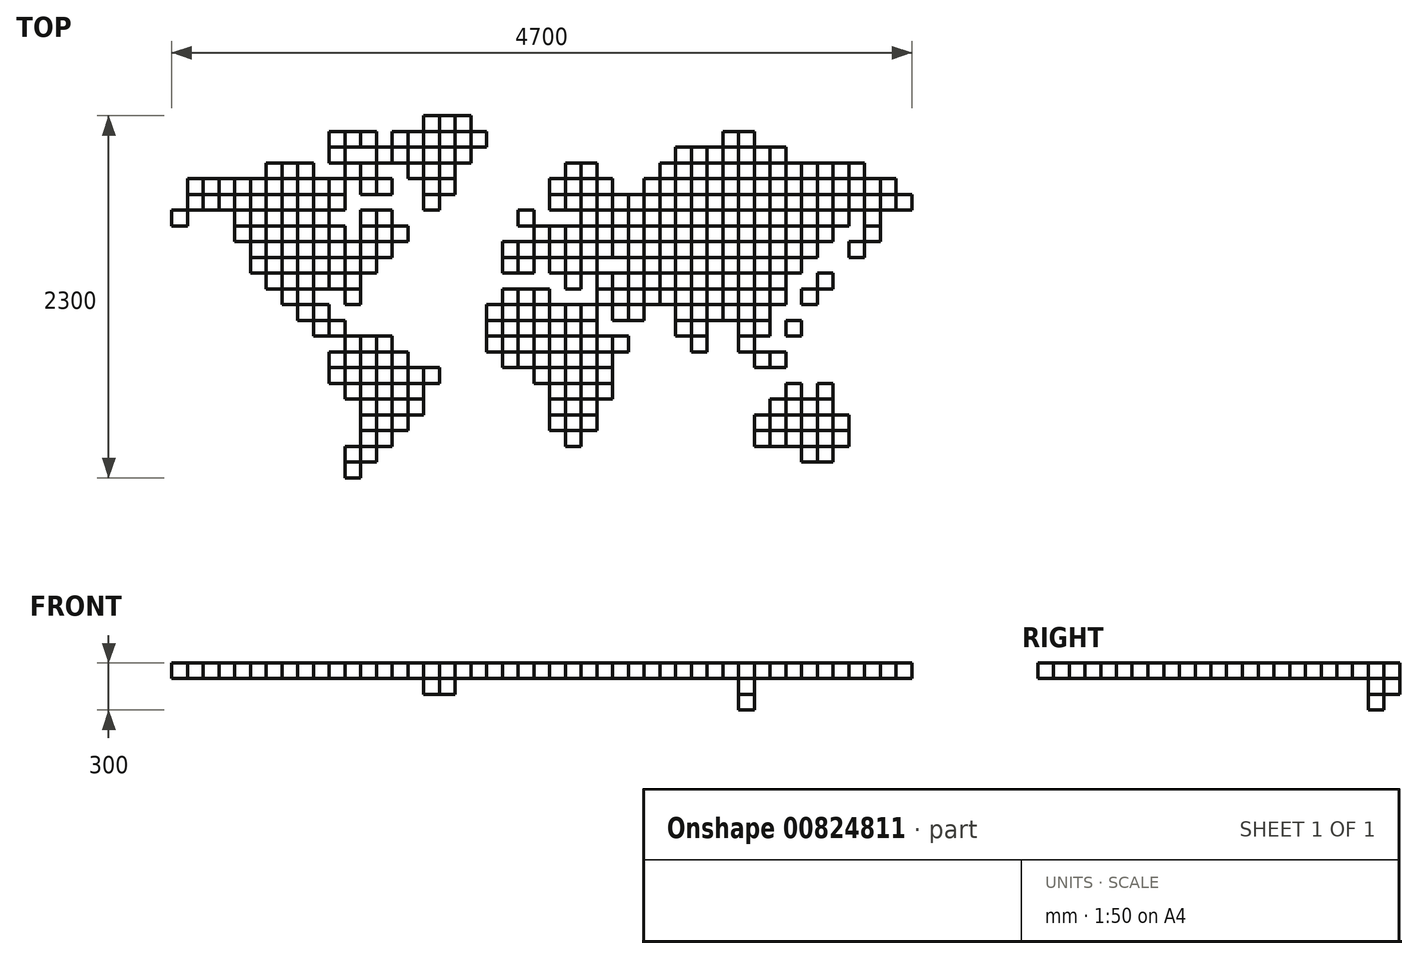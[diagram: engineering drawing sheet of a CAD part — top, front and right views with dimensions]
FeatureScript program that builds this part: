
annotation { "Feature Type Name" : "Feature", "Feature Type Description" : "" }
export const myFeature = defineFeature(function(context is Context, id is Id, definition is map)
    precondition{}
    {
        {
            var Q0;
            Q0=qCreatedBy(makeId("Top.planeOp"),FACE);
            var sketch = newSketch(context, id + "F0", { "sketchPlane" : qUnion([Q0])});
            skLineSegment(sketch, "E0.bottom", {"start": v(-5, 5) * mm, "end": v(5, 5) * mm});
            skLineSegment(sketch, "E0.top", {"start": v(-5, -5) * mm, "end": v(5, -5) * mm});
            skLineSegment(sketch, "E0.left", {"start": v(-5, 5) * mm, "end": v(-5, -5) * mm});
            skLineSegment(sketch, "E0.right", {"start": v(5, 5) * mm, "end": v(5, -5) * mm});
            skLineSegment(sketch, "E1", {"start": v(0, 0) * mm, "end": v(0, 5) * mm, "construction": true});
            skLineSegment(sketch, "E2", {"start": v(0, 0) * mm, "end": v(5, 0) * mm, "construction": true});
            skSolve(sketch);
        }
        {
            var Q0;
            Q0 = qSketchRegion(id + "F0", true);
            extrude(context, id + "F1", {"entities" : qUnion([Q0]), "depth" : 10 * mm, "offsetDistance" : 25 * mm});
        }
        {
            var Q0;
            Q0=makeQuery(id+"F1.opExtrude","SWEPT_BODY",BODY,{"disambiguationData":[OSD([sQuery(id+"F0.wireOp",EDGE,"E0.bottom"),sQuery(id+"F0.wireOp",EDGE,"E0.top"),sQuery(id+"F0.wireOp",EDGE,"E0.left"),sQuery(id+"F0.wireOp",EDGE,"E0.right")])]});
            var Q1;
            Q1=makeQuery(id+"F1.opExtrude","CAP_EDGE",EDGE,{"disambiguationData":[OSD([sQuery(id+"F0.wireOp",EDGE,"E0.bottom")])],"isStart":false});
            transform(context, id + "F2", {"entities" : qUnion([Q0]), "transformType" : TransformType.TRANSLATION_DISTANCE, "transformDirection" : qUnion([Q1]), "distance" : 10 * mm, "makeCopy" : true});
        }
        {
            var Q0;
            Q0=makeQuery(id+"F1.opExtrude","SWEPT_BODY",BODY,{"disambiguationData":[OSD([sQuery(id+"F0.wireOp",EDGE,"E0.bottom"),sQuery(id+"F0.wireOp",EDGE,"E0.top"),sQuery(id+"F0.wireOp",EDGE,"E0.left"),sQuery(id+"F0.wireOp",EDGE,"E0.right")])]});
            var Q1;
            Q1=makeQuery(id+"F2.opPattern","COPY",BODY,{"derivedFrom":makeQuery(id+"F1.opExtrude","SWEPT_BODY",BODY,{"disambiguationData":[OSD([sQuery(id+"F0.wireOp",EDGE,"E0.bottom"),sQuery(id+"F0.wireOp",EDGE,"E0.top"),sQuery(id+"F0.wireOp",EDGE,"E0.left"),sQuery(id+"F0.wireOp",EDGE,"E0.right")])]}),"instanceName":"1"});
            var Q2;
            Q2=makeQuery(id+"F2.opPattern","COPY",EDGE,{"derivedFrom":makeQuery(id+"F1.opExtrude","CAP_EDGE",EDGE,{"disambiguationData":[OSD([sQuery(id+"F0.wireOp",EDGE,"E0.right")])],"isStart":false}),"instanceName":"1"});
            transform(context, id + "F3", {"entities" : qUnion([Q0, Q1]), "transformType" : TransformType.TRANSLATION_DISTANCE, "transformDirection" : qUnion([Q2]), "distance" : 10 * mm, "makeCopy" : true});
        }
        {
            var Q0;
            Q0=makeQuery(id+"F1.opExtrude","SWEPT_BODY",BODY,{"disambiguationData":[OSD([sQuery(id+"F0.wireOp",EDGE,"E0.bottom"),sQuery(id+"F0.wireOp",EDGE,"E0.top"),sQuery(id+"F0.wireOp",EDGE,"E0.left"),sQuery(id+"F0.wireOp",EDGE,"E0.right")])]});
            var Q1;
            Q1=makeQuery(id+"F2.opPattern","COPY",BODY,{"derivedFrom":makeQuery(id+"F1.opExtrude","SWEPT_BODY",BODY,{"disambiguationData":[OSD([sQuery(id+"F0.wireOp",EDGE,"E0.bottom"),sQuery(id+"F0.wireOp",EDGE,"E0.top"),sQuery(id+"F0.wireOp",EDGE,"E0.left"),sQuery(id+"F0.wireOp",EDGE,"E0.right")])]}),"instanceName":"1"});
            var Q2;
            Q2=makeQuery(id+"F3.opPattern","COPY",EDGE,{"derivedFrom":makeQuery(id+"F2.opPattern","COPY",EDGE,{"derivedFrom":makeQuery(id+"F1.opExtrude","CAP_EDGE",EDGE,{"disambiguationData":[OSD([sQuery(id+"F0.wireOp",EDGE,"E0.bottom")])],"isStart":false}),"instanceName":"1"}),"instanceName":"1"});
            transform(context, id + "F4", {"entities" : qUnion([Q0, Q1]), "transformType" : TransformType.TRANSLATION_DISTANCE, "transformDirection" : qUnion([Q2]), "distance" : 20 * mm, "makeCopy" : true});
        }
        {
            var Q0;
            Q0=makeQuery(id+"F4.opPattern","COPY",BODY,{"derivedFrom":makeQuery(id+"F1.opExtrude","SWEPT_BODY",BODY,{"disambiguationData":[OSD([sQuery(id+"F0.wireOp",EDGE,"E0.bottom"),sQuery(id+"F0.wireOp",EDGE,"E0.top"),sQuery(id+"F0.wireOp",EDGE,"E0.left"),sQuery(id+"F0.wireOp",EDGE,"E0.right")])]}),"instanceName":"1"});
            var Q1;
            Q1=makeQuery(id+"F1.opExtrude","SWEPT_BODY",BODY,{"disambiguationData":[OSD([sQuery(id+"F0.wireOp",EDGE,"E0.bottom"),sQuery(id+"F0.wireOp",EDGE,"E0.top"),sQuery(id+"F0.wireOp",EDGE,"E0.left"),sQuery(id+"F0.wireOp",EDGE,"E0.right")])]});
            var Q2;
            Q2=makeQuery(id+"F2.opPattern","COPY",BODY,{"derivedFrom":makeQuery(id+"F1.opExtrude","SWEPT_BODY",BODY,{"disambiguationData":[OSD([sQuery(id+"F0.wireOp",EDGE,"E0.bottom"),sQuery(id+"F0.wireOp",EDGE,"E0.top"),sQuery(id+"F0.wireOp",EDGE,"E0.left"),sQuery(id+"F0.wireOp",EDGE,"E0.right")])]}),"instanceName":"1"});
            var Q3;
            Q3=makeQuery(id+"F4.opPattern","COPY",BODY,{"derivedFrom":makeQuery(id+"F2.opPattern","COPY",BODY,{"derivedFrom":makeQuery(id+"F1.opExtrude","SWEPT_BODY",BODY,{"disambiguationData":[OSD([sQuery(id+"F0.wireOp",EDGE,"E0.bottom"),sQuery(id+"F0.wireOp",EDGE,"E0.top"),sQuery(id+"F0.wireOp",EDGE,"E0.left"),sQuery(id+"F0.wireOp",EDGE,"E0.right")])]}),"instanceName":"1"}),"instanceName":"1"});
            var Q4;
            Q4=makeQuery(id+"F4.opPattern","COPY",EDGE,{"derivedFrom":makeQuery(id+"F2.opPattern","COPY",EDGE,{"derivedFrom":makeQuery(id+"F1.opExtrude","CAP_EDGE",EDGE,{"disambiguationData":[OSD([sQuery(id+"F0.wireOp",EDGE,"E0.top")])],"isStart":false}),"instanceName":"1"}),"instanceName":"1"});
            transform(context, id + "F5", {"entities" : qUnion([Q0, Q1, Q2, Q3]), "transformType" : TransformType.TRANSLATION_DISTANCE, "transformDirection" : qUnion([Q4]), "distance" : 40 * mm, "makeCopy" : true});
        }
        {
            var Q0;
            Q0=makeQuery(id+"F4.opPattern","COPY",BODY,{"derivedFrom":makeQuery(id+"F1.opExtrude","SWEPT_BODY",BODY,{"disambiguationData":[OSD([sQuery(id+"F0.wireOp",EDGE,"E0.bottom"),sQuery(id+"F0.wireOp",EDGE,"E0.top"),sQuery(id+"F0.wireOp",EDGE,"E0.left"),sQuery(id+"F0.wireOp",EDGE,"E0.right")])]}),"instanceName":"1"});
            var Q1;
            Q1=makeQuery(id+"F5.opPattern","COPY",BODY,{"derivedFrom":makeQuery(id+"F1.opExtrude","SWEPT_BODY",BODY,{"disambiguationData":[OSD([sQuery(id+"F0.wireOp",EDGE,"E0.bottom"),sQuery(id+"F0.wireOp",EDGE,"E0.top"),sQuery(id+"F0.wireOp",EDGE,"E0.left"),sQuery(id+"F0.wireOp",EDGE,"E0.right")])]}),"instanceName":"1"});
            var Q2;
            Q2=makeQuery(id+"F4.opPattern","COPY",BODY,{"derivedFrom":makeQuery(id+"F2.opPattern","COPY",BODY,{"derivedFrom":makeQuery(id+"F1.opExtrude","SWEPT_BODY",BODY,{"disambiguationData":[OSD([sQuery(id+"F0.wireOp",EDGE,"E0.bottom"),sQuery(id+"F0.wireOp",EDGE,"E0.top"),sQuery(id+"F0.wireOp",EDGE,"E0.left"),sQuery(id+"F0.wireOp",EDGE,"E0.right")])]}),"instanceName":"1"}),"instanceName":"1"});
            var Q3;
            Q3=makeQuery(id+"F5.opPattern","COPY",BODY,{"derivedFrom":makeQuery(id+"F2.opPattern","COPY",BODY,{"derivedFrom":makeQuery(id+"F1.opExtrude","SWEPT_BODY",BODY,{"disambiguationData":[OSD([sQuery(id+"F0.wireOp",EDGE,"E0.bottom"),sQuery(id+"F0.wireOp",EDGE,"E0.top"),sQuery(id+"F0.wireOp",EDGE,"E0.left"),sQuery(id+"F0.wireOp",EDGE,"E0.right")])]}),"instanceName":"1"}),"instanceName":"1"});
            var Q4;
            Q4=makeQuery(id+"F5.opPattern","COPY",BODY,{"derivedFrom":makeQuery(id+"F4.opPattern","COPY",BODY,{"derivedFrom":makeQuery(id+"F1.opExtrude","SWEPT_BODY",BODY,{"disambiguationData":[OSD([sQuery(id+"F0.wireOp",EDGE,"E0.bottom"),sQuery(id+"F0.wireOp",EDGE,"E0.top"),sQuery(id+"F0.wireOp",EDGE,"E0.left"),sQuery(id+"F0.wireOp",EDGE,"E0.right")])]}),"instanceName":"1"}),"instanceName":"1"});
            var Q5;
            Q5=makeQuery(id+"F5.opPattern","COPY",BODY,{"derivedFrom":makeQuery(id+"F4.opPattern","COPY",BODY,{"derivedFrom":makeQuery(id+"F2.opPattern","COPY",BODY,{"derivedFrom":makeQuery(id+"F1.opExtrude","SWEPT_BODY",BODY,{"disambiguationData":[OSD([sQuery(id+"F0.wireOp",EDGE,"E0.bottom"),sQuery(id+"F0.wireOp",EDGE,"E0.top"),sQuery(id+"F0.wireOp",EDGE,"E0.left"),sQuery(id+"F0.wireOp",EDGE,"E0.right")])]}),"instanceName":"1"}),"instanceName":"1"}),"instanceName":"1"});
            var Q6;
            Q6=makeQuery(id+"F5.opPattern","COPY",EDGE,{"derivedFrom":makeQuery(id+"F4.opPattern","COPY",EDGE,{"derivedFrom":makeQuery(id+"F2.opPattern","COPY",EDGE,{"derivedFrom":makeQuery(id+"F1.opExtrude","CAP_EDGE",EDGE,{"disambiguationData":[OSD([sQuery(id+"F0.wireOp",EDGE,"E0.right")])],"isStart":false}),"instanceName":"1"}),"instanceName":"1"}),"instanceName":"1"});
            transform(context, id + "F6", {"entities" : qUnion([Q0, Q1, Q2, Q3, Q4, Q5]), "transformType" : TransformType.TRANSLATION_DISTANCE, "transformDirection" : qUnion([Q6]), "distance" : 10 * mm, "oppositeDirection" : true, "makeCopy" : true});
        }
        {
            var Q0;
            Q0=makeQuery(id+"F4.opPattern","COPY",BODY,{"derivedFrom":makeQuery(id+"F2.opPattern","COPY",BODY,{"derivedFrom":makeQuery(id+"F1.opExtrude","SWEPT_BODY",BODY,{"disambiguationData":[OSD([sQuery(id+"F0.wireOp",EDGE,"E0.bottom"),sQuery(id+"F0.wireOp",EDGE,"E0.top"),sQuery(id+"F0.wireOp",EDGE,"E0.left"),sQuery(id+"F0.wireOp",EDGE,"E0.right")])]}),"instanceName":"1"}),"instanceName":"1"});
            var Q1;
            Q1=makeQuery(id+"F5.opPattern","COPY",BODY,{"derivedFrom":makeQuery(id+"F2.opPattern","COPY",BODY,{"derivedFrom":makeQuery(id+"F1.opExtrude","SWEPT_BODY",BODY,{"disambiguationData":[OSD([sQuery(id+"F0.wireOp",EDGE,"E0.bottom"),sQuery(id+"F0.wireOp",EDGE,"E0.top"),sQuery(id+"F0.wireOp",EDGE,"E0.left"),sQuery(id+"F0.wireOp",EDGE,"E0.right")])]}),"instanceName":"1"}),"instanceName":"1"});
            var Q2;
            Q2=makeQuery(id+"F5.opPattern","COPY",EDGE,{"derivedFrom":makeQuery(id+"F4.opPattern","COPY",EDGE,{"derivedFrom":makeQuery(id+"F2.opPattern","COPY",EDGE,{"derivedFrom":makeQuery(id+"F1.opExtrude","CAP_EDGE",EDGE,{"disambiguationData":[OSD([sQuery(id+"F0.wireOp",EDGE,"E0.right")])],"isStart":false}),"instanceName":"1"}),"instanceName":"1"}),"instanceName":"1"});
            transform(context, id + "F7", {"entities" : qUnion([Q0, Q1]), "transformType" : TransformType.TRANSLATION_DISTANCE, "transformDirection" : qUnion([Q2]), "distance" : 10 * mm, "makeCopy" : true});
        }
        {
            var Q0;
            Q0=makeQuery(id+"F5.opPattern","COPY",BODY,{"derivedFrom":makeQuery(id+"F1.opExtrude","SWEPT_BODY",BODY,{"disambiguationData":[OSD([sQuery(id+"F0.wireOp",EDGE,"E0.bottom"),sQuery(id+"F0.wireOp",EDGE,"E0.top"),sQuery(id+"F0.wireOp",EDGE,"E0.left"),sQuery(id+"F0.wireOp",EDGE,"E0.right")])]}),"instanceName":"1"});
            var Q1;
            Q1=makeQuery(id+"F5.opPattern","COPY",BODY,{"derivedFrom":makeQuery(id+"F4.opPattern","COPY",BODY,{"derivedFrom":makeQuery(id+"F1.opExtrude","SWEPT_BODY",BODY,{"disambiguationData":[OSD([sQuery(id+"F0.wireOp",EDGE,"E0.bottom"),sQuery(id+"F0.wireOp",EDGE,"E0.top"),sQuery(id+"F0.wireOp",EDGE,"E0.left"),sQuery(id+"F0.wireOp",EDGE,"E0.right")])]}),"instanceName":"1"}),"instanceName":"1"});
            var Q2;
            Q2=makeQuery(id+"F5.opPattern","COPY",BODY,{"derivedFrom":makeQuery(id+"F4.opPattern","COPY",BODY,{"derivedFrom":makeQuery(id+"F2.opPattern","COPY",BODY,{"derivedFrom":makeQuery(id+"F1.opExtrude","SWEPT_BODY",BODY,{"disambiguationData":[OSD([sQuery(id+"F0.wireOp",EDGE,"E0.bottom"),sQuery(id+"F0.wireOp",EDGE,"E0.top"),sQuery(id+"F0.wireOp",EDGE,"E0.left"),sQuery(id+"F0.wireOp",EDGE,"E0.right")])]}),"instanceName":"1"}),"instanceName":"1"}),"instanceName":"1"});
            var Q3;
            Q3=makeQuery(id+"F5.opPattern","COPY",EDGE,{"derivedFrom":makeQuery(id+"F4.opPattern","COPY",EDGE,{"derivedFrom":makeQuery(id+"F2.opPattern","COPY",EDGE,{"derivedFrom":makeQuery(id+"F1.opExtrude","CAP_EDGE",EDGE,{"disambiguationData":[OSD([sQuery(id+"F0.wireOp",EDGE,"E0.right")])],"isStart":false}),"instanceName":"1"}),"instanceName":"1"}),"instanceName":"1"});
            transform(context, id + "F8", {"entities" : qUnion([Q0, Q1, Q2]), "transformType" : TransformType.TRANSLATION_DISTANCE, "transformDirection" : qUnion([Q3]), "distance" : 20 * mm, "makeCopy" : true});
        }
        {
            var Q0;
            Q0=makeQuery(id+"F6.opPattern","COPY",BODY,{"derivedFrom":makeQuery(id+"F4.opPattern","COPY",BODY,{"derivedFrom":makeQuery(id+"F1.opExtrude","SWEPT_BODY",BODY,{"disambiguationData":[OSD([sQuery(id+"F0.wireOp",EDGE,"E0.bottom"),sQuery(id+"F0.wireOp",EDGE,"E0.top"),sQuery(id+"F0.wireOp",EDGE,"E0.left"),sQuery(id+"F0.wireOp",EDGE,"E0.right")])]}),"instanceName":"1"}),"instanceName":"1"});
            var Q1;
            Q1=makeQuery(id+"F6.opPattern","COPY",EDGE,{"derivedFrom":makeQuery(id+"F4.opPattern","COPY",EDGE,{"derivedFrom":makeQuery(id+"F1.opExtrude","CAP_EDGE",EDGE,{"disambiguationData":[OSD([sQuery(id+"F0.wireOp",EDGE,"E0.left")])],"isStart":false}),"instanceName":"1"}),"instanceName":"1"});
            transform(context, id + "F9", {"entities" : qUnion([Q0]), "transformType" : TransformType.TRANSLATION_DISTANCE, "transformDirection" : qUnion([Q1]), "distance" : 10 * mm, "oppositeDirection" : true, "makeCopy" : true});
        }
        {
            var Q0;
            Q0=makeQuery(id+"F9.opPattern","COPY",BODY,{"derivedFrom":makeQuery(id+"F6.opPattern","COPY",BODY,{"derivedFrom":makeQuery(id+"F4.opPattern","COPY",BODY,{"derivedFrom":makeQuery(id+"F1.opExtrude","SWEPT_BODY",BODY,{"disambiguationData":[OSD([sQuery(id+"F0.wireOp",EDGE,"E0.bottom"),sQuery(id+"F0.wireOp",EDGE,"E0.top"),sQuery(id+"F0.wireOp",EDGE,"E0.left"),sQuery(id+"F0.wireOp",EDGE,"E0.right")])]}),"instanceName":"1"}),"instanceName":"1"}),"instanceName":"1"});
            var Q1;
            Q1=makeQuery(id+"F9.opPattern","COPY",EDGE,{"derivedFrom":makeQuery(id+"F6.opPattern","COPY",EDGE,{"derivedFrom":makeQuery(id+"F4.opPattern","COPY",EDGE,{"derivedFrom":makeQuery(id+"F1.opExtrude","CAP_EDGE",EDGE,{"disambiguationData":[OSD([sQuery(id+"F0.wireOp",EDGE,"E0.bottom")])],"isStart":false}),"instanceName":"1"}),"instanceName":"1"}),"instanceName":"1"});
            transform(context, id + "F10", {"entities" : qUnion([Q0]), "transformType" : TransformType.TRANSLATION_DISTANCE, "transformDirection" : qUnion([Q1]), "distance" : 10 * mm, "oppositeDirection" : true, "makeCopy" : false});
        }
        {
            var Q0;
            Q0=makeQuery(id+"F4.opPattern","COPY",BODY,{"derivedFrom":makeQuery(id+"F2.opPattern","COPY",BODY,{"derivedFrom":makeQuery(id+"F1.opExtrude","SWEPT_BODY",BODY,{"disambiguationData":[OSD([sQuery(id+"F0.wireOp",EDGE,"E0.bottom"),sQuery(id+"F0.wireOp",EDGE,"E0.top"),sQuery(id+"F0.wireOp",EDGE,"E0.left"),sQuery(id+"F0.wireOp",EDGE,"E0.right")])]}),"instanceName":"1"}),"instanceName":"1"});
            var Q1;
            Q1=makeQuery(id+"F5.opPattern","COPY",BODY,{"derivedFrom":makeQuery(id+"F1.opExtrude","SWEPT_BODY",BODY,{"disambiguationData":[OSD([sQuery(id+"F0.wireOp",EDGE,"E0.bottom"),sQuery(id+"F0.wireOp",EDGE,"E0.top"),sQuery(id+"F0.wireOp",EDGE,"E0.left"),sQuery(id+"F0.wireOp",EDGE,"E0.right")])]}),"instanceName":"1"});
            var Q2;
            Q2=makeQuery(id+"F6.opPattern","COPY",BODY,{"derivedFrom":makeQuery(id+"F4.opPattern","COPY",BODY,{"derivedFrom":makeQuery(id+"F2.opPattern","COPY",BODY,{"derivedFrom":makeQuery(id+"F1.opExtrude","SWEPT_BODY",BODY,{"disambiguationData":[OSD([sQuery(id+"F0.wireOp",EDGE,"E0.bottom"),sQuery(id+"F0.wireOp",EDGE,"E0.top"),sQuery(id+"F0.wireOp",EDGE,"E0.left"),sQuery(id+"F0.wireOp",EDGE,"E0.right")])]}),"instanceName":"1"}),"instanceName":"1"}),"instanceName":"1"});
            var Q3;
            Q3=makeQuery(id+"F6.opPattern","COPY",BODY,{"derivedFrom":makeQuery(id+"F5.opPattern","COPY",BODY,{"derivedFrom":makeQuery(id+"F1.opExtrude","SWEPT_BODY",BODY,{"disambiguationData":[OSD([sQuery(id+"F0.wireOp",EDGE,"E0.bottom"),sQuery(id+"F0.wireOp",EDGE,"E0.top"),sQuery(id+"F0.wireOp",EDGE,"E0.left"),sQuery(id+"F0.wireOp",EDGE,"E0.right")])]}),"instanceName":"1"}),"instanceName":"1"});
            var Q4;
            Q4=makeQuery(id+"F6.opPattern","COPY",EDGE,{"derivedFrom":makeQuery(id+"F4.opPattern","COPY",EDGE,{"derivedFrom":makeQuery(id+"F2.opPattern","COPY",EDGE,{"derivedFrom":makeQuery(id+"F1.opExtrude","CAP_EDGE",EDGE,{"disambiguationData":[OSD([sQuery(id+"F0.wireOp",EDGE,"E0.left")])],"isStart":false}),"instanceName":"1"}),"instanceName":"1"}),"instanceName":"1"});
            transform(context, id + "F11", {"entities" : qUnion([Q0, Q1, Q2, Q3]), "transformType" : TransformType.TRANSLATION_DISTANCE, "transformDirection" : qUnion([Q4]), "distance" : 30 * mm, "oppositeDirection" : true, "makeCopy" : true});
        }
        {
            var Q0;
            Q0=makeQuery(id+"F6.opPattern","COPY",BODY,{"derivedFrom":makeQuery(id+"F5.opPattern","COPY",BODY,{"derivedFrom":makeQuery(id+"F2.opPattern","COPY",BODY,{"derivedFrom":makeQuery(id+"F1.opExtrude","SWEPT_BODY",BODY,{"disambiguationData":[OSD([sQuery(id+"F0.wireOp",EDGE,"E0.bottom"),sQuery(id+"F0.wireOp",EDGE,"E0.top"),sQuery(id+"F0.wireOp",EDGE,"E0.left"),sQuery(id+"F0.wireOp",EDGE,"E0.right")])]}),"instanceName":"1"}),"instanceName":"1"}),"instanceName":"1"});
            var Q1;
            Q1=makeQuery(id+"F6.opPattern","COPY",BODY,{"derivedFrom":makeQuery(id+"F5.opPattern","COPY",BODY,{"derivedFrom":makeQuery(id+"F4.opPattern","COPY",BODY,{"derivedFrom":makeQuery(id+"F2.opPattern","COPY",BODY,{"derivedFrom":makeQuery(id+"F1.opExtrude","SWEPT_BODY",BODY,{"disambiguationData":[OSD([sQuery(id+"F0.wireOp",EDGE,"E0.bottom"),sQuery(id+"F0.wireOp",EDGE,"E0.top"),sQuery(id+"F0.wireOp",EDGE,"E0.left"),sQuery(id+"F0.wireOp",EDGE,"E0.right")])]}),"instanceName":"1"}),"instanceName":"1"}),"instanceName":"1"}),"instanceName":"1"});
            var Q2;
            Q2=makeQuery(id+"F6.opPattern","COPY",BODY,{"derivedFrom":makeQuery(id+"F5.opPattern","COPY",BODY,{"derivedFrom":makeQuery(id+"F4.opPattern","COPY",BODY,{"derivedFrom":makeQuery(id+"F1.opExtrude","SWEPT_BODY",BODY,{"disambiguationData":[OSD([sQuery(id+"F0.wireOp",EDGE,"E0.bottom"),sQuery(id+"F0.wireOp",EDGE,"E0.top"),sQuery(id+"F0.wireOp",EDGE,"E0.left"),sQuery(id+"F0.wireOp",EDGE,"E0.right")])]}),"instanceName":"1"}),"instanceName":"1"}),"instanceName":"1"});
            var Q3;
            Q3=makeQuery(id+"F6.opPattern","COPY",EDGE,{"derivedFrom":makeQuery(id+"F5.opPattern","COPY",EDGE,{"derivedFrom":makeQuery(id+"F4.opPattern","COPY",EDGE,{"derivedFrom":makeQuery(id+"F2.opPattern","COPY",EDGE,{"derivedFrom":makeQuery(id+"F1.opExtrude","CAP_EDGE",EDGE,{"disambiguationData":[OSD([sQuery(id+"F0.wireOp",EDGE,"E0.right")])],"isStart":false}),"instanceName":"1"}),"instanceName":"1"}),"instanceName":"1"}),"instanceName":"1"});
            transform(context, id + "F12", {"entities" : qUnion([Q0, Q1, Q2]), "transformType" : TransformType.TRANSLATION_DISTANCE, "transformDirection" : qUnion([Q3]), "distance" : 10 * mm, "oppositeDirection" : true, "makeCopy" : true});
        }
        {
            var Q0;
            Q0=makeQuery(id+"F6.opPattern","COPY",BODY,{"derivedFrom":makeQuery(id+"F5.opPattern","COPY",BODY,{"derivedFrom":makeQuery(id+"F2.opPattern","COPY",BODY,{"derivedFrom":makeQuery(id+"F1.opExtrude","SWEPT_BODY",BODY,{"disambiguationData":[OSD([sQuery(id+"F0.wireOp",EDGE,"E0.bottom"),sQuery(id+"F0.wireOp",EDGE,"E0.top"),sQuery(id+"F0.wireOp",EDGE,"E0.left"),sQuery(id+"F0.wireOp",EDGE,"E0.right")])]}),"instanceName":"1"}),"instanceName":"1"}),"instanceName":"1"});
            var Q1;
            Q1=makeQuery(id+"F5.opPattern","COPY",BODY,{"derivedFrom":makeQuery(id+"F4.opPattern","COPY",BODY,{"derivedFrom":makeQuery(id+"F1.opExtrude","SWEPT_BODY",BODY,{"disambiguationData":[OSD([sQuery(id+"F0.wireOp",EDGE,"E0.bottom"),sQuery(id+"F0.wireOp",EDGE,"E0.top"),sQuery(id+"F0.wireOp",EDGE,"E0.left"),sQuery(id+"F0.wireOp",EDGE,"E0.right")])]}),"instanceName":"1"}),"instanceName":"1"});
            var Q2;
            Q2=makeQuery(id+"F12.opPattern","COPY",BODY,{"derivedFrom":makeQuery(id+"F6.opPattern","COPY",BODY,{"derivedFrom":makeQuery(id+"F5.opPattern","COPY",BODY,{"derivedFrom":makeQuery(id+"F2.opPattern","COPY",BODY,{"derivedFrom":makeQuery(id+"F1.opExtrude","SWEPT_BODY",BODY,{"disambiguationData":[OSD([sQuery(id+"F0.wireOp",EDGE,"E0.bottom"),sQuery(id+"F0.wireOp",EDGE,"E0.top"),sQuery(id+"F0.wireOp",EDGE,"E0.left"),sQuery(id+"F0.wireOp",EDGE,"E0.right")])]}),"instanceName":"1"}),"instanceName":"1"}),"instanceName":"1"}),"instanceName":"1"});
            var Q3;
            Q3=makeQuery(id+"F6.opPattern","COPY",BODY,{"derivedFrom":makeQuery(id+"F5.opPattern","COPY",BODY,{"derivedFrom":makeQuery(id+"F4.opPattern","COPY",BODY,{"derivedFrom":makeQuery(id+"F1.opExtrude","SWEPT_BODY",BODY,{"disambiguationData":[OSD([sQuery(id+"F0.wireOp",EDGE,"E0.bottom"),sQuery(id+"F0.wireOp",EDGE,"E0.top"),sQuery(id+"F0.wireOp",EDGE,"E0.left"),sQuery(id+"F0.wireOp",EDGE,"E0.right")])]}),"instanceName":"1"}),"instanceName":"1"}),"instanceName":"1"});
            var Q4;
            Q4=makeQuery(id+"F12.opPattern","COPY",EDGE,{"derivedFrom":makeQuery(id+"F6.opPattern","COPY",EDGE,{"derivedFrom":makeQuery(id+"F5.opPattern","COPY",EDGE,{"derivedFrom":makeQuery(id+"F4.opPattern","COPY",EDGE,{"derivedFrom":makeQuery(id+"F2.opPattern","COPY",EDGE,{"derivedFrom":makeQuery(id+"F1.opExtrude","CAP_EDGE",EDGE,{"disambiguationData":[OSD([sQuery(id+"F0.wireOp",EDGE,"E0.right")])],"isStart":false}),"instanceName":"1"}),"instanceName":"1"}),"instanceName":"1"}),"instanceName":"1"}),"instanceName":"1"});
            transform(context, id + "F13", {"entities" : qUnion([Q0, Q1, Q2, Q3]), "transformType" : TransformType.TRANSLATION_DISTANCE, "transformDirection" : qUnion([Q4]), "distance" : 30 * mm, "oppositeDirection" : true, "makeCopy" : true});
        }
        {
            var Q0;
            Q0=makeQuery(id+"F13.opPattern","COPY",BODY,{"derivedFrom":makeQuery(id+"F12.opPattern","COPY",BODY,{"derivedFrom":makeQuery(id+"F6.opPattern","COPY",BODY,{"derivedFrom":makeQuery(id+"F5.opPattern","COPY",BODY,{"derivedFrom":makeQuery(id+"F2.opPattern","COPY",BODY,{"derivedFrom":makeQuery(id+"F1.opExtrude","SWEPT_BODY",BODY,{"disambiguationData":[OSD([sQuery(id+"F0.wireOp",EDGE,"E0.bottom"),sQuery(id+"F0.wireOp",EDGE,"E0.top"),sQuery(id+"F0.wireOp",EDGE,"E0.left"),sQuery(id+"F0.wireOp",EDGE,"E0.right")])]}),"instanceName":"1"}),"instanceName":"1"}),"instanceName":"1"}),"instanceName":"1"}),"instanceName":"1"});
            var Q1;
            Q1=makeQuery(id+"F13.opPattern","COPY",EDGE,{"derivedFrom":makeQuery(id+"F12.opPattern","COPY",EDGE,{"derivedFrom":makeQuery(id+"F6.opPattern","COPY",EDGE,{"derivedFrom":makeQuery(id+"F5.opPattern","COPY",EDGE,{"derivedFrom":makeQuery(id+"F2.opPattern","COPY",EDGE,{"derivedFrom":makeQuery(id+"F1.opExtrude","CAP_EDGE",EDGE,{"disambiguationData":[OSD([sQuery(id+"F0.wireOp",EDGE,"E0.bottom")])],"isStart":true}),"instanceName":"1"}),"instanceName":"1"}),"instanceName":"1"}),"instanceName":"1"}),"instanceName":"1"});
            transform(context, id + "F14", {"entities" : qUnion([Q0]), "transformType" : TransformType.TRANSLATION_DISTANCE, "transformDirection" : qUnion([Q1]), "distance" : 10 * mm, "oppositeDirection" : true, "makeCopy" : true});
        }
        {
            var Q0;
            Q0=makeQuery(id+"F12.opPattern","COPY",BODY,{"derivedFrom":makeQuery(id+"F6.opPattern","COPY",BODY,{"derivedFrom":makeQuery(id+"F5.opPattern","COPY",BODY,{"derivedFrom":makeQuery(id+"F4.opPattern","COPY",BODY,{"derivedFrom":makeQuery(id+"F2.opPattern","COPY",BODY,{"derivedFrom":makeQuery(id+"F1.opExtrude","SWEPT_BODY",BODY,{"disambiguationData":[OSD([sQuery(id+"F0.wireOp",EDGE,"E0.bottom"),sQuery(id+"F0.wireOp",EDGE,"E0.top"),sQuery(id+"F0.wireOp",EDGE,"E0.left"),sQuery(id+"F0.wireOp",EDGE,"E0.right")])]}),"instanceName":"1"}),"instanceName":"1"}),"instanceName":"1"}),"instanceName":"1"}),"instanceName":"1"});
            var Q1;
            Q1=makeQuery(id+"F12.opPattern","COPY",EDGE,{"derivedFrom":makeQuery(id+"F6.opPattern","COPY",EDGE,{"derivedFrom":makeQuery(id+"F5.opPattern","COPY",EDGE,{"derivedFrom":makeQuery(id+"F4.opPattern","COPY",EDGE,{"derivedFrom":makeQuery(id+"F2.opPattern","COPY",EDGE,{"derivedFrom":makeQuery(id+"F1.opExtrude","CAP_EDGE",EDGE,{"disambiguationData":[OSD([sQuery(id+"F0.wireOp",EDGE,"E0.right")])],"isStart":false}),"instanceName":"1"}),"instanceName":"1"}),"instanceName":"1"}),"instanceName":"1"}),"instanceName":"1"});
            transform(context, id + "F15", {"entities" : qUnion([Q0]), "transformType" : TransformType.TRANSLATION_DISTANCE, "transformDirection" : qUnion([Q1]), "distance" : 10 * mm, "oppositeDirection" : true, "makeCopy" : true});
        }
        {
            var Q0;
            Q0=makeQuery(id+"F8.opPattern","COPY",BODY,{"derivedFrom":makeQuery(id+"F5.opPattern","COPY",BODY,{"derivedFrom":makeQuery(id+"F4.opPattern","COPY",BODY,{"derivedFrom":makeQuery(id+"F2.opPattern","COPY",BODY,{"derivedFrom":makeQuery(id+"F1.opExtrude","SWEPT_BODY",BODY,{"disambiguationData":[OSD([sQuery(id+"F0.wireOp",EDGE,"E0.bottom"),sQuery(id+"F0.wireOp",EDGE,"E0.top"),sQuery(id+"F0.wireOp",EDGE,"E0.left"),sQuery(id+"F0.wireOp",EDGE,"E0.right")])]}),"instanceName":"1"}),"instanceName":"1"}),"instanceName":"1"}),"instanceName":"1"});
            var Q1;
            Q1=makeQuery(id+"F8.opPattern","COPY",BODY,{"derivedFrom":makeQuery(id+"F5.opPattern","COPY",BODY,{"derivedFrom":makeQuery(id+"F4.opPattern","COPY",BODY,{"derivedFrom":makeQuery(id+"F1.opExtrude","SWEPT_BODY",BODY,{"disambiguationData":[OSD([sQuery(id+"F0.wireOp",EDGE,"E0.bottom"),sQuery(id+"F0.wireOp",EDGE,"E0.top"),sQuery(id+"F0.wireOp",EDGE,"E0.left"),sQuery(id+"F0.wireOp",EDGE,"E0.right")])]}),"instanceName":"1"}),"instanceName":"1"}),"instanceName":"1"});
            var Q2;
            Q2=makeQuery(id+"F8.opPattern","COPY",EDGE,{"derivedFrom":makeQuery(id+"F5.opPattern","COPY",EDGE,{"derivedFrom":makeQuery(id+"F4.opPattern","COPY",EDGE,{"derivedFrom":makeQuery(id+"F2.opPattern","COPY",EDGE,{"derivedFrom":makeQuery(id+"F1.opExtrude","CAP_EDGE",EDGE,{"disambiguationData":[OSD([sQuery(id+"F0.wireOp",EDGE,"E0.right")])],"isStart":false}),"instanceName":"1"}),"instanceName":"1"}),"instanceName":"1"}),"instanceName":"1"});
            transform(context, id + "F16", {"entities" : qUnion([Q0, Q1]), "transformType" : TransformType.TRANSLATION_DISTANCE, "transformDirection" : qUnion([Q2]), "distance" : 10 * mm, "makeCopy" : true});
        }
        {
            var Q0;
            Q0=makeQuery(id+"F5.opPattern","COPY",BODY,{"derivedFrom":makeQuery(id+"F4.opPattern","COPY",BODY,{"derivedFrom":makeQuery(id+"F1.opExtrude","SWEPT_BODY",BODY,{"disambiguationData":[OSD([sQuery(id+"F0.wireOp",EDGE,"E0.bottom"),sQuery(id+"F0.wireOp",EDGE,"E0.top"),sQuery(id+"F0.wireOp",EDGE,"E0.left"),sQuery(id+"F0.wireOp",EDGE,"E0.right")])]}),"instanceName":"1"}),"instanceName":"1"});
            var Q1;
            Q1=makeQuery(id+"F13.opPattern","COPY",BODY,{"derivedFrom":makeQuery(id+"F5.opPattern","COPY",BODY,{"derivedFrom":makeQuery(id+"F4.opPattern","COPY",BODY,{"derivedFrom":makeQuery(id+"F1.opExtrude","SWEPT_BODY",BODY,{"disambiguationData":[OSD([sQuery(id+"F0.wireOp",EDGE,"E0.bottom"),sQuery(id+"F0.wireOp",EDGE,"E0.top"),sQuery(id+"F0.wireOp",EDGE,"E0.left"),sQuery(id+"F0.wireOp",EDGE,"E0.right")])]}),"instanceName":"1"}),"instanceName":"1"}),"instanceName":"1"});
            var Q2;
            Q2=makeQuery(id+"F6.opPattern","COPY",BODY,{"derivedFrom":makeQuery(id+"F5.opPattern","COPY",BODY,{"derivedFrom":makeQuery(id+"F4.opPattern","COPY",BODY,{"derivedFrom":makeQuery(id+"F2.opPattern","COPY",BODY,{"derivedFrom":makeQuery(id+"F1.opExtrude","SWEPT_BODY",BODY,{"disambiguationData":[OSD([sQuery(id+"F0.wireOp",EDGE,"E0.bottom"),sQuery(id+"F0.wireOp",EDGE,"E0.top"),sQuery(id+"F0.wireOp",EDGE,"E0.left"),sQuery(id+"F0.wireOp",EDGE,"E0.right")])]}),"instanceName":"1"}),"instanceName":"1"}),"instanceName":"1"}),"instanceName":"1"});
            var Q3;
            Q3=makeQuery(id+"F8.opPattern","COPY",BODY,{"derivedFrom":makeQuery(id+"F5.opPattern","COPY",BODY,{"derivedFrom":makeQuery(id+"F4.opPattern","COPY",BODY,{"derivedFrom":makeQuery(id+"F2.opPattern","COPY",BODY,{"derivedFrom":makeQuery(id+"F1.opExtrude","SWEPT_BODY",BODY,{"disambiguationData":[OSD([sQuery(id+"F0.wireOp",EDGE,"E0.bottom"),sQuery(id+"F0.wireOp",EDGE,"E0.top"),sQuery(id+"F0.wireOp",EDGE,"E0.left"),sQuery(id+"F0.wireOp",EDGE,"E0.right")])]}),"instanceName":"1"}),"instanceName":"1"}),"instanceName":"1"}),"instanceName":"1"});
            var Q4;
            Q4=makeQuery(id+"F12.opPattern","COPY",BODY,{"derivedFrom":makeQuery(id+"F6.opPattern","COPY",BODY,{"derivedFrom":makeQuery(id+"F5.opPattern","COPY",BODY,{"derivedFrom":makeQuery(id+"F4.opPattern","COPY",BODY,{"derivedFrom":makeQuery(id+"F2.opPattern","COPY",BODY,{"derivedFrom":makeQuery(id+"F1.opExtrude","SWEPT_BODY",BODY,{"disambiguationData":[OSD([sQuery(id+"F0.wireOp",EDGE,"E0.bottom"),sQuery(id+"F0.wireOp",EDGE,"E0.top"),sQuery(id+"F0.wireOp",EDGE,"E0.left"),sQuery(id+"F0.wireOp",EDGE,"E0.right")])]}),"instanceName":"1"}),"instanceName":"1"}),"instanceName":"1"}),"instanceName":"1"}),"instanceName":"1"});
            var Q5;
            Q5=makeQuery(id+"F6.opPattern","COPY",BODY,{"derivedFrom":makeQuery(id+"F5.opPattern","COPY",BODY,{"derivedFrom":makeQuery(id+"F4.opPattern","COPY",BODY,{"derivedFrom":makeQuery(id+"F1.opExtrude","SWEPT_BODY",BODY,{"disambiguationData":[OSD([sQuery(id+"F0.wireOp",EDGE,"E0.bottom"),sQuery(id+"F0.wireOp",EDGE,"E0.top"),sQuery(id+"F0.wireOp",EDGE,"E0.left"),sQuery(id+"F0.wireOp",EDGE,"E0.right")])]}),"instanceName":"1"}),"instanceName":"1"}),"instanceName":"1"});
            var Q6;
            Q6=makeQuery(id+"F12.opPattern","COPY",BODY,{"derivedFrom":makeQuery(id+"F6.opPattern","COPY",BODY,{"derivedFrom":makeQuery(id+"F5.opPattern","COPY",BODY,{"derivedFrom":makeQuery(id+"F4.opPattern","COPY",BODY,{"derivedFrom":makeQuery(id+"F1.opExtrude","SWEPT_BODY",BODY,{"disambiguationData":[OSD([sQuery(id+"F0.wireOp",EDGE,"E0.bottom"),sQuery(id+"F0.wireOp",EDGE,"E0.top"),sQuery(id+"F0.wireOp",EDGE,"E0.left"),sQuery(id+"F0.wireOp",EDGE,"E0.right")])]}),"instanceName":"1"}),"instanceName":"1"}),"instanceName":"1"}),"instanceName":"1"});
            var Q7;
            Q7=makeQuery(id+"F15.opPattern","COPY",BODY,{"derivedFrom":makeQuery(id+"F12.opPattern","COPY",BODY,{"derivedFrom":makeQuery(id+"F6.opPattern","COPY",BODY,{"derivedFrom":makeQuery(id+"F5.opPattern","COPY",BODY,{"derivedFrom":makeQuery(id+"F4.opPattern","COPY",BODY,{"derivedFrom":makeQuery(id+"F2.opPattern","COPY",BODY,{"derivedFrom":makeQuery(id+"F1.opExtrude","SWEPT_BODY",BODY,{"disambiguationData":[OSD([sQuery(id+"F0.wireOp",EDGE,"E0.bottom"),sQuery(id+"F0.wireOp",EDGE,"E0.top"),sQuery(id+"F0.wireOp",EDGE,"E0.left"),sQuery(id+"F0.wireOp",EDGE,"E0.right")])]}),"instanceName":"1"}),"instanceName":"1"}),"instanceName":"1"}),"instanceName":"1"}),"instanceName":"1"}),"instanceName":"1"});
            var Q8;
            Q8=makeQuery(id+"F5.opPattern","COPY",BODY,{"derivedFrom":makeQuery(id+"F4.opPattern","COPY",BODY,{"derivedFrom":makeQuery(id+"F2.opPattern","COPY",BODY,{"derivedFrom":makeQuery(id+"F1.opExtrude","SWEPT_BODY",BODY,{"disambiguationData":[OSD([sQuery(id+"F0.wireOp",EDGE,"E0.bottom"),sQuery(id+"F0.wireOp",EDGE,"E0.top"),sQuery(id+"F0.wireOp",EDGE,"E0.left"),sQuery(id+"F0.wireOp",EDGE,"E0.right")])]}),"instanceName":"1"}),"instanceName":"1"}),"instanceName":"1"});
            var Q9;
            Q9=makeQuery(id+"F8.opPattern","COPY",BODY,{"derivedFrom":makeQuery(id+"F5.opPattern","COPY",BODY,{"derivedFrom":makeQuery(id+"F4.opPattern","COPY",BODY,{"derivedFrom":makeQuery(id+"F1.opExtrude","SWEPT_BODY",BODY,{"disambiguationData":[OSD([sQuery(id+"F0.wireOp",EDGE,"E0.bottom"),sQuery(id+"F0.wireOp",EDGE,"E0.top"),sQuery(id+"F0.wireOp",EDGE,"E0.left"),sQuery(id+"F0.wireOp",EDGE,"E0.right")])]}),"instanceName":"1"}),"instanceName":"1"}),"instanceName":"1"});
            var Q10;
            Q10=makeQuery(id+"F16.opPattern","COPY",BODY,{"derivedFrom":makeQuery(id+"F8.opPattern","COPY",BODY,{"derivedFrom":makeQuery(id+"F5.opPattern","COPY",BODY,{"derivedFrom":makeQuery(id+"F4.opPattern","COPY",BODY,{"derivedFrom":makeQuery(id+"F2.opPattern","COPY",BODY,{"derivedFrom":makeQuery(id+"F1.opExtrude","SWEPT_BODY",BODY,{"disambiguationData":[OSD([sQuery(id+"F0.wireOp",EDGE,"E0.bottom"),sQuery(id+"F0.wireOp",EDGE,"E0.top"),sQuery(id+"F0.wireOp",EDGE,"E0.left"),sQuery(id+"F0.wireOp",EDGE,"E0.right")])]}),"instanceName":"1"}),"instanceName":"1"}),"instanceName":"1"}),"instanceName":"1"}),"instanceName":"1"});
            var Q11;
            Q11=makeQuery(id+"F15.opPattern","COPY",EDGE,{"derivedFrom":makeQuery(id+"F12.opPattern","COPY",EDGE,{"derivedFrom":makeQuery(id+"F6.opPattern","COPY",EDGE,{"derivedFrom":makeQuery(id+"F5.opPattern","COPY",EDGE,{"derivedFrom":makeQuery(id+"F4.opPattern","COPY",EDGE,{"derivedFrom":makeQuery(id+"F2.opPattern","COPY",EDGE,{"derivedFrom":makeQuery(id+"F1.opExtrude","CAP_EDGE",EDGE,{"disambiguationData":[OSD([sQuery(id+"F0.wireOp",EDGE,"E0.bottom")])],"isStart":false}),"instanceName":"1"}),"instanceName":"1"}),"instanceName":"1"}),"instanceName":"1"}),"instanceName":"1"}),"instanceName":"1"});
            transform(context, id + "F17", {"entities" : qUnion([Q0, Q1, Q2, Q3, Q4, Q5, Q6, Q7, Q8, Q9, Q10]), "transformType" : TransformType.TRANSLATION_DISTANCE, "transformDirection" : qUnion([Q11]), "distance" : 20 * mm, "makeCopy" : true});
        }
        {
            var Q0;
            Q0=makeQuery(id+"F17.opPattern","COPY",BODY,{"derivedFrom":makeQuery(id+"F15.opPattern","COPY",BODY,{"derivedFrom":makeQuery(id+"F12.opPattern","COPY",BODY,{"derivedFrom":makeQuery(id+"F6.opPattern","COPY",BODY,{"derivedFrom":makeQuery(id+"F5.opPattern","COPY",BODY,{"derivedFrom":makeQuery(id+"F4.opPattern","COPY",BODY,{"derivedFrom":makeQuery(id+"F2.opPattern","COPY",BODY,{"derivedFrom":makeQuery(id+"F1.opExtrude","SWEPT_BODY",BODY,{"disambiguationData":[OSD([sQuery(id+"F0.wireOp",EDGE,"E0.bottom"),sQuery(id+"F0.wireOp",EDGE,"E0.top"),sQuery(id+"F0.wireOp",EDGE,"E0.left"),sQuery(id+"F0.wireOp",EDGE,"E0.right")])]}),"instanceName":"1"}),"instanceName":"1"}),"instanceName":"1"}),"instanceName":"1"}),"instanceName":"1"}),"instanceName":"1"}),"instanceName":"1"});
            var Q1;
            Q1=makeQuery(id+"F17.opPattern","COPY",BODY,{"derivedFrom":makeQuery(id+"F8.opPattern","COPY",BODY,{"derivedFrom":makeQuery(id+"F5.opPattern","COPY",BODY,{"derivedFrom":makeQuery(id+"F4.opPattern","COPY",BODY,{"derivedFrom":makeQuery(id+"F1.opExtrude","SWEPT_BODY",BODY,{"disambiguationData":[OSD([sQuery(id+"F0.wireOp",EDGE,"E0.bottom"),sQuery(id+"F0.wireOp",EDGE,"E0.top"),sQuery(id+"F0.wireOp",EDGE,"E0.left"),sQuery(id+"F0.wireOp",EDGE,"E0.right")])]}),"instanceName":"1"}),"instanceName":"1"}),"instanceName":"1"}),"instanceName":"1"});
            var Q2;
            Q2=makeQuery(id+"F17.opPattern","COPY",BODY,{"derivedFrom":makeQuery(id+"F8.opPattern","COPY",BODY,{"derivedFrom":makeQuery(id+"F5.opPattern","COPY",BODY,{"derivedFrom":makeQuery(id+"F4.opPattern","COPY",BODY,{"derivedFrom":makeQuery(id+"F2.opPattern","COPY",BODY,{"derivedFrom":makeQuery(id+"F1.opExtrude","SWEPT_BODY",BODY,{"disambiguationData":[OSD([sQuery(id+"F0.wireOp",EDGE,"E0.bottom"),sQuery(id+"F0.wireOp",EDGE,"E0.top"),sQuery(id+"F0.wireOp",EDGE,"E0.left"),sQuery(id+"F0.wireOp",EDGE,"E0.right")])]}),"instanceName":"1"}),"instanceName":"1"}),"instanceName":"1"}),"instanceName":"1"}),"instanceName":"1"});
            var Q3;
            Q3=makeQuery(id+"F17.opPattern","COPY",EDGE,{"derivedFrom":makeQuery(id+"F15.opPattern","COPY",EDGE,{"derivedFrom":makeQuery(id+"F12.opPattern","COPY",EDGE,{"derivedFrom":makeQuery(id+"F6.opPattern","COPY",EDGE,{"derivedFrom":makeQuery(id+"F5.opPattern","COPY",EDGE,{"derivedFrom":makeQuery(id+"F4.opPattern","COPY",EDGE,{"derivedFrom":makeQuery(id+"F2.opPattern","COPY",EDGE,{"derivedFrom":makeQuery(id+"F1.opExtrude","CAP_EDGE",EDGE,{"disambiguationData":[OSD([sQuery(id+"F0.wireOp",EDGE,"E0.right")])],"isStart":false}),"instanceName":"1"}),"instanceName":"1"}),"instanceName":"1"}),"instanceName":"1"}),"instanceName":"1"}),"instanceName":"1"}),"instanceName":"1"});
            transform(context, id + "F18", {"entities" : qUnion([Q0, Q1, Q2]), "transformType" : TransformType.TRANSLATION_DISTANCE, "transformDirection" : qUnion([Q3]), "distance" : 10 * mm, "oppositeDirection" : true, "makeCopy" : true});
        }
        {
            var Q0;
            Q0=makeQuery(id+"F13.opPattern","COPY",BODY,{"derivedFrom":makeQuery(id+"F5.opPattern","COPY",BODY,{"derivedFrom":makeQuery(id+"F4.opPattern","COPY",BODY,{"derivedFrom":makeQuery(id+"F1.opExtrude","SWEPT_BODY",BODY,{"disambiguationData":[OSD([sQuery(id+"F0.wireOp",EDGE,"E0.bottom"),sQuery(id+"F0.wireOp",EDGE,"E0.top"),sQuery(id+"F0.wireOp",EDGE,"E0.left"),sQuery(id+"F0.wireOp",EDGE,"E0.right")])]}),"instanceName":"1"}),"instanceName":"1"}),"instanceName":"1"});
            var Q1;
            Q1=makeQuery(id+"F15.opPattern","COPY",BODY,{"derivedFrom":makeQuery(id+"F12.opPattern","COPY",BODY,{"derivedFrom":makeQuery(id+"F6.opPattern","COPY",BODY,{"derivedFrom":makeQuery(id+"F5.opPattern","COPY",BODY,{"derivedFrom":makeQuery(id+"F4.opPattern","COPY",BODY,{"derivedFrom":makeQuery(id+"F2.opPattern","COPY",BODY,{"derivedFrom":makeQuery(id+"F1.opExtrude","SWEPT_BODY",BODY,{"disambiguationData":[OSD([sQuery(id+"F0.wireOp",EDGE,"E0.bottom"),sQuery(id+"F0.wireOp",EDGE,"E0.top"),sQuery(id+"F0.wireOp",EDGE,"E0.left"),sQuery(id+"F0.wireOp",EDGE,"E0.right")])]}),"instanceName":"1"}),"instanceName":"1"}),"instanceName":"1"}),"instanceName":"1"}),"instanceName":"1"}),"instanceName":"1"});
            var Q2;
            Q2=makeQuery(id+"F17.opPattern","COPY",BODY,{"derivedFrom":makeQuery(id+"F13.opPattern","COPY",BODY,{"derivedFrom":makeQuery(id+"F5.opPattern","COPY",BODY,{"derivedFrom":makeQuery(id+"F4.opPattern","COPY",BODY,{"derivedFrom":makeQuery(id+"F1.opExtrude","SWEPT_BODY",BODY,{"disambiguationData":[OSD([sQuery(id+"F0.wireOp",EDGE,"E0.bottom"),sQuery(id+"F0.wireOp",EDGE,"E0.top"),sQuery(id+"F0.wireOp",EDGE,"E0.left"),sQuery(id+"F0.wireOp",EDGE,"E0.right")])]}),"instanceName":"1"}),"instanceName":"1"}),"instanceName":"1"}),"instanceName":"1"});
            var Q3;
            Q3=makeQuery(id+"F17.opPattern","COPY",BODY,{"derivedFrom":makeQuery(id+"F15.opPattern","COPY",BODY,{"derivedFrom":makeQuery(id+"F12.opPattern","COPY",BODY,{"derivedFrom":makeQuery(id+"F6.opPattern","COPY",BODY,{"derivedFrom":makeQuery(id+"F5.opPattern","COPY",BODY,{"derivedFrom":makeQuery(id+"F4.opPattern","COPY",BODY,{"derivedFrom":makeQuery(id+"F2.opPattern","COPY",BODY,{"derivedFrom":makeQuery(id+"F1.opExtrude","SWEPT_BODY",BODY,{"disambiguationData":[OSD([sQuery(id+"F0.wireOp",EDGE,"E0.bottom"),sQuery(id+"F0.wireOp",EDGE,"E0.top"),sQuery(id+"F0.wireOp",EDGE,"E0.left"),sQuery(id+"F0.wireOp",EDGE,"E0.right")])]}),"instanceName":"1"}),"instanceName":"1"}),"instanceName":"1"}),"instanceName":"1"}),"instanceName":"1"}),"instanceName":"1"}),"instanceName":"1"});
            var Q4;
            Q4=makeQuery(id+"F17.opPattern","COPY",BODY,{"derivedFrom":makeQuery(id+"F12.opPattern","COPY",BODY,{"derivedFrom":makeQuery(id+"F6.opPattern","COPY",BODY,{"derivedFrom":makeQuery(id+"F5.opPattern","COPY",BODY,{"derivedFrom":makeQuery(id+"F4.opPattern","COPY",BODY,{"derivedFrom":makeQuery(id+"F2.opPattern","COPY",BODY,{"derivedFrom":makeQuery(id+"F1.opExtrude","SWEPT_BODY",BODY,{"disambiguationData":[OSD([sQuery(id+"F0.wireOp",EDGE,"E0.bottom"),sQuery(id+"F0.wireOp",EDGE,"E0.top"),sQuery(id+"F0.wireOp",EDGE,"E0.left"),sQuery(id+"F0.wireOp",EDGE,"E0.right")])]}),"instanceName":"1"}),"instanceName":"1"}),"instanceName":"1"}),"instanceName":"1"}),"instanceName":"1"}),"instanceName":"1"});
            var Q5;
            Q5=makeQuery(id+"F6.opPattern","COPY",BODY,{"derivedFrom":makeQuery(id+"F5.opPattern","COPY",BODY,{"derivedFrom":makeQuery(id+"F4.opPattern","COPY",BODY,{"derivedFrom":makeQuery(id+"F2.opPattern","COPY",BODY,{"derivedFrom":makeQuery(id+"F1.opExtrude","SWEPT_BODY",BODY,{"disambiguationData":[OSD([sQuery(id+"F0.wireOp",EDGE,"E0.bottom"),sQuery(id+"F0.wireOp",EDGE,"E0.top"),sQuery(id+"F0.wireOp",EDGE,"E0.left"),sQuery(id+"F0.wireOp",EDGE,"E0.right")])]}),"instanceName":"1"}),"instanceName":"1"}),"instanceName":"1"}),"instanceName":"1"});
            var Q6;
            Q6=makeQuery(id+"F17.opPattern","COPY",BODY,{"derivedFrom":makeQuery(id+"F12.opPattern","COPY",BODY,{"derivedFrom":makeQuery(id+"F6.opPattern","COPY",BODY,{"derivedFrom":makeQuery(id+"F5.opPattern","COPY",BODY,{"derivedFrom":makeQuery(id+"F4.opPattern","COPY",BODY,{"derivedFrom":makeQuery(id+"F1.opExtrude","SWEPT_BODY",BODY,{"disambiguationData":[OSD([sQuery(id+"F0.wireOp",EDGE,"E0.bottom"),sQuery(id+"F0.wireOp",EDGE,"E0.top"),sQuery(id+"F0.wireOp",EDGE,"E0.left"),sQuery(id+"F0.wireOp",EDGE,"E0.right")])]}),"instanceName":"1"}),"instanceName":"1"}),"instanceName":"1"}),"instanceName":"1"}),"instanceName":"1"});
            var Q7;
            Q7=makeQuery(id+"F12.opPattern","COPY",BODY,{"derivedFrom":makeQuery(id+"F6.opPattern","COPY",BODY,{"derivedFrom":makeQuery(id+"F5.opPattern","COPY",BODY,{"derivedFrom":makeQuery(id+"F4.opPattern","COPY",BODY,{"derivedFrom":makeQuery(id+"F1.opExtrude","SWEPT_BODY",BODY,{"disambiguationData":[OSD([sQuery(id+"F0.wireOp",EDGE,"E0.bottom"),sQuery(id+"F0.wireOp",EDGE,"E0.top"),sQuery(id+"F0.wireOp",EDGE,"E0.left"),sQuery(id+"F0.wireOp",EDGE,"E0.right")])]}),"instanceName":"1"}),"instanceName":"1"}),"instanceName":"1"}),"instanceName":"1"});
            var Q8;
            Q8=makeQuery(id+"F12.opPattern","COPY",BODY,{"derivedFrom":makeQuery(id+"F6.opPattern","COPY",BODY,{"derivedFrom":makeQuery(id+"F5.opPattern","COPY",BODY,{"derivedFrom":makeQuery(id+"F4.opPattern","COPY",BODY,{"derivedFrom":makeQuery(id+"F2.opPattern","COPY",BODY,{"derivedFrom":makeQuery(id+"F1.opExtrude","SWEPT_BODY",BODY,{"disambiguationData":[OSD([sQuery(id+"F0.wireOp",EDGE,"E0.bottom"),sQuery(id+"F0.wireOp",EDGE,"E0.top"),sQuery(id+"F0.wireOp",EDGE,"E0.left"),sQuery(id+"F0.wireOp",EDGE,"E0.right")])]}),"instanceName":"1"}),"instanceName":"1"}),"instanceName":"1"}),"instanceName":"1"}),"instanceName":"1"});
            var Q9;
            Q9=makeQuery(id+"F6.opPattern","COPY",BODY,{"derivedFrom":makeQuery(id+"F5.opPattern","COPY",BODY,{"derivedFrom":makeQuery(id+"F4.opPattern","COPY",BODY,{"derivedFrom":makeQuery(id+"F1.opExtrude","SWEPT_BODY",BODY,{"disambiguationData":[OSD([sQuery(id+"F0.wireOp",EDGE,"E0.bottom"),sQuery(id+"F0.wireOp",EDGE,"E0.top"),sQuery(id+"F0.wireOp",EDGE,"E0.left"),sQuery(id+"F0.wireOp",EDGE,"E0.right")])]}),"instanceName":"1"}),"instanceName":"1"}),"instanceName":"1"});
            var Q10;
            Q10=makeQuery(id+"F17.opPattern","COPY",BODY,{"derivedFrom":makeQuery(id+"F6.opPattern","COPY",BODY,{"derivedFrom":makeQuery(id+"F5.opPattern","COPY",BODY,{"derivedFrom":makeQuery(id+"F4.opPattern","COPY",BODY,{"derivedFrom":makeQuery(id+"F2.opPattern","COPY",BODY,{"derivedFrom":makeQuery(id+"F1.opExtrude","SWEPT_BODY",BODY,{"disambiguationData":[OSD([sQuery(id+"F0.wireOp",EDGE,"E0.bottom"),sQuery(id+"F0.wireOp",EDGE,"E0.top"),sQuery(id+"F0.wireOp",EDGE,"E0.left"),sQuery(id+"F0.wireOp",EDGE,"E0.right")])]}),"instanceName":"1"}),"instanceName":"1"}),"instanceName":"1"}),"instanceName":"1"}),"instanceName":"1"});
            var Q11;
            Q11=makeQuery(id+"F17.opPattern","COPY",BODY,{"derivedFrom":makeQuery(id+"F6.opPattern","COPY",BODY,{"derivedFrom":makeQuery(id+"F5.opPattern","COPY",BODY,{"derivedFrom":makeQuery(id+"F4.opPattern","COPY",BODY,{"derivedFrom":makeQuery(id+"F1.opExtrude","SWEPT_BODY",BODY,{"disambiguationData":[OSD([sQuery(id+"F0.wireOp",EDGE,"E0.bottom"),sQuery(id+"F0.wireOp",EDGE,"E0.top"),sQuery(id+"F0.wireOp",EDGE,"E0.left"),sQuery(id+"F0.wireOp",EDGE,"E0.right")])]}),"instanceName":"1"}),"instanceName":"1"}),"instanceName":"1"}),"instanceName":"1"});
            var Q12;
            Q12=makeQuery(id+"F17.opPattern","COPY",BODY,{"derivedFrom":makeQuery(id+"F5.opPattern","COPY",BODY,{"derivedFrom":makeQuery(id+"F4.opPattern","COPY",BODY,{"derivedFrom":makeQuery(id+"F2.opPattern","COPY",BODY,{"derivedFrom":makeQuery(id+"F1.opExtrude","SWEPT_BODY",BODY,{"disambiguationData":[OSD([sQuery(id+"F0.wireOp",EDGE,"E0.bottom"),sQuery(id+"F0.wireOp",EDGE,"E0.top"),sQuery(id+"F0.wireOp",EDGE,"E0.left"),sQuery(id+"F0.wireOp",EDGE,"E0.right")])]}),"instanceName":"1"}),"instanceName":"1"}),"instanceName":"1"}),"instanceName":"1"});
            var Q13;
            Q13=makeQuery(id+"F5.opPattern","COPY",BODY,{"derivedFrom":makeQuery(id+"F4.opPattern","COPY",BODY,{"derivedFrom":makeQuery(id+"F1.opExtrude","SWEPT_BODY",BODY,{"disambiguationData":[OSD([sQuery(id+"F0.wireOp",EDGE,"E0.bottom"),sQuery(id+"F0.wireOp",EDGE,"E0.top"),sQuery(id+"F0.wireOp",EDGE,"E0.left"),sQuery(id+"F0.wireOp",EDGE,"E0.right")])]}),"instanceName":"1"}),"instanceName":"1"});
            var Q14;
            Q14=makeQuery(id+"F5.opPattern","COPY",BODY,{"derivedFrom":makeQuery(id+"F4.opPattern","COPY",BODY,{"derivedFrom":makeQuery(id+"F2.opPattern","COPY",BODY,{"derivedFrom":makeQuery(id+"F1.opExtrude","SWEPT_BODY",BODY,{"disambiguationData":[OSD([sQuery(id+"F0.wireOp",EDGE,"E0.bottom"),sQuery(id+"F0.wireOp",EDGE,"E0.top"),sQuery(id+"F0.wireOp",EDGE,"E0.left"),sQuery(id+"F0.wireOp",EDGE,"E0.right")])]}),"instanceName":"1"}),"instanceName":"1"}),"instanceName":"1"});
            var Q15;
            Q15=makeQuery(id+"F17.opPattern","COPY",BODY,{"derivedFrom":makeQuery(id+"F5.opPattern","COPY",BODY,{"derivedFrom":makeQuery(id+"F4.opPattern","COPY",BODY,{"derivedFrom":makeQuery(id+"F1.opExtrude","SWEPT_BODY",BODY,{"disambiguationData":[OSD([sQuery(id+"F0.wireOp",EDGE,"E0.bottom"),sQuery(id+"F0.wireOp",EDGE,"E0.top"),sQuery(id+"F0.wireOp",EDGE,"E0.left"),sQuery(id+"F0.wireOp",EDGE,"E0.right")])]}),"instanceName":"1"}),"instanceName":"1"}),"instanceName":"1"});
            var Q16;
            Q16=makeQuery(id+"F18.opPattern","COPY",EDGE,{"derivedFrom":makeQuery(id+"F17.opPattern","COPY",EDGE,{"derivedFrom":makeQuery(id+"F15.opPattern","COPY",EDGE,{"derivedFrom":makeQuery(id+"F12.opPattern","COPY",EDGE,{"derivedFrom":makeQuery(id+"F6.opPattern","COPY",EDGE,{"derivedFrom":makeQuery(id+"F5.opPattern","COPY",EDGE,{"derivedFrom":makeQuery(id+"F4.opPattern","COPY",EDGE,{"derivedFrom":makeQuery(id+"F2.opPattern","COPY",EDGE,{"derivedFrom":makeQuery(id+"F1.opExtrude","CAP_EDGE",EDGE,{"disambiguationData":[OSD([sQuery(id+"F0.wireOp",EDGE,"E0.bottom")])],"isStart":false}),"instanceName":"1"}),"instanceName":"1"}),"instanceName":"1"}),"instanceName":"1"}),"instanceName":"1"}),"instanceName":"1"}),"instanceName":"1"}),"instanceName":"1"});
            transform(context, id + "F19", {"entities" : qUnion([Q0, Q1, Q2, Q3, Q4, Q5, Q6, Q7, Q8, Q9, Q10, Q11, Q12, Q13, Q14, Q15]), "transformType" : TransformType.TRANSLATION_DISTANCE, "transformDirection" : qUnion([Q16]), "distance" : 40 * mm, "makeCopy" : true});
        }
        {
            var Q0;
            Q0=makeQuery(id+"F8.opPattern","COPY",BODY,{"derivedFrom":makeQuery(id+"F5.opPattern","COPY",BODY,{"derivedFrom":makeQuery(id+"F4.opPattern","COPY",BODY,{"derivedFrom":makeQuery(id+"F2.opPattern","COPY",BODY,{"derivedFrom":makeQuery(id+"F1.opExtrude","SWEPT_BODY",BODY,{"disambiguationData":[OSD([sQuery(id+"F0.wireOp",EDGE,"E0.bottom"),sQuery(id+"F0.wireOp",EDGE,"E0.top"),sQuery(id+"F0.wireOp",EDGE,"E0.left"),sQuery(id+"F0.wireOp",EDGE,"E0.right")])]}),"instanceName":"1"}),"instanceName":"1"}),"instanceName":"1"}),"instanceName":"1"});
            var Q1;
            Q1=makeQuery(id+"F17.opPattern","COPY",BODY,{"derivedFrom":makeQuery(id+"F8.opPattern","COPY",BODY,{"derivedFrom":makeQuery(id+"F5.opPattern","COPY",BODY,{"derivedFrom":makeQuery(id+"F4.opPattern","COPY",BODY,{"derivedFrom":makeQuery(id+"F1.opExtrude","SWEPT_BODY",BODY,{"disambiguationData":[OSD([sQuery(id+"F0.wireOp",EDGE,"E0.bottom"),sQuery(id+"F0.wireOp",EDGE,"E0.top"),sQuery(id+"F0.wireOp",EDGE,"E0.left"),sQuery(id+"F0.wireOp",EDGE,"E0.right")])]}),"instanceName":"1"}),"instanceName":"1"}),"instanceName":"1"}),"instanceName":"1"});
            var Q2;
            Q2=makeQuery(id+"F17.opPattern","COPY",EDGE,{"derivedFrom":makeQuery(id+"F16.opPattern","COPY",EDGE,{"derivedFrom":makeQuery(id+"F8.opPattern","COPY",EDGE,{"derivedFrom":makeQuery(id+"F5.opPattern","COPY",EDGE,{"derivedFrom":makeQuery(id+"F4.opPattern","COPY",EDGE,{"derivedFrom":makeQuery(id+"F2.opPattern","COPY",EDGE,{"derivedFrom":makeQuery(id+"F1.opExtrude","CAP_EDGE",EDGE,{"disambiguationData":[OSD([sQuery(id+"F0.wireOp",EDGE,"E0.right")])],"isStart":false}),"instanceName":"1"}),"instanceName":"1"}),"instanceName":"1"}),"instanceName":"1"}),"instanceName":"1"}),"instanceName":"1"});
            transform(context, id + "F20", {"entities" : qUnion([Q0, Q1]), "transformType" : TransformType.TRANSLATION_DISTANCE, "transformDirection" : qUnion([Q2]), "distance" : 20 * mm, "makeCopy" : true});
        }
        {
            var Q0;
            Q0=makeQuery(id+"F19.opPattern","COPY",BODY,{"derivedFrom":makeQuery(id+"F12.opPattern","COPY",BODY,{"derivedFrom":makeQuery(id+"F6.opPattern","COPY",BODY,{"derivedFrom":makeQuery(id+"F5.opPattern","COPY",BODY,{"derivedFrom":makeQuery(id+"F4.opPattern","COPY",BODY,{"derivedFrom":makeQuery(id+"F2.opPattern","COPY",BODY,{"derivedFrom":makeQuery(id+"F1.opExtrude","SWEPT_BODY",BODY,{"disambiguationData":[OSD([sQuery(id+"F0.wireOp",EDGE,"E0.bottom"),sQuery(id+"F0.wireOp",EDGE,"E0.top"),sQuery(id+"F0.wireOp",EDGE,"E0.left"),sQuery(id+"F0.wireOp",EDGE,"E0.right")])]}),"instanceName":"1"}),"instanceName":"1"}),"instanceName":"1"}),"instanceName":"1"}),"instanceName":"1"}),"instanceName":"1"});
            var Q1;
            Q1=makeQuery(id+"F19.opPattern","COPY",BODY,{"derivedFrom":makeQuery(id+"F12.opPattern","COPY",BODY,{"derivedFrom":makeQuery(id+"F6.opPattern","COPY",BODY,{"derivedFrom":makeQuery(id+"F5.opPattern","COPY",BODY,{"derivedFrom":makeQuery(id+"F4.opPattern","COPY",BODY,{"derivedFrom":makeQuery(id+"F1.opExtrude","SWEPT_BODY",BODY,{"disambiguationData":[OSD([sQuery(id+"F0.wireOp",EDGE,"E0.bottom"),sQuery(id+"F0.wireOp",EDGE,"E0.top"),sQuery(id+"F0.wireOp",EDGE,"E0.left"),sQuery(id+"F0.wireOp",EDGE,"E0.right")])]}),"instanceName":"1"}),"instanceName":"1"}),"instanceName":"1"}),"instanceName":"1"}),"instanceName":"1"});
            var Q2;
            Q2=makeQuery(id+"F19.opPattern","COPY",BODY,{"derivedFrom":makeQuery(id+"F17.opPattern","COPY",BODY,{"derivedFrom":makeQuery(id+"F5.opPattern","COPY",BODY,{"derivedFrom":makeQuery(id+"F4.opPattern","COPY",BODY,{"derivedFrom":makeQuery(id+"F2.opPattern","COPY",BODY,{"derivedFrom":makeQuery(id+"F1.opExtrude","SWEPT_BODY",BODY,{"disambiguationData":[OSD([sQuery(id+"F0.wireOp",EDGE,"E0.bottom"),sQuery(id+"F0.wireOp",EDGE,"E0.top"),sQuery(id+"F0.wireOp",EDGE,"E0.left"),sQuery(id+"F0.wireOp",EDGE,"E0.right")])]}),"instanceName":"1"}),"instanceName":"1"}),"instanceName":"1"}),"instanceName":"1"}),"instanceName":"1"});
            var Q3;
            Q3=makeQuery(id+"F19.opPattern","COPY",BODY,{"derivedFrom":makeQuery(id+"F17.opPattern","COPY",BODY,{"derivedFrom":makeQuery(id+"F12.opPattern","COPY",BODY,{"derivedFrom":makeQuery(id+"F6.opPattern","COPY",BODY,{"derivedFrom":makeQuery(id+"F5.opPattern","COPY",BODY,{"derivedFrom":makeQuery(id+"F4.opPattern","COPY",BODY,{"derivedFrom":makeQuery(id+"F1.opExtrude","SWEPT_BODY",BODY,{"disambiguationData":[OSD([sQuery(id+"F0.wireOp",EDGE,"E0.bottom"),sQuery(id+"F0.wireOp",EDGE,"E0.top"),sQuery(id+"F0.wireOp",EDGE,"E0.left"),sQuery(id+"F0.wireOp",EDGE,"E0.right")])]}),"instanceName":"1"}),"instanceName":"1"}),"instanceName":"1"}),"instanceName":"1"}),"instanceName":"1"}),"instanceName":"1"});
            var Q4;
            Q4=makeQuery(id+"F19.opPattern","COPY",BODY,{"derivedFrom":makeQuery(id+"F5.opPattern","COPY",BODY,{"derivedFrom":makeQuery(id+"F4.opPattern","COPY",BODY,{"derivedFrom":makeQuery(id+"F1.opExtrude","SWEPT_BODY",BODY,{"disambiguationData":[OSD([sQuery(id+"F0.wireOp",EDGE,"E0.bottom"),sQuery(id+"F0.wireOp",EDGE,"E0.top"),sQuery(id+"F0.wireOp",EDGE,"E0.left"),sQuery(id+"F0.wireOp",EDGE,"E0.right")])]}),"instanceName":"1"}),"instanceName":"1"}),"instanceName":"1"});
            var Q5;
            Q5=makeQuery(id+"F19.opPattern","COPY",BODY,{"derivedFrom":makeQuery(id+"F17.opPattern","COPY",BODY,{"derivedFrom":makeQuery(id+"F6.opPattern","COPY",BODY,{"derivedFrom":makeQuery(id+"F5.opPattern","COPY",BODY,{"derivedFrom":makeQuery(id+"F4.opPattern","COPY",BODY,{"derivedFrom":makeQuery(id+"F2.opPattern","COPY",BODY,{"derivedFrom":makeQuery(id+"F1.opExtrude","SWEPT_BODY",BODY,{"disambiguationData":[OSD([sQuery(id+"F0.wireOp",EDGE,"E0.bottom"),sQuery(id+"F0.wireOp",EDGE,"E0.top"),sQuery(id+"F0.wireOp",EDGE,"E0.left"),sQuery(id+"F0.wireOp",EDGE,"E0.right")])]}),"instanceName":"1"}),"instanceName":"1"}),"instanceName":"1"}),"instanceName":"1"}),"instanceName":"1"}),"instanceName":"1"});
            var Q6;
            Q6=makeQuery(id+"F19.opPattern","COPY",BODY,{"derivedFrom":makeQuery(id+"F17.opPattern","COPY",BODY,{"derivedFrom":makeQuery(id+"F12.opPattern","COPY",BODY,{"derivedFrom":makeQuery(id+"F6.opPattern","COPY",BODY,{"derivedFrom":makeQuery(id+"F5.opPattern","COPY",BODY,{"derivedFrom":makeQuery(id+"F4.opPattern","COPY",BODY,{"derivedFrom":makeQuery(id+"F2.opPattern","COPY",BODY,{"derivedFrom":makeQuery(id+"F1.opExtrude","SWEPT_BODY",BODY,{"disambiguationData":[OSD([sQuery(id+"F0.wireOp",EDGE,"E0.bottom"),sQuery(id+"F0.wireOp",EDGE,"E0.top"),sQuery(id+"F0.wireOp",EDGE,"E0.left"),sQuery(id+"F0.wireOp",EDGE,"E0.right")])]}),"instanceName":"1"}),"instanceName":"1"}),"instanceName":"1"}),"instanceName":"1"}),"instanceName":"1"}),"instanceName":"1"}),"instanceName":"1"});
            var Q7;
            Q7=makeQuery(id+"F19.opPattern","COPY",BODY,{"derivedFrom":makeQuery(id+"F6.opPattern","COPY",BODY,{"derivedFrom":makeQuery(id+"F5.opPattern","COPY",BODY,{"derivedFrom":makeQuery(id+"F4.opPattern","COPY",BODY,{"derivedFrom":makeQuery(id+"F2.opPattern","COPY",BODY,{"derivedFrom":makeQuery(id+"F1.opExtrude","SWEPT_BODY",BODY,{"disambiguationData":[OSD([sQuery(id+"F0.wireOp",EDGE,"E0.bottom"),sQuery(id+"F0.wireOp",EDGE,"E0.top"),sQuery(id+"F0.wireOp",EDGE,"E0.left"),sQuery(id+"F0.wireOp",EDGE,"E0.right")])]}),"instanceName":"1"}),"instanceName":"1"}),"instanceName":"1"}),"instanceName":"1"}),"instanceName":"1"});
            var Q8;
            Q8=makeQuery(id+"F19.opPattern","COPY",BODY,{"derivedFrom":makeQuery(id+"F17.opPattern","COPY",BODY,{"derivedFrom":makeQuery(id+"F5.opPattern","COPY",BODY,{"derivedFrom":makeQuery(id+"F4.opPattern","COPY",BODY,{"derivedFrom":makeQuery(id+"F1.opExtrude","SWEPT_BODY",BODY,{"disambiguationData":[OSD([sQuery(id+"F0.wireOp",EDGE,"E0.bottom"),sQuery(id+"F0.wireOp",EDGE,"E0.top"),sQuery(id+"F0.wireOp",EDGE,"E0.left"),sQuery(id+"F0.wireOp",EDGE,"E0.right")])]}),"instanceName":"1"}),"instanceName":"1"}),"instanceName":"1"}),"instanceName":"1"});
            var Q9;
            Q9=makeQuery(id+"F19.opPattern","COPY",BODY,{"derivedFrom":makeQuery(id+"F5.opPattern","COPY",BODY,{"derivedFrom":makeQuery(id+"F4.opPattern","COPY",BODY,{"derivedFrom":makeQuery(id+"F2.opPattern","COPY",BODY,{"derivedFrom":makeQuery(id+"F1.opExtrude","SWEPT_BODY",BODY,{"disambiguationData":[OSD([sQuery(id+"F0.wireOp",EDGE,"E0.bottom"),sQuery(id+"F0.wireOp",EDGE,"E0.top"),sQuery(id+"F0.wireOp",EDGE,"E0.left"),sQuery(id+"F0.wireOp",EDGE,"E0.right")])]}),"instanceName":"1"}),"instanceName":"1"}),"instanceName":"1"}),"instanceName":"1"});
            var Q10;
            Q10=makeQuery(id+"F19.opPattern","COPY",BODY,{"derivedFrom":makeQuery(id+"F17.opPattern","COPY",BODY,{"derivedFrom":makeQuery(id+"F6.opPattern","COPY",BODY,{"derivedFrom":makeQuery(id+"F5.opPattern","COPY",BODY,{"derivedFrom":makeQuery(id+"F4.opPattern","COPY",BODY,{"derivedFrom":makeQuery(id+"F1.opExtrude","SWEPT_BODY",BODY,{"disambiguationData":[OSD([sQuery(id+"F0.wireOp",EDGE,"E0.bottom"),sQuery(id+"F0.wireOp",EDGE,"E0.top"),sQuery(id+"F0.wireOp",EDGE,"E0.left"),sQuery(id+"F0.wireOp",EDGE,"E0.right")])]}),"instanceName":"1"}),"instanceName":"1"}),"instanceName":"1"}),"instanceName":"1"}),"instanceName":"1"});
            var Q11;
            Q11=makeQuery(id+"F19.opPattern","COPY",BODY,{"derivedFrom":makeQuery(id+"F6.opPattern","COPY",BODY,{"derivedFrom":makeQuery(id+"F5.opPattern","COPY",BODY,{"derivedFrom":makeQuery(id+"F4.opPattern","COPY",BODY,{"derivedFrom":makeQuery(id+"F1.opExtrude","SWEPT_BODY",BODY,{"disambiguationData":[OSD([sQuery(id+"F0.wireOp",EDGE,"E0.bottom"),sQuery(id+"F0.wireOp",EDGE,"E0.top"),sQuery(id+"F0.wireOp",EDGE,"E0.left"),sQuery(id+"F0.wireOp",EDGE,"E0.right")])]}),"instanceName":"1"}),"instanceName":"1"}),"instanceName":"1"}),"instanceName":"1"});
            var Q12;
            Q12=makeQuery(id+"F19.opPattern","COPY",EDGE,{"derivedFrom":makeQuery(id+"F17.opPattern","COPY",EDGE,{"derivedFrom":makeQuery(id+"F5.opPattern","COPY",EDGE,{"derivedFrom":makeQuery(id+"F4.opPattern","COPY",EDGE,{"derivedFrom":makeQuery(id+"F2.opPattern","COPY",EDGE,{"derivedFrom":makeQuery(id+"F1.opExtrude","CAP_EDGE",EDGE,{"disambiguationData":[OSD([sQuery(id+"F0.wireOp",EDGE,"E0.right")])],"isStart":false}),"instanceName":"1"}),"instanceName":"1"}),"instanceName":"1"}),"instanceName":"1"}),"instanceName":"1"});
            transform(context, id + "F21", {"entities" : qUnion([Q0, Q1, Q2, Q3, Q4, Q5, Q6, Q7, Q8, Q9, Q10, Q11]), "transformType" : TransformType.TRANSLATION_DISTANCE, "transformDirection" : qUnion([Q12]), "distance" : 30 * mm, "makeCopy" : true});
        }
        {
            var Q0;
            Q0=makeQuery(id+"F21.opPattern","COPY",BODY,{"derivedFrom":makeQuery(id+"F19.opPattern","COPY",BODY,{"derivedFrom":makeQuery(id+"F12.opPattern","COPY",BODY,{"derivedFrom":makeQuery(id+"F6.opPattern","COPY",BODY,{"derivedFrom":makeQuery(id+"F5.opPattern","COPY",BODY,{"derivedFrom":makeQuery(id+"F4.opPattern","COPY",BODY,{"derivedFrom":makeQuery(id+"F2.opPattern","COPY",BODY,{"derivedFrom":makeQuery(id+"F1.opExtrude","SWEPT_BODY",BODY,{"disambiguationData":[OSD([sQuery(id+"F0.wireOp",EDGE,"E0.bottom"),sQuery(id+"F0.wireOp",EDGE,"E0.top"),sQuery(id+"F0.wireOp",EDGE,"E0.left"),sQuery(id+"F0.wireOp",EDGE,"E0.right")])]}),"instanceName":"1"}),"instanceName":"1"}),"instanceName":"1"}),"instanceName":"1"}),"instanceName":"1"}),"instanceName":"1"}),"instanceName":"1"});
            var Q1;
            Q1=makeQuery(id+"F21.opPattern","COPY",BODY,{"derivedFrom":makeQuery(id+"F19.opPattern","COPY",BODY,{"derivedFrom":makeQuery(id+"F6.opPattern","COPY",BODY,{"derivedFrom":makeQuery(id+"F5.opPattern","COPY",BODY,{"derivedFrom":makeQuery(id+"F4.opPattern","COPY",BODY,{"derivedFrom":makeQuery(id+"F2.opPattern","COPY",BODY,{"derivedFrom":makeQuery(id+"F1.opExtrude","SWEPT_BODY",BODY,{"disambiguationData":[OSD([sQuery(id+"F0.wireOp",EDGE,"E0.bottom"),sQuery(id+"F0.wireOp",EDGE,"E0.top"),sQuery(id+"F0.wireOp",EDGE,"E0.left"),sQuery(id+"F0.wireOp",EDGE,"E0.right")])]}),"instanceName":"1"}),"instanceName":"1"}),"instanceName":"1"}),"instanceName":"1"}),"instanceName":"1"}),"instanceName":"1"});
            var Q2;
            Q2=makeQuery(id+"F21.opPattern","COPY",BODY,{"derivedFrom":makeQuery(id+"F19.opPattern","COPY",BODY,{"derivedFrom":makeQuery(id+"F17.opPattern","COPY",BODY,{"derivedFrom":makeQuery(id+"F12.opPattern","COPY",BODY,{"derivedFrom":makeQuery(id+"F6.opPattern","COPY",BODY,{"derivedFrom":makeQuery(id+"F5.opPattern","COPY",BODY,{"derivedFrom":makeQuery(id+"F4.opPattern","COPY",BODY,{"derivedFrom":makeQuery(id+"F1.opExtrude","SWEPT_BODY",BODY,{"disambiguationData":[OSD([sQuery(id+"F0.wireOp",EDGE,"E0.bottom"),sQuery(id+"F0.wireOp",EDGE,"E0.top"),sQuery(id+"F0.wireOp",EDGE,"E0.left"),sQuery(id+"F0.wireOp",EDGE,"E0.right")])]}),"instanceName":"1"}),"instanceName":"1"}),"instanceName":"1"}),"instanceName":"1"}),"instanceName":"1"}),"instanceName":"1"}),"instanceName":"1"});
            var Q3;
            Q3=makeQuery(id+"F21.opPattern","COPY",BODY,{"derivedFrom":makeQuery(id+"F19.opPattern","COPY",BODY,{"derivedFrom":makeQuery(id+"F17.opPattern","COPY",BODY,{"derivedFrom":makeQuery(id+"F6.opPattern","COPY",BODY,{"derivedFrom":makeQuery(id+"F5.opPattern","COPY",BODY,{"derivedFrom":makeQuery(id+"F4.opPattern","COPY",BODY,{"derivedFrom":makeQuery(id+"F1.opExtrude","SWEPT_BODY",BODY,{"disambiguationData":[OSD([sQuery(id+"F0.wireOp",EDGE,"E0.bottom"),sQuery(id+"F0.wireOp",EDGE,"E0.top"),sQuery(id+"F0.wireOp",EDGE,"E0.left"),sQuery(id+"F0.wireOp",EDGE,"E0.right")])]}),"instanceName":"1"}),"instanceName":"1"}),"instanceName":"1"}),"instanceName":"1"}),"instanceName":"1"}),"instanceName":"1"});
            var Q4;
            Q4=makeQuery(id+"F21.opPattern","COPY",BODY,{"derivedFrom":makeQuery(id+"F19.opPattern","COPY",BODY,{"derivedFrom":makeQuery(id+"F17.opPattern","COPY",BODY,{"derivedFrom":makeQuery(id+"F5.opPattern","COPY",BODY,{"derivedFrom":makeQuery(id+"F4.opPattern","COPY",BODY,{"derivedFrom":makeQuery(id+"F1.opExtrude","SWEPT_BODY",BODY,{"disambiguationData":[OSD([sQuery(id+"F0.wireOp",EDGE,"E0.bottom"),sQuery(id+"F0.wireOp",EDGE,"E0.top"),sQuery(id+"F0.wireOp",EDGE,"E0.left"),sQuery(id+"F0.wireOp",EDGE,"E0.right")])]}),"instanceName":"1"}),"instanceName":"1"}),"instanceName":"1"}),"instanceName":"1"}),"instanceName":"1"});
            var Q5;
            Q5=makeQuery(id+"F21.opPattern","COPY",EDGE,{"derivedFrom":makeQuery(id+"F19.opPattern","COPY",EDGE,{"derivedFrom":makeQuery(id+"F17.opPattern","COPY",EDGE,{"derivedFrom":makeQuery(id+"F5.opPattern","COPY",EDGE,{"derivedFrom":makeQuery(id+"F4.opPattern","COPY",EDGE,{"derivedFrom":makeQuery(id+"F2.opPattern","COPY",EDGE,{"derivedFrom":makeQuery(id+"F1.opExtrude","CAP_EDGE",EDGE,{"disambiguationData":[OSD([sQuery(id+"F0.wireOp",EDGE,"E0.right")])],"isStart":false}),"instanceName":"1"}),"instanceName":"1"}),"instanceName":"1"}),"instanceName":"1"}),"instanceName":"1"}),"instanceName":"1"});
            transform(context, id + "F22", {"entities" : qUnion([Q0, Q1, Q2, Q3, Q4]), "transformType" : TransformType.TRANSLATION_DISTANCE, "transformDirection" : qUnion([Q5]), "distance" : 30 * mm, "makeCopy" : true});
        }
        {
            var Q0;
            Q0=makeQuery(id+"F19.opPattern","COPY",BODY,{"derivedFrom":makeQuery(id+"F17.opPattern","COPY",BODY,{"derivedFrom":makeQuery(id+"F15.opPattern","COPY",BODY,{"derivedFrom":makeQuery(id+"F12.opPattern","COPY",BODY,{"derivedFrom":makeQuery(id+"F6.opPattern","COPY",BODY,{"derivedFrom":makeQuery(id+"F5.opPattern","COPY",BODY,{"derivedFrom":makeQuery(id+"F4.opPattern","COPY",BODY,{"derivedFrom":makeQuery(id+"F2.opPattern","COPY",BODY,{"derivedFrom":makeQuery(id+"F1.opExtrude","SWEPT_BODY",BODY,{"disambiguationData":[OSD([sQuery(id+"F0.wireOp",EDGE,"E0.bottom"),sQuery(id+"F0.wireOp",EDGE,"E0.top"),sQuery(id+"F0.wireOp",EDGE,"E0.left"),sQuery(id+"F0.wireOp",EDGE,"E0.right")])]}),"instanceName":"1"}),"instanceName":"1"}),"instanceName":"1"}),"instanceName":"1"}),"instanceName":"1"}),"instanceName":"1"}),"instanceName":"1"}),"instanceName":"1"});
            var Q1;
            Q1=makeQuery(id+"F19.opPattern","COPY",BODY,{"derivedFrom":makeQuery(id+"F17.opPattern","COPY",BODY,{"derivedFrom":makeQuery(id+"F13.opPattern","COPY",BODY,{"derivedFrom":makeQuery(id+"F5.opPattern","COPY",BODY,{"derivedFrom":makeQuery(id+"F4.opPattern","COPY",BODY,{"derivedFrom":makeQuery(id+"F1.opExtrude","SWEPT_BODY",BODY,{"disambiguationData":[OSD([sQuery(id+"F0.wireOp",EDGE,"E0.bottom"),sQuery(id+"F0.wireOp",EDGE,"E0.top"),sQuery(id+"F0.wireOp",EDGE,"E0.left"),sQuery(id+"F0.wireOp",EDGE,"E0.right")])]}),"instanceName":"1"}),"instanceName":"1"}),"instanceName":"1"}),"instanceName":"1"}),"instanceName":"1"});
            var Q2;
            Q2=makeQuery(id+"F19.opPattern","COPY",BODY,{"derivedFrom":makeQuery(id+"F15.opPattern","COPY",BODY,{"derivedFrom":makeQuery(id+"F12.opPattern","COPY",BODY,{"derivedFrom":makeQuery(id+"F6.opPattern","COPY",BODY,{"derivedFrom":makeQuery(id+"F5.opPattern","COPY",BODY,{"derivedFrom":makeQuery(id+"F4.opPattern","COPY",BODY,{"derivedFrom":makeQuery(id+"F2.opPattern","COPY",BODY,{"derivedFrom":makeQuery(id+"F1.opExtrude","SWEPT_BODY",BODY,{"disambiguationData":[OSD([sQuery(id+"F0.wireOp",EDGE,"E0.bottom"),sQuery(id+"F0.wireOp",EDGE,"E0.top"),sQuery(id+"F0.wireOp",EDGE,"E0.left"),sQuery(id+"F0.wireOp",EDGE,"E0.right")])]}),"instanceName":"1"}),"instanceName":"1"}),"instanceName":"1"}),"instanceName":"1"}),"instanceName":"1"}),"instanceName":"1"}),"instanceName":"1"});
            var Q3;
            Q3=makeQuery(id+"F19.opPattern","COPY",BODY,{"derivedFrom":makeQuery(id+"F12.opPattern","COPY",BODY,{"derivedFrom":makeQuery(id+"F6.opPattern","COPY",BODY,{"derivedFrom":makeQuery(id+"F5.opPattern","COPY",BODY,{"derivedFrom":makeQuery(id+"F4.opPattern","COPY",BODY,{"derivedFrom":makeQuery(id+"F2.opPattern","COPY",BODY,{"derivedFrom":makeQuery(id+"F1.opExtrude","SWEPT_BODY",BODY,{"disambiguationData":[OSD([sQuery(id+"F0.wireOp",EDGE,"E0.bottom"),sQuery(id+"F0.wireOp",EDGE,"E0.top"),sQuery(id+"F0.wireOp",EDGE,"E0.left"),sQuery(id+"F0.wireOp",EDGE,"E0.right")])]}),"instanceName":"1"}),"instanceName":"1"}),"instanceName":"1"}),"instanceName":"1"}),"instanceName":"1"}),"instanceName":"1"});
            var Q4;
            Q4=makeQuery(id+"F19.opPattern","COPY",BODY,{"derivedFrom":makeQuery(id+"F17.opPattern","COPY",BODY,{"derivedFrom":makeQuery(id+"F12.opPattern","COPY",BODY,{"derivedFrom":makeQuery(id+"F6.opPattern","COPY",BODY,{"derivedFrom":makeQuery(id+"F5.opPattern","COPY",BODY,{"derivedFrom":makeQuery(id+"F4.opPattern","COPY",BODY,{"derivedFrom":makeQuery(id+"F1.opExtrude","SWEPT_BODY",BODY,{"disambiguationData":[OSD([sQuery(id+"F0.wireOp",EDGE,"E0.bottom"),sQuery(id+"F0.wireOp",EDGE,"E0.top"),sQuery(id+"F0.wireOp",EDGE,"E0.left"),sQuery(id+"F0.wireOp",EDGE,"E0.right")])]}),"instanceName":"1"}),"instanceName":"1"}),"instanceName":"1"}),"instanceName":"1"}),"instanceName":"1"}),"instanceName":"1"});
            var Q5;
            Q5=makeQuery(id+"F19.opPattern","COPY",BODY,{"derivedFrom":makeQuery(id+"F17.opPattern","COPY",BODY,{"derivedFrom":makeQuery(id+"F12.opPattern","COPY",BODY,{"derivedFrom":makeQuery(id+"F6.opPattern","COPY",BODY,{"derivedFrom":makeQuery(id+"F5.opPattern","COPY",BODY,{"derivedFrom":makeQuery(id+"F4.opPattern","COPY",BODY,{"derivedFrom":makeQuery(id+"F2.opPattern","COPY",BODY,{"derivedFrom":makeQuery(id+"F1.opExtrude","SWEPT_BODY",BODY,{"disambiguationData":[OSD([sQuery(id+"F0.wireOp",EDGE,"E0.bottom"),sQuery(id+"F0.wireOp",EDGE,"E0.top"),sQuery(id+"F0.wireOp",EDGE,"E0.left"),sQuery(id+"F0.wireOp",EDGE,"E0.right")])]}),"instanceName":"1"}),"instanceName":"1"}),"instanceName":"1"}),"instanceName":"1"}),"instanceName":"1"}),"instanceName":"1"}),"instanceName":"1"});
            var Q6;
            Q6=makeQuery(id+"F19.opPattern","COPY",BODY,{"derivedFrom":makeQuery(id+"F17.opPattern","COPY",BODY,{"derivedFrom":makeQuery(id+"F6.opPattern","COPY",BODY,{"derivedFrom":makeQuery(id+"F5.opPattern","COPY",BODY,{"derivedFrom":makeQuery(id+"F4.opPattern","COPY",BODY,{"derivedFrom":makeQuery(id+"F2.opPattern","COPY",BODY,{"derivedFrom":makeQuery(id+"F1.opExtrude","SWEPT_BODY",BODY,{"disambiguationData":[OSD([sQuery(id+"F0.wireOp",EDGE,"E0.bottom"),sQuery(id+"F0.wireOp",EDGE,"E0.top"),sQuery(id+"F0.wireOp",EDGE,"E0.left"),sQuery(id+"F0.wireOp",EDGE,"E0.right")])]}),"instanceName":"1"}),"instanceName":"1"}),"instanceName":"1"}),"instanceName":"1"}),"instanceName":"1"}),"instanceName":"1"});
            var Q7;
            Q7=makeQuery(id+"F19.opPattern","COPY",BODY,{"derivedFrom":makeQuery(id+"F17.opPattern","COPY",BODY,{"derivedFrom":makeQuery(id+"F6.opPattern","COPY",BODY,{"derivedFrom":makeQuery(id+"F5.opPattern","COPY",BODY,{"derivedFrom":makeQuery(id+"F4.opPattern","COPY",BODY,{"derivedFrom":makeQuery(id+"F1.opExtrude","SWEPT_BODY",BODY,{"disambiguationData":[OSD([sQuery(id+"F0.wireOp",EDGE,"E0.bottom"),sQuery(id+"F0.wireOp",EDGE,"E0.top"),sQuery(id+"F0.wireOp",EDGE,"E0.left"),sQuery(id+"F0.wireOp",EDGE,"E0.right")])]}),"instanceName":"1"}),"instanceName":"1"}),"instanceName":"1"}),"instanceName":"1"}),"instanceName":"1"});
            var Q8;
            Q8=makeQuery(id+"F19.opPattern","COPY",BODY,{"derivedFrom":makeQuery(id+"F6.opPattern","COPY",BODY,{"derivedFrom":makeQuery(id+"F5.opPattern","COPY",BODY,{"derivedFrom":makeQuery(id+"F4.opPattern","COPY",BODY,{"derivedFrom":makeQuery(id+"F2.opPattern","COPY",BODY,{"derivedFrom":makeQuery(id+"F1.opExtrude","SWEPT_BODY",BODY,{"disambiguationData":[OSD([sQuery(id+"F0.wireOp",EDGE,"E0.bottom"),sQuery(id+"F0.wireOp",EDGE,"E0.top"),sQuery(id+"F0.wireOp",EDGE,"E0.left"),sQuery(id+"F0.wireOp",EDGE,"E0.right")])]}),"instanceName":"1"}),"instanceName":"1"}),"instanceName":"1"}),"instanceName":"1"}),"instanceName":"1"});
            var Q9;
            Q9=makeQuery(id+"F19.opPattern","COPY",BODY,{"derivedFrom":makeQuery(id+"F5.opPattern","COPY",BODY,{"derivedFrom":makeQuery(id+"F4.opPattern","COPY",BODY,{"derivedFrom":makeQuery(id+"F2.opPattern","COPY",BODY,{"derivedFrom":makeQuery(id+"F1.opExtrude","SWEPT_BODY",BODY,{"disambiguationData":[OSD([sQuery(id+"F0.wireOp",EDGE,"E0.bottom"),sQuery(id+"F0.wireOp",EDGE,"E0.top"),sQuery(id+"F0.wireOp",EDGE,"E0.left"),sQuery(id+"F0.wireOp",EDGE,"E0.right")])]}),"instanceName":"1"}),"instanceName":"1"}),"instanceName":"1"}),"instanceName":"1"});
            var Q10;
            Q10=makeQuery(id+"F19.opPattern","COPY",BODY,{"derivedFrom":makeQuery(id+"F17.opPattern","COPY",BODY,{"derivedFrom":makeQuery(id+"F5.opPattern","COPY",BODY,{"derivedFrom":makeQuery(id+"F4.opPattern","COPY",BODY,{"derivedFrom":makeQuery(id+"F1.opExtrude","SWEPT_BODY",BODY,{"disambiguationData":[OSD([sQuery(id+"F0.wireOp",EDGE,"E0.bottom"),sQuery(id+"F0.wireOp",EDGE,"E0.top"),sQuery(id+"F0.wireOp",EDGE,"E0.left"),sQuery(id+"F0.wireOp",EDGE,"E0.right")])]}),"instanceName":"1"}),"instanceName":"1"}),"instanceName":"1"}),"instanceName":"1"});
            var Q11;
            Q11=makeQuery(id+"F19.opPattern","COPY",BODY,{"derivedFrom":makeQuery(id+"F17.opPattern","COPY",BODY,{"derivedFrom":makeQuery(id+"F5.opPattern","COPY",BODY,{"derivedFrom":makeQuery(id+"F4.opPattern","COPY",BODY,{"derivedFrom":makeQuery(id+"F2.opPattern","COPY",BODY,{"derivedFrom":makeQuery(id+"F1.opExtrude","SWEPT_BODY",BODY,{"disambiguationData":[OSD([sQuery(id+"F0.wireOp",EDGE,"E0.bottom"),sQuery(id+"F0.wireOp",EDGE,"E0.top"),sQuery(id+"F0.wireOp",EDGE,"E0.left"),sQuery(id+"F0.wireOp",EDGE,"E0.right")])]}),"instanceName":"1"}),"instanceName":"1"}),"instanceName":"1"}),"instanceName":"1"}),"instanceName":"1"});
            var Q12;
            Q12=makeQuery(id+"F21.opPattern","COPY",BODY,{"derivedFrom":makeQuery(id+"F19.opPattern","COPY",BODY,{"derivedFrom":makeQuery(id+"F17.opPattern","COPY",BODY,{"derivedFrom":makeQuery(id+"F12.opPattern","COPY",BODY,{"derivedFrom":makeQuery(id+"F6.opPattern","COPY",BODY,{"derivedFrom":makeQuery(id+"F5.opPattern","COPY",BODY,{"derivedFrom":makeQuery(id+"F4.opPattern","COPY",BODY,{"derivedFrom":makeQuery(id+"F2.opPattern","COPY",BODY,{"derivedFrom":makeQuery(id+"F1.opExtrude","SWEPT_BODY",BODY,{"disambiguationData":[OSD([sQuery(id+"F0.wireOp",EDGE,"E0.bottom"),sQuery(id+"F0.wireOp",EDGE,"E0.top"),sQuery(id+"F0.wireOp",EDGE,"E0.left"),sQuery(id+"F0.wireOp",EDGE,"E0.right")])]}),"instanceName":"1"}),"instanceName":"1"}),"instanceName":"1"}),"instanceName":"1"}),"instanceName":"1"}),"instanceName":"1"}),"instanceName":"1"}),"instanceName":"1"});
            var Q13;
            Q13=makeQuery(id+"F21.opPattern","COPY",BODY,{"derivedFrom":makeQuery(id+"F19.opPattern","COPY",BODY,{"derivedFrom":makeQuery(id+"F17.opPattern","COPY",BODY,{"derivedFrom":makeQuery(id+"F6.opPattern","COPY",BODY,{"derivedFrom":makeQuery(id+"F5.opPattern","COPY",BODY,{"derivedFrom":makeQuery(id+"F4.opPattern","COPY",BODY,{"derivedFrom":makeQuery(id+"F2.opPattern","COPY",BODY,{"derivedFrom":makeQuery(id+"F1.opExtrude","SWEPT_BODY",BODY,{"disambiguationData":[OSD([sQuery(id+"F0.wireOp",EDGE,"E0.bottom"),sQuery(id+"F0.wireOp",EDGE,"E0.top"),sQuery(id+"F0.wireOp",EDGE,"E0.left"),sQuery(id+"F0.wireOp",EDGE,"E0.right")])]}),"instanceName":"1"}),"instanceName":"1"}),"instanceName":"1"}),"instanceName":"1"}),"instanceName":"1"}),"instanceName":"1"}),"instanceName":"1"});
            var Q14;
            Q14=makeQuery(id+"F21.opPattern","COPY",BODY,{"derivedFrom":makeQuery(id+"F19.opPattern","COPY",BODY,{"derivedFrom":makeQuery(id+"F17.opPattern","COPY",BODY,{"derivedFrom":makeQuery(id+"F5.opPattern","COPY",BODY,{"derivedFrom":makeQuery(id+"F4.opPattern","COPY",BODY,{"derivedFrom":makeQuery(id+"F2.opPattern","COPY",BODY,{"derivedFrom":makeQuery(id+"F1.opExtrude","SWEPT_BODY",BODY,{"disambiguationData":[OSD([sQuery(id+"F0.wireOp",EDGE,"E0.bottom"),sQuery(id+"F0.wireOp",EDGE,"E0.top"),sQuery(id+"F0.wireOp",EDGE,"E0.left"),sQuery(id+"F0.wireOp",EDGE,"E0.right")])]}),"instanceName":"1"}),"instanceName":"1"}),"instanceName":"1"}),"instanceName":"1"}),"instanceName":"1"}),"instanceName":"1"});
            var Q15;
            Q15=makeQuery(id+"F21.opPattern","COPY",BODY,{"derivedFrom":makeQuery(id+"F19.opPattern","COPY",BODY,{"derivedFrom":makeQuery(id+"F17.opPattern","COPY",BODY,{"derivedFrom":makeQuery(id+"F5.opPattern","COPY",BODY,{"derivedFrom":makeQuery(id+"F4.opPattern","COPY",BODY,{"derivedFrom":makeQuery(id+"F1.opExtrude","SWEPT_BODY",BODY,{"disambiguationData":[OSD([sQuery(id+"F0.wireOp",EDGE,"E0.bottom"),sQuery(id+"F0.wireOp",EDGE,"E0.top"),sQuery(id+"F0.wireOp",EDGE,"E0.left"),sQuery(id+"F0.wireOp",EDGE,"E0.right")])]}),"instanceName":"1"}),"instanceName":"1"}),"instanceName":"1"}),"instanceName":"1"}),"instanceName":"1"});
            var Q16;
            Q16=makeQuery(id+"F21.opPattern","COPY",BODY,{"derivedFrom":makeQuery(id+"F19.opPattern","COPY",BODY,{"derivedFrom":makeQuery(id+"F17.opPattern","COPY",BODY,{"derivedFrom":makeQuery(id+"F6.opPattern","COPY",BODY,{"derivedFrom":makeQuery(id+"F5.opPattern","COPY",BODY,{"derivedFrom":makeQuery(id+"F4.opPattern","COPY",BODY,{"derivedFrom":makeQuery(id+"F1.opExtrude","SWEPT_BODY",BODY,{"disambiguationData":[OSD([sQuery(id+"F0.wireOp",EDGE,"E0.bottom"),sQuery(id+"F0.wireOp",EDGE,"E0.top"),sQuery(id+"F0.wireOp",EDGE,"E0.left"),sQuery(id+"F0.wireOp",EDGE,"E0.right")])]}),"instanceName":"1"}),"instanceName":"1"}),"instanceName":"1"}),"instanceName":"1"}),"instanceName":"1"}),"instanceName":"1"});
            var Q17;
            Q17=makeQuery(id+"F21.opPattern","COPY",BODY,{"derivedFrom":makeQuery(id+"F19.opPattern","COPY",BODY,{"derivedFrom":makeQuery(id+"F17.opPattern","COPY",BODY,{"derivedFrom":makeQuery(id+"F12.opPattern","COPY",BODY,{"derivedFrom":makeQuery(id+"F6.opPattern","COPY",BODY,{"derivedFrom":makeQuery(id+"F5.opPattern","COPY",BODY,{"derivedFrom":makeQuery(id+"F4.opPattern","COPY",BODY,{"derivedFrom":makeQuery(id+"F1.opExtrude","SWEPT_BODY",BODY,{"disambiguationData":[OSD([sQuery(id+"F0.wireOp",EDGE,"E0.bottom"),sQuery(id+"F0.wireOp",EDGE,"E0.top"),sQuery(id+"F0.wireOp",EDGE,"E0.left"),sQuery(id+"F0.wireOp",EDGE,"E0.right")])]}),"instanceName":"1"}),"instanceName":"1"}),"instanceName":"1"}),"instanceName":"1"}),"instanceName":"1"}),"instanceName":"1"}),"instanceName":"1"});
            var Q18;
            Q18=makeQuery(id+"F21.opPattern","COPY",BODY,{"derivedFrom":makeQuery(id+"F19.opPattern","COPY",BODY,{"derivedFrom":makeQuery(id+"F12.opPattern","COPY",BODY,{"derivedFrom":makeQuery(id+"F6.opPattern","COPY",BODY,{"derivedFrom":makeQuery(id+"F5.opPattern","COPY",BODY,{"derivedFrom":makeQuery(id+"F4.opPattern","COPY",BODY,{"derivedFrom":makeQuery(id+"F2.opPattern","COPY",BODY,{"derivedFrom":makeQuery(id+"F1.opExtrude","SWEPT_BODY",BODY,{"disambiguationData":[OSD([sQuery(id+"F0.wireOp",EDGE,"E0.bottom"),sQuery(id+"F0.wireOp",EDGE,"E0.top"),sQuery(id+"F0.wireOp",EDGE,"E0.left"),sQuery(id+"F0.wireOp",EDGE,"E0.right")])]}),"instanceName":"1"}),"instanceName":"1"}),"instanceName":"1"}),"instanceName":"1"}),"instanceName":"1"}),"instanceName":"1"}),"instanceName":"1"});
            var Q19;
            Q19=makeQuery(id+"F21.opPattern","COPY",BODY,{"derivedFrom":makeQuery(id+"F19.opPattern","COPY",BODY,{"derivedFrom":makeQuery(id+"F6.opPattern","COPY",BODY,{"derivedFrom":makeQuery(id+"F5.opPattern","COPY",BODY,{"derivedFrom":makeQuery(id+"F4.opPattern","COPY",BODY,{"derivedFrom":makeQuery(id+"F2.opPattern","COPY",BODY,{"derivedFrom":makeQuery(id+"F1.opExtrude","SWEPT_BODY",BODY,{"disambiguationData":[OSD([sQuery(id+"F0.wireOp",EDGE,"E0.bottom"),sQuery(id+"F0.wireOp",EDGE,"E0.top"),sQuery(id+"F0.wireOp",EDGE,"E0.left"),sQuery(id+"F0.wireOp",EDGE,"E0.right")])]}),"instanceName":"1"}),"instanceName":"1"}),"instanceName":"1"}),"instanceName":"1"}),"instanceName":"1"}),"instanceName":"1"});
            var Q20;
            Q20=makeQuery(id+"F21.opPattern","COPY",BODY,{"derivedFrom":makeQuery(id+"F19.opPattern","COPY",BODY,{"derivedFrom":makeQuery(id+"F5.opPattern","COPY",BODY,{"derivedFrom":makeQuery(id+"F4.opPattern","COPY",BODY,{"derivedFrom":makeQuery(id+"F2.opPattern","COPY",BODY,{"derivedFrom":makeQuery(id+"F1.opExtrude","SWEPT_BODY",BODY,{"disambiguationData":[OSD([sQuery(id+"F0.wireOp",EDGE,"E0.bottom"),sQuery(id+"F0.wireOp",EDGE,"E0.top"),sQuery(id+"F0.wireOp",EDGE,"E0.left"),sQuery(id+"F0.wireOp",EDGE,"E0.right")])]}),"instanceName":"1"}),"instanceName":"1"}),"instanceName":"1"}),"instanceName":"1"}),"instanceName":"1"});
            var Q21;
            Q21=makeQuery(id+"F21.opPattern","COPY",EDGE,{"derivedFrom":makeQuery(id+"F19.opPattern","COPY",EDGE,{"derivedFrom":makeQuery(id+"F17.opPattern","COPY",EDGE,{"derivedFrom":makeQuery(id+"F5.opPattern","COPY",EDGE,{"derivedFrom":makeQuery(id+"F4.opPattern","COPY",EDGE,{"derivedFrom":makeQuery(id+"F2.opPattern","COPY",EDGE,{"derivedFrom":makeQuery(id+"F1.opExtrude","CAP_EDGE",EDGE,{"disambiguationData":[OSD([sQuery(id+"F0.wireOp",EDGE,"E0.top")])],"isStart":false}),"instanceName":"1"}),"instanceName":"1"}),"instanceName":"1"}),"instanceName":"1"}),"instanceName":"1"}),"instanceName":"1"});
            transform(context, id + "F23", {"entities" : qUnion([Q0, Q1, Q2, Q3, Q4, Q5, Q6, Q7, Q8, Q9, Q10, Q11, Q12, Q13, Q14, Q15, Q16, Q17, Q18, Q19, Q20]), "transformType" : TransformType.TRANSLATION_DISTANCE, "transformDirection" : qUnion([Q21]), "distance" : 30 * mm, "makeCopy" : true});
        }
        {
            var Q0;
            Q0=makeQuery(id+"F23.opPattern","COPY",BODY,{"derivedFrom":makeQuery(id+"F21.opPattern","COPY",BODY,{"derivedFrom":makeQuery(id+"F19.opPattern","COPY",BODY,{"derivedFrom":makeQuery(id+"F17.opPattern","COPY",BODY,{"derivedFrom":makeQuery(id+"F12.opPattern","COPY",BODY,{"derivedFrom":makeQuery(id+"F6.opPattern","COPY",BODY,{"derivedFrom":makeQuery(id+"F5.opPattern","COPY",BODY,{"derivedFrom":makeQuery(id+"F4.opPattern","COPY",BODY,{"derivedFrom":makeQuery(id+"F1.opExtrude","SWEPT_BODY",BODY,{"disambiguationData":[OSD([sQuery(id+"F0.wireOp",EDGE,"E0.bottom"),sQuery(id+"F0.wireOp",EDGE,"E0.top"),sQuery(id+"F0.wireOp",EDGE,"E0.left"),sQuery(id+"F0.wireOp",EDGE,"E0.right")])]}),"instanceName":"1"}),"instanceName":"1"}),"instanceName":"1"}),"instanceName":"1"}),"instanceName":"1"}),"instanceName":"1"}),"instanceName":"1"}),"instanceName":"1"});
            var Q1;
            Q1=makeQuery(id+"F19.opPattern","COPY",BODY,{"derivedFrom":makeQuery(id+"F17.opPattern","COPY",BODY,{"derivedFrom":makeQuery(id+"F5.opPattern","COPY",BODY,{"derivedFrom":makeQuery(id+"F4.opPattern","COPY",BODY,{"derivedFrom":makeQuery(id+"F2.opPattern","COPY",BODY,{"derivedFrom":makeQuery(id+"F1.opExtrude","SWEPT_BODY",BODY,{"disambiguationData":[OSD([sQuery(id+"F0.wireOp",EDGE,"E0.bottom"),sQuery(id+"F0.wireOp",EDGE,"E0.top"),sQuery(id+"F0.wireOp",EDGE,"E0.left"),sQuery(id+"F0.wireOp",EDGE,"E0.right")])]}),"instanceName":"1"}),"instanceName":"1"}),"instanceName":"1"}),"instanceName":"1"}),"instanceName":"1"});
            var Q2;
            Q2=makeQuery(id+"F23.opPattern","COPY",BODY,{"derivedFrom":makeQuery(id+"F19.opPattern","COPY",BODY,{"derivedFrom":makeQuery(id+"F5.opPattern","COPY",BODY,{"derivedFrom":makeQuery(id+"F4.opPattern","COPY",BODY,{"derivedFrom":makeQuery(id+"F2.opPattern","COPY",BODY,{"derivedFrom":makeQuery(id+"F1.opExtrude","SWEPT_BODY",BODY,{"disambiguationData":[OSD([sQuery(id+"F0.wireOp",EDGE,"E0.bottom"),sQuery(id+"F0.wireOp",EDGE,"E0.top"),sQuery(id+"F0.wireOp",EDGE,"E0.left"),sQuery(id+"F0.wireOp",EDGE,"E0.right")])]}),"instanceName":"1"}),"instanceName":"1"}),"instanceName":"1"}),"instanceName":"1"}),"instanceName":"1"});
            var Q3;
            Q3=makeQuery(id+"F23.opPattern","COPY",BODY,{"derivedFrom":makeQuery(id+"F19.opPattern","COPY",BODY,{"derivedFrom":makeQuery(id+"F17.opPattern","COPY",BODY,{"derivedFrom":makeQuery(id+"F5.opPattern","COPY",BODY,{"derivedFrom":makeQuery(id+"F4.opPattern","COPY",BODY,{"derivedFrom":makeQuery(id+"F1.opExtrude","SWEPT_BODY",BODY,{"disambiguationData":[OSD([sQuery(id+"F0.wireOp",EDGE,"E0.bottom"),sQuery(id+"F0.wireOp",EDGE,"E0.top"),sQuery(id+"F0.wireOp",EDGE,"E0.left"),sQuery(id+"F0.wireOp",EDGE,"E0.right")])]}),"instanceName":"1"}),"instanceName":"1"}),"instanceName":"1"}),"instanceName":"1"}),"instanceName":"1"});
            var Q4;
            Q4=makeQuery(id+"F23.opPattern","COPY",BODY,{"derivedFrom":makeQuery(id+"F19.opPattern","COPY",BODY,{"derivedFrom":makeQuery(id+"F17.opPattern","COPY",BODY,{"derivedFrom":makeQuery(id+"F5.opPattern","COPY",BODY,{"derivedFrom":makeQuery(id+"F4.opPattern","COPY",BODY,{"derivedFrom":makeQuery(id+"F2.opPattern","COPY",BODY,{"derivedFrom":makeQuery(id+"F1.opExtrude","SWEPT_BODY",BODY,{"disambiguationData":[OSD([sQuery(id+"F0.wireOp",EDGE,"E0.bottom"),sQuery(id+"F0.wireOp",EDGE,"E0.top"),sQuery(id+"F0.wireOp",EDGE,"E0.left"),sQuery(id+"F0.wireOp",EDGE,"E0.right")])]}),"instanceName":"1"}),"instanceName":"1"}),"instanceName":"1"}),"instanceName":"1"}),"instanceName":"1"}),"instanceName":"1"});
            var Q5;
            Q5=makeQuery(id+"F23.opPattern","COPY",BODY,{"derivedFrom":makeQuery(id+"F21.opPattern","COPY",BODY,{"derivedFrom":makeQuery(id+"F19.opPattern","COPY",BODY,{"derivedFrom":makeQuery(id+"F17.opPattern","COPY",BODY,{"derivedFrom":makeQuery(id+"F6.opPattern","COPY",BODY,{"derivedFrom":makeQuery(id+"F5.opPattern","COPY",BODY,{"derivedFrom":makeQuery(id+"F4.opPattern","COPY",BODY,{"derivedFrom":makeQuery(id+"F1.opExtrude","SWEPT_BODY",BODY,{"disambiguationData":[OSD([sQuery(id+"F0.wireOp",EDGE,"E0.bottom"),sQuery(id+"F0.wireOp",EDGE,"E0.top"),sQuery(id+"F0.wireOp",EDGE,"E0.left"),sQuery(id+"F0.wireOp",EDGE,"E0.right")])]}),"instanceName":"1"}),"instanceName":"1"}),"instanceName":"1"}),"instanceName":"1"}),"instanceName":"1"}),"instanceName":"1"}),"instanceName":"1"});
            var Q6;
            Q6=makeQuery(id+"F23.opPattern","COPY",BODY,{"derivedFrom":makeQuery(id+"F21.opPattern","COPY",BODY,{"derivedFrom":makeQuery(id+"F19.opPattern","COPY",BODY,{"derivedFrom":makeQuery(id+"F17.opPattern","COPY",BODY,{"derivedFrom":makeQuery(id+"F12.opPattern","COPY",BODY,{"derivedFrom":makeQuery(id+"F6.opPattern","COPY",BODY,{"derivedFrom":makeQuery(id+"F5.opPattern","COPY",BODY,{"derivedFrom":makeQuery(id+"F4.opPattern","COPY",BODY,{"derivedFrom":makeQuery(id+"F2.opPattern","COPY",BODY,{"derivedFrom":makeQuery(id+"F1.opExtrude","SWEPT_BODY",BODY,{"disambiguationData":[OSD([sQuery(id+"F0.wireOp",EDGE,"E0.bottom"),sQuery(id+"F0.wireOp",EDGE,"E0.top"),sQuery(id+"F0.wireOp",EDGE,"E0.left"),sQuery(id+"F0.wireOp",EDGE,"E0.right")])]}),"instanceName":"1"}),"instanceName":"1"}),"instanceName":"1"}),"instanceName":"1"}),"instanceName":"1"}),"instanceName":"1"}),"instanceName":"1"}),"instanceName":"1"}),"instanceName":"1"});
            var Q7;
            Q7=makeQuery(id+"F23.opPattern","COPY",BODY,{"derivedFrom":makeQuery(id+"F21.opPattern","COPY",BODY,{"derivedFrom":makeQuery(id+"F19.opPattern","COPY",BODY,{"derivedFrom":makeQuery(id+"F17.opPattern","COPY",BODY,{"derivedFrom":makeQuery(id+"F5.opPattern","COPY",BODY,{"derivedFrom":makeQuery(id+"F4.opPattern","COPY",BODY,{"derivedFrom":makeQuery(id+"F2.opPattern","COPY",BODY,{"derivedFrom":makeQuery(id+"F1.opExtrude","SWEPT_BODY",BODY,{"disambiguationData":[OSD([sQuery(id+"F0.wireOp",EDGE,"E0.bottom"),sQuery(id+"F0.wireOp",EDGE,"E0.top"),sQuery(id+"F0.wireOp",EDGE,"E0.left"),sQuery(id+"F0.wireOp",EDGE,"E0.right")])]}),"instanceName":"1"}),"instanceName":"1"}),"instanceName":"1"}),"instanceName":"1"}),"instanceName":"1"}),"instanceName":"1"}),"instanceName":"1"});
            var Q8;
            Q8=makeQuery(id+"F23.opPattern","COPY",EDGE,{"derivedFrom":makeQuery(id+"F21.opPattern","COPY",EDGE,{"derivedFrom":makeQuery(id+"F19.opPattern","COPY",EDGE,{"derivedFrom":makeQuery(id+"F17.opPattern","COPY",EDGE,{"derivedFrom":makeQuery(id+"F5.opPattern","COPY",EDGE,{"derivedFrom":makeQuery(id+"F4.opPattern","COPY",EDGE,{"derivedFrom":makeQuery(id+"F2.opPattern","COPY",EDGE,{"derivedFrom":makeQuery(id+"F1.opExtrude","CAP_EDGE",EDGE,{"disambiguationData":[OSD([sQuery(id+"F0.wireOp",EDGE,"E0.right")])],"isStart":false}),"instanceName":"1"}),"instanceName":"1"}),"instanceName":"1"}),"instanceName":"1"}),"instanceName":"1"}),"instanceName":"1"}),"instanceName":"1"});
            transform(context, id + "F24", {"entities" : qUnion([Q0, Q1, Q2, Q3, Q4, Q5, Q6, Q7]), "transformType" : TransformType.TRANSLATION_DISTANCE, "transformDirection" : qUnion([Q8]), "distance" : 40 * mm, "makeCopy" : true});
        }
        {
            var Q0;
            Q0=makeQuery(id+"F24.opPattern","COPY",BODY,{"derivedFrom":makeQuery(id+"F23.opPattern","COPY",BODY,{"derivedFrom":makeQuery(id+"F21.opPattern","COPY",BODY,{"derivedFrom":makeQuery(id+"F19.opPattern","COPY",BODY,{"derivedFrom":makeQuery(id+"F17.opPattern","COPY",BODY,{"derivedFrom":makeQuery(id+"F5.opPattern","COPY",BODY,{"derivedFrom":makeQuery(id+"F4.opPattern","COPY",BODY,{"derivedFrom":makeQuery(id+"F2.opPattern","COPY",BODY,{"derivedFrom":makeQuery(id+"F1.opExtrude","SWEPT_BODY",BODY,{"disambiguationData":[OSD([sQuery(id+"F0.wireOp",EDGE,"E0.bottom"),sQuery(id+"F0.wireOp",EDGE,"E0.top"),sQuery(id+"F0.wireOp",EDGE,"E0.left"),sQuery(id+"F0.wireOp",EDGE,"E0.right")])]}),"instanceName":"1"}),"instanceName":"1"}),"instanceName":"1"}),"instanceName":"1"}),"instanceName":"1"}),"instanceName":"1"}),"instanceName":"1"}),"instanceName":"1"});
            var Q1;
            Q1=makeQuery(id+"F24.opPattern","COPY",EDGE,{"derivedFrom":makeQuery(id+"F23.opPattern","COPY",EDGE,{"derivedFrom":makeQuery(id+"F21.opPattern","COPY",EDGE,{"derivedFrom":makeQuery(id+"F19.opPattern","COPY",EDGE,{"derivedFrom":makeQuery(id+"F17.opPattern","COPY",EDGE,{"derivedFrom":makeQuery(id+"F5.opPattern","COPY",EDGE,{"derivedFrom":makeQuery(id+"F4.opPattern","COPY",EDGE,{"derivedFrom":makeQuery(id+"F2.opPattern","COPY",EDGE,{"derivedFrom":makeQuery(id+"F1.opExtrude","CAP_EDGE",EDGE,{"disambiguationData":[OSD([sQuery(id+"F0.wireOp",EDGE,"E0.top")])],"isStart":false}),"instanceName":"1"}),"instanceName":"1"}),"instanceName":"1"}),"instanceName":"1"}),"instanceName":"1"}),"instanceName":"1"}),"instanceName":"1"}),"instanceName":"1"});
            transform(context, id + "F25", {"entities" : qUnion([Q0]), "transformType" : TransformType.TRANSLATION_DISTANCE, "transformDirection" : qUnion([Q1]), "distance" : 10 * mm, "makeCopy" : true});
        }
        {
            var Q0;
            Q0=makeQuery(id+"F19.opPattern","COPY",BODY,{"derivedFrom":makeQuery(id+"F6.opPattern","COPY",BODY,{"derivedFrom":makeQuery(id+"F5.opPattern","COPY",BODY,{"derivedFrom":makeQuery(id+"F4.opPattern","COPY",BODY,{"derivedFrom":makeQuery(id+"F1.opExtrude","SWEPT_BODY",BODY,{"disambiguationData":[OSD([sQuery(id+"F0.wireOp",EDGE,"E0.bottom"),sQuery(id+"F0.wireOp",EDGE,"E0.top"),sQuery(id+"F0.wireOp",EDGE,"E0.left"),sQuery(id+"F0.wireOp",EDGE,"E0.right")])]}),"instanceName":"1"}),"instanceName":"1"}),"instanceName":"1"}),"instanceName":"1"});
            var Q1;
            Q1=makeQuery(id+"F19.opPattern","COPY",BODY,{"derivedFrom":makeQuery(id+"F15.opPattern","COPY",BODY,{"derivedFrom":makeQuery(id+"F12.opPattern","COPY",BODY,{"derivedFrom":makeQuery(id+"F6.opPattern","COPY",BODY,{"derivedFrom":makeQuery(id+"F5.opPattern","COPY",BODY,{"derivedFrom":makeQuery(id+"F4.opPattern","COPY",BODY,{"derivedFrom":makeQuery(id+"F2.opPattern","COPY",BODY,{"derivedFrom":makeQuery(id+"F1.opExtrude","SWEPT_BODY",BODY,{"disambiguationData":[OSD([sQuery(id+"F0.wireOp",EDGE,"E0.bottom"),sQuery(id+"F0.wireOp",EDGE,"E0.top"),sQuery(id+"F0.wireOp",EDGE,"E0.left"),sQuery(id+"F0.wireOp",EDGE,"E0.right")])]}),"instanceName":"1"}),"instanceName":"1"}),"instanceName":"1"}),"instanceName":"1"}),"instanceName":"1"}),"instanceName":"1"}),"instanceName":"1"});
            var Q2;
            Q2=makeQuery(id+"F19.opPattern","COPY",BODY,{"derivedFrom":makeQuery(id+"F5.opPattern","COPY",BODY,{"derivedFrom":makeQuery(id+"F4.opPattern","COPY",BODY,{"derivedFrom":makeQuery(id+"F1.opExtrude","SWEPT_BODY",BODY,{"disambiguationData":[OSD([sQuery(id+"F0.wireOp",EDGE,"E0.bottom"),sQuery(id+"F0.wireOp",EDGE,"E0.top"),sQuery(id+"F0.wireOp",EDGE,"E0.left"),sQuery(id+"F0.wireOp",EDGE,"E0.right")])]}),"instanceName":"1"}),"instanceName":"1"}),"instanceName":"1"});
            var Q3;
            Q3=makeQuery(id+"F23.opPattern","COPY",BODY,{"derivedFrom":makeQuery(id+"F19.opPattern","COPY",BODY,{"derivedFrom":makeQuery(id+"F6.opPattern","COPY",BODY,{"derivedFrom":makeQuery(id+"F5.opPattern","COPY",BODY,{"derivedFrom":makeQuery(id+"F4.opPattern","COPY",BODY,{"derivedFrom":makeQuery(id+"F2.opPattern","COPY",BODY,{"derivedFrom":makeQuery(id+"F1.opExtrude","SWEPT_BODY",BODY,{"disambiguationData":[OSD([sQuery(id+"F0.wireOp",EDGE,"E0.bottom"),sQuery(id+"F0.wireOp",EDGE,"E0.top"),sQuery(id+"F0.wireOp",EDGE,"E0.left"),sQuery(id+"F0.wireOp",EDGE,"E0.right")])]}),"instanceName":"1"}),"instanceName":"1"}),"instanceName":"1"}),"instanceName":"1"}),"instanceName":"1"}),"instanceName":"1"});
            var Q4;
            Q4=makeQuery(id+"F23.opPattern","COPY",BODY,{"derivedFrom":makeQuery(id+"F19.opPattern","COPY",BODY,{"derivedFrom":makeQuery(id+"F17.opPattern","COPY",BODY,{"derivedFrom":makeQuery(id+"F15.opPattern","COPY",BODY,{"derivedFrom":makeQuery(id+"F12.opPattern","COPY",BODY,{"derivedFrom":makeQuery(id+"F6.opPattern","COPY",BODY,{"derivedFrom":makeQuery(id+"F5.opPattern","COPY",BODY,{"derivedFrom":makeQuery(id+"F4.opPattern","COPY",BODY,{"derivedFrom":makeQuery(id+"F2.opPattern","COPY",BODY,{"derivedFrom":makeQuery(id+"F1.opExtrude","SWEPT_BODY",BODY,{"disambiguationData":[OSD([sQuery(id+"F0.wireOp",EDGE,"E0.bottom"),sQuery(id+"F0.wireOp",EDGE,"E0.top"),sQuery(id+"F0.wireOp",EDGE,"E0.left"),sQuery(id+"F0.wireOp",EDGE,"E0.right")])]}),"instanceName":"1"}),"instanceName":"1"}),"instanceName":"1"}),"instanceName":"1"}),"instanceName":"1"}),"instanceName":"1"}),"instanceName":"1"}),"instanceName":"1"}),"instanceName":"1"});
            var Q5;
            Q5=makeQuery(id+"F17.opPattern","COPY",BODY,{"derivedFrom":makeQuery(id+"F12.opPattern","COPY",BODY,{"derivedFrom":makeQuery(id+"F6.opPattern","COPY",BODY,{"derivedFrom":makeQuery(id+"F5.opPattern","COPY",BODY,{"derivedFrom":makeQuery(id+"F4.opPattern","COPY",BODY,{"derivedFrom":makeQuery(id+"F2.opPattern","COPY",BODY,{"derivedFrom":makeQuery(id+"F1.opExtrude","SWEPT_BODY",BODY,{"disambiguationData":[OSD([sQuery(id+"F0.wireOp",EDGE,"E0.bottom"),sQuery(id+"F0.wireOp",EDGE,"E0.top"),sQuery(id+"F0.wireOp",EDGE,"E0.left"),sQuery(id+"F0.wireOp",EDGE,"E0.right")])]}),"instanceName":"1"}),"instanceName":"1"}),"instanceName":"1"}),"instanceName":"1"}),"instanceName":"1"}),"instanceName":"1"});
            var Q6;
            Q6=makeQuery(id+"F19.opPattern","COPY",BODY,{"derivedFrom":makeQuery(id+"F17.opPattern","COPY",BODY,{"derivedFrom":makeQuery(id+"F12.opPattern","COPY",BODY,{"derivedFrom":makeQuery(id+"F6.opPattern","COPY",BODY,{"derivedFrom":makeQuery(id+"F5.opPattern","COPY",BODY,{"derivedFrom":makeQuery(id+"F4.opPattern","COPY",BODY,{"derivedFrom":makeQuery(id+"F1.opExtrude","SWEPT_BODY",BODY,{"disambiguationData":[OSD([sQuery(id+"F0.wireOp",EDGE,"E0.bottom"),sQuery(id+"F0.wireOp",EDGE,"E0.top"),sQuery(id+"F0.wireOp",EDGE,"E0.left"),sQuery(id+"F0.wireOp",EDGE,"E0.right")])]}),"instanceName":"1"}),"instanceName":"1"}),"instanceName":"1"}),"instanceName":"1"}),"instanceName":"1"}),"instanceName":"1"});
            var Q7;
            Q7=makeQuery(id+"F17.opPattern","COPY",BODY,{"derivedFrom":makeQuery(id+"F5.opPattern","COPY",BODY,{"derivedFrom":makeQuery(id+"F4.opPattern","COPY",BODY,{"derivedFrom":makeQuery(id+"F2.opPattern","COPY",BODY,{"derivedFrom":makeQuery(id+"F1.opExtrude","SWEPT_BODY",BODY,{"disambiguationData":[OSD([sQuery(id+"F0.wireOp",EDGE,"E0.bottom"),sQuery(id+"F0.wireOp",EDGE,"E0.top"),sQuery(id+"F0.wireOp",EDGE,"E0.left"),sQuery(id+"F0.wireOp",EDGE,"E0.right")])]}),"instanceName":"1"}),"instanceName":"1"}),"instanceName":"1"}),"instanceName":"1"});
            var Q8;
            Q8=makeQuery(id+"F17.opPattern","COPY",BODY,{"derivedFrom":makeQuery(id+"F15.opPattern","COPY",BODY,{"derivedFrom":makeQuery(id+"F12.opPattern","COPY",BODY,{"derivedFrom":makeQuery(id+"F6.opPattern","COPY",BODY,{"derivedFrom":makeQuery(id+"F5.opPattern","COPY",BODY,{"derivedFrom":makeQuery(id+"F4.opPattern","COPY",BODY,{"derivedFrom":makeQuery(id+"F2.opPattern","COPY",BODY,{"derivedFrom":makeQuery(id+"F1.opExtrude","SWEPT_BODY",BODY,{"disambiguationData":[OSD([sQuery(id+"F0.wireOp",EDGE,"E0.bottom"),sQuery(id+"F0.wireOp",EDGE,"E0.top"),sQuery(id+"F0.wireOp",EDGE,"E0.left"),sQuery(id+"F0.wireOp",EDGE,"E0.right")])]}),"instanceName":"1"}),"instanceName":"1"}),"instanceName":"1"}),"instanceName":"1"}),"instanceName":"1"}),"instanceName":"1"}),"instanceName":"1"});
            var Q9;
            Q9=makeQuery(id+"F23.opPattern","COPY",BODY,{"derivedFrom":makeQuery(id+"F19.opPattern","COPY",BODY,{"derivedFrom":makeQuery(id+"F12.opPattern","COPY",BODY,{"derivedFrom":makeQuery(id+"F6.opPattern","COPY",BODY,{"derivedFrom":makeQuery(id+"F5.opPattern","COPY",BODY,{"derivedFrom":makeQuery(id+"F4.opPattern","COPY",BODY,{"derivedFrom":makeQuery(id+"F2.opPattern","COPY",BODY,{"derivedFrom":makeQuery(id+"F1.opExtrude","SWEPT_BODY",BODY,{"disambiguationData":[OSD([sQuery(id+"F0.wireOp",EDGE,"E0.bottom"),sQuery(id+"F0.wireOp",EDGE,"E0.top"),sQuery(id+"F0.wireOp",EDGE,"E0.left"),sQuery(id+"F0.wireOp",EDGE,"E0.right")])]}),"instanceName":"1"}),"instanceName":"1"}),"instanceName":"1"}),"instanceName":"1"}),"instanceName":"1"}),"instanceName":"1"}),"instanceName":"1"});
            var Q10;
            Q10=makeQuery(id+"F19.opPattern","COPY",BODY,{"derivedFrom":makeQuery(id+"F17.opPattern","COPY",BODY,{"derivedFrom":makeQuery(id+"F5.opPattern","COPY",BODY,{"derivedFrom":makeQuery(id+"F4.opPattern","COPY",BODY,{"derivedFrom":makeQuery(id+"F2.opPattern","COPY",BODY,{"derivedFrom":makeQuery(id+"F1.opExtrude","SWEPT_BODY",BODY,{"disambiguationData":[OSD([sQuery(id+"F0.wireOp",EDGE,"E0.bottom"),sQuery(id+"F0.wireOp",EDGE,"E0.top"),sQuery(id+"F0.wireOp",EDGE,"E0.left"),sQuery(id+"F0.wireOp",EDGE,"E0.right")])]}),"instanceName":"1"}),"instanceName":"1"}),"instanceName":"1"}),"instanceName":"1"}),"instanceName":"1"});
            var Q11;
            Q11=makeQuery(id+"F17.opPattern","COPY",BODY,{"derivedFrom":makeQuery(id+"F8.opPattern","COPY",BODY,{"derivedFrom":makeQuery(id+"F5.opPattern","COPY",BODY,{"derivedFrom":makeQuery(id+"F4.opPattern","COPY",BODY,{"derivedFrom":makeQuery(id+"F1.opExtrude","SWEPT_BODY",BODY,{"disambiguationData":[OSD([sQuery(id+"F0.wireOp",EDGE,"E0.bottom"),sQuery(id+"F0.wireOp",EDGE,"E0.top"),sQuery(id+"F0.wireOp",EDGE,"E0.left"),sQuery(id+"F0.wireOp",EDGE,"E0.right")])]}),"instanceName":"1"}),"instanceName":"1"}),"instanceName":"1"}),"instanceName":"1"});
            var Q12;
            Q12=makeQuery(id+"F17.opPattern","COPY",BODY,{"derivedFrom":makeQuery(id+"F6.opPattern","COPY",BODY,{"derivedFrom":makeQuery(id+"F5.opPattern","COPY",BODY,{"derivedFrom":makeQuery(id+"F4.opPattern","COPY",BODY,{"derivedFrom":makeQuery(id+"F1.opExtrude","SWEPT_BODY",BODY,{"disambiguationData":[OSD([sQuery(id+"F0.wireOp",EDGE,"E0.bottom"),sQuery(id+"F0.wireOp",EDGE,"E0.top"),sQuery(id+"F0.wireOp",EDGE,"E0.left"),sQuery(id+"F0.wireOp",EDGE,"E0.right")])]}),"instanceName":"1"}),"instanceName":"1"}),"instanceName":"1"}),"instanceName":"1"});
            var Q13;
            Q13=makeQuery(id+"F17.opPattern","COPY",BODY,{"derivedFrom":makeQuery(id+"F5.opPattern","COPY",BODY,{"derivedFrom":makeQuery(id+"F4.opPattern","COPY",BODY,{"derivedFrom":makeQuery(id+"F1.opExtrude","SWEPT_BODY",BODY,{"disambiguationData":[OSD([sQuery(id+"F0.wireOp",EDGE,"E0.bottom"),sQuery(id+"F0.wireOp",EDGE,"E0.top"),sQuery(id+"F0.wireOp",EDGE,"E0.left"),sQuery(id+"F0.wireOp",EDGE,"E0.right")])]}),"instanceName":"1"}),"instanceName":"1"}),"instanceName":"1"});
            var Q14;
            Q14=makeQuery(id+"F19.opPattern","COPY",BODY,{"derivedFrom":makeQuery(id+"F6.opPattern","COPY",BODY,{"derivedFrom":makeQuery(id+"F5.opPattern","COPY",BODY,{"derivedFrom":makeQuery(id+"F4.opPattern","COPY",BODY,{"derivedFrom":makeQuery(id+"F2.opPattern","COPY",BODY,{"derivedFrom":makeQuery(id+"F1.opExtrude","SWEPT_BODY",BODY,{"disambiguationData":[OSD([sQuery(id+"F0.wireOp",EDGE,"E0.bottom"),sQuery(id+"F0.wireOp",EDGE,"E0.top"),sQuery(id+"F0.wireOp",EDGE,"E0.left"),sQuery(id+"F0.wireOp",EDGE,"E0.right")])]}),"instanceName":"1"}),"instanceName":"1"}),"instanceName":"1"}),"instanceName":"1"}),"instanceName":"1"});
            var Q15;
            Q15=makeQuery(id+"F17.opPattern","COPY",BODY,{"derivedFrom":makeQuery(id+"F12.opPattern","COPY",BODY,{"derivedFrom":makeQuery(id+"F6.opPattern","COPY",BODY,{"derivedFrom":makeQuery(id+"F5.opPattern","COPY",BODY,{"derivedFrom":makeQuery(id+"F4.opPattern","COPY",BODY,{"derivedFrom":makeQuery(id+"F1.opExtrude","SWEPT_BODY",BODY,{"disambiguationData":[OSD([sQuery(id+"F0.wireOp",EDGE,"E0.bottom"),sQuery(id+"F0.wireOp",EDGE,"E0.top"),sQuery(id+"F0.wireOp",EDGE,"E0.left"),sQuery(id+"F0.wireOp",EDGE,"E0.right")])]}),"instanceName":"1"}),"instanceName":"1"}),"instanceName":"1"}),"instanceName":"1"}),"instanceName":"1"});
            var Q16;
            Q16=makeQuery(id+"F19.opPattern","COPY",BODY,{"derivedFrom":makeQuery(id+"F12.opPattern","COPY",BODY,{"derivedFrom":makeQuery(id+"F6.opPattern","COPY",BODY,{"derivedFrom":makeQuery(id+"F5.opPattern","COPY",BODY,{"derivedFrom":makeQuery(id+"F4.opPattern","COPY",BODY,{"derivedFrom":makeQuery(id+"F2.opPattern","COPY",BODY,{"derivedFrom":makeQuery(id+"F1.opExtrude","SWEPT_BODY",BODY,{"disambiguationData":[OSD([sQuery(id+"F0.wireOp",EDGE,"E0.bottom"),sQuery(id+"F0.wireOp",EDGE,"E0.top"),sQuery(id+"F0.wireOp",EDGE,"E0.left"),sQuery(id+"F0.wireOp",EDGE,"E0.right")])]}),"instanceName":"1"}),"instanceName":"1"}),"instanceName":"1"}),"instanceName":"1"}),"instanceName":"1"}),"instanceName":"1"});
            var Q17;
            Q17=makeQuery(id+"F19.opPattern","COPY",BODY,{"derivedFrom":makeQuery(id+"F12.opPattern","COPY",BODY,{"derivedFrom":makeQuery(id+"F6.opPattern","COPY",BODY,{"derivedFrom":makeQuery(id+"F5.opPattern","COPY",BODY,{"derivedFrom":makeQuery(id+"F4.opPattern","COPY",BODY,{"derivedFrom":makeQuery(id+"F1.opExtrude","SWEPT_BODY",BODY,{"disambiguationData":[OSD([sQuery(id+"F0.wireOp",EDGE,"E0.bottom"),sQuery(id+"F0.wireOp",EDGE,"E0.top"),sQuery(id+"F0.wireOp",EDGE,"E0.left"),sQuery(id+"F0.wireOp",EDGE,"E0.right")])]}),"instanceName":"1"}),"instanceName":"1"}),"instanceName":"1"}),"instanceName":"1"}),"instanceName":"1"});
            var Q18;
            Q18=makeQuery(id+"F18.opPattern","COPY",BODY,{"derivedFrom":makeQuery(id+"F17.opPattern","COPY",BODY,{"derivedFrom":makeQuery(id+"F8.opPattern","COPY",BODY,{"derivedFrom":makeQuery(id+"F5.opPattern","COPY",BODY,{"derivedFrom":makeQuery(id+"F4.opPattern","COPY",BODY,{"derivedFrom":makeQuery(id+"F1.opExtrude","SWEPT_BODY",BODY,{"disambiguationData":[OSD([sQuery(id+"F0.wireOp",EDGE,"E0.bottom"),sQuery(id+"F0.wireOp",EDGE,"E0.top"),sQuery(id+"F0.wireOp",EDGE,"E0.left"),sQuery(id+"F0.wireOp",EDGE,"E0.right")])]}),"instanceName":"1"}),"instanceName":"1"}),"instanceName":"1"}),"instanceName":"1"}),"instanceName":"1"});
            var Q19;
            Q19=makeQuery(id+"F23.opPattern","COPY",BODY,{"derivedFrom":makeQuery(id+"F19.opPattern","COPY",BODY,{"derivedFrom":makeQuery(id+"F15.opPattern","COPY",BODY,{"derivedFrom":makeQuery(id+"F12.opPattern","COPY",BODY,{"derivedFrom":makeQuery(id+"F6.opPattern","COPY",BODY,{"derivedFrom":makeQuery(id+"F5.opPattern","COPY",BODY,{"derivedFrom":makeQuery(id+"F4.opPattern","COPY",BODY,{"derivedFrom":makeQuery(id+"F2.opPattern","COPY",BODY,{"derivedFrom":makeQuery(id+"F1.opExtrude","SWEPT_BODY",BODY,{"disambiguationData":[OSD([sQuery(id+"F0.wireOp",EDGE,"E0.bottom"),sQuery(id+"F0.wireOp",EDGE,"E0.top"),sQuery(id+"F0.wireOp",EDGE,"E0.left"),sQuery(id+"F0.wireOp",EDGE,"E0.right")])]}),"instanceName":"1"}),"instanceName":"1"}),"instanceName":"1"}),"instanceName":"1"}),"instanceName":"1"}),"instanceName":"1"}),"instanceName":"1"}),"instanceName":"1"});
            var Q20;
            Q20=makeQuery(id+"F19.opPattern","COPY",BODY,{"derivedFrom":makeQuery(id+"F17.opPattern","COPY",BODY,{"derivedFrom":makeQuery(id+"F13.opPattern","COPY",BODY,{"derivedFrom":makeQuery(id+"F5.opPattern","COPY",BODY,{"derivedFrom":makeQuery(id+"F4.opPattern","COPY",BODY,{"derivedFrom":makeQuery(id+"F1.opExtrude","SWEPT_BODY",BODY,{"disambiguationData":[OSD([sQuery(id+"F0.wireOp",EDGE,"E0.bottom"),sQuery(id+"F0.wireOp",EDGE,"E0.top"),sQuery(id+"F0.wireOp",EDGE,"E0.left"),sQuery(id+"F0.wireOp",EDGE,"E0.right")])]}),"instanceName":"1"}),"instanceName":"1"}),"instanceName":"1"}),"instanceName":"1"}),"instanceName":"1"});
            var Q21;
            Q21=makeQuery(id+"F21.opPattern","COPY",BODY,{"derivedFrom":makeQuery(id+"F19.opPattern","COPY",BODY,{"derivedFrom":makeQuery(id+"F6.opPattern","COPY",BODY,{"derivedFrom":makeQuery(id+"F5.opPattern","COPY",BODY,{"derivedFrom":makeQuery(id+"F4.opPattern","COPY",BODY,{"derivedFrom":makeQuery(id+"F2.opPattern","COPY",BODY,{"derivedFrom":makeQuery(id+"F1.opExtrude","SWEPT_BODY",BODY,{"disambiguationData":[OSD([sQuery(id+"F0.wireOp",EDGE,"E0.bottom"),sQuery(id+"F0.wireOp",EDGE,"E0.top"),sQuery(id+"F0.wireOp",EDGE,"E0.left"),sQuery(id+"F0.wireOp",EDGE,"E0.right")])]}),"instanceName":"1"}),"instanceName":"1"}),"instanceName":"1"}),"instanceName":"1"}),"instanceName":"1"}),"instanceName":"1"});
            var Q22;
            Q22=makeQuery(id+"F23.opPattern","COPY",BODY,{"derivedFrom":makeQuery(id+"F19.opPattern","COPY",BODY,{"derivedFrom":makeQuery(id+"F17.opPattern","COPY",BODY,{"derivedFrom":makeQuery(id+"F13.opPattern","COPY",BODY,{"derivedFrom":makeQuery(id+"F5.opPattern","COPY",BODY,{"derivedFrom":makeQuery(id+"F4.opPattern","COPY",BODY,{"derivedFrom":makeQuery(id+"F1.opExtrude","SWEPT_BODY",BODY,{"disambiguationData":[OSD([sQuery(id+"F0.wireOp",EDGE,"E0.bottom"),sQuery(id+"F0.wireOp",EDGE,"E0.top"),sQuery(id+"F0.wireOp",EDGE,"E0.left"),sQuery(id+"F0.wireOp",EDGE,"E0.right")])]}),"instanceName":"1"}),"instanceName":"1"}),"instanceName":"1"}),"instanceName":"1"}),"instanceName":"1"}),"instanceName":"1"});
            var Q23;
            Q23=makeQuery(id+"F21.opPattern","COPY",BODY,{"derivedFrom":makeQuery(id+"F19.opPattern","COPY",BODY,{"derivedFrom":makeQuery(id+"F5.opPattern","COPY",BODY,{"derivedFrom":makeQuery(id+"F4.opPattern","COPY",BODY,{"derivedFrom":makeQuery(id+"F1.opExtrude","SWEPT_BODY",BODY,{"disambiguationData":[OSD([sQuery(id+"F0.wireOp",EDGE,"E0.bottom"),sQuery(id+"F0.wireOp",EDGE,"E0.top"),sQuery(id+"F0.wireOp",EDGE,"E0.left"),sQuery(id+"F0.wireOp",EDGE,"E0.right")])]}),"instanceName":"1"}),"instanceName":"1"}),"instanceName":"1"}),"instanceName":"1"});
            var Q24;
            Q24=makeQuery(id+"F18.opPattern","COPY",BODY,{"derivedFrom":makeQuery(id+"F17.opPattern","COPY",BODY,{"derivedFrom":makeQuery(id+"F8.opPattern","COPY",BODY,{"derivedFrom":makeQuery(id+"F5.opPattern","COPY",BODY,{"derivedFrom":makeQuery(id+"F4.opPattern","COPY",BODY,{"derivedFrom":makeQuery(id+"F2.opPattern","COPY",BODY,{"derivedFrom":makeQuery(id+"F1.opExtrude","SWEPT_BODY",BODY,{"disambiguationData":[OSD([sQuery(id+"F0.wireOp",EDGE,"E0.bottom"),sQuery(id+"F0.wireOp",EDGE,"E0.top"),sQuery(id+"F0.wireOp",EDGE,"E0.left"),sQuery(id+"F0.wireOp",EDGE,"E0.right")])]}),"instanceName":"1"}),"instanceName":"1"}),"instanceName":"1"}),"instanceName":"1"}),"instanceName":"1"}),"instanceName":"1"});
            var Q25;
            Q25=makeQuery(id+"F19.opPattern","COPY",BODY,{"derivedFrom":makeQuery(id+"F17.opPattern","COPY",BODY,{"derivedFrom":makeQuery(id+"F15.opPattern","COPY",BODY,{"derivedFrom":makeQuery(id+"F12.opPattern","COPY",BODY,{"derivedFrom":makeQuery(id+"F6.opPattern","COPY",BODY,{"derivedFrom":makeQuery(id+"F5.opPattern","COPY",BODY,{"derivedFrom":makeQuery(id+"F4.opPattern","COPY",BODY,{"derivedFrom":makeQuery(id+"F2.opPattern","COPY",BODY,{"derivedFrom":makeQuery(id+"F1.opExtrude","SWEPT_BODY",BODY,{"disambiguationData":[OSD([sQuery(id+"F0.wireOp",EDGE,"E0.bottom"),sQuery(id+"F0.wireOp",EDGE,"E0.top"),sQuery(id+"F0.wireOp",EDGE,"E0.left"),sQuery(id+"F0.wireOp",EDGE,"E0.right")])]}),"instanceName":"1"}),"instanceName":"1"}),"instanceName":"1"}),"instanceName":"1"}),"instanceName":"1"}),"instanceName":"1"}),"instanceName":"1"}),"instanceName":"1"});
            var Q26;
            Q26=makeQuery(id+"F19.opPattern","COPY",BODY,{"derivedFrom":makeQuery(id+"F13.opPattern","COPY",BODY,{"derivedFrom":makeQuery(id+"F5.opPattern","COPY",BODY,{"derivedFrom":makeQuery(id+"F4.opPattern","COPY",BODY,{"derivedFrom":makeQuery(id+"F1.opExtrude","SWEPT_BODY",BODY,{"disambiguationData":[OSD([sQuery(id+"F0.wireOp",EDGE,"E0.bottom"),sQuery(id+"F0.wireOp",EDGE,"E0.top"),sQuery(id+"F0.wireOp",EDGE,"E0.left"),sQuery(id+"F0.wireOp",EDGE,"E0.right")])]}),"instanceName":"1"}),"instanceName":"1"}),"instanceName":"1"}),"instanceName":"1"});
            var Q27;
            Q27=makeQuery(id+"F17.opPattern","COPY",BODY,{"derivedFrom":makeQuery(id+"F13.opPattern","COPY",BODY,{"derivedFrom":makeQuery(id+"F5.opPattern","COPY",BODY,{"derivedFrom":makeQuery(id+"F4.opPattern","COPY",BODY,{"derivedFrom":makeQuery(id+"F1.opExtrude","SWEPT_BODY",BODY,{"disambiguationData":[OSD([sQuery(id+"F0.wireOp",EDGE,"E0.bottom"),sQuery(id+"F0.wireOp",EDGE,"E0.top"),sQuery(id+"F0.wireOp",EDGE,"E0.left"),sQuery(id+"F0.wireOp",EDGE,"E0.right")])]}),"instanceName":"1"}),"instanceName":"1"}),"instanceName":"1"}),"instanceName":"1"});
            var Q28;
            Q28=makeQuery(id+"F17.opPattern","COPY",BODY,{"derivedFrom":makeQuery(id+"F6.opPattern","COPY",BODY,{"derivedFrom":makeQuery(id+"F5.opPattern","COPY",BODY,{"derivedFrom":makeQuery(id+"F4.opPattern","COPY",BODY,{"derivedFrom":makeQuery(id+"F2.opPattern","COPY",BODY,{"derivedFrom":makeQuery(id+"F1.opExtrude","SWEPT_BODY",BODY,{"disambiguationData":[OSD([sQuery(id+"F0.wireOp",EDGE,"E0.bottom"),sQuery(id+"F0.wireOp",EDGE,"E0.top"),sQuery(id+"F0.wireOp",EDGE,"E0.left"),sQuery(id+"F0.wireOp",EDGE,"E0.right")])]}),"instanceName":"1"}),"instanceName":"1"}),"instanceName":"1"}),"instanceName":"1"}),"instanceName":"1"});
            var Q29;
            Q29=makeQuery(id+"F23.opPattern","COPY",EDGE,{"derivedFrom":makeQuery(id+"F19.opPattern","COPY",EDGE,{"derivedFrom":makeQuery(id+"F17.opPattern","COPY",EDGE,{"derivedFrom":makeQuery(id+"F15.opPattern","COPY",EDGE,{"derivedFrom":makeQuery(id+"F12.opPattern","COPY",EDGE,{"derivedFrom":makeQuery(id+"F6.opPattern","COPY",EDGE,{"derivedFrom":makeQuery(id+"F5.opPattern","COPY",EDGE,{"derivedFrom":makeQuery(id+"F4.opPattern","COPY",EDGE,{"derivedFrom":makeQuery(id+"F2.opPattern","COPY",EDGE,{"derivedFrom":makeQuery(id+"F1.opExtrude","CAP_EDGE",EDGE,{"disambiguationData":[OSD([sQuery(id+"F0.wireOp",EDGE,"E0.bottom")])],"isStart":false}),"instanceName":"1"}),"instanceName":"1"}),"instanceName":"1"}),"instanceName":"1"}),"instanceName":"1"}),"instanceName":"1"}),"instanceName":"1"}),"instanceName":"1"}),"instanceName":"1"});
            transform(context, id + "F26", {"entities" : qUnion([Q0, Q1, Q2, Q3, Q4, Q5, Q6, Q7, Q8, Q9, Q10, Q11, Q12, Q13, Q14, Q15, Q16, Q17, Q18, Q19, Q20, Q21, Q22, Q23, Q24, Q25, Q26, Q27, Q28]), "transformType" : TransformType.TRANSLATION_DISTANCE, "transformDirection" : qUnion([Q29]), "distance" : 90 * mm, "makeCopy" : true});
        }
        {
            var Q0;
            Q0=makeQuery(id+"F24.opPattern","COPY",BODY,{"derivedFrom":makeQuery(id+"F23.opPattern","COPY",BODY,{"derivedFrom":makeQuery(id+"F21.opPattern","COPY",BODY,{"derivedFrom":makeQuery(id+"F19.opPattern","COPY",BODY,{"derivedFrom":makeQuery(id+"F17.opPattern","COPY",BODY,{"derivedFrom":makeQuery(id+"F12.opPattern","COPY",BODY,{"derivedFrom":makeQuery(id+"F6.opPattern","COPY",BODY,{"derivedFrom":makeQuery(id+"F5.opPattern","COPY",BODY,{"derivedFrom":makeQuery(id+"F4.opPattern","COPY",BODY,{"derivedFrom":makeQuery(id+"F2.opPattern","COPY",BODY,{"derivedFrom":makeQuery(id+"F1.opExtrude","SWEPT_BODY",BODY,{"disambiguationData":[OSD([sQuery(id+"F0.wireOp",EDGE,"E0.bottom"),sQuery(id+"F0.wireOp",EDGE,"E0.top"),sQuery(id+"F0.wireOp",EDGE,"E0.left"),sQuery(id+"F0.wireOp",EDGE,"E0.right")])]}),"instanceName":"1"}),"instanceName":"1"}),"instanceName":"1"}),"instanceName":"1"}),"instanceName":"1"}),"instanceName":"1"}),"instanceName":"1"}),"instanceName":"1"}),"instanceName":"1"}),"instanceName":"1"});
            var Q1;
            Q1=makeQuery(id+"F23.opPattern","COPY",BODY,{"derivedFrom":makeQuery(id+"F21.opPattern","COPY",BODY,{"derivedFrom":makeQuery(id+"F19.opPattern","COPY",BODY,{"derivedFrom":makeQuery(id+"F17.opPattern","COPY",BODY,{"derivedFrom":makeQuery(id+"F5.opPattern","COPY",BODY,{"derivedFrom":makeQuery(id+"F4.opPattern","COPY",BODY,{"derivedFrom":makeQuery(id+"F1.opExtrude","SWEPT_BODY",BODY,{"disambiguationData":[OSD([sQuery(id+"F0.wireOp",EDGE,"E0.bottom"),sQuery(id+"F0.wireOp",EDGE,"E0.top"),sQuery(id+"F0.wireOp",EDGE,"E0.left"),sQuery(id+"F0.wireOp",EDGE,"E0.right")])]}),"instanceName":"1"}),"instanceName":"1"}),"instanceName":"1"}),"instanceName":"1"}),"instanceName":"1"}),"instanceName":"1"});
            var Q2;
            Q2=makeQuery(id+"F24.opPattern","COPY",EDGE,{"derivedFrom":makeQuery(id+"F23.opPattern","COPY",EDGE,{"derivedFrom":makeQuery(id+"F21.opPattern","COPY",EDGE,{"derivedFrom":makeQuery(id+"F19.opPattern","COPY",EDGE,{"derivedFrom":makeQuery(id+"F17.opPattern","COPY",EDGE,{"derivedFrom":makeQuery(id+"F12.opPattern","COPY",EDGE,{"derivedFrom":makeQuery(id+"F6.opPattern","COPY",EDGE,{"derivedFrom":makeQuery(id+"F5.opPattern","COPY",EDGE,{"derivedFrom":makeQuery(id+"F4.opPattern","COPY",EDGE,{"derivedFrom":makeQuery(id+"F2.opPattern","COPY",EDGE,{"derivedFrom":makeQuery(id+"F1.opExtrude","CAP_EDGE",EDGE,{"disambiguationData":[OSD([sQuery(id+"F0.wireOp",EDGE,"E0.top")])],"isStart":false}),"instanceName":"1"}),"instanceName":"1"}),"instanceName":"1"}),"instanceName":"1"}),"instanceName":"1"}),"instanceName":"1"}),"instanceName":"1"}),"instanceName":"1"}),"instanceName":"1"}),"instanceName":"1"});
            transform(context, id + "F27", {"entities" : qUnion([Q0, Q1]), "transformType" : TransformType.TRANSLATION_DISTANCE, "transformDirection" : qUnion([Q2]), "distance" : 20 * mm, "makeCopy" : true});
        }
        {
            var Q0;
            Q0=makeQuery(id+"F23.opPattern","COPY",BODY,{"derivedFrom":makeQuery(id+"F19.opPattern","COPY",BODY,{"derivedFrom":makeQuery(id+"F15.opPattern","COPY",BODY,{"derivedFrom":makeQuery(id+"F12.opPattern","COPY",BODY,{"derivedFrom":makeQuery(id+"F6.opPattern","COPY",BODY,{"derivedFrom":makeQuery(id+"F5.opPattern","COPY",BODY,{"derivedFrom":makeQuery(id+"F4.opPattern","COPY",BODY,{"derivedFrom":makeQuery(id+"F2.opPattern","COPY",BODY,{"derivedFrom":makeQuery(id+"F1.opExtrude","SWEPT_BODY",BODY,{"disambiguationData":[OSD([sQuery(id+"F0.wireOp",EDGE,"E0.bottom"),sQuery(id+"F0.wireOp",EDGE,"E0.top"),sQuery(id+"F0.wireOp",EDGE,"E0.left"),sQuery(id+"F0.wireOp",EDGE,"E0.right")])]}),"instanceName":"1"}),"instanceName":"1"}),"instanceName":"1"}),"instanceName":"1"}),"instanceName":"1"}),"instanceName":"1"}),"instanceName":"1"}),"instanceName":"1"});
            var Q1;
            Q1=makeQuery(id+"F19.opPattern","COPY",BODY,{"derivedFrom":makeQuery(id+"F17.opPattern","COPY",BODY,{"derivedFrom":makeQuery(id+"F15.opPattern","COPY",BODY,{"derivedFrom":makeQuery(id+"F12.opPattern","COPY",BODY,{"derivedFrom":makeQuery(id+"F6.opPattern","COPY",BODY,{"derivedFrom":makeQuery(id+"F5.opPattern","COPY",BODY,{"derivedFrom":makeQuery(id+"F4.opPattern","COPY",BODY,{"derivedFrom":makeQuery(id+"F2.opPattern","COPY",BODY,{"derivedFrom":makeQuery(id+"F1.opExtrude","SWEPT_BODY",BODY,{"disambiguationData":[OSD([sQuery(id+"F0.wireOp",EDGE,"E0.bottom"),sQuery(id+"F0.wireOp",EDGE,"E0.top"),sQuery(id+"F0.wireOp",EDGE,"E0.left"),sQuery(id+"F0.wireOp",EDGE,"E0.right")])]}),"instanceName":"1"}),"instanceName":"1"}),"instanceName":"1"}),"instanceName":"1"}),"instanceName":"1"}),"instanceName":"1"}),"instanceName":"1"}),"instanceName":"1"});
            var Q2;
            Q2=makeQuery(id+"F23.opPattern","COPY",BODY,{"derivedFrom":makeQuery(id+"F19.opPattern","COPY",BODY,{"derivedFrom":makeQuery(id+"F17.opPattern","COPY",BODY,{"derivedFrom":makeQuery(id+"F13.opPattern","COPY",BODY,{"derivedFrom":makeQuery(id+"F5.opPattern","COPY",BODY,{"derivedFrom":makeQuery(id+"F4.opPattern","COPY",BODY,{"derivedFrom":makeQuery(id+"F1.opExtrude","SWEPT_BODY",BODY,{"disambiguationData":[OSD([sQuery(id+"F0.wireOp",EDGE,"E0.bottom"),sQuery(id+"F0.wireOp",EDGE,"E0.top"),sQuery(id+"F0.wireOp",EDGE,"E0.left"),sQuery(id+"F0.wireOp",EDGE,"E0.right")])]}),"instanceName":"1"}),"instanceName":"1"}),"instanceName":"1"}),"instanceName":"1"}),"instanceName":"1"}),"instanceName":"1"});
            var Q3;
            Q3=makeQuery(id+"F26.opPattern","COPY",BODY,{"derivedFrom":makeQuery(id+"F19.opPattern","COPY",BODY,{"derivedFrom":makeQuery(id+"F15.opPattern","COPY",BODY,{"derivedFrom":makeQuery(id+"F12.opPattern","COPY",BODY,{"derivedFrom":makeQuery(id+"F6.opPattern","COPY",BODY,{"derivedFrom":makeQuery(id+"F5.opPattern","COPY",BODY,{"derivedFrom":makeQuery(id+"F4.opPattern","COPY",BODY,{"derivedFrom":makeQuery(id+"F2.opPattern","COPY",BODY,{"derivedFrom":makeQuery(id+"F1.opExtrude","SWEPT_BODY",BODY,{"disambiguationData":[OSD([sQuery(id+"F0.wireOp",EDGE,"E0.bottom"),sQuery(id+"F0.wireOp",EDGE,"E0.top"),sQuery(id+"F0.wireOp",EDGE,"E0.left"),sQuery(id+"F0.wireOp",EDGE,"E0.right")])]}),"instanceName":"1"}),"instanceName":"1"}),"instanceName":"1"}),"instanceName":"1"}),"instanceName":"1"}),"instanceName":"1"}),"instanceName":"1"}),"instanceName":"1"});
            var Q4;
            Q4=makeQuery(id+"F19.opPattern","COPY",BODY,{"derivedFrom":makeQuery(id+"F17.opPattern","COPY",BODY,{"derivedFrom":makeQuery(id+"F13.opPattern","COPY",BODY,{"derivedFrom":makeQuery(id+"F5.opPattern","COPY",BODY,{"derivedFrom":makeQuery(id+"F4.opPattern","COPY",BODY,{"derivedFrom":makeQuery(id+"F1.opExtrude","SWEPT_BODY",BODY,{"disambiguationData":[OSD([sQuery(id+"F0.wireOp",EDGE,"E0.bottom"),sQuery(id+"F0.wireOp",EDGE,"E0.top"),sQuery(id+"F0.wireOp",EDGE,"E0.left"),sQuery(id+"F0.wireOp",EDGE,"E0.right")])]}),"instanceName":"1"}),"instanceName":"1"}),"instanceName":"1"}),"instanceName":"1"}),"instanceName":"1"});
            var Q5;
            Q5=makeQuery(id+"F26.opPattern","COPY",BODY,{"derivedFrom":makeQuery(id+"F19.opPattern","COPY",BODY,{"derivedFrom":makeQuery(id+"F17.opPattern","COPY",BODY,{"derivedFrom":makeQuery(id+"F15.opPattern","COPY",BODY,{"derivedFrom":makeQuery(id+"F12.opPattern","COPY",BODY,{"derivedFrom":makeQuery(id+"F6.opPattern","COPY",BODY,{"derivedFrom":makeQuery(id+"F5.opPattern","COPY",BODY,{"derivedFrom":makeQuery(id+"F4.opPattern","COPY",BODY,{"derivedFrom":makeQuery(id+"F2.opPattern","COPY",BODY,{"derivedFrom":makeQuery(id+"F1.opExtrude","SWEPT_BODY",BODY,{"disambiguationData":[OSD([sQuery(id+"F0.wireOp",EDGE,"E0.bottom"),sQuery(id+"F0.wireOp",EDGE,"E0.top"),sQuery(id+"F0.wireOp",EDGE,"E0.left"),sQuery(id+"F0.wireOp",EDGE,"E0.right")])]}),"instanceName":"1"}),"instanceName":"1"}),"instanceName":"1"}),"instanceName":"1"}),"instanceName":"1"}),"instanceName":"1"}),"instanceName":"1"}),"instanceName":"1"}),"instanceName":"1"});
            var Q6;
            Q6=makeQuery(id+"F26.opPattern","COPY",BODY,{"derivedFrom":makeQuery(id+"F17.opPattern","COPY",BODY,{"derivedFrom":makeQuery(id+"F13.opPattern","COPY",BODY,{"derivedFrom":makeQuery(id+"F5.opPattern","COPY",BODY,{"derivedFrom":makeQuery(id+"F4.opPattern","COPY",BODY,{"derivedFrom":makeQuery(id+"F1.opExtrude","SWEPT_BODY",BODY,{"disambiguationData":[OSD([sQuery(id+"F0.wireOp",EDGE,"E0.bottom"),sQuery(id+"F0.wireOp",EDGE,"E0.top"),sQuery(id+"F0.wireOp",EDGE,"E0.left"),sQuery(id+"F0.wireOp",EDGE,"E0.right")])]}),"instanceName":"1"}),"instanceName":"1"}),"instanceName":"1"}),"instanceName":"1"}),"instanceName":"1"});
            var Q7;
            Q7=makeQuery(id+"F26.opPattern","COPY",BODY,{"derivedFrom":makeQuery(id+"F23.opPattern","COPY",BODY,{"derivedFrom":makeQuery(id+"F19.opPattern","COPY",BODY,{"derivedFrom":makeQuery(id+"F15.opPattern","COPY",BODY,{"derivedFrom":makeQuery(id+"F12.opPattern","COPY",BODY,{"derivedFrom":makeQuery(id+"F6.opPattern","COPY",BODY,{"derivedFrom":makeQuery(id+"F5.opPattern","COPY",BODY,{"derivedFrom":makeQuery(id+"F4.opPattern","COPY",BODY,{"derivedFrom":makeQuery(id+"F2.opPattern","COPY",BODY,{"derivedFrom":makeQuery(id+"F1.opExtrude","SWEPT_BODY",BODY,{"disambiguationData":[OSD([sQuery(id+"F0.wireOp",EDGE,"E0.bottom"),sQuery(id+"F0.wireOp",EDGE,"E0.top"),sQuery(id+"F0.wireOp",EDGE,"E0.left"),sQuery(id+"F0.wireOp",EDGE,"E0.right")])]}),"instanceName":"1"}),"instanceName":"1"}),"instanceName":"1"}),"instanceName":"1"}),"instanceName":"1"}),"instanceName":"1"}),"instanceName":"1"}),"instanceName":"1"}),"instanceName":"1"});
            var Q8;
            Q8=makeQuery(id+"F19.opPattern","COPY",BODY,{"derivedFrom":makeQuery(id+"F13.opPattern","COPY",BODY,{"derivedFrom":makeQuery(id+"F5.opPattern","COPY",BODY,{"derivedFrom":makeQuery(id+"F4.opPattern","COPY",BODY,{"derivedFrom":makeQuery(id+"F1.opExtrude","SWEPT_BODY",BODY,{"disambiguationData":[OSD([sQuery(id+"F0.wireOp",EDGE,"E0.bottom"),sQuery(id+"F0.wireOp",EDGE,"E0.top"),sQuery(id+"F0.wireOp",EDGE,"E0.left"),sQuery(id+"F0.wireOp",EDGE,"E0.right")])]}),"instanceName":"1"}),"instanceName":"1"}),"instanceName":"1"}),"instanceName":"1"});
            var Q9;
            Q9=makeQuery(id+"F19.opPattern","COPY",BODY,{"derivedFrom":makeQuery(id+"F15.opPattern","COPY",BODY,{"derivedFrom":makeQuery(id+"F12.opPattern","COPY",BODY,{"derivedFrom":makeQuery(id+"F6.opPattern","COPY",BODY,{"derivedFrom":makeQuery(id+"F5.opPattern","COPY",BODY,{"derivedFrom":makeQuery(id+"F4.opPattern","COPY",BODY,{"derivedFrom":makeQuery(id+"F2.opPattern","COPY",BODY,{"derivedFrom":makeQuery(id+"F1.opExtrude","SWEPT_BODY",BODY,{"disambiguationData":[OSD([sQuery(id+"F0.wireOp",EDGE,"E0.bottom"),sQuery(id+"F0.wireOp",EDGE,"E0.top"),sQuery(id+"F0.wireOp",EDGE,"E0.left"),sQuery(id+"F0.wireOp",EDGE,"E0.right")])]}),"instanceName":"1"}),"instanceName":"1"}),"instanceName":"1"}),"instanceName":"1"}),"instanceName":"1"}),"instanceName":"1"}),"instanceName":"1"});
            var Q10;
            Q10=makeQuery(id+"F26.opPattern","COPY",BODY,{"derivedFrom":makeQuery(id+"F17.opPattern","COPY",BODY,{"derivedFrom":makeQuery(id+"F15.opPattern","COPY",BODY,{"derivedFrom":makeQuery(id+"F12.opPattern","COPY",BODY,{"derivedFrom":makeQuery(id+"F6.opPattern","COPY",BODY,{"derivedFrom":makeQuery(id+"F5.opPattern","COPY",BODY,{"derivedFrom":makeQuery(id+"F4.opPattern","COPY",BODY,{"derivedFrom":makeQuery(id+"F2.opPattern","COPY",BODY,{"derivedFrom":makeQuery(id+"F1.opExtrude","SWEPT_BODY",BODY,{"disambiguationData":[OSD([sQuery(id+"F0.wireOp",EDGE,"E0.bottom"),sQuery(id+"F0.wireOp",EDGE,"E0.top"),sQuery(id+"F0.wireOp",EDGE,"E0.left"),sQuery(id+"F0.wireOp",EDGE,"E0.right")])]}),"instanceName":"1"}),"instanceName":"1"}),"instanceName":"1"}),"instanceName":"1"}),"instanceName":"1"}),"instanceName":"1"}),"instanceName":"1"}),"instanceName":"1"});
            var Q11;
            Q11=makeQuery(id+"F26.opPattern","COPY",BODY,{"derivedFrom":makeQuery(id+"F19.opPattern","COPY",BODY,{"derivedFrom":makeQuery(id+"F13.opPattern","COPY",BODY,{"derivedFrom":makeQuery(id+"F5.opPattern","COPY",BODY,{"derivedFrom":makeQuery(id+"F4.opPattern","COPY",BODY,{"derivedFrom":makeQuery(id+"F1.opExtrude","SWEPT_BODY",BODY,{"disambiguationData":[OSD([sQuery(id+"F0.wireOp",EDGE,"E0.bottom"),sQuery(id+"F0.wireOp",EDGE,"E0.top"),sQuery(id+"F0.wireOp",EDGE,"E0.left"),sQuery(id+"F0.wireOp",EDGE,"E0.right")])]}),"instanceName":"1"}),"instanceName":"1"}),"instanceName":"1"}),"instanceName":"1"}),"instanceName":"1"});
            var Q12;
            Q12=makeQuery(id+"F26.opPattern","COPY",BODY,{"derivedFrom":makeQuery(id+"F19.opPattern","COPY",BODY,{"derivedFrom":makeQuery(id+"F17.opPattern","COPY",BODY,{"derivedFrom":makeQuery(id+"F13.opPattern","COPY",BODY,{"derivedFrom":makeQuery(id+"F5.opPattern","COPY",BODY,{"derivedFrom":makeQuery(id+"F4.opPattern","COPY",BODY,{"derivedFrom":makeQuery(id+"F1.opExtrude","SWEPT_BODY",BODY,{"disambiguationData":[OSD([sQuery(id+"F0.wireOp",EDGE,"E0.bottom"),sQuery(id+"F0.wireOp",EDGE,"E0.top"),sQuery(id+"F0.wireOp",EDGE,"E0.left"),sQuery(id+"F0.wireOp",EDGE,"E0.right")])]}),"instanceName":"1"}),"instanceName":"1"}),"instanceName":"1"}),"instanceName":"1"}),"instanceName":"1"}),"instanceName":"1"});
            var Q13;
            Q13=makeQuery(id+"F23.opPattern","COPY",BODY,{"derivedFrom":makeQuery(id+"F19.opPattern","COPY",BODY,{"derivedFrom":makeQuery(id+"F17.opPattern","COPY",BODY,{"derivedFrom":makeQuery(id+"F15.opPattern","COPY",BODY,{"derivedFrom":makeQuery(id+"F12.opPattern","COPY",BODY,{"derivedFrom":makeQuery(id+"F6.opPattern","COPY",BODY,{"derivedFrom":makeQuery(id+"F5.opPattern","COPY",BODY,{"derivedFrom":makeQuery(id+"F4.opPattern","COPY",BODY,{"derivedFrom":makeQuery(id+"F2.opPattern","COPY",BODY,{"derivedFrom":makeQuery(id+"F1.opExtrude","SWEPT_BODY",BODY,{"disambiguationData":[OSD([sQuery(id+"F0.wireOp",EDGE,"E0.bottom"),sQuery(id+"F0.wireOp",EDGE,"E0.top"),sQuery(id+"F0.wireOp",EDGE,"E0.left"),sQuery(id+"F0.wireOp",EDGE,"E0.right")])]}),"instanceName":"1"}),"instanceName":"1"}),"instanceName":"1"}),"instanceName":"1"}),"instanceName":"1"}),"instanceName":"1"}),"instanceName":"1"}),"instanceName":"1"}),"instanceName":"1"});
            var Q14;
            Q14=makeQuery(id+"F26.opPattern","COPY",BODY,{"derivedFrom":makeQuery(id+"F23.opPattern","COPY",BODY,{"derivedFrom":makeQuery(id+"F19.opPattern","COPY",BODY,{"derivedFrom":makeQuery(id+"F17.opPattern","COPY",BODY,{"derivedFrom":makeQuery(id+"F13.opPattern","COPY",BODY,{"derivedFrom":makeQuery(id+"F5.opPattern","COPY",BODY,{"derivedFrom":makeQuery(id+"F4.opPattern","COPY",BODY,{"derivedFrom":makeQuery(id+"F1.opExtrude","SWEPT_BODY",BODY,{"disambiguationData":[OSD([sQuery(id+"F0.wireOp",EDGE,"E0.bottom"),sQuery(id+"F0.wireOp",EDGE,"E0.top"),sQuery(id+"F0.wireOp",EDGE,"E0.left"),sQuery(id+"F0.wireOp",EDGE,"E0.right")])]}),"instanceName":"1"}),"instanceName":"1"}),"instanceName":"1"}),"instanceName":"1"}),"instanceName":"1"}),"instanceName":"1"}),"instanceName":"1"});
            var Q15;
            Q15=makeQuery(id+"F26.opPattern","COPY",EDGE,{"derivedFrom":makeQuery(id+"F23.opPattern","COPY",EDGE,{"derivedFrom":makeQuery(id+"F19.opPattern","COPY",EDGE,{"derivedFrom":makeQuery(id+"F17.opPattern","COPY",EDGE,{"derivedFrom":makeQuery(id+"F15.opPattern","COPY",EDGE,{"derivedFrom":makeQuery(id+"F12.opPattern","COPY",EDGE,{"derivedFrom":makeQuery(id+"F6.opPattern","COPY",EDGE,{"derivedFrom":makeQuery(id+"F5.opPattern","COPY",EDGE,{"derivedFrom":makeQuery(id+"F4.opPattern","COPY",EDGE,{"derivedFrom":makeQuery(id+"F2.opPattern","COPY",EDGE,{"derivedFrom":makeQuery(id+"F1.opExtrude","CAP_EDGE",EDGE,{"disambiguationData":[OSD([sQuery(id+"F0.wireOp",EDGE,"E0.right")])],"isStart":false}),"instanceName":"1"}),"instanceName":"1"}),"instanceName":"1"}),"instanceName":"1"}),"instanceName":"1"}),"instanceName":"1"}),"instanceName":"1"}),"instanceName":"1"}),"instanceName":"1"}),"instanceName":"1"});
            transform(context, id + "F28", {"entities" : qUnion([Q0, Q1, Q2, Q3, Q4, Q5, Q6, Q7, Q8, Q9, Q10, Q11, Q12, Q13, Q14]), "transformType" : TransformType.TRANSLATION_DISTANCE, "transformDirection" : qUnion([Q15]), "distance" : 10 * mm, "oppositeDirection" : true, "makeCopy" : true});
        }
        {
            var Q0;
            Q0=makeQuery(id+"F19.opPattern","COPY",BODY,{"derivedFrom":makeQuery(id+"F15.opPattern","COPY",BODY,{"derivedFrom":makeQuery(id+"F12.opPattern","COPY",BODY,{"derivedFrom":makeQuery(id+"F6.opPattern","COPY",BODY,{"derivedFrom":makeQuery(id+"F5.opPattern","COPY",BODY,{"derivedFrom":makeQuery(id+"F4.opPattern","COPY",BODY,{"derivedFrom":makeQuery(id+"F2.opPattern","COPY",BODY,{"derivedFrom":makeQuery(id+"F1.opExtrude","SWEPT_BODY",BODY,{"disambiguationData":[OSD([sQuery(id+"F0.wireOp",EDGE,"E0.bottom"),sQuery(id+"F0.wireOp",EDGE,"E0.top"),sQuery(id+"F0.wireOp",EDGE,"E0.left"),sQuery(id+"F0.wireOp",EDGE,"E0.right")])]}),"instanceName":"1"}),"instanceName":"1"}),"instanceName":"1"}),"instanceName":"1"}),"instanceName":"1"}),"instanceName":"1"}),"instanceName":"1"});
            var Q1;
            Q1=makeQuery(id+"F26.opPattern","COPY",BODY,{"derivedFrom":makeQuery(id+"F17.opPattern","COPY",BODY,{"derivedFrom":makeQuery(id+"F13.opPattern","COPY",BODY,{"derivedFrom":makeQuery(id+"F5.opPattern","COPY",BODY,{"derivedFrom":makeQuery(id+"F4.opPattern","COPY",BODY,{"derivedFrom":makeQuery(id+"F1.opExtrude","SWEPT_BODY",BODY,{"disambiguationData":[OSD([sQuery(id+"F0.wireOp",EDGE,"E0.bottom"),sQuery(id+"F0.wireOp",EDGE,"E0.top"),sQuery(id+"F0.wireOp",EDGE,"E0.left"),sQuery(id+"F0.wireOp",EDGE,"E0.right")])]}),"instanceName":"1"}),"instanceName":"1"}),"instanceName":"1"}),"instanceName":"1"}),"instanceName":"1"});
            var Q2;
            Q2=makeQuery(id+"F19.opPattern","COPY",BODY,{"derivedFrom":makeQuery(id+"F13.opPattern","COPY",BODY,{"derivedFrom":makeQuery(id+"F5.opPattern","COPY",BODY,{"derivedFrom":makeQuery(id+"F4.opPattern","COPY",BODY,{"derivedFrom":makeQuery(id+"F1.opExtrude","SWEPT_BODY",BODY,{"disambiguationData":[OSD([sQuery(id+"F0.wireOp",EDGE,"E0.bottom"),sQuery(id+"F0.wireOp",EDGE,"E0.top"),sQuery(id+"F0.wireOp",EDGE,"E0.left"),sQuery(id+"F0.wireOp",EDGE,"E0.right")])]}),"instanceName":"1"}),"instanceName":"1"}),"instanceName":"1"}),"instanceName":"1"});
            var Q3;
            Q3=makeQuery(id+"F28.opPattern","COPY",BODY,{"derivedFrom":makeQuery(id+"F23.opPattern","COPY",BODY,{"derivedFrom":makeQuery(id+"F19.opPattern","COPY",BODY,{"derivedFrom":makeQuery(id+"F17.opPattern","COPY",BODY,{"derivedFrom":makeQuery(id+"F15.opPattern","COPY",BODY,{"derivedFrom":makeQuery(id+"F12.opPattern","COPY",BODY,{"derivedFrom":makeQuery(id+"F6.opPattern","COPY",BODY,{"derivedFrom":makeQuery(id+"F5.opPattern","COPY",BODY,{"derivedFrom":makeQuery(id+"F4.opPattern","COPY",BODY,{"derivedFrom":makeQuery(id+"F2.opPattern","COPY",BODY,{"derivedFrom":makeQuery(id+"F1.opExtrude","SWEPT_BODY",BODY,{"disambiguationData":[OSD([sQuery(id+"F0.wireOp",EDGE,"E0.bottom"),sQuery(id+"F0.wireOp",EDGE,"E0.top"),sQuery(id+"F0.wireOp",EDGE,"E0.left"),sQuery(id+"F0.wireOp",EDGE,"E0.right")])]}),"instanceName":"1"}),"instanceName":"1"}),"instanceName":"1"}),"instanceName":"1"}),"instanceName":"1"}),"instanceName":"1"}),"instanceName":"1"}),"instanceName":"1"}),"instanceName":"1"}),"instanceName":"1"});
            var Q4;
            Q4=makeQuery(id+"F19.opPattern","COPY",BODY,{"derivedFrom":makeQuery(id+"F17.opPattern","COPY",BODY,{"derivedFrom":makeQuery(id+"F15.opPattern","COPY",BODY,{"derivedFrom":makeQuery(id+"F12.opPattern","COPY",BODY,{"derivedFrom":makeQuery(id+"F6.opPattern","COPY",BODY,{"derivedFrom":makeQuery(id+"F5.opPattern","COPY",BODY,{"derivedFrom":makeQuery(id+"F4.opPattern","COPY",BODY,{"derivedFrom":makeQuery(id+"F2.opPattern","COPY",BODY,{"derivedFrom":makeQuery(id+"F1.opExtrude","SWEPT_BODY",BODY,{"disambiguationData":[OSD([sQuery(id+"F0.wireOp",EDGE,"E0.bottom"),sQuery(id+"F0.wireOp",EDGE,"E0.top"),sQuery(id+"F0.wireOp",EDGE,"E0.left"),sQuery(id+"F0.wireOp",EDGE,"E0.right")])]}),"instanceName":"1"}),"instanceName":"1"}),"instanceName":"1"}),"instanceName":"1"}),"instanceName":"1"}),"instanceName":"1"}),"instanceName":"1"}),"instanceName":"1"});
            var Q5;
            Q5=makeQuery(id+"F28.opPattern","COPY",BODY,{"derivedFrom":makeQuery(id+"F23.opPattern","COPY",BODY,{"derivedFrom":makeQuery(id+"F19.opPattern","COPY",BODY,{"derivedFrom":makeQuery(id+"F17.opPattern","COPY",BODY,{"derivedFrom":makeQuery(id+"F13.opPattern","COPY",BODY,{"derivedFrom":makeQuery(id+"F5.opPattern","COPY",BODY,{"derivedFrom":makeQuery(id+"F4.opPattern","COPY",BODY,{"derivedFrom":makeQuery(id+"F1.opExtrude","SWEPT_BODY",BODY,{"disambiguationData":[OSD([sQuery(id+"F0.wireOp",EDGE,"E0.bottom"),sQuery(id+"F0.wireOp",EDGE,"E0.top"),sQuery(id+"F0.wireOp",EDGE,"E0.left"),sQuery(id+"F0.wireOp",EDGE,"E0.right")])]}),"instanceName":"1"}),"instanceName":"1"}),"instanceName":"1"}),"instanceName":"1"}),"instanceName":"1"}),"instanceName":"1"}),"instanceName":"1"});
            var Q6;
            Q6=makeQuery(id+"F28.opPattern","COPY",BODY,{"derivedFrom":makeQuery(id+"F23.opPattern","COPY",BODY,{"derivedFrom":makeQuery(id+"F19.opPattern","COPY",BODY,{"derivedFrom":makeQuery(id+"F15.opPattern","COPY",BODY,{"derivedFrom":makeQuery(id+"F12.opPattern","COPY",BODY,{"derivedFrom":makeQuery(id+"F6.opPattern","COPY",BODY,{"derivedFrom":makeQuery(id+"F5.opPattern","COPY",BODY,{"derivedFrom":makeQuery(id+"F4.opPattern","COPY",BODY,{"derivedFrom":makeQuery(id+"F2.opPattern","COPY",BODY,{"derivedFrom":makeQuery(id+"F1.opExtrude","SWEPT_BODY",BODY,{"disambiguationData":[OSD([sQuery(id+"F0.wireOp",EDGE,"E0.bottom"),sQuery(id+"F0.wireOp",EDGE,"E0.top"),sQuery(id+"F0.wireOp",EDGE,"E0.left"),sQuery(id+"F0.wireOp",EDGE,"E0.right")])]}),"instanceName":"1"}),"instanceName":"1"}),"instanceName":"1"}),"instanceName":"1"}),"instanceName":"1"}),"instanceName":"1"}),"instanceName":"1"}),"instanceName":"1"}),"instanceName":"1"});
            var Q7;
            Q7=makeQuery(id+"F19.opPattern","COPY",BODY,{"derivedFrom":makeQuery(id+"F17.opPattern","COPY",BODY,{"derivedFrom":makeQuery(id+"F13.opPattern","COPY",BODY,{"derivedFrom":makeQuery(id+"F5.opPattern","COPY",BODY,{"derivedFrom":makeQuery(id+"F4.opPattern","COPY",BODY,{"derivedFrom":makeQuery(id+"F1.opExtrude","SWEPT_BODY",BODY,{"disambiguationData":[OSD([sQuery(id+"F0.wireOp",EDGE,"E0.bottom"),sQuery(id+"F0.wireOp",EDGE,"E0.top"),sQuery(id+"F0.wireOp",EDGE,"E0.left"),sQuery(id+"F0.wireOp",EDGE,"E0.right")])]}),"instanceName":"1"}),"instanceName":"1"}),"instanceName":"1"}),"instanceName":"1"}),"instanceName":"1"});
            var Q8;
            Q8=makeQuery(id+"F28.opPattern","COPY",BODY,{"derivedFrom":makeQuery(id+"F19.opPattern","COPY",BODY,{"derivedFrom":makeQuery(id+"F17.opPattern","COPY",BODY,{"derivedFrom":makeQuery(id+"F15.opPattern","COPY",BODY,{"derivedFrom":makeQuery(id+"F12.opPattern","COPY",BODY,{"derivedFrom":makeQuery(id+"F6.opPattern","COPY",BODY,{"derivedFrom":makeQuery(id+"F5.opPattern","COPY",BODY,{"derivedFrom":makeQuery(id+"F4.opPattern","COPY",BODY,{"derivedFrom":makeQuery(id+"F2.opPattern","COPY",BODY,{"derivedFrom":makeQuery(id+"F1.opExtrude","SWEPT_BODY",BODY,{"disambiguationData":[OSD([sQuery(id+"F0.wireOp",EDGE,"E0.bottom"),sQuery(id+"F0.wireOp",EDGE,"E0.top"),sQuery(id+"F0.wireOp",EDGE,"E0.left"),sQuery(id+"F0.wireOp",EDGE,"E0.right")])]}),"instanceName":"1"}),"instanceName":"1"}),"instanceName":"1"}),"instanceName":"1"}),"instanceName":"1"}),"instanceName":"1"}),"instanceName":"1"}),"instanceName":"1"}),"instanceName":"1"});
            var Q9;
            Q9=makeQuery(id+"F23.opPattern","COPY",BODY,{"derivedFrom":makeQuery(id+"F19.opPattern","COPY",BODY,{"derivedFrom":makeQuery(id+"F17.opPattern","COPY",BODY,{"derivedFrom":makeQuery(id+"F13.opPattern","COPY",BODY,{"derivedFrom":makeQuery(id+"F5.opPattern","COPY",BODY,{"derivedFrom":makeQuery(id+"F4.opPattern","COPY",BODY,{"derivedFrom":makeQuery(id+"F1.opExtrude","SWEPT_BODY",BODY,{"disambiguationData":[OSD([sQuery(id+"F0.wireOp",EDGE,"E0.bottom"),sQuery(id+"F0.wireOp",EDGE,"E0.top"),sQuery(id+"F0.wireOp",EDGE,"E0.left"),sQuery(id+"F0.wireOp",EDGE,"E0.right")])]}),"instanceName":"1"}),"instanceName":"1"}),"instanceName":"1"}),"instanceName":"1"}),"instanceName":"1"}),"instanceName":"1"});
            var Q10;
            Q10=makeQuery(id+"F26.opPattern","COPY",BODY,{"derivedFrom":makeQuery(id+"F19.opPattern","COPY",BODY,{"derivedFrom":makeQuery(id+"F15.opPattern","COPY",BODY,{"derivedFrom":makeQuery(id+"F12.opPattern","COPY",BODY,{"derivedFrom":makeQuery(id+"F6.opPattern","COPY",BODY,{"derivedFrom":makeQuery(id+"F5.opPattern","COPY",BODY,{"derivedFrom":makeQuery(id+"F4.opPattern","COPY",BODY,{"derivedFrom":makeQuery(id+"F2.opPattern","COPY",BODY,{"derivedFrom":makeQuery(id+"F1.opExtrude","SWEPT_BODY",BODY,{"disambiguationData":[OSD([sQuery(id+"F0.wireOp",EDGE,"E0.bottom"),sQuery(id+"F0.wireOp",EDGE,"E0.top"),sQuery(id+"F0.wireOp",EDGE,"E0.left"),sQuery(id+"F0.wireOp",EDGE,"E0.right")])]}),"instanceName":"1"}),"instanceName":"1"}),"instanceName":"1"}),"instanceName":"1"}),"instanceName":"1"}),"instanceName":"1"}),"instanceName":"1"}),"instanceName":"1"});
            var Q11;
            Q11=makeQuery(id+"F26.opPattern","COPY",BODY,{"derivedFrom":makeQuery(id+"F19.opPattern","COPY",BODY,{"derivedFrom":makeQuery(id+"F17.opPattern","COPY",BODY,{"derivedFrom":makeQuery(id+"F13.opPattern","COPY",BODY,{"derivedFrom":makeQuery(id+"F5.opPattern","COPY",BODY,{"derivedFrom":makeQuery(id+"F4.opPattern","COPY",BODY,{"derivedFrom":makeQuery(id+"F1.opExtrude","SWEPT_BODY",BODY,{"disambiguationData":[OSD([sQuery(id+"F0.wireOp",EDGE,"E0.bottom"),sQuery(id+"F0.wireOp",EDGE,"E0.top"),sQuery(id+"F0.wireOp",EDGE,"E0.left"),sQuery(id+"F0.wireOp",EDGE,"E0.right")])]}),"instanceName":"1"}),"instanceName":"1"}),"instanceName":"1"}),"instanceName":"1"}),"instanceName":"1"}),"instanceName":"1"});
            var Q12;
            Q12=makeQuery(id+"F26.opPattern","COPY",BODY,{"derivedFrom":makeQuery(id+"F19.opPattern","COPY",BODY,{"derivedFrom":makeQuery(id+"F17.opPattern","COPY",BODY,{"derivedFrom":makeQuery(id+"F15.opPattern","COPY",BODY,{"derivedFrom":makeQuery(id+"F12.opPattern","COPY",BODY,{"derivedFrom":makeQuery(id+"F6.opPattern","COPY",BODY,{"derivedFrom":makeQuery(id+"F5.opPattern","COPY",BODY,{"derivedFrom":makeQuery(id+"F4.opPattern","COPY",BODY,{"derivedFrom":makeQuery(id+"F2.opPattern","COPY",BODY,{"derivedFrom":makeQuery(id+"F1.opExtrude","SWEPT_BODY",BODY,{"disambiguationData":[OSD([sQuery(id+"F0.wireOp",EDGE,"E0.bottom"),sQuery(id+"F0.wireOp",EDGE,"E0.top"),sQuery(id+"F0.wireOp",EDGE,"E0.left"),sQuery(id+"F0.wireOp",EDGE,"E0.right")])]}),"instanceName":"1"}),"instanceName":"1"}),"instanceName":"1"}),"instanceName":"1"}),"instanceName":"1"}),"instanceName":"1"}),"instanceName":"1"}),"instanceName":"1"}),"instanceName":"1"});
            var Q13;
            Q13=makeQuery(id+"F23.opPattern","COPY",BODY,{"derivedFrom":makeQuery(id+"F19.opPattern","COPY",BODY,{"derivedFrom":makeQuery(id+"F15.opPattern","COPY",BODY,{"derivedFrom":makeQuery(id+"F12.opPattern","COPY",BODY,{"derivedFrom":makeQuery(id+"F6.opPattern","COPY",BODY,{"derivedFrom":makeQuery(id+"F5.opPattern","COPY",BODY,{"derivedFrom":makeQuery(id+"F4.opPattern","COPY",BODY,{"derivedFrom":makeQuery(id+"F2.opPattern","COPY",BODY,{"derivedFrom":makeQuery(id+"F1.opExtrude","SWEPT_BODY",BODY,{"disambiguationData":[OSD([sQuery(id+"F0.wireOp",EDGE,"E0.bottom"),sQuery(id+"F0.wireOp",EDGE,"E0.top"),sQuery(id+"F0.wireOp",EDGE,"E0.left"),sQuery(id+"F0.wireOp",EDGE,"E0.right")])]}),"instanceName":"1"}),"instanceName":"1"}),"instanceName":"1"}),"instanceName":"1"}),"instanceName":"1"}),"instanceName":"1"}),"instanceName":"1"}),"instanceName":"1"});
            var Q14;
            Q14=makeQuery(id+"F28.opPattern","COPY",BODY,{"derivedFrom":makeQuery(id+"F26.opPattern","COPY",BODY,{"derivedFrom":makeQuery(id+"F17.opPattern","COPY",BODY,{"derivedFrom":makeQuery(id+"F13.opPattern","COPY",BODY,{"derivedFrom":makeQuery(id+"F5.opPattern","COPY",BODY,{"derivedFrom":makeQuery(id+"F4.opPattern","COPY",BODY,{"derivedFrom":makeQuery(id+"F1.opExtrude","SWEPT_BODY",BODY,{"disambiguationData":[OSD([sQuery(id+"F0.wireOp",EDGE,"E0.bottom"),sQuery(id+"F0.wireOp",EDGE,"E0.top"),sQuery(id+"F0.wireOp",EDGE,"E0.left"),sQuery(id+"F0.wireOp",EDGE,"E0.right")])]}),"instanceName":"1"}),"instanceName":"1"}),"instanceName":"1"}),"instanceName":"1"}),"instanceName":"1"}),"instanceName":"1"});
            var Q15;
            Q15=makeQuery(id+"F23.opPattern","COPY",BODY,{"derivedFrom":makeQuery(id+"F19.opPattern","COPY",BODY,{"derivedFrom":makeQuery(id+"F17.opPattern","COPY",BODY,{"derivedFrom":makeQuery(id+"F15.opPattern","COPY",BODY,{"derivedFrom":makeQuery(id+"F12.opPattern","COPY",BODY,{"derivedFrom":makeQuery(id+"F6.opPattern","COPY",BODY,{"derivedFrom":makeQuery(id+"F5.opPattern","COPY",BODY,{"derivedFrom":makeQuery(id+"F4.opPattern","COPY",BODY,{"derivedFrom":makeQuery(id+"F2.opPattern","COPY",BODY,{"derivedFrom":makeQuery(id+"F1.opExtrude","SWEPT_BODY",BODY,{"disambiguationData":[OSD([sQuery(id+"F0.wireOp",EDGE,"E0.bottom"),sQuery(id+"F0.wireOp",EDGE,"E0.top"),sQuery(id+"F0.wireOp",EDGE,"E0.left"),sQuery(id+"F0.wireOp",EDGE,"E0.right")])]}),"instanceName":"1"}),"instanceName":"1"}),"instanceName":"1"}),"instanceName":"1"}),"instanceName":"1"}),"instanceName":"1"}),"instanceName":"1"}),"instanceName":"1"}),"instanceName":"1"});
            var Q16;
            Q16=makeQuery(id+"F26.opPattern","COPY",BODY,{"derivedFrom":makeQuery(id+"F17.opPattern","COPY",BODY,{"derivedFrom":makeQuery(id+"F15.opPattern","COPY",BODY,{"derivedFrom":makeQuery(id+"F12.opPattern","COPY",BODY,{"derivedFrom":makeQuery(id+"F6.opPattern","COPY",BODY,{"derivedFrom":makeQuery(id+"F5.opPattern","COPY",BODY,{"derivedFrom":makeQuery(id+"F4.opPattern","COPY",BODY,{"derivedFrom":makeQuery(id+"F2.opPattern","COPY",BODY,{"derivedFrom":makeQuery(id+"F1.opExtrude","SWEPT_BODY",BODY,{"disambiguationData":[OSD([sQuery(id+"F0.wireOp",EDGE,"E0.bottom"),sQuery(id+"F0.wireOp",EDGE,"E0.top"),sQuery(id+"F0.wireOp",EDGE,"E0.left"),sQuery(id+"F0.wireOp",EDGE,"E0.right")])]}),"instanceName":"1"}),"instanceName":"1"}),"instanceName":"1"}),"instanceName":"1"}),"instanceName":"1"}),"instanceName":"1"}),"instanceName":"1"}),"instanceName":"1"});
            var Q17;
            Q17=makeQuery(id+"F26.opPattern","COPY",BODY,{"derivedFrom":makeQuery(id+"F19.opPattern","COPY",BODY,{"derivedFrom":makeQuery(id+"F13.opPattern","COPY",BODY,{"derivedFrom":makeQuery(id+"F5.opPattern","COPY",BODY,{"derivedFrom":makeQuery(id+"F4.opPattern","COPY",BODY,{"derivedFrom":makeQuery(id+"F1.opExtrude","SWEPT_BODY",BODY,{"disambiguationData":[OSD([sQuery(id+"F0.wireOp",EDGE,"E0.bottom"),sQuery(id+"F0.wireOp",EDGE,"E0.top"),sQuery(id+"F0.wireOp",EDGE,"E0.left"),sQuery(id+"F0.wireOp",EDGE,"E0.right")])]}),"instanceName":"1"}),"instanceName":"1"}),"instanceName":"1"}),"instanceName":"1"}),"instanceName":"1"});
            var Q18;
            Q18=makeQuery(id+"F28.opPattern","COPY",BODY,{"derivedFrom":makeQuery(id+"F19.opPattern","COPY",BODY,{"derivedFrom":makeQuery(id+"F17.opPattern","COPY",BODY,{"derivedFrom":makeQuery(id+"F13.opPattern","COPY",BODY,{"derivedFrom":makeQuery(id+"F5.opPattern","COPY",BODY,{"derivedFrom":makeQuery(id+"F4.opPattern","COPY",BODY,{"derivedFrom":makeQuery(id+"F1.opExtrude","SWEPT_BODY",BODY,{"disambiguationData":[OSD([sQuery(id+"F0.wireOp",EDGE,"E0.bottom"),sQuery(id+"F0.wireOp",EDGE,"E0.top"),sQuery(id+"F0.wireOp",EDGE,"E0.left"),sQuery(id+"F0.wireOp",EDGE,"E0.right")])]}),"instanceName":"1"}),"instanceName":"1"}),"instanceName":"1"}),"instanceName":"1"}),"instanceName":"1"}),"instanceName":"1"});
            var Q19;
            Q19=makeQuery(id+"F28.opPattern","COPY",BODY,{"derivedFrom":makeQuery(id+"F19.opPattern","COPY",BODY,{"derivedFrom":makeQuery(id+"F15.opPattern","COPY",BODY,{"derivedFrom":makeQuery(id+"F12.opPattern","COPY",BODY,{"derivedFrom":makeQuery(id+"F6.opPattern","COPY",BODY,{"derivedFrom":makeQuery(id+"F5.opPattern","COPY",BODY,{"derivedFrom":makeQuery(id+"F4.opPattern","COPY",BODY,{"derivedFrom":makeQuery(id+"F2.opPattern","COPY",BODY,{"derivedFrom":makeQuery(id+"F1.opExtrude","SWEPT_BODY",BODY,{"disambiguationData":[OSD([sQuery(id+"F0.wireOp",EDGE,"E0.bottom"),sQuery(id+"F0.wireOp",EDGE,"E0.top"),sQuery(id+"F0.wireOp",EDGE,"E0.left"),sQuery(id+"F0.wireOp",EDGE,"E0.right")])]}),"instanceName":"1"}),"instanceName":"1"}),"instanceName":"1"}),"instanceName":"1"}),"instanceName":"1"}),"instanceName":"1"}),"instanceName":"1"}),"instanceName":"1"});
            var Q20;
            Q20=makeQuery(id+"F26.opPattern","COPY",EDGE,{"derivedFrom":makeQuery(id+"F23.opPattern","COPY",EDGE,{"derivedFrom":makeQuery(id+"F19.opPattern","COPY",EDGE,{"derivedFrom":makeQuery(id+"F17.opPattern","COPY",EDGE,{"derivedFrom":makeQuery(id+"F15.opPattern","COPY",EDGE,{"derivedFrom":makeQuery(id+"F12.opPattern","COPY",EDGE,{"derivedFrom":makeQuery(id+"F6.opPattern","COPY",EDGE,{"derivedFrom":makeQuery(id+"F5.opPattern","COPY",EDGE,{"derivedFrom":makeQuery(id+"F4.opPattern","COPY",EDGE,{"derivedFrom":makeQuery(id+"F2.opPattern","COPY",EDGE,{"derivedFrom":makeQuery(id+"F1.opExtrude","CAP_EDGE",EDGE,{"disambiguationData":[OSD([sQuery(id+"F0.wireOp",EDGE,"E0.right")])],"isStart":false}),"instanceName":"1"}),"instanceName":"1"}),"instanceName":"1"}),"instanceName":"1"}),"instanceName":"1"}),"instanceName":"1"}),"instanceName":"1"}),"instanceName":"1"}),"instanceName":"1"}),"instanceName":"1"});
            transform(context, id + "F29", {"entities" : qUnion([Q0, Q1, Q2, Q3, Q4, Q5, Q6, Q7, Q8, Q9, Q10, Q11, Q12, Q13, Q14, Q15, Q16, Q17, Q18, Q19]), "transformType" : TransformType.TRANSLATION_DISTANCE, "transformDirection" : qUnion([Q20]), "distance" : 20 * mm, "oppositeDirection" : true, "makeCopy" : true});
        }
        {
            var Q0;
            Q0=makeQuery(id+"F29.opPattern","COPY",BODY,{"derivedFrom":makeQuery(id+"F23.opPattern","COPY",BODY,{"derivedFrom":makeQuery(id+"F19.opPattern","COPY",BODY,{"derivedFrom":makeQuery(id+"F15.opPattern","COPY",BODY,{"derivedFrom":makeQuery(id+"F12.opPattern","COPY",BODY,{"derivedFrom":makeQuery(id+"F6.opPattern","COPY",BODY,{"derivedFrom":makeQuery(id+"F5.opPattern","COPY",BODY,{"derivedFrom":makeQuery(id+"F4.opPattern","COPY",BODY,{"derivedFrom":makeQuery(id+"F2.opPattern","COPY",BODY,{"derivedFrom":makeQuery(id+"F1.opExtrude","SWEPT_BODY",BODY,{"disambiguationData":[OSD([sQuery(id+"F0.wireOp",EDGE,"E0.bottom"),sQuery(id+"F0.wireOp",EDGE,"E0.top"),sQuery(id+"F0.wireOp",EDGE,"E0.left"),sQuery(id+"F0.wireOp",EDGE,"E0.right")])]}),"instanceName":"1"}),"instanceName":"1"}),"instanceName":"1"}),"instanceName":"1"}),"instanceName":"1"}),"instanceName":"1"}),"instanceName":"1"}),"instanceName":"1"}),"instanceName":"1"});
            var Q1;
            Q1=makeQuery(id+"F29.opPattern","COPY",BODY,{"derivedFrom":makeQuery(id+"F23.opPattern","COPY",BODY,{"derivedFrom":makeQuery(id+"F19.opPattern","COPY",BODY,{"derivedFrom":makeQuery(id+"F17.opPattern","COPY",BODY,{"derivedFrom":makeQuery(id+"F13.opPattern","COPY",BODY,{"derivedFrom":makeQuery(id+"F5.opPattern","COPY",BODY,{"derivedFrom":makeQuery(id+"F4.opPattern","COPY",BODY,{"derivedFrom":makeQuery(id+"F1.opExtrude","SWEPT_BODY",BODY,{"disambiguationData":[OSD([sQuery(id+"F0.wireOp",EDGE,"E0.bottom"),sQuery(id+"F0.wireOp",EDGE,"E0.top"),sQuery(id+"F0.wireOp",EDGE,"E0.left"),sQuery(id+"F0.wireOp",EDGE,"E0.right")])]}),"instanceName":"1"}),"instanceName":"1"}),"instanceName":"1"}),"instanceName":"1"}),"instanceName":"1"}),"instanceName":"1"}),"instanceName":"1"});
            var Q2;
            Q2=makeQuery(id+"F29.opPattern","COPY",EDGE,{"derivedFrom":makeQuery(id+"F28.opPattern","COPY",EDGE,{"derivedFrom":makeQuery(id+"F26.opPattern","COPY",EDGE,{"derivedFrom":makeQuery(id+"F17.opPattern","COPY",EDGE,{"derivedFrom":makeQuery(id+"F13.opPattern","COPY",EDGE,{"derivedFrom":makeQuery(id+"F5.opPattern","COPY",EDGE,{"derivedFrom":makeQuery(id+"F4.opPattern","COPY",EDGE,{"derivedFrom":makeQuery(id+"F1.opExtrude","CAP_EDGE",EDGE,{"disambiguationData":[OSD([sQuery(id+"F0.wireOp",EDGE,"E0.right")])],"isStart":false}),"instanceName":"1"}),"instanceName":"1"}),"instanceName":"1"}),"instanceName":"1"}),"instanceName":"1"}),"instanceName":"1"}),"instanceName":"1"});
            transform(context, id + "F30", {"entities" : qUnion([Q0, Q1]), "transformType" : TransformType.TRANSLATION_DISTANCE, "transformDirection" : qUnion([Q2]), "distance" : 20 * mm, "oppositeDirection" : true, "makeCopy" : true});
        }
        {
            var Q0;
            Q0=makeQuery(id+"F4.opPattern","COPY",BODY,{"derivedFrom":makeQuery(id+"F2.opPattern","COPY",BODY,{"derivedFrom":makeQuery(id+"F1.opExtrude","SWEPT_BODY",BODY,{"disambiguationData":[OSD([sQuery(id+"F0.wireOp",EDGE,"E0.bottom"),sQuery(id+"F0.wireOp",EDGE,"E0.top"),sQuery(id+"F0.wireOp",EDGE,"E0.left"),sQuery(id+"F0.wireOp",EDGE,"E0.right")])]}),"instanceName":"1"}),"instanceName":"1"});
            var Q1;
            Q1=makeQuery(id+"F1.opExtrude","SWEPT_BODY",BODY,{"disambiguationData":[OSD([sQuery(id+"F0.wireOp",EDGE,"E0.bottom"),sQuery(id+"F0.wireOp",EDGE,"E0.top"),sQuery(id+"F0.wireOp",EDGE,"E0.left"),sQuery(id+"F0.wireOp",EDGE,"E0.right")])]});
            var Q2;
            Q2=makeQuery(id+"F4.opPattern","COPY",BODY,{"derivedFrom":makeQuery(id+"F1.opExtrude","SWEPT_BODY",BODY,{"disambiguationData":[OSD([sQuery(id+"F0.wireOp",EDGE,"E0.bottom"),sQuery(id+"F0.wireOp",EDGE,"E0.top"),sQuery(id+"F0.wireOp",EDGE,"E0.left"),sQuery(id+"F0.wireOp",EDGE,"E0.right")])]}),"instanceName":"1"});
            var Q3;
            Q3=makeQuery(id+"F5.opPattern","COPY",BODY,{"derivedFrom":makeQuery(id+"F1.opExtrude","SWEPT_BODY",BODY,{"disambiguationData":[OSD([sQuery(id+"F0.wireOp",EDGE,"E0.bottom"),sQuery(id+"F0.wireOp",EDGE,"E0.top"),sQuery(id+"F0.wireOp",EDGE,"E0.left"),sQuery(id+"F0.wireOp",EDGE,"E0.right")])]}),"instanceName":"1"});
            var Q4;
            Q4=makeQuery(id+"F5.opPattern","COPY",BODY,{"derivedFrom":makeQuery(id+"F2.opPattern","COPY",BODY,{"derivedFrom":makeQuery(id+"F1.opExtrude","SWEPT_BODY",BODY,{"disambiguationData":[OSD([sQuery(id+"F0.wireOp",EDGE,"E0.bottom"),sQuery(id+"F0.wireOp",EDGE,"E0.top"),sQuery(id+"F0.wireOp",EDGE,"E0.left"),sQuery(id+"F0.wireOp",EDGE,"E0.right")])]}),"instanceName":"1"}),"instanceName":"1"});
            var Q5;
            Q5=makeQuery(id+"F2.opPattern","COPY",BODY,{"derivedFrom":makeQuery(id+"F1.opExtrude","SWEPT_BODY",BODY,{"disambiguationData":[OSD([sQuery(id+"F0.wireOp",EDGE,"E0.bottom"),sQuery(id+"F0.wireOp",EDGE,"E0.top"),sQuery(id+"F0.wireOp",EDGE,"E0.left"),sQuery(id+"F0.wireOp",EDGE,"E0.right")])]}),"instanceName":"1"});
            var Q6;
            Q6=makeQuery(id+"F3.opPattern","COPY",EDGE,{"derivedFrom":makeQuery(id+"F2.opPattern","COPY",EDGE,{"derivedFrom":makeQuery(id+"F1.opExtrude","CAP_EDGE",EDGE,{"disambiguationData":[OSD([sQuery(id+"F0.wireOp",EDGE,"E0.right")])],"isStart":false}),"instanceName":"1"}),"instanceName":"1"});
            transform(context, id + "F31", {"entities" : qUnion([Q0, Q1, Q2, Q3, Q4, Q5]), "transformType" : TransformType.TRANSLATION_DISTANCE, "transformDirection" : qUnion([Q6]), "distance" : 40 * mm, "makeCopy" : true});
        }
        {
            var Q0;
            Q0=makeQuery(id+"F31.opPattern","COPY",BODY,{"derivedFrom":makeQuery(id+"F1.opExtrude","SWEPT_BODY",BODY,{"disambiguationData":[OSD([sQuery(id+"F0.wireOp",EDGE,"E0.bottom"),sQuery(id+"F0.wireOp",EDGE,"E0.top"),sQuery(id+"F0.wireOp",EDGE,"E0.left"),sQuery(id+"F0.wireOp",EDGE,"E0.right")])]}),"instanceName":"1"});
            var Q1;
            Q1=makeQuery(id+"F31.opPattern","COPY",EDGE,{"derivedFrom":makeQuery(id+"F1.opExtrude","CAP_EDGE",EDGE,{"disambiguationData":[OSD([sQuery(id+"F0.wireOp",EDGE,"E0.top")])],"isStart":false}),"instanceName":"1"});
            transform(context, id + "F32", {"entities" : qUnion([Q0]), "transformType" : TransformType.TRANSLATION_DISTANCE, "transformDirection" : qUnion([Q1]), "distance" : 10 * mm, "oppositeDirection" : true, "makeCopy" : true});
        }
        {
            var Q0;
            Q0=makeQuery(id+"F31.opPattern","COPY",BODY,{"derivedFrom":makeQuery(id+"F2.opPattern","COPY",BODY,{"derivedFrom":makeQuery(id+"F1.opExtrude","SWEPT_BODY",BODY,{"disambiguationData":[OSD([sQuery(id+"F0.wireOp",EDGE,"E0.bottom"),sQuery(id+"F0.wireOp",EDGE,"E0.top"),sQuery(id+"F0.wireOp",EDGE,"E0.left"),sQuery(id+"F0.wireOp",EDGE,"E0.right")])]}),"instanceName":"1"}),"instanceName":"1"});
            var Q1;
            Q1=makeQuery(id+"F31.opPattern","COPY",BODY,{"derivedFrom":makeQuery(id+"F1.opExtrude","SWEPT_BODY",BODY,{"disambiguationData":[OSD([sQuery(id+"F0.wireOp",EDGE,"E0.bottom"),sQuery(id+"F0.wireOp",EDGE,"E0.top"),sQuery(id+"F0.wireOp",EDGE,"E0.left"),sQuery(id+"F0.wireOp",EDGE,"E0.right")])]}),"instanceName":"1"});
            var Q2;
            Q2=makeQuery(id+"F31.opPattern","COPY",BODY,{"derivedFrom":makeQuery(id+"F4.opPattern","COPY",BODY,{"derivedFrom":makeQuery(id+"F1.opExtrude","SWEPT_BODY",BODY,{"disambiguationData":[OSD([sQuery(id+"F0.wireOp",EDGE,"E0.bottom"),sQuery(id+"F0.wireOp",EDGE,"E0.top"),sQuery(id+"F0.wireOp",EDGE,"E0.left"),sQuery(id+"F0.wireOp",EDGE,"E0.right")])]}),"instanceName":"1"}),"instanceName":"1"});
            var Q3;
            Q3=makeQuery(id+"F31.opPattern","COPY",EDGE,{"derivedFrom":makeQuery(id+"F5.opPattern","COPY",EDGE,{"derivedFrom":makeQuery(id+"F2.opPattern","COPY",EDGE,{"derivedFrom":makeQuery(id+"F1.opExtrude","CAP_EDGE",EDGE,{"disambiguationData":[OSD([sQuery(id+"F0.wireOp",EDGE,"E0.right")])],"isStart":false}),"instanceName":"1"}),"instanceName":"1"}),"instanceName":"1"});
            transform(context, id + "F33", {"entities" : qUnion([Q0, Q1, Q2]), "transformType" : TransformType.TRANSLATION_DISTANCE, "transformDirection" : qUnion([Q3]), "distance" : 10 * mm, "oppositeDirection" : true, "makeCopy" : true});
        }
        {
            var Q0;
            Q0=makeQuery(id+"F31.opPattern","COPY",BODY,{"derivedFrom":makeQuery(id+"F4.opPattern","COPY",BODY,{"derivedFrom":makeQuery(id+"F2.opPattern","COPY",BODY,{"derivedFrom":makeQuery(id+"F1.opExtrude","SWEPT_BODY",BODY,{"disambiguationData":[OSD([sQuery(id+"F0.wireOp",EDGE,"E0.bottom"),sQuery(id+"F0.wireOp",EDGE,"E0.top"),sQuery(id+"F0.wireOp",EDGE,"E0.left"),sQuery(id+"F0.wireOp",EDGE,"E0.right")])]}),"instanceName":"1"}),"instanceName":"1"}),"instanceName":"1"});
            var Q1;
            Q1=makeQuery(id+"F31.opPattern","COPY",BODY,{"derivedFrom":makeQuery(id+"F1.opExtrude","SWEPT_BODY",BODY,{"disambiguationData":[OSD([sQuery(id+"F0.wireOp",EDGE,"E0.bottom"),sQuery(id+"F0.wireOp",EDGE,"E0.top"),sQuery(id+"F0.wireOp",EDGE,"E0.left"),sQuery(id+"F0.wireOp",EDGE,"E0.right")])]}),"instanceName":"1"});
            var Q2;
            Q2=makeQuery(id+"F31.opPattern","COPY",BODY,{"derivedFrom":makeQuery(id+"F2.opPattern","COPY",BODY,{"derivedFrom":makeQuery(id+"F1.opExtrude","SWEPT_BODY",BODY,{"disambiguationData":[OSD([sQuery(id+"F0.wireOp",EDGE,"E0.bottom"),sQuery(id+"F0.wireOp",EDGE,"E0.top"),sQuery(id+"F0.wireOp",EDGE,"E0.left"),sQuery(id+"F0.wireOp",EDGE,"E0.right")])]}),"instanceName":"1"}),"instanceName":"1"});
            var Q3;
            Q3=makeQuery(id+"F31.opPattern","COPY",BODY,{"derivedFrom":makeQuery(id+"F5.opPattern","COPY",BODY,{"derivedFrom":makeQuery(id+"F1.opExtrude","SWEPT_BODY",BODY,{"disambiguationData":[OSD([sQuery(id+"F0.wireOp",EDGE,"E0.bottom"),sQuery(id+"F0.wireOp",EDGE,"E0.top"),sQuery(id+"F0.wireOp",EDGE,"E0.left"),sQuery(id+"F0.wireOp",EDGE,"E0.right")])]}),"instanceName":"1"}),"instanceName":"1"});
            var Q4;
            Q4=makeQuery(id+"F31.opPattern","COPY",BODY,{"derivedFrom":makeQuery(id+"F5.opPattern","COPY",BODY,{"derivedFrom":makeQuery(id+"F2.opPattern","COPY",BODY,{"derivedFrom":makeQuery(id+"F1.opExtrude","SWEPT_BODY",BODY,{"disambiguationData":[OSD([sQuery(id+"F0.wireOp",EDGE,"E0.bottom"),sQuery(id+"F0.wireOp",EDGE,"E0.top"),sQuery(id+"F0.wireOp",EDGE,"E0.left"),sQuery(id+"F0.wireOp",EDGE,"E0.right")])]}),"instanceName":"1"}),"instanceName":"1"}),"instanceName":"1"});
            var Q5;
            Q5=makeQuery(id+"F32.opPattern","COPY",BODY,{"derivedFrom":makeQuery(id+"F31.opPattern","COPY",BODY,{"derivedFrom":makeQuery(id+"F1.opExtrude","SWEPT_BODY",BODY,{"disambiguationData":[OSD([sQuery(id+"F0.wireOp",EDGE,"E0.bottom"),sQuery(id+"F0.wireOp",EDGE,"E0.top"),sQuery(id+"F0.wireOp",EDGE,"E0.left"),sQuery(id+"F0.wireOp",EDGE,"E0.right")])]}),"instanceName":"1"}),"instanceName":"1"});
            var Q6;
            Q6=makeQuery(id+"F31.opPattern","COPY",BODY,{"derivedFrom":makeQuery(id+"F4.opPattern","COPY",BODY,{"derivedFrom":makeQuery(id+"F1.opExtrude","SWEPT_BODY",BODY,{"disambiguationData":[OSD([sQuery(id+"F0.wireOp",EDGE,"E0.bottom"),sQuery(id+"F0.wireOp",EDGE,"E0.top"),sQuery(id+"F0.wireOp",EDGE,"E0.left"),sQuery(id+"F0.wireOp",EDGE,"E0.right")])]}),"instanceName":"1"}),"instanceName":"1"});
            var Q7;
            Q7=makeQuery(id+"F31.opPattern","COPY",EDGE,{"derivedFrom":makeQuery(id+"F5.opPattern","COPY",EDGE,{"derivedFrom":makeQuery(id+"F2.opPattern","COPY",EDGE,{"derivedFrom":makeQuery(id+"F1.opExtrude","CAP_EDGE",EDGE,{"disambiguationData":[OSD([sQuery(id+"F0.wireOp",EDGE,"E0.right")])],"isStart":false}),"instanceName":"1"}),"instanceName":"1"}),"instanceName":"1"});
            transform(context, id + "F34", {"entities" : qUnion([Q0, Q1, Q2, Q3, Q4, Q5, Q6]), "transformType" : TransformType.TRANSLATION_DISTANCE, "transformDirection" : qUnion([Q7]), "distance" : 10 * mm, "makeCopy" : true});
        }
        {
            var Q0;
            Q0=makeQuery(id+"F31.opPattern","COPY",BODY,{"derivedFrom":makeQuery(id+"F4.opPattern","COPY",BODY,{"derivedFrom":makeQuery(id+"F1.opExtrude","SWEPT_BODY",BODY,{"disambiguationData":[OSD([sQuery(id+"F0.wireOp",EDGE,"E0.bottom"),sQuery(id+"F0.wireOp",EDGE,"E0.top"),sQuery(id+"F0.wireOp",EDGE,"E0.left"),sQuery(id+"F0.wireOp",EDGE,"E0.right")])]}),"instanceName":"1"}),"instanceName":"1"});
            var Q1;
            Q1=makeQuery(id+"F34.opPattern","COPY",BODY,{"derivedFrom":makeQuery(id+"F31.opPattern","COPY",BODY,{"derivedFrom":makeQuery(id+"F5.opPattern","COPY",BODY,{"derivedFrom":makeQuery(id+"F1.opExtrude","SWEPT_BODY",BODY,{"disambiguationData":[OSD([sQuery(id+"F0.wireOp",EDGE,"E0.bottom"),sQuery(id+"F0.wireOp",EDGE,"E0.top"),sQuery(id+"F0.wireOp",EDGE,"E0.left"),sQuery(id+"F0.wireOp",EDGE,"E0.right")])]}),"instanceName":"1"}),"instanceName":"1"}),"instanceName":"1"});
            var Q2;
            Q2=makeQuery(id+"F31.opPattern","COPY",BODY,{"derivedFrom":makeQuery(id+"F1.opExtrude","SWEPT_BODY",BODY,{"disambiguationData":[OSD([sQuery(id+"F0.wireOp",EDGE,"E0.bottom"),sQuery(id+"F0.wireOp",EDGE,"E0.top"),sQuery(id+"F0.wireOp",EDGE,"E0.left"),sQuery(id+"F0.wireOp",EDGE,"E0.right")])]}),"instanceName":"1"});
            var Q3;
            Q3=makeQuery(id+"F32.opPattern","COPY",BODY,{"derivedFrom":makeQuery(id+"F31.opPattern","COPY",BODY,{"derivedFrom":makeQuery(id+"F1.opExtrude","SWEPT_BODY",BODY,{"disambiguationData":[OSD([sQuery(id+"F0.wireOp",EDGE,"E0.bottom"),sQuery(id+"F0.wireOp",EDGE,"E0.top"),sQuery(id+"F0.wireOp",EDGE,"E0.left"),sQuery(id+"F0.wireOp",EDGE,"E0.right")])]}),"instanceName":"1"}),"instanceName":"1"});
            var Q4;
            Q4=makeQuery(id+"F34.opPattern","COPY",BODY,{"derivedFrom":makeQuery(id+"F31.opPattern","COPY",BODY,{"derivedFrom":makeQuery(id+"F5.opPattern","COPY",BODY,{"derivedFrom":makeQuery(id+"F2.opPattern","COPY",BODY,{"derivedFrom":makeQuery(id+"F1.opExtrude","SWEPT_BODY",BODY,{"disambiguationData":[OSD([sQuery(id+"F0.wireOp",EDGE,"E0.bottom"),sQuery(id+"F0.wireOp",EDGE,"E0.top"),sQuery(id+"F0.wireOp",EDGE,"E0.left"),sQuery(id+"F0.wireOp",EDGE,"E0.right")])]}),"instanceName":"1"}),"instanceName":"1"}),"instanceName":"1"}),"instanceName":"1"});
            var Q5;
            Q5=makeQuery(id+"F31.opPattern","COPY",BODY,{"derivedFrom":makeQuery(id+"F5.opPattern","COPY",BODY,{"derivedFrom":makeQuery(id+"F1.opExtrude","SWEPT_BODY",BODY,{"disambiguationData":[OSD([sQuery(id+"F0.wireOp",EDGE,"E0.bottom"),sQuery(id+"F0.wireOp",EDGE,"E0.top"),sQuery(id+"F0.wireOp",EDGE,"E0.left"),sQuery(id+"F0.wireOp",EDGE,"E0.right")])]}),"instanceName":"1"}),"instanceName":"1"});
            var Q6;
            Q6=makeQuery(id+"F34.opPattern","COPY",BODY,{"derivedFrom":makeQuery(id+"F31.opPattern","COPY",BODY,{"derivedFrom":makeQuery(id+"F4.opPattern","COPY",BODY,{"derivedFrom":makeQuery(id+"F1.opExtrude","SWEPT_BODY",BODY,{"disambiguationData":[OSD([sQuery(id+"F0.wireOp",EDGE,"E0.bottom"),sQuery(id+"F0.wireOp",EDGE,"E0.top"),sQuery(id+"F0.wireOp",EDGE,"E0.left"),sQuery(id+"F0.wireOp",EDGE,"E0.right")])]}),"instanceName":"1"}),"instanceName":"1"}),"instanceName":"1"});
            var Q7;
            Q7=makeQuery(id+"F31.opPattern","COPY",BODY,{"derivedFrom":makeQuery(id+"F2.opPattern","COPY",BODY,{"derivedFrom":makeQuery(id+"F1.opExtrude","SWEPT_BODY",BODY,{"disambiguationData":[OSD([sQuery(id+"F0.wireOp",EDGE,"E0.bottom"),sQuery(id+"F0.wireOp",EDGE,"E0.top"),sQuery(id+"F0.wireOp",EDGE,"E0.left"),sQuery(id+"F0.wireOp",EDGE,"E0.right")])]}),"instanceName":"1"}),"instanceName":"1"});
            var Q8;
            Q8=makeQuery(id+"F34.opPattern","COPY",BODY,{"derivedFrom":makeQuery(id+"F31.opPattern","COPY",BODY,{"derivedFrom":makeQuery(id+"F2.opPattern","COPY",BODY,{"derivedFrom":makeQuery(id+"F1.opExtrude","SWEPT_BODY",BODY,{"disambiguationData":[OSD([sQuery(id+"F0.wireOp",EDGE,"E0.bottom"),sQuery(id+"F0.wireOp",EDGE,"E0.top"),sQuery(id+"F0.wireOp",EDGE,"E0.left"),sQuery(id+"F0.wireOp",EDGE,"E0.right")])]}),"instanceName":"1"}),"instanceName":"1"}),"instanceName":"1"});
            var Q9;
            Q9=makeQuery(id+"F34.opPattern","COPY",BODY,{"derivedFrom":makeQuery(id+"F31.opPattern","COPY",BODY,{"derivedFrom":makeQuery(id+"F4.opPattern","COPY",BODY,{"derivedFrom":makeQuery(id+"F2.opPattern","COPY",BODY,{"derivedFrom":makeQuery(id+"F1.opExtrude","SWEPT_BODY",BODY,{"disambiguationData":[OSD([sQuery(id+"F0.wireOp",EDGE,"E0.bottom"),sQuery(id+"F0.wireOp",EDGE,"E0.top"),sQuery(id+"F0.wireOp",EDGE,"E0.left"),sQuery(id+"F0.wireOp",EDGE,"E0.right")])]}),"instanceName":"1"}),"instanceName":"1"}),"instanceName":"1"}),"instanceName":"1"});
            var Q10;
            Q10=makeQuery(id+"F31.opPattern","COPY",BODY,{"derivedFrom":makeQuery(id+"F5.opPattern","COPY",BODY,{"derivedFrom":makeQuery(id+"F2.opPattern","COPY",BODY,{"derivedFrom":makeQuery(id+"F1.opExtrude","SWEPT_BODY",BODY,{"disambiguationData":[OSD([sQuery(id+"F0.wireOp",EDGE,"E0.bottom"),sQuery(id+"F0.wireOp",EDGE,"E0.top"),sQuery(id+"F0.wireOp",EDGE,"E0.left"),sQuery(id+"F0.wireOp",EDGE,"E0.right")])]}),"instanceName":"1"}),"instanceName":"1"}),"instanceName":"1"});
            var Q11;
            Q11=makeQuery(id+"F34.opPattern","COPY",BODY,{"derivedFrom":makeQuery(id+"F31.opPattern","COPY",BODY,{"derivedFrom":makeQuery(id+"F1.opExtrude","SWEPT_BODY",BODY,{"disambiguationData":[OSD([sQuery(id+"F0.wireOp",EDGE,"E0.bottom"),sQuery(id+"F0.wireOp",EDGE,"E0.top"),sQuery(id+"F0.wireOp",EDGE,"E0.left"),sQuery(id+"F0.wireOp",EDGE,"E0.right")])]}),"instanceName":"1"}),"instanceName":"1"});
            var Q12;
            Q12=makeQuery(id+"F31.opPattern","COPY",BODY,{"derivedFrom":makeQuery(id+"F4.opPattern","COPY",BODY,{"derivedFrom":makeQuery(id+"F2.opPattern","COPY",BODY,{"derivedFrom":makeQuery(id+"F1.opExtrude","SWEPT_BODY",BODY,{"disambiguationData":[OSD([sQuery(id+"F0.wireOp",EDGE,"E0.bottom"),sQuery(id+"F0.wireOp",EDGE,"E0.top"),sQuery(id+"F0.wireOp",EDGE,"E0.left"),sQuery(id+"F0.wireOp",EDGE,"E0.right")])]}),"instanceName":"1"}),"instanceName":"1"}),"instanceName":"1"});
            var Q13;
            Q13=makeQuery(id+"F34.opPattern","COPY",EDGE,{"derivedFrom":makeQuery(id+"F31.opPattern","COPY",EDGE,{"derivedFrom":makeQuery(id+"F5.opPattern","COPY",EDGE,{"derivedFrom":makeQuery(id+"F2.opPattern","COPY",EDGE,{"derivedFrom":makeQuery(id+"F1.opExtrude","CAP_EDGE",EDGE,{"disambiguationData":[OSD([sQuery(id+"F0.wireOp",EDGE,"E0.right")])],"isStart":false}),"instanceName":"1"}),"instanceName":"1"}),"instanceName":"1"}),"instanceName":"1"});
            transform(context, id + "F35", {"entities" : qUnion([Q0, Q1, Q2, Q3, Q4, Q5, Q6, Q7, Q8, Q9, Q10, Q11, Q12]), "transformType" : TransformType.TRANSLATION_DISTANCE, "transformDirection" : qUnion([Q13]), "distance" : 20 * mm, "makeCopy" : true});
        }
        {
            var Q0;
            Q0=makeQuery(id+"F35.opPattern","COPY",BODY,{"derivedFrom":makeQuery(id+"F34.opPattern","COPY",BODY,{"derivedFrom":makeQuery(id+"F31.opPattern","COPY",BODY,{"derivedFrom":makeQuery(id+"F5.opPattern","COPY",BODY,{"derivedFrom":makeQuery(id+"F1.opExtrude","SWEPT_BODY",BODY,{"disambiguationData":[OSD([sQuery(id+"F0.wireOp",EDGE,"E0.bottom"),sQuery(id+"F0.wireOp",EDGE,"E0.top"),sQuery(id+"F0.wireOp",EDGE,"E0.left"),sQuery(id+"F0.wireOp",EDGE,"E0.right")])]}),"instanceName":"1"}),"instanceName":"1"}),"instanceName":"1"}),"instanceName":"1"});
            var Q1;
            Q1=makeQuery(id+"F35.opPattern","COPY",BODY,{"derivedFrom":makeQuery(id+"F31.opPattern","COPY",BODY,{"derivedFrom":makeQuery(id+"F5.opPattern","COPY",BODY,{"derivedFrom":makeQuery(id+"F1.opExtrude","SWEPT_BODY",BODY,{"disambiguationData":[OSD([sQuery(id+"F0.wireOp",EDGE,"E0.bottom"),sQuery(id+"F0.wireOp",EDGE,"E0.top"),sQuery(id+"F0.wireOp",EDGE,"E0.left"),sQuery(id+"F0.wireOp",EDGE,"E0.right")])]}),"instanceName":"1"}),"instanceName":"1"}),"instanceName":"1"});
            var Q2;
            Q2=makeQuery(id+"F35.opPattern","COPY",BODY,{"derivedFrom":makeQuery(id+"F31.opPattern","COPY",BODY,{"derivedFrom":makeQuery(id+"F5.opPattern","COPY",BODY,{"derivedFrom":makeQuery(id+"F2.opPattern","COPY",BODY,{"derivedFrom":makeQuery(id+"F1.opExtrude","SWEPT_BODY",BODY,{"disambiguationData":[OSD([sQuery(id+"F0.wireOp",EDGE,"E0.bottom"),sQuery(id+"F0.wireOp",EDGE,"E0.top"),sQuery(id+"F0.wireOp",EDGE,"E0.left"),sQuery(id+"F0.wireOp",EDGE,"E0.right")])]}),"instanceName":"1"}),"instanceName":"1"}),"instanceName":"1"}),"instanceName":"1"});
            var Q3;
            Q3=makeQuery(id+"F35.opPattern","COPY",EDGE,{"derivedFrom":makeQuery(id+"F34.opPattern","COPY",EDGE,{"derivedFrom":makeQuery(id+"F31.opPattern","COPY",EDGE,{"derivedFrom":makeQuery(id+"F5.opPattern","COPY",EDGE,{"derivedFrom":makeQuery(id+"F2.opPattern","COPY",EDGE,{"derivedFrom":makeQuery(id+"F1.opExtrude","CAP_EDGE",EDGE,{"disambiguationData":[OSD([sQuery(id+"F0.wireOp",EDGE,"E0.top")])],"isStart":false}),"instanceName":"1"}),"instanceName":"1"}),"instanceName":"1"}),"instanceName":"1"}),"instanceName":"1"});
            transform(context, id + "F36", {"entities" : qUnion([Q0, Q1, Q2]), "transformType" : TransformType.TRANSLATION_DISTANCE, "transformDirection" : qUnion([Q3]), "distance" : 20 * mm, "makeCopy" : true});
        }
        {
            var Q0;
            Q0=makeQuery(id+"F35.opPattern","COPY",BODY,{"derivedFrom":makeQuery(id+"F34.opPattern","COPY",BODY,{"derivedFrom":makeQuery(id+"F31.opPattern","COPY",BODY,{"derivedFrom":makeQuery(id+"F5.opPattern","COPY",BODY,{"derivedFrom":makeQuery(id+"F1.opExtrude","SWEPT_BODY",BODY,{"disambiguationData":[OSD([sQuery(id+"F0.wireOp",EDGE,"E0.bottom"),sQuery(id+"F0.wireOp",EDGE,"E0.top"),sQuery(id+"F0.wireOp",EDGE,"E0.left"),sQuery(id+"F0.wireOp",EDGE,"E0.right")])]}),"instanceName":"1"}),"instanceName":"1"}),"instanceName":"1"}),"instanceName":"1"});
            var Q1;
            Q1=makeQuery(id+"F35.opPattern","COPY",BODY,{"derivedFrom":makeQuery(id+"F34.opPattern","COPY",BODY,{"derivedFrom":makeQuery(id+"F31.opPattern","COPY",BODY,{"derivedFrom":makeQuery(id+"F4.opPattern","COPY",BODY,{"derivedFrom":makeQuery(id+"F2.opPattern","COPY",BODY,{"derivedFrom":makeQuery(id+"F1.opExtrude","SWEPT_BODY",BODY,{"disambiguationData":[OSD([sQuery(id+"F0.wireOp",EDGE,"E0.bottom"),sQuery(id+"F0.wireOp",EDGE,"E0.top"),sQuery(id+"F0.wireOp",EDGE,"E0.left"),sQuery(id+"F0.wireOp",EDGE,"E0.right")])]}),"instanceName":"1"}),"instanceName":"1"}),"instanceName":"1"}),"instanceName":"1"}),"instanceName":"1"});
            var Q2;
            Q2=makeQuery(id+"F35.opPattern","COPY",BODY,{"derivedFrom":makeQuery(id+"F31.opPattern","COPY",BODY,{"derivedFrom":makeQuery(id+"F5.opPattern","COPY",BODY,{"derivedFrom":makeQuery(id+"F2.opPattern","COPY",BODY,{"derivedFrom":makeQuery(id+"F1.opExtrude","SWEPT_BODY",BODY,{"disambiguationData":[OSD([sQuery(id+"F0.wireOp",EDGE,"E0.bottom"),sQuery(id+"F0.wireOp",EDGE,"E0.top"),sQuery(id+"F0.wireOp",EDGE,"E0.left"),sQuery(id+"F0.wireOp",EDGE,"E0.right")])]}),"instanceName":"1"}),"instanceName":"1"}),"instanceName":"1"}),"instanceName":"1"});
            var Q3;
            Q3=makeQuery(id+"F36.opPattern","COPY",BODY,{"derivedFrom":makeQuery(id+"F35.opPattern","COPY",BODY,{"derivedFrom":makeQuery(id+"F31.opPattern","COPY",BODY,{"derivedFrom":makeQuery(id+"F5.opPattern","COPY",BODY,{"derivedFrom":makeQuery(id+"F1.opExtrude","SWEPT_BODY",BODY,{"disambiguationData":[OSD([sQuery(id+"F0.wireOp",EDGE,"E0.bottom"),sQuery(id+"F0.wireOp",EDGE,"E0.top"),sQuery(id+"F0.wireOp",EDGE,"E0.left"),sQuery(id+"F0.wireOp",EDGE,"E0.right")])]}),"instanceName":"1"}),"instanceName":"1"}),"instanceName":"1"}),"instanceName":"1"});
            var Q4;
            Q4=makeQuery(id+"F36.opPattern","COPY",BODY,{"derivedFrom":makeQuery(id+"F35.opPattern","COPY",BODY,{"derivedFrom":makeQuery(id+"F34.opPattern","COPY",BODY,{"derivedFrom":makeQuery(id+"F31.opPattern","COPY",BODY,{"derivedFrom":makeQuery(id+"F5.opPattern","COPY",BODY,{"derivedFrom":makeQuery(id+"F1.opExtrude","SWEPT_BODY",BODY,{"disambiguationData":[OSD([sQuery(id+"F0.wireOp",EDGE,"E0.bottom"),sQuery(id+"F0.wireOp",EDGE,"E0.top"),sQuery(id+"F0.wireOp",EDGE,"E0.left"),sQuery(id+"F0.wireOp",EDGE,"E0.right")])]}),"instanceName":"1"}),"instanceName":"1"}),"instanceName":"1"}),"instanceName":"1"}),"instanceName":"1"});
            var Q5;
            Q5=makeQuery(id+"F35.opPattern","COPY",BODY,{"derivedFrom":makeQuery(id+"F31.opPattern","COPY",BODY,{"derivedFrom":makeQuery(id+"F4.opPattern","COPY",BODY,{"derivedFrom":makeQuery(id+"F1.opExtrude","SWEPT_BODY",BODY,{"disambiguationData":[OSD([sQuery(id+"F0.wireOp",EDGE,"E0.bottom"),sQuery(id+"F0.wireOp",EDGE,"E0.top"),sQuery(id+"F0.wireOp",EDGE,"E0.left"),sQuery(id+"F0.wireOp",EDGE,"E0.right")])]}),"instanceName":"1"}),"instanceName":"1"}),"instanceName":"1"});
            var Q6;
            Q6=makeQuery(id+"F35.opPattern","COPY",BODY,{"derivedFrom":makeQuery(id+"F31.opPattern","COPY",BODY,{"derivedFrom":makeQuery(id+"F5.opPattern","COPY",BODY,{"derivedFrom":makeQuery(id+"F1.opExtrude","SWEPT_BODY",BODY,{"disambiguationData":[OSD([sQuery(id+"F0.wireOp",EDGE,"E0.bottom"),sQuery(id+"F0.wireOp",EDGE,"E0.top"),sQuery(id+"F0.wireOp",EDGE,"E0.left"),sQuery(id+"F0.wireOp",EDGE,"E0.right")])]}),"instanceName":"1"}),"instanceName":"1"}),"instanceName":"1"});
            var Q7;
            Q7=makeQuery(id+"F35.opPattern","COPY",BODY,{"derivedFrom":makeQuery(id+"F31.opPattern","COPY",BODY,{"derivedFrom":makeQuery(id+"F4.opPattern","COPY",BODY,{"derivedFrom":makeQuery(id+"F2.opPattern","COPY",BODY,{"derivedFrom":makeQuery(id+"F1.opExtrude","SWEPT_BODY",BODY,{"disambiguationData":[OSD([sQuery(id+"F0.wireOp",EDGE,"E0.bottom"),sQuery(id+"F0.wireOp",EDGE,"E0.top"),sQuery(id+"F0.wireOp",EDGE,"E0.left"),sQuery(id+"F0.wireOp",EDGE,"E0.right")])]}),"instanceName":"1"}),"instanceName":"1"}),"instanceName":"1"}),"instanceName":"1"});
            var Q8;
            Q8=makeQuery(id+"F35.opPattern","COPY",BODY,{"derivedFrom":makeQuery(id+"F34.opPattern","COPY",BODY,{"derivedFrom":makeQuery(id+"F31.opPattern","COPY",BODY,{"derivedFrom":makeQuery(id+"F5.opPattern","COPY",BODY,{"derivedFrom":makeQuery(id+"F2.opPattern","COPY",BODY,{"derivedFrom":makeQuery(id+"F1.opExtrude","SWEPT_BODY",BODY,{"disambiguationData":[OSD([sQuery(id+"F0.wireOp",EDGE,"E0.bottom"),sQuery(id+"F0.wireOp",EDGE,"E0.top"),sQuery(id+"F0.wireOp",EDGE,"E0.left"),sQuery(id+"F0.wireOp",EDGE,"E0.right")])]}),"instanceName":"1"}),"instanceName":"1"}),"instanceName":"1"}),"instanceName":"1"}),"instanceName":"1"});
            var Q9;
            Q9=makeQuery(id+"F36.opPattern","COPY",EDGE,{"derivedFrom":makeQuery(id+"F35.opPattern","COPY",EDGE,{"derivedFrom":makeQuery(id+"F34.opPattern","COPY",EDGE,{"derivedFrom":makeQuery(id+"F31.opPattern","COPY",EDGE,{"derivedFrom":makeQuery(id+"F5.opPattern","COPY",EDGE,{"derivedFrom":makeQuery(id+"F1.opExtrude","CAP_EDGE",EDGE,{"disambiguationData":[OSD([sQuery(id+"F0.wireOp",EDGE,"E0.right")])],"isStart":false}),"instanceName":"1"}),"instanceName":"1"}),"instanceName":"1"}),"instanceName":"1"}),"instanceName":"1"});
            transform(context, id + "F37", {"entities" : qUnion([Q0, Q1, Q2, Q3, Q4, Q5, Q6, Q7, Q8]), "transformType" : TransformType.TRANSLATION_DISTANCE, "transformDirection" : qUnion([Q9]), "distance" : 20 * mm, "makeCopy" : true});
        }
        {
            var Q0;
            Q0=makeQuery(id+"F35.opPattern","COPY",BODY,{"derivedFrom":makeQuery(id+"F34.opPattern","COPY",BODY,{"derivedFrom":makeQuery(id+"F31.opPattern","COPY",BODY,{"derivedFrom":makeQuery(id+"F4.opPattern","COPY",BODY,{"derivedFrom":makeQuery(id+"F2.opPattern","COPY",BODY,{"derivedFrom":makeQuery(id+"F1.opExtrude","SWEPT_BODY",BODY,{"disambiguationData":[OSD([sQuery(id+"F0.wireOp",EDGE,"E0.bottom"),sQuery(id+"F0.wireOp",EDGE,"E0.top"),sQuery(id+"F0.wireOp",EDGE,"E0.left"),sQuery(id+"F0.wireOp",EDGE,"E0.right")])]}),"instanceName":"1"}),"instanceName":"1"}),"instanceName":"1"}),"instanceName":"1"}),"instanceName":"1"});
            var Q1;
            Q1=makeQuery(id+"F37.opPattern","COPY",BODY,{"derivedFrom":makeQuery(id+"F35.opPattern","COPY",BODY,{"derivedFrom":makeQuery(id+"F31.opPattern","COPY",BODY,{"derivedFrom":makeQuery(id+"F5.opPattern","COPY",BODY,{"derivedFrom":makeQuery(id+"F1.opExtrude","SWEPT_BODY",BODY,{"disambiguationData":[OSD([sQuery(id+"F0.wireOp",EDGE,"E0.bottom"),sQuery(id+"F0.wireOp",EDGE,"E0.top"),sQuery(id+"F0.wireOp",EDGE,"E0.left"),sQuery(id+"F0.wireOp",EDGE,"E0.right")])]}),"instanceName":"1"}),"instanceName":"1"}),"instanceName":"1"}),"instanceName":"1"});
            var Q2;
            Q2=makeQuery(id+"F35.opPattern","COPY",BODY,{"derivedFrom":makeQuery(id+"F34.opPattern","COPY",BODY,{"derivedFrom":makeQuery(id+"F31.opPattern","COPY",BODY,{"derivedFrom":makeQuery(id+"F5.opPattern","COPY",BODY,{"derivedFrom":makeQuery(id+"F2.opPattern","COPY",BODY,{"derivedFrom":makeQuery(id+"F1.opExtrude","SWEPT_BODY",BODY,{"disambiguationData":[OSD([sQuery(id+"F0.wireOp",EDGE,"E0.bottom"),sQuery(id+"F0.wireOp",EDGE,"E0.top"),sQuery(id+"F0.wireOp",EDGE,"E0.left"),sQuery(id+"F0.wireOp",EDGE,"E0.right")])]}),"instanceName":"1"}),"instanceName":"1"}),"instanceName":"1"}),"instanceName":"1"}),"instanceName":"1"});
            var Q3;
            Q3=makeQuery(id+"F35.opPattern","COPY",BODY,{"derivedFrom":makeQuery(id+"F34.opPattern","COPY",BODY,{"derivedFrom":makeQuery(id+"F31.opPattern","COPY",BODY,{"derivedFrom":makeQuery(id+"F5.opPattern","COPY",BODY,{"derivedFrom":makeQuery(id+"F1.opExtrude","SWEPT_BODY",BODY,{"disambiguationData":[OSD([sQuery(id+"F0.wireOp",EDGE,"E0.bottom"),sQuery(id+"F0.wireOp",EDGE,"E0.top"),sQuery(id+"F0.wireOp",EDGE,"E0.left"),sQuery(id+"F0.wireOp",EDGE,"E0.right")])]}),"instanceName":"1"}),"instanceName":"1"}),"instanceName":"1"}),"instanceName":"1"});
            var Q4;
            Q4=makeQuery(id+"F37.opPattern","COPY",BODY,{"derivedFrom":makeQuery(id+"F35.opPattern","COPY",BODY,{"derivedFrom":makeQuery(id+"F31.opPattern","COPY",BODY,{"derivedFrom":makeQuery(id+"F5.opPattern","COPY",BODY,{"derivedFrom":makeQuery(id+"F2.opPattern","COPY",BODY,{"derivedFrom":makeQuery(id+"F1.opExtrude","SWEPT_BODY",BODY,{"disambiguationData":[OSD([sQuery(id+"F0.wireOp",EDGE,"E0.bottom"),sQuery(id+"F0.wireOp",EDGE,"E0.top"),sQuery(id+"F0.wireOp",EDGE,"E0.left"),sQuery(id+"F0.wireOp",EDGE,"E0.right")])]}),"instanceName":"1"}),"instanceName":"1"}),"instanceName":"1"}),"instanceName":"1"}),"instanceName":"1"});
            var Q5;
            Q5=makeQuery(id+"F37.opPattern","COPY",BODY,{"derivedFrom":makeQuery(id+"F35.opPattern","COPY",BODY,{"derivedFrom":makeQuery(id+"F34.opPattern","COPY",BODY,{"derivedFrom":makeQuery(id+"F31.opPattern","COPY",BODY,{"derivedFrom":makeQuery(id+"F5.opPattern","COPY",BODY,{"derivedFrom":makeQuery(id+"F1.opExtrude","SWEPT_BODY",BODY,{"disambiguationData":[OSD([sQuery(id+"F0.wireOp",EDGE,"E0.bottom"),sQuery(id+"F0.wireOp",EDGE,"E0.top"),sQuery(id+"F0.wireOp",EDGE,"E0.left"),sQuery(id+"F0.wireOp",EDGE,"E0.right")])]}),"instanceName":"1"}),"instanceName":"1"}),"instanceName":"1"}),"instanceName":"1"}),"instanceName":"1"});
            var Q6;
            Q6=makeQuery(id+"F37.opPattern","COPY",BODY,{"derivedFrom":makeQuery(id+"F35.opPattern","COPY",BODY,{"derivedFrom":makeQuery(id+"F31.opPattern","COPY",BODY,{"derivedFrom":makeQuery(id+"F4.opPattern","COPY",BODY,{"derivedFrom":makeQuery(id+"F2.opPattern","COPY",BODY,{"derivedFrom":makeQuery(id+"F1.opExtrude","SWEPT_BODY",BODY,{"disambiguationData":[OSD([sQuery(id+"F0.wireOp",EDGE,"E0.bottom"),sQuery(id+"F0.wireOp",EDGE,"E0.top"),sQuery(id+"F0.wireOp",EDGE,"E0.left"),sQuery(id+"F0.wireOp",EDGE,"E0.right")])]}),"instanceName":"1"}),"instanceName":"1"}),"instanceName":"1"}),"instanceName":"1"}),"instanceName":"1"});
            var Q7;
            Q7=makeQuery(id+"F37.opPattern","COPY",EDGE,{"derivedFrom":makeQuery(id+"F36.opPattern","COPY",EDGE,{"derivedFrom":makeQuery(id+"F35.opPattern","COPY",EDGE,{"derivedFrom":makeQuery(id+"F34.opPattern","COPY",EDGE,{"derivedFrom":makeQuery(id+"F31.opPattern","COPY",EDGE,{"derivedFrom":makeQuery(id+"F5.opPattern","COPY",EDGE,{"derivedFrom":makeQuery(id+"F1.opExtrude","CAP_EDGE",EDGE,{"disambiguationData":[OSD([sQuery(id+"F0.wireOp",EDGE,"E0.right")])],"isStart":false}),"instanceName":"1"}),"instanceName":"1"}),"instanceName":"1"}),"instanceName":"1"}),"instanceName":"1"}),"instanceName":"1"});
            transform(context, id + "F38", {"entities" : qUnion([Q0, Q1, Q2, Q3, Q4, Q5, Q6]), "transformType" : TransformType.TRANSLATION_DISTANCE, "transformDirection" : qUnion([Q7]), "distance" : 30 * mm, "makeCopy" : true});
        }
        {
            var Q0;
            Q0=makeQuery(id+"F28.opPattern","COPY",BODY,{"derivedFrom":makeQuery(id+"F26.opPattern","COPY",BODY,{"derivedFrom":makeQuery(id+"F17.opPattern","COPY",BODY,{"derivedFrom":makeQuery(id+"F13.opPattern","COPY",BODY,{"derivedFrom":makeQuery(id+"F5.opPattern","COPY",BODY,{"derivedFrom":makeQuery(id+"F4.opPattern","COPY",BODY,{"derivedFrom":makeQuery(id+"F1.opExtrude","SWEPT_BODY",BODY,{"disambiguationData":[OSD([sQuery(id+"F0.wireOp",EDGE,"E0.bottom"),sQuery(id+"F0.wireOp",EDGE,"E0.top"),sQuery(id+"F0.wireOp",EDGE,"E0.left"),sQuery(id+"F0.wireOp",EDGE,"E0.right")])]}),"instanceName":"1"}),"instanceName":"1"}),"instanceName":"1"}),"instanceName":"1"}),"instanceName":"1"}),"instanceName":"1"});
            var Q1;
            Q1=makeQuery(id+"F28.opPattern","COPY",BODY,{"derivedFrom":makeQuery(id+"F26.opPattern","COPY",BODY,{"derivedFrom":makeQuery(id+"F19.opPattern","COPY",BODY,{"derivedFrom":makeQuery(id+"F13.opPattern","COPY",BODY,{"derivedFrom":makeQuery(id+"F5.opPattern","COPY",BODY,{"derivedFrom":makeQuery(id+"F4.opPattern","COPY",BODY,{"derivedFrom":makeQuery(id+"F1.opExtrude","SWEPT_BODY",BODY,{"disambiguationData":[OSD([sQuery(id+"F0.wireOp",EDGE,"E0.bottom"),sQuery(id+"F0.wireOp",EDGE,"E0.top"),sQuery(id+"F0.wireOp",EDGE,"E0.left"),sQuery(id+"F0.wireOp",EDGE,"E0.right")])]}),"instanceName":"1"}),"instanceName":"1"}),"instanceName":"1"}),"instanceName":"1"}),"instanceName":"1"}),"instanceName":"1"});
            var Q2;
            Q2=makeQuery(id+"F26.opPattern","COPY",BODY,{"derivedFrom":makeQuery(id+"F19.opPattern","COPY",BODY,{"derivedFrom":makeQuery(id+"F17.opPattern","COPY",BODY,{"derivedFrom":makeQuery(id+"F12.opPattern","COPY",BODY,{"derivedFrom":makeQuery(id+"F6.opPattern","COPY",BODY,{"derivedFrom":makeQuery(id+"F5.opPattern","COPY",BODY,{"derivedFrom":makeQuery(id+"F4.opPattern","COPY",BODY,{"derivedFrom":makeQuery(id+"F1.opExtrude","SWEPT_BODY",BODY,{"disambiguationData":[OSD([sQuery(id+"F0.wireOp",EDGE,"E0.bottom"),sQuery(id+"F0.wireOp",EDGE,"E0.top"),sQuery(id+"F0.wireOp",EDGE,"E0.left"),sQuery(id+"F0.wireOp",EDGE,"E0.right")])]}),"instanceName":"1"}),"instanceName":"1"}),"instanceName":"1"}),"instanceName":"1"}),"instanceName":"1"}),"instanceName":"1"}),"instanceName":"1"});
            var Q3;
            Q3=makeQuery(id+"F26.opPattern","COPY",BODY,{"derivedFrom":makeQuery(id+"F19.opPattern","COPY",BODY,{"derivedFrom":makeQuery(id+"F12.opPattern","COPY",BODY,{"derivedFrom":makeQuery(id+"F6.opPattern","COPY",BODY,{"derivedFrom":makeQuery(id+"F5.opPattern","COPY",BODY,{"derivedFrom":makeQuery(id+"F4.opPattern","COPY",BODY,{"derivedFrom":makeQuery(id+"F2.opPattern","COPY",BODY,{"derivedFrom":makeQuery(id+"F1.opExtrude","SWEPT_BODY",BODY,{"disambiguationData":[OSD([sQuery(id+"F0.wireOp",EDGE,"E0.bottom"),sQuery(id+"F0.wireOp",EDGE,"E0.top"),sQuery(id+"F0.wireOp",EDGE,"E0.left"),sQuery(id+"F0.wireOp",EDGE,"E0.right")])]}),"instanceName":"1"}),"instanceName":"1"}),"instanceName":"1"}),"instanceName":"1"}),"instanceName":"1"}),"instanceName":"1"}),"instanceName":"1"});
            var Q4;
            Q4=makeQuery(id+"F26.opPattern","COPY",BODY,{"derivedFrom":makeQuery(id+"F19.opPattern","COPY",BODY,{"derivedFrom":makeQuery(id+"F17.opPattern","COPY",BODY,{"derivedFrom":makeQuery(id+"F13.opPattern","COPY",BODY,{"derivedFrom":makeQuery(id+"F5.opPattern","COPY",BODY,{"derivedFrom":makeQuery(id+"F4.opPattern","COPY",BODY,{"derivedFrom":makeQuery(id+"F1.opExtrude","SWEPT_BODY",BODY,{"disambiguationData":[OSD([sQuery(id+"F0.wireOp",EDGE,"E0.bottom"),sQuery(id+"F0.wireOp",EDGE,"E0.top"),sQuery(id+"F0.wireOp",EDGE,"E0.left"),sQuery(id+"F0.wireOp",EDGE,"E0.right")])]}),"instanceName":"1"}),"instanceName":"1"}),"instanceName":"1"}),"instanceName":"1"}),"instanceName":"1"}),"instanceName":"1"});
            var Q5;
            Q5=makeQuery(id+"F26.opPattern","COPY",BODY,{"derivedFrom":makeQuery(id+"F17.opPattern","COPY",BODY,{"derivedFrom":makeQuery(id+"F12.opPattern","COPY",BODY,{"derivedFrom":makeQuery(id+"F6.opPattern","COPY",BODY,{"derivedFrom":makeQuery(id+"F5.opPattern","COPY",BODY,{"derivedFrom":makeQuery(id+"F4.opPattern","COPY",BODY,{"derivedFrom":makeQuery(id+"F2.opPattern","COPY",BODY,{"derivedFrom":makeQuery(id+"F1.opExtrude","SWEPT_BODY",BODY,{"disambiguationData":[OSD([sQuery(id+"F0.wireOp",EDGE,"E0.bottom"),sQuery(id+"F0.wireOp",EDGE,"E0.top"),sQuery(id+"F0.wireOp",EDGE,"E0.left"),sQuery(id+"F0.wireOp",EDGE,"E0.right")])]}),"instanceName":"1"}),"instanceName":"1"}),"instanceName":"1"}),"instanceName":"1"}),"instanceName":"1"}),"instanceName":"1"}),"instanceName":"1"});
            var Q6;
            Q6=makeQuery(id+"F26.opPattern","COPY",BODY,{"derivedFrom":makeQuery(id+"F19.opPattern","COPY",BODY,{"derivedFrom":makeQuery(id+"F13.opPattern","COPY",BODY,{"derivedFrom":makeQuery(id+"F5.opPattern","COPY",BODY,{"derivedFrom":makeQuery(id+"F4.opPattern","COPY",BODY,{"derivedFrom":makeQuery(id+"F1.opExtrude","SWEPT_BODY",BODY,{"disambiguationData":[OSD([sQuery(id+"F0.wireOp",EDGE,"E0.bottom"),sQuery(id+"F0.wireOp",EDGE,"E0.top"),sQuery(id+"F0.wireOp",EDGE,"E0.left"),sQuery(id+"F0.wireOp",EDGE,"E0.right")])]}),"instanceName":"1"}),"instanceName":"1"}),"instanceName":"1"}),"instanceName":"1"}),"instanceName":"1"});
            var Q7;
            Q7=makeQuery(id+"F26.opPattern","COPY",BODY,{"derivedFrom":makeQuery(id+"F19.opPattern","COPY",BODY,{"derivedFrom":makeQuery(id+"F12.opPattern","COPY",BODY,{"derivedFrom":makeQuery(id+"F6.opPattern","COPY",BODY,{"derivedFrom":makeQuery(id+"F5.opPattern","COPY",BODY,{"derivedFrom":makeQuery(id+"F4.opPattern","COPY",BODY,{"derivedFrom":makeQuery(id+"F1.opExtrude","SWEPT_BODY",BODY,{"disambiguationData":[OSD([sQuery(id+"F0.wireOp",EDGE,"E0.bottom"),sQuery(id+"F0.wireOp",EDGE,"E0.top"),sQuery(id+"F0.wireOp",EDGE,"E0.left"),sQuery(id+"F0.wireOp",EDGE,"E0.right")])]}),"instanceName":"1"}),"instanceName":"1"}),"instanceName":"1"}),"instanceName":"1"}),"instanceName":"1"}),"instanceName":"1"});
            var Q8;
            Q8=makeQuery(id+"F26.opPattern","COPY",BODY,{"derivedFrom":makeQuery(id+"F17.opPattern","COPY",BODY,{"derivedFrom":makeQuery(id+"F15.opPattern","COPY",BODY,{"derivedFrom":makeQuery(id+"F12.opPattern","COPY",BODY,{"derivedFrom":makeQuery(id+"F6.opPattern","COPY",BODY,{"derivedFrom":makeQuery(id+"F5.opPattern","COPY",BODY,{"derivedFrom":makeQuery(id+"F4.opPattern","COPY",BODY,{"derivedFrom":makeQuery(id+"F2.opPattern","COPY",BODY,{"derivedFrom":makeQuery(id+"F1.opExtrude","SWEPT_BODY",BODY,{"disambiguationData":[OSD([sQuery(id+"F0.wireOp",EDGE,"E0.bottom"),sQuery(id+"F0.wireOp",EDGE,"E0.top"),sQuery(id+"F0.wireOp",EDGE,"E0.left"),sQuery(id+"F0.wireOp",EDGE,"E0.right")])]}),"instanceName":"1"}),"instanceName":"1"}),"instanceName":"1"}),"instanceName":"1"}),"instanceName":"1"}),"instanceName":"1"}),"instanceName":"1"}),"instanceName":"1"});
            var Q9;
            Q9=makeQuery(id+"F23.opPattern","COPY",BODY,{"derivedFrom":makeQuery(id+"F19.opPattern","COPY",BODY,{"derivedFrom":makeQuery(id+"F17.opPattern","COPY",BODY,{"derivedFrom":makeQuery(id+"F12.opPattern","COPY",BODY,{"derivedFrom":makeQuery(id+"F6.opPattern","COPY",BODY,{"derivedFrom":makeQuery(id+"F5.opPattern","COPY",BODY,{"derivedFrom":makeQuery(id+"F4.opPattern","COPY",BODY,{"derivedFrom":makeQuery(id+"F2.opPattern","COPY",BODY,{"derivedFrom":makeQuery(id+"F1.opExtrude","SWEPT_BODY",BODY,{"disambiguationData":[OSD([sQuery(id+"F0.wireOp",EDGE,"E0.bottom"),sQuery(id+"F0.wireOp",EDGE,"E0.top"),sQuery(id+"F0.wireOp",EDGE,"E0.left"),sQuery(id+"F0.wireOp",EDGE,"E0.right")])]}),"instanceName":"1"}),"instanceName":"1"}),"instanceName":"1"}),"instanceName":"1"}),"instanceName":"1"}),"instanceName":"1"}),"instanceName":"1"}),"instanceName":"1"});
            var Q10;
            Q10=makeQuery(id+"F28.opPattern","COPY",BODY,{"derivedFrom":makeQuery(id+"F26.opPattern","COPY",BODY,{"derivedFrom":makeQuery(id+"F19.opPattern","COPY",BODY,{"derivedFrom":makeQuery(id+"F15.opPattern","COPY",BODY,{"derivedFrom":makeQuery(id+"F12.opPattern","COPY",BODY,{"derivedFrom":makeQuery(id+"F6.opPattern","COPY",BODY,{"derivedFrom":makeQuery(id+"F5.opPattern","COPY",BODY,{"derivedFrom":makeQuery(id+"F4.opPattern","COPY",BODY,{"derivedFrom":makeQuery(id+"F2.opPattern","COPY",BODY,{"derivedFrom":makeQuery(id+"F1.opExtrude","SWEPT_BODY",BODY,{"disambiguationData":[OSD([sQuery(id+"F0.wireOp",EDGE,"E0.bottom"),sQuery(id+"F0.wireOp",EDGE,"E0.top"),sQuery(id+"F0.wireOp",EDGE,"E0.left"),sQuery(id+"F0.wireOp",EDGE,"E0.right")])]}),"instanceName":"1"}),"instanceName":"1"}),"instanceName":"1"}),"instanceName":"1"}),"instanceName":"1"}),"instanceName":"1"}),"instanceName":"1"}),"instanceName":"1"}),"instanceName":"1"});
            var Q11;
            Q11=makeQuery(id+"F23.opPattern","COPY",BODY,{"derivedFrom":makeQuery(id+"F19.opPattern","COPY",BODY,{"derivedFrom":makeQuery(id+"F17.opPattern","COPY",BODY,{"derivedFrom":makeQuery(id+"F15.opPattern","COPY",BODY,{"derivedFrom":makeQuery(id+"F12.opPattern","COPY",BODY,{"derivedFrom":makeQuery(id+"F6.opPattern","COPY",BODY,{"derivedFrom":makeQuery(id+"F5.opPattern","COPY",BODY,{"derivedFrom":makeQuery(id+"F4.opPattern","COPY",BODY,{"derivedFrom":makeQuery(id+"F2.opPattern","COPY",BODY,{"derivedFrom":makeQuery(id+"F1.opExtrude","SWEPT_BODY",BODY,{"disambiguationData":[OSD([sQuery(id+"F0.wireOp",EDGE,"E0.bottom"),sQuery(id+"F0.wireOp",EDGE,"E0.top"),sQuery(id+"F0.wireOp",EDGE,"E0.left"),sQuery(id+"F0.wireOp",EDGE,"E0.right")])]}),"instanceName":"1"}),"instanceName":"1"}),"instanceName":"1"}),"instanceName":"1"}),"instanceName":"1"}),"instanceName":"1"}),"instanceName":"1"}),"instanceName":"1"}),"instanceName":"1"});
            var Q12;
            Q12=makeQuery(id+"F26.opPattern","COPY",BODY,{"derivedFrom":makeQuery(id+"F19.opPattern","COPY",BODY,{"derivedFrom":makeQuery(id+"F6.opPattern","COPY",BODY,{"derivedFrom":makeQuery(id+"F5.opPattern","COPY",BODY,{"derivedFrom":makeQuery(id+"F4.opPattern","COPY",BODY,{"derivedFrom":makeQuery(id+"F1.opExtrude","SWEPT_BODY",BODY,{"disambiguationData":[OSD([sQuery(id+"F0.wireOp",EDGE,"E0.bottom"),sQuery(id+"F0.wireOp",EDGE,"E0.top"),sQuery(id+"F0.wireOp",EDGE,"E0.left"),sQuery(id+"F0.wireOp",EDGE,"E0.right")])]}),"instanceName":"1"}),"instanceName":"1"}),"instanceName":"1"}),"instanceName":"1"}),"instanceName":"1"});
            var Q13;
            Q13=makeQuery(id+"F26.opPattern","COPY",BODY,{"derivedFrom":makeQuery(id+"F17.opPattern","COPY",BODY,{"derivedFrom":makeQuery(id+"F12.opPattern","COPY",BODY,{"derivedFrom":makeQuery(id+"F6.opPattern","COPY",BODY,{"derivedFrom":makeQuery(id+"F5.opPattern","COPY",BODY,{"derivedFrom":makeQuery(id+"F4.opPattern","COPY",BODY,{"derivedFrom":makeQuery(id+"F1.opExtrude","SWEPT_BODY",BODY,{"disambiguationData":[OSD([sQuery(id+"F0.wireOp",EDGE,"E0.bottom"),sQuery(id+"F0.wireOp",EDGE,"E0.top"),sQuery(id+"F0.wireOp",EDGE,"E0.left"),sQuery(id+"F0.wireOp",EDGE,"E0.right")])]}),"instanceName":"1"}),"instanceName":"1"}),"instanceName":"1"}),"instanceName":"1"}),"instanceName":"1"}),"instanceName":"1"});
            var Q14;
            Q14=makeQuery(id+"F26.opPattern","COPY",BODY,{"derivedFrom":makeQuery(id+"F19.opPattern","COPY",BODY,{"derivedFrom":makeQuery(id+"F15.opPattern","COPY",BODY,{"derivedFrom":makeQuery(id+"F12.opPattern","COPY",BODY,{"derivedFrom":makeQuery(id+"F6.opPattern","COPY",BODY,{"derivedFrom":makeQuery(id+"F5.opPattern","COPY",BODY,{"derivedFrom":makeQuery(id+"F4.opPattern","COPY",BODY,{"derivedFrom":makeQuery(id+"F2.opPattern","COPY",BODY,{"derivedFrom":makeQuery(id+"F1.opExtrude","SWEPT_BODY",BODY,{"disambiguationData":[OSD([sQuery(id+"F0.wireOp",EDGE,"E0.bottom"),sQuery(id+"F0.wireOp",EDGE,"E0.top"),sQuery(id+"F0.wireOp",EDGE,"E0.left"),sQuery(id+"F0.wireOp",EDGE,"E0.right")])]}),"instanceName":"1"}),"instanceName":"1"}),"instanceName":"1"}),"instanceName":"1"}),"instanceName":"1"}),"instanceName":"1"}),"instanceName":"1"}),"instanceName":"1"});
            var Q15;
            Q15=makeQuery(id+"F26.opPattern","COPY",BODY,{"derivedFrom":makeQuery(id+"F19.opPattern","COPY",BODY,{"derivedFrom":makeQuery(id+"F6.opPattern","COPY",BODY,{"derivedFrom":makeQuery(id+"F5.opPattern","COPY",BODY,{"derivedFrom":makeQuery(id+"F4.opPattern","COPY",BODY,{"derivedFrom":makeQuery(id+"F2.opPattern","COPY",BODY,{"derivedFrom":makeQuery(id+"F1.opExtrude","SWEPT_BODY",BODY,{"disambiguationData":[OSD([sQuery(id+"F0.wireOp",EDGE,"E0.bottom"),sQuery(id+"F0.wireOp",EDGE,"E0.top"),sQuery(id+"F0.wireOp",EDGE,"E0.left"),sQuery(id+"F0.wireOp",EDGE,"E0.right")])]}),"instanceName":"1"}),"instanceName":"1"}),"instanceName":"1"}),"instanceName":"1"}),"instanceName":"1"}),"instanceName":"1"});
            var Q16;
            Q16=makeQuery(id+"F28.opPattern","COPY",BODY,{"derivedFrom":makeQuery(id+"F26.opPattern","COPY",BODY,{"derivedFrom":makeQuery(id+"F17.opPattern","COPY",BODY,{"derivedFrom":makeQuery(id+"F15.opPattern","COPY",BODY,{"derivedFrom":makeQuery(id+"F12.opPattern","COPY",BODY,{"derivedFrom":makeQuery(id+"F6.opPattern","COPY",BODY,{"derivedFrom":makeQuery(id+"F5.opPattern","COPY",BODY,{"derivedFrom":makeQuery(id+"F4.opPattern","COPY",BODY,{"derivedFrom":makeQuery(id+"F2.opPattern","COPY",BODY,{"derivedFrom":makeQuery(id+"F1.opExtrude","SWEPT_BODY",BODY,{"disambiguationData":[OSD([sQuery(id+"F0.wireOp",EDGE,"E0.bottom"),sQuery(id+"F0.wireOp",EDGE,"E0.top"),sQuery(id+"F0.wireOp",EDGE,"E0.left"),sQuery(id+"F0.wireOp",EDGE,"E0.right")])]}),"instanceName":"1"}),"instanceName":"1"}),"instanceName":"1"}),"instanceName":"1"}),"instanceName":"1"}),"instanceName":"1"}),"instanceName":"1"}),"instanceName":"1"}),"instanceName":"1"});
            var Q17;
            Q17=makeQuery(id+"F29.opPattern","COPY",BODY,{"derivedFrom":makeQuery(id+"F26.opPattern","COPY",BODY,{"derivedFrom":makeQuery(id+"F19.opPattern","COPY",BODY,{"derivedFrom":makeQuery(id+"F15.opPattern","COPY",BODY,{"derivedFrom":makeQuery(id+"F12.opPattern","COPY",BODY,{"derivedFrom":makeQuery(id+"F6.opPattern","COPY",BODY,{"derivedFrom":makeQuery(id+"F5.opPattern","COPY",BODY,{"derivedFrom":makeQuery(id+"F4.opPattern","COPY",BODY,{"derivedFrom":makeQuery(id+"F2.opPattern","COPY",BODY,{"derivedFrom":makeQuery(id+"F1.opExtrude","SWEPT_BODY",BODY,{"disambiguationData":[OSD([sQuery(id+"F0.wireOp",EDGE,"E0.bottom"),sQuery(id+"F0.wireOp",EDGE,"E0.top"),sQuery(id+"F0.wireOp",EDGE,"E0.left"),sQuery(id+"F0.wireOp",EDGE,"E0.right")])]}),"instanceName":"1"}),"instanceName":"1"}),"instanceName":"1"}),"instanceName":"1"}),"instanceName":"1"}),"instanceName":"1"}),"instanceName":"1"}),"instanceName":"1"}),"instanceName":"1"});
            var Q18;
            Q18=makeQuery(id+"F26.opPattern","COPY",BODY,{"derivedFrom":makeQuery(id+"F17.opPattern","COPY",BODY,{"derivedFrom":makeQuery(id+"F13.opPattern","COPY",BODY,{"derivedFrom":makeQuery(id+"F5.opPattern","COPY",BODY,{"derivedFrom":makeQuery(id+"F4.opPattern","COPY",BODY,{"derivedFrom":makeQuery(id+"F1.opExtrude","SWEPT_BODY",BODY,{"disambiguationData":[OSD([sQuery(id+"F0.wireOp",EDGE,"E0.bottom"),sQuery(id+"F0.wireOp",EDGE,"E0.top"),sQuery(id+"F0.wireOp",EDGE,"E0.left"),sQuery(id+"F0.wireOp",EDGE,"E0.right")])]}),"instanceName":"1"}),"instanceName":"1"}),"instanceName":"1"}),"instanceName":"1"}),"instanceName":"1"});
            var Q19;
            Q19=makeQuery(id+"F29.opPattern","COPY",BODY,{"derivedFrom":makeQuery(id+"F26.opPattern","COPY",BODY,{"derivedFrom":makeQuery(id+"F17.opPattern","COPY",BODY,{"derivedFrom":makeQuery(id+"F15.opPattern","COPY",BODY,{"derivedFrom":makeQuery(id+"F12.opPattern","COPY",BODY,{"derivedFrom":makeQuery(id+"F6.opPattern","COPY",BODY,{"derivedFrom":makeQuery(id+"F5.opPattern","COPY",BODY,{"derivedFrom":makeQuery(id+"F4.opPattern","COPY",BODY,{"derivedFrom":makeQuery(id+"F2.opPattern","COPY",BODY,{"derivedFrom":makeQuery(id+"F1.opExtrude","SWEPT_BODY",BODY,{"disambiguationData":[OSD([sQuery(id+"F0.wireOp",EDGE,"E0.bottom"),sQuery(id+"F0.wireOp",EDGE,"E0.top"),sQuery(id+"F0.wireOp",EDGE,"E0.left"),sQuery(id+"F0.wireOp",EDGE,"E0.right")])]}),"instanceName":"1"}),"instanceName":"1"}),"instanceName":"1"}),"instanceName":"1"}),"instanceName":"1"}),"instanceName":"1"}),"instanceName":"1"}),"instanceName":"1"}),"instanceName":"1"});
            var Q20;
            Q20=makeQuery(id+"F26.opPattern","COPY",EDGE,{"derivedFrom":makeQuery(id+"F23.opPattern","COPY",EDGE,{"derivedFrom":makeQuery(id+"F19.opPattern","COPY",EDGE,{"derivedFrom":makeQuery(id+"F15.opPattern","COPY",EDGE,{"derivedFrom":makeQuery(id+"F12.opPattern","COPY",EDGE,{"derivedFrom":makeQuery(id+"F6.opPattern","COPY",EDGE,{"derivedFrom":makeQuery(id+"F5.opPattern","COPY",EDGE,{"derivedFrom":makeQuery(id+"F4.opPattern","COPY",EDGE,{"derivedFrom":makeQuery(id+"F2.opPattern","COPY",EDGE,{"derivedFrom":makeQuery(id+"F1.opExtrude","CAP_EDGE",EDGE,{"disambiguationData":[OSD([sQuery(id+"F0.wireOp",EDGE,"E0.left")])],"isStart":false}),"instanceName":"1"}),"instanceName":"1"}),"instanceName":"1"}),"instanceName":"1"}),"instanceName":"1"}),"instanceName":"1"}),"instanceName":"1"}),"instanceName":"1"}),"instanceName":"1"});
            transform(context, id + "F39", {"entities" : qUnion([Q0, Q1, Q2, Q3, Q4, Q5, Q6, Q7, Q8, Q9, Q10, Q11, Q12, Q13, Q14, Q15, Q16, Q17, Q18, Q19]), "transformType" : TransformType.TRANSLATION_DISTANCE, "transformDirection" : qUnion([Q20]), "distance" : 140 * mm, "makeCopy" : true});
        }
        {
            var Q0;
            Q0=makeQuery(id+"F19.opPattern","COPY",BODY,{"derivedFrom":makeQuery(id+"F17.opPattern","COPY",BODY,{"derivedFrom":makeQuery(id+"F12.opPattern","COPY",BODY,{"derivedFrom":makeQuery(id+"F6.opPattern","COPY",BODY,{"derivedFrom":makeQuery(id+"F5.opPattern","COPY",BODY,{"derivedFrom":makeQuery(id+"F4.opPattern","COPY",BODY,{"derivedFrom":makeQuery(id+"F2.opPattern","COPY",BODY,{"derivedFrom":makeQuery(id+"F1.opExtrude","SWEPT_BODY",BODY,{"disambiguationData":[OSD([sQuery(id+"F0.wireOp",EDGE,"E0.bottom"),sQuery(id+"F0.wireOp",EDGE,"E0.top"),sQuery(id+"F0.wireOp",EDGE,"E0.left"),sQuery(id+"F0.wireOp",EDGE,"E0.right")])]}),"instanceName":"1"}),"instanceName":"1"}),"instanceName":"1"}),"instanceName":"1"}),"instanceName":"1"}),"instanceName":"1"}),"instanceName":"1"});
            var Q1;
            Q1=makeQuery(id+"F23.opPattern","COPY",BODY,{"derivedFrom":makeQuery(id+"F19.opPattern","COPY",BODY,{"derivedFrom":makeQuery(id+"F17.opPattern","COPY",BODY,{"derivedFrom":makeQuery(id+"F12.opPattern","COPY",BODY,{"derivedFrom":makeQuery(id+"F6.opPattern","COPY",BODY,{"derivedFrom":makeQuery(id+"F5.opPattern","COPY",BODY,{"derivedFrom":makeQuery(id+"F4.opPattern","COPY",BODY,{"derivedFrom":makeQuery(id+"F1.opExtrude","SWEPT_BODY",BODY,{"disambiguationData":[OSD([sQuery(id+"F0.wireOp",EDGE,"E0.bottom"),sQuery(id+"F0.wireOp",EDGE,"E0.top"),sQuery(id+"F0.wireOp",EDGE,"E0.left"),sQuery(id+"F0.wireOp",EDGE,"E0.right")])]}),"instanceName":"1"}),"instanceName":"1"}),"instanceName":"1"}),"instanceName":"1"}),"instanceName":"1"}),"instanceName":"1"}),"instanceName":"1"});
            var Q2;
            Q2=makeQuery(id+"F24.opPattern","COPY",BODY,{"derivedFrom":makeQuery(id+"F23.opPattern","COPY",BODY,{"derivedFrom":makeQuery(id+"F21.opPattern","COPY",BODY,{"derivedFrom":makeQuery(id+"F19.opPattern","COPY",BODY,{"derivedFrom":makeQuery(id+"F17.opPattern","COPY",BODY,{"derivedFrom":makeQuery(id+"F12.opPattern","COPY",BODY,{"derivedFrom":makeQuery(id+"F6.opPattern","COPY",BODY,{"derivedFrom":makeQuery(id+"F5.opPattern","COPY",BODY,{"derivedFrom":makeQuery(id+"F4.opPattern","COPY",BODY,{"derivedFrom":makeQuery(id+"F2.opPattern","COPY",BODY,{"derivedFrom":makeQuery(id+"F1.opExtrude","SWEPT_BODY",BODY,{"disambiguationData":[OSD([sQuery(id+"F0.wireOp",EDGE,"E0.bottom"),sQuery(id+"F0.wireOp",EDGE,"E0.top"),sQuery(id+"F0.wireOp",EDGE,"E0.left"),sQuery(id+"F0.wireOp",EDGE,"E0.right")])]}),"instanceName":"1"}),"instanceName":"1"}),"instanceName":"1"}),"instanceName":"1"}),"instanceName":"1"}),"instanceName":"1"}),"instanceName":"1"}),"instanceName":"1"}),"instanceName":"1"}),"instanceName":"1"});
            var Q3;
            Q3=makeQuery(id+"F29.opPattern","COPY",BODY,{"derivedFrom":makeQuery(id+"F19.opPattern","COPY",BODY,{"derivedFrom":makeQuery(id+"F17.opPattern","COPY",BODY,{"derivedFrom":makeQuery(id+"F15.opPattern","COPY",BODY,{"derivedFrom":makeQuery(id+"F12.opPattern","COPY",BODY,{"derivedFrom":makeQuery(id+"F6.opPattern","COPY",BODY,{"derivedFrom":makeQuery(id+"F5.opPattern","COPY",BODY,{"derivedFrom":makeQuery(id+"F4.opPattern","COPY",BODY,{"derivedFrom":makeQuery(id+"F2.opPattern","COPY",BODY,{"derivedFrom":makeQuery(id+"F1.opExtrude","SWEPT_BODY",BODY,{"disambiguationData":[OSD([sQuery(id+"F0.wireOp",EDGE,"E0.bottom"),sQuery(id+"F0.wireOp",EDGE,"E0.top"),sQuery(id+"F0.wireOp",EDGE,"E0.left"),sQuery(id+"F0.wireOp",EDGE,"E0.right")])]}),"instanceName":"1"}),"instanceName":"1"}),"instanceName":"1"}),"instanceName":"1"}),"instanceName":"1"}),"instanceName":"1"}),"instanceName":"1"}),"instanceName":"1"}),"instanceName":"1"});
            var Q4;
            Q4=makeQuery(id+"F29.opPattern","COPY",BODY,{"derivedFrom":makeQuery(id+"F26.opPattern","COPY",BODY,{"derivedFrom":makeQuery(id+"F17.opPattern","COPY",BODY,{"derivedFrom":makeQuery(id+"F13.opPattern","COPY",BODY,{"derivedFrom":makeQuery(id+"F5.opPattern","COPY",BODY,{"derivedFrom":makeQuery(id+"F4.opPattern","COPY",BODY,{"derivedFrom":makeQuery(id+"F1.opExtrude","SWEPT_BODY",BODY,{"disambiguationData":[OSD([sQuery(id+"F0.wireOp",EDGE,"E0.bottom"),sQuery(id+"F0.wireOp",EDGE,"E0.top"),sQuery(id+"F0.wireOp",EDGE,"E0.left"),sQuery(id+"F0.wireOp",EDGE,"E0.right")])]}),"instanceName":"1"}),"instanceName":"1"}),"instanceName":"1"}),"instanceName":"1"}),"instanceName":"1"}),"instanceName":"1"});
            var Q5;
            Q5=makeQuery(id+"F26.opPattern","COPY",BODY,{"derivedFrom":makeQuery(id+"F17.opPattern","COPY",BODY,{"derivedFrom":makeQuery(id+"F5.opPattern","COPY",BODY,{"derivedFrom":makeQuery(id+"F4.opPattern","COPY",BODY,{"derivedFrom":makeQuery(id+"F2.opPattern","COPY",BODY,{"derivedFrom":makeQuery(id+"F1.opExtrude","SWEPT_BODY",BODY,{"disambiguationData":[OSD([sQuery(id+"F0.wireOp",EDGE,"E0.bottom"),sQuery(id+"F0.wireOp",EDGE,"E0.top"),sQuery(id+"F0.wireOp",EDGE,"E0.left"),sQuery(id+"F0.wireOp",EDGE,"E0.right")])]}),"instanceName":"1"}),"instanceName":"1"}),"instanceName":"1"}),"instanceName":"1"}),"instanceName":"1"});
            var Q6;
            Q6=makeQuery(id+"F18.opPattern","COPY",BODY,{"derivedFrom":makeQuery(id+"F17.opPattern","COPY",BODY,{"derivedFrom":makeQuery(id+"F15.opPattern","COPY",BODY,{"derivedFrom":makeQuery(id+"F12.opPattern","COPY",BODY,{"derivedFrom":makeQuery(id+"F6.opPattern","COPY",BODY,{"derivedFrom":makeQuery(id+"F5.opPattern","COPY",BODY,{"derivedFrom":makeQuery(id+"F4.opPattern","COPY",BODY,{"derivedFrom":makeQuery(id+"F2.opPattern","COPY",BODY,{"derivedFrom":makeQuery(id+"F1.opExtrude","SWEPT_BODY",BODY,{"disambiguationData":[OSD([sQuery(id+"F0.wireOp",EDGE,"E0.bottom"),sQuery(id+"F0.wireOp",EDGE,"E0.top"),sQuery(id+"F0.wireOp",EDGE,"E0.left"),sQuery(id+"F0.wireOp",EDGE,"E0.right")])]}),"instanceName":"1"}),"instanceName":"1"}),"instanceName":"1"}),"instanceName":"1"}),"instanceName":"1"}),"instanceName":"1"}),"instanceName":"1"}),"instanceName":"1"});
            var Q7;
            Q7=makeQuery(id+"F26.opPattern","COPY",BODY,{"derivedFrom":makeQuery(id+"F19.opPattern","COPY",BODY,{"derivedFrom":makeQuery(id+"F12.opPattern","COPY",BODY,{"derivedFrom":makeQuery(id+"F6.opPattern","COPY",BODY,{"derivedFrom":makeQuery(id+"F5.opPattern","COPY",BODY,{"derivedFrom":makeQuery(id+"F4.opPattern","COPY",BODY,{"derivedFrom":makeQuery(id+"F1.opExtrude","SWEPT_BODY",BODY,{"disambiguationData":[OSD([sQuery(id+"F0.wireOp",EDGE,"E0.bottom"),sQuery(id+"F0.wireOp",EDGE,"E0.top"),sQuery(id+"F0.wireOp",EDGE,"E0.left"),sQuery(id+"F0.wireOp",EDGE,"E0.right")])]}),"instanceName":"1"}),"instanceName":"1"}),"instanceName":"1"}),"instanceName":"1"}),"instanceName":"1"}),"instanceName":"1"});
            var Q8;
            Q8=makeQuery(id+"F26.opPattern","COPY",BODY,{"derivedFrom":makeQuery(id+"F18.opPattern","COPY",BODY,{"derivedFrom":makeQuery(id+"F17.opPattern","COPY",BODY,{"derivedFrom":makeQuery(id+"F8.opPattern","COPY",BODY,{"derivedFrom":makeQuery(id+"F5.opPattern","COPY",BODY,{"derivedFrom":makeQuery(id+"F4.opPattern","COPY",BODY,{"derivedFrom":makeQuery(id+"F2.opPattern","COPY",BODY,{"derivedFrom":makeQuery(id+"F1.opExtrude","SWEPT_BODY",BODY,{"disambiguationData":[OSD([sQuery(id+"F0.wireOp",EDGE,"E0.bottom"),sQuery(id+"F0.wireOp",EDGE,"E0.top"),sQuery(id+"F0.wireOp",EDGE,"E0.left"),sQuery(id+"F0.wireOp",EDGE,"E0.right")])]}),"instanceName":"1"}),"instanceName":"1"}),"instanceName":"1"}),"instanceName":"1"}),"instanceName":"1"}),"instanceName":"1"}),"instanceName":"1"});
            var Q9;
            Q9=makeQuery(id+"F19.opPattern","COPY",BODY,{"derivedFrom":makeQuery(id+"F6.opPattern","COPY",BODY,{"derivedFrom":makeQuery(id+"F5.opPattern","COPY",BODY,{"derivedFrom":makeQuery(id+"F4.opPattern","COPY",BODY,{"derivedFrom":makeQuery(id+"F1.opExtrude","SWEPT_BODY",BODY,{"disambiguationData":[OSD([sQuery(id+"F0.wireOp",EDGE,"E0.bottom"),sQuery(id+"F0.wireOp",EDGE,"E0.top"),sQuery(id+"F0.wireOp",EDGE,"E0.left"),sQuery(id+"F0.wireOp",EDGE,"E0.right")])]}),"instanceName":"1"}),"instanceName":"1"}),"instanceName":"1"}),"instanceName":"1"});
            var Q10;
            Q10=makeQuery(id+"F23.opPattern","COPY",BODY,{"derivedFrom":makeQuery(id+"F21.opPattern","COPY",BODY,{"derivedFrom":makeQuery(id+"F19.opPattern","COPY",BODY,{"derivedFrom":makeQuery(id+"F12.opPattern","COPY",BODY,{"derivedFrom":makeQuery(id+"F6.opPattern","COPY",BODY,{"derivedFrom":makeQuery(id+"F5.opPattern","COPY",BODY,{"derivedFrom":makeQuery(id+"F4.opPattern","COPY",BODY,{"derivedFrom":makeQuery(id+"F2.opPattern","COPY",BODY,{"derivedFrom":makeQuery(id+"F1.opExtrude","SWEPT_BODY",BODY,{"disambiguationData":[OSD([sQuery(id+"F0.wireOp",EDGE,"E0.bottom"),sQuery(id+"F0.wireOp",EDGE,"E0.top"),sQuery(id+"F0.wireOp",EDGE,"E0.left"),sQuery(id+"F0.wireOp",EDGE,"E0.right")])]}),"instanceName":"1"}),"instanceName":"1"}),"instanceName":"1"}),"instanceName":"1"}),"instanceName":"1"}),"instanceName":"1"}),"instanceName":"1"}),"instanceName":"1"});
            var Q11;
            Q11=makeQuery(id+"F26.opPattern","COPY",BODY,{"derivedFrom":makeQuery(id+"F19.opPattern","COPY",BODY,{"derivedFrom":makeQuery(id+"F5.opPattern","COPY",BODY,{"derivedFrom":makeQuery(id+"F4.opPattern","COPY",BODY,{"derivedFrom":makeQuery(id+"F1.opExtrude","SWEPT_BODY",BODY,{"disambiguationData":[OSD([sQuery(id+"F0.wireOp",EDGE,"E0.bottom"),sQuery(id+"F0.wireOp",EDGE,"E0.top"),sQuery(id+"F0.wireOp",EDGE,"E0.left"),sQuery(id+"F0.wireOp",EDGE,"E0.right")])]}),"instanceName":"1"}),"instanceName":"1"}),"instanceName":"1"}),"instanceName":"1"});
            var Q12;
            Q12=makeQuery(id+"F23.opPattern","COPY",BODY,{"derivedFrom":makeQuery(id+"F19.opPattern","COPY",BODY,{"derivedFrom":makeQuery(id+"F12.opPattern","COPY",BODY,{"derivedFrom":makeQuery(id+"F6.opPattern","COPY",BODY,{"derivedFrom":makeQuery(id+"F5.opPattern","COPY",BODY,{"derivedFrom":makeQuery(id+"F4.opPattern","COPY",BODY,{"derivedFrom":makeQuery(id+"F2.opPattern","COPY",BODY,{"derivedFrom":makeQuery(id+"F1.opExtrude","SWEPT_BODY",BODY,{"disambiguationData":[OSD([sQuery(id+"F0.wireOp",EDGE,"E0.bottom"),sQuery(id+"F0.wireOp",EDGE,"E0.top"),sQuery(id+"F0.wireOp",EDGE,"E0.left"),sQuery(id+"F0.wireOp",EDGE,"E0.right")])]}),"instanceName":"1"}),"instanceName":"1"}),"instanceName":"1"}),"instanceName":"1"}),"instanceName":"1"}),"instanceName":"1"}),"instanceName":"1"});
            var Q13;
            Q13=makeQuery(id+"F12.opPattern","COPY",BODY,{"derivedFrom":makeQuery(id+"F6.opPattern","COPY",BODY,{"derivedFrom":makeQuery(id+"F5.opPattern","COPY",BODY,{"derivedFrom":makeQuery(id+"F4.opPattern","COPY",BODY,{"derivedFrom":makeQuery(id+"F1.opExtrude","SWEPT_BODY",BODY,{"disambiguationData":[OSD([sQuery(id+"F0.wireOp",EDGE,"E0.bottom"),sQuery(id+"F0.wireOp",EDGE,"E0.top"),sQuery(id+"F0.wireOp",EDGE,"E0.left"),sQuery(id+"F0.wireOp",EDGE,"E0.right")])]}),"instanceName":"1"}),"instanceName":"1"}),"instanceName":"1"}),"instanceName":"1"});
            var Q14;
            Q14=makeQuery(id+"F21.opPattern","COPY",BODY,{"derivedFrom":makeQuery(id+"F19.opPattern","COPY",BODY,{"derivedFrom":makeQuery(id+"F17.opPattern","COPY",BODY,{"derivedFrom":makeQuery(id+"F12.opPattern","COPY",BODY,{"derivedFrom":makeQuery(id+"F6.opPattern","COPY",BODY,{"derivedFrom":makeQuery(id+"F5.opPattern","COPY",BODY,{"derivedFrom":makeQuery(id+"F4.opPattern","COPY",BODY,{"derivedFrom":makeQuery(id+"F1.opExtrude","SWEPT_BODY",BODY,{"disambiguationData":[OSD([sQuery(id+"F0.wireOp",EDGE,"E0.bottom"),sQuery(id+"F0.wireOp",EDGE,"E0.top"),sQuery(id+"F0.wireOp",EDGE,"E0.left"),sQuery(id+"F0.wireOp",EDGE,"E0.right")])]}),"instanceName":"1"}),"instanceName":"1"}),"instanceName":"1"}),"instanceName":"1"}),"instanceName":"1"}),"instanceName":"1"}),"instanceName":"1"});
            var Q15;
            Q15=makeQuery(id+"F29.opPattern","COPY",BODY,{"derivedFrom":makeQuery(id+"F23.opPattern","COPY",BODY,{"derivedFrom":makeQuery(id+"F19.opPattern","COPY",BODY,{"derivedFrom":makeQuery(id+"F15.opPattern","COPY",BODY,{"derivedFrom":makeQuery(id+"F12.opPattern","COPY",BODY,{"derivedFrom":makeQuery(id+"F6.opPattern","COPY",BODY,{"derivedFrom":makeQuery(id+"F5.opPattern","COPY",BODY,{"derivedFrom":makeQuery(id+"F4.opPattern","COPY",BODY,{"derivedFrom":makeQuery(id+"F2.opPattern","COPY",BODY,{"derivedFrom":makeQuery(id+"F1.opExtrude","SWEPT_BODY",BODY,{"disambiguationData":[OSD([sQuery(id+"F0.wireOp",EDGE,"E0.bottom"),sQuery(id+"F0.wireOp",EDGE,"E0.top"),sQuery(id+"F0.wireOp",EDGE,"E0.left"),sQuery(id+"F0.wireOp",EDGE,"E0.right")])]}),"instanceName":"1"}),"instanceName":"1"}),"instanceName":"1"}),"instanceName":"1"}),"instanceName":"1"}),"instanceName":"1"}),"instanceName":"1"}),"instanceName":"1"}),"instanceName":"1"});
            var Q16;
            Q16=makeQuery(id+"F26.opPattern","COPY",BODY,{"derivedFrom":makeQuery(id+"F17.opPattern","COPY",BODY,{"derivedFrom":makeQuery(id+"F5.opPattern","COPY",BODY,{"derivedFrom":makeQuery(id+"F4.opPattern","COPY",BODY,{"derivedFrom":makeQuery(id+"F1.opExtrude","SWEPT_BODY",BODY,{"disambiguationData":[OSD([sQuery(id+"F0.wireOp",EDGE,"E0.bottom"),sQuery(id+"F0.wireOp",EDGE,"E0.top"),sQuery(id+"F0.wireOp",EDGE,"E0.left"),sQuery(id+"F0.wireOp",EDGE,"E0.right")])]}),"instanceName":"1"}),"instanceName":"1"}),"instanceName":"1"}),"instanceName":"1"});
            var Q17;
            Q17=makeQuery(id+"F28.opPattern","COPY",BODY,{"derivedFrom":makeQuery(id+"F26.opPattern","COPY",BODY,{"derivedFrom":makeQuery(id+"F17.opPattern","COPY",BODY,{"derivedFrom":makeQuery(id+"F15.opPattern","COPY",BODY,{"derivedFrom":makeQuery(id+"F12.opPattern","COPY",BODY,{"derivedFrom":makeQuery(id+"F6.opPattern","COPY",BODY,{"derivedFrom":makeQuery(id+"F5.opPattern","COPY",BODY,{"derivedFrom":makeQuery(id+"F4.opPattern","COPY",BODY,{"derivedFrom":makeQuery(id+"F2.opPattern","COPY",BODY,{"derivedFrom":makeQuery(id+"F1.opExtrude","SWEPT_BODY",BODY,{"disambiguationData":[OSD([sQuery(id+"F0.wireOp",EDGE,"E0.bottom"),sQuery(id+"F0.wireOp",EDGE,"E0.top"),sQuery(id+"F0.wireOp",EDGE,"E0.left"),sQuery(id+"F0.wireOp",EDGE,"E0.right")])]}),"instanceName":"1"}),"instanceName":"1"}),"instanceName":"1"}),"instanceName":"1"}),"instanceName":"1"}),"instanceName":"1"}),"instanceName":"1"}),"instanceName":"1"}),"instanceName":"1"});
            var Q18;
            Q18=makeQuery(id+"F23.opPattern","COPY",BODY,{"derivedFrom":makeQuery(id+"F21.opPattern","COPY",BODY,{"derivedFrom":makeQuery(id+"F19.opPattern","COPY",BODY,{"derivedFrom":makeQuery(id+"F5.opPattern","COPY",BODY,{"derivedFrom":makeQuery(id+"F4.opPattern","COPY",BODY,{"derivedFrom":makeQuery(id+"F2.opPattern","COPY",BODY,{"derivedFrom":makeQuery(id+"F1.opExtrude","SWEPT_BODY",BODY,{"disambiguationData":[OSD([sQuery(id+"F0.wireOp",EDGE,"E0.bottom"),sQuery(id+"F0.wireOp",EDGE,"E0.top"),sQuery(id+"F0.wireOp",EDGE,"E0.left"),sQuery(id+"F0.wireOp",EDGE,"E0.right")])]}),"instanceName":"1"}),"instanceName":"1"}),"instanceName":"1"}),"instanceName":"1"}),"instanceName":"1"}),"instanceName":"1"});
            var Q19;
            Q19=makeQuery(id+"F23.opPattern","COPY",BODY,{"derivedFrom":makeQuery(id+"F19.opPattern","COPY",BODY,{"derivedFrom":makeQuery(id+"F5.opPattern","COPY",BODY,{"derivedFrom":makeQuery(id+"F4.opPattern","COPY",BODY,{"derivedFrom":makeQuery(id+"F2.opPattern","COPY",BODY,{"derivedFrom":makeQuery(id+"F1.opExtrude","SWEPT_BODY",BODY,{"disambiguationData":[OSD([sQuery(id+"F0.wireOp",EDGE,"E0.bottom"),sQuery(id+"F0.wireOp",EDGE,"E0.top"),sQuery(id+"F0.wireOp",EDGE,"E0.left"),sQuery(id+"F0.wireOp",EDGE,"E0.right")])]}),"instanceName":"1"}),"instanceName":"1"}),"instanceName":"1"}),"instanceName":"1"}),"instanceName":"1"});
            var Q20;
            Q20=makeQuery(id+"F19.opPattern","COPY",BODY,{"derivedFrom":makeQuery(id+"F17.opPattern","COPY",BODY,{"derivedFrom":makeQuery(id+"F5.opPattern","COPY",BODY,{"derivedFrom":makeQuery(id+"F4.opPattern","COPY",BODY,{"derivedFrom":makeQuery(id+"F2.opPattern","COPY",BODY,{"derivedFrom":makeQuery(id+"F1.opExtrude","SWEPT_BODY",BODY,{"disambiguationData":[OSD([sQuery(id+"F0.wireOp",EDGE,"E0.bottom"),sQuery(id+"F0.wireOp",EDGE,"E0.top"),sQuery(id+"F0.wireOp",EDGE,"E0.left"),sQuery(id+"F0.wireOp",EDGE,"E0.right")])]}),"instanceName":"1"}),"instanceName":"1"}),"instanceName":"1"}),"instanceName":"1"}),"instanceName":"1"});
            var Q21;
            Q21=makeQuery(id+"F21.opPattern","COPY",BODY,{"derivedFrom":makeQuery(id+"F19.opPattern","COPY",BODY,{"derivedFrom":makeQuery(id+"F17.opPattern","COPY",BODY,{"derivedFrom":makeQuery(id+"F6.opPattern","COPY",BODY,{"derivedFrom":makeQuery(id+"F5.opPattern","COPY",BODY,{"derivedFrom":makeQuery(id+"F4.opPattern","COPY",BODY,{"derivedFrom":makeQuery(id+"F1.opExtrude","SWEPT_BODY",BODY,{"disambiguationData":[OSD([sQuery(id+"F0.wireOp",EDGE,"E0.bottom"),sQuery(id+"F0.wireOp",EDGE,"E0.top"),sQuery(id+"F0.wireOp",EDGE,"E0.left"),sQuery(id+"F0.wireOp",EDGE,"E0.right")])]}),"instanceName":"1"}),"instanceName":"1"}),"instanceName":"1"}),"instanceName":"1"}),"instanceName":"1"}),"instanceName":"1"});
            var Q22;
            Q22=makeQuery(id+"F26.opPattern","COPY",BODY,{"derivedFrom":makeQuery(id+"F17.opPattern","COPY",BODY,{"derivedFrom":makeQuery(id+"F6.opPattern","COPY",BODY,{"derivedFrom":makeQuery(id+"F5.opPattern","COPY",BODY,{"derivedFrom":makeQuery(id+"F4.opPattern","COPY",BODY,{"derivedFrom":makeQuery(id+"F2.opPattern","COPY",BODY,{"derivedFrom":makeQuery(id+"F1.opExtrude","SWEPT_BODY",BODY,{"disambiguationData":[OSD([sQuery(id+"F0.wireOp",EDGE,"E0.bottom"),sQuery(id+"F0.wireOp",EDGE,"E0.top"),sQuery(id+"F0.wireOp",EDGE,"E0.left"),sQuery(id+"F0.wireOp",EDGE,"E0.right")])]}),"instanceName":"1"}),"instanceName":"1"}),"instanceName":"1"}),"instanceName":"1"}),"instanceName":"1"}),"instanceName":"1"});
            var Q23;
            Q23=makeQuery(id+"F23.opPattern","COPY",BODY,{"derivedFrom":makeQuery(id+"F19.opPattern","COPY",BODY,{"derivedFrom":makeQuery(id+"F17.opPattern","COPY",BODY,{"derivedFrom":makeQuery(id+"F6.opPattern","COPY",BODY,{"derivedFrom":makeQuery(id+"F5.opPattern","COPY",BODY,{"derivedFrom":makeQuery(id+"F4.opPattern","COPY",BODY,{"derivedFrom":makeQuery(id+"F1.opExtrude","SWEPT_BODY",BODY,{"disambiguationData":[OSD([sQuery(id+"F0.wireOp",EDGE,"E0.bottom"),sQuery(id+"F0.wireOp",EDGE,"E0.top"),sQuery(id+"F0.wireOp",EDGE,"E0.left"),sQuery(id+"F0.wireOp",EDGE,"E0.right")])]}),"instanceName":"1"}),"instanceName":"1"}),"instanceName":"1"}),"instanceName":"1"}),"instanceName":"1"}),"instanceName":"1"});
            var Q24;
            Q24=makeQuery(id+"F19.opPattern","COPY",BODY,{"derivedFrom":makeQuery(id+"F5.opPattern","COPY",BODY,{"derivedFrom":makeQuery(id+"F4.opPattern","COPY",BODY,{"derivedFrom":makeQuery(id+"F2.opPattern","COPY",BODY,{"derivedFrom":makeQuery(id+"F1.opExtrude","SWEPT_BODY",BODY,{"disambiguationData":[OSD([sQuery(id+"F0.wireOp",EDGE,"E0.bottom"),sQuery(id+"F0.wireOp",EDGE,"E0.top"),sQuery(id+"F0.wireOp",EDGE,"E0.left"),sQuery(id+"F0.wireOp",EDGE,"E0.right")])]}),"instanceName":"1"}),"instanceName":"1"}),"instanceName":"1"}),"instanceName":"1"});
            var Q25;
            Q25=makeQuery(id+"F24.opPattern","COPY",BODY,{"derivedFrom":makeQuery(id+"F23.opPattern","COPY",BODY,{"derivedFrom":makeQuery(id+"F19.opPattern","COPY",BODY,{"derivedFrom":makeQuery(id+"F17.opPattern","COPY",BODY,{"derivedFrom":makeQuery(id+"F5.opPattern","COPY",BODY,{"derivedFrom":makeQuery(id+"F4.opPattern","COPY",BODY,{"derivedFrom":makeQuery(id+"F1.opExtrude","SWEPT_BODY",BODY,{"disambiguationData":[OSD([sQuery(id+"F0.wireOp",EDGE,"E0.bottom"),sQuery(id+"F0.wireOp",EDGE,"E0.top"),sQuery(id+"F0.wireOp",EDGE,"E0.left"),sQuery(id+"F0.wireOp",EDGE,"E0.right")])]}),"instanceName":"1"}),"instanceName":"1"}),"instanceName":"1"}),"instanceName":"1"}),"instanceName":"1"}),"instanceName":"1"});
            var Q26;
            Q26=makeQuery(id+"F28.opPattern","COPY",BODY,{"derivedFrom":makeQuery(id+"F19.opPattern","COPY",BODY,{"derivedFrom":makeQuery(id+"F15.opPattern","COPY",BODY,{"derivedFrom":makeQuery(id+"F12.opPattern","COPY",BODY,{"derivedFrom":makeQuery(id+"F6.opPattern","COPY",BODY,{"derivedFrom":makeQuery(id+"F5.opPattern","COPY",BODY,{"derivedFrom":makeQuery(id+"F4.opPattern","COPY",BODY,{"derivedFrom":makeQuery(id+"F2.opPattern","COPY",BODY,{"derivedFrom":makeQuery(id+"F1.opExtrude","SWEPT_BODY",BODY,{"disambiguationData":[OSD([sQuery(id+"F0.wireOp",EDGE,"E0.bottom"),sQuery(id+"F0.wireOp",EDGE,"E0.top"),sQuery(id+"F0.wireOp",EDGE,"E0.left"),sQuery(id+"F0.wireOp",EDGE,"E0.right")])]}),"instanceName":"1"}),"instanceName":"1"}),"instanceName":"1"}),"instanceName":"1"}),"instanceName":"1"}),"instanceName":"1"}),"instanceName":"1"}),"instanceName":"1"});
            var Q27;
            Q27=makeQuery(id+"F28.opPattern","COPY",BODY,{"derivedFrom":makeQuery(id+"F19.opPattern","COPY",BODY,{"derivedFrom":makeQuery(id+"F17.opPattern","COPY",BODY,{"derivedFrom":makeQuery(id+"F13.opPattern","COPY",BODY,{"derivedFrom":makeQuery(id+"F5.opPattern","COPY",BODY,{"derivedFrom":makeQuery(id+"F4.opPattern","COPY",BODY,{"derivedFrom":makeQuery(id+"F1.opExtrude","SWEPT_BODY",BODY,{"disambiguationData":[OSD([sQuery(id+"F0.wireOp",EDGE,"E0.bottom"),sQuery(id+"F0.wireOp",EDGE,"E0.top"),sQuery(id+"F0.wireOp",EDGE,"E0.left"),sQuery(id+"F0.wireOp",EDGE,"E0.right")])]}),"instanceName":"1"}),"instanceName":"1"}),"instanceName":"1"}),"instanceName":"1"}),"instanceName":"1"}),"instanceName":"1"});
            var Q28;
            Q28=makeQuery(id+"F23.opPattern","COPY",BODY,{"derivedFrom":makeQuery(id+"F21.opPattern","COPY",BODY,{"derivedFrom":makeQuery(id+"F19.opPattern","COPY",BODY,{"derivedFrom":makeQuery(id+"F17.opPattern","COPY",BODY,{"derivedFrom":makeQuery(id+"F6.opPattern","COPY",BODY,{"derivedFrom":makeQuery(id+"F5.opPattern","COPY",BODY,{"derivedFrom":makeQuery(id+"F4.opPattern","COPY",BODY,{"derivedFrom":makeQuery(id+"F2.opPattern","COPY",BODY,{"derivedFrom":makeQuery(id+"F1.opExtrude","SWEPT_BODY",BODY,{"disambiguationData":[OSD([sQuery(id+"F0.wireOp",EDGE,"E0.bottom"),sQuery(id+"F0.wireOp",EDGE,"E0.top"),sQuery(id+"F0.wireOp",EDGE,"E0.left"),sQuery(id+"F0.wireOp",EDGE,"E0.right")])]}),"instanceName":"1"}),"instanceName":"1"}),"instanceName":"1"}),"instanceName":"1"}),"instanceName":"1"}),"instanceName":"1"}),"instanceName":"1"}),"instanceName":"1"});
            var Q29;
            Q29=makeQuery(id+"F19.opPattern","COPY",BODY,{"derivedFrom":makeQuery(id+"F17.opPattern","COPY",BODY,{"derivedFrom":makeQuery(id+"F12.opPattern","COPY",BODY,{"derivedFrom":makeQuery(id+"F6.opPattern","COPY",BODY,{"derivedFrom":makeQuery(id+"F5.opPattern","COPY",BODY,{"derivedFrom":makeQuery(id+"F4.opPattern","COPY",BODY,{"derivedFrom":makeQuery(id+"F1.opExtrude","SWEPT_BODY",BODY,{"disambiguationData":[OSD([sQuery(id+"F0.wireOp",EDGE,"E0.bottom"),sQuery(id+"F0.wireOp",EDGE,"E0.top"),sQuery(id+"F0.wireOp",EDGE,"E0.left"),sQuery(id+"F0.wireOp",EDGE,"E0.right")])]}),"instanceName":"1"}),"instanceName":"1"}),"instanceName":"1"}),"instanceName":"1"}),"instanceName":"1"}),"instanceName":"1"});
            var Q30;
            Q30=makeQuery(id+"F26.opPattern","COPY",BODY,{"derivedFrom":makeQuery(id+"F17.opPattern","COPY",BODY,{"derivedFrom":makeQuery(id+"F12.opPattern","COPY",BODY,{"derivedFrom":makeQuery(id+"F6.opPattern","COPY",BODY,{"derivedFrom":makeQuery(id+"F5.opPattern","COPY",BODY,{"derivedFrom":makeQuery(id+"F4.opPattern","COPY",BODY,{"derivedFrom":makeQuery(id+"F2.opPattern","COPY",BODY,{"derivedFrom":makeQuery(id+"F1.opExtrude","SWEPT_BODY",BODY,{"disambiguationData":[OSD([sQuery(id+"F0.wireOp",EDGE,"E0.bottom"),sQuery(id+"F0.wireOp",EDGE,"E0.top"),sQuery(id+"F0.wireOp",EDGE,"E0.left"),sQuery(id+"F0.wireOp",EDGE,"E0.right")])]}),"instanceName":"1"}),"instanceName":"1"}),"instanceName":"1"}),"instanceName":"1"}),"instanceName":"1"}),"instanceName":"1"}),"instanceName":"1"});
            var Q31;
            Q31=makeQuery(id+"F28.opPattern","COPY",BODY,{"derivedFrom":makeQuery(id+"F19.opPattern","COPY",BODY,{"derivedFrom":makeQuery(id+"F17.opPattern","COPY",BODY,{"derivedFrom":makeQuery(id+"F15.opPattern","COPY",BODY,{"derivedFrom":makeQuery(id+"F12.opPattern","COPY",BODY,{"derivedFrom":makeQuery(id+"F6.opPattern","COPY",BODY,{"derivedFrom":makeQuery(id+"F5.opPattern","COPY",BODY,{"derivedFrom":makeQuery(id+"F4.opPattern","COPY",BODY,{"derivedFrom":makeQuery(id+"F2.opPattern","COPY",BODY,{"derivedFrom":makeQuery(id+"F1.opExtrude","SWEPT_BODY",BODY,{"disambiguationData":[OSD([sQuery(id+"F0.wireOp",EDGE,"E0.bottom"),sQuery(id+"F0.wireOp",EDGE,"E0.top"),sQuery(id+"F0.wireOp",EDGE,"E0.left"),sQuery(id+"F0.wireOp",EDGE,"E0.right")])]}),"instanceName":"1"}),"instanceName":"1"}),"instanceName":"1"}),"instanceName":"1"}),"instanceName":"1"}),"instanceName":"1"}),"instanceName":"1"}),"instanceName":"1"}),"instanceName":"1"});
            var Q32;
            Q32=makeQuery(id+"F23.opPattern","COPY",BODY,{"derivedFrom":makeQuery(id+"F21.opPattern","COPY",BODY,{"derivedFrom":makeQuery(id+"F19.opPattern","COPY",BODY,{"derivedFrom":makeQuery(id+"F6.opPattern","COPY",BODY,{"derivedFrom":makeQuery(id+"F5.opPattern","COPY",BODY,{"derivedFrom":makeQuery(id+"F4.opPattern","COPY",BODY,{"derivedFrom":makeQuery(id+"F2.opPattern","COPY",BODY,{"derivedFrom":makeQuery(id+"F1.opExtrude","SWEPT_BODY",BODY,{"disambiguationData":[OSD([sQuery(id+"F0.wireOp",EDGE,"E0.bottom"),sQuery(id+"F0.wireOp",EDGE,"E0.top"),sQuery(id+"F0.wireOp",EDGE,"E0.left"),sQuery(id+"F0.wireOp",EDGE,"E0.right")])]}),"instanceName":"1"}),"instanceName":"1"}),"instanceName":"1"}),"instanceName":"1"}),"instanceName":"1"}),"instanceName":"1"}),"instanceName":"1"});
            var Q33;
            Q33=makeQuery(id+"F19.opPattern","COPY",BODY,{"derivedFrom":makeQuery(id+"F6.opPattern","COPY",BODY,{"derivedFrom":makeQuery(id+"F5.opPattern","COPY",BODY,{"derivedFrom":makeQuery(id+"F4.opPattern","COPY",BODY,{"derivedFrom":makeQuery(id+"F2.opPattern","COPY",BODY,{"derivedFrom":makeQuery(id+"F1.opExtrude","SWEPT_BODY",BODY,{"disambiguationData":[OSD([sQuery(id+"F0.wireOp",EDGE,"E0.bottom"),sQuery(id+"F0.wireOp",EDGE,"E0.top"),sQuery(id+"F0.wireOp",EDGE,"E0.left"),sQuery(id+"F0.wireOp",EDGE,"E0.right")])]}),"instanceName":"1"}),"instanceName":"1"}),"instanceName":"1"}),"instanceName":"1"}),"instanceName":"1"});
            var Q34;
            Q34=makeQuery(id+"F23.opPattern","COPY",BODY,{"derivedFrom":makeQuery(id+"F19.opPattern","COPY",BODY,{"derivedFrom":makeQuery(id+"F15.opPattern","COPY",BODY,{"derivedFrom":makeQuery(id+"F12.opPattern","COPY",BODY,{"derivedFrom":makeQuery(id+"F6.opPattern","COPY",BODY,{"derivedFrom":makeQuery(id+"F5.opPattern","COPY",BODY,{"derivedFrom":makeQuery(id+"F4.opPattern","COPY",BODY,{"derivedFrom":makeQuery(id+"F2.opPattern","COPY",BODY,{"derivedFrom":makeQuery(id+"F1.opExtrude","SWEPT_BODY",BODY,{"disambiguationData":[OSD([sQuery(id+"F0.wireOp",EDGE,"E0.bottom"),sQuery(id+"F0.wireOp",EDGE,"E0.top"),sQuery(id+"F0.wireOp",EDGE,"E0.left"),sQuery(id+"F0.wireOp",EDGE,"E0.right")])]}),"instanceName":"1"}),"instanceName":"1"}),"instanceName":"1"}),"instanceName":"1"}),"instanceName":"1"}),"instanceName":"1"}),"instanceName":"1"}),"instanceName":"1"});
            var Q35;
            Q35=makeQuery(id+"F28.opPattern","COPY",BODY,{"derivedFrom":makeQuery(id+"F26.opPattern","COPY",BODY,{"derivedFrom":makeQuery(id+"F19.opPattern","COPY",BODY,{"derivedFrom":makeQuery(id+"F13.opPattern","COPY",BODY,{"derivedFrom":makeQuery(id+"F5.opPattern","COPY",BODY,{"derivedFrom":makeQuery(id+"F4.opPattern","COPY",BODY,{"derivedFrom":makeQuery(id+"F1.opExtrude","SWEPT_BODY",BODY,{"disambiguationData":[OSD([sQuery(id+"F0.wireOp",EDGE,"E0.bottom"),sQuery(id+"F0.wireOp",EDGE,"E0.top"),sQuery(id+"F0.wireOp",EDGE,"E0.left"),sQuery(id+"F0.wireOp",EDGE,"E0.right")])]}),"instanceName":"1"}),"instanceName":"1"}),"instanceName":"1"}),"instanceName":"1"}),"instanceName":"1"}),"instanceName":"1"});
            var Q36;
            Q36=makeQuery(id+"F21.opPattern","COPY",BODY,{"derivedFrom":makeQuery(id+"F19.opPattern","COPY",BODY,{"derivedFrom":makeQuery(id+"F17.opPattern","COPY",BODY,{"derivedFrom":makeQuery(id+"F5.opPattern","COPY",BODY,{"derivedFrom":makeQuery(id+"F4.opPattern","COPY",BODY,{"derivedFrom":makeQuery(id+"F2.opPattern","COPY",BODY,{"derivedFrom":makeQuery(id+"F1.opExtrude","SWEPT_BODY",BODY,{"disambiguationData":[OSD([sQuery(id+"F0.wireOp",EDGE,"E0.bottom"),sQuery(id+"F0.wireOp",EDGE,"E0.top"),sQuery(id+"F0.wireOp",EDGE,"E0.left"),sQuery(id+"F0.wireOp",EDGE,"E0.right")])]}),"instanceName":"1"}),"instanceName":"1"}),"instanceName":"1"}),"instanceName":"1"}),"instanceName":"1"}),"instanceName":"1"});
            var Q37;
            Q37=makeQuery(id+"F23.opPattern","COPY",BODY,{"derivedFrom":makeQuery(id+"F19.opPattern","COPY",BODY,{"derivedFrom":makeQuery(id+"F17.opPattern","COPY",BODY,{"derivedFrom":makeQuery(id+"F15.opPattern","COPY",BODY,{"derivedFrom":makeQuery(id+"F12.opPattern","COPY",BODY,{"derivedFrom":makeQuery(id+"F6.opPattern","COPY",BODY,{"derivedFrom":makeQuery(id+"F5.opPattern","COPY",BODY,{"derivedFrom":makeQuery(id+"F4.opPattern","COPY",BODY,{"derivedFrom":makeQuery(id+"F2.opPattern","COPY",BODY,{"derivedFrom":makeQuery(id+"F1.opExtrude","SWEPT_BODY",BODY,{"disambiguationData":[OSD([sQuery(id+"F0.wireOp",EDGE,"E0.bottom"),sQuery(id+"F0.wireOp",EDGE,"E0.top"),sQuery(id+"F0.wireOp",EDGE,"E0.left"),sQuery(id+"F0.wireOp",EDGE,"E0.right")])]}),"instanceName":"1"}),"instanceName":"1"}),"instanceName":"1"}),"instanceName":"1"}),"instanceName":"1"}),"instanceName":"1"}),"instanceName":"1"}),"instanceName":"1"}),"instanceName":"1"});
            var Q38;
            Q38=makeQuery(id+"F19.opPattern","COPY",BODY,{"derivedFrom":makeQuery(id+"F17.opPattern","COPY",BODY,{"derivedFrom":makeQuery(id+"F15.opPattern","COPY",BODY,{"derivedFrom":makeQuery(id+"F12.opPattern","COPY",BODY,{"derivedFrom":makeQuery(id+"F6.opPattern","COPY",BODY,{"derivedFrom":makeQuery(id+"F5.opPattern","COPY",BODY,{"derivedFrom":makeQuery(id+"F4.opPattern","COPY",BODY,{"derivedFrom":makeQuery(id+"F2.opPattern","COPY",BODY,{"derivedFrom":makeQuery(id+"F1.opExtrude","SWEPT_BODY",BODY,{"disambiguationData":[OSD([sQuery(id+"F0.wireOp",EDGE,"E0.bottom"),sQuery(id+"F0.wireOp",EDGE,"E0.top"),sQuery(id+"F0.wireOp",EDGE,"E0.left"),sQuery(id+"F0.wireOp",EDGE,"E0.right")])]}),"instanceName":"1"}),"instanceName":"1"}),"instanceName":"1"}),"instanceName":"1"}),"instanceName":"1"}),"instanceName":"1"}),"instanceName":"1"}),"instanceName":"1"});
            var Q39;
            Q39=makeQuery(id+"F21.opPattern","COPY",BODY,{"derivedFrom":makeQuery(id+"F19.opPattern","COPY",BODY,{"derivedFrom":makeQuery(id+"F17.opPattern","COPY",BODY,{"derivedFrom":makeQuery(id+"F12.opPattern","COPY",BODY,{"derivedFrom":makeQuery(id+"F6.opPattern","COPY",BODY,{"derivedFrom":makeQuery(id+"F5.opPattern","COPY",BODY,{"derivedFrom":makeQuery(id+"F4.opPattern","COPY",BODY,{"derivedFrom":makeQuery(id+"F2.opPattern","COPY",BODY,{"derivedFrom":makeQuery(id+"F1.opExtrude","SWEPT_BODY",BODY,{"disambiguationData":[OSD([sQuery(id+"F0.wireOp",EDGE,"E0.bottom"),sQuery(id+"F0.wireOp",EDGE,"E0.top"),sQuery(id+"F0.wireOp",EDGE,"E0.left"),sQuery(id+"F0.wireOp",EDGE,"E0.right")])]}),"instanceName":"1"}),"instanceName":"1"}),"instanceName":"1"}),"instanceName":"1"}),"instanceName":"1"}),"instanceName":"1"}),"instanceName":"1"}),"instanceName":"1"});
            var Q40;
            Q40=makeQuery(id+"F21.opPattern","COPY",BODY,{"derivedFrom":makeQuery(id+"F19.opPattern","COPY",BODY,{"derivedFrom":makeQuery(id+"F12.opPattern","COPY",BODY,{"derivedFrom":makeQuery(id+"F6.opPattern","COPY",BODY,{"derivedFrom":makeQuery(id+"F5.opPattern","COPY",BODY,{"derivedFrom":makeQuery(id+"F4.opPattern","COPY",BODY,{"derivedFrom":makeQuery(id+"F2.opPattern","COPY",BODY,{"derivedFrom":makeQuery(id+"F1.opExtrude","SWEPT_BODY",BODY,{"disambiguationData":[OSD([sQuery(id+"F0.wireOp",EDGE,"E0.bottom"),sQuery(id+"F0.wireOp",EDGE,"E0.top"),sQuery(id+"F0.wireOp",EDGE,"E0.left"),sQuery(id+"F0.wireOp",EDGE,"E0.right")])]}),"instanceName":"1"}),"instanceName":"1"}),"instanceName":"1"}),"instanceName":"1"}),"instanceName":"1"}),"instanceName":"1"}),"instanceName":"1"});
            var Q41;
            Q41=makeQuery(id+"F28.opPattern","COPY",BODY,{"derivedFrom":makeQuery(id+"F23.opPattern","COPY",BODY,{"derivedFrom":makeQuery(id+"F19.opPattern","COPY",BODY,{"derivedFrom":makeQuery(id+"F15.opPattern","COPY",BODY,{"derivedFrom":makeQuery(id+"F12.opPattern","COPY",BODY,{"derivedFrom":makeQuery(id+"F6.opPattern","COPY",BODY,{"derivedFrom":makeQuery(id+"F5.opPattern","COPY",BODY,{"derivedFrom":makeQuery(id+"F4.opPattern","COPY",BODY,{"derivedFrom":makeQuery(id+"F2.opPattern","COPY",BODY,{"derivedFrom":makeQuery(id+"F1.opExtrude","SWEPT_BODY",BODY,{"disambiguationData":[OSD([sQuery(id+"F0.wireOp",EDGE,"E0.bottom"),sQuery(id+"F0.wireOp",EDGE,"E0.top"),sQuery(id+"F0.wireOp",EDGE,"E0.left"),sQuery(id+"F0.wireOp",EDGE,"E0.right")])]}),"instanceName":"1"}),"instanceName":"1"}),"instanceName":"1"}),"instanceName":"1"}),"instanceName":"1"}),"instanceName":"1"}),"instanceName":"1"}),"instanceName":"1"}),"instanceName":"1"});
            var Q42;
            Q42=makeQuery(id+"F28.opPattern","COPY",BODY,{"derivedFrom":makeQuery(id+"F23.opPattern","COPY",BODY,{"derivedFrom":makeQuery(id+"F19.opPattern","COPY",BODY,{"derivedFrom":makeQuery(id+"F17.opPattern","COPY",BODY,{"derivedFrom":makeQuery(id+"F13.opPattern","COPY",BODY,{"derivedFrom":makeQuery(id+"F5.opPattern","COPY",BODY,{"derivedFrom":makeQuery(id+"F4.opPattern","COPY",BODY,{"derivedFrom":makeQuery(id+"F1.opExtrude","SWEPT_BODY",BODY,{"disambiguationData":[OSD([sQuery(id+"F0.wireOp",EDGE,"E0.bottom"),sQuery(id+"F0.wireOp",EDGE,"E0.top"),sQuery(id+"F0.wireOp",EDGE,"E0.left"),sQuery(id+"F0.wireOp",EDGE,"E0.right")])]}),"instanceName":"1"}),"instanceName":"1"}),"instanceName":"1"}),"instanceName":"1"}),"instanceName":"1"}),"instanceName":"1"}),"instanceName":"1"});
            var Q43;
            Q43=makeQuery(id+"F23.opPattern","COPY",BODY,{"derivedFrom":makeQuery(id+"F19.opPattern","COPY",BODY,{"derivedFrom":makeQuery(id+"F17.opPattern","COPY",BODY,{"derivedFrom":makeQuery(id+"F5.opPattern","COPY",BODY,{"derivedFrom":makeQuery(id+"F4.opPattern","COPY",BODY,{"derivedFrom":makeQuery(id+"F1.opExtrude","SWEPT_BODY",BODY,{"disambiguationData":[OSD([sQuery(id+"F0.wireOp",EDGE,"E0.bottom"),sQuery(id+"F0.wireOp",EDGE,"E0.top"),sQuery(id+"F0.wireOp",EDGE,"E0.left"),sQuery(id+"F0.wireOp",EDGE,"E0.right")])]}),"instanceName":"1"}),"instanceName":"1"}),"instanceName":"1"}),"instanceName":"1"}),"instanceName":"1"});
            var Q44;
            Q44=makeQuery(id+"F23.opPattern","COPY",BODY,{"derivedFrom":makeQuery(id+"F19.opPattern","COPY",BODY,{"derivedFrom":makeQuery(id+"F17.opPattern","COPY",BODY,{"derivedFrom":makeQuery(id+"F5.opPattern","COPY",BODY,{"derivedFrom":makeQuery(id+"F4.opPattern","COPY",BODY,{"derivedFrom":makeQuery(id+"F2.opPattern","COPY",BODY,{"derivedFrom":makeQuery(id+"F1.opExtrude","SWEPT_BODY",BODY,{"disambiguationData":[OSD([sQuery(id+"F0.wireOp",EDGE,"E0.bottom"),sQuery(id+"F0.wireOp",EDGE,"E0.top"),sQuery(id+"F0.wireOp",EDGE,"E0.left"),sQuery(id+"F0.wireOp",EDGE,"E0.right")])]}),"instanceName":"1"}),"instanceName":"1"}),"instanceName":"1"}),"instanceName":"1"}),"instanceName":"1"}),"instanceName":"1"});
            var Q45;
            Q45=makeQuery(id+"F26.opPattern","COPY",BODY,{"derivedFrom":makeQuery(id+"F18.opPattern","COPY",BODY,{"derivedFrom":makeQuery(id+"F17.opPattern","COPY",BODY,{"derivedFrom":makeQuery(id+"F8.opPattern","COPY",BODY,{"derivedFrom":makeQuery(id+"F5.opPattern","COPY",BODY,{"derivedFrom":makeQuery(id+"F4.opPattern","COPY",BODY,{"derivedFrom":makeQuery(id+"F1.opExtrude","SWEPT_BODY",BODY,{"disambiguationData":[OSD([sQuery(id+"F0.wireOp",EDGE,"E0.bottom"),sQuery(id+"F0.wireOp",EDGE,"E0.top"),sQuery(id+"F0.wireOp",EDGE,"E0.left"),sQuery(id+"F0.wireOp",EDGE,"E0.right")])]}),"instanceName":"1"}),"instanceName":"1"}),"instanceName":"1"}),"instanceName":"1"}),"instanceName":"1"}),"instanceName":"1"});
            var Q46;
            Q46=makeQuery(id+"F26.opPattern","COPY",BODY,{"derivedFrom":makeQuery(id+"F17.opPattern","COPY",BODY,{"derivedFrom":makeQuery(id+"F8.opPattern","COPY",BODY,{"derivedFrom":makeQuery(id+"F5.opPattern","COPY",BODY,{"derivedFrom":makeQuery(id+"F4.opPattern","COPY",BODY,{"derivedFrom":makeQuery(id+"F1.opExtrude","SWEPT_BODY",BODY,{"disambiguationData":[OSD([sQuery(id+"F0.wireOp",EDGE,"E0.bottom"),sQuery(id+"F0.wireOp",EDGE,"E0.top"),sQuery(id+"F0.wireOp",EDGE,"E0.left"),sQuery(id+"F0.wireOp",EDGE,"E0.right")])]}),"instanceName":"1"}),"instanceName":"1"}),"instanceName":"1"}),"instanceName":"1"}),"instanceName":"1"});
            var Q47;
            Q47=makeQuery(id+"F29.opPattern","COPY",BODY,{"derivedFrom":makeQuery(id+"F26.opPattern","COPY",BODY,{"derivedFrom":makeQuery(id+"F17.opPattern","COPY",BODY,{"derivedFrom":makeQuery(id+"F15.opPattern","COPY",BODY,{"derivedFrom":makeQuery(id+"F12.opPattern","COPY",BODY,{"derivedFrom":makeQuery(id+"F6.opPattern","COPY",BODY,{"derivedFrom":makeQuery(id+"F5.opPattern","COPY",BODY,{"derivedFrom":makeQuery(id+"F4.opPattern","COPY",BODY,{"derivedFrom":makeQuery(id+"F2.opPattern","COPY",BODY,{"derivedFrom":makeQuery(id+"F1.opExtrude","SWEPT_BODY",BODY,{"disambiguationData":[OSD([sQuery(id+"F0.wireOp",EDGE,"E0.bottom"),sQuery(id+"F0.wireOp",EDGE,"E0.top"),sQuery(id+"F0.wireOp",EDGE,"E0.left"),sQuery(id+"F0.wireOp",EDGE,"E0.right")])]}),"instanceName":"1"}),"instanceName":"1"}),"instanceName":"1"}),"instanceName":"1"}),"instanceName":"1"}),"instanceName":"1"}),"instanceName":"1"}),"instanceName":"1"}),"instanceName":"1"});
            var Q48;
            Q48=makeQuery(id+"F19.opPattern","COPY",BODY,{"derivedFrom":makeQuery(id+"F12.opPattern","COPY",BODY,{"derivedFrom":makeQuery(id+"F6.opPattern","COPY",BODY,{"derivedFrom":makeQuery(id+"F5.opPattern","COPY",BODY,{"derivedFrom":makeQuery(id+"F4.opPattern","COPY",BODY,{"derivedFrom":makeQuery(id+"F1.opExtrude","SWEPT_BODY",BODY,{"disambiguationData":[OSD([sQuery(id+"F0.wireOp",EDGE,"E0.bottom"),sQuery(id+"F0.wireOp",EDGE,"E0.top"),sQuery(id+"F0.wireOp",EDGE,"E0.left"),sQuery(id+"F0.wireOp",EDGE,"E0.right")])]}),"instanceName":"1"}),"instanceName":"1"}),"instanceName":"1"}),"instanceName":"1"}),"instanceName":"1"});
            var Q49;
            Q49=makeQuery(id+"F17.opPattern","COPY",BODY,{"derivedFrom":makeQuery(id+"F13.opPattern","COPY",BODY,{"derivedFrom":makeQuery(id+"F5.opPattern","COPY",BODY,{"derivedFrom":makeQuery(id+"F4.opPattern","COPY",BODY,{"derivedFrom":makeQuery(id+"F1.opExtrude","SWEPT_BODY",BODY,{"disambiguationData":[OSD([sQuery(id+"F0.wireOp",EDGE,"E0.bottom"),sQuery(id+"F0.wireOp",EDGE,"E0.top"),sQuery(id+"F0.wireOp",EDGE,"E0.left"),sQuery(id+"F0.wireOp",EDGE,"E0.right")])]}),"instanceName":"1"}),"instanceName":"1"}),"instanceName":"1"}),"instanceName":"1"});
            var Q50;
            Q50=makeQuery(id+"F28.opPattern","COPY",BODY,{"derivedFrom":makeQuery(id+"F23.opPattern","COPY",BODY,{"derivedFrom":makeQuery(id+"F19.opPattern","COPY",BODY,{"derivedFrom":makeQuery(id+"F17.opPattern","COPY",BODY,{"derivedFrom":makeQuery(id+"F15.opPattern","COPY",BODY,{"derivedFrom":makeQuery(id+"F12.opPattern","COPY",BODY,{"derivedFrom":makeQuery(id+"F6.opPattern","COPY",BODY,{"derivedFrom":makeQuery(id+"F5.opPattern","COPY",BODY,{"derivedFrom":makeQuery(id+"F4.opPattern","COPY",BODY,{"derivedFrom":makeQuery(id+"F2.opPattern","COPY",BODY,{"derivedFrom":makeQuery(id+"F1.opExtrude","SWEPT_BODY",BODY,{"disambiguationData":[OSD([sQuery(id+"F0.wireOp",EDGE,"E0.bottom"),sQuery(id+"F0.wireOp",EDGE,"E0.top"),sQuery(id+"F0.wireOp",EDGE,"E0.left"),sQuery(id+"F0.wireOp",EDGE,"E0.right")])]}),"instanceName":"1"}),"instanceName":"1"}),"instanceName":"1"}),"instanceName":"1"}),"instanceName":"1"}),"instanceName":"1"}),"instanceName":"1"}),"instanceName":"1"}),"instanceName":"1"}),"instanceName":"1"});
            var Q51;
            Q51=makeQuery(id+"F28.opPattern","COPY",BODY,{"derivedFrom":makeQuery(id+"F19.opPattern","COPY",BODY,{"derivedFrom":makeQuery(id+"F13.opPattern","COPY",BODY,{"derivedFrom":makeQuery(id+"F5.opPattern","COPY",BODY,{"derivedFrom":makeQuery(id+"F4.opPattern","COPY",BODY,{"derivedFrom":makeQuery(id+"F1.opExtrude","SWEPT_BODY",BODY,{"disambiguationData":[OSD([sQuery(id+"F0.wireOp",EDGE,"E0.bottom"),sQuery(id+"F0.wireOp",EDGE,"E0.top"),sQuery(id+"F0.wireOp",EDGE,"E0.left"),sQuery(id+"F0.wireOp",EDGE,"E0.right")])]}),"instanceName":"1"}),"instanceName":"1"}),"instanceName":"1"}),"instanceName":"1"}),"instanceName":"1"});
            var Q52;
            Q52=makeQuery(id+"F29.opPattern","COPY",BODY,{"derivedFrom":makeQuery(id+"F19.opPattern","COPY",BODY,{"derivedFrom":makeQuery(id+"F17.opPattern","COPY",BODY,{"derivedFrom":makeQuery(id+"F13.opPattern","COPY",BODY,{"derivedFrom":makeQuery(id+"F5.opPattern","COPY",BODY,{"derivedFrom":makeQuery(id+"F4.opPattern","COPY",BODY,{"derivedFrom":makeQuery(id+"F1.opExtrude","SWEPT_BODY",BODY,{"disambiguationData":[OSD([sQuery(id+"F0.wireOp",EDGE,"E0.bottom"),sQuery(id+"F0.wireOp",EDGE,"E0.top"),sQuery(id+"F0.wireOp",EDGE,"E0.left"),sQuery(id+"F0.wireOp",EDGE,"E0.right")])]}),"instanceName":"1"}),"instanceName":"1"}),"instanceName":"1"}),"instanceName":"1"}),"instanceName":"1"}),"instanceName":"1"});
            var Q53;
            Q53=makeQuery(id+"F27.opPattern","COPY",BODY,{"derivedFrom":makeQuery(id+"F23.opPattern","COPY",BODY,{"derivedFrom":makeQuery(id+"F21.opPattern","COPY",BODY,{"derivedFrom":makeQuery(id+"F19.opPattern","COPY",BODY,{"derivedFrom":makeQuery(id+"F17.opPattern","COPY",BODY,{"derivedFrom":makeQuery(id+"F5.opPattern","COPY",BODY,{"derivedFrom":makeQuery(id+"F4.opPattern","COPY",BODY,{"derivedFrom":makeQuery(id+"F1.opExtrude","SWEPT_BODY",BODY,{"disambiguationData":[OSD([sQuery(id+"F0.wireOp",EDGE,"E0.bottom"),sQuery(id+"F0.wireOp",EDGE,"E0.top"),sQuery(id+"F0.wireOp",EDGE,"E0.left"),sQuery(id+"F0.wireOp",EDGE,"E0.right")])]}),"instanceName":"1"}),"instanceName":"1"}),"instanceName":"1"}),"instanceName":"1"}),"instanceName":"1"}),"instanceName":"1"}),"instanceName":"1"});
            var Q54;
            Q54=makeQuery(id+"F23.opPattern","COPY",BODY,{"derivedFrom":makeQuery(id+"F21.opPattern","COPY",BODY,{"derivedFrom":makeQuery(id+"F19.opPattern","COPY",BODY,{"derivedFrom":makeQuery(id+"F17.opPattern","COPY",BODY,{"derivedFrom":makeQuery(id+"F12.opPattern","COPY",BODY,{"derivedFrom":makeQuery(id+"F6.opPattern","COPY",BODY,{"derivedFrom":makeQuery(id+"F5.opPattern","COPY",BODY,{"derivedFrom":makeQuery(id+"F4.opPattern","COPY",BODY,{"derivedFrom":makeQuery(id+"F2.opPattern","COPY",BODY,{"derivedFrom":makeQuery(id+"F1.opExtrude","SWEPT_BODY",BODY,{"disambiguationData":[OSD([sQuery(id+"F0.wireOp",EDGE,"E0.bottom"),sQuery(id+"F0.wireOp",EDGE,"E0.top"),sQuery(id+"F0.wireOp",EDGE,"E0.left"),sQuery(id+"F0.wireOp",EDGE,"E0.right")])]}),"instanceName":"1"}),"instanceName":"1"}),"instanceName":"1"}),"instanceName":"1"}),"instanceName":"1"}),"instanceName":"1"}),"instanceName":"1"}),"instanceName":"1"}),"instanceName":"1"});
            var Q55;
            Q55=makeQuery(id+"F26.opPattern","COPY",BODY,{"derivedFrom":makeQuery(id+"F19.opPattern","COPY",BODY,{"derivedFrom":makeQuery(id+"F6.opPattern","COPY",BODY,{"derivedFrom":makeQuery(id+"F5.opPattern","COPY",BODY,{"derivedFrom":makeQuery(id+"F4.opPattern","COPY",BODY,{"derivedFrom":makeQuery(id+"F2.opPattern","COPY",BODY,{"derivedFrom":makeQuery(id+"F1.opExtrude","SWEPT_BODY",BODY,{"disambiguationData":[OSD([sQuery(id+"F0.wireOp",EDGE,"E0.bottom"),sQuery(id+"F0.wireOp",EDGE,"E0.top"),sQuery(id+"F0.wireOp",EDGE,"E0.left"),sQuery(id+"F0.wireOp",EDGE,"E0.right")])]}),"instanceName":"1"}),"instanceName":"1"}),"instanceName":"1"}),"instanceName":"1"}),"instanceName":"1"}),"instanceName":"1"});
            var Q56;
            Q56=makeQuery(id+"F24.opPattern","COPY",BODY,{"derivedFrom":makeQuery(id+"F23.opPattern","COPY",BODY,{"derivedFrom":makeQuery(id+"F21.opPattern","COPY",BODY,{"derivedFrom":makeQuery(id+"F19.opPattern","COPY",BODY,{"derivedFrom":makeQuery(id+"F17.opPattern","COPY",BODY,{"derivedFrom":makeQuery(id+"F12.opPattern","COPY",BODY,{"derivedFrom":makeQuery(id+"F6.opPattern","COPY",BODY,{"derivedFrom":makeQuery(id+"F5.opPattern","COPY",BODY,{"derivedFrom":makeQuery(id+"F4.opPattern","COPY",BODY,{"derivedFrom":makeQuery(id+"F1.opExtrude","SWEPT_BODY",BODY,{"disambiguationData":[OSD([sQuery(id+"F0.wireOp",EDGE,"E0.bottom"),sQuery(id+"F0.wireOp",EDGE,"E0.top"),sQuery(id+"F0.wireOp",EDGE,"E0.left"),sQuery(id+"F0.wireOp",EDGE,"E0.right")])]}),"instanceName":"1"}),"instanceName":"1"}),"instanceName":"1"}),"instanceName":"1"}),"instanceName":"1"}),"instanceName":"1"}),"instanceName":"1"}),"instanceName":"1"}),"instanceName":"1"});
            var Q57;
            Q57=makeQuery(id+"F23.opPattern","COPY",BODY,{"derivedFrom":makeQuery(id+"F21.opPattern","COPY",BODY,{"derivedFrom":makeQuery(id+"F19.opPattern","COPY",BODY,{"derivedFrom":makeQuery(id+"F17.opPattern","COPY",BODY,{"derivedFrom":makeQuery(id+"F6.opPattern","COPY",BODY,{"derivedFrom":makeQuery(id+"F5.opPattern","COPY",BODY,{"derivedFrom":makeQuery(id+"F4.opPattern","COPY",BODY,{"derivedFrom":makeQuery(id+"F1.opExtrude","SWEPT_BODY",BODY,{"disambiguationData":[OSD([sQuery(id+"F0.wireOp",EDGE,"E0.bottom"),sQuery(id+"F0.wireOp",EDGE,"E0.top"),sQuery(id+"F0.wireOp",EDGE,"E0.left"),sQuery(id+"F0.wireOp",EDGE,"E0.right")])]}),"instanceName":"1"}),"instanceName":"1"}),"instanceName":"1"}),"instanceName":"1"}),"instanceName":"1"}),"instanceName":"1"}),"instanceName":"1"});
            var Q58;
            Q58=makeQuery(id+"F19.opPattern","COPY",BODY,{"derivedFrom":makeQuery(id+"F17.opPattern","COPY",BODY,{"derivedFrom":makeQuery(id+"F5.opPattern","COPY",BODY,{"derivedFrom":makeQuery(id+"F4.opPattern","COPY",BODY,{"derivedFrom":makeQuery(id+"F1.opExtrude","SWEPT_BODY",BODY,{"disambiguationData":[OSD([sQuery(id+"F0.wireOp",EDGE,"E0.bottom"),sQuery(id+"F0.wireOp",EDGE,"E0.top"),sQuery(id+"F0.wireOp",EDGE,"E0.left"),sQuery(id+"F0.wireOp",EDGE,"E0.right")])]}),"instanceName":"1"}),"instanceName":"1"}),"instanceName":"1"}),"instanceName":"1"});
            var Q59;
            Q59=makeQuery(id+"F15.opPattern","COPY",BODY,{"derivedFrom":makeQuery(id+"F12.opPattern","COPY",BODY,{"derivedFrom":makeQuery(id+"F6.opPattern","COPY",BODY,{"derivedFrom":makeQuery(id+"F5.opPattern","COPY",BODY,{"derivedFrom":makeQuery(id+"F4.opPattern","COPY",BODY,{"derivedFrom":makeQuery(id+"F2.opPattern","COPY",BODY,{"derivedFrom":makeQuery(id+"F1.opExtrude","SWEPT_BODY",BODY,{"disambiguationData":[OSD([sQuery(id+"F0.wireOp",EDGE,"E0.bottom"),sQuery(id+"F0.wireOp",EDGE,"E0.top"),sQuery(id+"F0.wireOp",EDGE,"E0.left"),sQuery(id+"F0.wireOp",EDGE,"E0.right")])]}),"instanceName":"1"}),"instanceName":"1"}),"instanceName":"1"}),"instanceName":"1"}),"instanceName":"1"}),"instanceName":"1"});
            var Q60;
            Q60=makeQuery(id+"F19.opPattern","COPY",BODY,{"derivedFrom":makeQuery(id+"F15.opPattern","COPY",BODY,{"derivedFrom":makeQuery(id+"F12.opPattern","COPY",BODY,{"derivedFrom":makeQuery(id+"F6.opPattern","COPY",BODY,{"derivedFrom":makeQuery(id+"F5.opPattern","COPY",BODY,{"derivedFrom":makeQuery(id+"F4.opPattern","COPY",BODY,{"derivedFrom":makeQuery(id+"F2.opPattern","COPY",BODY,{"derivedFrom":makeQuery(id+"F1.opExtrude","SWEPT_BODY",BODY,{"disambiguationData":[OSD([sQuery(id+"F0.wireOp",EDGE,"E0.bottom"),sQuery(id+"F0.wireOp",EDGE,"E0.top"),sQuery(id+"F0.wireOp",EDGE,"E0.left"),sQuery(id+"F0.wireOp",EDGE,"E0.right")])]}),"instanceName":"1"}),"instanceName":"1"}),"instanceName":"1"}),"instanceName":"1"}),"instanceName":"1"}),"instanceName":"1"}),"instanceName":"1"});
            var Q61;
            Q61=makeQuery(id+"F26.opPattern","COPY",BODY,{"derivedFrom":makeQuery(id+"F19.opPattern","COPY",BODY,{"derivedFrom":makeQuery(id+"F6.opPattern","COPY",BODY,{"derivedFrom":makeQuery(id+"F5.opPattern","COPY",BODY,{"derivedFrom":makeQuery(id+"F4.opPattern","COPY",BODY,{"derivedFrom":makeQuery(id+"F1.opExtrude","SWEPT_BODY",BODY,{"disambiguationData":[OSD([sQuery(id+"F0.wireOp",EDGE,"E0.bottom"),sQuery(id+"F0.wireOp",EDGE,"E0.top"),sQuery(id+"F0.wireOp",EDGE,"E0.left"),sQuery(id+"F0.wireOp",EDGE,"E0.right")])]}),"instanceName":"1"}),"instanceName":"1"}),"instanceName":"1"}),"instanceName":"1"}),"instanceName":"1"});
            var Q62;
            Q62=makeQuery(id+"F23.opPattern","COPY",BODY,{"derivedFrom":makeQuery(id+"F21.opPattern","COPY",BODY,{"derivedFrom":makeQuery(id+"F19.opPattern","COPY",BODY,{"derivedFrom":makeQuery(id+"F17.opPattern","COPY",BODY,{"derivedFrom":makeQuery(id+"F12.opPattern","COPY",BODY,{"derivedFrom":makeQuery(id+"F6.opPattern","COPY",BODY,{"derivedFrom":makeQuery(id+"F5.opPattern","COPY",BODY,{"derivedFrom":makeQuery(id+"F4.opPattern","COPY",BODY,{"derivedFrom":makeQuery(id+"F1.opExtrude","SWEPT_BODY",BODY,{"disambiguationData":[OSD([sQuery(id+"F0.wireOp",EDGE,"E0.bottom"),sQuery(id+"F0.wireOp",EDGE,"E0.top"),sQuery(id+"F0.wireOp",EDGE,"E0.left"),sQuery(id+"F0.wireOp",EDGE,"E0.right")])]}),"instanceName":"1"}),"instanceName":"1"}),"instanceName":"1"}),"instanceName":"1"}),"instanceName":"1"}),"instanceName":"1"}),"instanceName":"1"}),"instanceName":"1"});
            var Q63;
            Q63=makeQuery(id+"F23.opPattern","COPY",BODY,{"derivedFrom":makeQuery(id+"F19.opPattern","COPY",BODY,{"derivedFrom":makeQuery(id+"F6.opPattern","COPY",BODY,{"derivedFrom":makeQuery(id+"F5.opPattern","COPY",BODY,{"derivedFrom":makeQuery(id+"F4.opPattern","COPY",BODY,{"derivedFrom":makeQuery(id+"F2.opPattern","COPY",BODY,{"derivedFrom":makeQuery(id+"F1.opExtrude","SWEPT_BODY",BODY,{"disambiguationData":[OSD([sQuery(id+"F0.wireOp",EDGE,"E0.bottom"),sQuery(id+"F0.wireOp",EDGE,"E0.top"),sQuery(id+"F0.wireOp",EDGE,"E0.left"),sQuery(id+"F0.wireOp",EDGE,"E0.right")])]}),"instanceName":"1"}),"instanceName":"1"}),"instanceName":"1"}),"instanceName":"1"}),"instanceName":"1"}),"instanceName":"1"});
            var Q64;
            Q64=makeQuery(id+"F24.opPattern","COPY",BODY,{"derivedFrom":makeQuery(id+"F23.opPattern","COPY",BODY,{"derivedFrom":makeQuery(id+"F19.opPattern","COPY",BODY,{"derivedFrom":makeQuery(id+"F5.opPattern","COPY",BODY,{"derivedFrom":makeQuery(id+"F4.opPattern","COPY",BODY,{"derivedFrom":makeQuery(id+"F2.opPattern","COPY",BODY,{"derivedFrom":makeQuery(id+"F1.opExtrude","SWEPT_BODY",BODY,{"disambiguationData":[OSD([sQuery(id+"F0.wireOp",EDGE,"E0.bottom"),sQuery(id+"F0.wireOp",EDGE,"E0.top"),sQuery(id+"F0.wireOp",EDGE,"E0.left"),sQuery(id+"F0.wireOp",EDGE,"E0.right")])]}),"instanceName":"1"}),"instanceName":"1"}),"instanceName":"1"}),"instanceName":"1"}),"instanceName":"1"}),"instanceName":"1"});
            var Q65;
            Q65=makeQuery(id+"F17.opPattern","COPY",BODY,{"derivedFrom":makeQuery(id+"F15.opPattern","COPY",BODY,{"derivedFrom":makeQuery(id+"F12.opPattern","COPY",BODY,{"derivedFrom":makeQuery(id+"F6.opPattern","COPY",BODY,{"derivedFrom":makeQuery(id+"F5.opPattern","COPY",BODY,{"derivedFrom":makeQuery(id+"F4.opPattern","COPY",BODY,{"derivedFrom":makeQuery(id+"F2.opPattern","COPY",BODY,{"derivedFrom":makeQuery(id+"F1.opExtrude","SWEPT_BODY",BODY,{"disambiguationData":[OSD([sQuery(id+"F0.wireOp",EDGE,"E0.bottom"),sQuery(id+"F0.wireOp",EDGE,"E0.top"),sQuery(id+"F0.wireOp",EDGE,"E0.left"),sQuery(id+"F0.wireOp",EDGE,"E0.right")])]}),"instanceName":"1"}),"instanceName":"1"}),"instanceName":"1"}),"instanceName":"1"}),"instanceName":"1"}),"instanceName":"1"}),"instanceName":"1"});
            var Q66;
            Q66=makeQuery(id+"F19.opPattern","COPY",BODY,{"derivedFrom":makeQuery(id+"F17.opPattern","COPY",BODY,{"derivedFrom":makeQuery(id+"F6.opPattern","COPY",BODY,{"derivedFrom":makeQuery(id+"F5.opPattern","COPY",BODY,{"derivedFrom":makeQuery(id+"F4.opPattern","COPY",BODY,{"derivedFrom":makeQuery(id+"F2.opPattern","COPY",BODY,{"derivedFrom":makeQuery(id+"F1.opExtrude","SWEPT_BODY",BODY,{"disambiguationData":[OSD([sQuery(id+"F0.wireOp",EDGE,"E0.bottom"),sQuery(id+"F0.wireOp",EDGE,"E0.top"),sQuery(id+"F0.wireOp",EDGE,"E0.left"),sQuery(id+"F0.wireOp",EDGE,"E0.right")])]}),"instanceName":"1"}),"instanceName":"1"}),"instanceName":"1"}),"instanceName":"1"}),"instanceName":"1"}),"instanceName":"1"});
            var Q67;
            Q67=makeQuery(id+"F21.opPattern","COPY",BODY,{"derivedFrom":makeQuery(id+"F19.opPattern","COPY",BODY,{"derivedFrom":makeQuery(id+"F17.opPattern","COPY",BODY,{"derivedFrom":makeQuery(id+"F6.opPattern","COPY",BODY,{"derivedFrom":makeQuery(id+"F5.opPattern","COPY",BODY,{"derivedFrom":makeQuery(id+"F4.opPattern","COPY",BODY,{"derivedFrom":makeQuery(id+"F2.opPattern","COPY",BODY,{"derivedFrom":makeQuery(id+"F1.opExtrude","SWEPT_BODY",BODY,{"disambiguationData":[OSD([sQuery(id+"F0.wireOp",EDGE,"E0.bottom"),sQuery(id+"F0.wireOp",EDGE,"E0.top"),sQuery(id+"F0.wireOp",EDGE,"E0.left"),sQuery(id+"F0.wireOp",EDGE,"E0.right")])]}),"instanceName":"1"}),"instanceName":"1"}),"instanceName":"1"}),"instanceName":"1"}),"instanceName":"1"}),"instanceName":"1"}),"instanceName":"1"});
            var Q68;
            Q68=makeQuery(id+"F23.opPattern","COPY",BODY,{"derivedFrom":makeQuery(id+"F19.opPattern","COPY",BODY,{"derivedFrom":makeQuery(id+"F17.opPattern","COPY",BODY,{"derivedFrom":makeQuery(id+"F6.opPattern","COPY",BODY,{"derivedFrom":makeQuery(id+"F5.opPattern","COPY",BODY,{"derivedFrom":makeQuery(id+"F4.opPattern","COPY",BODY,{"derivedFrom":makeQuery(id+"F2.opPattern","COPY",BODY,{"derivedFrom":makeQuery(id+"F1.opExtrude","SWEPT_BODY",BODY,{"disambiguationData":[OSD([sQuery(id+"F0.wireOp",EDGE,"E0.bottom"),sQuery(id+"F0.wireOp",EDGE,"E0.top"),sQuery(id+"F0.wireOp",EDGE,"E0.left"),sQuery(id+"F0.wireOp",EDGE,"E0.right")])]}),"instanceName":"1"}),"instanceName":"1"}),"instanceName":"1"}),"instanceName":"1"}),"instanceName":"1"}),"instanceName":"1"}),"instanceName":"1"});
            var Q69;
            Q69=makeQuery(id+"F19.opPattern","COPY",BODY,{"derivedFrom":makeQuery(id+"F12.opPattern","COPY",BODY,{"derivedFrom":makeQuery(id+"F6.opPattern","COPY",BODY,{"derivedFrom":makeQuery(id+"F5.opPattern","COPY",BODY,{"derivedFrom":makeQuery(id+"F4.opPattern","COPY",BODY,{"derivedFrom":makeQuery(id+"F2.opPattern","COPY",BODY,{"derivedFrom":makeQuery(id+"F1.opExtrude","SWEPT_BODY",BODY,{"disambiguationData":[OSD([sQuery(id+"F0.wireOp",EDGE,"E0.bottom"),sQuery(id+"F0.wireOp",EDGE,"E0.top"),sQuery(id+"F0.wireOp",EDGE,"E0.left"),sQuery(id+"F0.wireOp",EDGE,"E0.right")])]}),"instanceName":"1"}),"instanceName":"1"}),"instanceName":"1"}),"instanceName":"1"}),"instanceName":"1"}),"instanceName":"1"});
            var Q70;
            Q70=makeQuery(id+"F23.opPattern","COPY",BODY,{"derivedFrom":makeQuery(id+"F19.opPattern","COPY",BODY,{"derivedFrom":makeQuery(id+"F17.opPattern","COPY",BODY,{"derivedFrom":makeQuery(id+"F13.opPattern","COPY",BODY,{"derivedFrom":makeQuery(id+"F5.opPattern","COPY",BODY,{"derivedFrom":makeQuery(id+"F4.opPattern","COPY",BODY,{"derivedFrom":makeQuery(id+"F1.opExtrude","SWEPT_BODY",BODY,{"disambiguationData":[OSD([sQuery(id+"F0.wireOp",EDGE,"E0.bottom"),sQuery(id+"F0.wireOp",EDGE,"E0.top"),sQuery(id+"F0.wireOp",EDGE,"E0.left"),sQuery(id+"F0.wireOp",EDGE,"E0.right")])]}),"instanceName":"1"}),"instanceName":"1"}),"instanceName":"1"}),"instanceName":"1"}),"instanceName":"1"}),"instanceName":"1"});
            var Q71;
            Q71=makeQuery(id+"F19.opPattern","COPY",BODY,{"derivedFrom":makeQuery(id+"F13.opPattern","COPY",BODY,{"derivedFrom":makeQuery(id+"F5.opPattern","COPY",BODY,{"derivedFrom":makeQuery(id+"F4.opPattern","COPY",BODY,{"derivedFrom":makeQuery(id+"F1.opExtrude","SWEPT_BODY",BODY,{"disambiguationData":[OSD([sQuery(id+"F0.wireOp",EDGE,"E0.bottom"),sQuery(id+"F0.wireOp",EDGE,"E0.top"),sQuery(id+"F0.wireOp",EDGE,"E0.left"),sQuery(id+"F0.wireOp",EDGE,"E0.right")])]}),"instanceName":"1"}),"instanceName":"1"}),"instanceName":"1"}),"instanceName":"1"});
            var Q72;
            Q72=makeQuery(id+"F19.opPattern","COPY",BODY,{"derivedFrom":makeQuery(id+"F17.opPattern","COPY",BODY,{"derivedFrom":makeQuery(id+"F6.opPattern","COPY",BODY,{"derivedFrom":makeQuery(id+"F5.opPattern","COPY",BODY,{"derivedFrom":makeQuery(id+"F4.opPattern","COPY",BODY,{"derivedFrom":makeQuery(id+"F1.opExtrude","SWEPT_BODY",BODY,{"disambiguationData":[OSD([sQuery(id+"F0.wireOp",EDGE,"E0.bottom"),sQuery(id+"F0.wireOp",EDGE,"E0.top"),sQuery(id+"F0.wireOp",EDGE,"E0.left"),sQuery(id+"F0.wireOp",EDGE,"E0.right")])]}),"instanceName":"1"}),"instanceName":"1"}),"instanceName":"1"}),"instanceName":"1"}),"instanceName":"1"});
            var Q73;
            Q73=makeQuery(id+"F19.opPattern","COPY",BODY,{"derivedFrom":makeQuery(id+"F17.opPattern","COPY",BODY,{"derivedFrom":makeQuery(id+"F13.opPattern","COPY",BODY,{"derivedFrom":makeQuery(id+"F5.opPattern","COPY",BODY,{"derivedFrom":makeQuery(id+"F4.opPattern","COPY",BODY,{"derivedFrom":makeQuery(id+"F1.opExtrude","SWEPT_BODY",BODY,{"disambiguationData":[OSD([sQuery(id+"F0.wireOp",EDGE,"E0.bottom"),sQuery(id+"F0.wireOp",EDGE,"E0.top"),sQuery(id+"F0.wireOp",EDGE,"E0.left"),sQuery(id+"F0.wireOp",EDGE,"E0.right")])]}),"instanceName":"1"}),"instanceName":"1"}),"instanceName":"1"}),"instanceName":"1"}),"instanceName":"1"});
            var Q74;
            Q74=makeQuery(id+"F3.opPattern","COPY",EDGE,{"derivedFrom":makeQuery(id+"F1.opExtrude","CAP_EDGE",EDGE,{"disambiguationData":[OSD([sQuery(id+"F0.wireOp",EDGE,"E0.top")])],"isStart":false}),"instanceName":"1"});
            transform(context, id + "F40", {"entities" : qUnion([Q0, Q1, Q2, Q3, Q4, Q5, Q6, Q7, Q8, Q9, Q10, Q11, Q12, Q13, Q14, Q15, Q16, Q17, Q18, Q19, Q20, Q21, Q22, Q23, Q24, Q25, Q26, Q27, Q28, Q29, Q30, Q31, Q32, Q33, Q34, Q35, Q36, Q37, Q38, Q39, Q40, Q41, Q42, Q43, Q44, Q45, Q46, Q47, Q48, Q49, Q50, Q51, Q52, Q53, Q54, Q55, Q56, Q57, Q58, Q59, Q60, Q61, Q62, Q63, Q64, Q65, Q66, Q67, Q68, Q69, Q70, Q71, Q72, Q73]), "transformType" : TransformType.TRANSLATION_DISTANCE, "transformDirection" : qUnion([Q74]), "distance" : 270 * mm, "oppositeDirection" : true, "makeCopy" : true});
        }
        {
            var Q0;
            Q0=makeQuery(id+"F40.opPattern","COPY",BODY,{"derivedFrom":makeQuery(id+"F18.opPattern","COPY",BODY,{"derivedFrom":makeQuery(id+"F17.opPattern","COPY",BODY,{"derivedFrom":makeQuery(id+"F15.opPattern","COPY",BODY,{"derivedFrom":makeQuery(id+"F12.opPattern","COPY",BODY,{"derivedFrom":makeQuery(id+"F6.opPattern","COPY",BODY,{"derivedFrom":makeQuery(id+"F5.opPattern","COPY",BODY,{"derivedFrom":makeQuery(id+"F4.opPattern","COPY",BODY,{"derivedFrom":makeQuery(id+"F2.opPattern","COPY",BODY,{"derivedFrom":makeQuery(id+"F1.opExtrude","SWEPT_BODY",BODY,{"disambiguationData":[OSD([sQuery(id+"F0.wireOp",EDGE,"E0.bottom"),sQuery(id+"F0.wireOp",EDGE,"E0.top"),sQuery(id+"F0.wireOp",EDGE,"E0.left"),sQuery(id+"F0.wireOp",EDGE,"E0.right")])]}),"instanceName":"1"}),"instanceName":"1"}),"instanceName":"1"}),"instanceName":"1"}),"instanceName":"1"}),"instanceName":"1"}),"instanceName":"1"}),"instanceName":"1"}),"instanceName":"1"});
            var Q1;
            Q1=makeQuery(id+"F40.opPattern","COPY",BODY,{"derivedFrom":makeQuery(id+"F28.opPattern","COPY",BODY,{"derivedFrom":makeQuery(id+"F19.opPattern","COPY",BODY,{"derivedFrom":makeQuery(id+"F13.opPattern","COPY",BODY,{"derivedFrom":makeQuery(id+"F5.opPattern","COPY",BODY,{"derivedFrom":makeQuery(id+"F4.opPattern","COPY",BODY,{"derivedFrom":makeQuery(id+"F1.opExtrude","SWEPT_BODY",BODY,{"disambiguationData":[OSD([sQuery(id+"F0.wireOp",EDGE,"E0.bottom"),sQuery(id+"F0.wireOp",EDGE,"E0.top"),sQuery(id+"F0.wireOp",EDGE,"E0.left"),sQuery(id+"F0.wireOp",EDGE,"E0.right")])]}),"instanceName":"1"}),"instanceName":"1"}),"instanceName":"1"}),"instanceName":"1"}),"instanceName":"1"}),"instanceName":"1"});
            var Q2;
            Q2=makeQuery(id+"F40.opPattern","COPY",EDGE,{"derivedFrom":makeQuery(id+"F18.opPattern","COPY",EDGE,{"derivedFrom":makeQuery(id+"F17.opPattern","COPY",EDGE,{"derivedFrom":makeQuery(id+"F15.opPattern","COPY",EDGE,{"derivedFrom":makeQuery(id+"F12.opPattern","COPY",EDGE,{"derivedFrom":makeQuery(id+"F6.opPattern","COPY",EDGE,{"derivedFrom":makeQuery(id+"F5.opPattern","COPY",EDGE,{"derivedFrom":makeQuery(id+"F4.opPattern","COPY",EDGE,{"derivedFrom":makeQuery(id+"F2.opPattern","COPY",EDGE,{"derivedFrom":makeQuery(id+"F1.opExtrude","CAP_EDGE",EDGE,{"disambiguationData":[OSD([sQuery(id+"F0.wireOp",EDGE,"E0.bottom")])],"isStart":false}),"instanceName":"1"}),"instanceName":"1"}),"instanceName":"1"}),"instanceName":"1"}),"instanceName":"1"}),"instanceName":"1"}),"instanceName":"1"}),"instanceName":"1"}),"instanceName":"1"});
            transform(context, id + "F41", {"entities" : qUnion([Q0, Q1]), "transformType" : TransformType.TRANSLATION_DISTANCE, "transformDirection" : qUnion([Q2]), "distance" : 20 * mm, "oppositeDirection" : true, "makeCopy" : true});
        }
        {
            var Q0;
            Q0=makeQuery(id+"F29.opPattern","COPY",BODY,{"derivedFrom":makeQuery(id+"F28.opPattern","COPY",BODY,{"derivedFrom":makeQuery(id+"F19.opPattern","COPY",BODY,{"derivedFrom":makeQuery(id+"F17.opPattern","COPY",BODY,{"derivedFrom":makeQuery(id+"F15.opPattern","COPY",BODY,{"derivedFrom":makeQuery(id+"F12.opPattern","COPY",BODY,{"derivedFrom":makeQuery(id+"F6.opPattern","COPY",BODY,{"derivedFrom":makeQuery(id+"F5.opPattern","COPY",BODY,{"derivedFrom":makeQuery(id+"F4.opPattern","COPY",BODY,{"derivedFrom":makeQuery(id+"F2.opPattern","COPY",BODY,{"derivedFrom":makeQuery(id+"F1.opExtrude","SWEPT_BODY",BODY,{"disambiguationData":[OSD([sQuery(id+"F0.wireOp",EDGE,"E0.bottom"),sQuery(id+"F0.wireOp",EDGE,"E0.top"),sQuery(id+"F0.wireOp",EDGE,"E0.left"),sQuery(id+"F0.wireOp",EDGE,"E0.right")])]}),"instanceName":"1"}),"instanceName":"1"}),"instanceName":"1"}),"instanceName":"1"}),"instanceName":"1"}),"instanceName":"1"}),"instanceName":"1"}),"instanceName":"1"}),"instanceName":"1"}),"instanceName":"1"});
            var Q1;
            Q1=makeQuery(id+"F29.opPattern","COPY",BODY,{"derivedFrom":makeQuery(id+"F23.opPattern","COPY",BODY,{"derivedFrom":makeQuery(id+"F19.opPattern","COPY",BODY,{"derivedFrom":makeQuery(id+"F17.opPattern","COPY",BODY,{"derivedFrom":makeQuery(id+"F15.opPattern","COPY",BODY,{"derivedFrom":makeQuery(id+"F12.opPattern","COPY",BODY,{"derivedFrom":makeQuery(id+"F6.opPattern","COPY",BODY,{"derivedFrom":makeQuery(id+"F5.opPattern","COPY",BODY,{"derivedFrom":makeQuery(id+"F4.opPattern","COPY",BODY,{"derivedFrom":makeQuery(id+"F2.opPattern","COPY",BODY,{"derivedFrom":makeQuery(id+"F1.opExtrude","SWEPT_BODY",BODY,{"disambiguationData":[OSD([sQuery(id+"F0.wireOp",EDGE,"E0.bottom"),sQuery(id+"F0.wireOp",EDGE,"E0.top"),sQuery(id+"F0.wireOp",EDGE,"E0.left"),sQuery(id+"F0.wireOp",EDGE,"E0.right")])]}),"instanceName":"1"}),"instanceName":"1"}),"instanceName":"1"}),"instanceName":"1"}),"instanceName":"1"}),"instanceName":"1"}),"instanceName":"1"}),"instanceName":"1"}),"instanceName":"1"}),"instanceName":"1"});
            var Q2;
            Q2=makeQuery(id+"F29.opPattern","COPY",BODY,{"derivedFrom":makeQuery(id+"F28.opPattern","COPY",BODY,{"derivedFrom":makeQuery(id+"F23.opPattern","COPY",BODY,{"derivedFrom":makeQuery(id+"F19.opPattern","COPY",BODY,{"derivedFrom":makeQuery(id+"F17.opPattern","COPY",BODY,{"derivedFrom":makeQuery(id+"F13.opPattern","COPY",BODY,{"derivedFrom":makeQuery(id+"F5.opPattern","COPY",BODY,{"derivedFrom":makeQuery(id+"F4.opPattern","COPY",BODY,{"derivedFrom":makeQuery(id+"F1.opExtrude","SWEPT_BODY",BODY,{"disambiguationData":[OSD([sQuery(id+"F0.wireOp",EDGE,"E0.bottom"),sQuery(id+"F0.wireOp",EDGE,"E0.top"),sQuery(id+"F0.wireOp",EDGE,"E0.left"),sQuery(id+"F0.wireOp",EDGE,"E0.right")])]}),"instanceName":"1"}),"instanceName":"1"}),"instanceName":"1"}),"instanceName":"1"}),"instanceName":"1"}),"instanceName":"1"}),"instanceName":"1"}),"instanceName":"1"});
            var Q3;
            Q3=makeQuery(id+"F29.opPattern","COPY",BODY,{"derivedFrom":makeQuery(id+"F23.opPattern","COPY",BODY,{"derivedFrom":makeQuery(id+"F19.opPattern","COPY",BODY,{"derivedFrom":makeQuery(id+"F15.opPattern","COPY",BODY,{"derivedFrom":makeQuery(id+"F12.opPattern","COPY",BODY,{"derivedFrom":makeQuery(id+"F6.opPattern","COPY",BODY,{"derivedFrom":makeQuery(id+"F5.opPattern","COPY",BODY,{"derivedFrom":makeQuery(id+"F4.opPattern","COPY",BODY,{"derivedFrom":makeQuery(id+"F2.opPattern","COPY",BODY,{"derivedFrom":makeQuery(id+"F1.opExtrude","SWEPT_BODY",BODY,{"disambiguationData":[OSD([sQuery(id+"F0.wireOp",EDGE,"E0.bottom"),sQuery(id+"F0.wireOp",EDGE,"E0.top"),sQuery(id+"F0.wireOp",EDGE,"E0.left"),sQuery(id+"F0.wireOp",EDGE,"E0.right")])]}),"instanceName":"1"}),"instanceName":"1"}),"instanceName":"1"}),"instanceName":"1"}),"instanceName":"1"}),"instanceName":"1"}),"instanceName":"1"}),"instanceName":"1"}),"instanceName":"1"});
            var Q4;
            Q4=makeQuery(id+"F29.opPattern","COPY",BODY,{"derivedFrom":makeQuery(id+"F19.opPattern","COPY",BODY,{"derivedFrom":makeQuery(id+"F17.opPattern","COPY",BODY,{"derivedFrom":makeQuery(id+"F13.opPattern","COPY",BODY,{"derivedFrom":makeQuery(id+"F5.opPattern","COPY",BODY,{"derivedFrom":makeQuery(id+"F4.opPattern","COPY",BODY,{"derivedFrom":makeQuery(id+"F1.opExtrude","SWEPT_BODY",BODY,{"disambiguationData":[OSD([sQuery(id+"F0.wireOp",EDGE,"E0.bottom"),sQuery(id+"F0.wireOp",EDGE,"E0.top"),sQuery(id+"F0.wireOp",EDGE,"E0.left"),sQuery(id+"F0.wireOp",EDGE,"E0.right")])]}),"instanceName":"1"}),"instanceName":"1"}),"instanceName":"1"}),"instanceName":"1"}),"instanceName":"1"}),"instanceName":"1"});
            var Q5;
            Q5=makeQuery(id+"F29.opPattern","COPY",BODY,{"derivedFrom":makeQuery(id+"F28.opPattern","COPY",BODY,{"derivedFrom":makeQuery(id+"F26.opPattern","COPY",BODY,{"derivedFrom":makeQuery(id+"F17.opPattern","COPY",BODY,{"derivedFrom":makeQuery(id+"F13.opPattern","COPY",BODY,{"derivedFrom":makeQuery(id+"F5.opPattern","COPY",BODY,{"derivedFrom":makeQuery(id+"F4.opPattern","COPY",BODY,{"derivedFrom":makeQuery(id+"F1.opExtrude","SWEPT_BODY",BODY,{"disambiguationData":[OSD([sQuery(id+"F0.wireOp",EDGE,"E0.bottom"),sQuery(id+"F0.wireOp",EDGE,"E0.top"),sQuery(id+"F0.wireOp",EDGE,"E0.left"),sQuery(id+"F0.wireOp",EDGE,"E0.right")])]}),"instanceName":"1"}),"instanceName":"1"}),"instanceName":"1"}),"instanceName":"1"}),"instanceName":"1"}),"instanceName":"1"}),"instanceName":"1"});
            var Q6;
            Q6=makeQuery(id+"F29.opPattern","COPY",BODY,{"derivedFrom":makeQuery(id+"F28.opPattern","COPY",BODY,{"derivedFrom":makeQuery(id+"F23.opPattern","COPY",BODY,{"derivedFrom":makeQuery(id+"F19.opPattern","COPY",BODY,{"derivedFrom":makeQuery(id+"F17.opPattern","COPY",BODY,{"derivedFrom":makeQuery(id+"F15.opPattern","COPY",BODY,{"derivedFrom":makeQuery(id+"F12.opPattern","COPY",BODY,{"derivedFrom":makeQuery(id+"F6.opPattern","COPY",BODY,{"derivedFrom":makeQuery(id+"F5.opPattern","COPY",BODY,{"derivedFrom":makeQuery(id+"F4.opPattern","COPY",BODY,{"derivedFrom":makeQuery(id+"F2.opPattern","COPY",BODY,{"derivedFrom":makeQuery(id+"F1.opExtrude","SWEPT_BODY",BODY,{"disambiguationData":[OSD([sQuery(id+"F0.wireOp",EDGE,"E0.bottom"),sQuery(id+"F0.wireOp",EDGE,"E0.top"),sQuery(id+"F0.wireOp",EDGE,"E0.left"),sQuery(id+"F0.wireOp",EDGE,"E0.right")])]}),"instanceName":"1"}),"instanceName":"1"}),"instanceName":"1"}),"instanceName":"1"}),"instanceName":"1"}),"instanceName":"1"}),"instanceName":"1"}),"instanceName":"1"}),"instanceName":"1"}),"instanceName":"1"}),"instanceName":"1"});
            var Q7;
            Q7=makeQuery(id+"F23.opPattern","COPY",BODY,{"derivedFrom":makeQuery(id+"F19.opPattern","COPY",BODY,{"derivedFrom":makeQuery(id+"F12.opPattern","COPY",BODY,{"derivedFrom":makeQuery(id+"F6.opPattern","COPY",BODY,{"derivedFrom":makeQuery(id+"F5.opPattern","COPY",BODY,{"derivedFrom":makeQuery(id+"F4.opPattern","COPY",BODY,{"derivedFrom":makeQuery(id+"F2.opPattern","COPY",BODY,{"derivedFrom":makeQuery(id+"F1.opExtrude","SWEPT_BODY",BODY,{"disambiguationData":[OSD([sQuery(id+"F0.wireOp",EDGE,"E0.bottom"),sQuery(id+"F0.wireOp",EDGE,"E0.top"),sQuery(id+"F0.wireOp",EDGE,"E0.left"),sQuery(id+"F0.wireOp",EDGE,"E0.right")])]}),"instanceName":"1"}),"instanceName":"1"}),"instanceName":"1"}),"instanceName":"1"}),"instanceName":"1"}),"instanceName":"1"}),"instanceName":"1"});
            var Q8;
            Q8=makeQuery(id+"F23.opPattern","COPY",BODY,{"derivedFrom":makeQuery(id+"F19.opPattern","COPY",BODY,{"derivedFrom":makeQuery(id+"F17.opPattern","COPY",BODY,{"derivedFrom":makeQuery(id+"F13.opPattern","COPY",BODY,{"derivedFrom":makeQuery(id+"F5.opPattern","COPY",BODY,{"derivedFrom":makeQuery(id+"F4.opPattern","COPY",BODY,{"derivedFrom":makeQuery(id+"F1.opExtrude","SWEPT_BODY",BODY,{"disambiguationData":[OSD([sQuery(id+"F0.wireOp",EDGE,"E0.bottom"),sQuery(id+"F0.wireOp",EDGE,"E0.top"),sQuery(id+"F0.wireOp",EDGE,"E0.left"),sQuery(id+"F0.wireOp",EDGE,"E0.right")])]}),"instanceName":"1"}),"instanceName":"1"}),"instanceName":"1"}),"instanceName":"1"}),"instanceName":"1"}),"instanceName":"1"});
            var Q9;
            Q9=makeQuery(id+"F28.opPattern","COPY",BODY,{"derivedFrom":makeQuery(id+"F19.opPattern","COPY",BODY,{"derivedFrom":makeQuery(id+"F17.opPattern","COPY",BODY,{"derivedFrom":makeQuery(id+"F15.opPattern","COPY",BODY,{"derivedFrom":makeQuery(id+"F12.opPattern","COPY",BODY,{"derivedFrom":makeQuery(id+"F6.opPattern","COPY",BODY,{"derivedFrom":makeQuery(id+"F5.opPattern","COPY",BODY,{"derivedFrom":makeQuery(id+"F4.opPattern","COPY",BODY,{"derivedFrom":makeQuery(id+"F2.opPattern","COPY",BODY,{"derivedFrom":makeQuery(id+"F1.opExtrude","SWEPT_BODY",BODY,{"disambiguationData":[OSD([sQuery(id+"F0.wireOp",EDGE,"E0.bottom"),sQuery(id+"F0.wireOp",EDGE,"E0.top"),sQuery(id+"F0.wireOp",EDGE,"E0.left"),sQuery(id+"F0.wireOp",EDGE,"E0.right")])]}),"instanceName":"1"}),"instanceName":"1"}),"instanceName":"1"}),"instanceName":"1"}),"instanceName":"1"}),"instanceName":"1"}),"instanceName":"1"}),"instanceName":"1"}),"instanceName":"1"});
            var Q10;
            Q10=makeQuery(id+"F23.opPattern","COPY",BODY,{"derivedFrom":makeQuery(id+"F19.opPattern","COPY",BODY,{"derivedFrom":makeQuery(id+"F15.opPattern","COPY",BODY,{"derivedFrom":makeQuery(id+"F12.opPattern","COPY",BODY,{"derivedFrom":makeQuery(id+"F6.opPattern","COPY",BODY,{"derivedFrom":makeQuery(id+"F5.opPattern","COPY",BODY,{"derivedFrom":makeQuery(id+"F4.opPattern","COPY",BODY,{"derivedFrom":makeQuery(id+"F2.opPattern","COPY",BODY,{"derivedFrom":makeQuery(id+"F1.opExtrude","SWEPT_BODY",BODY,{"disambiguationData":[OSD([sQuery(id+"F0.wireOp",EDGE,"E0.bottom"),sQuery(id+"F0.wireOp",EDGE,"E0.top"),sQuery(id+"F0.wireOp",EDGE,"E0.left"),sQuery(id+"F0.wireOp",EDGE,"E0.right")])]}),"instanceName":"1"}),"instanceName":"1"}),"instanceName":"1"}),"instanceName":"1"}),"instanceName":"1"}),"instanceName":"1"}),"instanceName":"1"}),"instanceName":"1"});
            var Q11;
            Q11=makeQuery(id+"F29.opPattern","COPY",BODY,{"derivedFrom":makeQuery(id+"F19.opPattern","COPY",BODY,{"derivedFrom":makeQuery(id+"F15.opPattern","COPY",BODY,{"derivedFrom":makeQuery(id+"F12.opPattern","COPY",BODY,{"derivedFrom":makeQuery(id+"F6.opPattern","COPY",BODY,{"derivedFrom":makeQuery(id+"F5.opPattern","COPY",BODY,{"derivedFrom":makeQuery(id+"F4.opPattern","COPY",BODY,{"derivedFrom":makeQuery(id+"F2.opPattern","COPY",BODY,{"derivedFrom":makeQuery(id+"F1.opExtrude","SWEPT_BODY",BODY,{"disambiguationData":[OSD([sQuery(id+"F0.wireOp",EDGE,"E0.bottom"),sQuery(id+"F0.wireOp",EDGE,"E0.top"),sQuery(id+"F0.wireOp",EDGE,"E0.left"),sQuery(id+"F0.wireOp",EDGE,"E0.right")])]}),"instanceName":"1"}),"instanceName":"1"}),"instanceName":"1"}),"instanceName":"1"}),"instanceName":"1"}),"instanceName":"1"}),"instanceName":"1"}),"instanceName":"1"});
            var Q12;
            Q12=makeQuery(id+"F29.opPattern","COPY",BODY,{"derivedFrom":makeQuery(id+"F28.opPattern","COPY",BODY,{"derivedFrom":makeQuery(id+"F23.opPattern","COPY",BODY,{"derivedFrom":makeQuery(id+"F19.opPattern","COPY",BODY,{"derivedFrom":makeQuery(id+"F15.opPattern","COPY",BODY,{"derivedFrom":makeQuery(id+"F12.opPattern","COPY",BODY,{"derivedFrom":makeQuery(id+"F6.opPattern","COPY",BODY,{"derivedFrom":makeQuery(id+"F5.opPattern","COPY",BODY,{"derivedFrom":makeQuery(id+"F4.opPattern","COPY",BODY,{"derivedFrom":makeQuery(id+"F2.opPattern","COPY",BODY,{"derivedFrom":makeQuery(id+"F1.opExtrude","SWEPT_BODY",BODY,{"disambiguationData":[OSD([sQuery(id+"F0.wireOp",EDGE,"E0.bottom"),sQuery(id+"F0.wireOp",EDGE,"E0.top"),sQuery(id+"F0.wireOp",EDGE,"E0.left"),sQuery(id+"F0.wireOp",EDGE,"E0.right")])]}),"instanceName":"1"}),"instanceName":"1"}),"instanceName":"1"}),"instanceName":"1"}),"instanceName":"1"}),"instanceName":"1"}),"instanceName":"1"}),"instanceName":"1"}),"instanceName":"1"}),"instanceName":"1"});
            var Q13;
            Q13=makeQuery(id+"F28.opPattern","COPY",BODY,{"derivedFrom":makeQuery(id+"F23.opPattern","COPY",BODY,{"derivedFrom":makeQuery(id+"F19.opPattern","COPY",BODY,{"derivedFrom":makeQuery(id+"F15.opPattern","COPY",BODY,{"derivedFrom":makeQuery(id+"F12.opPattern","COPY",BODY,{"derivedFrom":makeQuery(id+"F6.opPattern","COPY",BODY,{"derivedFrom":makeQuery(id+"F5.opPattern","COPY",BODY,{"derivedFrom":makeQuery(id+"F4.opPattern","COPY",BODY,{"derivedFrom":makeQuery(id+"F2.opPattern","COPY",BODY,{"derivedFrom":makeQuery(id+"F1.opExtrude","SWEPT_BODY",BODY,{"disambiguationData":[OSD([sQuery(id+"F0.wireOp",EDGE,"E0.bottom"),sQuery(id+"F0.wireOp",EDGE,"E0.top"),sQuery(id+"F0.wireOp",EDGE,"E0.left"),sQuery(id+"F0.wireOp",EDGE,"E0.right")])]}),"instanceName":"1"}),"instanceName":"1"}),"instanceName":"1"}),"instanceName":"1"}),"instanceName":"1"}),"instanceName":"1"}),"instanceName":"1"}),"instanceName":"1"}),"instanceName":"1"});
            var Q14;
            Q14=makeQuery(id+"F29.opPattern","COPY",BODY,{"derivedFrom":makeQuery(id+"F28.opPattern","COPY",BODY,{"derivedFrom":makeQuery(id+"F19.opPattern","COPY",BODY,{"derivedFrom":makeQuery(id+"F17.opPattern","COPY",BODY,{"derivedFrom":makeQuery(id+"F13.opPattern","COPY",BODY,{"derivedFrom":makeQuery(id+"F5.opPattern","COPY",BODY,{"derivedFrom":makeQuery(id+"F4.opPattern","COPY",BODY,{"derivedFrom":makeQuery(id+"F1.opExtrude","SWEPT_BODY",BODY,{"disambiguationData":[OSD([sQuery(id+"F0.wireOp",EDGE,"E0.bottom"),sQuery(id+"F0.wireOp",EDGE,"E0.top"),sQuery(id+"F0.wireOp",EDGE,"E0.left"),sQuery(id+"F0.wireOp",EDGE,"E0.right")])]}),"instanceName":"1"}),"instanceName":"1"}),"instanceName":"1"}),"instanceName":"1"}),"instanceName":"1"}),"instanceName":"1"}),"instanceName":"1"});
            var Q15;
            Q15=makeQuery(id+"F29.opPattern","COPY",BODY,{"derivedFrom":makeQuery(id+"F23.opPattern","COPY",BODY,{"derivedFrom":makeQuery(id+"F19.opPattern","COPY",BODY,{"derivedFrom":makeQuery(id+"F17.opPattern","COPY",BODY,{"derivedFrom":makeQuery(id+"F13.opPattern","COPY",BODY,{"derivedFrom":makeQuery(id+"F5.opPattern","COPY",BODY,{"derivedFrom":makeQuery(id+"F4.opPattern","COPY",BODY,{"derivedFrom":makeQuery(id+"F1.opExtrude","SWEPT_BODY",BODY,{"disambiguationData":[OSD([sQuery(id+"F0.wireOp",EDGE,"E0.bottom"),sQuery(id+"F0.wireOp",EDGE,"E0.top"),sQuery(id+"F0.wireOp",EDGE,"E0.left"),sQuery(id+"F0.wireOp",EDGE,"E0.right")])]}),"instanceName":"1"}),"instanceName":"1"}),"instanceName":"1"}),"instanceName":"1"}),"instanceName":"1"}),"instanceName":"1"}),"instanceName":"1"});
            var Q16;
            Q16=makeQuery(id+"F28.opPattern","COPY",BODY,{"derivedFrom":makeQuery(id+"F23.opPattern","COPY",BODY,{"derivedFrom":makeQuery(id+"F19.opPattern","COPY",BODY,{"derivedFrom":makeQuery(id+"F17.opPattern","COPY",BODY,{"derivedFrom":makeQuery(id+"F13.opPattern","COPY",BODY,{"derivedFrom":makeQuery(id+"F5.opPattern","COPY",BODY,{"derivedFrom":makeQuery(id+"F4.opPattern","COPY",BODY,{"derivedFrom":makeQuery(id+"F1.opExtrude","SWEPT_BODY",BODY,{"disambiguationData":[OSD([sQuery(id+"F0.wireOp",EDGE,"E0.bottom"),sQuery(id+"F0.wireOp",EDGE,"E0.top"),sQuery(id+"F0.wireOp",EDGE,"E0.left"),sQuery(id+"F0.wireOp",EDGE,"E0.right")])]}),"instanceName":"1"}),"instanceName":"1"}),"instanceName":"1"}),"instanceName":"1"}),"instanceName":"1"}),"instanceName":"1"}),"instanceName":"1"});
            var Q17;
            Q17=makeQuery(id+"F29.opPattern","COPY",BODY,{"derivedFrom":makeQuery(id+"F19.opPattern","COPY",BODY,{"derivedFrom":makeQuery(id+"F17.opPattern","COPY",BODY,{"derivedFrom":makeQuery(id+"F15.opPattern","COPY",BODY,{"derivedFrom":makeQuery(id+"F12.opPattern","COPY",BODY,{"derivedFrom":makeQuery(id+"F6.opPattern","COPY",BODY,{"derivedFrom":makeQuery(id+"F5.opPattern","COPY",BODY,{"derivedFrom":makeQuery(id+"F4.opPattern","COPY",BODY,{"derivedFrom":makeQuery(id+"F2.opPattern","COPY",BODY,{"derivedFrom":makeQuery(id+"F1.opExtrude","SWEPT_BODY",BODY,{"disambiguationData":[OSD([sQuery(id+"F0.wireOp",EDGE,"E0.bottom"),sQuery(id+"F0.wireOp",EDGE,"E0.top"),sQuery(id+"F0.wireOp",EDGE,"E0.left"),sQuery(id+"F0.wireOp",EDGE,"E0.right")])]}),"instanceName":"1"}),"instanceName":"1"}),"instanceName":"1"}),"instanceName":"1"}),"instanceName":"1"}),"instanceName":"1"}),"instanceName":"1"}),"instanceName":"1"}),"instanceName":"1"});
            var Q18;
            Q18=makeQuery(id+"F29.opPattern","COPY",EDGE,{"derivedFrom":makeQuery(id+"F28.opPattern","COPY",EDGE,{"derivedFrom":makeQuery(id+"F19.opPattern","COPY",EDGE,{"derivedFrom":makeQuery(id+"F15.opPattern","COPY",EDGE,{"derivedFrom":makeQuery(id+"F12.opPattern","COPY",EDGE,{"derivedFrom":makeQuery(id+"F6.opPattern","COPY",EDGE,{"derivedFrom":makeQuery(id+"F5.opPattern","COPY",EDGE,{"derivedFrom":makeQuery(id+"F4.opPattern","COPY",EDGE,{"derivedFrom":makeQuery(id+"F2.opPattern","COPY",EDGE,{"derivedFrom":makeQuery(id+"F1.opExtrude","CAP_EDGE",EDGE,{"disambiguationData":[OSD([sQuery(id+"F0.wireOp",EDGE,"E0.bottom")])],"isStart":false}),"instanceName":"1"}),"instanceName":"1"}),"instanceName":"1"}),"instanceName":"1"}),"instanceName":"1"}),"instanceName":"1"}),"instanceName":"1"}),"instanceName":"1"}),"instanceName":"1"});
            transform(context, id + "F42", {"entities" : qUnion([Q0, Q1, Q2, Q3, Q4, Q5, Q6, Q7, Q8, Q9, Q10, Q11, Q12, Q13, Q14, Q15, Q16, Q17]), "transformType" : TransformType.TRANSLATION_DISTANCE, "transformDirection" : qUnion([Q18]), "distance" : 190 * mm, "oppositeDirection" : true, "makeCopy" : true});
        }
        {
            var Q0;
            Q0=makeQuery(id+"F42.opPattern","COPY",BODY,{"derivedFrom":makeQuery(id+"F29.opPattern","COPY",BODY,{"derivedFrom":makeQuery(id+"F28.opPattern","COPY",BODY,{"derivedFrom":makeQuery(id+"F23.opPattern","COPY",BODY,{"derivedFrom":makeQuery(id+"F19.opPattern","COPY",BODY,{"derivedFrom":makeQuery(id+"F17.opPattern","COPY",BODY,{"derivedFrom":makeQuery(id+"F15.opPattern","COPY",BODY,{"derivedFrom":makeQuery(id+"F12.opPattern","COPY",BODY,{"derivedFrom":makeQuery(id+"F6.opPattern","COPY",BODY,{"derivedFrom":makeQuery(id+"F5.opPattern","COPY",BODY,{"derivedFrom":makeQuery(id+"F4.opPattern","COPY",BODY,{"derivedFrom":makeQuery(id+"F2.opPattern","COPY",BODY,{"derivedFrom":makeQuery(id+"F1.opExtrude","SWEPT_BODY",BODY,{"disambiguationData":[OSD([sQuery(id+"F0.wireOp",EDGE,"E0.bottom"),sQuery(id+"F0.wireOp",EDGE,"E0.top"),sQuery(id+"F0.wireOp",EDGE,"E0.left"),sQuery(id+"F0.wireOp",EDGE,"E0.right")])]}),"instanceName":"1"}),"instanceName":"1"}),"instanceName":"1"}),"instanceName":"1"}),"instanceName":"1"}),"instanceName":"1"}),"instanceName":"1"}),"instanceName":"1"}),"instanceName":"1"}),"instanceName":"1"}),"instanceName":"1"}),"instanceName":"1"});
            var Q1;
            Q1=makeQuery(id+"F42.opPattern","COPY",BODY,{"derivedFrom":makeQuery(id+"F29.opPattern","COPY",BODY,{"derivedFrom":makeQuery(id+"F19.opPattern","COPY",BODY,{"derivedFrom":makeQuery(id+"F17.opPattern","COPY",BODY,{"derivedFrom":makeQuery(id+"F15.opPattern","COPY",BODY,{"derivedFrom":makeQuery(id+"F12.opPattern","COPY",BODY,{"derivedFrom":makeQuery(id+"F6.opPattern","COPY",BODY,{"derivedFrom":makeQuery(id+"F5.opPattern","COPY",BODY,{"derivedFrom":makeQuery(id+"F4.opPattern","COPY",BODY,{"derivedFrom":makeQuery(id+"F2.opPattern","COPY",BODY,{"derivedFrom":makeQuery(id+"F1.opExtrude","SWEPT_BODY",BODY,{"disambiguationData":[OSD([sQuery(id+"F0.wireOp",EDGE,"E0.bottom"),sQuery(id+"F0.wireOp",EDGE,"E0.top"),sQuery(id+"F0.wireOp",EDGE,"E0.left"),sQuery(id+"F0.wireOp",EDGE,"E0.right")])]}),"instanceName":"1"}),"instanceName":"1"}),"instanceName":"1"}),"instanceName":"1"}),"instanceName":"1"}),"instanceName":"1"}),"instanceName":"1"}),"instanceName":"1"}),"instanceName":"1"}),"instanceName":"1"});
            var Q2;
            Q2=makeQuery(id+"F42.opPattern","COPY",BODY,{"derivedFrom":makeQuery(id+"F29.opPattern","COPY",BODY,{"derivedFrom":makeQuery(id+"F23.opPattern","COPY",BODY,{"derivedFrom":makeQuery(id+"F19.opPattern","COPY",BODY,{"derivedFrom":makeQuery(id+"F17.opPattern","COPY",BODY,{"derivedFrom":makeQuery(id+"F13.opPattern","COPY",BODY,{"derivedFrom":makeQuery(id+"F5.opPattern","COPY",BODY,{"derivedFrom":makeQuery(id+"F4.opPattern","COPY",BODY,{"derivedFrom":makeQuery(id+"F1.opExtrude","SWEPT_BODY",BODY,{"disambiguationData":[OSD([sQuery(id+"F0.wireOp",EDGE,"E0.bottom"),sQuery(id+"F0.wireOp",EDGE,"E0.top"),sQuery(id+"F0.wireOp",EDGE,"E0.left"),sQuery(id+"F0.wireOp",EDGE,"E0.right")])]}),"instanceName":"1"}),"instanceName":"1"}),"instanceName":"1"}),"instanceName":"1"}),"instanceName":"1"}),"instanceName":"1"}),"instanceName":"1"}),"instanceName":"1"});
            var Q3;
            Q3=makeQuery(id+"F42.opPattern","COPY",BODY,{"derivedFrom":makeQuery(id+"F29.opPattern","COPY",BODY,{"derivedFrom":makeQuery(id+"F28.opPattern","COPY",BODY,{"derivedFrom":makeQuery(id+"F23.opPattern","COPY",BODY,{"derivedFrom":makeQuery(id+"F19.opPattern","COPY",BODY,{"derivedFrom":makeQuery(id+"F17.opPattern","COPY",BODY,{"derivedFrom":makeQuery(id+"F13.opPattern","COPY",BODY,{"derivedFrom":makeQuery(id+"F5.opPattern","COPY",BODY,{"derivedFrom":makeQuery(id+"F4.opPattern","COPY",BODY,{"derivedFrom":makeQuery(id+"F1.opExtrude","SWEPT_BODY",BODY,{"disambiguationData":[OSD([sQuery(id+"F0.wireOp",EDGE,"E0.bottom"),sQuery(id+"F0.wireOp",EDGE,"E0.top"),sQuery(id+"F0.wireOp",EDGE,"E0.left"),sQuery(id+"F0.wireOp",EDGE,"E0.right")])]}),"instanceName":"1"}),"instanceName":"1"}),"instanceName":"1"}),"instanceName":"1"}),"instanceName":"1"}),"instanceName":"1"}),"instanceName":"1"}),"instanceName":"1"}),"instanceName":"1"});
            var Q4;
            Q4=makeQuery(id+"F42.opPattern","COPY",BODY,{"derivedFrom":makeQuery(id+"F23.opPattern","COPY",BODY,{"derivedFrom":makeQuery(id+"F19.opPattern","COPY",BODY,{"derivedFrom":makeQuery(id+"F17.opPattern","COPY",BODY,{"derivedFrom":makeQuery(id+"F13.opPattern","COPY",BODY,{"derivedFrom":makeQuery(id+"F5.opPattern","COPY",BODY,{"derivedFrom":makeQuery(id+"F4.opPattern","COPY",BODY,{"derivedFrom":makeQuery(id+"F1.opExtrude","SWEPT_BODY",BODY,{"disambiguationData":[OSD([sQuery(id+"F0.wireOp",EDGE,"E0.bottom"),sQuery(id+"F0.wireOp",EDGE,"E0.top"),sQuery(id+"F0.wireOp",EDGE,"E0.left"),sQuery(id+"F0.wireOp",EDGE,"E0.right")])]}),"instanceName":"1"}),"instanceName":"1"}),"instanceName":"1"}),"instanceName":"1"}),"instanceName":"1"}),"instanceName":"1"}),"instanceName":"1"});
            var Q5;
            Q5=makeQuery(id+"F42.opPattern","COPY",BODY,{"derivedFrom":makeQuery(id+"F29.opPattern","COPY",BODY,{"derivedFrom":makeQuery(id+"F28.opPattern","COPY",BODY,{"derivedFrom":makeQuery(id+"F26.opPattern","COPY",BODY,{"derivedFrom":makeQuery(id+"F17.opPattern","COPY",BODY,{"derivedFrom":makeQuery(id+"F13.opPattern","COPY",BODY,{"derivedFrom":makeQuery(id+"F5.opPattern","COPY",BODY,{"derivedFrom":makeQuery(id+"F4.opPattern","COPY",BODY,{"derivedFrom":makeQuery(id+"F1.opExtrude","SWEPT_BODY",BODY,{"disambiguationData":[OSD([sQuery(id+"F0.wireOp",EDGE,"E0.bottom"),sQuery(id+"F0.wireOp",EDGE,"E0.top"),sQuery(id+"F0.wireOp",EDGE,"E0.left"),sQuery(id+"F0.wireOp",EDGE,"E0.right")])]}),"instanceName":"1"}),"instanceName":"1"}),"instanceName":"1"}),"instanceName":"1"}),"instanceName":"1"}),"instanceName":"1"}),"instanceName":"1"}),"instanceName":"1"});
            var Q6;
            Q6=makeQuery(id+"F42.opPattern","COPY",BODY,{"derivedFrom":makeQuery(id+"F29.opPattern","COPY",BODY,{"derivedFrom":makeQuery(id+"F28.opPattern","COPY",BODY,{"derivedFrom":makeQuery(id+"F23.opPattern","COPY",BODY,{"derivedFrom":makeQuery(id+"F19.opPattern","COPY",BODY,{"derivedFrom":makeQuery(id+"F15.opPattern","COPY",BODY,{"derivedFrom":makeQuery(id+"F12.opPattern","COPY",BODY,{"derivedFrom":makeQuery(id+"F6.opPattern","COPY",BODY,{"derivedFrom":makeQuery(id+"F5.opPattern","COPY",BODY,{"derivedFrom":makeQuery(id+"F4.opPattern","COPY",BODY,{"derivedFrom":makeQuery(id+"F2.opPattern","COPY",BODY,{"derivedFrom":makeQuery(id+"F1.opExtrude","SWEPT_BODY",BODY,{"disambiguationData":[OSD([sQuery(id+"F0.wireOp",EDGE,"E0.bottom"),sQuery(id+"F0.wireOp",EDGE,"E0.top"),sQuery(id+"F0.wireOp",EDGE,"E0.left"),sQuery(id+"F0.wireOp",EDGE,"E0.right")])]}),"instanceName":"1"}),"instanceName":"1"}),"instanceName":"1"}),"instanceName":"1"}),"instanceName":"1"}),"instanceName":"1"}),"instanceName":"1"}),"instanceName":"1"}),"instanceName":"1"}),"instanceName":"1"}),"instanceName":"1"});
            var Q7;
            Q7=makeQuery(id+"F42.opPattern","COPY",BODY,{"derivedFrom":makeQuery(id+"F29.opPattern","COPY",BODY,{"derivedFrom":makeQuery(id+"F23.opPattern","COPY",BODY,{"derivedFrom":makeQuery(id+"F19.opPattern","COPY",BODY,{"derivedFrom":makeQuery(id+"F15.opPattern","COPY",BODY,{"derivedFrom":makeQuery(id+"F12.opPattern","COPY",BODY,{"derivedFrom":makeQuery(id+"F6.opPattern","COPY",BODY,{"derivedFrom":makeQuery(id+"F5.opPattern","COPY",BODY,{"derivedFrom":makeQuery(id+"F4.opPattern","COPY",BODY,{"derivedFrom":makeQuery(id+"F2.opPattern","COPY",BODY,{"derivedFrom":makeQuery(id+"F1.opExtrude","SWEPT_BODY",BODY,{"disambiguationData":[OSD([sQuery(id+"F0.wireOp",EDGE,"E0.bottom"),sQuery(id+"F0.wireOp",EDGE,"E0.top"),sQuery(id+"F0.wireOp",EDGE,"E0.left"),sQuery(id+"F0.wireOp",EDGE,"E0.right")])]}),"instanceName":"1"}),"instanceName":"1"}),"instanceName":"1"}),"instanceName":"1"}),"instanceName":"1"}),"instanceName":"1"}),"instanceName":"1"}),"instanceName":"1"}),"instanceName":"1"}),"instanceName":"1"});
            var Q8;
            Q8=makeQuery(id+"F42.opPattern","COPY",BODY,{"derivedFrom":makeQuery(id+"F29.opPattern","COPY",BODY,{"derivedFrom":makeQuery(id+"F23.opPattern","COPY",BODY,{"derivedFrom":makeQuery(id+"F19.opPattern","COPY",BODY,{"derivedFrom":makeQuery(id+"F17.opPattern","COPY",BODY,{"derivedFrom":makeQuery(id+"F15.opPattern","COPY",BODY,{"derivedFrom":makeQuery(id+"F12.opPattern","COPY",BODY,{"derivedFrom":makeQuery(id+"F6.opPattern","COPY",BODY,{"derivedFrom":makeQuery(id+"F5.opPattern","COPY",BODY,{"derivedFrom":makeQuery(id+"F4.opPattern","COPY",BODY,{"derivedFrom":makeQuery(id+"F2.opPattern","COPY",BODY,{"derivedFrom":makeQuery(id+"F1.opExtrude","SWEPT_BODY",BODY,{"disambiguationData":[OSD([sQuery(id+"F0.wireOp",EDGE,"E0.bottom"),sQuery(id+"F0.wireOp",EDGE,"E0.top"),sQuery(id+"F0.wireOp",EDGE,"E0.left"),sQuery(id+"F0.wireOp",EDGE,"E0.right")])]}),"instanceName":"1"}),"instanceName":"1"}),"instanceName":"1"}),"instanceName":"1"}),"instanceName":"1"}),"instanceName":"1"}),"instanceName":"1"}),"instanceName":"1"}),"instanceName":"1"}),"instanceName":"1"}),"instanceName":"1"});
            var Q9;
            Q9=makeQuery(id+"F42.opPattern","COPY",BODY,{"derivedFrom":makeQuery(id+"F29.opPattern","COPY",BODY,{"derivedFrom":makeQuery(id+"F19.opPattern","COPY",BODY,{"derivedFrom":makeQuery(id+"F17.opPattern","COPY",BODY,{"derivedFrom":makeQuery(id+"F13.opPattern","COPY",BODY,{"derivedFrom":makeQuery(id+"F5.opPattern","COPY",BODY,{"derivedFrom":makeQuery(id+"F4.opPattern","COPY",BODY,{"derivedFrom":makeQuery(id+"F1.opExtrude","SWEPT_BODY",BODY,{"disambiguationData":[OSD([sQuery(id+"F0.wireOp",EDGE,"E0.bottom"),sQuery(id+"F0.wireOp",EDGE,"E0.top"),sQuery(id+"F0.wireOp",EDGE,"E0.left"),sQuery(id+"F0.wireOp",EDGE,"E0.right")])]}),"instanceName":"1"}),"instanceName":"1"}),"instanceName":"1"}),"instanceName":"1"}),"instanceName":"1"}),"instanceName":"1"}),"instanceName":"1"});
            var Q10;
            Q10=makeQuery(id+"F42.opPattern","COPY",BODY,{"derivedFrom":makeQuery(id+"F23.opPattern","COPY",BODY,{"derivedFrom":makeQuery(id+"F19.opPattern","COPY",BODY,{"derivedFrom":makeQuery(id+"F15.opPattern","COPY",BODY,{"derivedFrom":makeQuery(id+"F12.opPattern","COPY",BODY,{"derivedFrom":makeQuery(id+"F6.opPattern","COPY",BODY,{"derivedFrom":makeQuery(id+"F5.opPattern","COPY",BODY,{"derivedFrom":makeQuery(id+"F4.opPattern","COPY",BODY,{"derivedFrom":makeQuery(id+"F2.opPattern","COPY",BODY,{"derivedFrom":makeQuery(id+"F1.opExtrude","SWEPT_BODY",BODY,{"disambiguationData":[OSD([sQuery(id+"F0.wireOp",EDGE,"E0.bottom"),sQuery(id+"F0.wireOp",EDGE,"E0.top"),sQuery(id+"F0.wireOp",EDGE,"E0.left"),sQuery(id+"F0.wireOp",EDGE,"E0.right")])]}),"instanceName":"1"}),"instanceName":"1"}),"instanceName":"1"}),"instanceName":"1"}),"instanceName":"1"}),"instanceName":"1"}),"instanceName":"1"}),"instanceName":"1"}),"instanceName":"1"});
            var Q11;
            Q11=makeQuery(id+"F42.opPattern","COPY",BODY,{"derivedFrom":makeQuery(id+"F29.opPattern","COPY",BODY,{"derivedFrom":makeQuery(id+"F28.opPattern","COPY",BODY,{"derivedFrom":makeQuery(id+"F19.opPattern","COPY",BODY,{"derivedFrom":makeQuery(id+"F17.opPattern","COPY",BODY,{"derivedFrom":makeQuery(id+"F13.opPattern","COPY",BODY,{"derivedFrom":makeQuery(id+"F5.opPattern","COPY",BODY,{"derivedFrom":makeQuery(id+"F4.opPattern","COPY",BODY,{"derivedFrom":makeQuery(id+"F1.opExtrude","SWEPT_BODY",BODY,{"disambiguationData":[OSD([sQuery(id+"F0.wireOp",EDGE,"E0.bottom"),sQuery(id+"F0.wireOp",EDGE,"E0.top"),sQuery(id+"F0.wireOp",EDGE,"E0.left"),sQuery(id+"F0.wireOp",EDGE,"E0.right")])]}),"instanceName":"1"}),"instanceName":"1"}),"instanceName":"1"}),"instanceName":"1"}),"instanceName":"1"}),"instanceName":"1"}),"instanceName":"1"}),"instanceName":"1"});
            var Q12;
            Q12=makeQuery(id+"F42.opPattern","COPY",BODY,{"derivedFrom":makeQuery(id+"F28.opPattern","COPY",BODY,{"derivedFrom":makeQuery(id+"F19.opPattern","COPY",BODY,{"derivedFrom":makeQuery(id+"F17.opPattern","COPY",BODY,{"derivedFrom":makeQuery(id+"F15.opPattern","COPY",BODY,{"derivedFrom":makeQuery(id+"F12.opPattern","COPY",BODY,{"derivedFrom":makeQuery(id+"F6.opPattern","COPY",BODY,{"derivedFrom":makeQuery(id+"F5.opPattern","COPY",BODY,{"derivedFrom":makeQuery(id+"F4.opPattern","COPY",BODY,{"derivedFrom":makeQuery(id+"F2.opPattern","COPY",BODY,{"derivedFrom":makeQuery(id+"F1.opExtrude","SWEPT_BODY",BODY,{"disambiguationData":[OSD([sQuery(id+"F0.wireOp",EDGE,"E0.bottom"),sQuery(id+"F0.wireOp",EDGE,"E0.top"),sQuery(id+"F0.wireOp",EDGE,"E0.left"),sQuery(id+"F0.wireOp",EDGE,"E0.right")])]}),"instanceName":"1"}),"instanceName":"1"}),"instanceName":"1"}),"instanceName":"1"}),"instanceName":"1"}),"instanceName":"1"}),"instanceName":"1"}),"instanceName":"1"}),"instanceName":"1"}),"instanceName":"1"});
            var Q13;
            Q13=makeQuery(id+"F42.opPattern","COPY",BODY,{"derivedFrom":makeQuery(id+"F29.opPattern","COPY",BODY,{"derivedFrom":makeQuery(id+"F19.opPattern","COPY",BODY,{"derivedFrom":makeQuery(id+"F15.opPattern","COPY",BODY,{"derivedFrom":makeQuery(id+"F12.opPattern","COPY",BODY,{"derivedFrom":makeQuery(id+"F6.opPattern","COPY",BODY,{"derivedFrom":makeQuery(id+"F5.opPattern","COPY",BODY,{"derivedFrom":makeQuery(id+"F4.opPattern","COPY",BODY,{"derivedFrom":makeQuery(id+"F2.opPattern","COPY",BODY,{"derivedFrom":makeQuery(id+"F1.opExtrude","SWEPT_BODY",BODY,{"disambiguationData":[OSD([sQuery(id+"F0.wireOp",EDGE,"E0.bottom"),sQuery(id+"F0.wireOp",EDGE,"E0.top"),sQuery(id+"F0.wireOp",EDGE,"E0.left"),sQuery(id+"F0.wireOp",EDGE,"E0.right")])]}),"instanceName":"1"}),"instanceName":"1"}),"instanceName":"1"}),"instanceName":"1"}),"instanceName":"1"}),"instanceName":"1"}),"instanceName":"1"}),"instanceName":"1"}),"instanceName":"1"});
            var Q14;
            Q14=makeQuery(id+"F42.opPattern","COPY",BODY,{"derivedFrom":makeQuery(id+"F23.opPattern","COPY",BODY,{"derivedFrom":makeQuery(id+"F19.opPattern","COPY",BODY,{"derivedFrom":makeQuery(id+"F12.opPattern","COPY",BODY,{"derivedFrom":makeQuery(id+"F6.opPattern","COPY",BODY,{"derivedFrom":makeQuery(id+"F5.opPattern","COPY",BODY,{"derivedFrom":makeQuery(id+"F4.opPattern","COPY",BODY,{"derivedFrom":makeQuery(id+"F2.opPattern","COPY",BODY,{"derivedFrom":makeQuery(id+"F1.opExtrude","SWEPT_BODY",BODY,{"disambiguationData":[OSD([sQuery(id+"F0.wireOp",EDGE,"E0.bottom"),sQuery(id+"F0.wireOp",EDGE,"E0.top"),sQuery(id+"F0.wireOp",EDGE,"E0.left"),sQuery(id+"F0.wireOp",EDGE,"E0.right")])]}),"instanceName":"1"}),"instanceName":"1"}),"instanceName":"1"}),"instanceName":"1"}),"instanceName":"1"}),"instanceName":"1"}),"instanceName":"1"}),"instanceName":"1"});
            var Q15;
            Q15=makeQuery(id+"F42.opPattern","COPY",BODY,{"derivedFrom":makeQuery(id+"F28.opPattern","COPY",BODY,{"derivedFrom":makeQuery(id+"F23.opPattern","COPY",BODY,{"derivedFrom":makeQuery(id+"F19.opPattern","COPY",BODY,{"derivedFrom":makeQuery(id+"F17.opPattern","COPY",BODY,{"derivedFrom":makeQuery(id+"F13.opPattern","COPY",BODY,{"derivedFrom":makeQuery(id+"F5.opPattern","COPY",BODY,{"derivedFrom":makeQuery(id+"F4.opPattern","COPY",BODY,{"derivedFrom":makeQuery(id+"F1.opExtrude","SWEPT_BODY",BODY,{"disambiguationData":[OSD([sQuery(id+"F0.wireOp",EDGE,"E0.bottom"),sQuery(id+"F0.wireOp",EDGE,"E0.top"),sQuery(id+"F0.wireOp",EDGE,"E0.left"),sQuery(id+"F0.wireOp",EDGE,"E0.right")])]}),"instanceName":"1"}),"instanceName":"1"}),"instanceName":"1"}),"instanceName":"1"}),"instanceName":"1"}),"instanceName":"1"}),"instanceName":"1"}),"instanceName":"1"});
            var Q16;
            Q16=makeQuery(id+"F42.opPattern","COPY",BODY,{"derivedFrom":makeQuery(id+"F28.opPattern","COPY",BODY,{"derivedFrom":makeQuery(id+"F23.opPattern","COPY",BODY,{"derivedFrom":makeQuery(id+"F19.opPattern","COPY",BODY,{"derivedFrom":makeQuery(id+"F15.opPattern","COPY",BODY,{"derivedFrom":makeQuery(id+"F12.opPattern","COPY",BODY,{"derivedFrom":makeQuery(id+"F6.opPattern","COPY",BODY,{"derivedFrom":makeQuery(id+"F5.opPattern","COPY",BODY,{"derivedFrom":makeQuery(id+"F4.opPattern","COPY",BODY,{"derivedFrom":makeQuery(id+"F2.opPattern","COPY",BODY,{"derivedFrom":makeQuery(id+"F1.opExtrude","SWEPT_BODY",BODY,{"disambiguationData":[OSD([sQuery(id+"F0.wireOp",EDGE,"E0.bottom"),sQuery(id+"F0.wireOp",EDGE,"E0.top"),sQuery(id+"F0.wireOp",EDGE,"E0.left"),sQuery(id+"F0.wireOp",EDGE,"E0.right")])]}),"instanceName":"1"}),"instanceName":"1"}),"instanceName":"1"}),"instanceName":"1"}),"instanceName":"1"}),"instanceName":"1"}),"instanceName":"1"}),"instanceName":"1"}),"instanceName":"1"}),"instanceName":"1"});
            var Q17;
            Q17=makeQuery(id+"F42.opPattern","COPY",BODY,{"derivedFrom":makeQuery(id+"F29.opPattern","COPY",BODY,{"derivedFrom":makeQuery(id+"F28.opPattern","COPY",BODY,{"derivedFrom":makeQuery(id+"F19.opPattern","COPY",BODY,{"derivedFrom":makeQuery(id+"F17.opPattern","COPY",BODY,{"derivedFrom":makeQuery(id+"F15.opPattern","COPY",BODY,{"derivedFrom":makeQuery(id+"F12.opPattern","COPY",BODY,{"derivedFrom":makeQuery(id+"F6.opPattern","COPY",BODY,{"derivedFrom":makeQuery(id+"F5.opPattern","COPY",BODY,{"derivedFrom":makeQuery(id+"F4.opPattern","COPY",BODY,{"derivedFrom":makeQuery(id+"F2.opPattern","COPY",BODY,{"derivedFrom":makeQuery(id+"F1.opExtrude","SWEPT_BODY",BODY,{"disambiguationData":[OSD([sQuery(id+"F0.wireOp",EDGE,"E0.bottom"),sQuery(id+"F0.wireOp",EDGE,"E0.top"),sQuery(id+"F0.wireOp",EDGE,"E0.left"),sQuery(id+"F0.wireOp",EDGE,"E0.right")])]}),"instanceName":"1"}),"instanceName":"1"}),"instanceName":"1"}),"instanceName":"1"}),"instanceName":"1"}),"instanceName":"1"}),"instanceName":"1"}),"instanceName":"1"}),"instanceName":"1"}),"instanceName":"1"}),"instanceName":"1"});
            var Q18;
            Q18=makeQuery(id+"F42.opPattern","COPY",EDGE,{"derivedFrom":makeQuery(id+"F29.opPattern","COPY",EDGE,{"derivedFrom":makeQuery(id+"F28.opPattern","COPY",EDGE,{"derivedFrom":makeQuery(id+"F26.opPattern","COPY",EDGE,{"derivedFrom":makeQuery(id+"F17.opPattern","COPY",EDGE,{"derivedFrom":makeQuery(id+"F13.opPattern","COPY",EDGE,{"derivedFrom":makeQuery(id+"F5.opPattern","COPY",EDGE,{"derivedFrom":makeQuery(id+"F4.opPattern","COPY",EDGE,{"derivedFrom":makeQuery(id+"F1.opExtrude","CAP_EDGE",EDGE,{"disambiguationData":[OSD([sQuery(id+"F0.wireOp",EDGE,"E0.right")])],"isStart":false}),"instanceName":"1"}),"instanceName":"1"}),"instanceName":"1"}),"instanceName":"1"}),"instanceName":"1"}),"instanceName":"1"}),"instanceName":"1"}),"instanceName":"1"});
            transform(context, id + "F43", {"entities" : qUnion([Q0, Q1, Q2, Q3, Q4, Q5, Q6, Q7, Q8, Q9, Q10, Q11, Q12, Q13, Q14, Q15, Q16, Q17]), "transformType" : TransformType.TRANSLATION_DISTANCE, "transformDirection" : qUnion([Q18]), "distance" : 10 * mm, "oppositeDirection" : true, "makeCopy" : false});
        }
        {
            var Q0;
            Q0=makeQuery(id+"F42.opPattern","COPY",BODY,{"derivedFrom":makeQuery(id+"F29.opPattern","COPY",BODY,{"derivedFrom":makeQuery(id+"F28.opPattern","COPY",BODY,{"derivedFrom":makeQuery(id+"F23.opPattern","COPY",BODY,{"derivedFrom":makeQuery(id+"F19.opPattern","COPY",BODY,{"derivedFrom":makeQuery(id+"F17.opPattern","COPY",BODY,{"derivedFrom":makeQuery(id+"F15.opPattern","COPY",BODY,{"derivedFrom":makeQuery(id+"F12.opPattern","COPY",BODY,{"derivedFrom":makeQuery(id+"F6.opPattern","COPY",BODY,{"derivedFrom":makeQuery(id+"F5.opPattern","COPY",BODY,{"derivedFrom":makeQuery(id+"F4.opPattern","COPY",BODY,{"derivedFrom":makeQuery(id+"F2.opPattern","COPY",BODY,{"derivedFrom":makeQuery(id+"F1.opExtrude","SWEPT_BODY",BODY,{"disambiguationData":[OSD([sQuery(id+"F0.wireOp",EDGE,"E0.bottom"),sQuery(id+"F0.wireOp",EDGE,"E0.top"),sQuery(id+"F0.wireOp",EDGE,"E0.left"),sQuery(id+"F0.wireOp",EDGE,"E0.right")])]}),"instanceName":"1"}),"instanceName":"1"}),"instanceName":"1"}),"instanceName":"1"}),"instanceName":"1"}),"instanceName":"1"}),"instanceName":"1"}),"instanceName":"1"}),"instanceName":"1"}),"instanceName":"1"}),"instanceName":"1"}),"instanceName":"1"});
            var Q1;
            Q1=makeQuery(id+"F42.opPattern","COPY",BODY,{"derivedFrom":makeQuery(id+"F29.opPattern","COPY",BODY,{"derivedFrom":makeQuery(id+"F28.opPattern","COPY",BODY,{"derivedFrom":makeQuery(id+"F23.opPattern","COPY",BODY,{"derivedFrom":makeQuery(id+"F19.opPattern","COPY",BODY,{"derivedFrom":makeQuery(id+"F15.opPattern","COPY",BODY,{"derivedFrom":makeQuery(id+"F12.opPattern","COPY",BODY,{"derivedFrom":makeQuery(id+"F6.opPattern","COPY",BODY,{"derivedFrom":makeQuery(id+"F5.opPattern","COPY",BODY,{"derivedFrom":makeQuery(id+"F4.opPattern","COPY",BODY,{"derivedFrom":makeQuery(id+"F2.opPattern","COPY",BODY,{"derivedFrom":makeQuery(id+"F1.opExtrude","SWEPT_BODY",BODY,{"disambiguationData":[OSD([sQuery(id+"F0.wireOp",EDGE,"E0.bottom"),sQuery(id+"F0.wireOp",EDGE,"E0.top"),sQuery(id+"F0.wireOp",EDGE,"E0.left"),sQuery(id+"F0.wireOp",EDGE,"E0.right")])]}),"instanceName":"1"}),"instanceName":"1"}),"instanceName":"1"}),"instanceName":"1"}),"instanceName":"1"}),"instanceName":"1"}),"instanceName":"1"}),"instanceName":"1"}),"instanceName":"1"}),"instanceName":"1"}),"instanceName":"1"});
            var Q2;
            Q2=makeQuery(id+"F42.opPattern","COPY",BODY,{"derivedFrom":makeQuery(id+"F29.opPattern","COPY",BODY,{"derivedFrom":makeQuery(id+"F28.opPattern","COPY",BODY,{"derivedFrom":makeQuery(id+"F23.opPattern","COPY",BODY,{"derivedFrom":makeQuery(id+"F19.opPattern","COPY",BODY,{"derivedFrom":makeQuery(id+"F17.opPattern","COPY",BODY,{"derivedFrom":makeQuery(id+"F13.opPattern","COPY",BODY,{"derivedFrom":makeQuery(id+"F5.opPattern","COPY",BODY,{"derivedFrom":makeQuery(id+"F4.opPattern","COPY",BODY,{"derivedFrom":makeQuery(id+"F1.opExtrude","SWEPT_BODY",BODY,{"disambiguationData":[OSD([sQuery(id+"F0.wireOp",EDGE,"E0.bottom"),sQuery(id+"F0.wireOp",EDGE,"E0.top"),sQuery(id+"F0.wireOp",EDGE,"E0.left"),sQuery(id+"F0.wireOp",EDGE,"E0.right")])]}),"instanceName":"1"}),"instanceName":"1"}),"instanceName":"1"}),"instanceName":"1"}),"instanceName":"1"}),"instanceName":"1"}),"instanceName":"1"}),"instanceName":"1"}),"instanceName":"1"});
            var Q3;
            Q3=makeQuery(id+"F42.opPattern","COPY",EDGE,{"derivedFrom":makeQuery(id+"F29.opPattern","COPY",EDGE,{"derivedFrom":makeQuery(id+"F28.opPattern","COPY",EDGE,{"derivedFrom":makeQuery(id+"F26.opPattern","COPY",EDGE,{"derivedFrom":makeQuery(id+"F17.opPattern","COPY",EDGE,{"derivedFrom":makeQuery(id+"F13.opPattern","COPY",EDGE,{"derivedFrom":makeQuery(id+"F5.opPattern","COPY",EDGE,{"derivedFrom":makeQuery(id+"F4.opPattern","COPY",EDGE,{"derivedFrom":makeQuery(id+"F1.opExtrude","CAP_EDGE",EDGE,{"disambiguationData":[OSD([sQuery(id+"F0.wireOp",EDGE,"E0.right")])],"isStart":false}),"instanceName":"1"}),"instanceName":"1"}),"instanceName":"1"}),"instanceName":"1"}),"instanceName":"1"}),"instanceName":"1"}),"instanceName":"1"}),"instanceName":"1"});
            transform(context, id + "F44", {"entities" : qUnion([Q0, Q1, Q2]), "transformType" : TransformType.TRANSLATION_DISTANCE, "transformDirection" : qUnion([Q3]), "distance" : 10 * mm, "oppositeDirection" : true, "makeCopy" : true});
        }
        {
            var Q0;
            Q0=makeQuery(id+"F40.opPattern","COPY",BODY,{"derivedFrom":makeQuery(id+"F28.opPattern","COPY",BODY,{"derivedFrom":makeQuery(id+"F19.opPattern","COPY",BODY,{"derivedFrom":makeQuery(id+"F17.opPattern","COPY",BODY,{"derivedFrom":makeQuery(id+"F13.opPattern","COPY",BODY,{"derivedFrom":makeQuery(id+"F5.opPattern","COPY",BODY,{"derivedFrom":makeQuery(id+"F4.opPattern","COPY",BODY,{"derivedFrom":makeQuery(id+"F1.opExtrude","SWEPT_BODY",BODY,{"disambiguationData":[OSD([sQuery(id+"F0.wireOp",EDGE,"E0.bottom"),sQuery(id+"F0.wireOp",EDGE,"E0.top"),sQuery(id+"F0.wireOp",EDGE,"E0.left"),sQuery(id+"F0.wireOp",EDGE,"E0.right")])]}),"instanceName":"1"}),"instanceName":"1"}),"instanceName":"1"}),"instanceName":"1"}),"instanceName":"1"}),"instanceName":"1"}),"instanceName":"1"});
            var Q1;
            Q1=makeQuery(id+"F40.opPattern","COPY",BODY,{"derivedFrom":makeQuery(id+"F19.opPattern","COPY",BODY,{"derivedFrom":makeQuery(id+"F15.opPattern","COPY",BODY,{"derivedFrom":makeQuery(id+"F12.opPattern","COPY",BODY,{"derivedFrom":makeQuery(id+"F6.opPattern","COPY",BODY,{"derivedFrom":makeQuery(id+"F5.opPattern","COPY",BODY,{"derivedFrom":makeQuery(id+"F4.opPattern","COPY",BODY,{"derivedFrom":makeQuery(id+"F2.opPattern","COPY",BODY,{"derivedFrom":makeQuery(id+"F1.opExtrude","SWEPT_BODY",BODY,{"disambiguationData":[OSD([sQuery(id+"F0.wireOp",EDGE,"E0.bottom"),sQuery(id+"F0.wireOp",EDGE,"E0.top"),sQuery(id+"F0.wireOp",EDGE,"E0.left"),sQuery(id+"F0.wireOp",EDGE,"E0.right")])]}),"instanceName":"1"}),"instanceName":"1"}),"instanceName":"1"}),"instanceName":"1"}),"instanceName":"1"}),"instanceName":"1"}),"instanceName":"1"}),"instanceName":"1"});
            var Q2;
            Q2=makeQuery(id+"F40.opPattern","COPY",BODY,{"derivedFrom":makeQuery(id+"F19.opPattern","COPY",BODY,{"derivedFrom":makeQuery(id+"F17.opPattern","COPY",BODY,{"derivedFrom":makeQuery(id+"F12.opPattern","COPY",BODY,{"derivedFrom":makeQuery(id+"F6.opPattern","COPY",BODY,{"derivedFrom":makeQuery(id+"F5.opPattern","COPY",BODY,{"derivedFrom":makeQuery(id+"F4.opPattern","COPY",BODY,{"derivedFrom":makeQuery(id+"F1.opExtrude","SWEPT_BODY",BODY,{"disambiguationData":[OSD([sQuery(id+"F0.wireOp",EDGE,"E0.bottom"),sQuery(id+"F0.wireOp",EDGE,"E0.top"),sQuery(id+"F0.wireOp",EDGE,"E0.left"),sQuery(id+"F0.wireOp",EDGE,"E0.right")])]}),"instanceName":"1"}),"instanceName":"1"}),"instanceName":"1"}),"instanceName":"1"}),"instanceName":"1"}),"instanceName":"1"}),"instanceName":"1"});
            var Q3;
            Q3=makeQuery(id+"F40.opPattern","COPY",BODY,{"derivedFrom":makeQuery(id+"F28.opPattern","COPY",BODY,{"derivedFrom":makeQuery(id+"F19.opPattern","COPY",BODY,{"derivedFrom":makeQuery(id+"F15.opPattern","COPY",BODY,{"derivedFrom":makeQuery(id+"F12.opPattern","COPY",BODY,{"derivedFrom":makeQuery(id+"F6.opPattern","COPY",BODY,{"derivedFrom":makeQuery(id+"F5.opPattern","COPY",BODY,{"derivedFrom":makeQuery(id+"F4.opPattern","COPY",BODY,{"derivedFrom":makeQuery(id+"F2.opPattern","COPY",BODY,{"derivedFrom":makeQuery(id+"F1.opExtrude","SWEPT_BODY",BODY,{"disambiguationData":[OSD([sQuery(id+"F0.wireOp",EDGE,"E0.bottom"),sQuery(id+"F0.wireOp",EDGE,"E0.top"),sQuery(id+"F0.wireOp",EDGE,"E0.left"),sQuery(id+"F0.wireOp",EDGE,"E0.right")])]}),"instanceName":"1"}),"instanceName":"1"}),"instanceName":"1"}),"instanceName":"1"}),"instanceName":"1"}),"instanceName":"1"}),"instanceName":"1"}),"instanceName":"1"}),"instanceName":"1"});
            var Q4;
            Q4=makeQuery(id+"F40.opPattern","COPY",BODY,{"derivedFrom":makeQuery(id+"F19.opPattern","COPY",BODY,{"derivedFrom":makeQuery(id+"F17.opPattern","COPY",BODY,{"derivedFrom":makeQuery(id+"F12.opPattern","COPY",BODY,{"derivedFrom":makeQuery(id+"F6.opPattern","COPY",BODY,{"derivedFrom":makeQuery(id+"F5.opPattern","COPY",BODY,{"derivedFrom":makeQuery(id+"F4.opPattern","COPY",BODY,{"derivedFrom":makeQuery(id+"F2.opPattern","COPY",BODY,{"derivedFrom":makeQuery(id+"F1.opExtrude","SWEPT_BODY",BODY,{"disambiguationData":[OSD([sQuery(id+"F0.wireOp",EDGE,"E0.bottom"),sQuery(id+"F0.wireOp",EDGE,"E0.top"),sQuery(id+"F0.wireOp",EDGE,"E0.left"),sQuery(id+"F0.wireOp",EDGE,"E0.right")])]}),"instanceName":"1"}),"instanceName":"1"}),"instanceName":"1"}),"instanceName":"1"}),"instanceName":"1"}),"instanceName":"1"}),"instanceName":"1"}),"instanceName":"1"});
            var Q5;
            Q5=makeQuery(id+"F40.opPattern","COPY",BODY,{"derivedFrom":makeQuery(id+"F23.opPattern","COPY",BODY,{"derivedFrom":makeQuery(id+"F19.opPattern","COPY",BODY,{"derivedFrom":makeQuery(id+"F15.opPattern","COPY",BODY,{"derivedFrom":makeQuery(id+"F12.opPattern","COPY",BODY,{"derivedFrom":makeQuery(id+"F6.opPattern","COPY",BODY,{"derivedFrom":makeQuery(id+"F5.opPattern","COPY",BODY,{"derivedFrom":makeQuery(id+"F4.opPattern","COPY",BODY,{"derivedFrom":makeQuery(id+"F2.opPattern","COPY",BODY,{"derivedFrom":makeQuery(id+"F1.opExtrude","SWEPT_BODY",BODY,{"disambiguationData":[OSD([sQuery(id+"F0.wireOp",EDGE,"E0.bottom"),sQuery(id+"F0.wireOp",EDGE,"E0.top"),sQuery(id+"F0.wireOp",EDGE,"E0.left"),sQuery(id+"F0.wireOp",EDGE,"E0.right")])]}),"instanceName":"1"}),"instanceName":"1"}),"instanceName":"1"}),"instanceName":"1"}),"instanceName":"1"}),"instanceName":"1"}),"instanceName":"1"}),"instanceName":"1"}),"instanceName":"1"});
            var Q6;
            Q6=makeQuery(id+"F40.opPattern","COPY",BODY,{"derivedFrom":makeQuery(id+"F19.opPattern","COPY",BODY,{"derivedFrom":makeQuery(id+"F17.opPattern","COPY",BODY,{"derivedFrom":makeQuery(id+"F5.opPattern","COPY",BODY,{"derivedFrom":makeQuery(id+"F4.opPattern","COPY",BODY,{"derivedFrom":makeQuery(id+"F2.opPattern","COPY",BODY,{"derivedFrom":makeQuery(id+"F1.opExtrude","SWEPT_BODY",BODY,{"disambiguationData":[OSD([sQuery(id+"F0.wireOp",EDGE,"E0.bottom"),sQuery(id+"F0.wireOp",EDGE,"E0.top"),sQuery(id+"F0.wireOp",EDGE,"E0.left"),sQuery(id+"F0.wireOp",EDGE,"E0.right")])]}),"instanceName":"1"}),"instanceName":"1"}),"instanceName":"1"}),"instanceName":"1"}),"instanceName":"1"}),"instanceName":"1"});
            var Q7;
            Q7=makeQuery(id+"F40.opPattern","COPY",BODY,{"derivedFrom":makeQuery(id+"F28.opPattern","COPY",BODY,{"derivedFrom":makeQuery(id+"F23.opPattern","COPY",BODY,{"derivedFrom":makeQuery(id+"F19.opPattern","COPY",BODY,{"derivedFrom":makeQuery(id+"F15.opPattern","COPY",BODY,{"derivedFrom":makeQuery(id+"F12.opPattern","COPY",BODY,{"derivedFrom":makeQuery(id+"F6.opPattern","COPY",BODY,{"derivedFrom":makeQuery(id+"F5.opPattern","COPY",BODY,{"derivedFrom":makeQuery(id+"F4.opPattern","COPY",BODY,{"derivedFrom":makeQuery(id+"F2.opPattern","COPY",BODY,{"derivedFrom":makeQuery(id+"F1.opExtrude","SWEPT_BODY",BODY,{"disambiguationData":[OSD([sQuery(id+"F0.wireOp",EDGE,"E0.bottom"),sQuery(id+"F0.wireOp",EDGE,"E0.top"),sQuery(id+"F0.wireOp",EDGE,"E0.left"),sQuery(id+"F0.wireOp",EDGE,"E0.right")])]}),"instanceName":"1"}),"instanceName":"1"}),"instanceName":"1"}),"instanceName":"1"}),"instanceName":"1"}),"instanceName":"1"}),"instanceName":"1"}),"instanceName":"1"}),"instanceName":"1"}),"instanceName":"1"});
            var Q8;
            Q8=makeQuery(id+"F40.opPattern","COPY",BODY,{"derivedFrom":makeQuery(id+"F23.opPattern","COPY",BODY,{"derivedFrom":makeQuery(id+"F19.opPattern","COPY",BODY,{"derivedFrom":makeQuery(id+"F17.opPattern","COPY",BODY,{"derivedFrom":makeQuery(id+"F6.opPattern","COPY",BODY,{"derivedFrom":makeQuery(id+"F5.opPattern","COPY",BODY,{"derivedFrom":makeQuery(id+"F4.opPattern","COPY",BODY,{"derivedFrom":makeQuery(id+"F2.opPattern","COPY",BODY,{"derivedFrom":makeQuery(id+"F1.opExtrude","SWEPT_BODY",BODY,{"disambiguationData":[OSD([sQuery(id+"F0.wireOp",EDGE,"E0.bottom"),sQuery(id+"F0.wireOp",EDGE,"E0.top"),sQuery(id+"F0.wireOp",EDGE,"E0.left"),sQuery(id+"F0.wireOp",EDGE,"E0.right")])]}),"instanceName":"1"}),"instanceName":"1"}),"instanceName":"1"}),"instanceName":"1"}),"instanceName":"1"}),"instanceName":"1"}),"instanceName":"1"}),"instanceName":"1"});
            var Q9;
            Q9=makeQuery(id+"F40.opPattern","COPY",BODY,{"derivedFrom":makeQuery(id+"F23.opPattern","COPY",BODY,{"derivedFrom":makeQuery(id+"F19.opPattern","COPY",BODY,{"derivedFrom":makeQuery(id+"F17.opPattern","COPY",BODY,{"derivedFrom":makeQuery(id+"F12.opPattern","COPY",BODY,{"derivedFrom":makeQuery(id+"F6.opPattern","COPY",BODY,{"derivedFrom":makeQuery(id+"F5.opPattern","COPY",BODY,{"derivedFrom":makeQuery(id+"F4.opPattern","COPY",BODY,{"derivedFrom":makeQuery(id+"F1.opExtrude","SWEPT_BODY",BODY,{"disambiguationData":[OSD([sQuery(id+"F0.wireOp",EDGE,"E0.bottom"),sQuery(id+"F0.wireOp",EDGE,"E0.top"),sQuery(id+"F0.wireOp",EDGE,"E0.left"),sQuery(id+"F0.wireOp",EDGE,"E0.right")])]}),"instanceName":"1"}),"instanceName":"1"}),"instanceName":"1"}),"instanceName":"1"}),"instanceName":"1"}),"instanceName":"1"}),"instanceName":"1"}),"instanceName":"1"});
            var Q10;
            Q10=makeQuery(id+"F40.opPattern","COPY",BODY,{"derivedFrom":makeQuery(id+"F21.opPattern","COPY",BODY,{"derivedFrom":makeQuery(id+"F19.opPattern","COPY",BODY,{"derivedFrom":makeQuery(id+"F17.opPattern","COPY",BODY,{"derivedFrom":makeQuery(id+"F6.opPattern","COPY",BODY,{"derivedFrom":makeQuery(id+"F5.opPattern","COPY",BODY,{"derivedFrom":makeQuery(id+"F4.opPattern","COPY",BODY,{"derivedFrom":makeQuery(id+"F2.opPattern","COPY",BODY,{"derivedFrom":makeQuery(id+"F1.opExtrude","SWEPT_BODY",BODY,{"disambiguationData":[OSD([sQuery(id+"F0.wireOp",EDGE,"E0.bottom"),sQuery(id+"F0.wireOp",EDGE,"E0.top"),sQuery(id+"F0.wireOp",EDGE,"E0.left"),sQuery(id+"F0.wireOp",EDGE,"E0.right")])]}),"instanceName":"1"}),"instanceName":"1"}),"instanceName":"1"}),"instanceName":"1"}),"instanceName":"1"}),"instanceName":"1"}),"instanceName":"1"}),"instanceName":"1"});
            var Q11;
            Q11=makeQuery(id+"F40.opPattern","COPY",BODY,{"derivedFrom":makeQuery(id+"F29.opPattern","COPY",BODY,{"derivedFrom":makeQuery(id+"F19.opPattern","COPY",BODY,{"derivedFrom":makeQuery(id+"F17.opPattern","COPY",BODY,{"derivedFrom":makeQuery(id+"F13.opPattern","COPY",BODY,{"derivedFrom":makeQuery(id+"F5.opPattern","COPY",BODY,{"derivedFrom":makeQuery(id+"F4.opPattern","COPY",BODY,{"derivedFrom":makeQuery(id+"F1.opExtrude","SWEPT_BODY",BODY,{"disambiguationData":[OSD([sQuery(id+"F0.wireOp",EDGE,"E0.bottom"),sQuery(id+"F0.wireOp",EDGE,"E0.top"),sQuery(id+"F0.wireOp",EDGE,"E0.left"),sQuery(id+"F0.wireOp",EDGE,"E0.right")])]}),"instanceName":"1"}),"instanceName":"1"}),"instanceName":"1"}),"instanceName":"1"}),"instanceName":"1"}),"instanceName":"1"}),"instanceName":"1"});
            var Q12;
            Q12=makeQuery(id+"F40.opPattern","COPY",BODY,{"derivedFrom":makeQuery(id+"F28.opPattern","COPY",BODY,{"derivedFrom":makeQuery(id+"F23.opPattern","COPY",BODY,{"derivedFrom":makeQuery(id+"F19.opPattern","COPY",BODY,{"derivedFrom":makeQuery(id+"F17.opPattern","COPY",BODY,{"derivedFrom":makeQuery(id+"F13.opPattern","COPY",BODY,{"derivedFrom":makeQuery(id+"F5.opPattern","COPY",BODY,{"derivedFrom":makeQuery(id+"F4.opPattern","COPY",BODY,{"derivedFrom":makeQuery(id+"F1.opExtrude","SWEPT_BODY",BODY,{"disambiguationData":[OSD([sQuery(id+"F0.wireOp",EDGE,"E0.bottom"),sQuery(id+"F0.wireOp",EDGE,"E0.top"),sQuery(id+"F0.wireOp",EDGE,"E0.left"),sQuery(id+"F0.wireOp",EDGE,"E0.right")])]}),"instanceName":"1"}),"instanceName":"1"}),"instanceName":"1"}),"instanceName":"1"}),"instanceName":"1"}),"instanceName":"1"}),"instanceName":"1"}),"instanceName":"1"});
            var Q13;
            Q13=makeQuery(id+"F40.opPattern","COPY",BODY,{"derivedFrom":makeQuery(id+"F23.opPattern","COPY",BODY,{"derivedFrom":makeQuery(id+"F19.opPattern","COPY",BODY,{"derivedFrom":makeQuery(id+"F17.opPattern","COPY",BODY,{"derivedFrom":makeQuery(id+"F15.opPattern","COPY",BODY,{"derivedFrom":makeQuery(id+"F12.opPattern","COPY",BODY,{"derivedFrom":makeQuery(id+"F6.opPattern","COPY",BODY,{"derivedFrom":makeQuery(id+"F5.opPattern","COPY",BODY,{"derivedFrom":makeQuery(id+"F4.opPattern","COPY",BODY,{"derivedFrom":makeQuery(id+"F2.opPattern","COPY",BODY,{"derivedFrom":makeQuery(id+"F1.opExtrude","SWEPT_BODY",BODY,{"disambiguationData":[OSD([sQuery(id+"F0.wireOp",EDGE,"E0.bottom"),sQuery(id+"F0.wireOp",EDGE,"E0.top"),sQuery(id+"F0.wireOp",EDGE,"E0.left"),sQuery(id+"F0.wireOp",EDGE,"E0.right")])]}),"instanceName":"1"}),"instanceName":"1"}),"instanceName":"1"}),"instanceName":"1"}),"instanceName":"1"}),"instanceName":"1"}),"instanceName":"1"}),"instanceName":"1"}),"instanceName":"1"}),"instanceName":"1"});
            var Q14;
            Q14=makeQuery(id+"F40.opPattern","COPY",BODY,{"derivedFrom":makeQuery(id+"F21.opPattern","COPY",BODY,{"derivedFrom":makeQuery(id+"F19.opPattern","COPY",BODY,{"derivedFrom":makeQuery(id+"F17.opPattern","COPY",BODY,{"derivedFrom":makeQuery(id+"F6.opPattern","COPY",BODY,{"derivedFrom":makeQuery(id+"F5.opPattern","COPY",BODY,{"derivedFrom":makeQuery(id+"F4.opPattern","COPY",BODY,{"derivedFrom":makeQuery(id+"F1.opExtrude","SWEPT_BODY",BODY,{"disambiguationData":[OSD([sQuery(id+"F0.wireOp",EDGE,"E0.bottom"),sQuery(id+"F0.wireOp",EDGE,"E0.top"),sQuery(id+"F0.wireOp",EDGE,"E0.left"),sQuery(id+"F0.wireOp",EDGE,"E0.right")])]}),"instanceName":"1"}),"instanceName":"1"}),"instanceName":"1"}),"instanceName":"1"}),"instanceName":"1"}),"instanceName":"1"}),"instanceName":"1"});
            var Q15;
            Q15=makeQuery(id+"F40.opPattern","COPY",BODY,{"derivedFrom":makeQuery(id+"F19.opPattern","COPY",BODY,{"derivedFrom":makeQuery(id+"F17.opPattern","COPY",BODY,{"derivedFrom":makeQuery(id+"F6.opPattern","COPY",BODY,{"derivedFrom":makeQuery(id+"F5.opPattern","COPY",BODY,{"derivedFrom":makeQuery(id+"F4.opPattern","COPY",BODY,{"derivedFrom":makeQuery(id+"F2.opPattern","COPY",BODY,{"derivedFrom":makeQuery(id+"F1.opExtrude","SWEPT_BODY",BODY,{"disambiguationData":[OSD([sQuery(id+"F0.wireOp",EDGE,"E0.bottom"),sQuery(id+"F0.wireOp",EDGE,"E0.top"),sQuery(id+"F0.wireOp",EDGE,"E0.left"),sQuery(id+"F0.wireOp",EDGE,"E0.right")])]}),"instanceName":"1"}),"instanceName":"1"}),"instanceName":"1"}),"instanceName":"1"}),"instanceName":"1"}),"instanceName":"1"}),"instanceName":"1"});
            var Q16;
            Q16=makeQuery(id+"F40.opPattern","COPY",BODY,{"derivedFrom":makeQuery(id+"F19.opPattern","COPY",BODY,{"derivedFrom":makeQuery(id+"F17.opPattern","COPY",BODY,{"derivedFrom":makeQuery(id+"F13.opPattern","COPY",BODY,{"derivedFrom":makeQuery(id+"F5.opPattern","COPY",BODY,{"derivedFrom":makeQuery(id+"F4.opPattern","COPY",BODY,{"derivedFrom":makeQuery(id+"F1.opExtrude","SWEPT_BODY",BODY,{"disambiguationData":[OSD([sQuery(id+"F0.wireOp",EDGE,"E0.bottom"),sQuery(id+"F0.wireOp",EDGE,"E0.top"),sQuery(id+"F0.wireOp",EDGE,"E0.left"),sQuery(id+"F0.wireOp",EDGE,"E0.right")])]}),"instanceName":"1"}),"instanceName":"1"}),"instanceName":"1"}),"instanceName":"1"}),"instanceName":"1"}),"instanceName":"1"});
            var Q17;
            Q17=makeQuery(id+"F40.opPattern","COPY",BODY,{"derivedFrom":makeQuery(id+"F23.opPattern","COPY",BODY,{"derivedFrom":makeQuery(id+"F19.opPattern","COPY",BODY,{"derivedFrom":makeQuery(id+"F12.opPattern","COPY",BODY,{"derivedFrom":makeQuery(id+"F6.opPattern","COPY",BODY,{"derivedFrom":makeQuery(id+"F5.opPattern","COPY",BODY,{"derivedFrom":makeQuery(id+"F4.opPattern","COPY",BODY,{"derivedFrom":makeQuery(id+"F2.opPattern","COPY",BODY,{"derivedFrom":makeQuery(id+"F1.opExtrude","SWEPT_BODY",BODY,{"disambiguationData":[OSD([sQuery(id+"F0.wireOp",EDGE,"E0.bottom"),sQuery(id+"F0.wireOp",EDGE,"E0.top"),sQuery(id+"F0.wireOp",EDGE,"E0.left"),sQuery(id+"F0.wireOp",EDGE,"E0.right")])]}),"instanceName":"1"}),"instanceName":"1"}),"instanceName":"1"}),"instanceName":"1"}),"instanceName":"1"}),"instanceName":"1"}),"instanceName":"1"}),"instanceName":"1"});
            var Q18;
            Q18=makeQuery(id+"F40.opPattern","COPY",BODY,{"derivedFrom":makeQuery(id+"F29.opPattern","COPY",BODY,{"derivedFrom":makeQuery(id+"F19.opPattern","COPY",BODY,{"derivedFrom":makeQuery(id+"F17.opPattern","COPY",BODY,{"derivedFrom":makeQuery(id+"F15.opPattern","COPY",BODY,{"derivedFrom":makeQuery(id+"F12.opPattern","COPY",BODY,{"derivedFrom":makeQuery(id+"F6.opPattern","COPY",BODY,{"derivedFrom":makeQuery(id+"F5.opPattern","COPY",BODY,{"derivedFrom":makeQuery(id+"F4.opPattern","COPY",BODY,{"derivedFrom":makeQuery(id+"F2.opPattern","COPY",BODY,{"derivedFrom":makeQuery(id+"F1.opExtrude","SWEPT_BODY",BODY,{"disambiguationData":[OSD([sQuery(id+"F0.wireOp",EDGE,"E0.bottom"),sQuery(id+"F0.wireOp",EDGE,"E0.top"),sQuery(id+"F0.wireOp",EDGE,"E0.left"),sQuery(id+"F0.wireOp",EDGE,"E0.right")])]}),"instanceName":"1"}),"instanceName":"1"}),"instanceName":"1"}),"instanceName":"1"}),"instanceName":"1"}),"instanceName":"1"}),"instanceName":"1"}),"instanceName":"1"}),"instanceName":"1"}),"instanceName":"1"});
            var Q19;
            Q19=makeQuery(id+"F40.opPattern","COPY",BODY,{"derivedFrom":makeQuery(id+"F19.opPattern","COPY",BODY,{"derivedFrom":makeQuery(id+"F17.opPattern","COPY",BODY,{"derivedFrom":makeQuery(id+"F15.opPattern","COPY",BODY,{"derivedFrom":makeQuery(id+"F12.opPattern","COPY",BODY,{"derivedFrom":makeQuery(id+"F6.opPattern","COPY",BODY,{"derivedFrom":makeQuery(id+"F5.opPattern","COPY",BODY,{"derivedFrom":makeQuery(id+"F4.opPattern","COPY",BODY,{"derivedFrom":makeQuery(id+"F2.opPattern","COPY",BODY,{"derivedFrom":makeQuery(id+"F1.opExtrude","SWEPT_BODY",BODY,{"disambiguationData":[OSD([sQuery(id+"F0.wireOp",EDGE,"E0.bottom"),sQuery(id+"F0.wireOp",EDGE,"E0.top"),sQuery(id+"F0.wireOp",EDGE,"E0.left"),sQuery(id+"F0.wireOp",EDGE,"E0.right")])]}),"instanceName":"1"}),"instanceName":"1"}),"instanceName":"1"}),"instanceName":"1"}),"instanceName":"1"}),"instanceName":"1"}),"instanceName":"1"}),"instanceName":"1"}),"instanceName":"1"});
            var Q20;
            Q20=makeQuery(id+"F40.opPattern","COPY",BODY,{"derivedFrom":makeQuery(id+"F29.opPattern","COPY",BODY,{"derivedFrom":makeQuery(id+"F23.opPattern","COPY",BODY,{"derivedFrom":makeQuery(id+"F19.opPattern","COPY",BODY,{"derivedFrom":makeQuery(id+"F15.opPattern","COPY",BODY,{"derivedFrom":makeQuery(id+"F12.opPattern","COPY",BODY,{"derivedFrom":makeQuery(id+"F6.opPattern","COPY",BODY,{"derivedFrom":makeQuery(id+"F5.opPattern","COPY",BODY,{"derivedFrom":makeQuery(id+"F4.opPattern","COPY",BODY,{"derivedFrom":makeQuery(id+"F2.opPattern","COPY",BODY,{"derivedFrom":makeQuery(id+"F1.opExtrude","SWEPT_BODY",BODY,{"disambiguationData":[OSD([sQuery(id+"F0.wireOp",EDGE,"E0.bottom"),sQuery(id+"F0.wireOp",EDGE,"E0.top"),sQuery(id+"F0.wireOp",EDGE,"E0.left"),sQuery(id+"F0.wireOp",EDGE,"E0.right")])]}),"instanceName":"1"}),"instanceName":"1"}),"instanceName":"1"}),"instanceName":"1"}),"instanceName":"1"}),"instanceName":"1"}),"instanceName":"1"}),"instanceName":"1"}),"instanceName":"1"}),"instanceName":"1"});
            var Q21;
            Q21=makeQuery(id+"F40.opPattern","COPY",BODY,{"derivedFrom":makeQuery(id+"F23.opPattern","COPY",BODY,{"derivedFrom":makeQuery(id+"F19.opPattern","COPY",BODY,{"derivedFrom":makeQuery(id+"F17.opPattern","COPY",BODY,{"derivedFrom":makeQuery(id+"F13.opPattern","COPY",BODY,{"derivedFrom":makeQuery(id+"F5.opPattern","COPY",BODY,{"derivedFrom":makeQuery(id+"F4.opPattern","COPY",BODY,{"derivedFrom":makeQuery(id+"F1.opExtrude","SWEPT_BODY",BODY,{"disambiguationData":[OSD([sQuery(id+"F0.wireOp",EDGE,"E0.bottom"),sQuery(id+"F0.wireOp",EDGE,"E0.top"),sQuery(id+"F0.wireOp",EDGE,"E0.left"),sQuery(id+"F0.wireOp",EDGE,"E0.right")])]}),"instanceName":"1"}),"instanceName":"1"}),"instanceName":"1"}),"instanceName":"1"}),"instanceName":"1"}),"instanceName":"1"}),"instanceName":"1"});
            var Q22;
            Q22=makeQuery(id+"F40.opPattern","COPY",BODY,{"derivedFrom":makeQuery(id+"F23.opPattern","COPY",BODY,{"derivedFrom":makeQuery(id+"F21.opPattern","COPY",BODY,{"derivedFrom":makeQuery(id+"F19.opPattern","COPY",BODY,{"derivedFrom":makeQuery(id+"F12.opPattern","COPY",BODY,{"derivedFrom":makeQuery(id+"F6.opPattern","COPY",BODY,{"derivedFrom":makeQuery(id+"F5.opPattern","COPY",BODY,{"derivedFrom":makeQuery(id+"F4.opPattern","COPY",BODY,{"derivedFrom":makeQuery(id+"F2.opPattern","COPY",BODY,{"derivedFrom":makeQuery(id+"F1.opExtrude","SWEPT_BODY",BODY,{"disambiguationData":[OSD([sQuery(id+"F0.wireOp",EDGE,"E0.bottom"),sQuery(id+"F0.wireOp",EDGE,"E0.top"),sQuery(id+"F0.wireOp",EDGE,"E0.left"),sQuery(id+"F0.wireOp",EDGE,"E0.right")])]}),"instanceName":"1"}),"instanceName":"1"}),"instanceName":"1"}),"instanceName":"1"}),"instanceName":"1"}),"instanceName":"1"}),"instanceName":"1"}),"instanceName":"1"}),"instanceName":"1"});
            var Q23;
            Q23=makeQuery(id+"F40.opPattern","COPY",BODY,{"derivedFrom":makeQuery(id+"F28.opPattern","COPY",BODY,{"derivedFrom":makeQuery(id+"F19.opPattern","COPY",BODY,{"derivedFrom":makeQuery(id+"F17.opPattern","COPY",BODY,{"derivedFrom":makeQuery(id+"F15.opPattern","COPY",BODY,{"derivedFrom":makeQuery(id+"F12.opPattern","COPY",BODY,{"derivedFrom":makeQuery(id+"F6.opPattern","COPY",BODY,{"derivedFrom":makeQuery(id+"F5.opPattern","COPY",BODY,{"derivedFrom":makeQuery(id+"F4.opPattern","COPY",BODY,{"derivedFrom":makeQuery(id+"F2.opPattern","COPY",BODY,{"derivedFrom":makeQuery(id+"F1.opExtrude","SWEPT_BODY",BODY,{"disambiguationData":[OSD([sQuery(id+"F0.wireOp",EDGE,"E0.bottom"),sQuery(id+"F0.wireOp",EDGE,"E0.top"),sQuery(id+"F0.wireOp",EDGE,"E0.left"),sQuery(id+"F0.wireOp",EDGE,"E0.right")])]}),"instanceName":"1"}),"instanceName":"1"}),"instanceName":"1"}),"instanceName":"1"}),"instanceName":"1"}),"instanceName":"1"}),"instanceName":"1"}),"instanceName":"1"}),"instanceName":"1"}),"instanceName":"1"});
            var Q24;
            Q24=makeQuery(id+"F40.opPattern","COPY",BODY,{"derivedFrom":makeQuery(id+"F23.opPattern","COPY",BODY,{"derivedFrom":makeQuery(id+"F19.opPattern","COPY",BODY,{"derivedFrom":makeQuery(id+"F17.opPattern","COPY",BODY,{"derivedFrom":makeQuery(id+"F5.opPattern","COPY",BODY,{"derivedFrom":makeQuery(id+"F4.opPattern","COPY",BODY,{"derivedFrom":makeQuery(id+"F1.opExtrude","SWEPT_BODY",BODY,{"disambiguationData":[OSD([sQuery(id+"F0.wireOp",EDGE,"E0.bottom"),sQuery(id+"F0.wireOp",EDGE,"E0.top"),sQuery(id+"F0.wireOp",EDGE,"E0.left"),sQuery(id+"F0.wireOp",EDGE,"E0.right")])]}),"instanceName":"1"}),"instanceName":"1"}),"instanceName":"1"}),"instanceName":"1"}),"instanceName":"1"}),"instanceName":"1"});
            var Q25;
            Q25=makeQuery(id+"F40.opPattern","COPY",BODY,{"derivedFrom":makeQuery(id+"F23.opPattern","COPY",BODY,{"derivedFrom":makeQuery(id+"F19.opPattern","COPY",BODY,{"derivedFrom":makeQuery(id+"F17.opPattern","COPY",BODY,{"derivedFrom":makeQuery(id+"F6.opPattern","COPY",BODY,{"derivedFrom":makeQuery(id+"F5.opPattern","COPY",BODY,{"derivedFrom":makeQuery(id+"F4.opPattern","COPY",BODY,{"derivedFrom":makeQuery(id+"F1.opExtrude","SWEPT_BODY",BODY,{"disambiguationData":[OSD([sQuery(id+"F0.wireOp",EDGE,"E0.bottom"),sQuery(id+"F0.wireOp",EDGE,"E0.top"),sQuery(id+"F0.wireOp",EDGE,"E0.left"),sQuery(id+"F0.wireOp",EDGE,"E0.right")])]}),"instanceName":"1"}),"instanceName":"1"}),"instanceName":"1"}),"instanceName":"1"}),"instanceName":"1"}),"instanceName":"1"}),"instanceName":"1"});
            var Q26;
            Q26=makeQuery(id+"F40.opPattern","COPY",BODY,{"derivedFrom":makeQuery(id+"F23.opPattern","COPY",BODY,{"derivedFrom":makeQuery(id+"F19.opPattern","COPY",BODY,{"derivedFrom":makeQuery(id+"F5.opPattern","COPY",BODY,{"derivedFrom":makeQuery(id+"F4.opPattern","COPY",BODY,{"derivedFrom":makeQuery(id+"F2.opPattern","COPY",BODY,{"derivedFrom":makeQuery(id+"F1.opExtrude","SWEPT_BODY",BODY,{"disambiguationData":[OSD([sQuery(id+"F0.wireOp",EDGE,"E0.bottom"),sQuery(id+"F0.wireOp",EDGE,"E0.top"),sQuery(id+"F0.wireOp",EDGE,"E0.left"),sQuery(id+"F0.wireOp",EDGE,"E0.right")])]}),"instanceName":"1"}),"instanceName":"1"}),"instanceName":"1"}),"instanceName":"1"}),"instanceName":"1"}),"instanceName":"1"});
            var Q27;
            Q27=makeQuery(id+"F40.opPattern","COPY",BODY,{"derivedFrom":makeQuery(id+"F23.opPattern","COPY",BODY,{"derivedFrom":makeQuery(id+"F19.opPattern","COPY",BODY,{"derivedFrom":makeQuery(id+"F6.opPattern","COPY",BODY,{"derivedFrom":makeQuery(id+"F5.opPattern","COPY",BODY,{"derivedFrom":makeQuery(id+"F4.opPattern","COPY",BODY,{"derivedFrom":makeQuery(id+"F2.opPattern","COPY",BODY,{"derivedFrom":makeQuery(id+"F1.opExtrude","SWEPT_BODY",BODY,{"disambiguationData":[OSD([sQuery(id+"F0.wireOp",EDGE,"E0.bottom"),sQuery(id+"F0.wireOp",EDGE,"E0.top"),sQuery(id+"F0.wireOp",EDGE,"E0.left"),sQuery(id+"F0.wireOp",EDGE,"E0.right")])]}),"instanceName":"1"}),"instanceName":"1"}),"instanceName":"1"}),"instanceName":"1"}),"instanceName":"1"}),"instanceName":"1"}),"instanceName":"1"});
            var Q28;
            Q28=makeQuery(id+"F40.opPattern","COPY",BODY,{"derivedFrom":makeQuery(id+"F21.opPattern","COPY",BODY,{"derivedFrom":makeQuery(id+"F19.opPattern","COPY",BODY,{"derivedFrom":makeQuery(id+"F17.opPattern","COPY",BODY,{"derivedFrom":makeQuery(id+"F12.opPattern","COPY",BODY,{"derivedFrom":makeQuery(id+"F6.opPattern","COPY",BODY,{"derivedFrom":makeQuery(id+"F5.opPattern","COPY",BODY,{"derivedFrom":makeQuery(id+"F4.opPattern","COPY",BODY,{"derivedFrom":makeQuery(id+"F2.opPattern","COPY",BODY,{"derivedFrom":makeQuery(id+"F1.opExtrude","SWEPT_BODY",BODY,{"disambiguationData":[OSD([sQuery(id+"F0.wireOp",EDGE,"E0.bottom"),sQuery(id+"F0.wireOp",EDGE,"E0.top"),sQuery(id+"F0.wireOp",EDGE,"E0.left"),sQuery(id+"F0.wireOp",EDGE,"E0.right")])]}),"instanceName":"1"}),"instanceName":"1"}),"instanceName":"1"}),"instanceName":"1"}),"instanceName":"1"}),"instanceName":"1"}),"instanceName":"1"}),"instanceName":"1"}),"instanceName":"1"});
            var Q29;
            Q29=makeQuery(id+"F40.opPattern","COPY",EDGE,{"derivedFrom":makeQuery(id+"F27.opPattern","COPY",EDGE,{"derivedFrom":makeQuery(id+"F23.opPattern","COPY",EDGE,{"derivedFrom":makeQuery(id+"F21.opPattern","COPY",EDGE,{"derivedFrom":makeQuery(id+"F19.opPattern","COPY",EDGE,{"derivedFrom":makeQuery(id+"F17.opPattern","COPY",EDGE,{"derivedFrom":makeQuery(id+"F5.opPattern","COPY",EDGE,{"derivedFrom":makeQuery(id+"F4.opPattern","COPY",EDGE,{"derivedFrom":makeQuery(id+"F1.opExtrude","CAP_EDGE",EDGE,{"disambiguationData":[OSD([sQuery(id+"F0.wireOp",EDGE,"E0.right")])],"isStart":false}),"instanceName":"1"}),"instanceName":"1"}),"instanceName":"1"}),"instanceName":"1"}),"instanceName":"1"}),"instanceName":"1"}),"instanceName":"1"}),"instanceName":"1"});
            transform(context, id + "F45", {"entities" : qUnion([Q0, Q1, Q2, Q3, Q4, Q5, Q6, Q7, Q8, Q9, Q10, Q11, Q12, Q13, Q14, Q15, Q16, Q17, Q18, Q19, Q20, Q21, Q22, Q23, Q24, Q25, Q26, Q27, Q28]), "transformType" : TransformType.TRANSLATION_DISTANCE, "transformDirection" : qUnion([Q29]), "distance" : 110 * mm, "makeCopy" : true});
        }
        {
            var Q0;
            Q0=makeQuery(id+"F45.opPattern","COPY",BODY,{"derivedFrom":makeQuery(id+"F40.opPattern","COPY",BODY,{"derivedFrom":makeQuery(id+"F19.opPattern","COPY",BODY,{"derivedFrom":makeQuery(id+"F17.opPattern","COPY",BODY,{"derivedFrom":makeQuery(id+"F5.opPattern","COPY",BODY,{"derivedFrom":makeQuery(id+"F4.opPattern","COPY",BODY,{"derivedFrom":makeQuery(id+"F2.opPattern","COPY",BODY,{"derivedFrom":makeQuery(id+"F1.opExtrude","SWEPT_BODY",BODY,{"disambiguationData":[OSD([sQuery(id+"F0.wireOp",EDGE,"E0.bottom"),sQuery(id+"F0.wireOp",EDGE,"E0.top"),sQuery(id+"F0.wireOp",EDGE,"E0.left"),sQuery(id+"F0.wireOp",EDGE,"E0.right")])]}),"instanceName":"1"}),"instanceName":"1"}),"instanceName":"1"}),"instanceName":"1"}),"instanceName":"1"}),"instanceName":"1"}),"instanceName":"1"});
            var Q1;
            Q1=makeQuery(id+"F45.opPattern","COPY",BODY,{"derivedFrom":makeQuery(id+"F40.opPattern","COPY",BODY,{"derivedFrom":makeQuery(id+"F28.opPattern","COPY",BODY,{"derivedFrom":makeQuery(id+"F23.opPattern","COPY",BODY,{"derivedFrom":makeQuery(id+"F19.opPattern","COPY",BODY,{"derivedFrom":makeQuery(id+"F17.opPattern","COPY",BODY,{"derivedFrom":makeQuery(id+"F13.opPattern","COPY",BODY,{"derivedFrom":makeQuery(id+"F5.opPattern","COPY",BODY,{"derivedFrom":makeQuery(id+"F4.opPattern","COPY",BODY,{"derivedFrom":makeQuery(id+"F1.opExtrude","SWEPT_BODY",BODY,{"disambiguationData":[OSD([sQuery(id+"F0.wireOp",EDGE,"E0.bottom"),sQuery(id+"F0.wireOp",EDGE,"E0.top"),sQuery(id+"F0.wireOp",EDGE,"E0.left"),sQuery(id+"F0.wireOp",EDGE,"E0.right")])]}),"instanceName":"1"}),"instanceName":"1"}),"instanceName":"1"}),"instanceName":"1"}),"instanceName":"1"}),"instanceName":"1"}),"instanceName":"1"}),"instanceName":"1"}),"instanceName":"1"});
            var Q2;
            Q2=makeQuery(id+"F45.opPattern","COPY",BODY,{"derivedFrom":makeQuery(id+"F40.opPattern","COPY",BODY,{"derivedFrom":makeQuery(id+"F23.opPattern","COPY",BODY,{"derivedFrom":makeQuery(id+"F19.opPattern","COPY",BODY,{"derivedFrom":makeQuery(id+"F12.opPattern","COPY",BODY,{"derivedFrom":makeQuery(id+"F6.opPattern","COPY",BODY,{"derivedFrom":makeQuery(id+"F5.opPattern","COPY",BODY,{"derivedFrom":makeQuery(id+"F4.opPattern","COPY",BODY,{"derivedFrom":makeQuery(id+"F2.opPattern","COPY",BODY,{"derivedFrom":makeQuery(id+"F1.opExtrude","SWEPT_BODY",BODY,{"disambiguationData":[OSD([sQuery(id+"F0.wireOp",EDGE,"E0.bottom"),sQuery(id+"F0.wireOp",EDGE,"E0.top"),sQuery(id+"F0.wireOp",EDGE,"E0.left"),sQuery(id+"F0.wireOp",EDGE,"E0.right")])]}),"instanceName":"1"}),"instanceName":"1"}),"instanceName":"1"}),"instanceName":"1"}),"instanceName":"1"}),"instanceName":"1"}),"instanceName":"1"}),"instanceName":"1"}),"instanceName":"1"});
            var Q3;
            Q3=makeQuery(id+"F45.opPattern","COPY",BODY,{"derivedFrom":makeQuery(id+"F40.opPattern","COPY",BODY,{"derivedFrom":makeQuery(id+"F23.opPattern","COPY",BODY,{"derivedFrom":makeQuery(id+"F19.opPattern","COPY",BODY,{"derivedFrom":makeQuery(id+"F17.opPattern","COPY",BODY,{"derivedFrom":makeQuery(id+"F13.opPattern","COPY",BODY,{"derivedFrom":makeQuery(id+"F5.opPattern","COPY",BODY,{"derivedFrom":makeQuery(id+"F4.opPattern","COPY",BODY,{"derivedFrom":makeQuery(id+"F1.opExtrude","SWEPT_BODY",BODY,{"disambiguationData":[OSD([sQuery(id+"F0.wireOp",EDGE,"E0.bottom"),sQuery(id+"F0.wireOp",EDGE,"E0.top"),sQuery(id+"F0.wireOp",EDGE,"E0.left"),sQuery(id+"F0.wireOp",EDGE,"E0.right")])]}),"instanceName":"1"}),"instanceName":"1"}),"instanceName":"1"}),"instanceName":"1"}),"instanceName":"1"}),"instanceName":"1"}),"instanceName":"1"}),"instanceName":"1"});
            var Q4;
            Q4=makeQuery(id+"F45.opPattern","COPY",BODY,{"derivedFrom":makeQuery(id+"F40.opPattern","COPY",BODY,{"derivedFrom":makeQuery(id+"F19.opPattern","COPY",BODY,{"derivedFrom":makeQuery(id+"F17.opPattern","COPY",BODY,{"derivedFrom":makeQuery(id+"F6.opPattern","COPY",BODY,{"derivedFrom":makeQuery(id+"F5.opPattern","COPY",BODY,{"derivedFrom":makeQuery(id+"F4.opPattern","COPY",BODY,{"derivedFrom":makeQuery(id+"F2.opPattern","COPY",BODY,{"derivedFrom":makeQuery(id+"F1.opExtrude","SWEPT_BODY",BODY,{"disambiguationData":[OSD([sQuery(id+"F0.wireOp",EDGE,"E0.bottom"),sQuery(id+"F0.wireOp",EDGE,"E0.top"),sQuery(id+"F0.wireOp",EDGE,"E0.left"),sQuery(id+"F0.wireOp",EDGE,"E0.right")])]}),"instanceName":"1"}),"instanceName":"1"}),"instanceName":"1"}),"instanceName":"1"}),"instanceName":"1"}),"instanceName":"1"}),"instanceName":"1"}),"instanceName":"1"});
            var Q5;
            Q5=makeQuery(id+"F45.opPattern","COPY",BODY,{"derivedFrom":makeQuery(id+"F40.opPattern","COPY",BODY,{"derivedFrom":makeQuery(id+"F19.opPattern","COPY",BODY,{"derivedFrom":makeQuery(id+"F17.opPattern","COPY",BODY,{"derivedFrom":makeQuery(id+"F12.opPattern","COPY",BODY,{"derivedFrom":makeQuery(id+"F6.opPattern","COPY",BODY,{"derivedFrom":makeQuery(id+"F5.opPattern","COPY",BODY,{"derivedFrom":makeQuery(id+"F4.opPattern","COPY",BODY,{"derivedFrom":makeQuery(id+"F1.opExtrude","SWEPT_BODY",BODY,{"disambiguationData":[OSD([sQuery(id+"F0.wireOp",EDGE,"E0.bottom"),sQuery(id+"F0.wireOp",EDGE,"E0.top"),sQuery(id+"F0.wireOp",EDGE,"E0.left"),sQuery(id+"F0.wireOp",EDGE,"E0.right")])]}),"instanceName":"1"}),"instanceName":"1"}),"instanceName":"1"}),"instanceName":"1"}),"instanceName":"1"}),"instanceName":"1"}),"instanceName":"1"}),"instanceName":"1"});
            var Q6;
            Q6=makeQuery(id+"F45.opPattern","COPY",BODY,{"derivedFrom":makeQuery(id+"F40.opPattern","COPY",BODY,{"derivedFrom":makeQuery(id+"F19.opPattern","COPY",BODY,{"derivedFrom":makeQuery(id+"F15.opPattern","COPY",BODY,{"derivedFrom":makeQuery(id+"F12.opPattern","COPY",BODY,{"derivedFrom":makeQuery(id+"F6.opPattern","COPY",BODY,{"derivedFrom":makeQuery(id+"F5.opPattern","COPY",BODY,{"derivedFrom":makeQuery(id+"F4.opPattern","COPY",BODY,{"derivedFrom":makeQuery(id+"F2.opPattern","COPY",BODY,{"derivedFrom":makeQuery(id+"F1.opExtrude","SWEPT_BODY",BODY,{"disambiguationData":[OSD([sQuery(id+"F0.wireOp",EDGE,"E0.bottom"),sQuery(id+"F0.wireOp",EDGE,"E0.top"),sQuery(id+"F0.wireOp",EDGE,"E0.left"),sQuery(id+"F0.wireOp",EDGE,"E0.right")])]}),"instanceName":"1"}),"instanceName":"1"}),"instanceName":"1"}),"instanceName":"1"}),"instanceName":"1"}),"instanceName":"1"}),"instanceName":"1"}),"instanceName":"1"}),"instanceName":"1"});
            var Q7;
            Q7=makeQuery(id+"F45.opPattern","COPY",BODY,{"derivedFrom":makeQuery(id+"F40.opPattern","COPY",BODY,{"derivedFrom":makeQuery(id+"F23.opPattern","COPY",BODY,{"derivedFrom":makeQuery(id+"F19.opPattern","COPY",BODY,{"derivedFrom":makeQuery(id+"F17.opPattern","COPY",BODY,{"derivedFrom":makeQuery(id+"F5.opPattern","COPY",BODY,{"derivedFrom":makeQuery(id+"F4.opPattern","COPY",BODY,{"derivedFrom":makeQuery(id+"F1.opExtrude","SWEPT_BODY",BODY,{"disambiguationData":[OSD([sQuery(id+"F0.wireOp",EDGE,"E0.bottom"),sQuery(id+"F0.wireOp",EDGE,"E0.top"),sQuery(id+"F0.wireOp",EDGE,"E0.left"),sQuery(id+"F0.wireOp",EDGE,"E0.right")])]}),"instanceName":"1"}),"instanceName":"1"}),"instanceName":"1"}),"instanceName":"1"}),"instanceName":"1"}),"instanceName":"1"}),"instanceName":"1"});
            var Q8;
            Q8=makeQuery(id+"F45.opPattern","COPY",BODY,{"derivedFrom":makeQuery(id+"F40.opPattern","COPY",BODY,{"derivedFrom":makeQuery(id+"F23.opPattern","COPY",BODY,{"derivedFrom":makeQuery(id+"F21.opPattern","COPY",BODY,{"derivedFrom":makeQuery(id+"F19.opPattern","COPY",BODY,{"derivedFrom":makeQuery(id+"F12.opPattern","COPY",BODY,{"derivedFrom":makeQuery(id+"F6.opPattern","COPY",BODY,{"derivedFrom":makeQuery(id+"F5.opPattern","COPY",BODY,{"derivedFrom":makeQuery(id+"F4.opPattern","COPY",BODY,{"derivedFrom":makeQuery(id+"F2.opPattern","COPY",BODY,{"derivedFrom":makeQuery(id+"F1.opExtrude","SWEPT_BODY",BODY,{"disambiguationData":[OSD([sQuery(id+"F0.wireOp",EDGE,"E0.bottom"),sQuery(id+"F0.wireOp",EDGE,"E0.top"),sQuery(id+"F0.wireOp",EDGE,"E0.left"),sQuery(id+"F0.wireOp",EDGE,"E0.right")])]}),"instanceName":"1"}),"instanceName":"1"}),"instanceName":"1"}),"instanceName":"1"}),"instanceName":"1"}),"instanceName":"1"}),"instanceName":"1"}),"instanceName":"1"}),"instanceName":"1"}),"instanceName":"1"});
            var Q9;
            Q9=makeQuery(id+"F45.opPattern","COPY",BODY,{"derivedFrom":makeQuery(id+"F40.opPattern","COPY",BODY,{"derivedFrom":makeQuery(id+"F29.opPattern","COPY",BODY,{"derivedFrom":makeQuery(id+"F19.opPattern","COPY",BODY,{"derivedFrom":makeQuery(id+"F17.opPattern","COPY",BODY,{"derivedFrom":makeQuery(id+"F15.opPattern","COPY",BODY,{"derivedFrom":makeQuery(id+"F12.opPattern","COPY",BODY,{"derivedFrom":makeQuery(id+"F6.opPattern","COPY",BODY,{"derivedFrom":makeQuery(id+"F5.opPattern","COPY",BODY,{"derivedFrom":makeQuery(id+"F4.opPattern","COPY",BODY,{"derivedFrom":makeQuery(id+"F2.opPattern","COPY",BODY,{"derivedFrom":makeQuery(id+"F1.opExtrude","SWEPT_BODY",BODY,{"disambiguationData":[OSD([sQuery(id+"F0.wireOp",EDGE,"E0.bottom"),sQuery(id+"F0.wireOp",EDGE,"E0.top"),sQuery(id+"F0.wireOp",EDGE,"E0.left"),sQuery(id+"F0.wireOp",EDGE,"E0.right")])]}),"instanceName":"1"}),"instanceName":"1"}),"instanceName":"1"}),"instanceName":"1"}),"instanceName":"1"}),"instanceName":"1"}),"instanceName":"1"}),"instanceName":"1"}),"instanceName":"1"}),"instanceName":"1"}),"instanceName":"1"});
            var Q10;
            Q10=makeQuery(id+"F45.opPattern","COPY",BODY,{"derivedFrom":makeQuery(id+"F40.opPattern","COPY",BODY,{"derivedFrom":makeQuery(id+"F23.opPattern","COPY",BODY,{"derivedFrom":makeQuery(id+"F19.opPattern","COPY",BODY,{"derivedFrom":makeQuery(id+"F17.opPattern","COPY",BODY,{"derivedFrom":makeQuery(id+"F6.opPattern","COPY",BODY,{"derivedFrom":makeQuery(id+"F5.opPattern","COPY",BODY,{"derivedFrom":makeQuery(id+"F4.opPattern","COPY",BODY,{"derivedFrom":makeQuery(id+"F2.opPattern","COPY",BODY,{"derivedFrom":makeQuery(id+"F1.opExtrude","SWEPT_BODY",BODY,{"disambiguationData":[OSD([sQuery(id+"F0.wireOp",EDGE,"E0.bottom"),sQuery(id+"F0.wireOp",EDGE,"E0.top"),sQuery(id+"F0.wireOp",EDGE,"E0.left"),sQuery(id+"F0.wireOp",EDGE,"E0.right")])]}),"instanceName":"1"}),"instanceName":"1"}),"instanceName":"1"}),"instanceName":"1"}),"instanceName":"1"}),"instanceName":"1"}),"instanceName":"1"}),"instanceName":"1"}),"instanceName":"1"});
            var Q11;
            Q11=makeQuery(id+"F45.opPattern","COPY",BODY,{"derivedFrom":makeQuery(id+"F40.opPattern","COPY",BODY,{"derivedFrom":makeQuery(id+"F19.opPattern","COPY",BODY,{"derivedFrom":makeQuery(id+"F17.opPattern","COPY",BODY,{"derivedFrom":makeQuery(id+"F13.opPattern","COPY",BODY,{"derivedFrom":makeQuery(id+"F5.opPattern","COPY",BODY,{"derivedFrom":makeQuery(id+"F4.opPattern","COPY",BODY,{"derivedFrom":makeQuery(id+"F1.opExtrude","SWEPT_BODY",BODY,{"disambiguationData":[OSD([sQuery(id+"F0.wireOp",EDGE,"E0.bottom"),sQuery(id+"F0.wireOp",EDGE,"E0.top"),sQuery(id+"F0.wireOp",EDGE,"E0.left"),sQuery(id+"F0.wireOp",EDGE,"E0.right")])]}),"instanceName":"1"}),"instanceName":"1"}),"instanceName":"1"}),"instanceName":"1"}),"instanceName":"1"}),"instanceName":"1"}),"instanceName":"1"});
            var Q12;
            Q12=makeQuery(id+"F45.opPattern","COPY",BODY,{"derivedFrom":makeQuery(id+"F40.opPattern","COPY",BODY,{"derivedFrom":makeQuery(id+"F23.opPattern","COPY",BODY,{"derivedFrom":makeQuery(id+"F19.opPattern","COPY",BODY,{"derivedFrom":makeQuery(id+"F17.opPattern","COPY",BODY,{"derivedFrom":makeQuery(id+"F15.opPattern","COPY",BODY,{"derivedFrom":makeQuery(id+"F12.opPattern","COPY",BODY,{"derivedFrom":makeQuery(id+"F6.opPattern","COPY",BODY,{"derivedFrom":makeQuery(id+"F5.opPattern","COPY",BODY,{"derivedFrom":makeQuery(id+"F4.opPattern","COPY",BODY,{"derivedFrom":makeQuery(id+"F2.opPattern","COPY",BODY,{"derivedFrom":makeQuery(id+"F1.opExtrude","SWEPT_BODY",BODY,{"disambiguationData":[OSD([sQuery(id+"F0.wireOp",EDGE,"E0.bottom"),sQuery(id+"F0.wireOp",EDGE,"E0.top"),sQuery(id+"F0.wireOp",EDGE,"E0.left"),sQuery(id+"F0.wireOp",EDGE,"E0.right")])]}),"instanceName":"1"}),"instanceName":"1"}),"instanceName":"1"}),"instanceName":"1"}),"instanceName":"1"}),"instanceName":"1"}),"instanceName":"1"}),"instanceName":"1"}),"instanceName":"1"}),"instanceName":"1"}),"instanceName":"1"});
            var Q13;
            Q13=makeQuery(id+"F45.opPattern","COPY",BODY,{"derivedFrom":makeQuery(id+"F40.opPattern","COPY",BODY,{"derivedFrom":makeQuery(id+"F21.opPattern","COPY",BODY,{"derivedFrom":makeQuery(id+"F19.opPattern","COPY",BODY,{"derivedFrom":makeQuery(id+"F17.opPattern","COPY",BODY,{"derivedFrom":makeQuery(id+"F12.opPattern","COPY",BODY,{"derivedFrom":makeQuery(id+"F6.opPattern","COPY",BODY,{"derivedFrom":makeQuery(id+"F5.opPattern","COPY",BODY,{"derivedFrom":makeQuery(id+"F4.opPattern","COPY",BODY,{"derivedFrom":makeQuery(id+"F2.opPattern","COPY",BODY,{"derivedFrom":makeQuery(id+"F1.opExtrude","SWEPT_BODY",BODY,{"disambiguationData":[OSD([sQuery(id+"F0.wireOp",EDGE,"E0.bottom"),sQuery(id+"F0.wireOp",EDGE,"E0.top"),sQuery(id+"F0.wireOp",EDGE,"E0.left"),sQuery(id+"F0.wireOp",EDGE,"E0.right")])]}),"instanceName":"1"}),"instanceName":"1"}),"instanceName":"1"}),"instanceName":"1"}),"instanceName":"1"}),"instanceName":"1"}),"instanceName":"1"}),"instanceName":"1"}),"instanceName":"1"}),"instanceName":"1"});
            var Q14;
            Q14=makeQuery(id+"F45.opPattern","COPY",BODY,{"derivedFrom":makeQuery(id+"F40.opPattern","COPY",BODY,{"derivedFrom":makeQuery(id+"F21.opPattern","COPY",BODY,{"derivedFrom":makeQuery(id+"F19.opPattern","COPY",BODY,{"derivedFrom":makeQuery(id+"F17.opPattern","COPY",BODY,{"derivedFrom":makeQuery(id+"F6.opPattern","COPY",BODY,{"derivedFrom":makeQuery(id+"F5.opPattern","COPY",BODY,{"derivedFrom":makeQuery(id+"F4.opPattern","COPY",BODY,{"derivedFrom":makeQuery(id+"F1.opExtrude","SWEPT_BODY",BODY,{"disambiguationData":[OSD([sQuery(id+"F0.wireOp",EDGE,"E0.bottom"),sQuery(id+"F0.wireOp",EDGE,"E0.top"),sQuery(id+"F0.wireOp",EDGE,"E0.left"),sQuery(id+"F0.wireOp",EDGE,"E0.right")])]}),"instanceName":"1"}),"instanceName":"1"}),"instanceName":"1"}),"instanceName":"1"}),"instanceName":"1"}),"instanceName":"1"}),"instanceName":"1"}),"instanceName":"1"});
            var Q15;
            Q15=makeQuery(id+"F45.opPattern","COPY",BODY,{"derivedFrom":makeQuery(id+"F40.opPattern","COPY",BODY,{"derivedFrom":makeQuery(id+"F23.opPattern","COPY",BODY,{"derivedFrom":makeQuery(id+"F19.opPattern","COPY",BODY,{"derivedFrom":makeQuery(id+"F17.opPattern","COPY",BODY,{"derivedFrom":makeQuery(id+"F6.opPattern","COPY",BODY,{"derivedFrom":makeQuery(id+"F5.opPattern","COPY",BODY,{"derivedFrom":makeQuery(id+"F4.opPattern","COPY",BODY,{"derivedFrom":makeQuery(id+"F1.opExtrude","SWEPT_BODY",BODY,{"disambiguationData":[OSD([sQuery(id+"F0.wireOp",EDGE,"E0.bottom"),sQuery(id+"F0.wireOp",EDGE,"E0.top"),sQuery(id+"F0.wireOp",EDGE,"E0.left"),sQuery(id+"F0.wireOp",EDGE,"E0.right")])]}),"instanceName":"1"}),"instanceName":"1"}),"instanceName":"1"}),"instanceName":"1"}),"instanceName":"1"}),"instanceName":"1"}),"instanceName":"1"}),"instanceName":"1"});
            var Q16;
            Q16=makeQuery(id+"F45.opPattern","COPY",BODY,{"derivedFrom":makeQuery(id+"F40.opPattern","COPY",BODY,{"derivedFrom":makeQuery(id+"F23.opPattern","COPY",BODY,{"derivedFrom":makeQuery(id+"F19.opPattern","COPY",BODY,{"derivedFrom":makeQuery(id+"F15.opPattern","COPY",BODY,{"derivedFrom":makeQuery(id+"F12.opPattern","COPY",BODY,{"derivedFrom":makeQuery(id+"F6.opPattern","COPY",BODY,{"derivedFrom":makeQuery(id+"F5.opPattern","COPY",BODY,{"derivedFrom":makeQuery(id+"F4.opPattern","COPY",BODY,{"derivedFrom":makeQuery(id+"F2.opPattern","COPY",BODY,{"derivedFrom":makeQuery(id+"F1.opExtrude","SWEPT_BODY",BODY,{"disambiguationData":[OSD([sQuery(id+"F0.wireOp",EDGE,"E0.bottom"),sQuery(id+"F0.wireOp",EDGE,"E0.top"),sQuery(id+"F0.wireOp",EDGE,"E0.left"),sQuery(id+"F0.wireOp",EDGE,"E0.right")])]}),"instanceName":"1"}),"instanceName":"1"}),"instanceName":"1"}),"instanceName":"1"}),"instanceName":"1"}),"instanceName":"1"}),"instanceName":"1"}),"instanceName":"1"}),"instanceName":"1"}),"instanceName":"1"});
            var Q17;
            Q17=makeQuery(id+"F45.opPattern","COPY",BODY,{"derivedFrom":makeQuery(id+"F40.opPattern","COPY",BODY,{"derivedFrom":makeQuery(id+"F28.opPattern","COPY",BODY,{"derivedFrom":makeQuery(id+"F23.opPattern","COPY",BODY,{"derivedFrom":makeQuery(id+"F19.opPattern","COPY",BODY,{"derivedFrom":makeQuery(id+"F15.opPattern","COPY",BODY,{"derivedFrom":makeQuery(id+"F12.opPattern","COPY",BODY,{"derivedFrom":makeQuery(id+"F6.opPattern","COPY",BODY,{"derivedFrom":makeQuery(id+"F5.opPattern","COPY",BODY,{"derivedFrom":makeQuery(id+"F4.opPattern","COPY",BODY,{"derivedFrom":makeQuery(id+"F2.opPattern","COPY",BODY,{"derivedFrom":makeQuery(id+"F1.opExtrude","SWEPT_BODY",BODY,{"disambiguationData":[OSD([sQuery(id+"F0.wireOp",EDGE,"E0.bottom"),sQuery(id+"F0.wireOp",EDGE,"E0.top"),sQuery(id+"F0.wireOp",EDGE,"E0.left"),sQuery(id+"F0.wireOp",EDGE,"E0.right")])]}),"instanceName":"1"}),"instanceName":"1"}),"instanceName":"1"}),"instanceName":"1"}),"instanceName":"1"}),"instanceName":"1"}),"instanceName":"1"}),"instanceName":"1"}),"instanceName":"1"}),"instanceName":"1"}),"instanceName":"1"});
            var Q18;
            Q18=makeQuery(id+"F45.opPattern","COPY",BODY,{"derivedFrom":makeQuery(id+"F40.opPattern","COPY",BODY,{"derivedFrom":makeQuery(id+"F23.opPattern","COPY",BODY,{"derivedFrom":makeQuery(id+"F19.opPattern","COPY",BODY,{"derivedFrom":makeQuery(id+"F6.opPattern","COPY",BODY,{"derivedFrom":makeQuery(id+"F5.opPattern","COPY",BODY,{"derivedFrom":makeQuery(id+"F4.opPattern","COPY",BODY,{"derivedFrom":makeQuery(id+"F2.opPattern","COPY",BODY,{"derivedFrom":makeQuery(id+"F1.opExtrude","SWEPT_BODY",BODY,{"disambiguationData":[OSD([sQuery(id+"F0.wireOp",EDGE,"E0.bottom"),sQuery(id+"F0.wireOp",EDGE,"E0.top"),sQuery(id+"F0.wireOp",EDGE,"E0.left"),sQuery(id+"F0.wireOp",EDGE,"E0.right")])]}),"instanceName":"1"}),"instanceName":"1"}),"instanceName":"1"}),"instanceName":"1"}),"instanceName":"1"}),"instanceName":"1"}),"instanceName":"1"}),"instanceName":"1"});
            var Q19;
            Q19=makeQuery(id+"F45.opPattern","COPY",BODY,{"derivedFrom":makeQuery(id+"F40.opPattern","COPY",BODY,{"derivedFrom":makeQuery(id+"F28.opPattern","COPY",BODY,{"derivedFrom":makeQuery(id+"F19.opPattern","COPY",BODY,{"derivedFrom":makeQuery(id+"F17.opPattern","COPY",BODY,{"derivedFrom":makeQuery(id+"F15.opPattern","COPY",BODY,{"derivedFrom":makeQuery(id+"F12.opPattern","COPY",BODY,{"derivedFrom":makeQuery(id+"F6.opPattern","COPY",BODY,{"derivedFrom":makeQuery(id+"F5.opPattern","COPY",BODY,{"derivedFrom":makeQuery(id+"F4.opPattern","COPY",BODY,{"derivedFrom":makeQuery(id+"F2.opPattern","COPY",BODY,{"derivedFrom":makeQuery(id+"F1.opExtrude","SWEPT_BODY",BODY,{"disambiguationData":[OSD([sQuery(id+"F0.wireOp",EDGE,"E0.bottom"),sQuery(id+"F0.wireOp",EDGE,"E0.top"),sQuery(id+"F0.wireOp",EDGE,"E0.left"),sQuery(id+"F0.wireOp",EDGE,"E0.right")])]}),"instanceName":"1"}),"instanceName":"1"}),"instanceName":"1"}),"instanceName":"1"}),"instanceName":"1"}),"instanceName":"1"}),"instanceName":"1"}),"instanceName":"1"}),"instanceName":"1"}),"instanceName":"1"}),"instanceName":"1"});
            var Q20;
            Q20=makeQuery(id+"F45.opPattern","COPY",BODY,{"derivedFrom":makeQuery(id+"F40.opPattern","COPY",BODY,{"derivedFrom":makeQuery(id+"F28.opPattern","COPY",BODY,{"derivedFrom":makeQuery(id+"F19.opPattern","COPY",BODY,{"derivedFrom":makeQuery(id+"F17.opPattern","COPY",BODY,{"derivedFrom":makeQuery(id+"F13.opPattern","COPY",BODY,{"derivedFrom":makeQuery(id+"F5.opPattern","COPY",BODY,{"derivedFrom":makeQuery(id+"F4.opPattern","COPY",BODY,{"derivedFrom":makeQuery(id+"F1.opExtrude","SWEPT_BODY",BODY,{"disambiguationData":[OSD([sQuery(id+"F0.wireOp",EDGE,"E0.bottom"),sQuery(id+"F0.wireOp",EDGE,"E0.top"),sQuery(id+"F0.wireOp",EDGE,"E0.left"),sQuery(id+"F0.wireOp",EDGE,"E0.right")])]}),"instanceName":"1"}),"instanceName":"1"}),"instanceName":"1"}),"instanceName":"1"}),"instanceName":"1"}),"instanceName":"1"}),"instanceName":"1"}),"instanceName":"1"});
            var Q21;
            Q21=makeQuery(id+"F45.opPattern","COPY",BODY,{"derivedFrom":makeQuery(id+"F40.opPattern","COPY",BODY,{"derivedFrom":makeQuery(id+"F19.opPattern","COPY",BODY,{"derivedFrom":makeQuery(id+"F17.opPattern","COPY",BODY,{"derivedFrom":makeQuery(id+"F15.opPattern","COPY",BODY,{"derivedFrom":makeQuery(id+"F12.opPattern","COPY",BODY,{"derivedFrom":makeQuery(id+"F6.opPattern","COPY",BODY,{"derivedFrom":makeQuery(id+"F5.opPattern","COPY",BODY,{"derivedFrom":makeQuery(id+"F4.opPattern","COPY",BODY,{"derivedFrom":makeQuery(id+"F2.opPattern","COPY",BODY,{"derivedFrom":makeQuery(id+"F1.opExtrude","SWEPT_BODY",BODY,{"disambiguationData":[OSD([sQuery(id+"F0.wireOp",EDGE,"E0.bottom"),sQuery(id+"F0.wireOp",EDGE,"E0.top"),sQuery(id+"F0.wireOp",EDGE,"E0.left"),sQuery(id+"F0.wireOp",EDGE,"E0.right")])]}),"instanceName":"1"}),"instanceName":"1"}),"instanceName":"1"}),"instanceName":"1"}),"instanceName":"1"}),"instanceName":"1"}),"instanceName":"1"}),"instanceName":"1"}),"instanceName":"1"}),"instanceName":"1"});
            var Q22;
            Q22=makeQuery(id+"F45.opPattern","COPY",BODY,{"derivedFrom":makeQuery(id+"F40.opPattern","COPY",BODY,{"derivedFrom":makeQuery(id+"F29.opPattern","COPY",BODY,{"derivedFrom":makeQuery(id+"F23.opPattern","COPY",BODY,{"derivedFrom":makeQuery(id+"F19.opPattern","COPY",BODY,{"derivedFrom":makeQuery(id+"F15.opPattern","COPY",BODY,{"derivedFrom":makeQuery(id+"F12.opPattern","COPY",BODY,{"derivedFrom":makeQuery(id+"F6.opPattern","COPY",BODY,{"derivedFrom":makeQuery(id+"F5.opPattern","COPY",BODY,{"derivedFrom":makeQuery(id+"F4.opPattern","COPY",BODY,{"derivedFrom":makeQuery(id+"F2.opPattern","COPY",BODY,{"derivedFrom":makeQuery(id+"F1.opExtrude","SWEPT_BODY",BODY,{"disambiguationData":[OSD([sQuery(id+"F0.wireOp",EDGE,"E0.bottom"),sQuery(id+"F0.wireOp",EDGE,"E0.top"),sQuery(id+"F0.wireOp",EDGE,"E0.left"),sQuery(id+"F0.wireOp",EDGE,"E0.right")])]}),"instanceName":"1"}),"instanceName":"1"}),"instanceName":"1"}),"instanceName":"1"}),"instanceName":"1"}),"instanceName":"1"}),"instanceName":"1"}),"instanceName":"1"}),"instanceName":"1"}),"instanceName":"1"}),"instanceName":"1"});
            var Q23;
            Q23=makeQuery(id+"F45.opPattern","COPY",BODY,{"derivedFrom":makeQuery(id+"F40.opPattern","COPY",BODY,{"derivedFrom":makeQuery(id+"F23.opPattern","COPY",BODY,{"derivedFrom":makeQuery(id+"F19.opPattern","COPY",BODY,{"derivedFrom":makeQuery(id+"F5.opPattern","COPY",BODY,{"derivedFrom":makeQuery(id+"F4.opPattern","COPY",BODY,{"derivedFrom":makeQuery(id+"F2.opPattern","COPY",BODY,{"derivedFrom":makeQuery(id+"F1.opExtrude","SWEPT_BODY",BODY,{"disambiguationData":[OSD([sQuery(id+"F0.wireOp",EDGE,"E0.bottom"),sQuery(id+"F0.wireOp",EDGE,"E0.top"),sQuery(id+"F0.wireOp",EDGE,"E0.left"),sQuery(id+"F0.wireOp",EDGE,"E0.right")])]}),"instanceName":"1"}),"instanceName":"1"}),"instanceName":"1"}),"instanceName":"1"}),"instanceName":"1"}),"instanceName":"1"}),"instanceName":"1"});
            var Q24;
            Q24=makeQuery(id+"F45.opPattern","COPY",BODY,{"derivedFrom":makeQuery(id+"F40.opPattern","COPY",BODY,{"derivedFrom":makeQuery(id+"F19.opPattern","COPY",BODY,{"derivedFrom":makeQuery(id+"F17.opPattern","COPY",BODY,{"derivedFrom":makeQuery(id+"F12.opPattern","COPY",BODY,{"derivedFrom":makeQuery(id+"F6.opPattern","COPY",BODY,{"derivedFrom":makeQuery(id+"F5.opPattern","COPY",BODY,{"derivedFrom":makeQuery(id+"F4.opPattern","COPY",BODY,{"derivedFrom":makeQuery(id+"F2.opPattern","COPY",BODY,{"derivedFrom":makeQuery(id+"F1.opExtrude","SWEPT_BODY",BODY,{"disambiguationData":[OSD([sQuery(id+"F0.wireOp",EDGE,"E0.bottom"),sQuery(id+"F0.wireOp",EDGE,"E0.top"),sQuery(id+"F0.wireOp",EDGE,"E0.left"),sQuery(id+"F0.wireOp",EDGE,"E0.right")])]}),"instanceName":"1"}),"instanceName":"1"}),"instanceName":"1"}),"instanceName":"1"}),"instanceName":"1"}),"instanceName":"1"}),"instanceName":"1"}),"instanceName":"1"}),"instanceName":"1"});
            var Q25;
            Q25=makeQuery(id+"F45.opPattern","COPY",BODY,{"derivedFrom":makeQuery(id+"F40.opPattern","COPY",BODY,{"derivedFrom":makeQuery(id+"F21.opPattern","COPY",BODY,{"derivedFrom":makeQuery(id+"F19.opPattern","COPY",BODY,{"derivedFrom":makeQuery(id+"F17.opPattern","COPY",BODY,{"derivedFrom":makeQuery(id+"F6.opPattern","COPY",BODY,{"derivedFrom":makeQuery(id+"F5.opPattern","COPY",BODY,{"derivedFrom":makeQuery(id+"F4.opPattern","COPY",BODY,{"derivedFrom":makeQuery(id+"F2.opPattern","COPY",BODY,{"derivedFrom":makeQuery(id+"F1.opExtrude","SWEPT_BODY",BODY,{"disambiguationData":[OSD([sQuery(id+"F0.wireOp",EDGE,"E0.bottom"),sQuery(id+"F0.wireOp",EDGE,"E0.top"),sQuery(id+"F0.wireOp",EDGE,"E0.left"),sQuery(id+"F0.wireOp",EDGE,"E0.right")])]}),"instanceName":"1"}),"instanceName":"1"}),"instanceName":"1"}),"instanceName":"1"}),"instanceName":"1"}),"instanceName":"1"}),"instanceName":"1"}),"instanceName":"1"}),"instanceName":"1"});
            var Q26;
            Q26=makeQuery(id+"F45.opPattern","COPY",BODY,{"derivedFrom":makeQuery(id+"F40.opPattern","COPY",BODY,{"derivedFrom":makeQuery(id+"F23.opPattern","COPY",BODY,{"derivedFrom":makeQuery(id+"F19.opPattern","COPY",BODY,{"derivedFrom":makeQuery(id+"F17.opPattern","COPY",BODY,{"derivedFrom":makeQuery(id+"F12.opPattern","COPY",BODY,{"derivedFrom":makeQuery(id+"F6.opPattern","COPY",BODY,{"derivedFrom":makeQuery(id+"F5.opPattern","COPY",BODY,{"derivedFrom":makeQuery(id+"F4.opPattern","COPY",BODY,{"derivedFrom":makeQuery(id+"F1.opExtrude","SWEPT_BODY",BODY,{"disambiguationData":[OSD([sQuery(id+"F0.wireOp",EDGE,"E0.bottom"),sQuery(id+"F0.wireOp",EDGE,"E0.top"),sQuery(id+"F0.wireOp",EDGE,"E0.left"),sQuery(id+"F0.wireOp",EDGE,"E0.right")])]}),"instanceName":"1"}),"instanceName":"1"}),"instanceName":"1"}),"instanceName":"1"}),"instanceName":"1"}),"instanceName":"1"}),"instanceName":"1"}),"instanceName":"1"}),"instanceName":"1"});
            var Q27;
            Q27=makeQuery(id+"F45.opPattern","COPY",BODY,{"derivedFrom":makeQuery(id+"F40.opPattern","COPY",BODY,{"derivedFrom":makeQuery(id+"F29.opPattern","COPY",BODY,{"derivedFrom":makeQuery(id+"F19.opPattern","COPY",BODY,{"derivedFrom":makeQuery(id+"F17.opPattern","COPY",BODY,{"derivedFrom":makeQuery(id+"F13.opPattern","COPY",BODY,{"derivedFrom":makeQuery(id+"F5.opPattern","COPY",BODY,{"derivedFrom":makeQuery(id+"F4.opPattern","COPY",BODY,{"derivedFrom":makeQuery(id+"F1.opExtrude","SWEPT_BODY",BODY,{"disambiguationData":[OSD([sQuery(id+"F0.wireOp",EDGE,"E0.bottom"),sQuery(id+"F0.wireOp",EDGE,"E0.top"),sQuery(id+"F0.wireOp",EDGE,"E0.left"),sQuery(id+"F0.wireOp",EDGE,"E0.right")])]}),"instanceName":"1"}),"instanceName":"1"}),"instanceName":"1"}),"instanceName":"1"}),"instanceName":"1"}),"instanceName":"1"}),"instanceName":"1"}),"instanceName":"1"});
            var Q28;
            Q28=makeQuery(id+"F45.opPattern","COPY",BODY,{"derivedFrom":makeQuery(id+"F40.opPattern","COPY",BODY,{"derivedFrom":makeQuery(id+"F28.opPattern","COPY",BODY,{"derivedFrom":makeQuery(id+"F19.opPattern","COPY",BODY,{"derivedFrom":makeQuery(id+"F15.opPattern","COPY",BODY,{"derivedFrom":makeQuery(id+"F12.opPattern","COPY",BODY,{"derivedFrom":makeQuery(id+"F6.opPattern","COPY",BODY,{"derivedFrom":makeQuery(id+"F5.opPattern","COPY",BODY,{"derivedFrom":makeQuery(id+"F4.opPattern","COPY",BODY,{"derivedFrom":makeQuery(id+"F2.opPattern","COPY",BODY,{"derivedFrom":makeQuery(id+"F1.opExtrude","SWEPT_BODY",BODY,{"disambiguationData":[OSD([sQuery(id+"F0.wireOp",EDGE,"E0.bottom"),sQuery(id+"F0.wireOp",EDGE,"E0.top"),sQuery(id+"F0.wireOp",EDGE,"E0.left"),sQuery(id+"F0.wireOp",EDGE,"E0.right")])]}),"instanceName":"1"}),"instanceName":"1"}),"instanceName":"1"}),"instanceName":"1"}),"instanceName":"1"}),"instanceName":"1"}),"instanceName":"1"}),"instanceName":"1"}),"instanceName":"1"}),"instanceName":"1"});
            var Q29;
            Q29=makeQuery(id+"F45.opPattern","COPY",EDGE,{"derivedFrom":makeQuery(id+"F40.opPattern","COPY",EDGE,{"derivedFrom":makeQuery(id+"F23.opPattern","COPY",EDGE,{"derivedFrom":makeQuery(id+"F19.opPattern","COPY",EDGE,{"derivedFrom":makeQuery(id+"F17.opPattern","COPY",EDGE,{"derivedFrom":makeQuery(id+"F6.opPattern","COPY",EDGE,{"derivedFrom":makeQuery(id+"F5.opPattern","COPY",EDGE,{"derivedFrom":makeQuery(id+"F4.opPattern","COPY",EDGE,{"derivedFrom":makeQuery(id+"F2.opPattern","COPY",EDGE,{"derivedFrom":makeQuery(id+"F1.opExtrude","CAP_EDGE",EDGE,{"disambiguationData":[OSD([sQuery(id+"F0.wireOp",EDGE,"E0.top")])],"isStart":false}),"instanceName":"1"}),"instanceName":"1"}),"instanceName":"1"}),"instanceName":"1"}),"instanceName":"1"}),"instanceName":"1"}),"instanceName":"1"}),"instanceName":"1"}),"instanceName":"1"});
            transform(context, id + "F46", {"entities" : qUnion([Q0, Q1, Q2, Q3, Q4, Q5, Q6, Q7, Q8, Q9, Q10, Q11, Q12, Q13, Q14, Q15, Q16, Q17, Q18, Q19, Q20, Q21, Q22, Q23, Q24, Q25, Q26, Q27, Q28]), "transformType" : TransformType.TRANSLATION_DISTANCE, "transformDirection" : qUnion([Q29]), "distance" : 50 * mm, "makeCopy" : false});
        }
        {
            var Q0;
            Q0=makeQuery(id+"F45.opPattern","COPY",BODY,{"derivedFrom":makeQuery(id+"F40.opPattern","COPY",BODY,{"derivedFrom":makeQuery(id+"F21.opPattern","COPY",BODY,{"derivedFrom":makeQuery(id+"F19.opPattern","COPY",BODY,{"derivedFrom":makeQuery(id+"F17.opPattern","COPY",BODY,{"derivedFrom":makeQuery(id+"F6.opPattern","COPY",BODY,{"derivedFrom":makeQuery(id+"F5.opPattern","COPY",BODY,{"derivedFrom":makeQuery(id+"F4.opPattern","COPY",BODY,{"derivedFrom":makeQuery(id+"F1.opExtrude","SWEPT_BODY",BODY,{"disambiguationData":[OSD([sQuery(id+"F0.wireOp",EDGE,"E0.bottom"),sQuery(id+"F0.wireOp",EDGE,"E0.top"),sQuery(id+"F0.wireOp",EDGE,"E0.left"),sQuery(id+"F0.wireOp",EDGE,"E0.right")])]}),"instanceName":"1"}),"instanceName":"1"}),"instanceName":"1"}),"instanceName":"1"}),"instanceName":"1"}),"instanceName":"1"}),"instanceName":"1"}),"instanceName":"1"});
            var Q1;
            Q1=makeQuery(id+"F45.opPattern","COPY",EDGE,{"derivedFrom":makeQuery(id+"F40.opPattern","COPY",EDGE,{"derivedFrom":makeQuery(id+"F21.opPattern","COPY",EDGE,{"derivedFrom":makeQuery(id+"F19.opPattern","COPY",EDGE,{"derivedFrom":makeQuery(id+"F17.opPattern","COPY",EDGE,{"derivedFrom":makeQuery(id+"F6.opPattern","COPY",EDGE,{"derivedFrom":makeQuery(id+"F5.opPattern","COPY",EDGE,{"derivedFrom":makeQuery(id+"F4.opPattern","COPY",EDGE,{"derivedFrom":makeQuery(id+"F2.opPattern","COPY",EDGE,{"derivedFrom":makeQuery(id+"F1.opExtrude","CAP_EDGE",EDGE,{"disambiguationData":[OSD([sQuery(id+"F0.wireOp",EDGE,"E0.left")])],"isStart":false}),"instanceName":"1"}),"instanceName":"1"}),"instanceName":"1"}),"instanceName":"1"}),"instanceName":"1"}),"instanceName":"1"}),"instanceName":"1"}),"instanceName":"1"}),"instanceName":"1"});
            transform(context, id + "F47", {"entities" : qUnion([Q0]), "transformType" : TransformType.TRANSLATION_DISTANCE, "transformDirection" : qUnion([Q1]), "distance" : 10 * mm, "makeCopy" : true});
        }
        {
            var Q0;
            Q0=makeQuery(id+"F45.opPattern","COPY",BODY,{"derivedFrom":makeQuery(id+"F40.opPattern","COPY",BODY,{"derivedFrom":makeQuery(id+"F23.opPattern","COPY",BODY,{"derivedFrom":makeQuery(id+"F19.opPattern","COPY",BODY,{"derivedFrom":makeQuery(id+"F17.opPattern","COPY",BODY,{"derivedFrom":makeQuery(id+"F15.opPattern","COPY",BODY,{"derivedFrom":makeQuery(id+"F12.opPattern","COPY",BODY,{"derivedFrom":makeQuery(id+"F6.opPattern","COPY",BODY,{"derivedFrom":makeQuery(id+"F5.opPattern","COPY",BODY,{"derivedFrom":makeQuery(id+"F4.opPattern","COPY",BODY,{"derivedFrom":makeQuery(id+"F2.opPattern","COPY",BODY,{"derivedFrom":makeQuery(id+"F1.opExtrude","SWEPT_BODY",BODY,{"disambiguationData":[OSD([sQuery(id+"F0.wireOp",EDGE,"E0.bottom"),sQuery(id+"F0.wireOp",EDGE,"E0.top"),sQuery(id+"F0.wireOp",EDGE,"E0.left"),sQuery(id+"F0.wireOp",EDGE,"E0.right")])]}),"instanceName":"1"}),"instanceName":"1"}),"instanceName":"1"}),"instanceName":"1"}),"instanceName":"1"}),"instanceName":"1"}),"instanceName":"1"}),"instanceName":"1"}),"instanceName":"1"}),"instanceName":"1"}),"instanceName":"1"});
            var Q1;
            Q1=makeQuery(id+"F45.opPattern","COPY",BODY,{"derivedFrom":makeQuery(id+"F40.opPattern","COPY",BODY,{"derivedFrom":makeQuery(id+"F23.opPattern","COPY",BODY,{"derivedFrom":makeQuery(id+"F19.opPattern","COPY",BODY,{"derivedFrom":makeQuery(id+"F17.opPattern","COPY",BODY,{"derivedFrom":makeQuery(id+"F12.opPattern","COPY",BODY,{"derivedFrom":makeQuery(id+"F6.opPattern","COPY",BODY,{"derivedFrom":makeQuery(id+"F5.opPattern","COPY",BODY,{"derivedFrom":makeQuery(id+"F4.opPattern","COPY",BODY,{"derivedFrom":makeQuery(id+"F1.opExtrude","SWEPT_BODY",BODY,{"disambiguationData":[OSD([sQuery(id+"F0.wireOp",EDGE,"E0.bottom"),sQuery(id+"F0.wireOp",EDGE,"E0.top"),sQuery(id+"F0.wireOp",EDGE,"E0.left"),sQuery(id+"F0.wireOp",EDGE,"E0.right")])]}),"instanceName":"1"}),"instanceName":"1"}),"instanceName":"1"}),"instanceName":"1"}),"instanceName":"1"}),"instanceName":"1"}),"instanceName":"1"}),"instanceName":"1"}),"instanceName":"1"});
            var Q2;
            Q2=makeQuery(id+"F45.opPattern","COPY",EDGE,{"derivedFrom":makeQuery(id+"F40.opPattern","COPY",EDGE,{"derivedFrom":makeQuery(id+"F23.opPattern","COPY",EDGE,{"derivedFrom":makeQuery(id+"F19.opPattern","COPY",EDGE,{"derivedFrom":makeQuery(id+"F17.opPattern","COPY",EDGE,{"derivedFrom":makeQuery(id+"F15.opPattern","COPY",EDGE,{"derivedFrom":makeQuery(id+"F12.opPattern","COPY",EDGE,{"derivedFrom":makeQuery(id+"F6.opPattern","COPY",EDGE,{"derivedFrom":makeQuery(id+"F5.opPattern","COPY",EDGE,{"derivedFrom":makeQuery(id+"F4.opPattern","COPY",EDGE,{"derivedFrom":makeQuery(id+"F2.opPattern","COPY",EDGE,{"derivedFrom":makeQuery(id+"F1.opExtrude","CAP_EDGE",EDGE,{"disambiguationData":[OSD([sQuery(id+"F0.wireOp",EDGE,"E0.top")])],"isStart":false}),"instanceName":"1"}),"instanceName":"1"}),"instanceName":"1"}),"instanceName":"1"}),"instanceName":"1"}),"instanceName":"1"}),"instanceName":"1"}),"instanceName":"1"}),"instanceName":"1"}),"instanceName":"1"}),"instanceName":"1"});
            transform(context, id + "F48", {"entities" : qUnion([Q0, Q1]), "transformType" : TransformType.TRANSLATION_DISTANCE, "transformDirection" : qUnion([Q2]), "distance" : 10 * mm, "makeCopy" : true});
        }
        {
            var Q0;
            Q0=makeQuery(id+"F42.opPattern","COPY",BODY,{"derivedFrom":makeQuery(id+"F29.opPattern","COPY",BODY,{"derivedFrom":makeQuery(id+"F28.opPattern","COPY",BODY,{"derivedFrom":makeQuery(id+"F23.opPattern","COPY",BODY,{"derivedFrom":makeQuery(id+"F19.opPattern","COPY",BODY,{"derivedFrom":makeQuery(id+"F15.opPattern","COPY",BODY,{"derivedFrom":makeQuery(id+"F12.opPattern","COPY",BODY,{"derivedFrom":makeQuery(id+"F6.opPattern","COPY",BODY,{"derivedFrom":makeQuery(id+"F5.opPattern","COPY",BODY,{"derivedFrom":makeQuery(id+"F4.opPattern","COPY",BODY,{"derivedFrom":makeQuery(id+"F2.opPattern","COPY",BODY,{"derivedFrom":makeQuery(id+"F1.opExtrude","SWEPT_BODY",BODY,{"disambiguationData":[OSD([sQuery(id+"F0.wireOp",EDGE,"E0.bottom"),sQuery(id+"F0.wireOp",EDGE,"E0.top"),sQuery(id+"F0.wireOp",EDGE,"E0.left"),sQuery(id+"F0.wireOp",EDGE,"E0.right")])]}),"instanceName":"1"}),"instanceName":"1"}),"instanceName":"1"}),"instanceName":"1"}),"instanceName":"1"}),"instanceName":"1"}),"instanceName":"1"}),"instanceName":"1"}),"instanceName":"1"}),"instanceName":"1"}),"instanceName":"1"});
            var Q1;
            Q1=makeQuery(id+"F42.opPattern","COPY",BODY,{"derivedFrom":makeQuery(id+"F29.opPattern","COPY",BODY,{"derivedFrom":makeQuery(id+"F28.opPattern","COPY",BODY,{"derivedFrom":makeQuery(id+"F19.opPattern","COPY",BODY,{"derivedFrom":makeQuery(id+"F17.opPattern","COPY",BODY,{"derivedFrom":makeQuery(id+"F13.opPattern","COPY",BODY,{"derivedFrom":makeQuery(id+"F5.opPattern","COPY",BODY,{"derivedFrom":makeQuery(id+"F4.opPattern","COPY",BODY,{"derivedFrom":makeQuery(id+"F1.opExtrude","SWEPT_BODY",BODY,{"disambiguationData":[OSD([sQuery(id+"F0.wireOp",EDGE,"E0.bottom"),sQuery(id+"F0.wireOp",EDGE,"E0.top"),sQuery(id+"F0.wireOp",EDGE,"E0.left"),sQuery(id+"F0.wireOp",EDGE,"E0.right")])]}),"instanceName":"1"}),"instanceName":"1"}),"instanceName":"1"}),"instanceName":"1"}),"instanceName":"1"}),"instanceName":"1"}),"instanceName":"1"}),"instanceName":"1"});
            var Q2;
            Q2=makeQuery(id+"F42.opPattern","COPY",BODY,{"derivedFrom":makeQuery(id+"F29.opPattern","COPY",BODY,{"derivedFrom":makeQuery(id+"F28.opPattern","COPY",BODY,{"derivedFrom":makeQuery(id+"F19.opPattern","COPY",BODY,{"derivedFrom":makeQuery(id+"F17.opPattern","COPY",BODY,{"derivedFrom":makeQuery(id+"F15.opPattern","COPY",BODY,{"derivedFrom":makeQuery(id+"F12.opPattern","COPY",BODY,{"derivedFrom":makeQuery(id+"F6.opPattern","COPY",BODY,{"derivedFrom":makeQuery(id+"F5.opPattern","COPY",BODY,{"derivedFrom":makeQuery(id+"F4.opPattern","COPY",BODY,{"derivedFrom":makeQuery(id+"F2.opPattern","COPY",BODY,{"derivedFrom":makeQuery(id+"F1.opExtrude","SWEPT_BODY",BODY,{"disambiguationData":[OSD([sQuery(id+"F0.wireOp",EDGE,"E0.bottom"),sQuery(id+"F0.wireOp",EDGE,"E0.top"),sQuery(id+"F0.wireOp",EDGE,"E0.left"),sQuery(id+"F0.wireOp",EDGE,"E0.right")])]}),"instanceName":"1"}),"instanceName":"1"}),"instanceName":"1"}),"instanceName":"1"}),"instanceName":"1"}),"instanceName":"1"}),"instanceName":"1"}),"instanceName":"1"}),"instanceName":"1"}),"instanceName":"1"}),"instanceName":"1"});
            var Q3;
            Q3=makeQuery(id+"F42.opPattern","COPY",BODY,{"derivedFrom":makeQuery(id+"F29.opPattern","COPY",BODY,{"derivedFrom":makeQuery(id+"F19.opPattern","COPY",BODY,{"derivedFrom":makeQuery(id+"F17.opPattern","COPY",BODY,{"derivedFrom":makeQuery(id+"F13.opPattern","COPY",BODY,{"derivedFrom":makeQuery(id+"F5.opPattern","COPY",BODY,{"derivedFrom":makeQuery(id+"F4.opPattern","COPY",BODY,{"derivedFrom":makeQuery(id+"F1.opExtrude","SWEPT_BODY",BODY,{"disambiguationData":[OSD([sQuery(id+"F0.wireOp",EDGE,"E0.bottom"),sQuery(id+"F0.wireOp",EDGE,"E0.top"),sQuery(id+"F0.wireOp",EDGE,"E0.left"),sQuery(id+"F0.wireOp",EDGE,"E0.right")])]}),"instanceName":"1"}),"instanceName":"1"}),"instanceName":"1"}),"instanceName":"1"}),"instanceName":"1"}),"instanceName":"1"}),"instanceName":"1"});
            var Q4;
            Q4=makeQuery(id+"F42.opPattern","COPY",EDGE,{"derivedFrom":makeQuery(id+"F29.opPattern","COPY",EDGE,{"derivedFrom":makeQuery(id+"F28.opPattern","COPY",EDGE,{"derivedFrom":makeQuery(id+"F19.opPattern","COPY",EDGE,{"derivedFrom":makeQuery(id+"F17.opPattern","COPY",EDGE,{"derivedFrom":makeQuery(id+"F13.opPattern","COPY",EDGE,{"derivedFrom":makeQuery(id+"F5.opPattern","COPY",EDGE,{"derivedFrom":makeQuery(id+"F4.opPattern","COPY",EDGE,{"derivedFrom":makeQuery(id+"F1.opExtrude","CAP_EDGE",EDGE,{"disambiguationData":[OSD([sQuery(id+"F0.wireOp",EDGE,"E0.bottom")])],"isStart":false}),"instanceName":"1"}),"instanceName":"1"}),"instanceName":"1"}),"instanceName":"1"}),"instanceName":"1"}),"instanceName":"1"}),"instanceName":"1"}),"instanceName":"1"});
            transform(context, id + "F49", {"entities" : qUnion([Q0, Q1, Q2, Q3]), "transformType" : TransformType.TRANSLATION_DISTANCE, "transformDirection" : qUnion([Q4]), "distance" : 40 * mm, "oppositeDirection" : true, "makeCopy" : true});
        }
        {
            var Q0;
            Q0=makeQuery(id+"F40.opPattern","COPY",BODY,{"derivedFrom":makeQuery(id+"F27.opPattern","COPY",BODY,{"derivedFrom":makeQuery(id+"F23.opPattern","COPY",BODY,{"derivedFrom":makeQuery(id+"F21.opPattern","COPY",BODY,{"derivedFrom":makeQuery(id+"F19.opPattern","COPY",BODY,{"derivedFrom":makeQuery(id+"F17.opPattern","COPY",BODY,{"derivedFrom":makeQuery(id+"F5.opPattern","COPY",BODY,{"derivedFrom":makeQuery(id+"F4.opPattern","COPY",BODY,{"derivedFrom":makeQuery(id+"F1.opExtrude","SWEPT_BODY",BODY,{"disambiguationData":[OSD([sQuery(id+"F0.wireOp",EDGE,"E0.bottom"),sQuery(id+"F0.wireOp",EDGE,"E0.top"),sQuery(id+"F0.wireOp",EDGE,"E0.left"),sQuery(id+"F0.wireOp",EDGE,"E0.right")])]}),"instanceName":"1"}),"instanceName":"1"}),"instanceName":"1"}),"instanceName":"1"}),"instanceName":"1"}),"instanceName":"1"}),"instanceName":"1"}),"instanceName":"1"});
            var Q1;
            Q1=makeQuery(id+"F28.opPattern","COPY",BODY,{"derivedFrom":makeQuery(id+"F23.opPattern","COPY",BODY,{"derivedFrom":makeQuery(id+"F19.opPattern","COPY",BODY,{"derivedFrom":makeQuery(id+"F15.opPattern","COPY",BODY,{"derivedFrom":makeQuery(id+"F12.opPattern","COPY",BODY,{"derivedFrom":makeQuery(id+"F6.opPattern","COPY",BODY,{"derivedFrom":makeQuery(id+"F5.opPattern","COPY",BODY,{"derivedFrom":makeQuery(id+"F4.opPattern","COPY",BODY,{"derivedFrom":makeQuery(id+"F2.opPattern","COPY",BODY,{"derivedFrom":makeQuery(id+"F1.opExtrude","SWEPT_BODY",BODY,{"disambiguationData":[OSD([sQuery(id+"F0.wireOp",EDGE,"E0.bottom"),sQuery(id+"F0.wireOp",EDGE,"E0.top"),sQuery(id+"F0.wireOp",EDGE,"E0.left"),sQuery(id+"F0.wireOp",EDGE,"E0.right")])]}),"instanceName":"1"}),"instanceName":"1"}),"instanceName":"1"}),"instanceName":"1"}),"instanceName":"1"}),"instanceName":"1"}),"instanceName":"1"}),"instanceName":"1"}),"instanceName":"1"});
            var Q2;
            Q2=makeQuery(id+"F4.opPattern","COPY",BODY,{"derivedFrom":makeQuery(id+"F1.opExtrude","SWEPT_BODY",BODY,{"disambiguationData":[OSD([sQuery(id+"F0.wireOp",EDGE,"E0.bottom"),sQuery(id+"F0.wireOp",EDGE,"E0.top"),sQuery(id+"F0.wireOp",EDGE,"E0.left"),sQuery(id+"F0.wireOp",EDGE,"E0.right")])]}),"instanceName":"1"});
            var Q3;
            Q3=makeQuery(id+"F37.opPattern","COPY",BODY,{"derivedFrom":makeQuery(id+"F35.opPattern","COPY",BODY,{"derivedFrom":makeQuery(id+"F31.opPattern","COPY",BODY,{"derivedFrom":makeQuery(id+"F5.opPattern","COPY",BODY,{"derivedFrom":makeQuery(id+"F2.opPattern","COPY",BODY,{"derivedFrom":makeQuery(id+"F1.opExtrude","SWEPT_BODY",BODY,{"disambiguationData":[OSD([sQuery(id+"F0.wireOp",EDGE,"E0.bottom"),sQuery(id+"F0.wireOp",EDGE,"E0.top"),sQuery(id+"F0.wireOp",EDGE,"E0.left"),sQuery(id+"F0.wireOp",EDGE,"E0.right")])]}),"instanceName":"1"}),"instanceName":"1"}),"instanceName":"1"}),"instanceName":"1"}),"instanceName":"1"});
            var Q4;
            Q4=makeQuery(id+"F3.opPattern","COPY",BODY,{"derivedFrom":makeQuery(id+"F2.opPattern","COPY",BODY,{"derivedFrom":makeQuery(id+"F1.opExtrude","SWEPT_BODY",BODY,{"disambiguationData":[OSD([sQuery(id+"F0.wireOp",EDGE,"E0.bottom"),sQuery(id+"F0.wireOp",EDGE,"E0.top"),sQuery(id+"F0.wireOp",EDGE,"E0.left"),sQuery(id+"F0.wireOp",EDGE,"E0.right")])]}),"instanceName":"1"}),"instanceName":"1"});
            var Q5;
            Q5=makeQuery(id+"F34.opPattern","COPY",BODY,{"derivedFrom":makeQuery(id+"F31.opPattern","COPY",BODY,{"derivedFrom":makeQuery(id+"F1.opExtrude","SWEPT_BODY",BODY,{"disambiguationData":[OSD([sQuery(id+"F0.wireOp",EDGE,"E0.bottom"),sQuery(id+"F0.wireOp",EDGE,"E0.top"),sQuery(id+"F0.wireOp",EDGE,"E0.left"),sQuery(id+"F0.wireOp",EDGE,"E0.right")])]}),"instanceName":"1"}),"instanceName":"1"});
            var Q6;
            Q6=makeQuery(id+"F39.opPattern","COPY",BODY,{"derivedFrom":makeQuery(id+"F26.opPattern","COPY",BODY,{"derivedFrom":makeQuery(id+"F17.opPattern","COPY",BODY,{"derivedFrom":makeQuery(id+"F13.opPattern","COPY",BODY,{"derivedFrom":makeQuery(id+"F5.opPattern","COPY",BODY,{"derivedFrom":makeQuery(id+"F4.opPattern","COPY",BODY,{"derivedFrom":makeQuery(id+"F1.opExtrude","SWEPT_BODY",BODY,{"disambiguationData":[OSD([sQuery(id+"F0.wireOp",EDGE,"E0.bottom"),sQuery(id+"F0.wireOp",EDGE,"E0.top"),sQuery(id+"F0.wireOp",EDGE,"E0.left"),sQuery(id+"F0.wireOp",EDGE,"E0.right")])]}),"instanceName":"1"}),"instanceName":"1"}),"instanceName":"1"}),"instanceName":"1"}),"instanceName":"1"}),"instanceName":"1"});
            var Q7;
            Q7=makeQuery(id+"F39.opPattern","COPY",BODY,{"derivedFrom":makeQuery(id+"F26.opPattern","COPY",BODY,{"derivedFrom":makeQuery(id+"F19.opPattern","COPY",BODY,{"derivedFrom":makeQuery(id+"F12.opPattern","COPY",BODY,{"derivedFrom":makeQuery(id+"F6.opPattern","COPY",BODY,{"derivedFrom":makeQuery(id+"F5.opPattern","COPY",BODY,{"derivedFrom":makeQuery(id+"F4.opPattern","COPY",BODY,{"derivedFrom":makeQuery(id+"F1.opExtrude","SWEPT_BODY",BODY,{"disambiguationData":[OSD([sQuery(id+"F0.wireOp",EDGE,"E0.bottom"),sQuery(id+"F0.wireOp",EDGE,"E0.top"),sQuery(id+"F0.wireOp",EDGE,"E0.left"),sQuery(id+"F0.wireOp",EDGE,"E0.right")])]}),"instanceName":"1"}),"instanceName":"1"}),"instanceName":"1"}),"instanceName":"1"}),"instanceName":"1"}),"instanceName":"1"}),"instanceName":"1"});
            var Q8;
            Q8=makeQuery(id+"F21.opPattern","COPY",BODY,{"derivedFrom":makeQuery(id+"F19.opPattern","COPY",BODY,{"derivedFrom":makeQuery(id+"F5.opPattern","COPY",BODY,{"derivedFrom":makeQuery(id+"F4.opPattern","COPY",BODY,{"derivedFrom":makeQuery(id+"F1.opExtrude","SWEPT_BODY",BODY,{"disambiguationData":[OSD([sQuery(id+"F0.wireOp",EDGE,"E0.bottom"),sQuery(id+"F0.wireOp",EDGE,"E0.top"),sQuery(id+"F0.wireOp",EDGE,"E0.left"),sQuery(id+"F0.wireOp",EDGE,"E0.right")])]}),"instanceName":"1"}),"instanceName":"1"}),"instanceName":"1"}),"instanceName":"1"});
            var Q9;
            Q9=makeQuery(id+"F24.opPattern","COPY",BODY,{"derivedFrom":makeQuery(id+"F23.opPattern","COPY",BODY,{"derivedFrom":makeQuery(id+"F21.opPattern","COPY",BODY,{"derivedFrom":makeQuery(id+"F19.opPattern","COPY",BODY,{"derivedFrom":makeQuery(id+"F17.opPattern","COPY",BODY,{"derivedFrom":makeQuery(id+"F6.opPattern","COPY",BODY,{"derivedFrom":makeQuery(id+"F5.opPattern","COPY",BODY,{"derivedFrom":makeQuery(id+"F4.opPattern","COPY",BODY,{"derivedFrom":makeQuery(id+"F1.opExtrude","SWEPT_BODY",BODY,{"disambiguationData":[OSD([sQuery(id+"F0.wireOp",EDGE,"E0.bottom"),sQuery(id+"F0.wireOp",EDGE,"E0.top"),sQuery(id+"F0.wireOp",EDGE,"E0.left"),sQuery(id+"F0.wireOp",EDGE,"E0.right")])]}),"instanceName":"1"}),"instanceName":"1"}),"instanceName":"1"}),"instanceName":"1"}),"instanceName":"1"}),"instanceName":"1"}),"instanceName":"1"}),"instanceName":"1"});
            var Q10;
            Q10=makeQuery(id+"F39.opPattern","COPY",BODY,{"derivedFrom":makeQuery(id+"F26.opPattern","COPY",BODY,{"derivedFrom":makeQuery(id+"F19.opPattern","COPY",BODY,{"derivedFrom":makeQuery(id+"F12.opPattern","COPY",BODY,{"derivedFrom":makeQuery(id+"F6.opPattern","COPY",BODY,{"derivedFrom":makeQuery(id+"F5.opPattern","COPY",BODY,{"derivedFrom":makeQuery(id+"F4.opPattern","COPY",BODY,{"derivedFrom":makeQuery(id+"F2.opPattern","COPY",BODY,{"derivedFrom":makeQuery(id+"F1.opExtrude","SWEPT_BODY",BODY,{"disambiguationData":[OSD([sQuery(id+"F0.wireOp",EDGE,"E0.bottom"),sQuery(id+"F0.wireOp",EDGE,"E0.top"),sQuery(id+"F0.wireOp",EDGE,"E0.left"),sQuery(id+"F0.wireOp",EDGE,"E0.right")])]}),"instanceName":"1"}),"instanceName":"1"}),"instanceName":"1"}),"instanceName":"1"}),"instanceName":"1"}),"instanceName":"1"}),"instanceName":"1"}),"instanceName":"1"});
            var Q11;
            Q11=makeQuery(id+"F23.opPattern","COPY",BODY,{"derivedFrom":makeQuery(id+"F19.opPattern","COPY",BODY,{"derivedFrom":makeQuery(id+"F17.opPattern","COPY",BODY,{"derivedFrom":makeQuery(id+"F15.opPattern","COPY",BODY,{"derivedFrom":makeQuery(id+"F12.opPattern","COPY",BODY,{"derivedFrom":makeQuery(id+"F6.opPattern","COPY",BODY,{"derivedFrom":makeQuery(id+"F5.opPattern","COPY",BODY,{"derivedFrom":makeQuery(id+"F4.opPattern","COPY",BODY,{"derivedFrom":makeQuery(id+"F2.opPattern","COPY",BODY,{"derivedFrom":makeQuery(id+"F1.opExtrude","SWEPT_BODY",BODY,{"disambiguationData":[OSD([sQuery(id+"F0.wireOp",EDGE,"E0.bottom"),sQuery(id+"F0.wireOp",EDGE,"E0.top"),sQuery(id+"F0.wireOp",EDGE,"E0.left"),sQuery(id+"F0.wireOp",EDGE,"E0.right")])]}),"instanceName":"1"}),"instanceName":"1"}),"instanceName":"1"}),"instanceName":"1"}),"instanceName":"1"}),"instanceName":"1"}),"instanceName":"1"}),"instanceName":"1"}),"instanceName":"1"});
            var Q12;
            Q12=makeQuery(id+"F38.opPattern","COPY",BODY,{"derivedFrom":makeQuery(id+"F37.opPattern","COPY",BODY,{"derivedFrom":makeQuery(id+"F35.opPattern","COPY",BODY,{"derivedFrom":makeQuery(id+"F31.opPattern","COPY",BODY,{"derivedFrom":makeQuery(id+"F5.opPattern","COPY",BODY,{"derivedFrom":makeQuery(id+"F1.opExtrude","SWEPT_BODY",BODY,{"disambiguationData":[OSD([sQuery(id+"F0.wireOp",EDGE,"E0.bottom"),sQuery(id+"F0.wireOp",EDGE,"E0.top"),sQuery(id+"F0.wireOp",EDGE,"E0.left"),sQuery(id+"F0.wireOp",EDGE,"E0.right")])]}),"instanceName":"1"}),"instanceName":"1"}),"instanceName":"1"}),"instanceName":"1"}),"instanceName":"1"});
            var Q13;
            Q13=makeQuery(id+"F40.opPattern","COPY",BODY,{"derivedFrom":makeQuery(id+"F23.opPattern","COPY",BODY,{"derivedFrom":makeQuery(id+"F21.opPattern","COPY",BODY,{"derivedFrom":makeQuery(id+"F19.opPattern","COPY",BODY,{"derivedFrom":makeQuery(id+"F17.opPattern","COPY",BODY,{"derivedFrom":makeQuery(id+"F12.opPattern","COPY",BODY,{"derivedFrom":makeQuery(id+"F6.opPattern","COPY",BODY,{"derivedFrom":makeQuery(id+"F5.opPattern","COPY",BODY,{"derivedFrom":makeQuery(id+"F4.opPattern","COPY",BODY,{"derivedFrom":makeQuery(id+"F2.opPattern","COPY",BODY,{"derivedFrom":makeQuery(id+"F1.opExtrude","SWEPT_BODY",BODY,{"disambiguationData":[OSD([sQuery(id+"F0.wireOp",EDGE,"E0.bottom"),sQuery(id+"F0.wireOp",EDGE,"E0.top"),sQuery(id+"F0.wireOp",EDGE,"E0.left"),sQuery(id+"F0.wireOp",EDGE,"E0.right")])]}),"instanceName":"1"}),"instanceName":"1"}),"instanceName":"1"}),"instanceName":"1"}),"instanceName":"1"}),"instanceName":"1"}),"instanceName":"1"}),"instanceName":"1"}),"instanceName":"1"}),"instanceName":"1"});
            var Q14;
            Q14=makeQuery(id+"F37.opPattern","COPY",BODY,{"derivedFrom":makeQuery(id+"F35.opPattern","COPY",BODY,{"derivedFrom":makeQuery(id+"F34.opPattern","COPY",BODY,{"derivedFrom":makeQuery(id+"F31.opPattern","COPY",BODY,{"derivedFrom":makeQuery(id+"F4.opPattern","COPY",BODY,{"derivedFrom":makeQuery(id+"F2.opPattern","COPY",BODY,{"derivedFrom":makeQuery(id+"F1.opExtrude","SWEPT_BODY",BODY,{"disambiguationData":[OSD([sQuery(id+"F0.wireOp",EDGE,"E0.bottom"),sQuery(id+"F0.wireOp",EDGE,"E0.top"),sQuery(id+"F0.wireOp",EDGE,"E0.left"),sQuery(id+"F0.wireOp",EDGE,"E0.right")])]}),"instanceName":"1"}),"instanceName":"1"}),"instanceName":"1"}),"instanceName":"1"}),"instanceName":"1"}),"instanceName":"1"});
            var Q15;
            Q15=makeQuery(id+"F38.opPattern","COPY",BODY,{"derivedFrom":makeQuery(id+"F35.opPattern","COPY",BODY,{"derivedFrom":makeQuery(id+"F34.opPattern","COPY",BODY,{"derivedFrom":makeQuery(id+"F31.opPattern","COPY",BODY,{"derivedFrom":makeQuery(id+"F5.opPattern","COPY",BODY,{"derivedFrom":makeQuery(id+"F1.opExtrude","SWEPT_BODY",BODY,{"disambiguationData":[OSD([sQuery(id+"F0.wireOp",EDGE,"E0.bottom"),sQuery(id+"F0.wireOp",EDGE,"E0.top"),sQuery(id+"F0.wireOp",EDGE,"E0.left"),sQuery(id+"F0.wireOp",EDGE,"E0.right")])]}),"instanceName":"1"}),"instanceName":"1"}),"instanceName":"1"}),"instanceName":"1"}),"instanceName":"1"});
            var Q16;
            Q16=makeQuery(id+"F26.opPattern","COPY",BODY,{"derivedFrom":makeQuery(id+"F23.opPattern","COPY",BODY,{"derivedFrom":makeQuery(id+"F19.opPattern","COPY",BODY,{"derivedFrom":makeQuery(id+"F17.opPattern","COPY",BODY,{"derivedFrom":makeQuery(id+"F13.opPattern","COPY",BODY,{"derivedFrom":makeQuery(id+"F5.opPattern","COPY",BODY,{"derivedFrom":makeQuery(id+"F4.opPattern","COPY",BODY,{"derivedFrom":makeQuery(id+"F1.opExtrude","SWEPT_BODY",BODY,{"disambiguationData":[OSD([sQuery(id+"F0.wireOp",EDGE,"E0.bottom"),sQuery(id+"F0.wireOp",EDGE,"E0.top"),sQuery(id+"F0.wireOp",EDGE,"E0.left"),sQuery(id+"F0.wireOp",EDGE,"E0.right")])]}),"instanceName":"1"}),"instanceName":"1"}),"instanceName":"1"}),"instanceName":"1"}),"instanceName":"1"}),"instanceName":"1"}),"instanceName":"1"});
            var Q17;
            Q17=makeQuery(id+"F26.opPattern","COPY",BODY,{"derivedFrom":makeQuery(id+"F19.opPattern","COPY",BODY,{"derivedFrom":makeQuery(id+"F17.opPattern","COPY",BODY,{"derivedFrom":makeQuery(id+"F12.opPattern","COPY",BODY,{"derivedFrom":makeQuery(id+"F6.opPattern","COPY",BODY,{"derivedFrom":makeQuery(id+"F5.opPattern","COPY",BODY,{"derivedFrom":makeQuery(id+"F4.opPattern","COPY",BODY,{"derivedFrom":makeQuery(id+"F1.opExtrude","SWEPT_BODY",BODY,{"disambiguationData":[OSD([sQuery(id+"F0.wireOp",EDGE,"E0.bottom"),sQuery(id+"F0.wireOp",EDGE,"E0.top"),sQuery(id+"F0.wireOp",EDGE,"E0.left"),sQuery(id+"F0.wireOp",EDGE,"E0.right")])]}),"instanceName":"1"}),"instanceName":"1"}),"instanceName":"1"}),"instanceName":"1"}),"instanceName":"1"}),"instanceName":"1"}),"instanceName":"1"});
            var Q18;
            Q18=makeQuery(id+"F28.opPattern","COPY",BODY,{"derivedFrom":makeQuery(id+"F23.opPattern","COPY",BODY,{"derivedFrom":makeQuery(id+"F19.opPattern","COPY",BODY,{"derivedFrom":makeQuery(id+"F17.opPattern","COPY",BODY,{"derivedFrom":makeQuery(id+"F15.opPattern","COPY",BODY,{"derivedFrom":makeQuery(id+"F12.opPattern","COPY",BODY,{"derivedFrom":makeQuery(id+"F6.opPattern","COPY",BODY,{"derivedFrom":makeQuery(id+"F5.opPattern","COPY",BODY,{"derivedFrom":makeQuery(id+"F4.opPattern","COPY",BODY,{"derivedFrom":makeQuery(id+"F2.opPattern","COPY",BODY,{"derivedFrom":makeQuery(id+"F1.opExtrude","SWEPT_BODY",BODY,{"disambiguationData":[OSD([sQuery(id+"F0.wireOp",EDGE,"E0.bottom"),sQuery(id+"F0.wireOp",EDGE,"E0.top"),sQuery(id+"F0.wireOp",EDGE,"E0.left"),sQuery(id+"F0.wireOp",EDGE,"E0.right")])]}),"instanceName":"1"}),"instanceName":"1"}),"instanceName":"1"}),"instanceName":"1"}),"instanceName":"1"}),"instanceName":"1"}),"instanceName":"1"}),"instanceName":"1"}),"instanceName":"1"}),"instanceName":"1"});
            var Q19;
            Q19=makeQuery(id+"F19.opPattern","COPY",BODY,{"derivedFrom":makeQuery(id+"F6.opPattern","COPY",BODY,{"derivedFrom":makeQuery(id+"F5.opPattern","COPY",BODY,{"derivedFrom":makeQuery(id+"F4.opPattern","COPY",BODY,{"derivedFrom":makeQuery(id+"F1.opExtrude","SWEPT_BODY",BODY,{"disambiguationData":[OSD([sQuery(id+"F0.wireOp",EDGE,"E0.bottom"),sQuery(id+"F0.wireOp",EDGE,"E0.top"),sQuery(id+"F0.wireOp",EDGE,"E0.left"),sQuery(id+"F0.wireOp",EDGE,"E0.right")])]}),"instanceName":"1"}),"instanceName":"1"}),"instanceName":"1"}),"instanceName":"1"});
            var Q20;
            Q20=makeQuery(id+"F39.opPattern","COPY",BODY,{"derivedFrom":makeQuery(id+"F29.opPattern","COPY",BODY,{"derivedFrom":makeQuery(id+"F26.opPattern","COPY",BODY,{"derivedFrom":makeQuery(id+"F17.opPattern","COPY",BODY,{"derivedFrom":makeQuery(id+"F15.opPattern","COPY",BODY,{"derivedFrom":makeQuery(id+"F12.opPattern","COPY",BODY,{"derivedFrom":makeQuery(id+"F6.opPattern","COPY",BODY,{"derivedFrom":makeQuery(id+"F5.opPattern","COPY",BODY,{"derivedFrom":makeQuery(id+"F4.opPattern","COPY",BODY,{"derivedFrom":makeQuery(id+"F2.opPattern","COPY",BODY,{"derivedFrom":makeQuery(id+"F1.opExtrude","SWEPT_BODY",BODY,{"disambiguationData":[OSD([sQuery(id+"F0.wireOp",EDGE,"E0.bottom"),sQuery(id+"F0.wireOp",EDGE,"E0.top"),sQuery(id+"F0.wireOp",EDGE,"E0.left"),sQuery(id+"F0.wireOp",EDGE,"E0.right")])]}),"instanceName":"1"}),"instanceName":"1"}),"instanceName":"1"}),"instanceName":"1"}),"instanceName":"1"}),"instanceName":"1"}),"instanceName":"1"}),"instanceName":"1"}),"instanceName":"1"}),"instanceName":"1"});
            var Q21;
            Q21=makeQuery(id+"F39.opPattern","COPY",BODY,{"derivedFrom":makeQuery(id+"F26.opPattern","COPY",BODY,{"derivedFrom":makeQuery(id+"F17.opPattern","COPY",BODY,{"derivedFrom":makeQuery(id+"F15.opPattern","COPY",BODY,{"derivedFrom":makeQuery(id+"F12.opPattern","COPY",BODY,{"derivedFrom":makeQuery(id+"F6.opPattern","COPY",BODY,{"derivedFrom":makeQuery(id+"F5.opPattern","COPY",BODY,{"derivedFrom":makeQuery(id+"F4.opPattern","COPY",BODY,{"derivedFrom":makeQuery(id+"F2.opPattern","COPY",BODY,{"derivedFrom":makeQuery(id+"F1.opExtrude","SWEPT_BODY",BODY,{"disambiguationData":[OSD([sQuery(id+"F0.wireOp",EDGE,"E0.bottom"),sQuery(id+"F0.wireOp",EDGE,"E0.top"),sQuery(id+"F0.wireOp",EDGE,"E0.left"),sQuery(id+"F0.wireOp",EDGE,"E0.right")])]}),"instanceName":"1"}),"instanceName":"1"}),"instanceName":"1"}),"instanceName":"1"}),"instanceName":"1"}),"instanceName":"1"}),"instanceName":"1"}),"instanceName":"1"}),"instanceName":"1"});
            var Q22;
            Q22=makeQuery(id+"F32.opPattern","COPY",BODY,{"derivedFrom":makeQuery(id+"F31.opPattern","COPY",BODY,{"derivedFrom":makeQuery(id+"F1.opExtrude","SWEPT_BODY",BODY,{"disambiguationData":[OSD([sQuery(id+"F0.wireOp",EDGE,"E0.bottom"),sQuery(id+"F0.wireOp",EDGE,"E0.top"),sQuery(id+"F0.wireOp",EDGE,"E0.left"),sQuery(id+"F0.wireOp",EDGE,"E0.right")])]}),"instanceName":"1"}),"instanceName":"1"});
            var Q23;
            Q23=makeQuery(id+"F23.opPattern","COPY",BODY,{"derivedFrom":makeQuery(id+"F21.opPattern","COPY",BODY,{"derivedFrom":makeQuery(id+"F19.opPattern","COPY",BODY,{"derivedFrom":makeQuery(id+"F17.opPattern","COPY",BODY,{"derivedFrom":makeQuery(id+"F5.opPattern","COPY",BODY,{"derivedFrom":makeQuery(id+"F4.opPattern","COPY",BODY,{"derivedFrom":makeQuery(id+"F2.opPattern","COPY",BODY,{"derivedFrom":makeQuery(id+"F1.opExtrude","SWEPT_BODY",BODY,{"disambiguationData":[OSD([sQuery(id+"F0.wireOp",EDGE,"E0.bottom"),sQuery(id+"F0.wireOp",EDGE,"E0.top"),sQuery(id+"F0.wireOp",EDGE,"E0.left"),sQuery(id+"F0.wireOp",EDGE,"E0.right")])]}),"instanceName":"1"}),"instanceName":"1"}),"instanceName":"1"}),"instanceName":"1"}),"instanceName":"1"}),"instanceName":"1"}),"instanceName":"1"});
            var Q24;
            Q24=makeQuery(id+"F42.opPattern","COPY",BODY,{"derivedFrom":makeQuery(id+"F29.opPattern","COPY",BODY,{"derivedFrom":makeQuery(id+"F28.opPattern","COPY",BODY,{"derivedFrom":makeQuery(id+"F23.opPattern","COPY",BODY,{"derivedFrom":makeQuery(id+"F19.opPattern","COPY",BODY,{"derivedFrom":makeQuery(id+"F15.opPattern","COPY",BODY,{"derivedFrom":makeQuery(id+"F12.opPattern","COPY",BODY,{"derivedFrom":makeQuery(id+"F6.opPattern","COPY",BODY,{"derivedFrom":makeQuery(id+"F5.opPattern","COPY",BODY,{"derivedFrom":makeQuery(id+"F4.opPattern","COPY",BODY,{"derivedFrom":makeQuery(id+"F2.opPattern","COPY",BODY,{"derivedFrom":makeQuery(id+"F1.opExtrude","SWEPT_BODY",BODY,{"disambiguationData":[OSD([sQuery(id+"F0.wireOp",EDGE,"E0.bottom"),sQuery(id+"F0.wireOp",EDGE,"E0.top"),sQuery(id+"F0.wireOp",EDGE,"E0.left"),sQuery(id+"F0.wireOp",EDGE,"E0.right")])]}),"instanceName":"1"}),"instanceName":"1"}),"instanceName":"1"}),"instanceName":"1"}),"instanceName":"1"}),"instanceName":"1"}),"instanceName":"1"}),"instanceName":"1"}),"instanceName":"1"}),"instanceName":"1"}),"instanceName":"1"});
            var Q25;
            Q25=makeQuery(id+"F40.opPattern","COPY",BODY,{"derivedFrom":makeQuery(id+"F24.opPattern","COPY",BODY,{"derivedFrom":makeQuery(id+"F23.opPattern","COPY",BODY,{"derivedFrom":makeQuery(id+"F21.opPattern","COPY",BODY,{"derivedFrom":makeQuery(id+"F19.opPattern","COPY",BODY,{"derivedFrom":makeQuery(id+"F17.opPattern","COPY",BODY,{"derivedFrom":makeQuery(id+"F12.opPattern","COPY",BODY,{"derivedFrom":makeQuery(id+"F6.opPattern","COPY",BODY,{"derivedFrom":makeQuery(id+"F5.opPattern","COPY",BODY,{"derivedFrom":makeQuery(id+"F4.opPattern","COPY",BODY,{"derivedFrom":makeQuery(id+"F2.opPattern","COPY",BODY,{"derivedFrom":makeQuery(id+"F1.opExtrude","SWEPT_BODY",BODY,{"disambiguationData":[OSD([sQuery(id+"F0.wireOp",EDGE,"E0.bottom"),sQuery(id+"F0.wireOp",EDGE,"E0.top"),sQuery(id+"F0.wireOp",EDGE,"E0.left"),sQuery(id+"F0.wireOp",EDGE,"E0.right")])]}),"instanceName":"1"}),"instanceName":"1"}),"instanceName":"1"}),"instanceName":"1"}),"instanceName":"1"}),"instanceName":"1"}),"instanceName":"1"}),"instanceName":"1"}),"instanceName":"1"}),"instanceName":"1"}),"instanceName":"1"});
            var Q26;
            Q26=makeQuery(id+"F45.opPattern","COPY",BODY,{"derivedFrom":makeQuery(id+"F40.opPattern","COPY",BODY,{"derivedFrom":makeQuery(id+"F28.opPattern","COPY",BODY,{"derivedFrom":makeQuery(id+"F23.opPattern","COPY",BODY,{"derivedFrom":makeQuery(id+"F19.opPattern","COPY",BODY,{"derivedFrom":makeQuery(id+"F17.opPattern","COPY",BODY,{"derivedFrom":makeQuery(id+"F13.opPattern","COPY",BODY,{"derivedFrom":makeQuery(id+"F5.opPattern","COPY",BODY,{"derivedFrom":makeQuery(id+"F4.opPattern","COPY",BODY,{"derivedFrom":makeQuery(id+"F1.opExtrude","SWEPT_BODY",BODY,{"disambiguationData":[OSD([sQuery(id+"F0.wireOp",EDGE,"E0.bottom"),sQuery(id+"F0.wireOp",EDGE,"E0.top"),sQuery(id+"F0.wireOp",EDGE,"E0.left"),sQuery(id+"F0.wireOp",EDGE,"E0.right")])]}),"instanceName":"1"}),"instanceName":"1"}),"instanceName":"1"}),"instanceName":"1"}),"instanceName":"1"}),"instanceName":"1"}),"instanceName":"1"}),"instanceName":"1"}),"instanceName":"1"});
            var Q27;
            Q27=makeQuery(id+"F40.opPattern","COPY",BODY,{"derivedFrom":makeQuery(id+"F29.opPattern","COPY",BODY,{"derivedFrom":makeQuery(id+"F19.opPattern","COPY",BODY,{"derivedFrom":makeQuery(id+"F17.opPattern","COPY",BODY,{"derivedFrom":makeQuery(id+"F13.opPattern","COPY",BODY,{"derivedFrom":makeQuery(id+"F5.opPattern","COPY",BODY,{"derivedFrom":makeQuery(id+"F4.opPattern","COPY",BODY,{"derivedFrom":makeQuery(id+"F1.opExtrude","SWEPT_BODY",BODY,{"disambiguationData":[OSD([sQuery(id+"F0.wireOp",EDGE,"E0.bottom"),sQuery(id+"F0.wireOp",EDGE,"E0.top"),sQuery(id+"F0.wireOp",EDGE,"E0.left"),sQuery(id+"F0.wireOp",EDGE,"E0.right")])]}),"instanceName":"1"}),"instanceName":"1"}),"instanceName":"1"}),"instanceName":"1"}),"instanceName":"1"}),"instanceName":"1"}),"instanceName":"1"});
            var Q28;
            Q28=makeQuery(id+"F16.opPattern","COPY",BODY,{"derivedFrom":makeQuery(id+"F8.opPattern","COPY",BODY,{"derivedFrom":makeQuery(id+"F5.opPattern","COPY",BODY,{"derivedFrom":makeQuery(id+"F4.opPattern","COPY",BODY,{"derivedFrom":makeQuery(id+"F1.opExtrude","SWEPT_BODY",BODY,{"disambiguationData":[OSD([sQuery(id+"F0.wireOp",EDGE,"E0.bottom"),sQuery(id+"F0.wireOp",EDGE,"E0.top"),sQuery(id+"F0.wireOp",EDGE,"E0.left"),sQuery(id+"F0.wireOp",EDGE,"E0.right")])]}),"instanceName":"1"}),"instanceName":"1"}),"instanceName":"1"}),"instanceName":"1"});
            var Q29;
            Q29=makeQuery(id+"F44.opPattern","COPY",BODY,{"derivedFrom":makeQuery(id+"F42.opPattern","COPY",BODY,{"derivedFrom":makeQuery(id+"F29.opPattern","COPY",BODY,{"derivedFrom":makeQuery(id+"F28.opPattern","COPY",BODY,{"derivedFrom":makeQuery(id+"F23.opPattern","COPY",BODY,{"derivedFrom":makeQuery(id+"F19.opPattern","COPY",BODY,{"derivedFrom":makeQuery(id+"F17.opPattern","COPY",BODY,{"derivedFrom":makeQuery(id+"F13.opPattern","COPY",BODY,{"derivedFrom":makeQuery(id+"F5.opPattern","COPY",BODY,{"derivedFrom":makeQuery(id+"F4.opPattern","COPY",BODY,{"derivedFrom":makeQuery(id+"F1.opExtrude","SWEPT_BODY",BODY,{"disambiguationData":[OSD([sQuery(id+"F0.wireOp",EDGE,"E0.bottom"),sQuery(id+"F0.wireOp",EDGE,"E0.top"),sQuery(id+"F0.wireOp",EDGE,"E0.left"),sQuery(id+"F0.wireOp",EDGE,"E0.right")])]}),"instanceName":"1"}),"instanceName":"1"}),"instanceName":"1"}),"instanceName":"1"}),"instanceName":"1"}),"instanceName":"1"}),"instanceName":"1"}),"instanceName":"1"}),"instanceName":"1"}),"instanceName":"1"});
            var Q30;
            Q30=makeQuery(id+"F38.opPattern","COPY",BODY,{"derivedFrom":makeQuery(id+"F37.opPattern","COPY",BODY,{"derivedFrom":makeQuery(id+"F35.opPattern","COPY",BODY,{"derivedFrom":makeQuery(id+"F31.opPattern","COPY",BODY,{"derivedFrom":makeQuery(id+"F5.opPattern","COPY",BODY,{"derivedFrom":makeQuery(id+"F2.opPattern","COPY",BODY,{"derivedFrom":makeQuery(id+"F1.opExtrude","SWEPT_BODY",BODY,{"disambiguationData":[OSD([sQuery(id+"F0.wireOp",EDGE,"E0.bottom"),sQuery(id+"F0.wireOp",EDGE,"E0.top"),sQuery(id+"F0.wireOp",EDGE,"E0.left"),sQuery(id+"F0.wireOp",EDGE,"E0.right")])]}),"instanceName":"1"}),"instanceName":"1"}),"instanceName":"1"}),"instanceName":"1"}),"instanceName":"1"}),"instanceName":"1"});
            var Q31;
            Q31=makeQuery(id+"F24.opPattern","COPY",BODY,{"derivedFrom":makeQuery(id+"F19.opPattern","COPY",BODY,{"derivedFrom":makeQuery(id+"F17.opPattern","COPY",BODY,{"derivedFrom":makeQuery(id+"F5.opPattern","COPY",BODY,{"derivedFrom":makeQuery(id+"F4.opPattern","COPY",BODY,{"derivedFrom":makeQuery(id+"F2.opPattern","COPY",BODY,{"derivedFrom":makeQuery(id+"F1.opExtrude","SWEPT_BODY",BODY,{"disambiguationData":[OSD([sQuery(id+"F0.wireOp",EDGE,"E0.bottom"),sQuery(id+"F0.wireOp",EDGE,"E0.top"),sQuery(id+"F0.wireOp",EDGE,"E0.left"),sQuery(id+"F0.wireOp",EDGE,"E0.right")])]}),"instanceName":"1"}),"instanceName":"1"}),"instanceName":"1"}),"instanceName":"1"}),"instanceName":"1"}),"instanceName":"1"});
            var Q32;
            Q32=makeQuery(id+"F40.opPattern","COPY",BODY,{"derivedFrom":makeQuery(id+"F29.opPattern","COPY",BODY,{"derivedFrom":makeQuery(id+"F23.opPattern","COPY",BODY,{"derivedFrom":makeQuery(id+"F19.opPattern","COPY",BODY,{"derivedFrom":makeQuery(id+"F15.opPattern","COPY",BODY,{"derivedFrom":makeQuery(id+"F12.opPattern","COPY",BODY,{"derivedFrom":makeQuery(id+"F6.opPattern","COPY",BODY,{"derivedFrom":makeQuery(id+"F5.opPattern","COPY",BODY,{"derivedFrom":makeQuery(id+"F4.opPattern","COPY",BODY,{"derivedFrom":makeQuery(id+"F2.opPattern","COPY",BODY,{"derivedFrom":makeQuery(id+"F1.opExtrude","SWEPT_BODY",BODY,{"disambiguationData":[OSD([sQuery(id+"F0.wireOp",EDGE,"E0.bottom"),sQuery(id+"F0.wireOp",EDGE,"E0.top"),sQuery(id+"F0.wireOp",EDGE,"E0.left"),sQuery(id+"F0.wireOp",EDGE,"E0.right")])]}),"instanceName":"1"}),"instanceName":"1"}),"instanceName":"1"}),"instanceName":"1"}),"instanceName":"1"}),"instanceName":"1"}),"instanceName":"1"}),"instanceName":"1"}),"instanceName":"1"}),"instanceName":"1"});
            var Q33;
            Q33=makeQuery(id+"F40.opPattern","COPY",BODY,{"derivedFrom":makeQuery(id+"F26.opPattern","COPY",BODY,{"derivedFrom":makeQuery(id+"F17.opPattern","COPY",BODY,{"derivedFrom":makeQuery(id+"F5.opPattern","COPY",BODY,{"derivedFrom":makeQuery(id+"F4.opPattern","COPY",BODY,{"derivedFrom":makeQuery(id+"F2.opPattern","COPY",BODY,{"derivedFrom":makeQuery(id+"F1.opExtrude","SWEPT_BODY",BODY,{"disambiguationData":[OSD([sQuery(id+"F0.wireOp",EDGE,"E0.bottom"),sQuery(id+"F0.wireOp",EDGE,"E0.top"),sQuery(id+"F0.wireOp",EDGE,"E0.left"),sQuery(id+"F0.wireOp",EDGE,"E0.right")])]}),"instanceName":"1"}),"instanceName":"1"}),"instanceName":"1"}),"instanceName":"1"}),"instanceName":"1"}),"instanceName":"1"});
            var Q34;
            Q34=makeQuery(id+"F35.opPattern","COPY",BODY,{"derivedFrom":makeQuery(id+"F31.opPattern","COPY",BODY,{"derivedFrom":makeQuery(id+"F4.opPattern","COPY",BODY,{"derivedFrom":makeQuery(id+"F2.opPattern","COPY",BODY,{"derivedFrom":makeQuery(id+"F1.opExtrude","SWEPT_BODY",BODY,{"disambiguationData":[OSD([sQuery(id+"F0.wireOp",EDGE,"E0.bottom"),sQuery(id+"F0.wireOp",EDGE,"E0.top"),sQuery(id+"F0.wireOp",EDGE,"E0.left"),sQuery(id+"F0.wireOp",EDGE,"E0.right")])]}),"instanceName":"1"}),"instanceName":"1"}),"instanceName":"1"}),"instanceName":"1"});
            var Q35;
            Q35=makeQuery(id+"F17.opPattern","COPY",BODY,{"derivedFrom":makeQuery(id+"F8.opPattern","COPY",BODY,{"derivedFrom":makeQuery(id+"F5.opPattern","COPY",BODY,{"derivedFrom":makeQuery(id+"F4.opPattern","COPY",BODY,{"derivedFrom":makeQuery(id+"F1.opExtrude","SWEPT_BODY",BODY,{"disambiguationData":[OSD([sQuery(id+"F0.wireOp",EDGE,"E0.bottom"),sQuery(id+"F0.wireOp",EDGE,"E0.top"),sQuery(id+"F0.wireOp",EDGE,"E0.left"),sQuery(id+"F0.wireOp",EDGE,"E0.right")])]}),"instanceName":"1"}),"instanceName":"1"}),"instanceName":"1"}),"instanceName":"1"});
            var Q36;
            Q36=makeQuery(id+"F6.opPattern","COPY",BODY,{"derivedFrom":makeQuery(id+"F5.opPattern","COPY",BODY,{"derivedFrom":makeQuery(id+"F1.opExtrude","SWEPT_BODY",BODY,{"disambiguationData":[OSD([sQuery(id+"F0.wireOp",EDGE,"E0.bottom"),sQuery(id+"F0.wireOp",EDGE,"E0.top"),sQuery(id+"F0.wireOp",EDGE,"E0.left"),sQuery(id+"F0.wireOp",EDGE,"E0.right")])]}),"instanceName":"1"}),"instanceName":"1"});
            var Q37;
            Q37=makeQuery(id+"F34.opPattern","COPY",BODY,{"derivedFrom":makeQuery(id+"F31.opPattern","COPY",BODY,{"derivedFrom":makeQuery(id+"F4.opPattern","COPY",BODY,{"derivedFrom":makeQuery(id+"F2.opPattern","COPY",BODY,{"derivedFrom":makeQuery(id+"F1.opExtrude","SWEPT_BODY",BODY,{"disambiguationData":[OSD([sQuery(id+"F0.wireOp",EDGE,"E0.bottom"),sQuery(id+"F0.wireOp",EDGE,"E0.top"),sQuery(id+"F0.wireOp",EDGE,"E0.left"),sQuery(id+"F0.wireOp",EDGE,"E0.right")])]}),"instanceName":"1"}),"instanceName":"1"}),"instanceName":"1"}),"instanceName":"1"});
            var Q38;
            Q38=makeQuery(id+"F40.opPattern","COPY",BODY,{"derivedFrom":makeQuery(id+"F26.opPattern","COPY",BODY,{"derivedFrom":makeQuery(id+"F19.opPattern","COPY",BODY,{"derivedFrom":makeQuery(id+"F6.opPattern","COPY",BODY,{"derivedFrom":makeQuery(id+"F5.opPattern","COPY",BODY,{"derivedFrom":makeQuery(id+"F4.opPattern","COPY",BODY,{"derivedFrom":makeQuery(id+"F2.opPattern","COPY",BODY,{"derivedFrom":makeQuery(id+"F1.opExtrude","SWEPT_BODY",BODY,{"disambiguationData":[OSD([sQuery(id+"F0.wireOp",EDGE,"E0.bottom"),sQuery(id+"F0.wireOp",EDGE,"E0.top"),sQuery(id+"F0.wireOp",EDGE,"E0.left"),sQuery(id+"F0.wireOp",EDGE,"E0.right")])]}),"instanceName":"1"}),"instanceName":"1"}),"instanceName":"1"}),"instanceName":"1"}),"instanceName":"1"}),"instanceName":"1"}),"instanceName":"1"});
            var Q39;
            Q39=makeQuery(id+"F23.opPattern","COPY",BODY,{"derivedFrom":makeQuery(id+"F19.opPattern","COPY",BODY,{"derivedFrom":makeQuery(id+"F15.opPattern","COPY",BODY,{"derivedFrom":makeQuery(id+"F12.opPattern","COPY",BODY,{"derivedFrom":makeQuery(id+"F6.opPattern","COPY",BODY,{"derivedFrom":makeQuery(id+"F5.opPattern","COPY",BODY,{"derivedFrom":makeQuery(id+"F4.opPattern","COPY",BODY,{"derivedFrom":makeQuery(id+"F2.opPattern","COPY",BODY,{"derivedFrom":makeQuery(id+"F1.opExtrude","SWEPT_BODY",BODY,{"disambiguationData":[OSD([sQuery(id+"F0.wireOp",EDGE,"E0.bottom"),sQuery(id+"F0.wireOp",EDGE,"E0.top"),sQuery(id+"F0.wireOp",EDGE,"E0.left"),sQuery(id+"F0.wireOp",EDGE,"E0.right")])]}),"instanceName":"1"}),"instanceName":"1"}),"instanceName":"1"}),"instanceName":"1"}),"instanceName":"1"}),"instanceName":"1"}),"instanceName":"1"}),"instanceName":"1"});
            var Q40;
            Q40=makeQuery(id+"F19.opPattern","COPY",BODY,{"derivedFrom":makeQuery(id+"F17.opPattern","COPY",BODY,{"derivedFrom":makeQuery(id+"F6.opPattern","COPY",BODY,{"derivedFrom":makeQuery(id+"F5.opPattern","COPY",BODY,{"derivedFrom":makeQuery(id+"F4.opPattern","COPY",BODY,{"derivedFrom":makeQuery(id+"F1.opExtrude","SWEPT_BODY",BODY,{"disambiguationData":[OSD([sQuery(id+"F0.wireOp",EDGE,"E0.bottom"),sQuery(id+"F0.wireOp",EDGE,"E0.top"),sQuery(id+"F0.wireOp",EDGE,"E0.left"),sQuery(id+"F0.wireOp",EDGE,"E0.right")])]}),"instanceName":"1"}),"instanceName":"1"}),"instanceName":"1"}),"instanceName":"1"}),"instanceName":"1"});
            var Q41;
            Q41=makeQuery(id+"F6.opPattern","COPY",BODY,{"derivedFrom":makeQuery(id+"F5.opPattern","COPY",BODY,{"derivedFrom":makeQuery(id+"F4.opPattern","COPY",BODY,{"derivedFrom":makeQuery(id+"F1.opExtrude","SWEPT_BODY",BODY,{"disambiguationData":[OSD([sQuery(id+"F0.wireOp",EDGE,"E0.bottom"),sQuery(id+"F0.wireOp",EDGE,"E0.top"),sQuery(id+"F0.wireOp",EDGE,"E0.left"),sQuery(id+"F0.wireOp",EDGE,"E0.right")])]}),"instanceName":"1"}),"instanceName":"1"}),"instanceName":"1"});
            var Q42;
            Q42=makeQuery(id+"F40.opPattern","COPY",BODY,{"derivedFrom":makeQuery(id+"F19.opPattern","COPY",BODY,{"derivedFrom":makeQuery(id+"F17.opPattern","COPY",BODY,{"derivedFrom":makeQuery(id+"F5.opPattern","COPY",BODY,{"derivedFrom":makeQuery(id+"F4.opPattern","COPY",BODY,{"derivedFrom":makeQuery(id+"F1.opExtrude","SWEPT_BODY",BODY,{"disambiguationData":[OSD([sQuery(id+"F0.wireOp",EDGE,"E0.bottom"),sQuery(id+"F0.wireOp",EDGE,"E0.top"),sQuery(id+"F0.wireOp",EDGE,"E0.left"),sQuery(id+"F0.wireOp",EDGE,"E0.right")])]}),"instanceName":"1"}),"instanceName":"1"}),"instanceName":"1"}),"instanceName":"1"}),"instanceName":"1"});
            var Q43;
            Q43=makeQuery(id+"F29.opPattern","COPY",BODY,{"derivedFrom":makeQuery(id+"F23.opPattern","COPY",BODY,{"derivedFrom":makeQuery(id+"F19.opPattern","COPY",BODY,{"derivedFrom":makeQuery(id+"F17.opPattern","COPY",BODY,{"derivedFrom":makeQuery(id+"F15.opPattern","COPY",BODY,{"derivedFrom":makeQuery(id+"F12.opPattern","COPY",BODY,{"derivedFrom":makeQuery(id+"F6.opPattern","COPY",BODY,{"derivedFrom":makeQuery(id+"F5.opPattern","COPY",BODY,{"derivedFrom":makeQuery(id+"F4.opPattern","COPY",BODY,{"derivedFrom":makeQuery(id+"F2.opPattern","COPY",BODY,{"derivedFrom":makeQuery(id+"F1.opExtrude","SWEPT_BODY",BODY,{"disambiguationData":[OSD([sQuery(id+"F0.wireOp",EDGE,"E0.bottom"),sQuery(id+"F0.wireOp",EDGE,"E0.top"),sQuery(id+"F0.wireOp",EDGE,"E0.left"),sQuery(id+"F0.wireOp",EDGE,"E0.right")])]}),"instanceName":"1"}),"instanceName":"1"}),"instanceName":"1"}),"instanceName":"1"}),"instanceName":"1"}),"instanceName":"1"}),"instanceName":"1"}),"instanceName":"1"}),"instanceName":"1"}),"instanceName":"1"});
            var Q44;
            Q44=makeQuery(id+"F28.opPattern","COPY",BODY,{"derivedFrom":makeQuery(id+"F26.opPattern","COPY",BODY,{"derivedFrom":makeQuery(id+"F17.opPattern","COPY",BODY,{"derivedFrom":makeQuery(id+"F13.opPattern","COPY",BODY,{"derivedFrom":makeQuery(id+"F5.opPattern","COPY",BODY,{"derivedFrom":makeQuery(id+"F4.opPattern","COPY",BODY,{"derivedFrom":makeQuery(id+"F1.opExtrude","SWEPT_BODY",BODY,{"disambiguationData":[OSD([sQuery(id+"F0.wireOp",EDGE,"E0.bottom"),sQuery(id+"F0.wireOp",EDGE,"E0.top"),sQuery(id+"F0.wireOp",EDGE,"E0.left"),sQuery(id+"F0.wireOp",EDGE,"E0.right")])]}),"instanceName":"1"}),"instanceName":"1"}),"instanceName":"1"}),"instanceName":"1"}),"instanceName":"1"}),"instanceName":"1"});
            var Q45;
            Q45=makeQuery(id+"F26.opPattern","COPY",BODY,{"derivedFrom":makeQuery(id+"F18.opPattern","COPY",BODY,{"derivedFrom":makeQuery(id+"F17.opPattern","COPY",BODY,{"derivedFrom":makeQuery(id+"F8.opPattern","COPY",BODY,{"derivedFrom":makeQuery(id+"F5.opPattern","COPY",BODY,{"derivedFrom":makeQuery(id+"F4.opPattern","COPY",BODY,{"derivedFrom":makeQuery(id+"F2.opPattern","COPY",BODY,{"derivedFrom":makeQuery(id+"F1.opExtrude","SWEPT_BODY",BODY,{"disambiguationData":[OSD([sQuery(id+"F0.wireOp",EDGE,"E0.bottom"),sQuery(id+"F0.wireOp",EDGE,"E0.top"),sQuery(id+"F0.wireOp",EDGE,"E0.left"),sQuery(id+"F0.wireOp",EDGE,"E0.right")])]}),"instanceName":"1"}),"instanceName":"1"}),"instanceName":"1"}),"instanceName":"1"}),"instanceName":"1"}),"instanceName":"1"}),"instanceName":"1"});
            var Q46;
            Q46=makeQuery(id+"F37.opPattern","COPY",BODY,{"derivedFrom":makeQuery(id+"F35.opPattern","COPY",BODY,{"derivedFrom":makeQuery(id+"F31.opPattern","COPY",BODY,{"derivedFrom":makeQuery(id+"F5.opPattern","COPY",BODY,{"derivedFrom":makeQuery(id+"F1.opExtrude","SWEPT_BODY",BODY,{"disambiguationData":[OSD([sQuery(id+"F0.wireOp",EDGE,"E0.bottom"),sQuery(id+"F0.wireOp",EDGE,"E0.top"),sQuery(id+"F0.wireOp",EDGE,"E0.left"),sQuery(id+"F0.wireOp",EDGE,"E0.right")])]}),"instanceName":"1"}),"instanceName":"1"}),"instanceName":"1"}),"instanceName":"1"});
            var Q47;
            Q47=makeQuery(id+"F40.opPattern","COPY",BODY,{"derivedFrom":makeQuery(id+"F23.opPattern","COPY",BODY,{"derivedFrom":makeQuery(id+"F19.opPattern","COPY",BODY,{"derivedFrom":makeQuery(id+"F6.opPattern","COPY",BODY,{"derivedFrom":makeQuery(id+"F5.opPattern","COPY",BODY,{"derivedFrom":makeQuery(id+"F4.opPattern","COPY",BODY,{"derivedFrom":makeQuery(id+"F2.opPattern","COPY",BODY,{"derivedFrom":makeQuery(id+"F1.opExtrude","SWEPT_BODY",BODY,{"disambiguationData":[OSD([sQuery(id+"F0.wireOp",EDGE,"E0.bottom"),sQuery(id+"F0.wireOp",EDGE,"E0.top"),sQuery(id+"F0.wireOp",EDGE,"E0.left"),sQuery(id+"F0.wireOp",EDGE,"E0.right")])]}),"instanceName":"1"}),"instanceName":"1"}),"instanceName":"1"}),"instanceName":"1"}),"instanceName":"1"}),"instanceName":"1"}),"instanceName":"1"});
            var Q48;
            Q48=makeQuery(id+"F39.opPattern","COPY",BODY,{"derivedFrom":makeQuery(id+"F23.opPattern","COPY",BODY,{"derivedFrom":makeQuery(id+"F19.opPattern","COPY",BODY,{"derivedFrom":makeQuery(id+"F17.opPattern","COPY",BODY,{"derivedFrom":makeQuery(id+"F15.opPattern","COPY",BODY,{"derivedFrom":makeQuery(id+"F12.opPattern","COPY",BODY,{"derivedFrom":makeQuery(id+"F6.opPattern","COPY",BODY,{"derivedFrom":makeQuery(id+"F5.opPattern","COPY",BODY,{"derivedFrom":makeQuery(id+"F4.opPattern","COPY",BODY,{"derivedFrom":makeQuery(id+"F2.opPattern","COPY",BODY,{"derivedFrom":makeQuery(id+"F1.opExtrude","SWEPT_BODY",BODY,{"disambiguationData":[OSD([sQuery(id+"F0.wireOp",EDGE,"E0.bottom"),sQuery(id+"F0.wireOp",EDGE,"E0.top"),sQuery(id+"F0.wireOp",EDGE,"E0.left"),sQuery(id+"F0.wireOp",EDGE,"E0.right")])]}),"instanceName":"1"}),"instanceName":"1"}),"instanceName":"1"}),"instanceName":"1"}),"instanceName":"1"}),"instanceName":"1"}),"instanceName":"1"}),"instanceName":"1"}),"instanceName":"1"}),"instanceName":"1"});
            var Q49;
            Q49=makeQuery(id+"F40.opPattern","COPY",BODY,{"derivedFrom":makeQuery(id+"F23.opPattern","COPY",BODY,{"derivedFrom":makeQuery(id+"F19.opPattern","COPY",BODY,{"derivedFrom":makeQuery(id+"F15.opPattern","COPY",BODY,{"derivedFrom":makeQuery(id+"F12.opPattern","COPY",BODY,{"derivedFrom":makeQuery(id+"F6.opPattern","COPY",BODY,{"derivedFrom":makeQuery(id+"F5.opPattern","COPY",BODY,{"derivedFrom":makeQuery(id+"F4.opPattern","COPY",BODY,{"derivedFrom":makeQuery(id+"F2.opPattern","COPY",BODY,{"derivedFrom":makeQuery(id+"F1.opExtrude","SWEPT_BODY",BODY,{"disambiguationData":[OSD([sQuery(id+"F0.wireOp",EDGE,"E0.bottom"),sQuery(id+"F0.wireOp",EDGE,"E0.top"),sQuery(id+"F0.wireOp",EDGE,"E0.left"),sQuery(id+"F0.wireOp",EDGE,"E0.right")])]}),"instanceName":"1"}),"instanceName":"1"}),"instanceName":"1"}),"instanceName":"1"}),"instanceName":"1"}),"instanceName":"1"}),"instanceName":"1"}),"instanceName":"1"}),"instanceName":"1"});
            var Q50;
            Q50=makeQuery(id+"F23.opPattern","COPY",BODY,{"derivedFrom":makeQuery(id+"F21.opPattern","COPY",BODY,{"derivedFrom":makeQuery(id+"F19.opPattern","COPY",BODY,{"derivedFrom":makeQuery(id+"F17.opPattern","COPY",BODY,{"derivedFrom":makeQuery(id+"F6.opPattern","COPY",BODY,{"derivedFrom":makeQuery(id+"F5.opPattern","COPY",BODY,{"derivedFrom":makeQuery(id+"F4.opPattern","COPY",BODY,{"derivedFrom":makeQuery(id+"F1.opExtrude","SWEPT_BODY",BODY,{"disambiguationData":[OSD([sQuery(id+"F0.wireOp",EDGE,"E0.bottom"),sQuery(id+"F0.wireOp",EDGE,"E0.top"),sQuery(id+"F0.wireOp",EDGE,"E0.left"),sQuery(id+"F0.wireOp",EDGE,"E0.right")])]}),"instanceName":"1"}),"instanceName":"1"}),"instanceName":"1"}),"instanceName":"1"}),"instanceName":"1"}),"instanceName":"1"}),"instanceName":"1"});
            var Q51;
            Q51=makeQuery(id+"F19.opPattern","COPY",BODY,{"derivedFrom":makeQuery(id+"F12.opPattern","COPY",BODY,{"derivedFrom":makeQuery(id+"F6.opPattern","COPY",BODY,{"derivedFrom":makeQuery(id+"F5.opPattern","COPY",BODY,{"derivedFrom":makeQuery(id+"F4.opPattern","COPY",BODY,{"derivedFrom":makeQuery(id+"F2.opPattern","COPY",BODY,{"derivedFrom":makeQuery(id+"F1.opExtrude","SWEPT_BODY",BODY,{"disambiguationData":[OSD([sQuery(id+"F0.wireOp",EDGE,"E0.bottom"),sQuery(id+"F0.wireOp",EDGE,"E0.top"),sQuery(id+"F0.wireOp",EDGE,"E0.left"),sQuery(id+"F0.wireOp",EDGE,"E0.right")])]}),"instanceName":"1"}),"instanceName":"1"}),"instanceName":"1"}),"instanceName":"1"}),"instanceName":"1"}),"instanceName":"1"});
            var Q52;
            Q52=makeQuery(id+"F35.opPattern","COPY",BODY,{"derivedFrom":makeQuery(id+"F34.opPattern","COPY",BODY,{"derivedFrom":makeQuery(id+"F31.opPattern","COPY",BODY,{"derivedFrom":makeQuery(id+"F5.opPattern","COPY",BODY,{"derivedFrom":makeQuery(id+"F2.opPattern","COPY",BODY,{"derivedFrom":makeQuery(id+"F1.opExtrude","SWEPT_BODY",BODY,{"disambiguationData":[OSD([sQuery(id+"F0.wireOp",EDGE,"E0.bottom"),sQuery(id+"F0.wireOp",EDGE,"E0.top"),sQuery(id+"F0.wireOp",EDGE,"E0.left"),sQuery(id+"F0.wireOp",EDGE,"E0.right")])]}),"instanceName":"1"}),"instanceName":"1"}),"instanceName":"1"}),"instanceName":"1"}),"instanceName":"1"});
            var Q53;
            Q53=makeQuery(id+"F39.opPattern","COPY",BODY,{"derivedFrom":makeQuery(id+"F26.opPattern","COPY",BODY,{"derivedFrom":makeQuery(id+"F19.opPattern","COPY",BODY,{"derivedFrom":makeQuery(id+"F13.opPattern","COPY",BODY,{"derivedFrom":makeQuery(id+"F5.opPattern","COPY",BODY,{"derivedFrom":makeQuery(id+"F4.opPattern","COPY",BODY,{"derivedFrom":makeQuery(id+"F1.opExtrude","SWEPT_BODY",BODY,{"disambiguationData":[OSD([sQuery(id+"F0.wireOp",EDGE,"E0.bottom"),sQuery(id+"F0.wireOp",EDGE,"E0.top"),sQuery(id+"F0.wireOp",EDGE,"E0.left"),sQuery(id+"F0.wireOp",EDGE,"E0.right")])]}),"instanceName":"1"}),"instanceName":"1"}),"instanceName":"1"}),"instanceName":"1"}),"instanceName":"1"}),"instanceName":"1"});
            var Q54;
            Q54=makeQuery(id+"F26.opPattern","COPY",BODY,{"derivedFrom":makeQuery(id+"F19.opPattern","COPY",BODY,{"derivedFrom":makeQuery(id+"F17.opPattern","COPY",BODY,{"derivedFrom":makeQuery(id+"F5.opPattern","COPY",BODY,{"derivedFrom":makeQuery(id+"F4.opPattern","COPY",BODY,{"derivedFrom":makeQuery(id+"F2.opPattern","COPY",BODY,{"derivedFrom":makeQuery(id+"F1.opExtrude","SWEPT_BODY",BODY,{"disambiguationData":[OSD([sQuery(id+"F0.wireOp",EDGE,"E0.bottom"),sQuery(id+"F0.wireOp",EDGE,"E0.top"),sQuery(id+"F0.wireOp",EDGE,"E0.left"),sQuery(id+"F0.wireOp",EDGE,"E0.right")])]}),"instanceName":"1"}),"instanceName":"1"}),"instanceName":"1"}),"instanceName":"1"}),"instanceName":"1"}),"instanceName":"1"});
            var Q55;
            Q55=makeQuery(id+"F28.opPattern","COPY",BODY,{"derivedFrom":makeQuery(id+"F26.opPattern","COPY",BODY,{"derivedFrom":makeQuery(id+"F19.opPattern","COPY",BODY,{"derivedFrom":makeQuery(id+"F15.opPattern","COPY",BODY,{"derivedFrom":makeQuery(id+"F12.opPattern","COPY",BODY,{"derivedFrom":makeQuery(id+"F6.opPattern","COPY",BODY,{"derivedFrom":makeQuery(id+"F5.opPattern","COPY",BODY,{"derivedFrom":makeQuery(id+"F4.opPattern","COPY",BODY,{"derivedFrom":makeQuery(id+"F2.opPattern","COPY",BODY,{"derivedFrom":makeQuery(id+"F1.opExtrude","SWEPT_BODY",BODY,{"disambiguationData":[OSD([sQuery(id+"F0.wireOp",EDGE,"E0.bottom"),sQuery(id+"F0.wireOp",EDGE,"E0.top"),sQuery(id+"F0.wireOp",EDGE,"E0.left"),sQuery(id+"F0.wireOp",EDGE,"E0.right")])]}),"instanceName":"1"}),"instanceName":"1"}),"instanceName":"1"}),"instanceName":"1"}),"instanceName":"1"}),"instanceName":"1"}),"instanceName":"1"}),"instanceName":"1"}),"instanceName":"1"});
            var Q56;
            Q56=makeQuery(id+"F22.opPattern","COPY",BODY,{"derivedFrom":makeQuery(id+"F21.opPattern","COPY",BODY,{"derivedFrom":makeQuery(id+"F19.opPattern","COPY",BODY,{"derivedFrom":makeQuery(id+"F17.opPattern","COPY",BODY,{"derivedFrom":makeQuery(id+"F5.opPattern","COPY",BODY,{"derivedFrom":makeQuery(id+"F4.opPattern","COPY",BODY,{"derivedFrom":makeQuery(id+"F1.opExtrude","SWEPT_BODY",BODY,{"disambiguationData":[OSD([sQuery(id+"F0.wireOp",EDGE,"E0.bottom"),sQuery(id+"F0.wireOp",EDGE,"E0.top"),sQuery(id+"F0.wireOp",EDGE,"E0.left"),sQuery(id+"F0.wireOp",EDGE,"E0.right")])]}),"instanceName":"1"}),"instanceName":"1"}),"instanceName":"1"}),"instanceName":"1"}),"instanceName":"1"}),"instanceName":"1"});
            var Q57;
            Q57=makeQuery(id+"F42.opPattern","COPY",BODY,{"derivedFrom":makeQuery(id+"F29.opPattern","COPY",BODY,{"derivedFrom":makeQuery(id+"F19.opPattern","COPY",BODY,{"derivedFrom":makeQuery(id+"F15.opPattern","COPY",BODY,{"derivedFrom":makeQuery(id+"F12.opPattern","COPY",BODY,{"derivedFrom":makeQuery(id+"F6.opPattern","COPY",BODY,{"derivedFrom":makeQuery(id+"F5.opPattern","COPY",BODY,{"derivedFrom":makeQuery(id+"F4.opPattern","COPY",BODY,{"derivedFrom":makeQuery(id+"F2.opPattern","COPY",BODY,{"derivedFrom":makeQuery(id+"F1.opExtrude","SWEPT_BODY",BODY,{"disambiguationData":[OSD([sQuery(id+"F0.wireOp",EDGE,"E0.bottom"),sQuery(id+"F0.wireOp",EDGE,"E0.top"),sQuery(id+"F0.wireOp",EDGE,"E0.left"),sQuery(id+"F0.wireOp",EDGE,"E0.right")])]}),"instanceName":"1"}),"instanceName":"1"}),"instanceName":"1"}),"instanceName":"1"}),"instanceName":"1"}),"instanceName":"1"}),"instanceName":"1"}),"instanceName":"1"}),"instanceName":"1"});
            var Q58;
            Q58=makeQuery(id+"F28.opPattern","COPY",BODY,{"derivedFrom":makeQuery(id+"F26.opPattern","COPY",BODY,{"derivedFrom":makeQuery(id+"F23.opPattern","COPY",BODY,{"derivedFrom":makeQuery(id+"F19.opPattern","COPY",BODY,{"derivedFrom":makeQuery(id+"F15.opPattern","COPY",BODY,{"derivedFrom":makeQuery(id+"F12.opPattern","COPY",BODY,{"derivedFrom":makeQuery(id+"F6.opPattern","COPY",BODY,{"derivedFrom":makeQuery(id+"F5.opPattern","COPY",BODY,{"derivedFrom":makeQuery(id+"F4.opPattern","COPY",BODY,{"derivedFrom":makeQuery(id+"F2.opPattern","COPY",BODY,{"derivedFrom":makeQuery(id+"F1.opExtrude","SWEPT_BODY",BODY,{"disambiguationData":[OSD([sQuery(id+"F0.wireOp",EDGE,"E0.bottom"),sQuery(id+"F0.wireOp",EDGE,"E0.top"),sQuery(id+"F0.wireOp",EDGE,"E0.left"),sQuery(id+"F0.wireOp",EDGE,"E0.right")])]}),"instanceName":"1"}),"instanceName":"1"}),"instanceName":"1"}),"instanceName":"1"}),"instanceName":"1"}),"instanceName":"1"}),"instanceName":"1"}),"instanceName":"1"}),"instanceName":"1"}),"instanceName":"1"});
            var Q59;
            Q59=makeQuery(id+"F23.opPattern","COPY",BODY,{"derivedFrom":makeQuery(id+"F19.opPattern","COPY",BODY,{"derivedFrom":makeQuery(id+"F12.opPattern","COPY",BODY,{"derivedFrom":makeQuery(id+"F6.opPattern","COPY",BODY,{"derivedFrom":makeQuery(id+"F5.opPattern","COPY",BODY,{"derivedFrom":makeQuery(id+"F4.opPattern","COPY",BODY,{"derivedFrom":makeQuery(id+"F2.opPattern","COPY",BODY,{"derivedFrom":makeQuery(id+"F1.opExtrude","SWEPT_BODY",BODY,{"disambiguationData":[OSD([sQuery(id+"F0.wireOp",EDGE,"E0.bottom"),sQuery(id+"F0.wireOp",EDGE,"E0.top"),sQuery(id+"F0.wireOp",EDGE,"E0.left"),sQuery(id+"F0.wireOp",EDGE,"E0.right")])]}),"instanceName":"1"}),"instanceName":"1"}),"instanceName":"1"}),"instanceName":"1"}),"instanceName":"1"}),"instanceName":"1"}),"instanceName":"1"});
            var Q60;
            Q60=makeQuery(id+"F48.opPattern","COPY",BODY,{"derivedFrom":makeQuery(id+"F45.opPattern","COPY",BODY,{"derivedFrom":makeQuery(id+"F40.opPattern","COPY",BODY,{"derivedFrom":makeQuery(id+"F23.opPattern","COPY",BODY,{"derivedFrom":makeQuery(id+"F19.opPattern","COPY",BODY,{"derivedFrom":makeQuery(id+"F17.opPattern","COPY",BODY,{"derivedFrom":makeQuery(id+"F12.opPattern","COPY",BODY,{"derivedFrom":makeQuery(id+"F6.opPattern","COPY",BODY,{"derivedFrom":makeQuery(id+"F5.opPattern","COPY",BODY,{"derivedFrom":makeQuery(id+"F4.opPattern","COPY",BODY,{"derivedFrom":makeQuery(id+"F1.opExtrude","SWEPT_BODY",BODY,{"disambiguationData":[OSD([sQuery(id+"F0.wireOp",EDGE,"E0.bottom"),sQuery(id+"F0.wireOp",EDGE,"E0.top"),sQuery(id+"F0.wireOp",EDGE,"E0.left"),sQuery(id+"F0.wireOp",EDGE,"E0.right")])]}),"instanceName":"1"}),"instanceName":"1"}),"instanceName":"1"}),"instanceName":"1"}),"instanceName":"1"}),"instanceName":"1"}),"instanceName":"1"}),"instanceName":"1"}),"instanceName":"1"}),"instanceName":"1"});
            var Q61;
            Q61=makeQuery(id+"F34.opPattern","COPY",BODY,{"derivedFrom":makeQuery(id+"F31.opPattern","COPY",BODY,{"derivedFrom":makeQuery(id+"F5.opPattern","COPY",BODY,{"derivedFrom":makeQuery(id+"F2.opPattern","COPY",BODY,{"derivedFrom":makeQuery(id+"F1.opExtrude","SWEPT_BODY",BODY,{"disambiguationData":[OSD([sQuery(id+"F0.wireOp",EDGE,"E0.bottom"),sQuery(id+"F0.wireOp",EDGE,"E0.top"),sQuery(id+"F0.wireOp",EDGE,"E0.left"),sQuery(id+"F0.wireOp",EDGE,"E0.right")])]}),"instanceName":"1"}),"instanceName":"1"}),"instanceName":"1"}),"instanceName":"1"});
            var Q62;
            Q62=makeQuery(id+"F39.opPattern","COPY",BODY,{"derivedFrom":makeQuery(id+"F29.opPattern","COPY",BODY,{"derivedFrom":makeQuery(id+"F26.opPattern","COPY",BODY,{"derivedFrom":makeQuery(id+"F19.opPattern","COPY",BODY,{"derivedFrom":makeQuery(id+"F15.opPattern","COPY",BODY,{"derivedFrom":makeQuery(id+"F12.opPattern","COPY",BODY,{"derivedFrom":makeQuery(id+"F6.opPattern","COPY",BODY,{"derivedFrom":makeQuery(id+"F5.opPattern","COPY",BODY,{"derivedFrom":makeQuery(id+"F4.opPattern","COPY",BODY,{"derivedFrom":makeQuery(id+"F2.opPattern","COPY",BODY,{"derivedFrom":makeQuery(id+"F1.opExtrude","SWEPT_BODY",BODY,{"disambiguationData":[OSD([sQuery(id+"F0.wireOp",EDGE,"E0.bottom"),sQuery(id+"F0.wireOp",EDGE,"E0.top"),sQuery(id+"F0.wireOp",EDGE,"E0.left"),sQuery(id+"F0.wireOp",EDGE,"E0.right")])]}),"instanceName":"1"}),"instanceName":"1"}),"instanceName":"1"}),"instanceName":"1"}),"instanceName":"1"}),"instanceName":"1"}),"instanceName":"1"}),"instanceName":"1"}),"instanceName":"1"}),"instanceName":"1"});
            var Q63;
            Q63=makeQuery(id+"F7.opPattern","COPY",BODY,{"derivedFrom":makeQuery(id+"F4.opPattern","COPY",BODY,{"derivedFrom":makeQuery(id+"F2.opPattern","COPY",BODY,{"derivedFrom":makeQuery(id+"F1.opExtrude","SWEPT_BODY",BODY,{"disambiguationData":[OSD([sQuery(id+"F0.wireOp",EDGE,"E0.bottom"),sQuery(id+"F0.wireOp",EDGE,"E0.top"),sQuery(id+"F0.wireOp",EDGE,"E0.left"),sQuery(id+"F0.wireOp",EDGE,"E0.right")])]}),"instanceName":"1"}),"instanceName":"1"}),"instanceName":"1"});
            var Q64;
            Q64=makeQuery(id+"F17.opPattern","COPY",BODY,{"derivedFrom":makeQuery(id+"F16.opPattern","COPY",BODY,{"derivedFrom":makeQuery(id+"F8.opPattern","COPY",BODY,{"derivedFrom":makeQuery(id+"F5.opPattern","COPY",BODY,{"derivedFrom":makeQuery(id+"F4.opPattern","COPY",BODY,{"derivedFrom":makeQuery(id+"F2.opPattern","COPY",BODY,{"derivedFrom":makeQuery(id+"F1.opExtrude","SWEPT_BODY",BODY,{"disambiguationData":[OSD([sQuery(id+"F0.wireOp",EDGE,"E0.bottom"),sQuery(id+"F0.wireOp",EDGE,"E0.top"),sQuery(id+"F0.wireOp",EDGE,"E0.left"),sQuery(id+"F0.wireOp",EDGE,"E0.right")])]}),"instanceName":"1"}),"instanceName":"1"}),"instanceName":"1"}),"instanceName":"1"}),"instanceName":"1"}),"instanceName":"1"});
            var Q65;
            Q65=makeQuery(id+"F40.opPattern","COPY",BODY,{"derivedFrom":makeQuery(id+"F19.opPattern","COPY",BODY,{"derivedFrom":makeQuery(id+"F5.opPattern","COPY",BODY,{"derivedFrom":makeQuery(id+"F4.opPattern","COPY",BODY,{"derivedFrom":makeQuery(id+"F2.opPattern","COPY",BODY,{"derivedFrom":makeQuery(id+"F1.opExtrude","SWEPT_BODY",BODY,{"disambiguationData":[OSD([sQuery(id+"F0.wireOp",EDGE,"E0.bottom"),sQuery(id+"F0.wireOp",EDGE,"E0.top"),sQuery(id+"F0.wireOp",EDGE,"E0.left"),sQuery(id+"F0.wireOp",EDGE,"E0.right")])]}),"instanceName":"1"}),"instanceName":"1"}),"instanceName":"1"}),"instanceName":"1"}),"instanceName":"1"});
            var Q66;
            Q66=makeQuery(id+"F42.opPattern","COPY",BODY,{"derivedFrom":makeQuery(id+"F29.opPattern","COPY",BODY,{"derivedFrom":makeQuery(id+"F28.opPattern","COPY",BODY,{"derivedFrom":makeQuery(id+"F26.opPattern","COPY",BODY,{"derivedFrom":makeQuery(id+"F17.opPattern","COPY",BODY,{"derivedFrom":makeQuery(id+"F13.opPattern","COPY",BODY,{"derivedFrom":makeQuery(id+"F5.opPattern","COPY",BODY,{"derivedFrom":makeQuery(id+"F4.opPattern","COPY",BODY,{"derivedFrom":makeQuery(id+"F1.opExtrude","SWEPT_BODY",BODY,{"disambiguationData":[OSD([sQuery(id+"F0.wireOp",EDGE,"E0.bottom"),sQuery(id+"F0.wireOp",EDGE,"E0.top"),sQuery(id+"F0.wireOp",EDGE,"E0.left"),sQuery(id+"F0.wireOp",EDGE,"E0.right")])]}),"instanceName":"1"}),"instanceName":"1"}),"instanceName":"1"}),"instanceName":"1"}),"instanceName":"1"}),"instanceName":"1"}),"instanceName":"1"}),"instanceName":"1"});
            var Q67;
            Q67=makeQuery(id+"F1.opExtrude","SWEPT_BODY",BODY,{"disambiguationData":[OSD([sQuery(id+"F0.wireOp",EDGE,"E0.bottom"),sQuery(id+"F0.wireOp",EDGE,"E0.top"),sQuery(id+"F0.wireOp",EDGE,"E0.left"),sQuery(id+"F0.wireOp",EDGE,"E0.right")])]});
            var Q68;
            Q68=makeQuery(id+"F5.opPattern","COPY",BODY,{"derivedFrom":makeQuery(id+"F1.opExtrude","SWEPT_BODY",BODY,{"disambiguationData":[OSD([sQuery(id+"F0.wireOp",EDGE,"E0.bottom"),sQuery(id+"F0.wireOp",EDGE,"E0.top"),sQuery(id+"F0.wireOp",EDGE,"E0.left"),sQuery(id+"F0.wireOp",EDGE,"E0.right")])]}),"instanceName":"1"});
            var Q69;
            Q69=makeQuery(id+"F23.opPattern","COPY",BODY,{"derivedFrom":makeQuery(id+"F19.opPattern","COPY",BODY,{"derivedFrom":makeQuery(id+"F17.opPattern","COPY",BODY,{"derivedFrom":makeQuery(id+"F13.opPattern","COPY",BODY,{"derivedFrom":makeQuery(id+"F5.opPattern","COPY",BODY,{"derivedFrom":makeQuery(id+"F4.opPattern","COPY",BODY,{"derivedFrom":makeQuery(id+"F1.opExtrude","SWEPT_BODY",BODY,{"disambiguationData":[OSD([sQuery(id+"F0.wireOp",EDGE,"E0.bottom"),sQuery(id+"F0.wireOp",EDGE,"E0.top"),sQuery(id+"F0.wireOp",EDGE,"E0.left"),sQuery(id+"F0.wireOp",EDGE,"E0.right")])]}),"instanceName":"1"}),"instanceName":"1"}),"instanceName":"1"}),"instanceName":"1"}),"instanceName":"1"}),"instanceName":"1"});
            var Q70;
            Q70=makeQuery(id+"F39.opPattern","COPY",BODY,{"derivedFrom":makeQuery(id+"F26.opPattern","COPY",BODY,{"derivedFrom":makeQuery(id+"F19.opPattern","COPY",BODY,{"derivedFrom":makeQuery(id+"F6.opPattern","COPY",BODY,{"derivedFrom":makeQuery(id+"F5.opPattern","COPY",BODY,{"derivedFrom":makeQuery(id+"F4.opPattern","COPY",BODY,{"derivedFrom":makeQuery(id+"F1.opExtrude","SWEPT_BODY",BODY,{"disambiguationData":[OSD([sQuery(id+"F0.wireOp",EDGE,"E0.bottom"),sQuery(id+"F0.wireOp",EDGE,"E0.top"),sQuery(id+"F0.wireOp",EDGE,"E0.left"),sQuery(id+"F0.wireOp",EDGE,"E0.right")])]}),"instanceName":"1"}),"instanceName":"1"}),"instanceName":"1"}),"instanceName":"1"}),"instanceName":"1"}),"instanceName":"1"});
            var Q71;
            Q71=makeQuery(id+"F24.opPattern","COPY",BODY,{"derivedFrom":makeQuery(id+"F23.opPattern","COPY",BODY,{"derivedFrom":makeQuery(id+"F21.opPattern","COPY",BODY,{"derivedFrom":makeQuery(id+"F19.opPattern","COPY",BODY,{"derivedFrom":makeQuery(id+"F17.opPattern","COPY",BODY,{"derivedFrom":makeQuery(id+"F12.opPattern","COPY",BODY,{"derivedFrom":makeQuery(id+"F6.opPattern","COPY",BODY,{"derivedFrom":makeQuery(id+"F5.opPattern","COPY",BODY,{"derivedFrom":makeQuery(id+"F4.opPattern","COPY",BODY,{"derivedFrom":makeQuery(id+"F1.opExtrude","SWEPT_BODY",BODY,{"disambiguationData":[OSD([sQuery(id+"F0.wireOp",EDGE,"E0.bottom"),sQuery(id+"F0.wireOp",EDGE,"E0.top"),sQuery(id+"F0.wireOp",EDGE,"E0.left"),sQuery(id+"F0.wireOp",EDGE,"E0.right")])]}),"instanceName":"1"}),"instanceName":"1"}),"instanceName":"1"}),"instanceName":"1"}),"instanceName":"1"}),"instanceName":"1"}),"instanceName":"1"}),"instanceName":"1"}),"instanceName":"1"});
            var Q72;
            Q72=makeQuery(id+"F40.opPattern","COPY",BODY,{"derivedFrom":makeQuery(id+"F21.opPattern","COPY",BODY,{"derivedFrom":makeQuery(id+"F19.opPattern","COPY",BODY,{"derivedFrom":makeQuery(id+"F17.opPattern","COPY",BODY,{"derivedFrom":makeQuery(id+"F6.opPattern","COPY",BODY,{"derivedFrom":makeQuery(id+"F5.opPattern","COPY",BODY,{"derivedFrom":makeQuery(id+"F4.opPattern","COPY",BODY,{"derivedFrom":makeQuery(id+"F1.opExtrude","SWEPT_BODY",BODY,{"disambiguationData":[OSD([sQuery(id+"F0.wireOp",EDGE,"E0.bottom"),sQuery(id+"F0.wireOp",EDGE,"E0.top"),sQuery(id+"F0.wireOp",EDGE,"E0.left"),sQuery(id+"F0.wireOp",EDGE,"E0.right")])]}),"instanceName":"1"}),"instanceName":"1"}),"instanceName":"1"}),"instanceName":"1"}),"instanceName":"1"}),"instanceName":"1"}),"instanceName":"1"});
            var Q73;
            Q73=makeQuery(id+"F40.opPattern","COPY",BODY,{"derivedFrom":makeQuery(id+"F23.opPattern","COPY",BODY,{"derivedFrom":makeQuery(id+"F19.opPattern","COPY",BODY,{"derivedFrom":makeQuery(id+"F17.opPattern","COPY",BODY,{"derivedFrom":makeQuery(id+"F15.opPattern","COPY",BODY,{"derivedFrom":makeQuery(id+"F12.opPattern","COPY",BODY,{"derivedFrom":makeQuery(id+"F6.opPattern","COPY",BODY,{"derivedFrom":makeQuery(id+"F5.opPattern","COPY",BODY,{"derivedFrom":makeQuery(id+"F4.opPattern","COPY",BODY,{"derivedFrom":makeQuery(id+"F2.opPattern","COPY",BODY,{"derivedFrom":makeQuery(id+"F1.opExtrude","SWEPT_BODY",BODY,{"disambiguationData":[OSD([sQuery(id+"F0.wireOp",EDGE,"E0.bottom"),sQuery(id+"F0.wireOp",EDGE,"E0.top"),sQuery(id+"F0.wireOp",EDGE,"E0.left"),sQuery(id+"F0.wireOp",EDGE,"E0.right")])]}),"instanceName":"1"}),"instanceName":"1"}),"instanceName":"1"}),"instanceName":"1"}),"instanceName":"1"}),"instanceName":"1"}),"instanceName":"1"}),"instanceName":"1"}),"instanceName":"1"}),"instanceName":"1"});
            var Q74;
            Q74=makeQuery(id+"F34.opPattern","COPY",BODY,{"derivedFrom":makeQuery(id+"F31.opPattern","COPY",BODY,{"derivedFrom":makeQuery(id+"F5.opPattern","COPY",BODY,{"derivedFrom":makeQuery(id+"F1.opExtrude","SWEPT_BODY",BODY,{"disambiguationData":[OSD([sQuery(id+"F0.wireOp",EDGE,"E0.bottom"),sQuery(id+"F0.wireOp",EDGE,"E0.top"),sQuery(id+"F0.wireOp",EDGE,"E0.left"),sQuery(id+"F0.wireOp",EDGE,"E0.right")])]}),"instanceName":"1"}),"instanceName":"1"}),"instanceName":"1"});
            var Q75;
            Q75=makeQuery(id+"F45.opPattern","COPY",BODY,{"derivedFrom":makeQuery(id+"F40.opPattern","COPY",BODY,{"derivedFrom":makeQuery(id+"F29.opPattern","COPY",BODY,{"derivedFrom":makeQuery(id+"F23.opPattern","COPY",BODY,{"derivedFrom":makeQuery(id+"F19.opPattern","COPY",BODY,{"derivedFrom":makeQuery(id+"F15.opPattern","COPY",BODY,{"derivedFrom":makeQuery(id+"F12.opPattern","COPY",BODY,{"derivedFrom":makeQuery(id+"F6.opPattern","COPY",BODY,{"derivedFrom":makeQuery(id+"F5.opPattern","COPY",BODY,{"derivedFrom":makeQuery(id+"F4.opPattern","COPY",BODY,{"derivedFrom":makeQuery(id+"F2.opPattern","COPY",BODY,{"derivedFrom":makeQuery(id+"F1.opExtrude","SWEPT_BODY",BODY,{"disambiguationData":[OSD([sQuery(id+"F0.wireOp",EDGE,"E0.bottom"),sQuery(id+"F0.wireOp",EDGE,"E0.top"),sQuery(id+"F0.wireOp",EDGE,"E0.left"),sQuery(id+"F0.wireOp",EDGE,"E0.right")])]}),"instanceName":"1"}),"instanceName":"1"}),"instanceName":"1"}),"instanceName":"1"}),"instanceName":"1"}),"instanceName":"1"}),"instanceName":"1"}),"instanceName":"1"}),"instanceName":"1"}),"instanceName":"1"}),"instanceName":"1"});
            var Q76;
            Q76=makeQuery(id+"F47.opPattern","COPY",BODY,{"derivedFrom":makeQuery(id+"F45.opPattern","COPY",BODY,{"derivedFrom":makeQuery(id+"F40.opPattern","COPY",BODY,{"derivedFrom":makeQuery(id+"F21.opPattern","COPY",BODY,{"derivedFrom":makeQuery(id+"F19.opPattern","COPY",BODY,{"derivedFrom":makeQuery(id+"F17.opPattern","COPY",BODY,{"derivedFrom":makeQuery(id+"F6.opPattern","COPY",BODY,{"derivedFrom":makeQuery(id+"F5.opPattern","COPY",BODY,{"derivedFrom":makeQuery(id+"F4.opPattern","COPY",BODY,{"derivedFrom":makeQuery(id+"F1.opExtrude","SWEPT_BODY",BODY,{"disambiguationData":[OSD([sQuery(id+"F0.wireOp",EDGE,"E0.bottom"),sQuery(id+"F0.wireOp",EDGE,"E0.top"),sQuery(id+"F0.wireOp",EDGE,"E0.left"),sQuery(id+"F0.wireOp",EDGE,"E0.right")])]}),"instanceName":"1"}),"instanceName":"1"}),"instanceName":"1"}),"instanceName":"1"}),"instanceName":"1"}),"instanceName":"1"}),"instanceName":"1"}),"instanceName":"1"}),"instanceName":"1"});
            var Q77;
            Q77=makeQuery(id+"F49.opPattern","COPY",BODY,{"derivedFrom":makeQuery(id+"F42.opPattern","COPY",BODY,{"derivedFrom":makeQuery(id+"F29.opPattern","COPY",BODY,{"derivedFrom":makeQuery(id+"F28.opPattern","COPY",BODY,{"derivedFrom":makeQuery(id+"F19.opPattern","COPY",BODY,{"derivedFrom":makeQuery(id+"F17.opPattern","COPY",BODY,{"derivedFrom":makeQuery(id+"F15.opPattern","COPY",BODY,{"derivedFrom":makeQuery(id+"F12.opPattern","COPY",BODY,{"derivedFrom":makeQuery(id+"F6.opPattern","COPY",BODY,{"derivedFrom":makeQuery(id+"F5.opPattern","COPY",BODY,{"derivedFrom":makeQuery(id+"F4.opPattern","COPY",BODY,{"derivedFrom":makeQuery(id+"F2.opPattern","COPY",BODY,{"derivedFrom":makeQuery(id+"F1.opExtrude","SWEPT_BODY",BODY,{"disambiguationData":[OSD([sQuery(id+"F0.wireOp",EDGE,"E0.bottom"),sQuery(id+"F0.wireOp",EDGE,"E0.top"),sQuery(id+"F0.wireOp",EDGE,"E0.left"),sQuery(id+"F0.wireOp",EDGE,"E0.right")])]}),"instanceName":"1"}),"instanceName":"1"}),"instanceName":"1"}),"instanceName":"1"}),"instanceName":"1"}),"instanceName":"1"}),"instanceName":"1"}),"instanceName":"1"}),"instanceName":"1"}),"instanceName":"1"}),"instanceName":"1"}),"instanceName":"1"});
            var Q78;
            Q78=makeQuery(id+"F26.opPattern","COPY",BODY,{"derivedFrom":makeQuery(id+"F19.opPattern","COPY",BODY,{"derivedFrom":makeQuery(id+"F17.opPattern","COPY",BODY,{"derivedFrom":makeQuery(id+"F15.opPattern","COPY",BODY,{"derivedFrom":makeQuery(id+"F12.opPattern","COPY",BODY,{"derivedFrom":makeQuery(id+"F6.opPattern","COPY",BODY,{"derivedFrom":makeQuery(id+"F5.opPattern","COPY",BODY,{"derivedFrom":makeQuery(id+"F4.opPattern","COPY",BODY,{"derivedFrom":makeQuery(id+"F2.opPattern","COPY",BODY,{"derivedFrom":makeQuery(id+"F1.opExtrude","SWEPT_BODY",BODY,{"disambiguationData":[OSD([sQuery(id+"F0.wireOp",EDGE,"E0.bottom"),sQuery(id+"F0.wireOp",EDGE,"E0.top"),sQuery(id+"F0.wireOp",EDGE,"E0.left"),sQuery(id+"F0.wireOp",EDGE,"E0.right")])]}),"instanceName":"1"}),"instanceName":"1"}),"instanceName":"1"}),"instanceName":"1"}),"instanceName":"1"}),"instanceName":"1"}),"instanceName":"1"}),"instanceName":"1"}),"instanceName":"1"});
            var Q79;
            Q79=makeQuery(id+"F23.opPattern","COPY",BODY,{"derivedFrom":makeQuery(id+"F21.opPattern","COPY",BODY,{"derivedFrom":makeQuery(id+"F19.opPattern","COPY",BODY,{"derivedFrom":makeQuery(id+"F12.opPattern","COPY",BODY,{"derivedFrom":makeQuery(id+"F6.opPattern","COPY",BODY,{"derivedFrom":makeQuery(id+"F5.opPattern","COPY",BODY,{"derivedFrom":makeQuery(id+"F4.opPattern","COPY",BODY,{"derivedFrom":makeQuery(id+"F2.opPattern","COPY",BODY,{"derivedFrom":makeQuery(id+"F1.opExtrude","SWEPT_BODY",BODY,{"disambiguationData":[OSD([sQuery(id+"F0.wireOp",EDGE,"E0.bottom"),sQuery(id+"F0.wireOp",EDGE,"E0.top"),sQuery(id+"F0.wireOp",EDGE,"E0.left"),sQuery(id+"F0.wireOp",EDGE,"E0.right")])]}),"instanceName":"1"}),"instanceName":"1"}),"instanceName":"1"}),"instanceName":"1"}),"instanceName":"1"}),"instanceName":"1"}),"instanceName":"1"}),"instanceName":"1"});
            var Q80;
            Q80=makeQuery(id+"F40.opPattern","COPY",BODY,{"derivedFrom":makeQuery(id+"F28.opPattern","COPY",BODY,{"derivedFrom":makeQuery(id+"F19.opPattern","COPY",BODY,{"derivedFrom":makeQuery(id+"F17.opPattern","COPY",BODY,{"derivedFrom":makeQuery(id+"F13.opPattern","COPY",BODY,{"derivedFrom":makeQuery(id+"F5.opPattern","COPY",BODY,{"derivedFrom":makeQuery(id+"F4.opPattern","COPY",BODY,{"derivedFrom":makeQuery(id+"F1.opExtrude","SWEPT_BODY",BODY,{"disambiguationData":[OSD([sQuery(id+"F0.wireOp",EDGE,"E0.bottom"),sQuery(id+"F0.wireOp",EDGE,"E0.top"),sQuery(id+"F0.wireOp",EDGE,"E0.left"),sQuery(id+"F0.wireOp",EDGE,"E0.right")])]}),"instanceName":"1"}),"instanceName":"1"}),"instanceName":"1"}),"instanceName":"1"}),"instanceName":"1"}),"instanceName":"1"}),"instanceName":"1"});
            var Q81;
            Q81=makeQuery(id+"F45.opPattern","COPY",BODY,{"derivedFrom":makeQuery(id+"F40.opPattern","COPY",BODY,{"derivedFrom":makeQuery(id+"F28.opPattern","COPY",BODY,{"derivedFrom":makeQuery(id+"F19.opPattern","COPY",BODY,{"derivedFrom":makeQuery(id+"F17.opPattern","COPY",BODY,{"derivedFrom":makeQuery(id+"F15.opPattern","COPY",BODY,{"derivedFrom":makeQuery(id+"F12.opPattern","COPY",BODY,{"derivedFrom":makeQuery(id+"F6.opPattern","COPY",BODY,{"derivedFrom":makeQuery(id+"F5.opPattern","COPY",BODY,{"derivedFrom":makeQuery(id+"F4.opPattern","COPY",BODY,{"derivedFrom":makeQuery(id+"F2.opPattern","COPY",BODY,{"derivedFrom":makeQuery(id+"F1.opExtrude","SWEPT_BODY",BODY,{"disambiguationData":[OSD([sQuery(id+"F0.wireOp",EDGE,"E0.bottom"),sQuery(id+"F0.wireOp",EDGE,"E0.top"),sQuery(id+"F0.wireOp",EDGE,"E0.left"),sQuery(id+"F0.wireOp",EDGE,"E0.right")])]}),"instanceName":"1"}),"instanceName":"1"}),"instanceName":"1"}),"instanceName":"1"}),"instanceName":"1"}),"instanceName":"1"}),"instanceName":"1"}),"instanceName":"1"}),"instanceName":"1"}),"instanceName":"1"}),"instanceName":"1"});
            var Q82;
            Q82=makeQuery(id+"F26.opPattern","COPY",BODY,{"derivedFrom":makeQuery(id+"F18.opPattern","COPY",BODY,{"derivedFrom":makeQuery(id+"F17.opPattern","COPY",BODY,{"derivedFrom":makeQuery(id+"F8.opPattern","COPY",BODY,{"derivedFrom":makeQuery(id+"F5.opPattern","COPY",BODY,{"derivedFrom":makeQuery(id+"F4.opPattern","COPY",BODY,{"derivedFrom":makeQuery(id+"F1.opExtrude","SWEPT_BODY",BODY,{"disambiguationData":[OSD([sQuery(id+"F0.wireOp",EDGE,"E0.bottom"),sQuery(id+"F0.wireOp",EDGE,"E0.top"),sQuery(id+"F0.wireOp",EDGE,"E0.left"),sQuery(id+"F0.wireOp",EDGE,"E0.right")])]}),"instanceName":"1"}),"instanceName":"1"}),"instanceName":"1"}),"instanceName":"1"}),"instanceName":"1"}),"instanceName":"1"});
            var Q83;
            Q83=makeQuery(id+"F21.opPattern","COPY",BODY,{"derivedFrom":makeQuery(id+"F19.opPattern","COPY",BODY,{"derivedFrom":makeQuery(id+"F17.opPattern","COPY",BODY,{"derivedFrom":makeQuery(id+"F5.opPattern","COPY",BODY,{"derivedFrom":makeQuery(id+"F4.opPattern","COPY",BODY,{"derivedFrom":makeQuery(id+"F2.opPattern","COPY",BODY,{"derivedFrom":makeQuery(id+"F1.opExtrude","SWEPT_BODY",BODY,{"disambiguationData":[OSD([sQuery(id+"F0.wireOp",EDGE,"E0.bottom"),sQuery(id+"F0.wireOp",EDGE,"E0.top"),sQuery(id+"F0.wireOp",EDGE,"E0.left"),sQuery(id+"F0.wireOp",EDGE,"E0.right")])]}),"instanceName":"1"}),"instanceName":"1"}),"instanceName":"1"}),"instanceName":"1"}),"instanceName":"1"}),"instanceName":"1"});
            var Q84;
            Q84=makeQuery(id+"F40.opPattern","COPY",BODY,{"derivedFrom":makeQuery(id+"F23.opPattern","COPY",BODY,{"derivedFrom":makeQuery(id+"F19.opPattern","COPY",BODY,{"derivedFrom":makeQuery(id+"F17.opPattern","COPY",BODY,{"derivedFrom":makeQuery(id+"F12.opPattern","COPY",BODY,{"derivedFrom":makeQuery(id+"F6.opPattern","COPY",BODY,{"derivedFrom":makeQuery(id+"F5.opPattern","COPY",BODY,{"derivedFrom":makeQuery(id+"F4.opPattern","COPY",BODY,{"derivedFrom":makeQuery(id+"F1.opExtrude","SWEPT_BODY",BODY,{"disambiguationData":[OSD([sQuery(id+"F0.wireOp",EDGE,"E0.bottom"),sQuery(id+"F0.wireOp",EDGE,"E0.top"),sQuery(id+"F0.wireOp",EDGE,"E0.left"),sQuery(id+"F0.wireOp",EDGE,"E0.right")])]}),"instanceName":"1"}),"instanceName":"1"}),"instanceName":"1"}),"instanceName":"1"}),"instanceName":"1"}),"instanceName":"1"}),"instanceName":"1"}),"instanceName":"1"});
            var Q85;
            Q85=makeQuery(id+"F26.opPattern","COPY",BODY,{"derivedFrom":makeQuery(id+"F17.opPattern","COPY",BODY,{"derivedFrom":makeQuery(id+"F15.opPattern","COPY",BODY,{"derivedFrom":makeQuery(id+"F12.opPattern","COPY",BODY,{"derivedFrom":makeQuery(id+"F6.opPattern","COPY",BODY,{"derivedFrom":makeQuery(id+"F5.opPattern","COPY",BODY,{"derivedFrom":makeQuery(id+"F4.opPattern","COPY",BODY,{"derivedFrom":makeQuery(id+"F2.opPattern","COPY",BODY,{"derivedFrom":makeQuery(id+"F1.opExtrude","SWEPT_BODY",BODY,{"disambiguationData":[OSD([sQuery(id+"F0.wireOp",EDGE,"E0.bottom"),sQuery(id+"F0.wireOp",EDGE,"E0.top"),sQuery(id+"F0.wireOp",EDGE,"E0.left"),sQuery(id+"F0.wireOp",EDGE,"E0.right")])]}),"instanceName":"1"}),"instanceName":"1"}),"instanceName":"1"}),"instanceName":"1"}),"instanceName":"1"}),"instanceName":"1"}),"instanceName":"1"}),"instanceName":"1"});
            var Q86;
            Q86=makeQuery(id+"F45.opPattern","COPY",BODY,{"derivedFrom":makeQuery(id+"F40.opPattern","COPY",BODY,{"derivedFrom":makeQuery(id+"F19.opPattern","COPY",BODY,{"derivedFrom":makeQuery(id+"F17.opPattern","COPY",BODY,{"derivedFrom":makeQuery(id+"F13.opPattern","COPY",BODY,{"derivedFrom":makeQuery(id+"F5.opPattern","COPY",BODY,{"derivedFrom":makeQuery(id+"F4.opPattern","COPY",BODY,{"derivedFrom":makeQuery(id+"F1.opExtrude","SWEPT_BODY",BODY,{"disambiguationData":[OSD([sQuery(id+"F0.wireOp",EDGE,"E0.bottom"),sQuery(id+"F0.wireOp",EDGE,"E0.top"),sQuery(id+"F0.wireOp",EDGE,"E0.left"),sQuery(id+"F0.wireOp",EDGE,"E0.right")])]}),"instanceName":"1"}),"instanceName":"1"}),"instanceName":"1"}),"instanceName":"1"}),"instanceName":"1"}),"instanceName":"1"}),"instanceName":"1"});
            var Q87;
            Q87=makeQuery(id+"F15.opPattern","COPY",BODY,{"derivedFrom":makeQuery(id+"F12.opPattern","COPY",BODY,{"derivedFrom":makeQuery(id+"F6.opPattern","COPY",BODY,{"derivedFrom":makeQuery(id+"F5.opPattern","COPY",BODY,{"derivedFrom":makeQuery(id+"F4.opPattern","COPY",BODY,{"derivedFrom":makeQuery(id+"F2.opPattern","COPY",BODY,{"derivedFrom":makeQuery(id+"F1.opExtrude","SWEPT_BODY",BODY,{"disambiguationData":[OSD([sQuery(id+"F0.wireOp",EDGE,"E0.bottom"),sQuery(id+"F0.wireOp",EDGE,"E0.top"),sQuery(id+"F0.wireOp",EDGE,"E0.left"),sQuery(id+"F0.wireOp",EDGE,"E0.right")])]}),"instanceName":"1"}),"instanceName":"1"}),"instanceName":"1"}),"instanceName":"1"}),"instanceName":"1"}),"instanceName":"1"});
            var Q88;
            Q88=makeQuery(id+"F45.opPattern","COPY",BODY,{"derivedFrom":makeQuery(id+"F40.opPattern","COPY",BODY,{"derivedFrom":makeQuery(id+"F21.opPattern","COPY",BODY,{"derivedFrom":makeQuery(id+"F19.opPattern","COPY",BODY,{"derivedFrom":makeQuery(id+"F17.opPattern","COPY",BODY,{"derivedFrom":makeQuery(id+"F12.opPattern","COPY",BODY,{"derivedFrom":makeQuery(id+"F6.opPattern","COPY",BODY,{"derivedFrom":makeQuery(id+"F5.opPattern","COPY",BODY,{"derivedFrom":makeQuery(id+"F4.opPattern","COPY",BODY,{"derivedFrom":makeQuery(id+"F2.opPattern","COPY",BODY,{"derivedFrom":makeQuery(id+"F1.opExtrude","SWEPT_BODY",BODY,{"disambiguationData":[OSD([sQuery(id+"F0.wireOp",EDGE,"E0.bottom"),sQuery(id+"F0.wireOp",EDGE,"E0.top"),sQuery(id+"F0.wireOp",EDGE,"E0.left"),sQuery(id+"F0.wireOp",EDGE,"E0.right")])]}),"instanceName":"1"}),"instanceName":"1"}),"instanceName":"1"}),"instanceName":"1"}),"instanceName":"1"}),"instanceName":"1"}),"instanceName":"1"}),"instanceName":"1"}),"instanceName":"1"}),"instanceName":"1"});
            var Q89;
            Q89=makeQuery(id+"F19.opPattern","COPY",BODY,{"derivedFrom":makeQuery(id+"F17.opPattern","COPY",BODY,{"derivedFrom":makeQuery(id+"F15.opPattern","COPY",BODY,{"derivedFrom":makeQuery(id+"F12.opPattern","COPY",BODY,{"derivedFrom":makeQuery(id+"F6.opPattern","COPY",BODY,{"derivedFrom":makeQuery(id+"F5.opPattern","COPY",BODY,{"derivedFrom":makeQuery(id+"F4.opPattern","COPY",BODY,{"derivedFrom":makeQuery(id+"F2.opPattern","COPY",BODY,{"derivedFrom":makeQuery(id+"F1.opExtrude","SWEPT_BODY",BODY,{"disambiguationData":[OSD([sQuery(id+"F0.wireOp",EDGE,"E0.bottom"),sQuery(id+"F0.wireOp",EDGE,"E0.top"),sQuery(id+"F0.wireOp",EDGE,"E0.left"),sQuery(id+"F0.wireOp",EDGE,"E0.right")])]}),"instanceName":"1"}),"instanceName":"1"}),"instanceName":"1"}),"instanceName":"1"}),"instanceName":"1"}),"instanceName":"1"}),"instanceName":"1"}),"instanceName":"1"});
            var Q90;
            Q90=makeQuery(id+"F35.opPattern","COPY",BODY,{"derivedFrom":makeQuery(id+"F34.opPattern","COPY",BODY,{"derivedFrom":makeQuery(id+"F31.opPattern","COPY",BODY,{"derivedFrom":makeQuery(id+"F4.opPattern","COPY",BODY,{"derivedFrom":makeQuery(id+"F1.opExtrude","SWEPT_BODY",BODY,{"disambiguationData":[OSD([sQuery(id+"F0.wireOp",EDGE,"E0.bottom"),sQuery(id+"F0.wireOp",EDGE,"E0.top"),sQuery(id+"F0.wireOp",EDGE,"E0.left"),sQuery(id+"F0.wireOp",EDGE,"E0.right")])]}),"instanceName":"1"}),"instanceName":"1"}),"instanceName":"1"}),"instanceName":"1"});
            var Q91;
            Q91=makeQuery(id+"F29.opPattern","COPY",BODY,{"derivedFrom":makeQuery(id+"F26.opPattern","COPY",BODY,{"derivedFrom":makeQuery(id+"F19.opPattern","COPY",BODY,{"derivedFrom":makeQuery(id+"F17.opPattern","COPY",BODY,{"derivedFrom":makeQuery(id+"F13.opPattern","COPY",BODY,{"derivedFrom":makeQuery(id+"F5.opPattern","COPY",BODY,{"derivedFrom":makeQuery(id+"F4.opPattern","COPY",BODY,{"derivedFrom":makeQuery(id+"F1.opExtrude","SWEPT_BODY",BODY,{"disambiguationData":[OSD([sQuery(id+"F0.wireOp",EDGE,"E0.bottom"),sQuery(id+"F0.wireOp",EDGE,"E0.top"),sQuery(id+"F0.wireOp",EDGE,"E0.left"),sQuery(id+"F0.wireOp",EDGE,"E0.right")])]}),"instanceName":"1"}),"instanceName":"1"}),"instanceName":"1"}),"instanceName":"1"}),"instanceName":"1"}),"instanceName":"1"}),"instanceName":"1"});
            var Q92;
            Q92=makeQuery(id+"F45.opPattern","COPY",BODY,{"derivedFrom":makeQuery(id+"F40.opPattern","COPY",BODY,{"derivedFrom":makeQuery(id+"F23.opPattern","COPY",BODY,{"derivedFrom":makeQuery(id+"F19.opPattern","COPY",BODY,{"derivedFrom":makeQuery(id+"F15.opPattern","COPY",BODY,{"derivedFrom":makeQuery(id+"F12.opPattern","COPY",BODY,{"derivedFrom":makeQuery(id+"F6.opPattern","COPY",BODY,{"derivedFrom":makeQuery(id+"F5.opPattern","COPY",BODY,{"derivedFrom":makeQuery(id+"F4.opPattern","COPY",BODY,{"derivedFrom":makeQuery(id+"F2.opPattern","COPY",BODY,{"derivedFrom":makeQuery(id+"F1.opExtrude","SWEPT_BODY",BODY,{"disambiguationData":[OSD([sQuery(id+"F0.wireOp",EDGE,"E0.bottom"),sQuery(id+"F0.wireOp",EDGE,"E0.top"),sQuery(id+"F0.wireOp",EDGE,"E0.left"),sQuery(id+"F0.wireOp",EDGE,"E0.right")])]}),"instanceName":"1"}),"instanceName":"1"}),"instanceName":"1"}),"instanceName":"1"}),"instanceName":"1"}),"instanceName":"1"}),"instanceName":"1"}),"instanceName":"1"}),"instanceName":"1"}),"instanceName":"1"});
            var Q93;
            Q93=makeQuery(id+"F17.opPattern","COPY",BODY,{"derivedFrom":makeQuery(id+"F13.opPattern","COPY",BODY,{"derivedFrom":makeQuery(id+"F5.opPattern","COPY",BODY,{"derivedFrom":makeQuery(id+"F4.opPattern","COPY",BODY,{"derivedFrom":makeQuery(id+"F1.opExtrude","SWEPT_BODY",BODY,{"disambiguationData":[OSD([sQuery(id+"F0.wireOp",EDGE,"E0.bottom"),sQuery(id+"F0.wireOp",EDGE,"E0.top"),sQuery(id+"F0.wireOp",EDGE,"E0.left"),sQuery(id+"F0.wireOp",EDGE,"E0.right")])]}),"instanceName":"1"}),"instanceName":"1"}),"instanceName":"1"}),"instanceName":"1"});
            var Q94;
            Q94=makeQuery(id+"F29.opPattern","COPY",BODY,{"derivedFrom":makeQuery(id+"F28.opPattern","COPY",BODY,{"derivedFrom":makeQuery(id+"F23.opPattern","COPY",BODY,{"derivedFrom":makeQuery(id+"F19.opPattern","COPY",BODY,{"derivedFrom":makeQuery(id+"F17.opPattern","COPY",BODY,{"derivedFrom":makeQuery(id+"F15.opPattern","COPY",BODY,{"derivedFrom":makeQuery(id+"F12.opPattern","COPY",BODY,{"derivedFrom":makeQuery(id+"F6.opPattern","COPY",BODY,{"derivedFrom":makeQuery(id+"F5.opPattern","COPY",BODY,{"derivedFrom":makeQuery(id+"F4.opPattern","COPY",BODY,{"derivedFrom":makeQuery(id+"F2.opPattern","COPY",BODY,{"derivedFrom":makeQuery(id+"F1.opExtrude","SWEPT_BODY",BODY,{"disambiguationData":[OSD([sQuery(id+"F0.wireOp",EDGE,"E0.bottom"),sQuery(id+"F0.wireOp",EDGE,"E0.top"),sQuery(id+"F0.wireOp",EDGE,"E0.left"),sQuery(id+"F0.wireOp",EDGE,"E0.right")])]}),"instanceName":"1"}),"instanceName":"1"}),"instanceName":"1"}),"instanceName":"1"}),"instanceName":"1"}),"instanceName":"1"}),"instanceName":"1"}),"instanceName":"1"}),"instanceName":"1"}),"instanceName":"1"}),"instanceName":"1"});
            var Q95;
            Q95=makeQuery(id+"F31.opPattern","COPY",BODY,{"derivedFrom":makeQuery(id+"F2.opPattern","COPY",BODY,{"derivedFrom":makeQuery(id+"F1.opExtrude","SWEPT_BODY",BODY,{"disambiguationData":[OSD([sQuery(id+"F0.wireOp",EDGE,"E0.bottom"),sQuery(id+"F0.wireOp",EDGE,"E0.top"),sQuery(id+"F0.wireOp",EDGE,"E0.left"),sQuery(id+"F0.wireOp",EDGE,"E0.right")])]}),"instanceName":"1"}),"instanceName":"1"});
            var Q96;
            Q96=makeQuery(id+"F45.opPattern","COPY",BODY,{"derivedFrom":makeQuery(id+"F40.opPattern","COPY",BODY,{"derivedFrom":makeQuery(id+"F23.opPattern","COPY",BODY,{"derivedFrom":makeQuery(id+"F19.opPattern","COPY",BODY,{"derivedFrom":makeQuery(id+"F17.opPattern","COPY",BODY,{"derivedFrom":makeQuery(id+"F13.opPattern","COPY",BODY,{"derivedFrom":makeQuery(id+"F5.opPattern","COPY",BODY,{"derivedFrom":makeQuery(id+"F4.opPattern","COPY",BODY,{"derivedFrom":makeQuery(id+"F1.opExtrude","SWEPT_BODY",BODY,{"disambiguationData":[OSD([sQuery(id+"F0.wireOp",EDGE,"E0.bottom"),sQuery(id+"F0.wireOp",EDGE,"E0.top"),sQuery(id+"F0.wireOp",EDGE,"E0.left"),sQuery(id+"F0.wireOp",EDGE,"E0.right")])]}),"instanceName":"1"}),"instanceName":"1"}),"instanceName":"1"}),"instanceName":"1"}),"instanceName":"1"}),"instanceName":"1"}),"instanceName":"1"}),"instanceName":"1"});
            var Q97;
            Q97=makeQuery(id+"F17.opPattern","COPY",BODY,{"derivedFrom":makeQuery(id+"F12.opPattern","COPY",BODY,{"derivedFrom":makeQuery(id+"F6.opPattern","COPY",BODY,{"derivedFrom":makeQuery(id+"F5.opPattern","COPY",BODY,{"derivedFrom":makeQuery(id+"F4.opPattern","COPY",BODY,{"derivedFrom":makeQuery(id+"F2.opPattern","COPY",BODY,{"derivedFrom":makeQuery(id+"F1.opExtrude","SWEPT_BODY",BODY,{"disambiguationData":[OSD([sQuery(id+"F0.wireOp",EDGE,"E0.bottom"),sQuery(id+"F0.wireOp",EDGE,"E0.top"),sQuery(id+"F0.wireOp",EDGE,"E0.left"),sQuery(id+"F0.wireOp",EDGE,"E0.right")])]}),"instanceName":"1"}),"instanceName":"1"}),"instanceName":"1"}),"instanceName":"1"}),"instanceName":"1"}),"instanceName":"1"});
            var Q98;
            Q98=makeQuery(id+"F40.opPattern","COPY",BODY,{"derivedFrom":makeQuery(id+"F19.opPattern","COPY",BODY,{"derivedFrom":makeQuery(id+"F13.opPattern","COPY",BODY,{"derivedFrom":makeQuery(id+"F5.opPattern","COPY",BODY,{"derivedFrom":makeQuery(id+"F4.opPattern","COPY",BODY,{"derivedFrom":makeQuery(id+"F1.opExtrude","SWEPT_BODY",BODY,{"disambiguationData":[OSD([sQuery(id+"F0.wireOp",EDGE,"E0.bottom"),sQuery(id+"F0.wireOp",EDGE,"E0.top"),sQuery(id+"F0.wireOp",EDGE,"E0.left"),sQuery(id+"F0.wireOp",EDGE,"E0.right")])]}),"instanceName":"1"}),"instanceName":"1"}),"instanceName":"1"}),"instanceName":"1"}),"instanceName":"1"});
            var Q99;
            Q99=makeQuery(id+"F13.opPattern","COPY",BODY,{"derivedFrom":makeQuery(id+"F12.opPattern","COPY",BODY,{"derivedFrom":makeQuery(id+"F6.opPattern","COPY",BODY,{"derivedFrom":makeQuery(id+"F5.opPattern","COPY",BODY,{"derivedFrom":makeQuery(id+"F2.opPattern","COPY",BODY,{"derivedFrom":makeQuery(id+"F1.opExtrude","SWEPT_BODY",BODY,{"disambiguationData":[OSD([sQuery(id+"F0.wireOp",EDGE,"E0.bottom"),sQuery(id+"F0.wireOp",EDGE,"E0.top"),sQuery(id+"F0.wireOp",EDGE,"E0.left"),sQuery(id+"F0.wireOp",EDGE,"E0.right")])]}),"instanceName":"1"}),"instanceName":"1"}),"instanceName":"1"}),"instanceName":"1"}),"instanceName":"1"});
            var Q100;
            Q100=makeQuery(id+"F28.opPattern","COPY",BODY,{"derivedFrom":makeQuery(id+"F19.opPattern","COPY",BODY,{"derivedFrom":makeQuery(id+"F17.opPattern","COPY",BODY,{"derivedFrom":makeQuery(id+"F15.opPattern","COPY",BODY,{"derivedFrom":makeQuery(id+"F12.opPattern","COPY",BODY,{"derivedFrom":makeQuery(id+"F6.opPattern","COPY",BODY,{"derivedFrom":makeQuery(id+"F5.opPattern","COPY",BODY,{"derivedFrom":makeQuery(id+"F4.opPattern","COPY",BODY,{"derivedFrom":makeQuery(id+"F2.opPattern","COPY",BODY,{"derivedFrom":makeQuery(id+"F1.opExtrude","SWEPT_BODY",BODY,{"disambiguationData":[OSD([sQuery(id+"F0.wireOp",EDGE,"E0.bottom"),sQuery(id+"F0.wireOp",EDGE,"E0.top"),sQuery(id+"F0.wireOp",EDGE,"E0.left"),sQuery(id+"F0.wireOp",EDGE,"E0.right")])]}),"instanceName":"1"}),"instanceName":"1"}),"instanceName":"1"}),"instanceName":"1"}),"instanceName":"1"}),"instanceName":"1"}),"instanceName":"1"}),"instanceName":"1"}),"instanceName":"1"});
            var Q101;
            Q101=makeQuery(id+"F40.opPattern","COPY",BODY,{"derivedFrom":makeQuery(id+"F19.opPattern","COPY",BODY,{"derivedFrom":makeQuery(id+"F17.opPattern","COPY",BODY,{"derivedFrom":makeQuery(id+"F15.opPattern","COPY",BODY,{"derivedFrom":makeQuery(id+"F12.opPattern","COPY",BODY,{"derivedFrom":makeQuery(id+"F6.opPattern","COPY",BODY,{"derivedFrom":makeQuery(id+"F5.opPattern","COPY",BODY,{"derivedFrom":makeQuery(id+"F4.opPattern","COPY",BODY,{"derivedFrom":makeQuery(id+"F2.opPattern","COPY",BODY,{"derivedFrom":makeQuery(id+"F1.opExtrude","SWEPT_BODY",BODY,{"disambiguationData":[OSD([sQuery(id+"F0.wireOp",EDGE,"E0.bottom"),sQuery(id+"F0.wireOp",EDGE,"E0.top"),sQuery(id+"F0.wireOp",EDGE,"E0.left"),sQuery(id+"F0.wireOp",EDGE,"E0.right")])]}),"instanceName":"1"}),"instanceName":"1"}),"instanceName":"1"}),"instanceName":"1"}),"instanceName":"1"}),"instanceName":"1"}),"instanceName":"1"}),"instanceName":"1"}),"instanceName":"1"});
            var Q102;
            Q102=makeQuery(id+"F23.opPattern","COPY",BODY,{"derivedFrom":makeQuery(id+"F19.opPattern","COPY",BODY,{"derivedFrom":makeQuery(id+"F6.opPattern","COPY",BODY,{"derivedFrom":makeQuery(id+"F5.opPattern","COPY",BODY,{"derivedFrom":makeQuery(id+"F4.opPattern","COPY",BODY,{"derivedFrom":makeQuery(id+"F2.opPattern","COPY",BODY,{"derivedFrom":makeQuery(id+"F1.opExtrude","SWEPT_BODY",BODY,{"disambiguationData":[OSD([sQuery(id+"F0.wireOp",EDGE,"E0.bottom"),sQuery(id+"F0.wireOp",EDGE,"E0.top"),sQuery(id+"F0.wireOp",EDGE,"E0.left"),sQuery(id+"F0.wireOp",EDGE,"E0.right")])]}),"instanceName":"1"}),"instanceName":"1"}),"instanceName":"1"}),"instanceName":"1"}),"instanceName":"1"}),"instanceName":"1"});
            var Q103;
            Q103=makeQuery(id+"F45.opPattern","COPY",BODY,{"derivedFrom":makeQuery(id+"F40.opPattern","COPY",BODY,{"derivedFrom":makeQuery(id+"F29.opPattern","COPY",BODY,{"derivedFrom":makeQuery(id+"F19.opPattern","COPY",BODY,{"derivedFrom":makeQuery(id+"F17.opPattern","COPY",BODY,{"derivedFrom":makeQuery(id+"F15.opPattern","COPY",BODY,{"derivedFrom":makeQuery(id+"F12.opPattern","COPY",BODY,{"derivedFrom":makeQuery(id+"F6.opPattern","COPY",BODY,{"derivedFrom":makeQuery(id+"F5.opPattern","COPY",BODY,{"derivedFrom":makeQuery(id+"F4.opPattern","COPY",BODY,{"derivedFrom":makeQuery(id+"F2.opPattern","COPY",BODY,{"derivedFrom":makeQuery(id+"F1.opExtrude","SWEPT_BODY",BODY,{"disambiguationData":[OSD([sQuery(id+"F0.wireOp",EDGE,"E0.bottom"),sQuery(id+"F0.wireOp",EDGE,"E0.top"),sQuery(id+"F0.wireOp",EDGE,"E0.left"),sQuery(id+"F0.wireOp",EDGE,"E0.right")])]}),"instanceName":"1"}),"instanceName":"1"}),"instanceName":"1"}),"instanceName":"1"}),"instanceName":"1"}),"instanceName":"1"}),"instanceName":"1"}),"instanceName":"1"}),"instanceName":"1"}),"instanceName":"1"}),"instanceName":"1"});
            var Q104;
            Q104=makeQuery(id+"F40.opPattern","COPY",BODY,{"derivedFrom":makeQuery(id+"F19.opPattern","COPY",BODY,{"derivedFrom":makeQuery(id+"F17.opPattern","COPY",BODY,{"derivedFrom":makeQuery(id+"F13.opPattern","COPY",BODY,{"derivedFrom":makeQuery(id+"F5.opPattern","COPY",BODY,{"derivedFrom":makeQuery(id+"F4.opPattern","COPY",BODY,{"derivedFrom":makeQuery(id+"F1.opExtrude","SWEPT_BODY",BODY,{"disambiguationData":[OSD([sQuery(id+"F0.wireOp",EDGE,"E0.bottom"),sQuery(id+"F0.wireOp",EDGE,"E0.top"),sQuery(id+"F0.wireOp",EDGE,"E0.left"),sQuery(id+"F0.wireOp",EDGE,"E0.right")])]}),"instanceName":"1"}),"instanceName":"1"}),"instanceName":"1"}),"instanceName":"1"}),"instanceName":"1"}),"instanceName":"1"});
            var Q105;
            Q105=makeQuery(id+"F40.opPattern","COPY",BODY,{"derivedFrom":makeQuery(id+"F21.opPattern","COPY",BODY,{"derivedFrom":makeQuery(id+"F19.opPattern","COPY",BODY,{"derivedFrom":makeQuery(id+"F17.opPattern","COPY",BODY,{"derivedFrom":makeQuery(id+"F5.opPattern","COPY",BODY,{"derivedFrom":makeQuery(id+"F4.opPattern","COPY",BODY,{"derivedFrom":makeQuery(id+"F2.opPattern","COPY",BODY,{"derivedFrom":makeQuery(id+"F1.opExtrude","SWEPT_BODY",BODY,{"disambiguationData":[OSD([sQuery(id+"F0.wireOp",EDGE,"E0.bottom"),sQuery(id+"F0.wireOp",EDGE,"E0.top"),sQuery(id+"F0.wireOp",EDGE,"E0.left"),sQuery(id+"F0.wireOp",EDGE,"E0.right")])]}),"instanceName":"1"}),"instanceName":"1"}),"instanceName":"1"}),"instanceName":"1"}),"instanceName":"1"}),"instanceName":"1"}),"instanceName":"1"});
            var Q106;
            Q106=makeQuery(id+"F26.opPattern","COPY",BODY,{"derivedFrom":makeQuery(id+"F19.opPattern","COPY",BODY,{"derivedFrom":makeQuery(id+"F6.opPattern","COPY",BODY,{"derivedFrom":makeQuery(id+"F5.opPattern","COPY",BODY,{"derivedFrom":makeQuery(id+"F4.opPattern","COPY",BODY,{"derivedFrom":makeQuery(id+"F1.opExtrude","SWEPT_BODY",BODY,{"disambiguationData":[OSD([sQuery(id+"F0.wireOp",EDGE,"E0.bottom"),sQuery(id+"F0.wireOp",EDGE,"E0.top"),sQuery(id+"F0.wireOp",EDGE,"E0.left"),sQuery(id+"F0.wireOp",EDGE,"E0.right")])]}),"instanceName":"1"}),"instanceName":"1"}),"instanceName":"1"}),"instanceName":"1"}),"instanceName":"1"});
            var Q107;
            Q107=makeQuery(id+"F23.opPattern","COPY",BODY,{"derivedFrom":makeQuery(id+"F21.opPattern","COPY",BODY,{"derivedFrom":makeQuery(id+"F19.opPattern","COPY",BODY,{"derivedFrom":makeQuery(id+"F17.opPattern","COPY",BODY,{"derivedFrom":makeQuery(id+"F12.opPattern","COPY",BODY,{"derivedFrom":makeQuery(id+"F6.opPattern","COPY",BODY,{"derivedFrom":makeQuery(id+"F5.opPattern","COPY",BODY,{"derivedFrom":makeQuery(id+"F4.opPattern","COPY",BODY,{"derivedFrom":makeQuery(id+"F2.opPattern","COPY",BODY,{"derivedFrom":makeQuery(id+"F1.opExtrude","SWEPT_BODY",BODY,{"disambiguationData":[OSD([sQuery(id+"F0.wireOp",EDGE,"E0.bottom"),sQuery(id+"F0.wireOp",EDGE,"E0.top"),sQuery(id+"F0.wireOp",EDGE,"E0.left"),sQuery(id+"F0.wireOp",EDGE,"E0.right")])]}),"instanceName":"1"}),"instanceName":"1"}),"instanceName":"1"}),"instanceName":"1"}),"instanceName":"1"}),"instanceName":"1"}),"instanceName":"1"}),"instanceName":"1"}),"instanceName":"1"});
            var Q108;
            Q108=makeQuery(id+"F26.opPattern","COPY",BODY,{"derivedFrom":makeQuery(id+"F21.opPattern","COPY",BODY,{"derivedFrom":makeQuery(id+"F19.opPattern","COPY",BODY,{"derivedFrom":makeQuery(id+"F6.opPattern","COPY",BODY,{"derivedFrom":makeQuery(id+"F5.opPattern","COPY",BODY,{"derivedFrom":makeQuery(id+"F4.opPattern","COPY",BODY,{"derivedFrom":makeQuery(id+"F2.opPattern","COPY",BODY,{"derivedFrom":makeQuery(id+"F1.opExtrude","SWEPT_BODY",BODY,{"disambiguationData":[OSD([sQuery(id+"F0.wireOp",EDGE,"E0.bottom"),sQuery(id+"F0.wireOp",EDGE,"E0.top"),sQuery(id+"F0.wireOp",EDGE,"E0.left"),sQuery(id+"F0.wireOp",EDGE,"E0.right")])]}),"instanceName":"1"}),"instanceName":"1"}),"instanceName":"1"}),"instanceName":"1"}),"instanceName":"1"}),"instanceName":"1"}),"instanceName":"1"});
            var Q109;
            Q109=makeQuery(id+"F40.opPattern","COPY",BODY,{"derivedFrom":makeQuery(id+"F18.opPattern","COPY",BODY,{"derivedFrom":makeQuery(id+"F17.opPattern","COPY",BODY,{"derivedFrom":makeQuery(id+"F15.opPattern","COPY",BODY,{"derivedFrom":makeQuery(id+"F12.opPattern","COPY",BODY,{"derivedFrom":makeQuery(id+"F6.opPattern","COPY",BODY,{"derivedFrom":makeQuery(id+"F5.opPattern","COPY",BODY,{"derivedFrom":makeQuery(id+"F4.opPattern","COPY",BODY,{"derivedFrom":makeQuery(id+"F2.opPattern","COPY",BODY,{"derivedFrom":makeQuery(id+"F1.opExtrude","SWEPT_BODY",BODY,{"disambiguationData":[OSD([sQuery(id+"F0.wireOp",EDGE,"E0.bottom"),sQuery(id+"F0.wireOp",EDGE,"E0.top"),sQuery(id+"F0.wireOp",EDGE,"E0.left"),sQuery(id+"F0.wireOp",EDGE,"E0.right")])]}),"instanceName":"1"}),"instanceName":"1"}),"instanceName":"1"}),"instanceName":"1"}),"instanceName":"1"}),"instanceName":"1"}),"instanceName":"1"}),"instanceName":"1"}),"instanceName":"1"});
            var Q110;
            Q110=makeQuery(id+"F17.opPattern","COPY",BODY,{"derivedFrom":makeQuery(id+"F15.opPattern","COPY",BODY,{"derivedFrom":makeQuery(id+"F12.opPattern","COPY",BODY,{"derivedFrom":makeQuery(id+"F6.opPattern","COPY",BODY,{"derivedFrom":makeQuery(id+"F5.opPattern","COPY",BODY,{"derivedFrom":makeQuery(id+"F4.opPattern","COPY",BODY,{"derivedFrom":makeQuery(id+"F2.opPattern","COPY",BODY,{"derivedFrom":makeQuery(id+"F1.opExtrude","SWEPT_BODY",BODY,{"disambiguationData":[OSD([sQuery(id+"F0.wireOp",EDGE,"E0.bottom"),sQuery(id+"F0.wireOp",EDGE,"E0.top"),sQuery(id+"F0.wireOp",EDGE,"E0.left"),sQuery(id+"F0.wireOp",EDGE,"E0.right")])]}),"instanceName":"1"}),"instanceName":"1"}),"instanceName":"1"}),"instanceName":"1"}),"instanceName":"1"}),"instanceName":"1"}),"instanceName":"1"});
            var Q111;
            Q111=makeQuery(id+"F40.opPattern","COPY",BODY,{"derivedFrom":makeQuery(id+"F19.opPattern","COPY",BODY,{"derivedFrom":makeQuery(id+"F12.opPattern","COPY",BODY,{"derivedFrom":makeQuery(id+"F6.opPattern","COPY",BODY,{"derivedFrom":makeQuery(id+"F5.opPattern","COPY",BODY,{"derivedFrom":makeQuery(id+"F4.opPattern","COPY",BODY,{"derivedFrom":makeQuery(id+"F1.opExtrude","SWEPT_BODY",BODY,{"disambiguationData":[OSD([sQuery(id+"F0.wireOp",EDGE,"E0.bottom"),sQuery(id+"F0.wireOp",EDGE,"E0.top"),sQuery(id+"F0.wireOp",EDGE,"E0.left"),sQuery(id+"F0.wireOp",EDGE,"E0.right")])]}),"instanceName":"1"}),"instanceName":"1"}),"instanceName":"1"}),"instanceName":"1"}),"instanceName":"1"}),"instanceName":"1"});
            var Q112;
            Q112=makeQuery(id+"F40.opPattern","COPY",BODY,{"derivedFrom":makeQuery(id+"F26.opPattern","COPY",BODY,{"derivedFrom":makeQuery(id+"F18.opPattern","COPY",BODY,{"derivedFrom":makeQuery(id+"F17.opPattern","COPY",BODY,{"derivedFrom":makeQuery(id+"F8.opPattern","COPY",BODY,{"derivedFrom":makeQuery(id+"F5.opPattern","COPY",BODY,{"derivedFrom":makeQuery(id+"F4.opPattern","COPY",BODY,{"derivedFrom":makeQuery(id+"F1.opExtrude","SWEPT_BODY",BODY,{"disambiguationData":[OSD([sQuery(id+"F0.wireOp",EDGE,"E0.bottom"),sQuery(id+"F0.wireOp",EDGE,"E0.top"),sQuery(id+"F0.wireOp",EDGE,"E0.left"),sQuery(id+"F0.wireOp",EDGE,"E0.right")])]}),"instanceName":"1"}),"instanceName":"1"}),"instanceName":"1"}),"instanceName":"1"}),"instanceName":"1"}),"instanceName":"1"}),"instanceName":"1"});
            var Q113;
            Q113=makeQuery(id+"F6.opPattern","COPY",BODY,{"derivedFrom":makeQuery(id+"F4.opPattern","COPY",BODY,{"derivedFrom":makeQuery(id+"F1.opExtrude","SWEPT_BODY",BODY,{"disambiguationData":[OSD([sQuery(id+"F0.wireOp",EDGE,"E0.bottom"),sQuery(id+"F0.wireOp",EDGE,"E0.top"),sQuery(id+"F0.wireOp",EDGE,"E0.left"),sQuery(id+"F0.wireOp",EDGE,"E0.right")])]}),"instanceName":"1"}),"instanceName":"1"});
            var Q114;
            Q114=makeQuery(id+"F26.opPattern","COPY",BODY,{"derivedFrom":makeQuery(id+"F17.opPattern","COPY",BODY,{"derivedFrom":makeQuery(id+"F8.opPattern","COPY",BODY,{"derivedFrom":makeQuery(id+"F5.opPattern","COPY",BODY,{"derivedFrom":makeQuery(id+"F4.opPattern","COPY",BODY,{"derivedFrom":makeQuery(id+"F1.opExtrude","SWEPT_BODY",BODY,{"disambiguationData":[OSD([sQuery(id+"F0.wireOp",EDGE,"E0.bottom"),sQuery(id+"F0.wireOp",EDGE,"E0.top"),sQuery(id+"F0.wireOp",EDGE,"E0.left"),sQuery(id+"F0.wireOp",EDGE,"E0.right")])]}),"instanceName":"1"}),"instanceName":"1"}),"instanceName":"1"}),"instanceName":"1"}),"instanceName":"1"});
            var Q115;
            Q115=makeQuery(id+"F40.opPattern","COPY",BODY,{"derivedFrom":makeQuery(id+"F19.opPattern","COPY",BODY,{"derivedFrom":makeQuery(id+"F17.opPattern","COPY",BODY,{"derivedFrom":makeQuery(id+"F5.opPattern","COPY",BODY,{"derivedFrom":makeQuery(id+"F4.opPattern","COPY",BODY,{"derivedFrom":makeQuery(id+"F2.opPattern","COPY",BODY,{"derivedFrom":makeQuery(id+"F1.opExtrude","SWEPT_BODY",BODY,{"disambiguationData":[OSD([sQuery(id+"F0.wireOp",EDGE,"E0.bottom"),sQuery(id+"F0.wireOp",EDGE,"E0.top"),sQuery(id+"F0.wireOp",EDGE,"E0.left"),sQuery(id+"F0.wireOp",EDGE,"E0.right")])]}),"instanceName":"1"}),"instanceName":"1"}),"instanceName":"1"}),"instanceName":"1"}),"instanceName":"1"}),"instanceName":"1"});
            var Q116;
            Q116=makeQuery(id+"F21.opPattern","COPY",BODY,{"derivedFrom":makeQuery(id+"F19.opPattern","COPY",BODY,{"derivedFrom":makeQuery(id+"F17.opPattern","COPY",BODY,{"derivedFrom":makeQuery(id+"F6.opPattern","COPY",BODY,{"derivedFrom":makeQuery(id+"F5.opPattern","COPY",BODY,{"derivedFrom":makeQuery(id+"F4.opPattern","COPY",BODY,{"derivedFrom":makeQuery(id+"F1.opExtrude","SWEPT_BODY",BODY,{"disambiguationData":[OSD([sQuery(id+"F0.wireOp",EDGE,"E0.bottom"),sQuery(id+"F0.wireOp",EDGE,"E0.top"),sQuery(id+"F0.wireOp",EDGE,"E0.left"),sQuery(id+"F0.wireOp",EDGE,"E0.right")])]}),"instanceName":"1"}),"instanceName":"1"}),"instanceName":"1"}),"instanceName":"1"}),"instanceName":"1"}),"instanceName":"1"});
            var Q117;
            Q117=makeQuery(id+"F17.opPattern","COPY",BODY,{"derivedFrom":makeQuery(id+"F6.opPattern","COPY",BODY,{"derivedFrom":makeQuery(id+"F5.opPattern","COPY",BODY,{"derivedFrom":makeQuery(id+"F4.opPattern","COPY",BODY,{"derivedFrom":makeQuery(id+"F2.opPattern","COPY",BODY,{"derivedFrom":makeQuery(id+"F1.opExtrude","SWEPT_BODY",BODY,{"disambiguationData":[OSD([sQuery(id+"F0.wireOp",EDGE,"E0.bottom"),sQuery(id+"F0.wireOp",EDGE,"E0.top"),sQuery(id+"F0.wireOp",EDGE,"E0.left"),sQuery(id+"F0.wireOp",EDGE,"E0.right")])]}),"instanceName":"1"}),"instanceName":"1"}),"instanceName":"1"}),"instanceName":"1"}),"instanceName":"1"});
            var Q118;
            Q118=makeQuery(id+"F19.opPattern","COPY",BODY,{"derivedFrom":makeQuery(id+"F5.opPattern","COPY",BODY,{"derivedFrom":makeQuery(id+"F4.opPattern","COPY",BODY,{"derivedFrom":makeQuery(id+"F1.opExtrude","SWEPT_BODY",BODY,{"disambiguationData":[OSD([sQuery(id+"F0.wireOp",EDGE,"E0.bottom"),sQuery(id+"F0.wireOp",EDGE,"E0.top"),sQuery(id+"F0.wireOp",EDGE,"E0.left"),sQuery(id+"F0.wireOp",EDGE,"E0.right")])]}),"instanceName":"1"}),"instanceName":"1"}),"instanceName":"1"});
            var Q119;
            Q119=makeQuery(id+"F19.opPattern","COPY",BODY,{"derivedFrom":makeQuery(id+"F17.opPattern","COPY",BODY,{"derivedFrom":makeQuery(id+"F12.opPattern","COPY",BODY,{"derivedFrom":makeQuery(id+"F6.opPattern","COPY",BODY,{"derivedFrom":makeQuery(id+"F5.opPattern","COPY",BODY,{"derivedFrom":makeQuery(id+"F4.opPattern","COPY",BODY,{"derivedFrom":makeQuery(id+"F1.opExtrude","SWEPT_BODY",BODY,{"disambiguationData":[OSD([sQuery(id+"F0.wireOp",EDGE,"E0.bottom"),sQuery(id+"F0.wireOp",EDGE,"E0.top"),sQuery(id+"F0.wireOp",EDGE,"E0.left"),sQuery(id+"F0.wireOp",EDGE,"E0.right")])]}),"instanceName":"1"}),"instanceName":"1"}),"instanceName":"1"}),"instanceName":"1"}),"instanceName":"1"}),"instanceName":"1"});
            var Q120;
            Q120=makeQuery(id+"F45.opPattern","COPY",BODY,{"derivedFrom":makeQuery(id+"F40.opPattern","COPY",BODY,{"derivedFrom":makeQuery(id+"F23.opPattern","COPY",BODY,{"derivedFrom":makeQuery(id+"F19.opPattern","COPY",BODY,{"derivedFrom":makeQuery(id+"F17.opPattern","COPY",BODY,{"derivedFrom":makeQuery(id+"F6.opPattern","COPY",BODY,{"derivedFrom":makeQuery(id+"F5.opPattern","COPY",BODY,{"derivedFrom":makeQuery(id+"F4.opPattern","COPY",BODY,{"derivedFrom":makeQuery(id+"F1.opExtrude","SWEPT_BODY",BODY,{"disambiguationData":[OSD([sQuery(id+"F0.wireOp",EDGE,"E0.bottom"),sQuery(id+"F0.wireOp",EDGE,"E0.top"),sQuery(id+"F0.wireOp",EDGE,"E0.left"),sQuery(id+"F0.wireOp",EDGE,"E0.right")])]}),"instanceName":"1"}),"instanceName":"1"}),"instanceName":"1"}),"instanceName":"1"}),"instanceName":"1"}),"instanceName":"1"}),"instanceName":"1"}),"instanceName":"1"});
            var Q121;
            Q121=makeQuery(id+"F19.opPattern","COPY",BODY,{"derivedFrom":makeQuery(id+"F12.opPattern","COPY",BODY,{"derivedFrom":makeQuery(id+"F6.opPattern","COPY",BODY,{"derivedFrom":makeQuery(id+"F5.opPattern","COPY",BODY,{"derivedFrom":makeQuery(id+"F4.opPattern","COPY",BODY,{"derivedFrom":makeQuery(id+"F1.opExtrude","SWEPT_BODY",BODY,{"disambiguationData":[OSD([sQuery(id+"F0.wireOp",EDGE,"E0.bottom"),sQuery(id+"F0.wireOp",EDGE,"E0.top"),sQuery(id+"F0.wireOp",EDGE,"E0.left"),sQuery(id+"F0.wireOp",EDGE,"E0.right")])]}),"instanceName":"1"}),"instanceName":"1"}),"instanceName":"1"}),"instanceName":"1"}),"instanceName":"1"});
            var Q122;
            Q122=makeQuery(id+"F18.opPattern","COPY",BODY,{"derivedFrom":makeQuery(id+"F17.opPattern","COPY",BODY,{"derivedFrom":makeQuery(id+"F15.opPattern","COPY",BODY,{"derivedFrom":makeQuery(id+"F12.opPattern","COPY",BODY,{"derivedFrom":makeQuery(id+"F6.opPattern","COPY",BODY,{"derivedFrom":makeQuery(id+"F5.opPattern","COPY",BODY,{"derivedFrom":makeQuery(id+"F4.opPattern","COPY",BODY,{"derivedFrom":makeQuery(id+"F2.opPattern","COPY",BODY,{"derivedFrom":makeQuery(id+"F1.opExtrude","SWEPT_BODY",BODY,{"disambiguationData":[OSD([sQuery(id+"F0.wireOp",EDGE,"E0.bottom"),sQuery(id+"F0.wireOp",EDGE,"E0.top"),sQuery(id+"F0.wireOp",EDGE,"E0.left"),sQuery(id+"F0.wireOp",EDGE,"E0.right")])]}),"instanceName":"1"}),"instanceName":"1"}),"instanceName":"1"}),"instanceName":"1"}),"instanceName":"1"}),"instanceName":"1"}),"instanceName":"1"}),"instanceName":"1"});
            var Q123;
            Q123=makeQuery(id+"F21.opPattern","COPY",BODY,{"derivedFrom":makeQuery(id+"F19.opPattern","COPY",BODY,{"derivedFrom":makeQuery(id+"F17.opPattern","COPY",BODY,{"derivedFrom":makeQuery(id+"F5.opPattern","COPY",BODY,{"derivedFrom":makeQuery(id+"F4.opPattern","COPY",BODY,{"derivedFrom":makeQuery(id+"F1.opExtrude","SWEPT_BODY",BODY,{"disambiguationData":[OSD([sQuery(id+"F0.wireOp",EDGE,"E0.bottom"),sQuery(id+"F0.wireOp",EDGE,"E0.top"),sQuery(id+"F0.wireOp",EDGE,"E0.left"),sQuery(id+"F0.wireOp",EDGE,"E0.right")])]}),"instanceName":"1"}),"instanceName":"1"}),"instanceName":"1"}),"instanceName":"1"}),"instanceName":"1"});
            var Q124;
            Q124=makeQuery(id+"F28.opPattern","COPY",BODY,{"derivedFrom":makeQuery(id+"F26.opPattern","COPY",BODY,{"derivedFrom":makeQuery(id+"F23.opPattern","COPY",BODY,{"derivedFrom":makeQuery(id+"F19.opPattern","COPY",BODY,{"derivedFrom":makeQuery(id+"F17.opPattern","COPY",BODY,{"derivedFrom":makeQuery(id+"F13.opPattern","COPY",BODY,{"derivedFrom":makeQuery(id+"F5.opPattern","COPY",BODY,{"derivedFrom":makeQuery(id+"F4.opPattern","COPY",BODY,{"derivedFrom":makeQuery(id+"F1.opExtrude","SWEPT_BODY",BODY,{"disambiguationData":[OSD([sQuery(id+"F0.wireOp",EDGE,"E0.bottom"),sQuery(id+"F0.wireOp",EDGE,"E0.top"),sQuery(id+"F0.wireOp",EDGE,"E0.left"),sQuery(id+"F0.wireOp",EDGE,"E0.right")])]}),"instanceName":"1"}),"instanceName":"1"}),"instanceName":"1"}),"instanceName":"1"}),"instanceName":"1"}),"instanceName":"1"}),"instanceName":"1"}),"instanceName":"1"});
            var Q125;
            Q125=makeQuery(id+"F11.opPattern","COPY",BODY,{"derivedFrom":makeQuery(id+"F6.opPattern","COPY",BODY,{"derivedFrom":makeQuery(id+"F5.opPattern","COPY",BODY,{"derivedFrom":makeQuery(id+"F1.opExtrude","SWEPT_BODY",BODY,{"disambiguationData":[OSD([sQuery(id+"F0.wireOp",EDGE,"E0.bottom"),sQuery(id+"F0.wireOp",EDGE,"E0.top"),sQuery(id+"F0.wireOp",EDGE,"E0.left"),sQuery(id+"F0.wireOp",EDGE,"E0.right")])]}),"instanceName":"1"}),"instanceName":"1"}),"instanceName":"1"});
            var Q126;
            Q126=makeQuery(id+"F37.opPattern","COPY",BODY,{"derivedFrom":makeQuery(id+"F35.opPattern","COPY",BODY,{"derivedFrom":makeQuery(id+"F34.opPattern","COPY",BODY,{"derivedFrom":makeQuery(id+"F31.opPattern","COPY",BODY,{"derivedFrom":makeQuery(id+"F5.opPattern","COPY",BODY,{"derivedFrom":makeQuery(id+"F2.opPattern","COPY",BODY,{"derivedFrom":makeQuery(id+"F1.opExtrude","SWEPT_BODY",BODY,{"disambiguationData":[OSD([sQuery(id+"F0.wireOp",EDGE,"E0.bottom"),sQuery(id+"F0.wireOp",EDGE,"E0.top"),sQuery(id+"F0.wireOp",EDGE,"E0.left"),sQuery(id+"F0.wireOp",EDGE,"E0.right")])]}),"instanceName":"1"}),"instanceName":"1"}),"instanceName":"1"}),"instanceName":"1"}),"instanceName":"1"}),"instanceName":"1"});
            var Q127;
            Q127=makeQuery(id+"F26.opPattern","COPY",BODY,{"derivedFrom":makeQuery(id+"F23.opPattern","COPY",BODY,{"derivedFrom":makeQuery(id+"F19.opPattern","COPY",BODY,{"derivedFrom":makeQuery(id+"F17.opPattern","COPY",BODY,{"derivedFrom":makeQuery(id+"F15.opPattern","COPY",BODY,{"derivedFrom":makeQuery(id+"F12.opPattern","COPY",BODY,{"derivedFrom":makeQuery(id+"F6.opPattern","COPY",BODY,{"derivedFrom":makeQuery(id+"F5.opPattern","COPY",BODY,{"derivedFrom":makeQuery(id+"F4.opPattern","COPY",BODY,{"derivedFrom":makeQuery(id+"F2.opPattern","COPY",BODY,{"derivedFrom":makeQuery(id+"F1.opExtrude","SWEPT_BODY",BODY,{"disambiguationData":[OSD([sQuery(id+"F0.wireOp",EDGE,"E0.bottom"),sQuery(id+"F0.wireOp",EDGE,"E0.top"),sQuery(id+"F0.wireOp",EDGE,"E0.left"),sQuery(id+"F0.wireOp",EDGE,"E0.right")])]}),"instanceName":"1"}),"instanceName":"1"}),"instanceName":"1"}),"instanceName":"1"}),"instanceName":"1"}),"instanceName":"1"}),"instanceName":"1"}),"instanceName":"1"}),"instanceName":"1"}),"instanceName":"1"});
            var Q128;
            Q128=makeQuery(id+"F26.opPattern","COPY",BODY,{"derivedFrom":makeQuery(id+"F19.opPattern","COPY",BODY,{"derivedFrom":makeQuery(id+"F13.opPattern","COPY",BODY,{"derivedFrom":makeQuery(id+"F5.opPattern","COPY",BODY,{"derivedFrom":makeQuery(id+"F4.opPattern","COPY",BODY,{"derivedFrom":makeQuery(id+"F1.opExtrude","SWEPT_BODY",BODY,{"disambiguationData":[OSD([sQuery(id+"F0.wireOp",EDGE,"E0.bottom"),sQuery(id+"F0.wireOp",EDGE,"E0.top"),sQuery(id+"F0.wireOp",EDGE,"E0.left"),sQuery(id+"F0.wireOp",EDGE,"E0.right")])]}),"instanceName":"1"}),"instanceName":"1"}),"instanceName":"1"}),"instanceName":"1"}),"instanceName":"1"});
            var Q129;
            Q129=makeQuery(id+"F40.opPattern","COPY",BODY,{"derivedFrom":makeQuery(id+"F19.opPattern","COPY",BODY,{"derivedFrom":makeQuery(id+"F6.opPattern","COPY",BODY,{"derivedFrom":makeQuery(id+"F5.opPattern","COPY",BODY,{"derivedFrom":makeQuery(id+"F4.opPattern","COPY",BODY,{"derivedFrom":makeQuery(id+"F2.opPattern","COPY",BODY,{"derivedFrom":makeQuery(id+"F1.opExtrude","SWEPT_BODY",BODY,{"disambiguationData":[OSD([sQuery(id+"F0.wireOp",EDGE,"E0.bottom"),sQuery(id+"F0.wireOp",EDGE,"E0.top"),sQuery(id+"F0.wireOp",EDGE,"E0.left"),sQuery(id+"F0.wireOp",EDGE,"E0.right")])]}),"instanceName":"1"}),"instanceName":"1"}),"instanceName":"1"}),"instanceName":"1"}),"instanceName":"1"}),"instanceName":"1"});
            var Q130;
            Q130=makeQuery(id+"F35.opPattern","COPY",BODY,{"derivedFrom":makeQuery(id+"F31.opPattern","COPY",BODY,{"derivedFrom":makeQuery(id+"F4.opPattern","COPY",BODY,{"derivedFrom":makeQuery(id+"F1.opExtrude","SWEPT_BODY",BODY,{"disambiguationData":[OSD([sQuery(id+"F0.wireOp",EDGE,"E0.bottom"),sQuery(id+"F0.wireOp",EDGE,"E0.top"),sQuery(id+"F0.wireOp",EDGE,"E0.left"),sQuery(id+"F0.wireOp",EDGE,"E0.right")])]}),"instanceName":"1"}),"instanceName":"1"}),"instanceName":"1"});
            var Q131;
            Q131=makeQuery(id+"F40.opPattern","COPY",BODY,{"derivedFrom":makeQuery(id+"F24.opPattern","COPY",BODY,{"derivedFrom":makeQuery(id+"F23.opPattern","COPY",BODY,{"derivedFrom":makeQuery(id+"F21.opPattern","COPY",BODY,{"derivedFrom":makeQuery(id+"F19.opPattern","COPY",BODY,{"derivedFrom":makeQuery(id+"F17.opPattern","COPY",BODY,{"derivedFrom":makeQuery(id+"F12.opPattern","COPY",BODY,{"derivedFrom":makeQuery(id+"F6.opPattern","COPY",BODY,{"derivedFrom":makeQuery(id+"F5.opPattern","COPY",BODY,{"derivedFrom":makeQuery(id+"F4.opPattern","COPY",BODY,{"derivedFrom":makeQuery(id+"F1.opExtrude","SWEPT_BODY",BODY,{"disambiguationData":[OSD([sQuery(id+"F0.wireOp",EDGE,"E0.bottom"),sQuery(id+"F0.wireOp",EDGE,"E0.top"),sQuery(id+"F0.wireOp",EDGE,"E0.left"),sQuery(id+"F0.wireOp",EDGE,"E0.right")])]}),"instanceName":"1"}),"instanceName":"1"}),"instanceName":"1"}),"instanceName":"1"}),"instanceName":"1"}),"instanceName":"1"}),"instanceName":"1"}),"instanceName":"1"}),"instanceName":"1"}),"instanceName":"1"});
            var Q132;
            Q132=makeQuery(id+"F28.opPattern","COPY",BODY,{"derivedFrom":makeQuery(id+"F23.opPattern","COPY",BODY,{"derivedFrom":makeQuery(id+"F19.opPattern","COPY",BODY,{"derivedFrom":makeQuery(id+"F17.opPattern","COPY",BODY,{"derivedFrom":makeQuery(id+"F13.opPattern","COPY",BODY,{"derivedFrom":makeQuery(id+"F5.opPattern","COPY",BODY,{"derivedFrom":makeQuery(id+"F4.opPattern","COPY",BODY,{"derivedFrom":makeQuery(id+"F1.opExtrude","SWEPT_BODY",BODY,{"disambiguationData":[OSD([sQuery(id+"F0.wireOp",EDGE,"E0.bottom"),sQuery(id+"F0.wireOp",EDGE,"E0.top"),sQuery(id+"F0.wireOp",EDGE,"E0.left"),sQuery(id+"F0.wireOp",EDGE,"E0.right")])]}),"instanceName":"1"}),"instanceName":"1"}),"instanceName":"1"}),"instanceName":"1"}),"instanceName":"1"}),"instanceName":"1"}),"instanceName":"1"});
            var Q133;
            Q133=makeQuery(id+"F29.opPattern","COPY",BODY,{"derivedFrom":makeQuery(id+"F28.opPattern","COPY",BODY,{"derivedFrom":makeQuery(id+"F19.opPattern","COPY",BODY,{"derivedFrom":makeQuery(id+"F15.opPattern","COPY",BODY,{"derivedFrom":makeQuery(id+"F12.opPattern","COPY",BODY,{"derivedFrom":makeQuery(id+"F6.opPattern","COPY",BODY,{"derivedFrom":makeQuery(id+"F5.opPattern","COPY",BODY,{"derivedFrom":makeQuery(id+"F4.opPattern","COPY",BODY,{"derivedFrom":makeQuery(id+"F2.opPattern","COPY",BODY,{"derivedFrom":makeQuery(id+"F1.opExtrude","SWEPT_BODY",BODY,{"disambiguationData":[OSD([sQuery(id+"F0.wireOp",EDGE,"E0.bottom"),sQuery(id+"F0.wireOp",EDGE,"E0.top"),sQuery(id+"F0.wireOp",EDGE,"E0.left"),sQuery(id+"F0.wireOp",EDGE,"E0.right")])]}),"instanceName":"1"}),"instanceName":"1"}),"instanceName":"1"}),"instanceName":"1"}),"instanceName":"1"}),"instanceName":"1"}),"instanceName":"1"}),"instanceName":"1"}),"instanceName":"1"});
            var Q134;
            Q134=makeQuery(id+"F35.opPattern","COPY",BODY,{"derivedFrom":makeQuery(id+"F34.opPattern","COPY",BODY,{"derivedFrom":makeQuery(id+"F31.opPattern","COPY",BODY,{"derivedFrom":makeQuery(id+"F2.opPattern","COPY",BODY,{"derivedFrom":makeQuery(id+"F1.opExtrude","SWEPT_BODY",BODY,{"disambiguationData":[OSD([sQuery(id+"F0.wireOp",EDGE,"E0.bottom"),sQuery(id+"F0.wireOp",EDGE,"E0.top"),sQuery(id+"F0.wireOp",EDGE,"E0.left"),sQuery(id+"F0.wireOp",EDGE,"E0.right")])]}),"instanceName":"1"}),"instanceName":"1"}),"instanceName":"1"}),"instanceName":"1"});
            var Q135;
            Q135=makeQuery(id+"F33.opPattern","COPY",BODY,{"derivedFrom":makeQuery(id+"F31.opPattern","COPY",BODY,{"derivedFrom":makeQuery(id+"F4.opPattern","COPY",BODY,{"derivedFrom":makeQuery(id+"F1.opExtrude","SWEPT_BODY",BODY,{"disambiguationData":[OSD([sQuery(id+"F0.wireOp",EDGE,"E0.bottom"),sQuery(id+"F0.wireOp",EDGE,"E0.top"),sQuery(id+"F0.wireOp",EDGE,"E0.left"),sQuery(id+"F0.wireOp",EDGE,"E0.right")])]}),"instanceName":"1"}),"instanceName":"1"}),"instanceName":"1"});
            var Q136;
            Q136=makeQuery(id+"F40.opPattern","COPY",BODY,{"derivedFrom":makeQuery(id+"F19.opPattern","COPY",BODY,{"derivedFrom":makeQuery(id+"F12.opPattern","COPY",BODY,{"derivedFrom":makeQuery(id+"F6.opPattern","COPY",BODY,{"derivedFrom":makeQuery(id+"F5.opPattern","COPY",BODY,{"derivedFrom":makeQuery(id+"F4.opPattern","COPY",BODY,{"derivedFrom":makeQuery(id+"F2.opPattern","COPY",BODY,{"derivedFrom":makeQuery(id+"F1.opExtrude","SWEPT_BODY",BODY,{"disambiguationData":[OSD([sQuery(id+"F0.wireOp",EDGE,"E0.bottom"),sQuery(id+"F0.wireOp",EDGE,"E0.top"),sQuery(id+"F0.wireOp",EDGE,"E0.left"),sQuery(id+"F0.wireOp",EDGE,"E0.right")])]}),"instanceName":"1"}),"instanceName":"1"}),"instanceName":"1"}),"instanceName":"1"}),"instanceName":"1"}),"instanceName":"1"}),"instanceName":"1"});
            var Q137;
            Q137=makeQuery(id+"F40.opPattern","COPY",BODY,{"derivedFrom":makeQuery(id+"F26.opPattern","COPY",BODY,{"derivedFrom":makeQuery(id+"F17.opPattern","COPY",BODY,{"derivedFrom":makeQuery(id+"F6.opPattern","COPY",BODY,{"derivedFrom":makeQuery(id+"F5.opPattern","COPY",BODY,{"derivedFrom":makeQuery(id+"F4.opPattern","COPY",BODY,{"derivedFrom":makeQuery(id+"F2.opPattern","COPY",BODY,{"derivedFrom":makeQuery(id+"F1.opExtrude","SWEPT_BODY",BODY,{"disambiguationData":[OSD([sQuery(id+"F0.wireOp",EDGE,"E0.bottom"),sQuery(id+"F0.wireOp",EDGE,"E0.top"),sQuery(id+"F0.wireOp",EDGE,"E0.left"),sQuery(id+"F0.wireOp",EDGE,"E0.right")])]}),"instanceName":"1"}),"instanceName":"1"}),"instanceName":"1"}),"instanceName":"1"}),"instanceName":"1"}),"instanceName":"1"}),"instanceName":"1"});
            var Q138;
            Q138=makeQuery(id+"F26.opPattern","COPY",BODY,{"derivedFrom":makeQuery(id+"F17.opPattern","COPY",BODY,{"derivedFrom":makeQuery(id+"F13.opPattern","COPY",BODY,{"derivedFrom":makeQuery(id+"F5.opPattern","COPY",BODY,{"derivedFrom":makeQuery(id+"F4.opPattern","COPY",BODY,{"derivedFrom":makeQuery(id+"F1.opExtrude","SWEPT_BODY",BODY,{"disambiguationData":[OSD([sQuery(id+"F0.wireOp",EDGE,"E0.bottom"),sQuery(id+"F0.wireOp",EDGE,"E0.top"),sQuery(id+"F0.wireOp",EDGE,"E0.left"),sQuery(id+"F0.wireOp",EDGE,"E0.right")])]}),"instanceName":"1"}),"instanceName":"1"}),"instanceName":"1"}),"instanceName":"1"}),"instanceName":"1"});
            var Q139;
            Q139=makeQuery(id+"F40.opPattern","COPY",BODY,{"derivedFrom":makeQuery(id+"F19.opPattern","COPY",BODY,{"derivedFrom":makeQuery(id+"F17.opPattern","COPY",BODY,{"derivedFrom":makeQuery(id+"F6.opPattern","COPY",BODY,{"derivedFrom":makeQuery(id+"F5.opPattern","COPY",BODY,{"derivedFrom":makeQuery(id+"F4.opPattern","COPY",BODY,{"derivedFrom":makeQuery(id+"F1.opExtrude","SWEPT_BODY",BODY,{"disambiguationData":[OSD([sQuery(id+"F0.wireOp",EDGE,"E0.bottom"),sQuery(id+"F0.wireOp",EDGE,"E0.top"),sQuery(id+"F0.wireOp",EDGE,"E0.left"),sQuery(id+"F0.wireOp",EDGE,"E0.right")])]}),"instanceName":"1"}),"instanceName":"1"}),"instanceName":"1"}),"instanceName":"1"}),"instanceName":"1"}),"instanceName":"1"});
            var Q140;
            Q140=makeQuery(id+"F45.opPattern","COPY",BODY,{"derivedFrom":makeQuery(id+"F40.opPattern","COPY",BODY,{"derivedFrom":makeQuery(id+"F29.opPattern","COPY",BODY,{"derivedFrom":makeQuery(id+"F19.opPattern","COPY",BODY,{"derivedFrom":makeQuery(id+"F17.opPattern","COPY",BODY,{"derivedFrom":makeQuery(id+"F13.opPattern","COPY",BODY,{"derivedFrom":makeQuery(id+"F5.opPattern","COPY",BODY,{"derivedFrom":makeQuery(id+"F4.opPattern","COPY",BODY,{"derivedFrom":makeQuery(id+"F1.opExtrude","SWEPT_BODY",BODY,{"disambiguationData":[OSD([sQuery(id+"F0.wireOp",EDGE,"E0.bottom"),sQuery(id+"F0.wireOp",EDGE,"E0.top"),sQuery(id+"F0.wireOp",EDGE,"E0.left"),sQuery(id+"F0.wireOp",EDGE,"E0.right")])]}),"instanceName":"1"}),"instanceName":"1"}),"instanceName":"1"}),"instanceName":"1"}),"instanceName":"1"}),"instanceName":"1"}),"instanceName":"1"}),"instanceName":"1"});
            var Q141;
            Q141=makeQuery(id+"F26.opPattern","COPY",BODY,{"derivedFrom":makeQuery(id+"F17.opPattern","COPY",BODY,{"derivedFrom":makeQuery(id+"F6.opPattern","COPY",BODY,{"derivedFrom":makeQuery(id+"F5.opPattern","COPY",BODY,{"derivedFrom":makeQuery(id+"F4.opPattern","COPY",BODY,{"derivedFrom":makeQuery(id+"F1.opExtrude","SWEPT_BODY",BODY,{"disambiguationData":[OSD([sQuery(id+"F0.wireOp",EDGE,"E0.bottom"),sQuery(id+"F0.wireOp",EDGE,"E0.top"),sQuery(id+"F0.wireOp",EDGE,"E0.left"),sQuery(id+"F0.wireOp",EDGE,"E0.right")])]}),"instanceName":"1"}),"instanceName":"1"}),"instanceName":"1"}),"instanceName":"1"}),"instanceName":"1"});
            var Q142;
            Q142=makeQuery(id+"F12.opPattern","COPY",BODY,{"derivedFrom":makeQuery(id+"F6.opPattern","COPY",BODY,{"derivedFrom":makeQuery(id+"F5.opPattern","COPY",BODY,{"derivedFrom":makeQuery(id+"F4.opPattern","COPY",BODY,{"derivedFrom":makeQuery(id+"F1.opExtrude","SWEPT_BODY",BODY,{"disambiguationData":[OSD([sQuery(id+"F0.wireOp",EDGE,"E0.bottom"),sQuery(id+"F0.wireOp",EDGE,"E0.top"),sQuery(id+"F0.wireOp",EDGE,"E0.left"),sQuery(id+"F0.wireOp",EDGE,"E0.right")])]}),"instanceName":"1"}),"instanceName":"1"}),"instanceName":"1"}),"instanceName":"1"});
            var Q143;
            Q143=makeQuery(id+"F24.opPattern","COPY",BODY,{"derivedFrom":makeQuery(id+"F23.opPattern","COPY",BODY,{"derivedFrom":makeQuery(id+"F19.opPattern","COPY",BODY,{"derivedFrom":makeQuery(id+"F17.opPattern","COPY",BODY,{"derivedFrom":makeQuery(id+"F5.opPattern","COPY",BODY,{"derivedFrom":makeQuery(id+"F4.opPattern","COPY",BODY,{"derivedFrom":makeQuery(id+"F1.opExtrude","SWEPT_BODY",BODY,{"disambiguationData":[OSD([sQuery(id+"F0.wireOp",EDGE,"E0.bottom"),sQuery(id+"F0.wireOp",EDGE,"E0.top"),sQuery(id+"F0.wireOp",EDGE,"E0.left"),sQuery(id+"F0.wireOp",EDGE,"E0.right")])]}),"instanceName":"1"}),"instanceName":"1"}),"instanceName":"1"}),"instanceName":"1"}),"instanceName":"1"}),"instanceName":"1"});
            var Q144;
            Q144=makeQuery(id+"F41.opPattern","COPY",BODY,{"derivedFrom":makeQuery(id+"F40.opPattern","COPY",BODY,{"derivedFrom":makeQuery(id+"F28.opPattern","COPY",BODY,{"derivedFrom":makeQuery(id+"F19.opPattern","COPY",BODY,{"derivedFrom":makeQuery(id+"F13.opPattern","COPY",BODY,{"derivedFrom":makeQuery(id+"F5.opPattern","COPY",BODY,{"derivedFrom":makeQuery(id+"F4.opPattern","COPY",BODY,{"derivedFrom":makeQuery(id+"F1.opExtrude","SWEPT_BODY",BODY,{"disambiguationData":[OSD([sQuery(id+"F0.wireOp",EDGE,"E0.bottom"),sQuery(id+"F0.wireOp",EDGE,"E0.top"),sQuery(id+"F0.wireOp",EDGE,"E0.left"),sQuery(id+"F0.wireOp",EDGE,"E0.right")])]}),"instanceName":"1"}),"instanceName":"1"}),"instanceName":"1"}),"instanceName":"1"}),"instanceName":"1"}),"instanceName":"1"}),"instanceName":"1"});
            var Q145;
            Q145=makeQuery(id+"F40.opPattern","COPY",BODY,{"derivedFrom":makeQuery(id+"F28.opPattern","COPY",BODY,{"derivedFrom":makeQuery(id+"F23.opPattern","COPY",BODY,{"derivedFrom":makeQuery(id+"F19.opPattern","COPY",BODY,{"derivedFrom":makeQuery(id+"F17.opPattern","COPY",BODY,{"derivedFrom":makeQuery(id+"F15.opPattern","COPY",BODY,{"derivedFrom":makeQuery(id+"F12.opPattern","COPY",BODY,{"derivedFrom":makeQuery(id+"F6.opPattern","COPY",BODY,{"derivedFrom":makeQuery(id+"F5.opPattern","COPY",BODY,{"derivedFrom":makeQuery(id+"F4.opPattern","COPY",BODY,{"derivedFrom":makeQuery(id+"F2.opPattern","COPY",BODY,{"derivedFrom":makeQuery(id+"F1.opExtrude","SWEPT_BODY",BODY,{"disambiguationData":[OSD([sQuery(id+"F0.wireOp",EDGE,"E0.bottom"),sQuery(id+"F0.wireOp",EDGE,"E0.top"),sQuery(id+"F0.wireOp",EDGE,"E0.left"),sQuery(id+"F0.wireOp",EDGE,"E0.right")])]}),"instanceName":"1"}),"instanceName":"1"}),"instanceName":"1"}),"instanceName":"1"}),"instanceName":"1"}),"instanceName":"1"}),"instanceName":"1"}),"instanceName":"1"}),"instanceName":"1"}),"instanceName":"1"}),"instanceName":"1"});
            var Q146;
            Q146=makeQuery(id+"F18.opPattern","COPY",BODY,{"derivedFrom":makeQuery(id+"F17.opPattern","COPY",BODY,{"derivedFrom":makeQuery(id+"F8.opPattern","COPY",BODY,{"derivedFrom":makeQuery(id+"F5.opPattern","COPY",BODY,{"derivedFrom":makeQuery(id+"F4.opPattern","COPY",BODY,{"derivedFrom":makeQuery(id+"F1.opExtrude","SWEPT_BODY",BODY,{"disambiguationData":[OSD([sQuery(id+"F0.wireOp",EDGE,"E0.bottom"),sQuery(id+"F0.wireOp",EDGE,"E0.top"),sQuery(id+"F0.wireOp",EDGE,"E0.left"),sQuery(id+"F0.wireOp",EDGE,"E0.right")])]}),"instanceName":"1"}),"instanceName":"1"}),"instanceName":"1"}),"instanceName":"1"}),"instanceName":"1"});
            var Q147;
            Q147=makeQuery(id+"F29.opPattern","COPY",BODY,{"derivedFrom":makeQuery(id+"F28.opPattern","COPY",BODY,{"derivedFrom":makeQuery(id+"F19.opPattern","COPY",BODY,{"derivedFrom":makeQuery(id+"F17.opPattern","COPY",BODY,{"derivedFrom":makeQuery(id+"F13.opPattern","COPY",BODY,{"derivedFrom":makeQuery(id+"F5.opPattern","COPY",BODY,{"derivedFrom":makeQuery(id+"F4.opPattern","COPY",BODY,{"derivedFrom":makeQuery(id+"F1.opExtrude","SWEPT_BODY",BODY,{"disambiguationData":[OSD([sQuery(id+"F0.wireOp",EDGE,"E0.bottom"),sQuery(id+"F0.wireOp",EDGE,"E0.top"),sQuery(id+"F0.wireOp",EDGE,"E0.left"),sQuery(id+"F0.wireOp",EDGE,"E0.right")])]}),"instanceName":"1"}),"instanceName":"1"}),"instanceName":"1"}),"instanceName":"1"}),"instanceName":"1"}),"instanceName":"1"}),"instanceName":"1"});
            var Q148;
            Q148=makeQuery(id+"F39.opPattern","COPY",BODY,{"derivedFrom":makeQuery(id+"F26.opPattern","COPY",BODY,{"derivedFrom":makeQuery(id+"F17.opPattern","COPY",BODY,{"derivedFrom":makeQuery(id+"F12.opPattern","COPY",BODY,{"derivedFrom":makeQuery(id+"F6.opPattern","COPY",BODY,{"derivedFrom":makeQuery(id+"F5.opPattern","COPY",BODY,{"derivedFrom":makeQuery(id+"F4.opPattern","COPY",BODY,{"derivedFrom":makeQuery(id+"F2.opPattern","COPY",BODY,{"derivedFrom":makeQuery(id+"F1.opExtrude","SWEPT_BODY",BODY,{"disambiguationData":[OSD([sQuery(id+"F0.wireOp",EDGE,"E0.bottom"),sQuery(id+"F0.wireOp",EDGE,"E0.top"),sQuery(id+"F0.wireOp",EDGE,"E0.left"),sQuery(id+"F0.wireOp",EDGE,"E0.right")])]}),"instanceName":"1"}),"instanceName":"1"}),"instanceName":"1"}),"instanceName":"1"}),"instanceName":"1"}),"instanceName":"1"}),"instanceName":"1"}),"instanceName":"1"});
            var Q149;
            Q149=makeQuery(id+"F31.opPattern","COPY",BODY,{"derivedFrom":makeQuery(id+"F4.opPattern","COPY",BODY,{"derivedFrom":makeQuery(id+"F2.opPattern","COPY",BODY,{"derivedFrom":makeQuery(id+"F1.opExtrude","SWEPT_BODY",BODY,{"disambiguationData":[OSD([sQuery(id+"F0.wireOp",EDGE,"E0.bottom"),sQuery(id+"F0.wireOp",EDGE,"E0.top"),sQuery(id+"F0.wireOp",EDGE,"E0.left"),sQuery(id+"F0.wireOp",EDGE,"E0.right")])]}),"instanceName":"1"}),"instanceName":"1"}),"instanceName":"1"});
            var Q150;
            Q150=makeQuery(id+"F26.opPattern","COPY",BODY,{"derivedFrom":makeQuery(id+"F23.opPattern","COPY",BODY,{"derivedFrom":makeQuery(id+"F19.opPattern","COPY",BODY,{"derivedFrom":makeQuery(id+"F6.opPattern","COPY",BODY,{"derivedFrom":makeQuery(id+"F5.opPattern","COPY",BODY,{"derivedFrom":makeQuery(id+"F4.opPattern","COPY",BODY,{"derivedFrom":makeQuery(id+"F2.opPattern","COPY",BODY,{"derivedFrom":makeQuery(id+"F1.opExtrude","SWEPT_BODY",BODY,{"disambiguationData":[OSD([sQuery(id+"F0.wireOp",EDGE,"E0.bottom"),sQuery(id+"F0.wireOp",EDGE,"E0.top"),sQuery(id+"F0.wireOp",EDGE,"E0.left"),sQuery(id+"F0.wireOp",EDGE,"E0.right")])]}),"instanceName":"1"}),"instanceName":"1"}),"instanceName":"1"}),"instanceName":"1"}),"instanceName":"1"}),"instanceName":"1"}),"instanceName":"1"});
            var Q151;
            Q151=makeQuery(id+"F26.opPattern","COPY",BODY,{"derivedFrom":makeQuery(id+"F19.opPattern","COPY",BODY,{"derivedFrom":makeQuery(id+"F12.opPattern","COPY",BODY,{"derivedFrom":makeQuery(id+"F6.opPattern","COPY",BODY,{"derivedFrom":makeQuery(id+"F5.opPattern","COPY",BODY,{"derivedFrom":makeQuery(id+"F4.opPattern","COPY",BODY,{"derivedFrom":makeQuery(id+"F1.opExtrude","SWEPT_BODY",BODY,{"disambiguationData":[OSD([sQuery(id+"F0.wireOp",EDGE,"E0.bottom"),sQuery(id+"F0.wireOp",EDGE,"E0.top"),sQuery(id+"F0.wireOp",EDGE,"E0.left"),sQuery(id+"F0.wireOp",EDGE,"E0.right")])]}),"instanceName":"1"}),"instanceName":"1"}),"instanceName":"1"}),"instanceName":"1"}),"instanceName":"1"}),"instanceName":"1"});
            var Q152;
            Q152=makeQuery(id+"F33.opPattern","COPY",BODY,{"derivedFrom":makeQuery(id+"F31.opPattern","COPY",BODY,{"derivedFrom":makeQuery(id+"F1.opExtrude","SWEPT_BODY",BODY,{"disambiguationData":[OSD([sQuery(id+"F0.wireOp",EDGE,"E0.bottom"),sQuery(id+"F0.wireOp",EDGE,"E0.top"),sQuery(id+"F0.wireOp",EDGE,"E0.left"),sQuery(id+"F0.wireOp",EDGE,"E0.right")])]}),"instanceName":"1"}),"instanceName":"1"});
            var Q153;
            Q153=makeQuery(id+"F45.opPattern","COPY",BODY,{"derivedFrom":makeQuery(id+"F40.opPattern","COPY",BODY,{"derivedFrom":makeQuery(id+"F19.opPattern","COPY",BODY,{"derivedFrom":makeQuery(id+"F17.opPattern","COPY",BODY,{"derivedFrom":makeQuery(id+"F15.opPattern","COPY",BODY,{"derivedFrom":makeQuery(id+"F12.opPattern","COPY",BODY,{"derivedFrom":makeQuery(id+"F6.opPattern","COPY",BODY,{"derivedFrom":makeQuery(id+"F5.opPattern","COPY",BODY,{"derivedFrom":makeQuery(id+"F4.opPattern","COPY",BODY,{"derivedFrom":makeQuery(id+"F2.opPattern","COPY",BODY,{"derivedFrom":makeQuery(id+"F1.opExtrude","SWEPT_BODY",BODY,{"disambiguationData":[OSD([sQuery(id+"F0.wireOp",EDGE,"E0.bottom"),sQuery(id+"F0.wireOp",EDGE,"E0.top"),sQuery(id+"F0.wireOp",EDGE,"E0.left"),sQuery(id+"F0.wireOp",EDGE,"E0.right")])]}),"instanceName":"1"}),"instanceName":"1"}),"instanceName":"1"}),"instanceName":"1"}),"instanceName":"1"}),"instanceName":"1"}),"instanceName":"1"}),"instanceName":"1"}),"instanceName":"1"}),"instanceName":"1"});
            var Q154;
            Q154=makeQuery(id+"F40.opPattern","COPY",BODY,{"derivedFrom":makeQuery(id+"F23.opPattern","COPY",BODY,{"derivedFrom":makeQuery(id+"F19.opPattern","COPY",BODY,{"derivedFrom":makeQuery(id+"F17.opPattern","COPY",BODY,{"derivedFrom":makeQuery(id+"F6.opPattern","COPY",BODY,{"derivedFrom":makeQuery(id+"F5.opPattern","COPY",BODY,{"derivedFrom":makeQuery(id+"F4.opPattern","COPY",BODY,{"derivedFrom":makeQuery(id+"F1.opExtrude","SWEPT_BODY",BODY,{"disambiguationData":[OSD([sQuery(id+"F0.wireOp",EDGE,"E0.bottom"),sQuery(id+"F0.wireOp",EDGE,"E0.top"),sQuery(id+"F0.wireOp",EDGE,"E0.left"),sQuery(id+"F0.wireOp",EDGE,"E0.right")])]}),"instanceName":"1"}),"instanceName":"1"}),"instanceName":"1"}),"instanceName":"1"}),"instanceName":"1"}),"instanceName":"1"}),"instanceName":"1"});
            var Q155;
            Q155=makeQuery(id+"F23.opPattern","COPY",BODY,{"derivedFrom":makeQuery(id+"F19.opPattern","COPY",BODY,{"derivedFrom":makeQuery(id+"F17.opPattern","COPY",BODY,{"derivedFrom":makeQuery(id+"F12.opPattern","COPY",BODY,{"derivedFrom":makeQuery(id+"F6.opPattern","COPY",BODY,{"derivedFrom":makeQuery(id+"F5.opPattern","COPY",BODY,{"derivedFrom":makeQuery(id+"F4.opPattern","COPY",BODY,{"derivedFrom":makeQuery(id+"F2.opPattern","COPY",BODY,{"derivedFrom":makeQuery(id+"F1.opExtrude","SWEPT_BODY",BODY,{"disambiguationData":[OSD([sQuery(id+"F0.wireOp",EDGE,"E0.bottom"),sQuery(id+"F0.wireOp",EDGE,"E0.top"),sQuery(id+"F0.wireOp",EDGE,"E0.left"),sQuery(id+"F0.wireOp",EDGE,"E0.right")])]}),"instanceName":"1"}),"instanceName":"1"}),"instanceName":"1"}),"instanceName":"1"}),"instanceName":"1"}),"instanceName":"1"}),"instanceName":"1"}),"instanceName":"1"});
            var Q156;
            Q156=makeQuery(id+"F39.opPattern","COPY",BODY,{"derivedFrom":makeQuery(id+"F23.opPattern","COPY",BODY,{"derivedFrom":makeQuery(id+"F19.opPattern","COPY",BODY,{"derivedFrom":makeQuery(id+"F17.opPattern","COPY",BODY,{"derivedFrom":makeQuery(id+"F12.opPattern","COPY",BODY,{"derivedFrom":makeQuery(id+"F6.opPattern","COPY",BODY,{"derivedFrom":makeQuery(id+"F5.opPattern","COPY",BODY,{"derivedFrom":makeQuery(id+"F4.opPattern","COPY",BODY,{"derivedFrom":makeQuery(id+"F2.opPattern","COPY",BODY,{"derivedFrom":makeQuery(id+"F1.opExtrude","SWEPT_BODY",BODY,{"disambiguationData":[OSD([sQuery(id+"F0.wireOp",EDGE,"E0.bottom"),sQuery(id+"F0.wireOp",EDGE,"E0.top"),sQuery(id+"F0.wireOp",EDGE,"E0.left"),sQuery(id+"F0.wireOp",EDGE,"E0.right")])]}),"instanceName":"1"}),"instanceName":"1"}),"instanceName":"1"}),"instanceName":"1"}),"instanceName":"1"}),"instanceName":"1"}),"instanceName":"1"}),"instanceName":"1"}),"instanceName":"1"});
            var Q157;
            Q157=makeQuery(id+"F45.opPattern","COPY",BODY,{"derivedFrom":makeQuery(id+"F40.opPattern","COPY",BODY,{"derivedFrom":makeQuery(id+"F28.opPattern","COPY",BODY,{"derivedFrom":makeQuery(id+"F19.opPattern","COPY",BODY,{"derivedFrom":makeQuery(id+"F17.opPattern","COPY",BODY,{"derivedFrom":makeQuery(id+"F13.opPattern","COPY",BODY,{"derivedFrom":makeQuery(id+"F5.opPattern","COPY",BODY,{"derivedFrom":makeQuery(id+"F4.opPattern","COPY",BODY,{"derivedFrom":makeQuery(id+"F1.opExtrude","SWEPT_BODY",BODY,{"disambiguationData":[OSD([sQuery(id+"F0.wireOp",EDGE,"E0.bottom"),sQuery(id+"F0.wireOp",EDGE,"E0.top"),sQuery(id+"F0.wireOp",EDGE,"E0.left"),sQuery(id+"F0.wireOp",EDGE,"E0.right")])]}),"instanceName":"1"}),"instanceName":"1"}),"instanceName":"1"}),"instanceName":"1"}),"instanceName":"1"}),"instanceName":"1"}),"instanceName":"1"}),"instanceName":"1"});
            var Q158;
            Q158=makeQuery(id+"F23.opPattern","COPY",BODY,{"derivedFrom":makeQuery(id+"F19.opPattern","COPY",BODY,{"derivedFrom":makeQuery(id+"F17.opPattern","COPY",BODY,{"derivedFrom":makeQuery(id+"F5.opPattern","COPY",BODY,{"derivedFrom":makeQuery(id+"F4.opPattern","COPY",BODY,{"derivedFrom":makeQuery(id+"F1.opExtrude","SWEPT_BODY",BODY,{"disambiguationData":[OSD([sQuery(id+"F0.wireOp",EDGE,"E0.bottom"),sQuery(id+"F0.wireOp",EDGE,"E0.top"),sQuery(id+"F0.wireOp",EDGE,"E0.left"),sQuery(id+"F0.wireOp",EDGE,"E0.right")])]}),"instanceName":"1"}),"instanceName":"1"}),"instanceName":"1"}),"instanceName":"1"}),"instanceName":"1"});
            var Q159;
            Q159=makeQuery(id+"F28.opPattern","COPY",BODY,{"derivedFrom":makeQuery(id+"F26.opPattern","COPY",BODY,{"derivedFrom":makeQuery(id+"F19.opPattern","COPY",BODY,{"derivedFrom":makeQuery(id+"F13.opPattern","COPY",BODY,{"derivedFrom":makeQuery(id+"F5.opPattern","COPY",BODY,{"derivedFrom":makeQuery(id+"F4.opPattern","COPY",BODY,{"derivedFrom":makeQuery(id+"F1.opExtrude","SWEPT_BODY",BODY,{"disambiguationData":[OSD([sQuery(id+"F0.wireOp",EDGE,"E0.bottom"),sQuery(id+"F0.wireOp",EDGE,"E0.top"),sQuery(id+"F0.wireOp",EDGE,"E0.left"),sQuery(id+"F0.wireOp",EDGE,"E0.right")])]}),"instanceName":"1"}),"instanceName":"1"}),"instanceName":"1"}),"instanceName":"1"}),"instanceName":"1"}),"instanceName":"1"});
            var Q160;
            Q160=makeQuery(id+"F36.opPattern","COPY",BODY,{"derivedFrom":makeQuery(id+"F35.opPattern","COPY",BODY,{"derivedFrom":makeQuery(id+"F31.opPattern","COPY",BODY,{"derivedFrom":makeQuery(id+"F5.opPattern","COPY",BODY,{"derivedFrom":makeQuery(id+"F2.opPattern","COPY",BODY,{"derivedFrom":makeQuery(id+"F1.opExtrude","SWEPT_BODY",BODY,{"disambiguationData":[OSD([sQuery(id+"F0.wireOp",EDGE,"E0.bottom"),sQuery(id+"F0.wireOp",EDGE,"E0.top"),sQuery(id+"F0.wireOp",EDGE,"E0.left"),sQuery(id+"F0.wireOp",EDGE,"E0.right")])]}),"instanceName":"1"}),"instanceName":"1"}),"instanceName":"1"}),"instanceName":"1"}),"instanceName":"1"});
            var Q161;
            Q161=makeQuery(id+"F28.opPattern","COPY",BODY,{"derivedFrom":makeQuery(id+"F26.opPattern","COPY",BODY,{"derivedFrom":makeQuery(id+"F19.opPattern","COPY",BODY,{"derivedFrom":makeQuery(id+"F17.opPattern","COPY",BODY,{"derivedFrom":makeQuery(id+"F15.opPattern","COPY",BODY,{"derivedFrom":makeQuery(id+"F12.opPattern","COPY",BODY,{"derivedFrom":makeQuery(id+"F6.opPattern","COPY",BODY,{"derivedFrom":makeQuery(id+"F5.opPattern","COPY",BODY,{"derivedFrom":makeQuery(id+"F4.opPattern","COPY",BODY,{"derivedFrom":makeQuery(id+"F2.opPattern","COPY",BODY,{"derivedFrom":makeQuery(id+"F1.opExtrude","SWEPT_BODY",BODY,{"disambiguationData":[OSD([sQuery(id+"F0.wireOp",EDGE,"E0.bottom"),sQuery(id+"F0.wireOp",EDGE,"E0.top"),sQuery(id+"F0.wireOp",EDGE,"E0.left"),sQuery(id+"F0.wireOp",EDGE,"E0.right")])]}),"instanceName":"1"}),"instanceName":"1"}),"instanceName":"1"}),"instanceName":"1"}),"instanceName":"1"}),"instanceName":"1"}),"instanceName":"1"}),"instanceName":"1"}),"instanceName":"1"}),"instanceName":"1"});
            var Q162;
            Q162=makeQuery(id+"F26.opPattern","COPY",BODY,{"derivedFrom":makeQuery(id+"F19.opPattern","COPY",BODY,{"derivedFrom":makeQuery(id+"F12.opPattern","COPY",BODY,{"derivedFrom":makeQuery(id+"F6.opPattern","COPY",BODY,{"derivedFrom":makeQuery(id+"F5.opPattern","COPY",BODY,{"derivedFrom":makeQuery(id+"F4.opPattern","COPY",BODY,{"derivedFrom":makeQuery(id+"F2.opPattern","COPY",BODY,{"derivedFrom":makeQuery(id+"F1.opExtrude","SWEPT_BODY",BODY,{"disambiguationData":[OSD([sQuery(id+"F0.wireOp",EDGE,"E0.bottom"),sQuery(id+"F0.wireOp",EDGE,"E0.top"),sQuery(id+"F0.wireOp",EDGE,"E0.left"),sQuery(id+"F0.wireOp",EDGE,"E0.right")])]}),"instanceName":"1"}),"instanceName":"1"}),"instanceName":"1"}),"instanceName":"1"}),"instanceName":"1"}),"instanceName":"1"}),"instanceName":"1"});
            var Q163;
            Q163=makeQuery(id+"F45.opPattern","COPY",BODY,{"derivedFrom":makeQuery(id+"F40.opPattern","COPY",BODY,{"derivedFrom":makeQuery(id+"F19.opPattern","COPY",BODY,{"derivedFrom":makeQuery(id+"F17.opPattern","COPY",BODY,{"derivedFrom":makeQuery(id+"F12.opPattern","COPY",BODY,{"derivedFrom":makeQuery(id+"F6.opPattern","COPY",BODY,{"derivedFrom":makeQuery(id+"F5.opPattern","COPY",BODY,{"derivedFrom":makeQuery(id+"F4.opPattern","COPY",BODY,{"derivedFrom":makeQuery(id+"F2.opPattern","COPY",BODY,{"derivedFrom":makeQuery(id+"F1.opExtrude","SWEPT_BODY",BODY,{"disambiguationData":[OSD([sQuery(id+"F0.wireOp",EDGE,"E0.bottom"),sQuery(id+"F0.wireOp",EDGE,"E0.top"),sQuery(id+"F0.wireOp",EDGE,"E0.left"),sQuery(id+"F0.wireOp",EDGE,"E0.right")])]}),"instanceName":"1"}),"instanceName":"1"}),"instanceName":"1"}),"instanceName":"1"}),"instanceName":"1"}),"instanceName":"1"}),"instanceName":"1"}),"instanceName":"1"}),"instanceName":"1"});
            var Q164;
            Q164=makeQuery(id+"F30.opPattern","COPY",BODY,{"derivedFrom":makeQuery(id+"F29.opPattern","COPY",BODY,{"derivedFrom":makeQuery(id+"F28.opPattern","COPY",BODY,{"derivedFrom":makeQuery(id+"F19.opPattern","COPY",BODY,{"derivedFrom":makeQuery(id+"F17.opPattern","COPY",BODY,{"derivedFrom":makeQuery(id+"F15.opPattern","COPY",BODY,{"derivedFrom":makeQuery(id+"F12.opPattern","COPY",BODY,{"derivedFrom":makeQuery(id+"F6.opPattern","COPY",BODY,{"derivedFrom":makeQuery(id+"F5.opPattern","COPY",BODY,{"derivedFrom":makeQuery(id+"F4.opPattern","COPY",BODY,{"derivedFrom":makeQuery(id+"F2.opPattern","COPY",BODY,{"derivedFrom":makeQuery(id+"F1.opExtrude","SWEPT_BODY",BODY,{"disambiguationData":[OSD([sQuery(id+"F0.wireOp",EDGE,"E0.bottom"),sQuery(id+"F0.wireOp",EDGE,"E0.top"),sQuery(id+"F0.wireOp",EDGE,"E0.left"),sQuery(id+"F0.wireOp",EDGE,"E0.right")])]}),"instanceName":"1"}),"instanceName":"1"}),"instanceName":"1"}),"instanceName":"1"}),"instanceName":"1"}),"instanceName":"1"}),"instanceName":"1"}),"instanceName":"1"}),"instanceName":"1"}),"instanceName":"1"}),"instanceName":"1"});
            var Q165;
            Q165=makeQuery(id+"F19.opPattern","COPY",BODY,{"derivedFrom":makeQuery(id+"F13.opPattern","COPY",BODY,{"derivedFrom":makeQuery(id+"F5.opPattern","COPY",BODY,{"derivedFrom":makeQuery(id+"F4.opPattern","COPY",BODY,{"derivedFrom":makeQuery(id+"F1.opExtrude","SWEPT_BODY",BODY,{"disambiguationData":[OSD([sQuery(id+"F0.wireOp",EDGE,"E0.bottom"),sQuery(id+"F0.wireOp",EDGE,"E0.top"),sQuery(id+"F0.wireOp",EDGE,"E0.left"),sQuery(id+"F0.wireOp",EDGE,"E0.right")])]}),"instanceName":"1"}),"instanceName":"1"}),"instanceName":"1"}),"instanceName":"1"});
            var Q166;
            Q166=makeQuery(id+"F29.opPattern","COPY",BODY,{"derivedFrom":makeQuery(id+"F28.opPattern","COPY",BODY,{"derivedFrom":makeQuery(id+"F26.opPattern","COPY",BODY,{"derivedFrom":makeQuery(id+"F17.opPattern","COPY",BODY,{"derivedFrom":makeQuery(id+"F13.opPattern","COPY",BODY,{"derivedFrom":makeQuery(id+"F5.opPattern","COPY",BODY,{"derivedFrom":makeQuery(id+"F4.opPattern","COPY",BODY,{"derivedFrom":makeQuery(id+"F1.opExtrude","SWEPT_BODY",BODY,{"disambiguationData":[OSD([sQuery(id+"F0.wireOp",EDGE,"E0.bottom"),sQuery(id+"F0.wireOp",EDGE,"E0.top"),sQuery(id+"F0.wireOp",EDGE,"E0.left"),sQuery(id+"F0.wireOp",EDGE,"E0.right")])]}),"instanceName":"1"}),"instanceName":"1"}),"instanceName":"1"}),"instanceName":"1"}),"instanceName":"1"}),"instanceName":"1"}),"instanceName":"1"});
            var Q167;
            Q167=makeQuery(id+"F22.opPattern","COPY",BODY,{"derivedFrom":makeQuery(id+"F21.opPattern","COPY",BODY,{"derivedFrom":makeQuery(id+"F19.opPattern","COPY",BODY,{"derivedFrom":makeQuery(id+"F17.opPattern","COPY",BODY,{"derivedFrom":makeQuery(id+"F12.opPattern","COPY",BODY,{"derivedFrom":makeQuery(id+"F6.opPattern","COPY",BODY,{"derivedFrom":makeQuery(id+"F5.opPattern","COPY",BODY,{"derivedFrom":makeQuery(id+"F4.opPattern","COPY",BODY,{"derivedFrom":makeQuery(id+"F1.opExtrude","SWEPT_BODY",BODY,{"disambiguationData":[OSD([sQuery(id+"F0.wireOp",EDGE,"E0.bottom"),sQuery(id+"F0.wireOp",EDGE,"E0.top"),sQuery(id+"F0.wireOp",EDGE,"E0.left"),sQuery(id+"F0.wireOp",EDGE,"E0.right")])]}),"instanceName":"1"}),"instanceName":"1"}),"instanceName":"1"}),"instanceName":"1"}),"instanceName":"1"}),"instanceName":"1"}),"instanceName":"1"}),"instanceName":"1"});
            var Q168;
            Q168=makeQuery(id+"F40.opPattern","COPY",BODY,{"derivedFrom":makeQuery(id+"F23.opPattern","COPY",BODY,{"derivedFrom":makeQuery(id+"F21.opPattern","COPY",BODY,{"derivedFrom":makeQuery(id+"F19.opPattern","COPY",BODY,{"derivedFrom":makeQuery(id+"F12.opPattern","COPY",BODY,{"derivedFrom":makeQuery(id+"F6.opPattern","COPY",BODY,{"derivedFrom":makeQuery(id+"F5.opPattern","COPY",BODY,{"derivedFrom":makeQuery(id+"F4.opPattern","COPY",BODY,{"derivedFrom":makeQuery(id+"F2.opPattern","COPY",BODY,{"derivedFrom":makeQuery(id+"F1.opExtrude","SWEPT_BODY",BODY,{"disambiguationData":[OSD([sQuery(id+"F0.wireOp",EDGE,"E0.bottom"),sQuery(id+"F0.wireOp",EDGE,"E0.top"),sQuery(id+"F0.wireOp",EDGE,"E0.left"),sQuery(id+"F0.wireOp",EDGE,"E0.right")])]}),"instanceName":"1"}),"instanceName":"1"}),"instanceName":"1"}),"instanceName":"1"}),"instanceName":"1"}),"instanceName":"1"}),"instanceName":"1"}),"instanceName":"1"}),"instanceName":"1"});
            var Q169;
            Q169=makeQuery(id+"F45.opPattern","COPY",BODY,{"derivedFrom":makeQuery(id+"F40.opPattern","COPY",BODY,{"derivedFrom":makeQuery(id+"F23.opPattern","COPY",BODY,{"derivedFrom":makeQuery(id+"F19.opPattern","COPY",BODY,{"derivedFrom":makeQuery(id+"F17.opPattern","COPY",BODY,{"derivedFrom":makeQuery(id+"F12.opPattern","COPY",BODY,{"derivedFrom":makeQuery(id+"F6.opPattern","COPY",BODY,{"derivedFrom":makeQuery(id+"F5.opPattern","COPY",BODY,{"derivedFrom":makeQuery(id+"F4.opPattern","COPY",BODY,{"derivedFrom":makeQuery(id+"F1.opExtrude","SWEPT_BODY",BODY,{"disambiguationData":[OSD([sQuery(id+"F0.wireOp",EDGE,"E0.bottom"),sQuery(id+"F0.wireOp",EDGE,"E0.top"),sQuery(id+"F0.wireOp",EDGE,"E0.left"),sQuery(id+"F0.wireOp",EDGE,"E0.right")])]}),"instanceName":"1"}),"instanceName":"1"}),"instanceName":"1"}),"instanceName":"1"}),"instanceName":"1"}),"instanceName":"1"}),"instanceName":"1"}),"instanceName":"1"}),"instanceName":"1"});
            var Q170;
            Q170=makeQuery(id+"F4.opPattern","COPY",BODY,{"derivedFrom":makeQuery(id+"F2.opPattern","COPY",BODY,{"derivedFrom":makeQuery(id+"F1.opExtrude","SWEPT_BODY",BODY,{"disambiguationData":[OSD([sQuery(id+"F0.wireOp",EDGE,"E0.bottom"),sQuery(id+"F0.wireOp",EDGE,"E0.top"),sQuery(id+"F0.wireOp",EDGE,"E0.left"),sQuery(id+"F0.wireOp",EDGE,"E0.right")])]}),"instanceName":"1"}),"instanceName":"1"});
            var Q171;
            Q171=makeQuery(id+"F45.opPattern","COPY",BODY,{"derivedFrom":makeQuery(id+"F40.opPattern","COPY",BODY,{"derivedFrom":makeQuery(id+"F21.opPattern","COPY",BODY,{"derivedFrom":makeQuery(id+"F19.opPattern","COPY",BODY,{"derivedFrom":makeQuery(id+"F17.opPattern","COPY",BODY,{"derivedFrom":makeQuery(id+"F6.opPattern","COPY",BODY,{"derivedFrom":makeQuery(id+"F5.opPattern","COPY",BODY,{"derivedFrom":makeQuery(id+"F4.opPattern","COPY",BODY,{"derivedFrom":makeQuery(id+"F2.opPattern","COPY",BODY,{"derivedFrom":makeQuery(id+"F1.opExtrude","SWEPT_BODY",BODY,{"disambiguationData":[OSD([sQuery(id+"F0.wireOp",EDGE,"E0.bottom"),sQuery(id+"F0.wireOp",EDGE,"E0.top"),sQuery(id+"F0.wireOp",EDGE,"E0.left"),sQuery(id+"F0.wireOp",EDGE,"E0.right")])]}),"instanceName":"1"}),"instanceName":"1"}),"instanceName":"1"}),"instanceName":"1"}),"instanceName":"1"}),"instanceName":"1"}),"instanceName":"1"}),"instanceName":"1"}),"instanceName":"1"});
            var Q172;
            Q172=makeQuery(id+"F23.opPattern","COPY",BODY,{"derivedFrom":makeQuery(id+"F21.opPattern","COPY",BODY,{"derivedFrom":makeQuery(id+"F19.opPattern","COPY",BODY,{"derivedFrom":makeQuery(id+"F5.opPattern","COPY",BODY,{"derivedFrom":makeQuery(id+"F4.opPattern","COPY",BODY,{"derivedFrom":makeQuery(id+"F2.opPattern","COPY",BODY,{"derivedFrom":makeQuery(id+"F1.opExtrude","SWEPT_BODY",BODY,{"disambiguationData":[OSD([sQuery(id+"F0.wireOp",EDGE,"E0.bottom"),sQuery(id+"F0.wireOp",EDGE,"E0.top"),sQuery(id+"F0.wireOp",EDGE,"E0.left"),sQuery(id+"F0.wireOp",EDGE,"E0.right")])]}),"instanceName":"1"}),"instanceName":"1"}),"instanceName":"1"}),"instanceName":"1"}),"instanceName":"1"}),"instanceName":"1"});
            var Q173;
            Q173=makeQuery(id+"F40.opPattern","COPY",BODY,{"derivedFrom":makeQuery(id+"F23.opPattern","COPY",BODY,{"derivedFrom":makeQuery(id+"F21.opPattern","COPY",BODY,{"derivedFrom":makeQuery(id+"F19.opPattern","COPY",BODY,{"derivedFrom":makeQuery(id+"F17.opPattern","COPY",BODY,{"derivedFrom":makeQuery(id+"F6.opPattern","COPY",BODY,{"derivedFrom":makeQuery(id+"F5.opPattern","COPY",BODY,{"derivedFrom":makeQuery(id+"F4.opPattern","COPY",BODY,{"derivedFrom":makeQuery(id+"F1.opExtrude","SWEPT_BODY",BODY,{"disambiguationData":[OSD([sQuery(id+"F0.wireOp",EDGE,"E0.bottom"),sQuery(id+"F0.wireOp",EDGE,"E0.top"),sQuery(id+"F0.wireOp",EDGE,"E0.left"),sQuery(id+"F0.wireOp",EDGE,"E0.right")])]}),"instanceName":"1"}),"instanceName":"1"}),"instanceName":"1"}),"instanceName":"1"}),"instanceName":"1"}),"instanceName":"1"}),"instanceName":"1"}),"instanceName":"1"});
            var Q174;
            Q174=makeQuery(id+"F28.opPattern","COPY",BODY,{"derivedFrom":makeQuery(id+"F26.opPattern","COPY",BODY,{"derivedFrom":makeQuery(id+"F19.opPattern","COPY",BODY,{"derivedFrom":makeQuery(id+"F17.opPattern","COPY",BODY,{"derivedFrom":makeQuery(id+"F13.opPattern","COPY",BODY,{"derivedFrom":makeQuery(id+"F5.opPattern","COPY",BODY,{"derivedFrom":makeQuery(id+"F4.opPattern","COPY",BODY,{"derivedFrom":makeQuery(id+"F1.opExtrude","SWEPT_BODY",BODY,{"disambiguationData":[OSD([sQuery(id+"F0.wireOp",EDGE,"E0.bottom"),sQuery(id+"F0.wireOp",EDGE,"E0.top"),sQuery(id+"F0.wireOp",EDGE,"E0.left"),sQuery(id+"F0.wireOp",EDGE,"E0.right")])]}),"instanceName":"1"}),"instanceName":"1"}),"instanceName":"1"}),"instanceName":"1"}),"instanceName":"1"}),"instanceName":"1"}),"instanceName":"1"});
            var Q175;
            Q175=makeQuery(id+"F19.opPattern","COPY",BODY,{"derivedFrom":makeQuery(id+"F17.opPattern","COPY",BODY,{"derivedFrom":makeQuery(id+"F13.opPattern","COPY",BODY,{"derivedFrom":makeQuery(id+"F5.opPattern","COPY",BODY,{"derivedFrom":makeQuery(id+"F4.opPattern","COPY",BODY,{"derivedFrom":makeQuery(id+"F1.opExtrude","SWEPT_BODY",BODY,{"disambiguationData":[OSD([sQuery(id+"F0.wireOp",EDGE,"E0.bottom"),sQuery(id+"F0.wireOp",EDGE,"E0.top"),sQuery(id+"F0.wireOp",EDGE,"E0.left"),sQuery(id+"F0.wireOp",EDGE,"E0.right")])]}),"instanceName":"1"}),"instanceName":"1"}),"instanceName":"1"}),"instanceName":"1"}),"instanceName":"1"});
            var Q176;
            Q176=makeQuery(id+"F45.opPattern","COPY",BODY,{"derivedFrom":makeQuery(id+"F40.opPattern","COPY",BODY,{"derivedFrom":makeQuery(id+"F23.opPattern","COPY",BODY,{"derivedFrom":makeQuery(id+"F21.opPattern","COPY",BODY,{"derivedFrom":makeQuery(id+"F19.opPattern","COPY",BODY,{"derivedFrom":makeQuery(id+"F12.opPattern","COPY",BODY,{"derivedFrom":makeQuery(id+"F6.opPattern","COPY",BODY,{"derivedFrom":makeQuery(id+"F5.opPattern","COPY",BODY,{"derivedFrom":makeQuery(id+"F4.opPattern","COPY",BODY,{"derivedFrom":makeQuery(id+"F2.opPattern","COPY",BODY,{"derivedFrom":makeQuery(id+"F1.opExtrude","SWEPT_BODY",BODY,{"disambiguationData":[OSD([sQuery(id+"F0.wireOp",EDGE,"E0.bottom"),sQuery(id+"F0.wireOp",EDGE,"E0.top"),sQuery(id+"F0.wireOp",EDGE,"E0.left"),sQuery(id+"F0.wireOp",EDGE,"E0.right")])]}),"instanceName":"1"}),"instanceName":"1"}),"instanceName":"1"}),"instanceName":"1"}),"instanceName":"1"}),"instanceName":"1"}),"instanceName":"1"}),"instanceName":"1"}),"instanceName":"1"}),"instanceName":"1"});
            var Q177;
            Q177=makeQuery(id+"F37.opPattern","COPY",BODY,{"derivedFrom":makeQuery(id+"F35.opPattern","COPY",BODY,{"derivedFrom":makeQuery(id+"F31.opPattern","COPY",BODY,{"derivedFrom":makeQuery(id+"F4.opPattern","COPY",BODY,{"derivedFrom":makeQuery(id+"F1.opExtrude","SWEPT_BODY",BODY,{"disambiguationData":[OSD([sQuery(id+"F0.wireOp",EDGE,"E0.bottom"),sQuery(id+"F0.wireOp",EDGE,"E0.top"),sQuery(id+"F0.wireOp",EDGE,"E0.left"),sQuery(id+"F0.wireOp",EDGE,"E0.right")])]}),"instanceName":"1"}),"instanceName":"1"}),"instanceName":"1"}),"instanceName":"1"});
            var Q178;
            Q178=makeQuery(id+"F19.opPattern","COPY",BODY,{"derivedFrom":makeQuery(id+"F17.opPattern","COPY",BODY,{"derivedFrom":makeQuery(id+"F5.opPattern","COPY",BODY,{"derivedFrom":makeQuery(id+"F4.opPattern","COPY",BODY,{"derivedFrom":makeQuery(id+"F1.opExtrude","SWEPT_BODY",BODY,{"disambiguationData":[OSD([sQuery(id+"F0.wireOp",EDGE,"E0.bottom"),sQuery(id+"F0.wireOp",EDGE,"E0.top"),sQuery(id+"F0.wireOp",EDGE,"E0.left"),sQuery(id+"F0.wireOp",EDGE,"E0.right")])]}),"instanceName":"1"}),"instanceName":"1"}),"instanceName":"1"}),"instanceName":"1"});
            var Q179;
            Q179=makeQuery(id+"F40.opPattern","COPY",BODY,{"derivedFrom":makeQuery(id+"F23.opPattern","COPY",BODY,{"derivedFrom":makeQuery(id+"F21.opPattern","COPY",BODY,{"derivedFrom":makeQuery(id+"F19.opPattern","COPY",BODY,{"derivedFrom":makeQuery(id+"F5.opPattern","COPY",BODY,{"derivedFrom":makeQuery(id+"F4.opPattern","COPY",BODY,{"derivedFrom":makeQuery(id+"F2.opPattern","COPY",BODY,{"derivedFrom":makeQuery(id+"F1.opExtrude","SWEPT_BODY",BODY,{"disambiguationData":[OSD([sQuery(id+"F0.wireOp",EDGE,"E0.bottom"),sQuery(id+"F0.wireOp",EDGE,"E0.top"),sQuery(id+"F0.wireOp",EDGE,"E0.left"),sQuery(id+"F0.wireOp",EDGE,"E0.right")])]}),"instanceName":"1"}),"instanceName":"1"}),"instanceName":"1"}),"instanceName":"1"}),"instanceName":"1"}),"instanceName":"1"}),"instanceName":"1"});
            var Q180;
            Q180=makeQuery(id+"F42.opPattern","COPY",BODY,{"derivedFrom":makeQuery(id+"F23.opPattern","COPY",BODY,{"derivedFrom":makeQuery(id+"F19.opPattern","COPY",BODY,{"derivedFrom":makeQuery(id+"F17.opPattern","COPY",BODY,{"derivedFrom":makeQuery(id+"F13.opPattern","COPY",BODY,{"derivedFrom":makeQuery(id+"F5.opPattern","COPY",BODY,{"derivedFrom":makeQuery(id+"F4.opPattern","COPY",BODY,{"derivedFrom":makeQuery(id+"F1.opExtrude","SWEPT_BODY",BODY,{"disambiguationData":[OSD([sQuery(id+"F0.wireOp",EDGE,"E0.bottom"),sQuery(id+"F0.wireOp",EDGE,"E0.top"),sQuery(id+"F0.wireOp",EDGE,"E0.left"),sQuery(id+"F0.wireOp",EDGE,"E0.right")])]}),"instanceName":"1"}),"instanceName":"1"}),"instanceName":"1"}),"instanceName":"1"}),"instanceName":"1"}),"instanceName":"1"}),"instanceName":"1"});
            var Q181;
            Q181=makeQuery(id+"F23.opPattern","COPY",BODY,{"derivedFrom":makeQuery(id+"F19.opPattern","COPY",BODY,{"derivedFrom":makeQuery(id+"F5.opPattern","COPY",BODY,{"derivedFrom":makeQuery(id+"F4.opPattern","COPY",BODY,{"derivedFrom":makeQuery(id+"F2.opPattern","COPY",BODY,{"derivedFrom":makeQuery(id+"F1.opExtrude","SWEPT_BODY",BODY,{"disambiguationData":[OSD([sQuery(id+"F0.wireOp",EDGE,"E0.bottom"),sQuery(id+"F0.wireOp",EDGE,"E0.top"),sQuery(id+"F0.wireOp",EDGE,"E0.left"),sQuery(id+"F0.wireOp",EDGE,"E0.right")])]}),"instanceName":"1"}),"instanceName":"1"}),"instanceName":"1"}),"instanceName":"1"}),"instanceName":"1"});
            var Q182;
            Q182=makeQuery(id+"F29.opPattern","COPY",BODY,{"derivedFrom":makeQuery(id+"F23.opPattern","COPY",BODY,{"derivedFrom":makeQuery(id+"F19.opPattern","COPY",BODY,{"derivedFrom":makeQuery(id+"F17.opPattern","COPY",BODY,{"derivedFrom":makeQuery(id+"F13.opPattern","COPY",BODY,{"derivedFrom":makeQuery(id+"F5.opPattern","COPY",BODY,{"derivedFrom":makeQuery(id+"F4.opPattern","COPY",BODY,{"derivedFrom":makeQuery(id+"F1.opExtrude","SWEPT_BODY",BODY,{"disambiguationData":[OSD([sQuery(id+"F0.wireOp",EDGE,"E0.bottom"),sQuery(id+"F0.wireOp",EDGE,"E0.top"),sQuery(id+"F0.wireOp",EDGE,"E0.left"),sQuery(id+"F0.wireOp",EDGE,"E0.right")])]}),"instanceName":"1"}),"instanceName":"1"}),"instanceName":"1"}),"instanceName":"1"}),"instanceName":"1"}),"instanceName":"1"}),"instanceName":"1"});
            var Q183;
            Q183=makeQuery(id+"F35.opPattern","COPY",BODY,{"derivedFrom":makeQuery(id+"F34.opPattern","COPY",BODY,{"derivedFrom":makeQuery(id+"F31.opPattern","COPY",BODY,{"derivedFrom":makeQuery(id+"F4.opPattern","COPY",BODY,{"derivedFrom":makeQuery(id+"F2.opPattern","COPY",BODY,{"derivedFrom":makeQuery(id+"F1.opExtrude","SWEPT_BODY",BODY,{"disambiguationData":[OSD([sQuery(id+"F0.wireOp",EDGE,"E0.bottom"),sQuery(id+"F0.wireOp",EDGE,"E0.top"),sQuery(id+"F0.wireOp",EDGE,"E0.left"),sQuery(id+"F0.wireOp",EDGE,"E0.right")])]}),"instanceName":"1"}),"instanceName":"1"}),"instanceName":"1"}),"instanceName":"1"}),"instanceName":"1"});
            var Q184;
            Q184=makeQuery(id+"F19.opPattern","COPY",BODY,{"derivedFrom":makeQuery(id+"F5.opPattern","COPY",BODY,{"derivedFrom":makeQuery(id+"F4.opPattern","COPY",BODY,{"derivedFrom":makeQuery(id+"F2.opPattern","COPY",BODY,{"derivedFrom":makeQuery(id+"F1.opExtrude","SWEPT_BODY",BODY,{"disambiguationData":[OSD([sQuery(id+"F0.wireOp",EDGE,"E0.bottom"),sQuery(id+"F0.wireOp",EDGE,"E0.top"),sQuery(id+"F0.wireOp",EDGE,"E0.left"),sQuery(id+"F0.wireOp",EDGE,"E0.right")])]}),"instanceName":"1"}),"instanceName":"1"}),"instanceName":"1"}),"instanceName":"1"});
            var Q185;
            Q185=makeQuery(id+"F40.opPattern","COPY",BODY,{"derivedFrom":makeQuery(id+"F24.opPattern","COPY",BODY,{"derivedFrom":makeQuery(id+"F23.opPattern","COPY",BODY,{"derivedFrom":makeQuery(id+"F19.opPattern","COPY",BODY,{"derivedFrom":makeQuery(id+"F17.opPattern","COPY",BODY,{"derivedFrom":makeQuery(id+"F5.opPattern","COPY",BODY,{"derivedFrom":makeQuery(id+"F4.opPattern","COPY",BODY,{"derivedFrom":makeQuery(id+"F1.opExtrude","SWEPT_BODY",BODY,{"disambiguationData":[OSD([sQuery(id+"F0.wireOp",EDGE,"E0.bottom"),sQuery(id+"F0.wireOp",EDGE,"E0.top"),sQuery(id+"F0.wireOp",EDGE,"E0.left"),sQuery(id+"F0.wireOp",EDGE,"E0.right")])]}),"instanceName":"1"}),"instanceName":"1"}),"instanceName":"1"}),"instanceName":"1"}),"instanceName":"1"}),"instanceName":"1"}),"instanceName":"1"});
            var Q186;
            Q186=makeQuery(id+"F29.opPattern","COPY",BODY,{"derivedFrom":makeQuery(id+"F26.opPattern","COPY",BODY,{"derivedFrom":makeQuery(id+"F19.opPattern","COPY",BODY,{"derivedFrom":makeQuery(id+"F13.opPattern","COPY",BODY,{"derivedFrom":makeQuery(id+"F5.opPattern","COPY",BODY,{"derivedFrom":makeQuery(id+"F4.opPattern","COPY",BODY,{"derivedFrom":makeQuery(id+"F1.opExtrude","SWEPT_BODY",BODY,{"disambiguationData":[OSD([sQuery(id+"F0.wireOp",EDGE,"E0.bottom"),sQuery(id+"F0.wireOp",EDGE,"E0.top"),sQuery(id+"F0.wireOp",EDGE,"E0.left"),sQuery(id+"F0.wireOp",EDGE,"E0.right")])]}),"instanceName":"1"}),"instanceName":"1"}),"instanceName":"1"}),"instanceName":"1"}),"instanceName":"1"}),"instanceName":"1"});
            var Q187;
            Q187=makeQuery(id+"F42.opPattern","COPY",BODY,{"derivedFrom":makeQuery(id+"F29.opPattern","COPY",BODY,{"derivedFrom":makeQuery(id+"F28.opPattern","COPY",BODY,{"derivedFrom":makeQuery(id+"F19.opPattern","COPY",BODY,{"derivedFrom":makeQuery(id+"F17.opPattern","COPY",BODY,{"derivedFrom":makeQuery(id+"F15.opPattern","COPY",BODY,{"derivedFrom":makeQuery(id+"F12.opPattern","COPY",BODY,{"derivedFrom":makeQuery(id+"F6.opPattern","COPY",BODY,{"derivedFrom":makeQuery(id+"F5.opPattern","COPY",BODY,{"derivedFrom":makeQuery(id+"F4.opPattern","COPY",BODY,{"derivedFrom":makeQuery(id+"F2.opPattern","COPY",BODY,{"derivedFrom":makeQuery(id+"F1.opExtrude","SWEPT_BODY",BODY,{"disambiguationData":[OSD([sQuery(id+"F0.wireOp",EDGE,"E0.bottom"),sQuery(id+"F0.wireOp",EDGE,"E0.top"),sQuery(id+"F0.wireOp",EDGE,"E0.left"),sQuery(id+"F0.wireOp",EDGE,"E0.right")])]}),"instanceName":"1"}),"instanceName":"1"}),"instanceName":"1"}),"instanceName":"1"}),"instanceName":"1"}),"instanceName":"1"}),"instanceName":"1"}),"instanceName":"1"}),"instanceName":"1"}),"instanceName":"1"}),"instanceName":"1"});
            var Q188;
            Q188=makeQuery(id+"F40.opPattern","COPY",BODY,{"derivedFrom":makeQuery(id+"F23.opPattern","COPY",BODY,{"derivedFrom":makeQuery(id+"F19.opPattern","COPY",BODY,{"derivedFrom":makeQuery(id+"F12.opPattern","COPY",BODY,{"derivedFrom":makeQuery(id+"F6.opPattern","COPY",BODY,{"derivedFrom":makeQuery(id+"F5.opPattern","COPY",BODY,{"derivedFrom":makeQuery(id+"F4.opPattern","COPY",BODY,{"derivedFrom":makeQuery(id+"F2.opPattern","COPY",BODY,{"derivedFrom":makeQuery(id+"F1.opExtrude","SWEPT_BODY",BODY,{"disambiguationData":[OSD([sQuery(id+"F0.wireOp",EDGE,"E0.bottom"),sQuery(id+"F0.wireOp",EDGE,"E0.top"),sQuery(id+"F0.wireOp",EDGE,"E0.left"),sQuery(id+"F0.wireOp",EDGE,"E0.right")])]}),"instanceName":"1"}),"instanceName":"1"}),"instanceName":"1"}),"instanceName":"1"}),"instanceName":"1"}),"instanceName":"1"}),"instanceName":"1"}),"instanceName":"1"});
            var Q189;
            Q189=makeQuery(id+"F45.opPattern","COPY",BODY,{"derivedFrom":makeQuery(id+"F40.opPattern","COPY",BODY,{"derivedFrom":makeQuery(id+"F23.opPattern","COPY",BODY,{"derivedFrom":makeQuery(id+"F19.opPattern","COPY",BODY,{"derivedFrom":makeQuery(id+"F12.opPattern","COPY",BODY,{"derivedFrom":makeQuery(id+"F6.opPattern","COPY",BODY,{"derivedFrom":makeQuery(id+"F5.opPattern","COPY",BODY,{"derivedFrom":makeQuery(id+"F4.opPattern","COPY",BODY,{"derivedFrom":makeQuery(id+"F2.opPattern","COPY",BODY,{"derivedFrom":makeQuery(id+"F1.opExtrude","SWEPT_BODY",BODY,{"disambiguationData":[OSD([sQuery(id+"F0.wireOp",EDGE,"E0.bottom"),sQuery(id+"F0.wireOp",EDGE,"E0.top"),sQuery(id+"F0.wireOp",EDGE,"E0.left"),sQuery(id+"F0.wireOp",EDGE,"E0.right")])]}),"instanceName":"1"}),"instanceName":"1"}),"instanceName":"1"}),"instanceName":"1"}),"instanceName":"1"}),"instanceName":"1"}),"instanceName":"1"}),"instanceName":"1"}),"instanceName":"1"});
            var Q190;
            Q190=makeQuery(id+"F13.opPattern","COPY",BODY,{"derivedFrom":makeQuery(id+"F6.opPattern","COPY",BODY,{"derivedFrom":makeQuery(id+"F5.opPattern","COPY",BODY,{"derivedFrom":makeQuery(id+"F4.opPattern","COPY",BODY,{"derivedFrom":makeQuery(id+"F1.opExtrude","SWEPT_BODY",BODY,{"disambiguationData":[OSD([sQuery(id+"F0.wireOp",EDGE,"E0.bottom"),sQuery(id+"F0.wireOp",EDGE,"E0.top"),sQuery(id+"F0.wireOp",EDGE,"E0.left"),sQuery(id+"F0.wireOp",EDGE,"E0.right")])]}),"instanceName":"1"}),"instanceName":"1"}),"instanceName":"1"}),"instanceName":"1"});
            var Q191;
            Q191=makeQuery(id+"F23.opPattern","COPY",BODY,{"derivedFrom":makeQuery(id+"F21.opPattern","COPY",BODY,{"derivedFrom":makeQuery(id+"F19.opPattern","COPY",BODY,{"derivedFrom":makeQuery(id+"F17.opPattern","COPY",BODY,{"derivedFrom":makeQuery(id+"F5.opPattern","COPY",BODY,{"derivedFrom":makeQuery(id+"F4.opPattern","COPY",BODY,{"derivedFrom":makeQuery(id+"F1.opExtrude","SWEPT_BODY",BODY,{"disambiguationData":[OSD([sQuery(id+"F0.wireOp",EDGE,"E0.bottom"),sQuery(id+"F0.wireOp",EDGE,"E0.top"),sQuery(id+"F0.wireOp",EDGE,"E0.left"),sQuery(id+"F0.wireOp",EDGE,"E0.right")])]}),"instanceName":"1"}),"instanceName":"1"}),"instanceName":"1"}),"instanceName":"1"}),"instanceName":"1"}),"instanceName":"1"});
            var Q192;
            Q192=makeQuery(id+"F26.opPattern","COPY",BODY,{"derivedFrom":makeQuery(id+"F21.opPattern","COPY",BODY,{"derivedFrom":makeQuery(id+"F19.opPattern","COPY",BODY,{"derivedFrom":makeQuery(id+"F5.opPattern","COPY",BODY,{"derivedFrom":makeQuery(id+"F4.opPattern","COPY",BODY,{"derivedFrom":makeQuery(id+"F1.opExtrude","SWEPT_BODY",BODY,{"disambiguationData":[OSD([sQuery(id+"F0.wireOp",EDGE,"E0.bottom"),sQuery(id+"F0.wireOp",EDGE,"E0.top"),sQuery(id+"F0.wireOp",EDGE,"E0.left"),sQuery(id+"F0.wireOp",EDGE,"E0.right")])]}),"instanceName":"1"}),"instanceName":"1"}),"instanceName":"1"}),"instanceName":"1"}),"instanceName":"1"});
            var Q193;
            Q193=makeQuery(id+"F40.opPattern","COPY",BODY,{"derivedFrom":makeQuery(id+"F29.opPattern","COPY",BODY,{"derivedFrom":makeQuery(id+"F19.opPattern","COPY",BODY,{"derivedFrom":makeQuery(id+"F17.opPattern","COPY",BODY,{"derivedFrom":makeQuery(id+"F15.opPattern","COPY",BODY,{"derivedFrom":makeQuery(id+"F12.opPattern","COPY",BODY,{"derivedFrom":makeQuery(id+"F6.opPattern","COPY",BODY,{"derivedFrom":makeQuery(id+"F5.opPattern","COPY",BODY,{"derivedFrom":makeQuery(id+"F4.opPattern","COPY",BODY,{"derivedFrom":makeQuery(id+"F2.opPattern","COPY",BODY,{"derivedFrom":makeQuery(id+"F1.opExtrude","SWEPT_BODY",BODY,{"disambiguationData":[OSD([sQuery(id+"F0.wireOp",EDGE,"E0.bottom"),sQuery(id+"F0.wireOp",EDGE,"E0.top"),sQuery(id+"F0.wireOp",EDGE,"E0.left"),sQuery(id+"F0.wireOp",EDGE,"E0.right")])]}),"instanceName":"1"}),"instanceName":"1"}),"instanceName":"1"}),"instanceName":"1"}),"instanceName":"1"}),"instanceName":"1"}),"instanceName":"1"}),"instanceName":"1"}),"instanceName":"1"}),"instanceName":"1"});
            var Q194;
            Q194=makeQuery(id+"F40.opPattern","COPY",BODY,{"derivedFrom":makeQuery(id+"F28.opPattern","COPY",BODY,{"derivedFrom":makeQuery(id+"F19.opPattern","COPY",BODY,{"derivedFrom":makeQuery(id+"F13.opPattern","COPY",BODY,{"derivedFrom":makeQuery(id+"F5.opPattern","COPY",BODY,{"derivedFrom":makeQuery(id+"F4.opPattern","COPY",BODY,{"derivedFrom":makeQuery(id+"F1.opExtrude","SWEPT_BODY",BODY,{"disambiguationData":[OSD([sQuery(id+"F0.wireOp",EDGE,"E0.bottom"),sQuery(id+"F0.wireOp",EDGE,"E0.top"),sQuery(id+"F0.wireOp",EDGE,"E0.left"),sQuery(id+"F0.wireOp",EDGE,"E0.right")])]}),"instanceName":"1"}),"instanceName":"1"}),"instanceName":"1"}),"instanceName":"1"}),"instanceName":"1"}),"instanceName":"1"});
            var Q195;
            Q195=makeQuery(id+"F40.opPattern","COPY",BODY,{"derivedFrom":makeQuery(id+"F23.opPattern","COPY",BODY,{"derivedFrom":makeQuery(id+"F21.opPattern","COPY",BODY,{"derivedFrom":makeQuery(id+"F19.opPattern","COPY",BODY,{"derivedFrom":makeQuery(id+"F17.opPattern","COPY",BODY,{"derivedFrom":makeQuery(id+"F12.opPattern","COPY",BODY,{"derivedFrom":makeQuery(id+"F6.opPattern","COPY",BODY,{"derivedFrom":makeQuery(id+"F5.opPattern","COPY",BODY,{"derivedFrom":makeQuery(id+"F4.opPattern","COPY",BODY,{"derivedFrom":makeQuery(id+"F1.opExtrude","SWEPT_BODY",BODY,{"disambiguationData":[OSD([sQuery(id+"F0.wireOp",EDGE,"E0.bottom"),sQuery(id+"F0.wireOp",EDGE,"E0.top"),sQuery(id+"F0.wireOp",EDGE,"E0.left"),sQuery(id+"F0.wireOp",EDGE,"E0.right")])]}),"instanceName":"1"}),"instanceName":"1"}),"instanceName":"1"}),"instanceName":"1"}),"instanceName":"1"}),"instanceName":"1"}),"instanceName":"1"}),"instanceName":"1"}),"instanceName":"1"});
            var Q196;
            Q196=makeQuery(id+"F22.opPattern","COPY",BODY,{"derivedFrom":makeQuery(id+"F21.opPattern","COPY",BODY,{"derivedFrom":makeQuery(id+"F19.opPattern","COPY",BODY,{"derivedFrom":makeQuery(id+"F6.opPattern","COPY",BODY,{"derivedFrom":makeQuery(id+"F5.opPattern","COPY",BODY,{"derivedFrom":makeQuery(id+"F4.opPattern","COPY",BODY,{"derivedFrom":makeQuery(id+"F2.opPattern","COPY",BODY,{"derivedFrom":makeQuery(id+"F1.opExtrude","SWEPT_BODY",BODY,{"disambiguationData":[OSD([sQuery(id+"F0.wireOp",EDGE,"E0.bottom"),sQuery(id+"F0.wireOp",EDGE,"E0.top"),sQuery(id+"F0.wireOp",EDGE,"E0.left"),sQuery(id+"F0.wireOp",EDGE,"E0.right")])]}),"instanceName":"1"}),"instanceName":"1"}),"instanceName":"1"}),"instanceName":"1"}),"instanceName":"1"}),"instanceName":"1"}),"instanceName":"1"});
            var Q197;
            Q197=makeQuery(id+"F17.opPattern","COPY",BODY,{"derivedFrom":makeQuery(id+"F5.opPattern","COPY",BODY,{"derivedFrom":makeQuery(id+"F4.opPattern","COPY",BODY,{"derivedFrom":makeQuery(id+"F1.opExtrude","SWEPT_BODY",BODY,{"disambiguationData":[OSD([sQuery(id+"F0.wireOp",EDGE,"E0.bottom"),sQuery(id+"F0.wireOp",EDGE,"E0.top"),sQuery(id+"F0.wireOp",EDGE,"E0.left"),sQuery(id+"F0.wireOp",EDGE,"E0.right")])]}),"instanceName":"1"}),"instanceName":"1"}),"instanceName":"1"});
            var Q198;
            Q198=makeQuery(id+"F40.opPattern","COPY",BODY,{"derivedFrom":makeQuery(id+"F23.opPattern","COPY",BODY,{"derivedFrom":makeQuery(id+"F19.opPattern","COPY",BODY,{"derivedFrom":makeQuery(id+"F5.opPattern","COPY",BODY,{"derivedFrom":makeQuery(id+"F4.opPattern","COPY",BODY,{"derivedFrom":makeQuery(id+"F2.opPattern","COPY",BODY,{"derivedFrom":makeQuery(id+"F1.opExtrude","SWEPT_BODY",BODY,{"disambiguationData":[OSD([sQuery(id+"F0.wireOp",EDGE,"E0.bottom"),sQuery(id+"F0.wireOp",EDGE,"E0.top"),sQuery(id+"F0.wireOp",EDGE,"E0.left"),sQuery(id+"F0.wireOp",EDGE,"E0.right")])]}),"instanceName":"1"}),"instanceName":"1"}),"instanceName":"1"}),"instanceName":"1"}),"instanceName":"1"}),"instanceName":"1"});
            var Q199;
            Q199=makeQuery(id+"F18.opPattern","COPY",BODY,{"derivedFrom":makeQuery(id+"F17.opPattern","COPY",BODY,{"derivedFrom":makeQuery(id+"F8.opPattern","COPY",BODY,{"derivedFrom":makeQuery(id+"F5.opPattern","COPY",BODY,{"derivedFrom":makeQuery(id+"F4.opPattern","COPY",BODY,{"derivedFrom":makeQuery(id+"F2.opPattern","COPY",BODY,{"derivedFrom":makeQuery(id+"F1.opExtrude","SWEPT_BODY",BODY,{"disambiguationData":[OSD([sQuery(id+"F0.wireOp",EDGE,"E0.bottom"),sQuery(id+"F0.wireOp",EDGE,"E0.top"),sQuery(id+"F0.wireOp",EDGE,"E0.left"),sQuery(id+"F0.wireOp",EDGE,"E0.right")])]}),"instanceName":"1"}),"instanceName":"1"}),"instanceName":"1"}),"instanceName":"1"}),"instanceName":"1"}),"instanceName":"1"});
            var Q200;
            Q200=makeQuery(id+"F6.opPattern","COPY",BODY,{"derivedFrom":makeQuery(id+"F4.opPattern","COPY",BODY,{"derivedFrom":makeQuery(id+"F2.opPattern","COPY",BODY,{"derivedFrom":makeQuery(id+"F1.opExtrude","SWEPT_BODY",BODY,{"disambiguationData":[OSD([sQuery(id+"F0.wireOp",EDGE,"E0.bottom"),sQuery(id+"F0.wireOp",EDGE,"E0.top"),sQuery(id+"F0.wireOp",EDGE,"E0.left"),sQuery(id+"F0.wireOp",EDGE,"E0.right")])]}),"instanceName":"1"}),"instanceName":"1"}),"instanceName":"1"});
            var Q201;
            Q201=makeQuery(id+"F20.opPattern","COPY",BODY,{"derivedFrom":makeQuery(id+"F8.opPattern","COPY",BODY,{"derivedFrom":makeQuery(id+"F5.opPattern","COPY",BODY,{"derivedFrom":makeQuery(id+"F4.opPattern","COPY",BODY,{"derivedFrom":makeQuery(id+"F2.opPattern","COPY",BODY,{"derivedFrom":makeQuery(id+"F1.opExtrude","SWEPT_BODY",BODY,{"disambiguationData":[OSD([sQuery(id+"F0.wireOp",EDGE,"E0.bottom"),sQuery(id+"F0.wireOp",EDGE,"E0.top"),sQuery(id+"F0.wireOp",EDGE,"E0.left"),sQuery(id+"F0.wireOp",EDGE,"E0.right")])]}),"instanceName":"1"}),"instanceName":"1"}),"instanceName":"1"}),"instanceName":"1"}),"instanceName":"1"});
            var Q202;
            Q202=makeQuery(id+"F26.opPattern","COPY",BODY,{"derivedFrom":makeQuery(id+"F23.opPattern","COPY",BODY,{"derivedFrom":makeQuery(id+"F19.opPattern","COPY",BODY,{"derivedFrom":makeQuery(id+"F12.opPattern","COPY",BODY,{"derivedFrom":makeQuery(id+"F6.opPattern","COPY",BODY,{"derivedFrom":makeQuery(id+"F5.opPattern","COPY",BODY,{"derivedFrom":makeQuery(id+"F4.opPattern","COPY",BODY,{"derivedFrom":makeQuery(id+"F2.opPattern","COPY",BODY,{"derivedFrom":makeQuery(id+"F1.opExtrude","SWEPT_BODY",BODY,{"disambiguationData":[OSD([sQuery(id+"F0.wireOp",EDGE,"E0.bottom"),sQuery(id+"F0.wireOp",EDGE,"E0.top"),sQuery(id+"F0.wireOp",EDGE,"E0.left"),sQuery(id+"F0.wireOp",EDGE,"E0.right")])]}),"instanceName":"1"}),"instanceName":"1"}),"instanceName":"1"}),"instanceName":"1"}),"instanceName":"1"}),"instanceName":"1"}),"instanceName":"1"}),"instanceName":"1"});
            var Q203;
            Q203=makeQuery(id+"F40.opPattern","COPY",BODY,{"derivedFrom":makeQuery(id+"F26.opPattern","COPY",BODY,{"derivedFrom":makeQuery(id+"F17.opPattern","COPY",BODY,{"derivedFrom":makeQuery(id+"F12.opPattern","COPY",BODY,{"derivedFrom":makeQuery(id+"F6.opPattern","COPY",BODY,{"derivedFrom":makeQuery(id+"F5.opPattern","COPY",BODY,{"derivedFrom":makeQuery(id+"F4.opPattern","COPY",BODY,{"derivedFrom":makeQuery(id+"F2.opPattern","COPY",BODY,{"derivedFrom":makeQuery(id+"F1.opExtrude","SWEPT_BODY",BODY,{"disambiguationData":[OSD([sQuery(id+"F0.wireOp",EDGE,"E0.bottom"),sQuery(id+"F0.wireOp",EDGE,"E0.top"),sQuery(id+"F0.wireOp",EDGE,"E0.left"),sQuery(id+"F0.wireOp",EDGE,"E0.right")])]}),"instanceName":"1"}),"instanceName":"1"}),"instanceName":"1"}),"instanceName":"1"}),"instanceName":"1"}),"instanceName":"1"}),"instanceName":"1"}),"instanceName":"1"});
            var Q204;
            Q204=makeQuery(id+"F29.opPattern","COPY",BODY,{"derivedFrom":makeQuery(id+"F23.opPattern","COPY",BODY,{"derivedFrom":makeQuery(id+"F19.opPattern","COPY",BODY,{"derivedFrom":makeQuery(id+"F15.opPattern","COPY",BODY,{"derivedFrom":makeQuery(id+"F12.opPattern","COPY",BODY,{"derivedFrom":makeQuery(id+"F6.opPattern","COPY",BODY,{"derivedFrom":makeQuery(id+"F5.opPattern","COPY",BODY,{"derivedFrom":makeQuery(id+"F4.opPattern","COPY",BODY,{"derivedFrom":makeQuery(id+"F2.opPattern","COPY",BODY,{"derivedFrom":makeQuery(id+"F1.opExtrude","SWEPT_BODY",BODY,{"disambiguationData":[OSD([sQuery(id+"F0.wireOp",EDGE,"E0.bottom"),sQuery(id+"F0.wireOp",EDGE,"E0.top"),sQuery(id+"F0.wireOp",EDGE,"E0.left"),sQuery(id+"F0.wireOp",EDGE,"E0.right")])]}),"instanceName":"1"}),"instanceName":"1"}),"instanceName":"1"}),"instanceName":"1"}),"instanceName":"1"}),"instanceName":"1"}),"instanceName":"1"}),"instanceName":"1"}),"instanceName":"1"});
            var Q205;
            Q205=makeQuery(id+"F42.opPattern","COPY",BODY,{"derivedFrom":makeQuery(id+"F23.opPattern","COPY",BODY,{"derivedFrom":makeQuery(id+"F19.opPattern","COPY",BODY,{"derivedFrom":makeQuery(id+"F15.opPattern","COPY",BODY,{"derivedFrom":makeQuery(id+"F12.opPattern","COPY",BODY,{"derivedFrom":makeQuery(id+"F6.opPattern","COPY",BODY,{"derivedFrom":makeQuery(id+"F5.opPattern","COPY",BODY,{"derivedFrom":makeQuery(id+"F4.opPattern","COPY",BODY,{"derivedFrom":makeQuery(id+"F2.opPattern","COPY",BODY,{"derivedFrom":makeQuery(id+"F1.opExtrude","SWEPT_BODY",BODY,{"disambiguationData":[OSD([sQuery(id+"F0.wireOp",EDGE,"E0.bottom"),sQuery(id+"F0.wireOp",EDGE,"E0.top"),sQuery(id+"F0.wireOp",EDGE,"E0.left"),sQuery(id+"F0.wireOp",EDGE,"E0.right")])]}),"instanceName":"1"}),"instanceName":"1"}),"instanceName":"1"}),"instanceName":"1"}),"instanceName":"1"}),"instanceName":"1"}),"instanceName":"1"}),"instanceName":"1"}),"instanceName":"1"});
            var Q206;
            Q206=makeQuery(id+"F40.opPattern","COPY",BODY,{"derivedFrom":makeQuery(id+"F23.opPattern","COPY",BODY,{"derivedFrom":makeQuery(id+"F19.opPattern","COPY",BODY,{"derivedFrom":makeQuery(id+"F17.opPattern","COPY",BODY,{"derivedFrom":makeQuery(id+"F6.opPattern","COPY",BODY,{"derivedFrom":makeQuery(id+"F5.opPattern","COPY",BODY,{"derivedFrom":makeQuery(id+"F4.opPattern","COPY",BODY,{"derivedFrom":makeQuery(id+"F2.opPattern","COPY",BODY,{"derivedFrom":makeQuery(id+"F1.opExtrude","SWEPT_BODY",BODY,{"disambiguationData":[OSD([sQuery(id+"F0.wireOp",EDGE,"E0.bottom"),sQuery(id+"F0.wireOp",EDGE,"E0.top"),sQuery(id+"F0.wireOp",EDGE,"E0.left"),sQuery(id+"F0.wireOp",EDGE,"E0.right")])]}),"instanceName":"1"}),"instanceName":"1"}),"instanceName":"1"}),"instanceName":"1"}),"instanceName":"1"}),"instanceName":"1"}),"instanceName":"1"}),"instanceName":"1"});
            var Q207;
            Q207=makeQuery(id+"F38.opPattern","COPY",BODY,{"derivedFrom":makeQuery(id+"F35.opPattern","COPY",BODY,{"derivedFrom":makeQuery(id+"F34.opPattern","COPY",BODY,{"derivedFrom":makeQuery(id+"F31.opPattern","COPY",BODY,{"derivedFrom":makeQuery(id+"F5.opPattern","COPY",BODY,{"derivedFrom":makeQuery(id+"F2.opPattern","COPY",BODY,{"derivedFrom":makeQuery(id+"F1.opExtrude","SWEPT_BODY",BODY,{"disambiguationData":[OSD([sQuery(id+"F0.wireOp",EDGE,"E0.bottom"),sQuery(id+"F0.wireOp",EDGE,"E0.top"),sQuery(id+"F0.wireOp",EDGE,"E0.left"),sQuery(id+"F0.wireOp",EDGE,"E0.right")])]}),"instanceName":"1"}),"instanceName":"1"}),"instanceName":"1"}),"instanceName":"1"}),"instanceName":"1"}),"instanceName":"1"});
            var Q208;
            Q208=makeQuery(id+"F19.opPattern","COPY",BODY,{"derivedFrom":makeQuery(id+"F15.opPattern","COPY",BODY,{"derivedFrom":makeQuery(id+"F12.opPattern","COPY",BODY,{"derivedFrom":makeQuery(id+"F6.opPattern","COPY",BODY,{"derivedFrom":makeQuery(id+"F5.opPattern","COPY",BODY,{"derivedFrom":makeQuery(id+"F4.opPattern","COPY",BODY,{"derivedFrom":makeQuery(id+"F2.opPattern","COPY",BODY,{"derivedFrom":makeQuery(id+"F1.opExtrude","SWEPT_BODY",BODY,{"disambiguationData":[OSD([sQuery(id+"F0.wireOp",EDGE,"E0.bottom"),sQuery(id+"F0.wireOp",EDGE,"E0.top"),sQuery(id+"F0.wireOp",EDGE,"E0.left"),sQuery(id+"F0.wireOp",EDGE,"E0.right")])]}),"instanceName":"1"}),"instanceName":"1"}),"instanceName":"1"}),"instanceName":"1"}),"instanceName":"1"}),"instanceName":"1"}),"instanceName":"1"});
            var Q209;
            Q209=makeQuery(id+"F39.opPattern","COPY",BODY,{"derivedFrom":makeQuery(id+"F28.opPattern","COPY",BODY,{"derivedFrom":makeQuery(id+"F26.opPattern","COPY",BODY,{"derivedFrom":makeQuery(id+"F19.opPattern","COPY",BODY,{"derivedFrom":makeQuery(id+"F13.opPattern","COPY",BODY,{"derivedFrom":makeQuery(id+"F5.opPattern","COPY",BODY,{"derivedFrom":makeQuery(id+"F4.opPattern","COPY",BODY,{"derivedFrom":makeQuery(id+"F1.opExtrude","SWEPT_BODY",BODY,{"disambiguationData":[OSD([sQuery(id+"F0.wireOp",EDGE,"E0.bottom"),sQuery(id+"F0.wireOp",EDGE,"E0.top"),sQuery(id+"F0.wireOp",EDGE,"E0.left"),sQuery(id+"F0.wireOp",EDGE,"E0.right")])]}),"instanceName":"1"}),"instanceName":"1"}),"instanceName":"1"}),"instanceName":"1"}),"instanceName":"1"}),"instanceName":"1"}),"instanceName":"1"});
            var Q210;
            Q210=makeQuery(id+"F16.opPattern","COPY",BODY,{"derivedFrom":makeQuery(id+"F8.opPattern","COPY",BODY,{"derivedFrom":makeQuery(id+"F5.opPattern","COPY",BODY,{"derivedFrom":makeQuery(id+"F4.opPattern","COPY",BODY,{"derivedFrom":makeQuery(id+"F2.opPattern","COPY",BODY,{"derivedFrom":makeQuery(id+"F1.opExtrude","SWEPT_BODY",BODY,{"disambiguationData":[OSD([sQuery(id+"F0.wireOp",EDGE,"E0.bottom"),sQuery(id+"F0.wireOp",EDGE,"E0.top"),sQuery(id+"F0.wireOp",EDGE,"E0.left"),sQuery(id+"F0.wireOp",EDGE,"E0.right")])]}),"instanceName":"1"}),"instanceName":"1"}),"instanceName":"1"}),"instanceName":"1"}),"instanceName":"1"});
            var Q211;
            Q211=makeQuery(id+"F13.opPattern","COPY",BODY,{"derivedFrom":makeQuery(id+"F6.opPattern","COPY",BODY,{"derivedFrom":makeQuery(id+"F5.opPattern","COPY",BODY,{"derivedFrom":makeQuery(id+"F2.opPattern","COPY",BODY,{"derivedFrom":makeQuery(id+"F1.opExtrude","SWEPT_BODY",BODY,{"disambiguationData":[OSD([sQuery(id+"F0.wireOp",EDGE,"E0.bottom"),sQuery(id+"F0.wireOp",EDGE,"E0.top"),sQuery(id+"F0.wireOp",EDGE,"E0.left"),sQuery(id+"F0.wireOp",EDGE,"E0.right")])]}),"instanceName":"1"}),"instanceName":"1"}),"instanceName":"1"}),"instanceName":"1"});
            var Q212;
            Q212=makeQuery(id+"F14.opPattern","COPY",BODY,{"derivedFrom":makeQuery(id+"F13.opPattern","COPY",BODY,{"derivedFrom":makeQuery(id+"F12.opPattern","COPY",BODY,{"derivedFrom":makeQuery(id+"F6.opPattern","COPY",BODY,{"derivedFrom":makeQuery(id+"F5.opPattern","COPY",BODY,{"derivedFrom":makeQuery(id+"F2.opPattern","COPY",BODY,{"derivedFrom":makeQuery(id+"F1.opExtrude","SWEPT_BODY",BODY,{"disambiguationData":[OSD([sQuery(id+"F0.wireOp",EDGE,"E0.bottom"),sQuery(id+"F0.wireOp",EDGE,"E0.top"),sQuery(id+"F0.wireOp",EDGE,"E0.left"),sQuery(id+"F0.wireOp",EDGE,"E0.right")])]}),"instanceName":"1"}),"instanceName":"1"}),"instanceName":"1"}),"instanceName":"1"}),"instanceName":"1"}),"instanceName":"1"});
            var Q213;
            Q213=makeQuery(id+"F42.opPattern","COPY",BODY,{"derivedFrom":makeQuery(id+"F29.opPattern","COPY",BODY,{"derivedFrom":makeQuery(id+"F23.opPattern","COPY",BODY,{"derivedFrom":makeQuery(id+"F19.opPattern","COPY",BODY,{"derivedFrom":makeQuery(id+"F17.opPattern","COPY",BODY,{"derivedFrom":makeQuery(id+"F13.opPattern","COPY",BODY,{"derivedFrom":makeQuery(id+"F5.opPattern","COPY",BODY,{"derivedFrom":makeQuery(id+"F4.opPattern","COPY",BODY,{"derivedFrom":makeQuery(id+"F1.opExtrude","SWEPT_BODY",BODY,{"disambiguationData":[OSD([sQuery(id+"F0.wireOp",EDGE,"E0.bottom"),sQuery(id+"F0.wireOp",EDGE,"E0.top"),sQuery(id+"F0.wireOp",EDGE,"E0.left"),sQuery(id+"F0.wireOp",EDGE,"E0.right")])]}),"instanceName":"1"}),"instanceName":"1"}),"instanceName":"1"}),"instanceName":"1"}),"instanceName":"1"}),"instanceName":"1"}),"instanceName":"1"}),"instanceName":"1"});
            var Q214;
            Q214=makeQuery(id+"F40.opPattern","COPY",BODY,{"derivedFrom":makeQuery(id+"F29.opPattern","COPY",BODY,{"derivedFrom":makeQuery(id+"F26.opPattern","COPY",BODY,{"derivedFrom":makeQuery(id+"F17.opPattern","COPY",BODY,{"derivedFrom":makeQuery(id+"F15.opPattern","COPY",BODY,{"derivedFrom":makeQuery(id+"F12.opPattern","COPY",BODY,{"derivedFrom":makeQuery(id+"F6.opPattern","COPY",BODY,{"derivedFrom":makeQuery(id+"F5.opPattern","COPY",BODY,{"derivedFrom":makeQuery(id+"F4.opPattern","COPY",BODY,{"derivedFrom":makeQuery(id+"F2.opPattern","COPY",BODY,{"derivedFrom":makeQuery(id+"F1.opExtrude","SWEPT_BODY",BODY,{"disambiguationData":[OSD([sQuery(id+"F0.wireOp",EDGE,"E0.bottom"),sQuery(id+"F0.wireOp",EDGE,"E0.top"),sQuery(id+"F0.wireOp",EDGE,"E0.left"),sQuery(id+"F0.wireOp",EDGE,"E0.right")])]}),"instanceName":"1"}),"instanceName":"1"}),"instanceName":"1"}),"instanceName":"1"}),"instanceName":"1"}),"instanceName":"1"}),"instanceName":"1"}),"instanceName":"1"}),"instanceName":"1"}),"instanceName":"1"});
            var Q215;
            Q215=makeQuery(id+"F34.opPattern","COPY",BODY,{"derivedFrom":makeQuery(id+"F31.opPattern","COPY",BODY,{"derivedFrom":makeQuery(id+"F4.opPattern","COPY",BODY,{"derivedFrom":makeQuery(id+"F1.opExtrude","SWEPT_BODY",BODY,{"disambiguationData":[OSD([sQuery(id+"F0.wireOp",EDGE,"E0.bottom"),sQuery(id+"F0.wireOp",EDGE,"E0.top"),sQuery(id+"F0.wireOp",EDGE,"E0.left"),sQuery(id+"F0.wireOp",EDGE,"E0.right")])]}),"instanceName":"1"}),"instanceName":"1"}),"instanceName":"1"});
            var Q216;
            Q216=makeQuery(id+"F22.opPattern","COPY",BODY,{"derivedFrom":makeQuery(id+"F21.opPattern","COPY",BODY,{"derivedFrom":makeQuery(id+"F19.opPattern","COPY",BODY,{"derivedFrom":makeQuery(id+"F12.opPattern","COPY",BODY,{"derivedFrom":makeQuery(id+"F6.opPattern","COPY",BODY,{"derivedFrom":makeQuery(id+"F5.opPattern","COPY",BODY,{"derivedFrom":makeQuery(id+"F4.opPattern","COPY",BODY,{"derivedFrom":makeQuery(id+"F2.opPattern","COPY",BODY,{"derivedFrom":makeQuery(id+"F1.opExtrude","SWEPT_BODY",BODY,{"disambiguationData":[OSD([sQuery(id+"F0.wireOp",EDGE,"E0.bottom"),sQuery(id+"F0.wireOp",EDGE,"E0.top"),sQuery(id+"F0.wireOp",EDGE,"E0.left"),sQuery(id+"F0.wireOp",EDGE,"E0.right")])]}),"instanceName":"1"}),"instanceName":"1"}),"instanceName":"1"}),"instanceName":"1"}),"instanceName":"1"}),"instanceName":"1"}),"instanceName":"1"}),"instanceName":"1"});
            var Q217;
            Q217=makeQuery(id+"F44.opPattern","COPY",BODY,{"derivedFrom":makeQuery(id+"F42.opPattern","COPY",BODY,{"derivedFrom":makeQuery(id+"F29.opPattern","COPY",BODY,{"derivedFrom":makeQuery(id+"F28.opPattern","COPY",BODY,{"derivedFrom":makeQuery(id+"F23.opPattern","COPY",BODY,{"derivedFrom":makeQuery(id+"F19.opPattern","COPY",BODY,{"derivedFrom":makeQuery(id+"F17.opPattern","COPY",BODY,{"derivedFrom":makeQuery(id+"F15.opPattern","COPY",BODY,{"derivedFrom":makeQuery(id+"F12.opPattern","COPY",BODY,{"derivedFrom":makeQuery(id+"F6.opPattern","COPY",BODY,{"derivedFrom":makeQuery(id+"F5.opPattern","COPY",BODY,{"derivedFrom":makeQuery(id+"F4.opPattern","COPY",BODY,{"derivedFrom":makeQuery(id+"F2.opPattern","COPY",BODY,{"derivedFrom":makeQuery(id+"F1.opExtrude","SWEPT_BODY",BODY,{"disambiguationData":[OSD([sQuery(id+"F0.wireOp",EDGE,"E0.bottom"),sQuery(id+"F0.wireOp",EDGE,"E0.top"),sQuery(id+"F0.wireOp",EDGE,"E0.left"),sQuery(id+"F0.wireOp",EDGE,"E0.right")])]}),"instanceName":"1"}),"instanceName":"1"}),"instanceName":"1"}),"instanceName":"1"}),"instanceName":"1"}),"instanceName":"1"}),"instanceName":"1"}),"instanceName":"1"}),"instanceName":"1"}),"instanceName":"1"}),"instanceName":"1"}),"instanceName":"1"}),"instanceName":"1"});
            var Q218;
            Q218=makeQuery(id+"F6.opPattern","COPY",BODY,{"derivedFrom":makeQuery(id+"F5.opPattern","COPY",BODY,{"derivedFrom":makeQuery(id+"F4.opPattern","COPY",BODY,{"derivedFrom":makeQuery(id+"F2.opPattern","COPY",BODY,{"derivedFrom":makeQuery(id+"F1.opExtrude","SWEPT_BODY",BODY,{"disambiguationData":[OSD([sQuery(id+"F0.wireOp",EDGE,"E0.bottom"),sQuery(id+"F0.wireOp",EDGE,"E0.top"),sQuery(id+"F0.wireOp",EDGE,"E0.left"),sQuery(id+"F0.wireOp",EDGE,"E0.right")])]}),"instanceName":"1"}),"instanceName":"1"}),"instanceName":"1"}),"instanceName":"1"});
            var Q219;
            Q219=makeQuery(id+"F40.opPattern","COPY",BODY,{"derivedFrom":makeQuery(id+"F28.opPattern","COPY",BODY,{"derivedFrom":makeQuery(id+"F23.opPattern","COPY",BODY,{"derivedFrom":makeQuery(id+"F19.opPattern","COPY",BODY,{"derivedFrom":makeQuery(id+"F15.opPattern","COPY",BODY,{"derivedFrom":makeQuery(id+"F12.opPattern","COPY",BODY,{"derivedFrom":makeQuery(id+"F6.opPattern","COPY",BODY,{"derivedFrom":makeQuery(id+"F5.opPattern","COPY",BODY,{"derivedFrom":makeQuery(id+"F4.opPattern","COPY",BODY,{"derivedFrom":makeQuery(id+"F2.opPattern","COPY",BODY,{"derivedFrom":makeQuery(id+"F1.opExtrude","SWEPT_BODY",BODY,{"disambiguationData":[OSD([sQuery(id+"F0.wireOp",EDGE,"E0.bottom"),sQuery(id+"F0.wireOp",EDGE,"E0.top"),sQuery(id+"F0.wireOp",EDGE,"E0.left"),sQuery(id+"F0.wireOp",EDGE,"E0.right")])]}),"instanceName":"1"}),"instanceName":"1"}),"instanceName":"1"}),"instanceName":"1"}),"instanceName":"1"}),"instanceName":"1"}),"instanceName":"1"}),"instanceName":"1"}),"instanceName":"1"}),"instanceName":"1"});
            var Q220;
            Q220=makeQuery(id+"F24.opPattern","COPY",BODY,{"derivedFrom":makeQuery(id+"F23.opPattern","COPY",BODY,{"derivedFrom":makeQuery(id+"F21.opPattern","COPY",BODY,{"derivedFrom":makeQuery(id+"F19.opPattern","COPY",BODY,{"derivedFrom":makeQuery(id+"F17.opPattern","COPY",BODY,{"derivedFrom":makeQuery(id+"F12.opPattern","COPY",BODY,{"derivedFrom":makeQuery(id+"F6.opPattern","COPY",BODY,{"derivedFrom":makeQuery(id+"F5.opPattern","COPY",BODY,{"derivedFrom":makeQuery(id+"F4.opPattern","COPY",BODY,{"derivedFrom":makeQuery(id+"F2.opPattern","COPY",BODY,{"derivedFrom":makeQuery(id+"F1.opExtrude","SWEPT_BODY",BODY,{"disambiguationData":[OSD([sQuery(id+"F0.wireOp",EDGE,"E0.bottom"),sQuery(id+"F0.wireOp",EDGE,"E0.top"),sQuery(id+"F0.wireOp",EDGE,"E0.left"),sQuery(id+"F0.wireOp",EDGE,"E0.right")])]}),"instanceName":"1"}),"instanceName":"1"}),"instanceName":"1"}),"instanceName":"1"}),"instanceName":"1"}),"instanceName":"1"}),"instanceName":"1"}),"instanceName":"1"}),"instanceName":"1"}),"instanceName":"1"});
            var Q221;
            Q221=makeQuery(id+"F42.opPattern","COPY",BODY,{"derivedFrom":makeQuery(id+"F23.opPattern","COPY",BODY,{"derivedFrom":makeQuery(id+"F19.opPattern","COPY",BODY,{"derivedFrom":makeQuery(id+"F12.opPattern","COPY",BODY,{"derivedFrom":makeQuery(id+"F6.opPattern","COPY",BODY,{"derivedFrom":makeQuery(id+"F5.opPattern","COPY",BODY,{"derivedFrom":makeQuery(id+"F4.opPattern","COPY",BODY,{"derivedFrom":makeQuery(id+"F2.opPattern","COPY",BODY,{"derivedFrom":makeQuery(id+"F1.opExtrude","SWEPT_BODY",BODY,{"disambiguationData":[OSD([sQuery(id+"F0.wireOp",EDGE,"E0.bottom"),sQuery(id+"F0.wireOp",EDGE,"E0.top"),sQuery(id+"F0.wireOp",EDGE,"E0.left"),sQuery(id+"F0.wireOp",EDGE,"E0.right")])]}),"instanceName":"1"}),"instanceName":"1"}),"instanceName":"1"}),"instanceName":"1"}),"instanceName":"1"}),"instanceName":"1"}),"instanceName":"1"}),"instanceName":"1"});
            var Q222;
            Q222=makeQuery(id+"F23.opPattern","COPY",BODY,{"derivedFrom":makeQuery(id+"F19.opPattern","COPY",BODY,{"derivedFrom":makeQuery(id+"F17.opPattern","COPY",BODY,{"derivedFrom":makeQuery(id+"F5.opPattern","COPY",BODY,{"derivedFrom":makeQuery(id+"F4.opPattern","COPY",BODY,{"derivedFrom":makeQuery(id+"F2.opPattern","COPY",BODY,{"derivedFrom":makeQuery(id+"F1.opExtrude","SWEPT_BODY",BODY,{"disambiguationData":[OSD([sQuery(id+"F0.wireOp",EDGE,"E0.bottom"),sQuery(id+"F0.wireOp",EDGE,"E0.top"),sQuery(id+"F0.wireOp",EDGE,"E0.left"),sQuery(id+"F0.wireOp",EDGE,"E0.right")])]}),"instanceName":"1"}),"instanceName":"1"}),"instanceName":"1"}),"instanceName":"1"}),"instanceName":"1"}),"instanceName":"1"});
            var Q223;
            Q223=makeQuery(id+"F40.opPattern","COPY",BODY,{"derivedFrom":makeQuery(id+"F19.opPattern","COPY",BODY,{"derivedFrom":makeQuery(id+"F15.opPattern","COPY",BODY,{"derivedFrom":makeQuery(id+"F12.opPattern","COPY",BODY,{"derivedFrom":makeQuery(id+"F6.opPattern","COPY",BODY,{"derivedFrom":makeQuery(id+"F5.opPattern","COPY",BODY,{"derivedFrom":makeQuery(id+"F4.opPattern","COPY",BODY,{"derivedFrom":makeQuery(id+"F2.opPattern","COPY",BODY,{"derivedFrom":makeQuery(id+"F1.opExtrude","SWEPT_BODY",BODY,{"disambiguationData":[OSD([sQuery(id+"F0.wireOp",EDGE,"E0.bottom"),sQuery(id+"F0.wireOp",EDGE,"E0.top"),sQuery(id+"F0.wireOp",EDGE,"E0.left"),sQuery(id+"F0.wireOp",EDGE,"E0.right")])]}),"instanceName":"1"}),"instanceName":"1"}),"instanceName":"1"}),"instanceName":"1"}),"instanceName":"1"}),"instanceName":"1"}),"instanceName":"1"}),"instanceName":"1"});
            var Q224;
            Q224=makeQuery(id+"F27.opPattern","COPY",BODY,{"derivedFrom":makeQuery(id+"F23.opPattern","COPY",BODY,{"derivedFrom":makeQuery(id+"F21.opPattern","COPY",BODY,{"derivedFrom":makeQuery(id+"F19.opPattern","COPY",BODY,{"derivedFrom":makeQuery(id+"F17.opPattern","COPY",BODY,{"derivedFrom":makeQuery(id+"F5.opPattern","COPY",BODY,{"derivedFrom":makeQuery(id+"F4.opPattern","COPY",BODY,{"derivedFrom":makeQuery(id+"F1.opExtrude","SWEPT_BODY",BODY,{"disambiguationData":[OSD([sQuery(id+"F0.wireOp",EDGE,"E0.bottom"),sQuery(id+"F0.wireOp",EDGE,"E0.top"),sQuery(id+"F0.wireOp",EDGE,"E0.left"),sQuery(id+"F0.wireOp",EDGE,"E0.right")])]}),"instanceName":"1"}),"instanceName":"1"}),"instanceName":"1"}),"instanceName":"1"}),"instanceName":"1"}),"instanceName":"1"}),"instanceName":"1"});
            var Q225;
            Q225=makeQuery(id+"F26.opPattern","COPY",BODY,{"derivedFrom":makeQuery(id+"F19.opPattern","COPY",BODY,{"derivedFrom":makeQuery(id+"F17.opPattern","COPY",BODY,{"derivedFrom":makeQuery(id+"F13.opPattern","COPY",BODY,{"derivedFrom":makeQuery(id+"F5.opPattern","COPY",BODY,{"derivedFrom":makeQuery(id+"F4.opPattern","COPY",BODY,{"derivedFrom":makeQuery(id+"F1.opExtrude","SWEPT_BODY",BODY,{"disambiguationData":[OSD([sQuery(id+"F0.wireOp",EDGE,"E0.bottom"),sQuery(id+"F0.wireOp",EDGE,"E0.top"),sQuery(id+"F0.wireOp",EDGE,"E0.left"),sQuery(id+"F0.wireOp",EDGE,"E0.right")])]}),"instanceName":"1"}),"instanceName":"1"}),"instanceName":"1"}),"instanceName":"1"}),"instanceName":"1"}),"instanceName":"1"});
            var Q226;
            Q226=makeQuery(id+"F23.opPattern","COPY",BODY,{"derivedFrom":makeQuery(id+"F19.opPattern","COPY",BODY,{"derivedFrom":makeQuery(id+"F17.opPattern","COPY",BODY,{"derivedFrom":makeQuery(id+"F12.opPattern","COPY",BODY,{"derivedFrom":makeQuery(id+"F6.opPattern","COPY",BODY,{"derivedFrom":makeQuery(id+"F5.opPattern","COPY",BODY,{"derivedFrom":makeQuery(id+"F4.opPattern","COPY",BODY,{"derivedFrom":makeQuery(id+"F1.opExtrude","SWEPT_BODY",BODY,{"disambiguationData":[OSD([sQuery(id+"F0.wireOp",EDGE,"E0.bottom"),sQuery(id+"F0.wireOp",EDGE,"E0.top"),sQuery(id+"F0.wireOp",EDGE,"E0.left"),sQuery(id+"F0.wireOp",EDGE,"E0.right")])]}),"instanceName":"1"}),"instanceName":"1"}),"instanceName":"1"}),"instanceName":"1"}),"instanceName":"1"}),"instanceName":"1"}),"instanceName":"1"});
            var Q227;
            Q227=makeQuery(id+"F23.opPattern","COPY",BODY,{"derivedFrom":makeQuery(id+"F19.opPattern","COPY",BODY,{"derivedFrom":makeQuery(id+"F17.opPattern","COPY",BODY,{"derivedFrom":makeQuery(id+"F6.opPattern","COPY",BODY,{"derivedFrom":makeQuery(id+"F5.opPattern","COPY",BODY,{"derivedFrom":makeQuery(id+"F4.opPattern","COPY",BODY,{"derivedFrom":makeQuery(id+"F1.opExtrude","SWEPT_BODY",BODY,{"disambiguationData":[OSD([sQuery(id+"F0.wireOp",EDGE,"E0.bottom"),sQuery(id+"F0.wireOp",EDGE,"E0.top"),sQuery(id+"F0.wireOp",EDGE,"E0.left"),sQuery(id+"F0.wireOp",EDGE,"E0.right")])]}),"instanceName":"1"}),"instanceName":"1"}),"instanceName":"1"}),"instanceName":"1"}),"instanceName":"1"}),"instanceName":"1"});
            var Q228;
            Q228=makeQuery(id+"F44.opPattern","COPY",BODY,{"derivedFrom":makeQuery(id+"F42.opPattern","COPY",BODY,{"derivedFrom":makeQuery(id+"F29.opPattern","COPY",BODY,{"derivedFrom":makeQuery(id+"F28.opPattern","COPY",BODY,{"derivedFrom":makeQuery(id+"F23.opPattern","COPY",BODY,{"derivedFrom":makeQuery(id+"F19.opPattern","COPY",BODY,{"derivedFrom":makeQuery(id+"F15.opPattern","COPY",BODY,{"derivedFrom":makeQuery(id+"F12.opPattern","COPY",BODY,{"derivedFrom":makeQuery(id+"F6.opPattern","COPY",BODY,{"derivedFrom":makeQuery(id+"F5.opPattern","COPY",BODY,{"derivedFrom":makeQuery(id+"F4.opPattern","COPY",BODY,{"derivedFrom":makeQuery(id+"F2.opPattern","COPY",BODY,{"derivedFrom":makeQuery(id+"F1.opExtrude","SWEPT_BODY",BODY,{"disambiguationData":[OSD([sQuery(id+"F0.wireOp",EDGE,"E0.bottom"),sQuery(id+"F0.wireOp",EDGE,"E0.top"),sQuery(id+"F0.wireOp",EDGE,"E0.left"),sQuery(id+"F0.wireOp",EDGE,"E0.right")])]}),"instanceName":"1"}),"instanceName":"1"}),"instanceName":"1"}),"instanceName":"1"}),"instanceName":"1"}),"instanceName":"1"}),"instanceName":"1"}),"instanceName":"1"}),"instanceName":"1"}),"instanceName":"1"}),"instanceName":"1"}),"instanceName":"1"});
            var Q229;
            Q229=makeQuery(id+"F42.opPattern","COPY",BODY,{"derivedFrom":makeQuery(id+"F29.opPattern","COPY",BODY,{"derivedFrom":makeQuery(id+"F19.opPattern","COPY",BODY,{"derivedFrom":makeQuery(id+"F17.opPattern","COPY",BODY,{"derivedFrom":makeQuery(id+"F15.opPattern","COPY",BODY,{"derivedFrom":makeQuery(id+"F12.opPattern","COPY",BODY,{"derivedFrom":makeQuery(id+"F6.opPattern","COPY",BODY,{"derivedFrom":makeQuery(id+"F5.opPattern","COPY",BODY,{"derivedFrom":makeQuery(id+"F4.opPattern","COPY",BODY,{"derivedFrom":makeQuery(id+"F2.opPattern","COPY",BODY,{"derivedFrom":makeQuery(id+"F1.opExtrude","SWEPT_BODY",BODY,{"disambiguationData":[OSD([sQuery(id+"F0.wireOp",EDGE,"E0.bottom"),sQuery(id+"F0.wireOp",EDGE,"E0.top"),sQuery(id+"F0.wireOp",EDGE,"E0.left"),sQuery(id+"F0.wireOp",EDGE,"E0.right")])]}),"instanceName":"1"}),"instanceName":"1"}),"instanceName":"1"}),"instanceName":"1"}),"instanceName":"1"}),"instanceName":"1"}),"instanceName":"1"}),"instanceName":"1"}),"instanceName":"1"}),"instanceName":"1"});
            var Q230;
            Q230=makeQuery(id+"F39.opPattern","COPY",BODY,{"derivedFrom":makeQuery(id+"F26.opPattern","COPY",BODY,{"derivedFrom":makeQuery(id+"F19.opPattern","COPY",BODY,{"derivedFrom":makeQuery(id+"F15.opPattern","COPY",BODY,{"derivedFrom":makeQuery(id+"F12.opPattern","COPY",BODY,{"derivedFrom":makeQuery(id+"F6.opPattern","COPY",BODY,{"derivedFrom":makeQuery(id+"F5.opPattern","COPY",BODY,{"derivedFrom":makeQuery(id+"F4.opPattern","COPY",BODY,{"derivedFrom":makeQuery(id+"F2.opPattern","COPY",BODY,{"derivedFrom":makeQuery(id+"F1.opExtrude","SWEPT_BODY",BODY,{"disambiguationData":[OSD([sQuery(id+"F0.wireOp",EDGE,"E0.bottom"),sQuery(id+"F0.wireOp",EDGE,"E0.top"),sQuery(id+"F0.wireOp",EDGE,"E0.left"),sQuery(id+"F0.wireOp",EDGE,"E0.right")])]}),"instanceName":"1"}),"instanceName":"1"}),"instanceName":"1"}),"instanceName":"1"}),"instanceName":"1"}),"instanceName":"1"}),"instanceName":"1"}),"instanceName":"1"}),"instanceName":"1"});
            var Q231;
            Q231=makeQuery(id+"F42.opPattern","COPY",BODY,{"derivedFrom":makeQuery(id+"F29.opPattern","COPY",BODY,{"derivedFrom":makeQuery(id+"F23.opPattern","COPY",BODY,{"derivedFrom":makeQuery(id+"F19.opPattern","COPY",BODY,{"derivedFrom":makeQuery(id+"F15.opPattern","COPY",BODY,{"derivedFrom":makeQuery(id+"F12.opPattern","COPY",BODY,{"derivedFrom":makeQuery(id+"F6.opPattern","COPY",BODY,{"derivedFrom":makeQuery(id+"F5.opPattern","COPY",BODY,{"derivedFrom":makeQuery(id+"F4.opPattern","COPY",BODY,{"derivedFrom":makeQuery(id+"F2.opPattern","COPY",BODY,{"derivedFrom":makeQuery(id+"F1.opExtrude","SWEPT_BODY",BODY,{"disambiguationData":[OSD([sQuery(id+"F0.wireOp",EDGE,"E0.bottom"),sQuery(id+"F0.wireOp",EDGE,"E0.top"),sQuery(id+"F0.wireOp",EDGE,"E0.left"),sQuery(id+"F0.wireOp",EDGE,"E0.right")])]}),"instanceName":"1"}),"instanceName":"1"}),"instanceName":"1"}),"instanceName":"1"}),"instanceName":"1"}),"instanceName":"1"}),"instanceName":"1"}),"instanceName":"1"}),"instanceName":"1"}),"instanceName":"1"});
            var Q232;
            Q232=makeQuery(id+"F45.opPattern","COPY",BODY,{"derivedFrom":makeQuery(id+"F40.opPattern","COPY",BODY,{"derivedFrom":makeQuery(id+"F21.opPattern","COPY",BODY,{"derivedFrom":makeQuery(id+"F19.opPattern","COPY",BODY,{"derivedFrom":makeQuery(id+"F17.opPattern","COPY",BODY,{"derivedFrom":makeQuery(id+"F6.opPattern","COPY",BODY,{"derivedFrom":makeQuery(id+"F5.opPattern","COPY",BODY,{"derivedFrom":makeQuery(id+"F4.opPattern","COPY",BODY,{"derivedFrom":makeQuery(id+"F1.opExtrude","SWEPT_BODY",BODY,{"disambiguationData":[OSD([sQuery(id+"F0.wireOp",EDGE,"E0.bottom"),sQuery(id+"F0.wireOp",EDGE,"E0.top"),sQuery(id+"F0.wireOp",EDGE,"E0.left"),sQuery(id+"F0.wireOp",EDGE,"E0.right")])]}),"instanceName":"1"}),"instanceName":"1"}),"instanceName":"1"}),"instanceName":"1"}),"instanceName":"1"}),"instanceName":"1"}),"instanceName":"1"}),"instanceName":"1"});
            var Q233;
            Q233=makeQuery(id+"F26.opPattern","COPY",BODY,{"derivedFrom":makeQuery(id+"F17.opPattern","COPY",BODY,{"derivedFrom":makeQuery(id+"F12.opPattern","COPY",BODY,{"derivedFrom":makeQuery(id+"F6.opPattern","COPY",BODY,{"derivedFrom":makeQuery(id+"F5.opPattern","COPY",BODY,{"derivedFrom":makeQuery(id+"F4.opPattern","COPY",BODY,{"derivedFrom":makeQuery(id+"F1.opExtrude","SWEPT_BODY",BODY,{"disambiguationData":[OSD([sQuery(id+"F0.wireOp",EDGE,"E0.bottom"),sQuery(id+"F0.wireOp",EDGE,"E0.top"),sQuery(id+"F0.wireOp",EDGE,"E0.left"),sQuery(id+"F0.wireOp",EDGE,"E0.right")])]}),"instanceName":"1"}),"instanceName":"1"}),"instanceName":"1"}),"instanceName":"1"}),"instanceName":"1"}),"instanceName":"1"});
            var Q234;
            Q234=makeQuery(id+"F31.opPattern","COPY",BODY,{"derivedFrom":makeQuery(id+"F1.opExtrude","SWEPT_BODY",BODY,{"disambiguationData":[OSD([sQuery(id+"F0.wireOp",EDGE,"E0.bottom"),sQuery(id+"F0.wireOp",EDGE,"E0.top"),sQuery(id+"F0.wireOp",EDGE,"E0.left"),sQuery(id+"F0.wireOp",EDGE,"E0.right")])]}),"instanceName":"1"});
            var Q235;
            Q235=makeQuery(id+"F39.opPattern","COPY",BODY,{"derivedFrom":makeQuery(id+"F26.opPattern","COPY",BODY,{"derivedFrom":makeQuery(id+"F19.opPattern","COPY",BODY,{"derivedFrom":makeQuery(id+"F17.opPattern","COPY",BODY,{"derivedFrom":makeQuery(id+"F12.opPattern","COPY",BODY,{"derivedFrom":makeQuery(id+"F6.opPattern","COPY",BODY,{"derivedFrom":makeQuery(id+"F5.opPattern","COPY",BODY,{"derivedFrom":makeQuery(id+"F4.opPattern","COPY",BODY,{"derivedFrom":makeQuery(id+"F1.opExtrude","SWEPT_BODY",BODY,{"disambiguationData":[OSD([sQuery(id+"F0.wireOp",EDGE,"E0.bottom"),sQuery(id+"F0.wireOp",EDGE,"E0.top"),sQuery(id+"F0.wireOp",EDGE,"E0.left"),sQuery(id+"F0.wireOp",EDGE,"E0.right")])]}),"instanceName":"1"}),"instanceName":"1"}),"instanceName":"1"}),"instanceName":"1"}),"instanceName":"1"}),"instanceName":"1"}),"instanceName":"1"}),"instanceName":"1"});
            var Q236;
            Q236=makeQuery(id+"F29.opPattern","COPY",BODY,{"derivedFrom":makeQuery(id+"F19.opPattern","COPY",BODY,{"derivedFrom":makeQuery(id+"F17.opPattern","COPY",BODY,{"derivedFrom":makeQuery(id+"F13.opPattern","COPY",BODY,{"derivedFrom":makeQuery(id+"F5.opPattern","COPY",BODY,{"derivedFrom":makeQuery(id+"F4.opPattern","COPY",BODY,{"derivedFrom":makeQuery(id+"F1.opExtrude","SWEPT_BODY",BODY,{"disambiguationData":[OSD([sQuery(id+"F0.wireOp",EDGE,"E0.bottom"),sQuery(id+"F0.wireOp",EDGE,"E0.top"),sQuery(id+"F0.wireOp",EDGE,"E0.left"),sQuery(id+"F0.wireOp",EDGE,"E0.right")])]}),"instanceName":"1"}),"instanceName":"1"}),"instanceName":"1"}),"instanceName":"1"}),"instanceName":"1"}),"instanceName":"1"});
            var Q237;
            Q237=makeQuery(id+"F26.opPattern","COPY",BODY,{"derivedFrom":makeQuery(id+"F19.opPattern","COPY",BODY,{"derivedFrom":makeQuery(id+"F15.opPattern","COPY",BODY,{"derivedFrom":makeQuery(id+"F12.opPattern","COPY",BODY,{"derivedFrom":makeQuery(id+"F6.opPattern","COPY",BODY,{"derivedFrom":makeQuery(id+"F5.opPattern","COPY",BODY,{"derivedFrom":makeQuery(id+"F4.opPattern","COPY",BODY,{"derivedFrom":makeQuery(id+"F2.opPattern","COPY",BODY,{"derivedFrom":makeQuery(id+"F1.opExtrude","SWEPT_BODY",BODY,{"disambiguationData":[OSD([sQuery(id+"F0.wireOp",EDGE,"E0.bottom"),sQuery(id+"F0.wireOp",EDGE,"E0.top"),sQuery(id+"F0.wireOp",EDGE,"E0.left"),sQuery(id+"F0.wireOp",EDGE,"E0.right")])]}),"instanceName":"1"}),"instanceName":"1"}),"instanceName":"1"}),"instanceName":"1"}),"instanceName":"1"}),"instanceName":"1"}),"instanceName":"1"}),"instanceName":"1"});
            var Q238;
            Q238=makeQuery(id+"F35.opPattern","COPY",BODY,{"derivedFrom":makeQuery(id+"F32.opPattern","COPY",BODY,{"derivedFrom":makeQuery(id+"F31.opPattern","COPY",BODY,{"derivedFrom":makeQuery(id+"F1.opExtrude","SWEPT_BODY",BODY,{"disambiguationData":[OSD([sQuery(id+"F0.wireOp",EDGE,"E0.bottom"),sQuery(id+"F0.wireOp",EDGE,"E0.top"),sQuery(id+"F0.wireOp",EDGE,"E0.left"),sQuery(id+"F0.wireOp",EDGE,"E0.right")])]}),"instanceName":"1"}),"instanceName":"1"}),"instanceName":"1"});
            var Q239;
            Q239=makeQuery(id+"F21.opPattern","COPY",BODY,{"derivedFrom":makeQuery(id+"F19.opPattern","COPY",BODY,{"derivedFrom":makeQuery(id+"F12.opPattern","COPY",BODY,{"derivedFrom":makeQuery(id+"F6.opPattern","COPY",BODY,{"derivedFrom":makeQuery(id+"F5.opPattern","COPY",BODY,{"derivedFrom":makeQuery(id+"F4.opPattern","COPY",BODY,{"derivedFrom":makeQuery(id+"F1.opExtrude","SWEPT_BODY",BODY,{"disambiguationData":[OSD([sQuery(id+"F0.wireOp",EDGE,"E0.bottom"),sQuery(id+"F0.wireOp",EDGE,"E0.top"),sQuery(id+"F0.wireOp",EDGE,"E0.left"),sQuery(id+"F0.wireOp",EDGE,"E0.right")])]}),"instanceName":"1"}),"instanceName":"1"}),"instanceName":"1"}),"instanceName":"1"}),"instanceName":"1"}),"instanceName":"1"});
            var Q240;
            Q240=makeQuery(id+"F45.opPattern","COPY",BODY,{"derivedFrom":makeQuery(id+"F40.opPattern","COPY",BODY,{"derivedFrom":makeQuery(id+"F19.opPattern","COPY",BODY,{"derivedFrom":makeQuery(id+"F15.opPattern","COPY",BODY,{"derivedFrom":makeQuery(id+"F12.opPattern","COPY",BODY,{"derivedFrom":makeQuery(id+"F6.opPattern","COPY",BODY,{"derivedFrom":makeQuery(id+"F5.opPattern","COPY",BODY,{"derivedFrom":makeQuery(id+"F4.opPattern","COPY",BODY,{"derivedFrom":makeQuery(id+"F2.opPattern","COPY",BODY,{"derivedFrom":makeQuery(id+"F1.opExtrude","SWEPT_BODY",BODY,{"disambiguationData":[OSD([sQuery(id+"F0.wireOp",EDGE,"E0.bottom"),sQuery(id+"F0.wireOp",EDGE,"E0.top"),sQuery(id+"F0.wireOp",EDGE,"E0.left"),sQuery(id+"F0.wireOp",EDGE,"E0.right")])]}),"instanceName":"1"}),"instanceName":"1"}),"instanceName":"1"}),"instanceName":"1"}),"instanceName":"1"}),"instanceName":"1"}),"instanceName":"1"}),"instanceName":"1"}),"instanceName":"1"});
            var Q241;
            Q241=makeQuery(id+"F40.opPattern","COPY",BODY,{"derivedFrom":makeQuery(id+"F26.opPattern","COPY",BODY,{"derivedFrom":makeQuery(id+"F19.opPattern","COPY",BODY,{"derivedFrom":makeQuery(id+"F12.opPattern","COPY",BODY,{"derivedFrom":makeQuery(id+"F6.opPattern","COPY",BODY,{"derivedFrom":makeQuery(id+"F5.opPattern","COPY",BODY,{"derivedFrom":makeQuery(id+"F4.opPattern","COPY",BODY,{"derivedFrom":makeQuery(id+"F1.opExtrude","SWEPT_BODY",BODY,{"disambiguationData":[OSD([sQuery(id+"F0.wireOp",EDGE,"E0.bottom"),sQuery(id+"F0.wireOp",EDGE,"E0.top"),sQuery(id+"F0.wireOp",EDGE,"E0.left"),sQuery(id+"F0.wireOp",EDGE,"E0.right")])]}),"instanceName":"1"}),"instanceName":"1"}),"instanceName":"1"}),"instanceName":"1"}),"instanceName":"1"}),"instanceName":"1"}),"instanceName":"1"});
            var Q242;
            Q242=makeQuery(id+"F19.opPattern","COPY",BODY,{"derivedFrom":makeQuery(id+"F17.opPattern","COPY",BODY,{"derivedFrom":makeQuery(id+"F6.opPattern","COPY",BODY,{"derivedFrom":makeQuery(id+"F5.opPattern","COPY",BODY,{"derivedFrom":makeQuery(id+"F4.opPattern","COPY",BODY,{"derivedFrom":makeQuery(id+"F2.opPattern","COPY",BODY,{"derivedFrom":makeQuery(id+"F1.opExtrude","SWEPT_BODY",BODY,{"disambiguationData":[OSD([sQuery(id+"F0.wireOp",EDGE,"E0.bottom"),sQuery(id+"F0.wireOp",EDGE,"E0.top"),sQuery(id+"F0.wireOp",EDGE,"E0.left"),sQuery(id+"F0.wireOp",EDGE,"E0.right")])]}),"instanceName":"1"}),"instanceName":"1"}),"instanceName":"1"}),"instanceName":"1"}),"instanceName":"1"}),"instanceName":"1"});
            var Q243;
            Q243=makeQuery(id+"F11.opPattern","COPY",BODY,{"derivedFrom":makeQuery(id+"F5.opPattern","COPY",BODY,{"derivedFrom":makeQuery(id+"F1.opExtrude","SWEPT_BODY",BODY,{"disambiguationData":[OSD([sQuery(id+"F0.wireOp",EDGE,"E0.bottom"),sQuery(id+"F0.wireOp",EDGE,"E0.top"),sQuery(id+"F0.wireOp",EDGE,"E0.left"),sQuery(id+"F0.wireOp",EDGE,"E0.right")])]}),"instanceName":"1"}),"instanceName":"1"});
            var Q244;
            Q244=makeQuery(id+"F49.opPattern","COPY",BODY,{"derivedFrom":makeQuery(id+"F42.opPattern","COPY",BODY,{"derivedFrom":makeQuery(id+"F29.opPattern","COPY",BODY,{"derivedFrom":makeQuery(id+"F28.opPattern","COPY",BODY,{"derivedFrom":makeQuery(id+"F19.opPattern","COPY",BODY,{"derivedFrom":makeQuery(id+"F17.opPattern","COPY",BODY,{"derivedFrom":makeQuery(id+"F13.opPattern","COPY",BODY,{"derivedFrom":makeQuery(id+"F5.opPattern","COPY",BODY,{"derivedFrom":makeQuery(id+"F4.opPattern","COPY",BODY,{"derivedFrom":makeQuery(id+"F1.opExtrude","SWEPT_BODY",BODY,{"disambiguationData":[OSD([sQuery(id+"F0.wireOp",EDGE,"E0.bottom"),sQuery(id+"F0.wireOp",EDGE,"E0.top"),sQuery(id+"F0.wireOp",EDGE,"E0.left"),sQuery(id+"F0.wireOp",EDGE,"E0.right")])]}),"instanceName":"1"}),"instanceName":"1"}),"instanceName":"1"}),"instanceName":"1"}),"instanceName":"1"}),"instanceName":"1"}),"instanceName":"1"}),"instanceName":"1"}),"instanceName":"1"});
            var Q245;
            Q245=makeQuery(id+"F40.opPattern","COPY",BODY,{"derivedFrom":makeQuery(id+"F15.opPattern","COPY",BODY,{"derivedFrom":makeQuery(id+"F12.opPattern","COPY",BODY,{"derivedFrom":makeQuery(id+"F6.opPattern","COPY",BODY,{"derivedFrom":makeQuery(id+"F5.opPattern","COPY",BODY,{"derivedFrom":makeQuery(id+"F4.opPattern","COPY",BODY,{"derivedFrom":makeQuery(id+"F2.opPattern","COPY",BODY,{"derivedFrom":makeQuery(id+"F1.opExtrude","SWEPT_BODY",BODY,{"disambiguationData":[OSD([sQuery(id+"F0.wireOp",EDGE,"E0.bottom"),sQuery(id+"F0.wireOp",EDGE,"E0.top"),sQuery(id+"F0.wireOp",EDGE,"E0.left"),sQuery(id+"F0.wireOp",EDGE,"E0.right")])]}),"instanceName":"1"}),"instanceName":"1"}),"instanceName":"1"}),"instanceName":"1"}),"instanceName":"1"}),"instanceName":"1"}),"instanceName":"1"});
            var Q246;
            Q246=makeQuery(id+"F40.opPattern","COPY",BODY,{"derivedFrom":makeQuery(id+"F23.opPattern","COPY",BODY,{"derivedFrom":makeQuery(id+"F19.opPattern","COPY",BODY,{"derivedFrom":makeQuery(id+"F17.opPattern","COPY",BODY,{"derivedFrom":makeQuery(id+"F5.opPattern","COPY",BODY,{"derivedFrom":makeQuery(id+"F4.opPattern","COPY",BODY,{"derivedFrom":makeQuery(id+"F1.opExtrude","SWEPT_BODY",BODY,{"disambiguationData":[OSD([sQuery(id+"F0.wireOp",EDGE,"E0.bottom"),sQuery(id+"F0.wireOp",EDGE,"E0.top"),sQuery(id+"F0.wireOp",EDGE,"E0.left"),sQuery(id+"F0.wireOp",EDGE,"E0.right")])]}),"instanceName":"1"}),"instanceName":"1"}),"instanceName":"1"}),"instanceName":"1"}),"instanceName":"1"}),"instanceName":"1"});
            var Q247;
            Q247=makeQuery(id+"F45.opPattern","COPY",BODY,{"derivedFrom":makeQuery(id+"F40.opPattern","COPY",BODY,{"derivedFrom":makeQuery(id+"F23.opPattern","COPY",BODY,{"derivedFrom":makeQuery(id+"F19.opPattern","COPY",BODY,{"derivedFrom":makeQuery(id+"F6.opPattern","COPY",BODY,{"derivedFrom":makeQuery(id+"F5.opPattern","COPY",BODY,{"derivedFrom":makeQuery(id+"F4.opPattern","COPY",BODY,{"derivedFrom":makeQuery(id+"F2.opPattern","COPY",BODY,{"derivedFrom":makeQuery(id+"F1.opExtrude","SWEPT_BODY",BODY,{"disambiguationData":[OSD([sQuery(id+"F0.wireOp",EDGE,"E0.bottom"),sQuery(id+"F0.wireOp",EDGE,"E0.top"),sQuery(id+"F0.wireOp",EDGE,"E0.left"),sQuery(id+"F0.wireOp",EDGE,"E0.right")])]}),"instanceName":"1"}),"instanceName":"1"}),"instanceName":"1"}),"instanceName":"1"}),"instanceName":"1"}),"instanceName":"1"}),"instanceName":"1"}),"instanceName":"1"});
            var Q248;
            Q248=makeQuery(id+"F29.opPattern","COPY",BODY,{"derivedFrom":makeQuery(id+"F26.opPattern","COPY",BODY,{"derivedFrom":makeQuery(id+"F17.opPattern","COPY",BODY,{"derivedFrom":makeQuery(id+"F15.opPattern","COPY",BODY,{"derivedFrom":makeQuery(id+"F12.opPattern","COPY",BODY,{"derivedFrom":makeQuery(id+"F6.opPattern","COPY",BODY,{"derivedFrom":makeQuery(id+"F5.opPattern","COPY",BODY,{"derivedFrom":makeQuery(id+"F4.opPattern","COPY",BODY,{"derivedFrom":makeQuery(id+"F2.opPattern","COPY",BODY,{"derivedFrom":makeQuery(id+"F1.opExtrude","SWEPT_BODY",BODY,{"disambiguationData":[OSD([sQuery(id+"F0.wireOp",EDGE,"E0.bottom"),sQuery(id+"F0.wireOp",EDGE,"E0.top"),sQuery(id+"F0.wireOp",EDGE,"E0.left"),sQuery(id+"F0.wireOp",EDGE,"E0.right")])]}),"instanceName":"1"}),"instanceName":"1"}),"instanceName":"1"}),"instanceName":"1"}),"instanceName":"1"}),"instanceName":"1"}),"instanceName":"1"}),"instanceName":"1"}),"instanceName":"1"});
            var Q249;
            Q249=makeQuery(id+"F40.opPattern","COPY",BODY,{"derivedFrom":makeQuery(id+"F19.opPattern","COPY",BODY,{"derivedFrom":makeQuery(id+"F17.opPattern","COPY",BODY,{"derivedFrom":makeQuery(id+"F6.opPattern","COPY",BODY,{"derivedFrom":makeQuery(id+"F5.opPattern","COPY",BODY,{"derivedFrom":makeQuery(id+"F4.opPattern","COPY",BODY,{"derivedFrom":makeQuery(id+"F2.opPattern","COPY",BODY,{"derivedFrom":makeQuery(id+"F1.opExtrude","SWEPT_BODY",BODY,{"disambiguationData":[OSD([sQuery(id+"F0.wireOp",EDGE,"E0.bottom"),sQuery(id+"F0.wireOp",EDGE,"E0.top"),sQuery(id+"F0.wireOp",EDGE,"E0.left"),sQuery(id+"F0.wireOp",EDGE,"E0.right")])]}),"instanceName":"1"}),"instanceName":"1"}),"instanceName":"1"}),"instanceName":"1"}),"instanceName":"1"}),"instanceName":"1"}),"instanceName":"1"});
            var Q250;
            Q250=makeQuery(id+"F39.opPattern","COPY",BODY,{"derivedFrom":makeQuery(id+"F28.opPattern","COPY",BODY,{"derivedFrom":makeQuery(id+"F26.opPattern","COPY",BODY,{"derivedFrom":makeQuery(id+"F17.opPattern","COPY",BODY,{"derivedFrom":makeQuery(id+"F13.opPattern","COPY",BODY,{"derivedFrom":makeQuery(id+"F5.opPattern","COPY",BODY,{"derivedFrom":makeQuery(id+"F4.opPattern","COPY",BODY,{"derivedFrom":makeQuery(id+"F1.opExtrude","SWEPT_BODY",BODY,{"disambiguationData":[OSD([sQuery(id+"F0.wireOp",EDGE,"E0.bottom"),sQuery(id+"F0.wireOp",EDGE,"E0.top"),sQuery(id+"F0.wireOp",EDGE,"E0.left"),sQuery(id+"F0.wireOp",EDGE,"E0.right")])]}),"instanceName":"1"}),"instanceName":"1"}),"instanceName":"1"}),"instanceName":"1"}),"instanceName":"1"}),"instanceName":"1"}),"instanceName":"1"});
            var Q251;
            Q251=makeQuery(id+"F40.opPattern","COPY",BODY,{"derivedFrom":makeQuery(id+"F24.opPattern","COPY",BODY,{"derivedFrom":makeQuery(id+"F23.opPattern","COPY",BODY,{"derivedFrom":makeQuery(id+"F19.opPattern","COPY",BODY,{"derivedFrom":makeQuery(id+"F5.opPattern","COPY",BODY,{"derivedFrom":makeQuery(id+"F4.opPattern","COPY",BODY,{"derivedFrom":makeQuery(id+"F2.opPattern","COPY",BODY,{"derivedFrom":makeQuery(id+"F1.opExtrude","SWEPT_BODY",BODY,{"disambiguationData":[OSD([sQuery(id+"F0.wireOp",EDGE,"E0.bottom"),sQuery(id+"F0.wireOp",EDGE,"E0.top"),sQuery(id+"F0.wireOp",EDGE,"E0.left"),sQuery(id+"F0.wireOp",EDGE,"E0.right")])]}),"instanceName":"1"}),"instanceName":"1"}),"instanceName":"1"}),"instanceName":"1"}),"instanceName":"1"}),"instanceName":"1"}),"instanceName":"1"});
            var Q252;
            Q252=makeQuery(id+"F42.opPattern","COPY",BODY,{"derivedFrom":makeQuery(id+"F28.opPattern","COPY",BODY,{"derivedFrom":makeQuery(id+"F23.opPattern","COPY",BODY,{"derivedFrom":makeQuery(id+"F19.opPattern","COPY",BODY,{"derivedFrom":makeQuery(id+"F15.opPattern","COPY",BODY,{"derivedFrom":makeQuery(id+"F12.opPattern","COPY",BODY,{"derivedFrom":makeQuery(id+"F6.opPattern","COPY",BODY,{"derivedFrom":makeQuery(id+"F5.opPattern","COPY",BODY,{"derivedFrom":makeQuery(id+"F4.opPattern","COPY",BODY,{"derivedFrom":makeQuery(id+"F2.opPattern","COPY",BODY,{"derivedFrom":makeQuery(id+"F1.opExtrude","SWEPT_BODY",BODY,{"disambiguationData":[OSD([sQuery(id+"F0.wireOp",EDGE,"E0.bottom"),sQuery(id+"F0.wireOp",EDGE,"E0.top"),sQuery(id+"F0.wireOp",EDGE,"E0.left"),sQuery(id+"F0.wireOp",EDGE,"E0.right")])]}),"instanceName":"1"}),"instanceName":"1"}),"instanceName":"1"}),"instanceName":"1"}),"instanceName":"1"}),"instanceName":"1"}),"instanceName":"1"}),"instanceName":"1"}),"instanceName":"1"}),"instanceName":"1"});
            var Q253;
            Q253=makeQuery(id+"F17.opPattern","COPY",BODY,{"derivedFrom":makeQuery(id+"F6.opPattern","COPY",BODY,{"derivedFrom":makeQuery(id+"F5.opPattern","COPY",BODY,{"derivedFrom":makeQuery(id+"F4.opPattern","COPY",BODY,{"derivedFrom":makeQuery(id+"F1.opExtrude","SWEPT_BODY",BODY,{"disambiguationData":[OSD([sQuery(id+"F0.wireOp",EDGE,"E0.bottom"),sQuery(id+"F0.wireOp",EDGE,"E0.top"),sQuery(id+"F0.wireOp",EDGE,"E0.left"),sQuery(id+"F0.wireOp",EDGE,"E0.right")])]}),"instanceName":"1"}),"instanceName":"1"}),"instanceName":"1"}),"instanceName":"1"});
            var Q254;
            Q254=makeQuery(id+"F40.opPattern","COPY",BODY,{"derivedFrom":makeQuery(id+"F21.opPattern","COPY",BODY,{"derivedFrom":makeQuery(id+"F19.opPattern","COPY",BODY,{"derivedFrom":makeQuery(id+"F17.opPattern","COPY",BODY,{"derivedFrom":makeQuery(id+"F12.opPattern","COPY",BODY,{"derivedFrom":makeQuery(id+"F6.opPattern","COPY",BODY,{"derivedFrom":makeQuery(id+"F5.opPattern","COPY",BODY,{"derivedFrom":makeQuery(id+"F4.opPattern","COPY",BODY,{"derivedFrom":makeQuery(id+"F1.opExtrude","SWEPT_BODY",BODY,{"disambiguationData":[OSD([sQuery(id+"F0.wireOp",EDGE,"E0.bottom"),sQuery(id+"F0.wireOp",EDGE,"E0.top"),sQuery(id+"F0.wireOp",EDGE,"E0.left"),sQuery(id+"F0.wireOp",EDGE,"E0.right")])]}),"instanceName":"1"}),"instanceName":"1"}),"instanceName":"1"}),"instanceName":"1"}),"instanceName":"1"}),"instanceName":"1"}),"instanceName":"1"}),"instanceName":"1"});
            var Q255;
            Q255=makeQuery(id+"F30.opPattern","COPY",BODY,{"derivedFrom":makeQuery(id+"F29.opPattern","COPY",BODY,{"derivedFrom":makeQuery(id+"F23.opPattern","COPY",BODY,{"derivedFrom":makeQuery(id+"F19.opPattern","COPY",BODY,{"derivedFrom":makeQuery(id+"F17.opPattern","COPY",BODY,{"derivedFrom":makeQuery(id+"F13.opPattern","COPY",BODY,{"derivedFrom":makeQuery(id+"F5.opPattern","COPY",BODY,{"derivedFrom":makeQuery(id+"F4.opPattern","COPY",BODY,{"derivedFrom":makeQuery(id+"F1.opExtrude","SWEPT_BODY",BODY,{"disambiguationData":[OSD([sQuery(id+"F0.wireOp",EDGE,"E0.bottom"),sQuery(id+"F0.wireOp",EDGE,"E0.top"),sQuery(id+"F0.wireOp",EDGE,"E0.left"),sQuery(id+"F0.wireOp",EDGE,"E0.right")])]}),"instanceName":"1"}),"instanceName":"1"}),"instanceName":"1"}),"instanceName":"1"}),"instanceName":"1"}),"instanceName":"1"}),"instanceName":"1"}),"instanceName":"1"});
            var Q256;
            Q256=makeQuery(id+"F21.opPattern","COPY",BODY,{"derivedFrom":makeQuery(id+"F19.opPattern","COPY",BODY,{"derivedFrom":makeQuery(id+"F17.opPattern","COPY",BODY,{"derivedFrom":makeQuery(id+"F6.opPattern","COPY",BODY,{"derivedFrom":makeQuery(id+"F5.opPattern","COPY",BODY,{"derivedFrom":makeQuery(id+"F4.opPattern","COPY",BODY,{"derivedFrom":makeQuery(id+"F2.opPattern","COPY",BODY,{"derivedFrom":makeQuery(id+"F1.opExtrude","SWEPT_BODY",BODY,{"disambiguationData":[OSD([sQuery(id+"F0.wireOp",EDGE,"E0.bottom"),sQuery(id+"F0.wireOp",EDGE,"E0.top"),sQuery(id+"F0.wireOp",EDGE,"E0.left"),sQuery(id+"F0.wireOp",EDGE,"E0.right")])]}),"instanceName":"1"}),"instanceName":"1"}),"instanceName":"1"}),"instanceName":"1"}),"instanceName":"1"}),"instanceName":"1"}),"instanceName":"1"});
            var Q257;
            Q257=makeQuery(id+"F40.opPattern","COPY",BODY,{"derivedFrom":makeQuery(id+"F23.opPattern","COPY",BODY,{"derivedFrom":makeQuery(id+"F19.opPattern","COPY",BODY,{"derivedFrom":makeQuery(id+"F17.opPattern","COPY",BODY,{"derivedFrom":makeQuery(id+"F13.opPattern","COPY",BODY,{"derivedFrom":makeQuery(id+"F5.opPattern","COPY",BODY,{"derivedFrom":makeQuery(id+"F4.opPattern","COPY",BODY,{"derivedFrom":makeQuery(id+"F1.opExtrude","SWEPT_BODY",BODY,{"disambiguationData":[OSD([sQuery(id+"F0.wireOp",EDGE,"E0.bottom"),sQuery(id+"F0.wireOp",EDGE,"E0.top"),sQuery(id+"F0.wireOp",EDGE,"E0.left"),sQuery(id+"F0.wireOp",EDGE,"E0.right")])]}),"instanceName":"1"}),"instanceName":"1"}),"instanceName":"1"}),"instanceName":"1"}),"instanceName":"1"}),"instanceName":"1"}),"instanceName":"1"});
            var Q258;
            Q258=makeQuery(id+"F34.opPattern","COPY",BODY,{"derivedFrom":makeQuery(id+"F32.opPattern","COPY",BODY,{"derivedFrom":makeQuery(id+"F31.opPattern","COPY",BODY,{"derivedFrom":makeQuery(id+"F1.opExtrude","SWEPT_BODY",BODY,{"disambiguationData":[OSD([sQuery(id+"F0.wireOp",EDGE,"E0.bottom"),sQuery(id+"F0.wireOp",EDGE,"E0.top"),sQuery(id+"F0.wireOp",EDGE,"E0.left"),sQuery(id+"F0.wireOp",EDGE,"E0.right")])]}),"instanceName":"1"}),"instanceName":"1"}),"instanceName":"1"});
            var Q259;
            Q259=makeQuery(id+"F23.opPattern","COPY",BODY,{"derivedFrom":makeQuery(id+"F21.opPattern","COPY",BODY,{"derivedFrom":makeQuery(id+"F19.opPattern","COPY",BODY,{"derivedFrom":makeQuery(id+"F17.opPattern","COPY",BODY,{"derivedFrom":makeQuery(id+"F12.opPattern","COPY",BODY,{"derivedFrom":makeQuery(id+"F6.opPattern","COPY",BODY,{"derivedFrom":makeQuery(id+"F5.opPattern","COPY",BODY,{"derivedFrom":makeQuery(id+"F4.opPattern","COPY",BODY,{"derivedFrom":makeQuery(id+"F1.opExtrude","SWEPT_BODY",BODY,{"disambiguationData":[OSD([sQuery(id+"F0.wireOp",EDGE,"E0.bottom"),sQuery(id+"F0.wireOp",EDGE,"E0.top"),sQuery(id+"F0.wireOp",EDGE,"E0.left"),sQuery(id+"F0.wireOp",EDGE,"E0.right")])]}),"instanceName":"1"}),"instanceName":"1"}),"instanceName":"1"}),"instanceName":"1"}),"instanceName":"1"}),"instanceName":"1"}),"instanceName":"1"}),"instanceName":"1"});
            var Q260;
            Q260=makeQuery(id+"F17.opPattern","COPY",BODY,{"derivedFrom":makeQuery(id+"F5.opPattern","COPY",BODY,{"derivedFrom":makeQuery(id+"F4.opPattern","COPY",BODY,{"derivedFrom":makeQuery(id+"F2.opPattern","COPY",BODY,{"derivedFrom":makeQuery(id+"F1.opExtrude","SWEPT_BODY",BODY,{"disambiguationData":[OSD([sQuery(id+"F0.wireOp",EDGE,"E0.bottom"),sQuery(id+"F0.wireOp",EDGE,"E0.top"),sQuery(id+"F0.wireOp",EDGE,"E0.left"),sQuery(id+"F0.wireOp",EDGE,"E0.right")])]}),"instanceName":"1"}),"instanceName":"1"}),"instanceName":"1"}),"instanceName":"1"});
            var Q261;
            Q261=makeQuery(id+"F45.opPattern","COPY",BODY,{"derivedFrom":makeQuery(id+"F40.opPattern","COPY",BODY,{"derivedFrom":makeQuery(id+"F23.opPattern","COPY",BODY,{"derivedFrom":makeQuery(id+"F19.opPattern","COPY",BODY,{"derivedFrom":makeQuery(id+"F17.opPattern","COPY",BODY,{"derivedFrom":makeQuery(id+"F15.opPattern","COPY",BODY,{"derivedFrom":makeQuery(id+"F12.opPattern","COPY",BODY,{"derivedFrom":makeQuery(id+"F6.opPattern","COPY",BODY,{"derivedFrom":makeQuery(id+"F5.opPattern","COPY",BODY,{"derivedFrom":makeQuery(id+"F4.opPattern","COPY",BODY,{"derivedFrom":makeQuery(id+"F2.opPattern","COPY",BODY,{"derivedFrom":makeQuery(id+"F1.opExtrude","SWEPT_BODY",BODY,{"disambiguationData":[OSD([sQuery(id+"F0.wireOp",EDGE,"E0.bottom"),sQuery(id+"F0.wireOp",EDGE,"E0.top"),sQuery(id+"F0.wireOp",EDGE,"E0.left"),sQuery(id+"F0.wireOp",EDGE,"E0.right")])]}),"instanceName":"1"}),"instanceName":"1"}),"instanceName":"1"}),"instanceName":"1"}),"instanceName":"1"}),"instanceName":"1"}),"instanceName":"1"}),"instanceName":"1"}),"instanceName":"1"}),"instanceName":"1"}),"instanceName":"1"});
            var Q262;
            Q262=makeQuery(id+"F29.opPattern","COPY",BODY,{"derivedFrom":makeQuery(id+"F28.opPattern","COPY",BODY,{"derivedFrom":makeQuery(id+"F23.opPattern","COPY",BODY,{"derivedFrom":makeQuery(id+"F19.opPattern","COPY",BODY,{"derivedFrom":makeQuery(id+"F17.opPattern","COPY",BODY,{"derivedFrom":makeQuery(id+"F13.opPattern","COPY",BODY,{"derivedFrom":makeQuery(id+"F5.opPattern","COPY",BODY,{"derivedFrom":makeQuery(id+"F4.opPattern","COPY",BODY,{"derivedFrom":makeQuery(id+"F1.opExtrude","SWEPT_BODY",BODY,{"disambiguationData":[OSD([sQuery(id+"F0.wireOp",EDGE,"E0.bottom"),sQuery(id+"F0.wireOp",EDGE,"E0.top"),sQuery(id+"F0.wireOp",EDGE,"E0.left"),sQuery(id+"F0.wireOp",EDGE,"E0.right")])]}),"instanceName":"1"}),"instanceName":"1"}),"instanceName":"1"}),"instanceName":"1"}),"instanceName":"1"}),"instanceName":"1"}),"instanceName":"1"}),"instanceName":"1"});
            var Q263;
            Q263=makeQuery(id+"F5.opPattern","COPY",BODY,{"derivedFrom":makeQuery(id+"F4.opPattern","COPY",BODY,{"derivedFrom":makeQuery(id+"F1.opExtrude","SWEPT_BODY",BODY,{"disambiguationData":[OSD([sQuery(id+"F0.wireOp",EDGE,"E0.bottom"),sQuery(id+"F0.wireOp",EDGE,"E0.top"),sQuery(id+"F0.wireOp",EDGE,"E0.left"),sQuery(id+"F0.wireOp",EDGE,"E0.right")])]}),"instanceName":"1"}),"instanceName":"1"});
            var Q264;
            Q264=makeQuery(id+"F42.opPattern","COPY",BODY,{"derivedFrom":makeQuery(id+"F29.opPattern","COPY",BODY,{"derivedFrom":makeQuery(id+"F28.opPattern","COPY",BODY,{"derivedFrom":makeQuery(id+"F19.opPattern","COPY",BODY,{"derivedFrom":makeQuery(id+"F17.opPattern","COPY",BODY,{"derivedFrom":makeQuery(id+"F13.opPattern","COPY",BODY,{"derivedFrom":makeQuery(id+"F5.opPattern","COPY",BODY,{"derivedFrom":makeQuery(id+"F4.opPattern","COPY",BODY,{"derivedFrom":makeQuery(id+"F1.opExtrude","SWEPT_BODY",BODY,{"disambiguationData":[OSD([sQuery(id+"F0.wireOp",EDGE,"E0.bottom"),sQuery(id+"F0.wireOp",EDGE,"E0.top"),sQuery(id+"F0.wireOp",EDGE,"E0.left"),sQuery(id+"F0.wireOp",EDGE,"E0.right")])]}),"instanceName":"1"}),"instanceName":"1"}),"instanceName":"1"}),"instanceName":"1"}),"instanceName":"1"}),"instanceName":"1"}),"instanceName":"1"}),"instanceName":"1"});
            var Q265;
            Q265=makeQuery(id+"F31.opPattern","COPY",BODY,{"derivedFrom":makeQuery(id+"F5.opPattern","COPY",BODY,{"derivedFrom":makeQuery(id+"F1.opExtrude","SWEPT_BODY",BODY,{"disambiguationData":[OSD([sQuery(id+"F0.wireOp",EDGE,"E0.bottom"),sQuery(id+"F0.wireOp",EDGE,"E0.top"),sQuery(id+"F0.wireOp",EDGE,"E0.left"),sQuery(id+"F0.wireOp",EDGE,"E0.right")])]}),"instanceName":"1"}),"instanceName":"1"});
            var Q266;
            Q266=makeQuery(id+"F17.opPattern","COPY",BODY,{"derivedFrom":makeQuery(id+"F12.opPattern","COPY",BODY,{"derivedFrom":makeQuery(id+"F6.opPattern","COPY",BODY,{"derivedFrom":makeQuery(id+"F5.opPattern","COPY",BODY,{"derivedFrom":makeQuery(id+"F4.opPattern","COPY",BODY,{"derivedFrom":makeQuery(id+"F1.opExtrude","SWEPT_BODY",BODY,{"disambiguationData":[OSD([sQuery(id+"F0.wireOp",EDGE,"E0.bottom"),sQuery(id+"F0.wireOp",EDGE,"E0.top"),sQuery(id+"F0.wireOp",EDGE,"E0.left"),sQuery(id+"F0.wireOp",EDGE,"E0.right")])]}),"instanceName":"1"}),"instanceName":"1"}),"instanceName":"1"}),"instanceName":"1"}),"instanceName":"1"});
            var Q267;
            Q267=makeQuery(id+"F29.opPattern","COPY",BODY,{"derivedFrom":makeQuery(id+"F28.opPattern","COPY",BODY,{"derivedFrom":makeQuery(id+"F23.opPattern","COPY",BODY,{"derivedFrom":makeQuery(id+"F19.opPattern","COPY",BODY,{"derivedFrom":makeQuery(id+"F15.opPattern","COPY",BODY,{"derivedFrom":makeQuery(id+"F12.opPattern","COPY",BODY,{"derivedFrom":makeQuery(id+"F6.opPattern","COPY",BODY,{"derivedFrom":makeQuery(id+"F5.opPattern","COPY",BODY,{"derivedFrom":makeQuery(id+"F4.opPattern","COPY",BODY,{"derivedFrom":makeQuery(id+"F2.opPattern","COPY",BODY,{"derivedFrom":makeQuery(id+"F1.opExtrude","SWEPT_BODY",BODY,{"disambiguationData":[OSD([sQuery(id+"F0.wireOp",EDGE,"E0.bottom"),sQuery(id+"F0.wireOp",EDGE,"E0.top"),sQuery(id+"F0.wireOp",EDGE,"E0.left"),sQuery(id+"F0.wireOp",EDGE,"E0.right")])]}),"instanceName":"1"}),"instanceName":"1"}),"instanceName":"1"}),"instanceName":"1"}),"instanceName":"1"}),"instanceName":"1"}),"instanceName":"1"}),"instanceName":"1"}),"instanceName":"1"}),"instanceName":"1"});
            var Q268;
            Q268=makeQuery(id+"F29.opPattern","COPY",BODY,{"derivedFrom":makeQuery(id+"F19.opPattern","COPY",BODY,{"derivedFrom":makeQuery(id+"F17.opPattern","COPY",BODY,{"derivedFrom":makeQuery(id+"F15.opPattern","COPY",BODY,{"derivedFrom":makeQuery(id+"F12.opPattern","COPY",BODY,{"derivedFrom":makeQuery(id+"F6.opPattern","COPY",BODY,{"derivedFrom":makeQuery(id+"F5.opPattern","COPY",BODY,{"derivedFrom":makeQuery(id+"F4.opPattern","COPY",BODY,{"derivedFrom":makeQuery(id+"F2.opPattern","COPY",BODY,{"derivedFrom":makeQuery(id+"F1.opExtrude","SWEPT_BODY",BODY,{"disambiguationData":[OSD([sQuery(id+"F0.wireOp",EDGE,"E0.bottom"),sQuery(id+"F0.wireOp",EDGE,"E0.top"),sQuery(id+"F0.wireOp",EDGE,"E0.left"),sQuery(id+"F0.wireOp",EDGE,"E0.right")])]}),"instanceName":"1"}),"instanceName":"1"}),"instanceName":"1"}),"instanceName":"1"}),"instanceName":"1"}),"instanceName":"1"}),"instanceName":"1"}),"instanceName":"1"}),"instanceName":"1"});
            var Q269;
            Q269=makeQuery(id+"F41.opPattern","COPY",BODY,{"derivedFrom":makeQuery(id+"F40.opPattern","COPY",BODY,{"derivedFrom":makeQuery(id+"F18.opPattern","COPY",BODY,{"derivedFrom":makeQuery(id+"F17.opPattern","COPY",BODY,{"derivedFrom":makeQuery(id+"F15.opPattern","COPY",BODY,{"derivedFrom":makeQuery(id+"F12.opPattern","COPY",BODY,{"derivedFrom":makeQuery(id+"F6.opPattern","COPY",BODY,{"derivedFrom":makeQuery(id+"F5.opPattern","COPY",BODY,{"derivedFrom":makeQuery(id+"F4.opPattern","COPY",BODY,{"derivedFrom":makeQuery(id+"F2.opPattern","COPY",BODY,{"derivedFrom":makeQuery(id+"F1.opExtrude","SWEPT_BODY",BODY,{"disambiguationData":[OSD([sQuery(id+"F0.wireOp",EDGE,"E0.bottom"),sQuery(id+"F0.wireOp",EDGE,"E0.top"),sQuery(id+"F0.wireOp",EDGE,"E0.left"),sQuery(id+"F0.wireOp",EDGE,"E0.right")])]}),"instanceName":"1"}),"instanceName":"1"}),"instanceName":"1"}),"instanceName":"1"}),"instanceName":"1"}),"instanceName":"1"}),"instanceName":"1"}),"instanceName":"1"}),"instanceName":"1"}),"instanceName":"1"});
            var Q270;
            Q270=makeQuery(id+"F8.opPattern","COPY",BODY,{"derivedFrom":makeQuery(id+"F5.opPattern","COPY",BODY,{"derivedFrom":makeQuery(id+"F4.opPattern","COPY",BODY,{"derivedFrom":makeQuery(id+"F1.opExtrude","SWEPT_BODY",BODY,{"disambiguationData":[OSD([sQuery(id+"F0.wireOp",EDGE,"E0.bottom"),sQuery(id+"F0.wireOp",EDGE,"E0.top"),sQuery(id+"F0.wireOp",EDGE,"E0.left"),sQuery(id+"F0.wireOp",EDGE,"E0.right")])]}),"instanceName":"1"}),"instanceName":"1"}),"instanceName":"1"});
            var Q271;
            Q271=makeQuery(id+"F29.opPattern","COPY",BODY,{"derivedFrom":makeQuery(id+"F26.opPattern","COPY",BODY,{"derivedFrom":makeQuery(id+"F19.opPattern","COPY",BODY,{"derivedFrom":makeQuery(id+"F15.opPattern","COPY",BODY,{"derivedFrom":makeQuery(id+"F12.opPattern","COPY",BODY,{"derivedFrom":makeQuery(id+"F6.opPattern","COPY",BODY,{"derivedFrom":makeQuery(id+"F5.opPattern","COPY",BODY,{"derivedFrom":makeQuery(id+"F4.opPattern","COPY",BODY,{"derivedFrom":makeQuery(id+"F2.opPattern","COPY",BODY,{"derivedFrom":makeQuery(id+"F1.opExtrude","SWEPT_BODY",BODY,{"disambiguationData":[OSD([sQuery(id+"F0.wireOp",EDGE,"E0.bottom"),sQuery(id+"F0.wireOp",EDGE,"E0.top"),sQuery(id+"F0.wireOp",EDGE,"E0.left"),sQuery(id+"F0.wireOp",EDGE,"E0.right")])]}),"instanceName":"1"}),"instanceName":"1"}),"instanceName":"1"}),"instanceName":"1"}),"instanceName":"1"}),"instanceName":"1"}),"instanceName":"1"}),"instanceName":"1"}),"instanceName":"1"});
            var Q272;
            Q272=makeQuery(id+"F40.opPattern","COPY",BODY,{"derivedFrom":makeQuery(id+"F19.opPattern","COPY",BODY,{"derivedFrom":makeQuery(id+"F17.opPattern","COPY",BODY,{"derivedFrom":makeQuery(id+"F12.opPattern","COPY",BODY,{"derivedFrom":makeQuery(id+"F6.opPattern","COPY",BODY,{"derivedFrom":makeQuery(id+"F5.opPattern","COPY",BODY,{"derivedFrom":makeQuery(id+"F4.opPattern","COPY",BODY,{"derivedFrom":makeQuery(id+"F1.opExtrude","SWEPT_BODY",BODY,{"disambiguationData":[OSD([sQuery(id+"F0.wireOp",EDGE,"E0.bottom"),sQuery(id+"F0.wireOp",EDGE,"E0.top"),sQuery(id+"F0.wireOp",EDGE,"E0.left"),sQuery(id+"F0.wireOp",EDGE,"E0.right")])]}),"instanceName":"1"}),"instanceName":"1"}),"instanceName":"1"}),"instanceName":"1"}),"instanceName":"1"}),"instanceName":"1"}),"instanceName":"1"});
            var Q273;
            Q273=makeQuery(id+"F40.opPattern","COPY",BODY,{"derivedFrom":makeQuery(id+"F12.opPattern","COPY",BODY,{"derivedFrom":makeQuery(id+"F6.opPattern","COPY",BODY,{"derivedFrom":makeQuery(id+"F5.opPattern","COPY",BODY,{"derivedFrom":makeQuery(id+"F4.opPattern","COPY",BODY,{"derivedFrom":makeQuery(id+"F1.opExtrude","SWEPT_BODY",BODY,{"disambiguationData":[OSD([sQuery(id+"F0.wireOp",EDGE,"E0.bottom"),sQuery(id+"F0.wireOp",EDGE,"E0.top"),sQuery(id+"F0.wireOp",EDGE,"E0.left"),sQuery(id+"F0.wireOp",EDGE,"E0.right")])]}),"instanceName":"1"}),"instanceName":"1"}),"instanceName":"1"}),"instanceName":"1"}),"instanceName":"1"});
            var Q274;
            Q274=makeQuery(id+"F26.opPattern","COPY",BODY,{"derivedFrom":makeQuery(id+"F23.opPattern","COPY",BODY,{"derivedFrom":makeQuery(id+"F19.opPattern","COPY",BODY,{"derivedFrom":makeQuery(id+"F15.opPattern","COPY",BODY,{"derivedFrom":makeQuery(id+"F12.opPattern","COPY",BODY,{"derivedFrom":makeQuery(id+"F6.opPattern","COPY",BODY,{"derivedFrom":makeQuery(id+"F5.opPattern","COPY",BODY,{"derivedFrom":makeQuery(id+"F4.opPattern","COPY",BODY,{"derivedFrom":makeQuery(id+"F2.opPattern","COPY",BODY,{"derivedFrom":makeQuery(id+"F1.opExtrude","SWEPT_BODY",BODY,{"disambiguationData":[OSD([sQuery(id+"F0.wireOp",EDGE,"E0.bottom"),sQuery(id+"F0.wireOp",EDGE,"E0.top"),sQuery(id+"F0.wireOp",EDGE,"E0.left"),sQuery(id+"F0.wireOp",EDGE,"E0.right")])]}),"instanceName":"1"}),"instanceName":"1"}),"instanceName":"1"}),"instanceName":"1"}),"instanceName":"1"}),"instanceName":"1"}),"instanceName":"1"}),"instanceName":"1"}),"instanceName":"1"});
            var Q275;
            Q275=makeQuery(id+"F26.opPattern","COPY",BODY,{"derivedFrom":makeQuery(id+"F17.opPattern","COPY",BODY,{"derivedFrom":makeQuery(id+"F5.opPattern","COPY",BODY,{"derivedFrom":makeQuery(id+"F4.opPattern","COPY",BODY,{"derivedFrom":makeQuery(id+"F1.opExtrude","SWEPT_BODY",BODY,{"disambiguationData":[OSD([sQuery(id+"F0.wireOp",EDGE,"E0.bottom"),sQuery(id+"F0.wireOp",EDGE,"E0.top"),sQuery(id+"F0.wireOp",EDGE,"E0.left"),sQuery(id+"F0.wireOp",EDGE,"E0.right")])]}),"instanceName":"1"}),"instanceName":"1"}),"instanceName":"1"}),"instanceName":"1"});
            var Q276;
            Q276=makeQuery(id+"F31.opPattern","COPY",BODY,{"derivedFrom":makeQuery(id+"F5.opPattern","COPY",BODY,{"derivedFrom":makeQuery(id+"F2.opPattern","COPY",BODY,{"derivedFrom":makeQuery(id+"F1.opExtrude","SWEPT_BODY",BODY,{"disambiguationData":[OSD([sQuery(id+"F0.wireOp",EDGE,"E0.bottom"),sQuery(id+"F0.wireOp",EDGE,"E0.top"),sQuery(id+"F0.wireOp",EDGE,"E0.left"),sQuery(id+"F0.wireOp",EDGE,"E0.right")])]}),"instanceName":"1"}),"instanceName":"1"}),"instanceName":"1"});
            var Q277;
            Q277=makeQuery(id+"F40.opPattern","COPY",BODY,{"derivedFrom":makeQuery(id+"F28.opPattern","COPY",BODY,{"derivedFrom":makeQuery(id+"F19.opPattern","COPY",BODY,{"derivedFrom":makeQuery(id+"F17.opPattern","COPY",BODY,{"derivedFrom":makeQuery(id+"F15.opPattern","COPY",BODY,{"derivedFrom":makeQuery(id+"F12.opPattern","COPY",BODY,{"derivedFrom":makeQuery(id+"F6.opPattern","COPY",BODY,{"derivedFrom":makeQuery(id+"F5.opPattern","COPY",BODY,{"derivedFrom":makeQuery(id+"F4.opPattern","COPY",BODY,{"derivedFrom":makeQuery(id+"F2.opPattern","COPY",BODY,{"derivedFrom":makeQuery(id+"F1.opExtrude","SWEPT_BODY",BODY,{"disambiguationData":[OSD([sQuery(id+"F0.wireOp",EDGE,"E0.bottom"),sQuery(id+"F0.wireOp",EDGE,"E0.top"),sQuery(id+"F0.wireOp",EDGE,"E0.left"),sQuery(id+"F0.wireOp",EDGE,"E0.right")])]}),"instanceName":"1"}),"instanceName":"1"}),"instanceName":"1"}),"instanceName":"1"}),"instanceName":"1"}),"instanceName":"1"}),"instanceName":"1"}),"instanceName":"1"}),"instanceName":"1"}),"instanceName":"1"});
            var Q278;
            Q278=makeQuery(id+"F33.opPattern","COPY",BODY,{"derivedFrom":makeQuery(id+"F31.opPattern","COPY",BODY,{"derivedFrom":makeQuery(id+"F2.opPattern","COPY",BODY,{"derivedFrom":makeQuery(id+"F1.opExtrude","SWEPT_BODY",BODY,{"disambiguationData":[OSD([sQuery(id+"F0.wireOp",EDGE,"E0.bottom"),sQuery(id+"F0.wireOp",EDGE,"E0.top"),sQuery(id+"F0.wireOp",EDGE,"E0.left"),sQuery(id+"F0.wireOp",EDGE,"E0.right")])]}),"instanceName":"1"}),"instanceName":"1"}),"instanceName":"1"});
            var Q279;
            Q279=makeQuery(id+"F19.opPattern","COPY",BODY,{"derivedFrom":makeQuery(id+"F17.opPattern","COPY",BODY,{"derivedFrom":makeQuery(id+"F5.opPattern","COPY",BODY,{"derivedFrom":makeQuery(id+"F4.opPattern","COPY",BODY,{"derivedFrom":makeQuery(id+"F2.opPattern","COPY",BODY,{"derivedFrom":makeQuery(id+"F1.opExtrude","SWEPT_BODY",BODY,{"disambiguationData":[OSD([sQuery(id+"F0.wireOp",EDGE,"E0.bottom"),sQuery(id+"F0.wireOp",EDGE,"E0.top"),sQuery(id+"F0.wireOp",EDGE,"E0.left"),sQuery(id+"F0.wireOp",EDGE,"E0.right")])]}),"instanceName":"1"}),"instanceName":"1"}),"instanceName":"1"}),"instanceName":"1"}),"instanceName":"1"});
            var Q280;
            Q280=makeQuery(id+"F39.opPattern","COPY",BODY,{"derivedFrom":makeQuery(id+"F26.opPattern","COPY",BODY,{"derivedFrom":makeQuery(id+"F19.opPattern","COPY",BODY,{"derivedFrom":makeQuery(id+"F17.opPattern","COPY",BODY,{"derivedFrom":makeQuery(id+"F13.opPattern","COPY",BODY,{"derivedFrom":makeQuery(id+"F5.opPattern","COPY",BODY,{"derivedFrom":makeQuery(id+"F4.opPattern","COPY",BODY,{"derivedFrom":makeQuery(id+"F1.opExtrude","SWEPT_BODY",BODY,{"disambiguationData":[OSD([sQuery(id+"F0.wireOp",EDGE,"E0.bottom"),sQuery(id+"F0.wireOp",EDGE,"E0.top"),sQuery(id+"F0.wireOp",EDGE,"E0.left"),sQuery(id+"F0.wireOp",EDGE,"E0.right")])]}),"instanceName":"1"}),"instanceName":"1"}),"instanceName":"1"}),"instanceName":"1"}),"instanceName":"1"}),"instanceName":"1"}),"instanceName":"1"});
            var Q281;
            Q281=makeQuery(id+"F45.opPattern","COPY",BODY,{"derivedFrom":makeQuery(id+"F40.opPattern","COPY",BODY,{"derivedFrom":makeQuery(id+"F28.opPattern","COPY",BODY,{"derivedFrom":makeQuery(id+"F23.opPattern","COPY",BODY,{"derivedFrom":makeQuery(id+"F19.opPattern","COPY",BODY,{"derivedFrom":makeQuery(id+"F15.opPattern","COPY",BODY,{"derivedFrom":makeQuery(id+"F12.opPattern","COPY",BODY,{"derivedFrom":makeQuery(id+"F6.opPattern","COPY",BODY,{"derivedFrom":makeQuery(id+"F5.opPattern","COPY",BODY,{"derivedFrom":makeQuery(id+"F4.opPattern","COPY",BODY,{"derivedFrom":makeQuery(id+"F2.opPattern","COPY",BODY,{"derivedFrom":makeQuery(id+"F1.opExtrude","SWEPT_BODY",BODY,{"disambiguationData":[OSD([sQuery(id+"F0.wireOp",EDGE,"E0.bottom"),sQuery(id+"F0.wireOp",EDGE,"E0.top"),sQuery(id+"F0.wireOp",EDGE,"E0.left"),sQuery(id+"F0.wireOp",EDGE,"E0.right")])]}),"instanceName":"1"}),"instanceName":"1"}),"instanceName":"1"}),"instanceName":"1"}),"instanceName":"1"}),"instanceName":"1"}),"instanceName":"1"}),"instanceName":"1"}),"instanceName":"1"}),"instanceName":"1"}),"instanceName":"1"});
            var Q282;
            Q282=makeQuery(id+"F49.opPattern","COPY",BODY,{"derivedFrom":makeQuery(id+"F42.opPattern","COPY",BODY,{"derivedFrom":makeQuery(id+"F29.opPattern","COPY",BODY,{"derivedFrom":makeQuery(id+"F19.opPattern","COPY",BODY,{"derivedFrom":makeQuery(id+"F17.opPattern","COPY",BODY,{"derivedFrom":makeQuery(id+"F13.opPattern","COPY",BODY,{"derivedFrom":makeQuery(id+"F5.opPattern","COPY",BODY,{"derivedFrom":makeQuery(id+"F4.opPattern","COPY",BODY,{"derivedFrom":makeQuery(id+"F1.opExtrude","SWEPT_BODY",BODY,{"disambiguationData":[OSD([sQuery(id+"F0.wireOp",EDGE,"E0.bottom"),sQuery(id+"F0.wireOp",EDGE,"E0.top"),sQuery(id+"F0.wireOp",EDGE,"E0.left"),sQuery(id+"F0.wireOp",EDGE,"E0.right")])]}),"instanceName":"1"}),"instanceName":"1"}),"instanceName":"1"}),"instanceName":"1"}),"instanceName":"1"}),"instanceName":"1"}),"instanceName":"1"}),"instanceName":"1"});
            var Q283;
            Q283=makeQuery(id+"F40.opPattern","COPY",BODY,{"derivedFrom":makeQuery(id+"F19.opPattern","COPY",BODY,{"derivedFrom":makeQuery(id+"F17.opPattern","COPY",BODY,{"derivedFrom":makeQuery(id+"F12.opPattern","COPY",BODY,{"derivedFrom":makeQuery(id+"F6.opPattern","COPY",BODY,{"derivedFrom":makeQuery(id+"F5.opPattern","COPY",BODY,{"derivedFrom":makeQuery(id+"F4.opPattern","COPY",BODY,{"derivedFrom":makeQuery(id+"F2.opPattern","COPY",BODY,{"derivedFrom":makeQuery(id+"F1.opExtrude","SWEPT_BODY",BODY,{"disambiguationData":[OSD([sQuery(id+"F0.wireOp",EDGE,"E0.bottom"),sQuery(id+"F0.wireOp",EDGE,"E0.top"),sQuery(id+"F0.wireOp",EDGE,"E0.left"),sQuery(id+"F0.wireOp",EDGE,"E0.right")])]}),"instanceName":"1"}),"instanceName":"1"}),"instanceName":"1"}),"instanceName":"1"}),"instanceName":"1"}),"instanceName":"1"}),"instanceName":"1"}),"instanceName":"1"});
            var Q284;
            Q284=makeQuery(id+"F9.opPattern","COPY",BODY,{"derivedFrom":makeQuery(id+"F6.opPattern","COPY",BODY,{"derivedFrom":makeQuery(id+"F4.opPattern","COPY",BODY,{"derivedFrom":makeQuery(id+"F1.opExtrude","SWEPT_BODY",BODY,{"disambiguationData":[OSD([sQuery(id+"F0.wireOp",EDGE,"E0.bottom"),sQuery(id+"F0.wireOp",EDGE,"E0.top"),sQuery(id+"F0.wireOp",EDGE,"E0.left"),sQuery(id+"F0.wireOp",EDGE,"E0.right")])]}),"instanceName":"1"}),"instanceName":"1"}),"instanceName":"1"});
            var Q285;
            Q285=makeQuery(id+"F29.opPattern","COPY",BODY,{"derivedFrom":makeQuery(id+"F19.opPattern","COPY",BODY,{"derivedFrom":makeQuery(id+"F13.opPattern","COPY",BODY,{"derivedFrom":makeQuery(id+"F5.opPattern","COPY",BODY,{"derivedFrom":makeQuery(id+"F4.opPattern","COPY",BODY,{"derivedFrom":makeQuery(id+"F1.opExtrude","SWEPT_BODY",BODY,{"disambiguationData":[OSD([sQuery(id+"F0.wireOp",EDGE,"E0.bottom"),sQuery(id+"F0.wireOp",EDGE,"E0.top"),sQuery(id+"F0.wireOp",EDGE,"E0.left"),sQuery(id+"F0.wireOp",EDGE,"E0.right")])]}),"instanceName":"1"}),"instanceName":"1"}),"instanceName":"1"}),"instanceName":"1"}),"instanceName":"1"});
            var Q286;
            Q286=makeQuery(id+"F13.opPattern","COPY",BODY,{"derivedFrom":makeQuery(id+"F5.opPattern","COPY",BODY,{"derivedFrom":makeQuery(id+"F4.opPattern","COPY",BODY,{"derivedFrom":makeQuery(id+"F1.opExtrude","SWEPT_BODY",BODY,{"disambiguationData":[OSD([sQuery(id+"F0.wireOp",EDGE,"E0.bottom"),sQuery(id+"F0.wireOp",EDGE,"E0.top"),sQuery(id+"F0.wireOp",EDGE,"E0.left"),sQuery(id+"F0.wireOp",EDGE,"E0.right")])]}),"instanceName":"1"}),"instanceName":"1"}),"instanceName":"1"});
            var Q287;
            Q287=makeQuery(id+"F36.opPattern","COPY",BODY,{"derivedFrom":makeQuery(id+"F35.opPattern","COPY",BODY,{"derivedFrom":makeQuery(id+"F31.opPattern","COPY",BODY,{"derivedFrom":makeQuery(id+"F5.opPattern","COPY",BODY,{"derivedFrom":makeQuery(id+"F1.opExtrude","SWEPT_BODY",BODY,{"disambiguationData":[OSD([sQuery(id+"F0.wireOp",EDGE,"E0.bottom"),sQuery(id+"F0.wireOp",EDGE,"E0.top"),sQuery(id+"F0.wireOp",EDGE,"E0.left"),sQuery(id+"F0.wireOp",EDGE,"E0.right")])]}),"instanceName":"1"}),"instanceName":"1"}),"instanceName":"1"}),"instanceName":"1"});
            var Q288;
            Q288=makeQuery(id+"F35.opPattern","COPY",BODY,{"derivedFrom":makeQuery(id+"F34.opPattern","COPY",BODY,{"derivedFrom":makeQuery(id+"F31.opPattern","COPY",BODY,{"derivedFrom":makeQuery(id+"F5.opPattern","COPY",BODY,{"derivedFrom":makeQuery(id+"F1.opExtrude","SWEPT_BODY",BODY,{"disambiguationData":[OSD([sQuery(id+"F0.wireOp",EDGE,"E0.bottom"),sQuery(id+"F0.wireOp",EDGE,"E0.top"),sQuery(id+"F0.wireOp",EDGE,"E0.left"),sQuery(id+"F0.wireOp",EDGE,"E0.right")])]}),"instanceName":"1"}),"instanceName":"1"}),"instanceName":"1"}),"instanceName":"1"});
            var Q289;
            Q289=makeQuery(id+"F49.opPattern","COPY",BODY,{"derivedFrom":makeQuery(id+"F42.opPattern","COPY",BODY,{"derivedFrom":makeQuery(id+"F29.opPattern","COPY",BODY,{"derivedFrom":makeQuery(id+"F28.opPattern","COPY",BODY,{"derivedFrom":makeQuery(id+"F23.opPattern","COPY",BODY,{"derivedFrom":makeQuery(id+"F19.opPattern","COPY",BODY,{"derivedFrom":makeQuery(id+"F15.opPattern","COPY",BODY,{"derivedFrom":makeQuery(id+"F12.opPattern","COPY",BODY,{"derivedFrom":makeQuery(id+"F6.opPattern","COPY",BODY,{"derivedFrom":makeQuery(id+"F5.opPattern","COPY",BODY,{"derivedFrom":makeQuery(id+"F4.opPattern","COPY",BODY,{"derivedFrom":makeQuery(id+"F2.opPattern","COPY",BODY,{"derivedFrom":makeQuery(id+"F1.opExtrude","SWEPT_BODY",BODY,{"disambiguationData":[OSD([sQuery(id+"F0.wireOp",EDGE,"E0.bottom"),sQuery(id+"F0.wireOp",EDGE,"E0.top"),sQuery(id+"F0.wireOp",EDGE,"E0.left"),sQuery(id+"F0.wireOp",EDGE,"E0.right")])]}),"instanceName":"1"}),"instanceName":"1"}),"instanceName":"1"}),"instanceName":"1"}),"instanceName":"1"}),"instanceName":"1"}),"instanceName":"1"}),"instanceName":"1"}),"instanceName":"1"}),"instanceName":"1"}),"instanceName":"1"}),"instanceName":"1"});
            var Q290;
            Q290=makeQuery(id+"F40.opPattern","COPY",BODY,{"derivedFrom":makeQuery(id+"F17.opPattern","COPY",BODY,{"derivedFrom":makeQuery(id+"F15.opPattern","COPY",BODY,{"derivedFrom":makeQuery(id+"F12.opPattern","COPY",BODY,{"derivedFrom":makeQuery(id+"F6.opPattern","COPY",BODY,{"derivedFrom":makeQuery(id+"F5.opPattern","COPY",BODY,{"derivedFrom":makeQuery(id+"F4.opPattern","COPY",BODY,{"derivedFrom":makeQuery(id+"F2.opPattern","COPY",BODY,{"derivedFrom":makeQuery(id+"F1.opExtrude","SWEPT_BODY",BODY,{"disambiguationData":[OSD([sQuery(id+"F0.wireOp",EDGE,"E0.bottom"),sQuery(id+"F0.wireOp",EDGE,"E0.top"),sQuery(id+"F0.wireOp",EDGE,"E0.left"),sQuery(id+"F0.wireOp",EDGE,"E0.right")])]}),"instanceName":"1"}),"instanceName":"1"}),"instanceName":"1"}),"instanceName":"1"}),"instanceName":"1"}),"instanceName":"1"}),"instanceName":"1"}),"instanceName":"1"});
            var Q291;
            Q291=makeQuery(id+"F23.opPattern","COPY",BODY,{"derivedFrom":makeQuery(id+"F21.opPattern","COPY",BODY,{"derivedFrom":makeQuery(id+"F19.opPattern","COPY",BODY,{"derivedFrom":makeQuery(id+"F6.opPattern","COPY",BODY,{"derivedFrom":makeQuery(id+"F5.opPattern","COPY",BODY,{"derivedFrom":makeQuery(id+"F4.opPattern","COPY",BODY,{"derivedFrom":makeQuery(id+"F2.opPattern","COPY",BODY,{"derivedFrom":makeQuery(id+"F1.opExtrude","SWEPT_BODY",BODY,{"disambiguationData":[OSD([sQuery(id+"F0.wireOp",EDGE,"E0.bottom"),sQuery(id+"F0.wireOp",EDGE,"E0.top"),sQuery(id+"F0.wireOp",EDGE,"E0.left"),sQuery(id+"F0.wireOp",EDGE,"E0.right")])]}),"instanceName":"1"}),"instanceName":"1"}),"instanceName":"1"}),"instanceName":"1"}),"instanceName":"1"}),"instanceName":"1"}),"instanceName":"1"});
            var Q292;
            Q292=makeQuery(id+"F23.opPattern","COPY",BODY,{"derivedFrom":makeQuery(id+"F19.opPattern","COPY",BODY,{"derivedFrom":makeQuery(id+"F17.opPattern","COPY",BODY,{"derivedFrom":makeQuery(id+"F6.opPattern","COPY",BODY,{"derivedFrom":makeQuery(id+"F5.opPattern","COPY",BODY,{"derivedFrom":makeQuery(id+"F4.opPattern","COPY",BODY,{"derivedFrom":makeQuery(id+"F2.opPattern","COPY",BODY,{"derivedFrom":makeQuery(id+"F1.opExtrude","SWEPT_BODY",BODY,{"disambiguationData":[OSD([sQuery(id+"F0.wireOp",EDGE,"E0.bottom"),sQuery(id+"F0.wireOp",EDGE,"E0.top"),sQuery(id+"F0.wireOp",EDGE,"E0.left"),sQuery(id+"F0.wireOp",EDGE,"E0.right")])]}),"instanceName":"1"}),"instanceName":"1"}),"instanceName":"1"}),"instanceName":"1"}),"instanceName":"1"}),"instanceName":"1"}),"instanceName":"1"});
            var Q293;
            Q293=makeQuery(id+"F24.opPattern","COPY",BODY,{"derivedFrom":makeQuery(id+"F23.opPattern","COPY",BODY,{"derivedFrom":makeQuery(id+"F19.opPattern","COPY",BODY,{"derivedFrom":makeQuery(id+"F17.opPattern","COPY",BODY,{"derivedFrom":makeQuery(id+"F5.opPattern","COPY",BODY,{"derivedFrom":makeQuery(id+"F4.opPattern","COPY",BODY,{"derivedFrom":makeQuery(id+"F2.opPattern","COPY",BODY,{"derivedFrom":makeQuery(id+"F1.opExtrude","SWEPT_BODY",BODY,{"disambiguationData":[OSD([sQuery(id+"F0.wireOp",EDGE,"E0.bottom"),sQuery(id+"F0.wireOp",EDGE,"E0.top"),sQuery(id+"F0.wireOp",EDGE,"E0.left"),sQuery(id+"F0.wireOp",EDGE,"E0.right")])]}),"instanceName":"1"}),"instanceName":"1"}),"instanceName":"1"}),"instanceName":"1"}),"instanceName":"1"}),"instanceName":"1"}),"instanceName":"1"});
            var Q294;
            Q294=makeQuery(id+"F11.opPattern","COPY",BODY,{"derivedFrom":makeQuery(id+"F4.opPattern","COPY",BODY,{"derivedFrom":makeQuery(id+"F2.opPattern","COPY",BODY,{"derivedFrom":makeQuery(id+"F1.opExtrude","SWEPT_BODY",BODY,{"disambiguationData":[OSD([sQuery(id+"F0.wireOp",EDGE,"E0.bottom"),sQuery(id+"F0.wireOp",EDGE,"E0.top"),sQuery(id+"F0.wireOp",EDGE,"E0.left"),sQuery(id+"F0.wireOp",EDGE,"E0.right")])]}),"instanceName":"1"}),"instanceName":"1"}),"instanceName":"1"});
            var Q295;
            Q295=makeQuery(id+"F23.opPattern","COPY",BODY,{"derivedFrom":makeQuery(id+"F21.opPattern","COPY",BODY,{"derivedFrom":makeQuery(id+"F19.opPattern","COPY",BODY,{"derivedFrom":makeQuery(id+"F17.opPattern","COPY",BODY,{"derivedFrom":makeQuery(id+"F6.opPattern","COPY",BODY,{"derivedFrom":makeQuery(id+"F5.opPattern","COPY",BODY,{"derivedFrom":makeQuery(id+"F4.opPattern","COPY",BODY,{"derivedFrom":makeQuery(id+"F2.opPattern","COPY",BODY,{"derivedFrom":makeQuery(id+"F1.opExtrude","SWEPT_BODY",BODY,{"disambiguationData":[OSD([sQuery(id+"F0.wireOp",EDGE,"E0.bottom"),sQuery(id+"F0.wireOp",EDGE,"E0.top"),sQuery(id+"F0.wireOp",EDGE,"E0.left"),sQuery(id+"F0.wireOp",EDGE,"E0.right")])]}),"instanceName":"1"}),"instanceName":"1"}),"instanceName":"1"}),"instanceName":"1"}),"instanceName":"1"}),"instanceName":"1"}),"instanceName":"1"}),"instanceName":"1"});
            var Q296;
            Q296=makeQuery(id+"F40.opPattern","COPY",BODY,{"derivedFrom":makeQuery(id+"F28.opPattern","COPY",BODY,{"derivedFrom":makeQuery(id+"F23.opPattern","COPY",BODY,{"derivedFrom":makeQuery(id+"F19.opPattern","COPY",BODY,{"derivedFrom":makeQuery(id+"F17.opPattern","COPY",BODY,{"derivedFrom":makeQuery(id+"F13.opPattern","COPY",BODY,{"derivedFrom":makeQuery(id+"F5.opPattern","COPY",BODY,{"derivedFrom":makeQuery(id+"F4.opPattern","COPY",BODY,{"derivedFrom":makeQuery(id+"F1.opExtrude","SWEPT_BODY",BODY,{"disambiguationData":[OSD([sQuery(id+"F0.wireOp",EDGE,"E0.bottom"),sQuery(id+"F0.wireOp",EDGE,"E0.top"),sQuery(id+"F0.wireOp",EDGE,"E0.left"),sQuery(id+"F0.wireOp",EDGE,"E0.right")])]}),"instanceName":"1"}),"instanceName":"1"}),"instanceName":"1"}),"instanceName":"1"}),"instanceName":"1"}),"instanceName":"1"}),"instanceName":"1"}),"instanceName":"1"});
            var Q297;
            Q297=makeQuery(id+"F12.opPattern","COPY",BODY,{"derivedFrom":makeQuery(id+"F6.opPattern","COPY",BODY,{"derivedFrom":makeQuery(id+"F5.opPattern","COPY",BODY,{"derivedFrom":makeQuery(id+"F4.opPattern","COPY",BODY,{"derivedFrom":makeQuery(id+"F2.opPattern","COPY",BODY,{"derivedFrom":makeQuery(id+"F1.opExtrude","SWEPT_BODY",BODY,{"disambiguationData":[OSD([sQuery(id+"F0.wireOp",EDGE,"E0.bottom"),sQuery(id+"F0.wireOp",EDGE,"E0.top"),sQuery(id+"F0.wireOp",EDGE,"E0.left"),sQuery(id+"F0.wireOp",EDGE,"E0.right")])]}),"instanceName":"1"}),"instanceName":"1"}),"instanceName":"1"}),"instanceName":"1"}),"instanceName":"1"});
            var Q298;
            Q298=makeQuery(id+"F38.opPattern","COPY",BODY,{"derivedFrom":makeQuery(id+"F35.opPattern","COPY",BODY,{"derivedFrom":makeQuery(id+"F34.opPattern","COPY",BODY,{"derivedFrom":makeQuery(id+"F31.opPattern","COPY",BODY,{"derivedFrom":makeQuery(id+"F4.opPattern","COPY",BODY,{"derivedFrom":makeQuery(id+"F2.opPattern","COPY",BODY,{"derivedFrom":makeQuery(id+"F1.opExtrude","SWEPT_BODY",BODY,{"disambiguationData":[OSD([sQuery(id+"F0.wireOp",EDGE,"E0.bottom"),sQuery(id+"F0.wireOp",EDGE,"E0.top"),sQuery(id+"F0.wireOp",EDGE,"E0.left"),sQuery(id+"F0.wireOp",EDGE,"E0.right")])]}),"instanceName":"1"}),"instanceName":"1"}),"instanceName":"1"}),"instanceName":"1"}),"instanceName":"1"}),"instanceName":"1"});
            var Q299;
            Q299=makeQuery(id+"F34.opPattern","COPY",BODY,{"derivedFrom":makeQuery(id+"F31.opPattern","COPY",BODY,{"derivedFrom":makeQuery(id+"F2.opPattern","COPY",BODY,{"derivedFrom":makeQuery(id+"F1.opExtrude","SWEPT_BODY",BODY,{"disambiguationData":[OSD([sQuery(id+"F0.wireOp",EDGE,"E0.bottom"),sQuery(id+"F0.wireOp",EDGE,"E0.top"),sQuery(id+"F0.wireOp",EDGE,"E0.left"),sQuery(id+"F0.wireOp",EDGE,"E0.right")])]}),"instanceName":"1"}),"instanceName":"1"}),"instanceName":"1"});
            var Q300;
            Q300=makeQuery(id+"F40.opPattern","COPY",BODY,{"derivedFrom":makeQuery(id+"F21.opPattern","COPY",BODY,{"derivedFrom":makeQuery(id+"F19.opPattern","COPY",BODY,{"derivedFrom":makeQuery(id+"F17.opPattern","COPY",BODY,{"derivedFrom":makeQuery(id+"F6.opPattern","COPY",BODY,{"derivedFrom":makeQuery(id+"F5.opPattern","COPY",BODY,{"derivedFrom":makeQuery(id+"F4.opPattern","COPY",BODY,{"derivedFrom":makeQuery(id+"F2.opPattern","COPY",BODY,{"derivedFrom":makeQuery(id+"F1.opExtrude","SWEPT_BODY",BODY,{"disambiguationData":[OSD([sQuery(id+"F0.wireOp",EDGE,"E0.bottom"),sQuery(id+"F0.wireOp",EDGE,"E0.top"),sQuery(id+"F0.wireOp",EDGE,"E0.left"),sQuery(id+"F0.wireOp",EDGE,"E0.right")])]}),"instanceName":"1"}),"instanceName":"1"}),"instanceName":"1"}),"instanceName":"1"}),"instanceName":"1"}),"instanceName":"1"}),"instanceName":"1"}),"instanceName":"1"});
            var Q301;
            Q301=makeQuery(id+"F6.opPattern","COPY",BODY,{"derivedFrom":makeQuery(id+"F5.opPattern","COPY",BODY,{"derivedFrom":makeQuery(id+"F2.opPattern","COPY",BODY,{"derivedFrom":makeQuery(id+"F1.opExtrude","SWEPT_BODY",BODY,{"disambiguationData":[OSD([sQuery(id+"F0.wireOp",EDGE,"E0.bottom"),sQuery(id+"F0.wireOp",EDGE,"E0.top"),sQuery(id+"F0.wireOp",EDGE,"E0.left"),sQuery(id+"F0.wireOp",EDGE,"E0.right")])]}),"instanceName":"1"}),"instanceName":"1"}),"instanceName":"1"});
            var Q302;
            Q302=makeQuery(id+"F19.opPattern","COPY",BODY,{"derivedFrom":makeQuery(id+"F6.opPattern","COPY",BODY,{"derivedFrom":makeQuery(id+"F5.opPattern","COPY",BODY,{"derivedFrom":makeQuery(id+"F4.opPattern","COPY",BODY,{"derivedFrom":makeQuery(id+"F2.opPattern","COPY",BODY,{"derivedFrom":makeQuery(id+"F1.opExtrude","SWEPT_BODY",BODY,{"disambiguationData":[OSD([sQuery(id+"F0.wireOp",EDGE,"E0.bottom"),sQuery(id+"F0.wireOp",EDGE,"E0.top"),sQuery(id+"F0.wireOp",EDGE,"E0.left"),sQuery(id+"F0.wireOp",EDGE,"E0.right")])]}),"instanceName":"1"}),"instanceName":"1"}),"instanceName":"1"}),"instanceName":"1"}),"instanceName":"1"});
            var Q303;
            Q303=makeQuery(id+"F5.opPattern","COPY",BODY,{"derivedFrom":makeQuery(id+"F4.opPattern","COPY",BODY,{"derivedFrom":makeQuery(id+"F2.opPattern","COPY",BODY,{"derivedFrom":makeQuery(id+"F1.opExtrude","SWEPT_BODY",BODY,{"disambiguationData":[OSD([sQuery(id+"F0.wireOp",EDGE,"E0.bottom"),sQuery(id+"F0.wireOp",EDGE,"E0.top"),sQuery(id+"F0.wireOp",EDGE,"E0.left"),sQuery(id+"F0.wireOp",EDGE,"E0.right")])]}),"instanceName":"1"}),"instanceName":"1"}),"instanceName":"1"});
            var Q304;
            Q304=makeQuery(id+"F38.opPattern","COPY",BODY,{"derivedFrom":makeQuery(id+"F37.opPattern","COPY",BODY,{"derivedFrom":makeQuery(id+"F35.opPattern","COPY",BODY,{"derivedFrom":makeQuery(id+"F34.opPattern","COPY",BODY,{"derivedFrom":makeQuery(id+"F31.opPattern","COPY",BODY,{"derivedFrom":makeQuery(id+"F5.opPattern","COPY",BODY,{"derivedFrom":makeQuery(id+"F1.opExtrude","SWEPT_BODY",BODY,{"disambiguationData":[OSD([sQuery(id+"F0.wireOp",EDGE,"E0.bottom"),sQuery(id+"F0.wireOp",EDGE,"E0.top"),sQuery(id+"F0.wireOp",EDGE,"E0.left"),sQuery(id+"F0.wireOp",EDGE,"E0.right")])]}),"instanceName":"1"}),"instanceName":"1"}),"instanceName":"1"}),"instanceName":"1"}),"instanceName":"1"}),"instanceName":"1"});
            var Q305;
            Q305=makeQuery(id+"F28.opPattern","COPY",BODY,{"derivedFrom":makeQuery(id+"F19.opPattern","COPY",BODY,{"derivedFrom":makeQuery(id+"F15.opPattern","COPY",BODY,{"derivedFrom":makeQuery(id+"F12.opPattern","COPY",BODY,{"derivedFrom":makeQuery(id+"F6.opPattern","COPY",BODY,{"derivedFrom":makeQuery(id+"F5.opPattern","COPY",BODY,{"derivedFrom":makeQuery(id+"F4.opPattern","COPY",BODY,{"derivedFrom":makeQuery(id+"F2.opPattern","COPY",BODY,{"derivedFrom":makeQuery(id+"F1.opExtrude","SWEPT_BODY",BODY,{"disambiguationData":[OSD([sQuery(id+"F0.wireOp",EDGE,"E0.bottom"),sQuery(id+"F0.wireOp",EDGE,"E0.top"),sQuery(id+"F0.wireOp",EDGE,"E0.left"),sQuery(id+"F0.wireOp",EDGE,"E0.right")])]}),"instanceName":"1"}),"instanceName":"1"}),"instanceName":"1"}),"instanceName":"1"}),"instanceName":"1"}),"instanceName":"1"}),"instanceName":"1"}),"instanceName":"1"});
            var Q306;
            Q306=makeQuery(id+"F40.opPattern","COPY",BODY,{"derivedFrom":makeQuery(id+"F26.opPattern","COPY",BODY,{"derivedFrom":makeQuery(id+"F17.opPattern","COPY",BODY,{"derivedFrom":makeQuery(id+"F5.opPattern","COPY",BODY,{"derivedFrom":makeQuery(id+"F4.opPattern","COPY",BODY,{"derivedFrom":makeQuery(id+"F1.opExtrude","SWEPT_BODY",BODY,{"disambiguationData":[OSD([sQuery(id+"F0.wireOp",EDGE,"E0.bottom"),sQuery(id+"F0.wireOp",EDGE,"E0.top"),sQuery(id+"F0.wireOp",EDGE,"E0.left"),sQuery(id+"F0.wireOp",EDGE,"E0.right")])]}),"instanceName":"1"}),"instanceName":"1"}),"instanceName":"1"}),"instanceName":"1"}),"instanceName":"1"});
            var Q307;
            Q307=makeQuery(id+"F24.opPattern","COPY",BODY,{"derivedFrom":makeQuery(id+"F23.opPattern","COPY",BODY,{"derivedFrom":makeQuery(id+"F21.opPattern","COPY",BODY,{"derivedFrom":makeQuery(id+"F19.opPattern","COPY",BODY,{"derivedFrom":makeQuery(id+"F17.opPattern","COPY",BODY,{"derivedFrom":makeQuery(id+"F5.opPattern","COPY",BODY,{"derivedFrom":makeQuery(id+"F4.opPattern","COPY",BODY,{"derivedFrom":makeQuery(id+"F2.opPattern","COPY",BODY,{"derivedFrom":makeQuery(id+"F1.opExtrude","SWEPT_BODY",BODY,{"disambiguationData":[OSD([sQuery(id+"F0.wireOp",EDGE,"E0.bottom"),sQuery(id+"F0.wireOp",EDGE,"E0.top"),sQuery(id+"F0.wireOp",EDGE,"E0.left"),sQuery(id+"F0.wireOp",EDGE,"E0.right")])]}),"instanceName":"1"}),"instanceName":"1"}),"instanceName":"1"}),"instanceName":"1"}),"instanceName":"1"}),"instanceName":"1"}),"instanceName":"1"}),"instanceName":"1"});
            var Q308;
            Q308=makeQuery(id+"F35.opPattern","COPY",BODY,{"derivedFrom":makeQuery(id+"F31.opPattern","COPY",BODY,{"derivedFrom":makeQuery(id+"F5.opPattern","COPY",BODY,{"derivedFrom":makeQuery(id+"F1.opExtrude","SWEPT_BODY",BODY,{"disambiguationData":[OSD([sQuery(id+"F0.wireOp",EDGE,"E0.bottom"),sQuery(id+"F0.wireOp",EDGE,"E0.top"),sQuery(id+"F0.wireOp",EDGE,"E0.left"),sQuery(id+"F0.wireOp",EDGE,"E0.right")])]}),"instanceName":"1"}),"instanceName":"1"}),"instanceName":"1"});
            var Q309;
            Q309=makeQuery(id+"F2.opPattern","COPY",BODY,{"derivedFrom":makeQuery(id+"F1.opExtrude","SWEPT_BODY",BODY,{"disambiguationData":[OSD([sQuery(id+"F0.wireOp",EDGE,"E0.bottom"),sQuery(id+"F0.wireOp",EDGE,"E0.top"),sQuery(id+"F0.wireOp",EDGE,"E0.left"),sQuery(id+"F0.wireOp",EDGE,"E0.right")])]}),"instanceName":"1"});
            var Q310;
            Q310=makeQuery(id+"F37.opPattern","COPY",BODY,{"derivedFrom":makeQuery(id+"F35.opPattern","COPY",BODY,{"derivedFrom":makeQuery(id+"F31.opPattern","COPY",BODY,{"derivedFrom":makeQuery(id+"F4.opPattern","COPY",BODY,{"derivedFrom":makeQuery(id+"F2.opPattern","COPY",BODY,{"derivedFrom":makeQuery(id+"F1.opExtrude","SWEPT_BODY",BODY,{"disambiguationData":[OSD([sQuery(id+"F0.wireOp",EDGE,"E0.bottom"),sQuery(id+"F0.wireOp",EDGE,"E0.top"),sQuery(id+"F0.wireOp",EDGE,"E0.left"),sQuery(id+"F0.wireOp",EDGE,"E0.right")])]}),"instanceName":"1"}),"instanceName":"1"}),"instanceName":"1"}),"instanceName":"1"}),"instanceName":"1"});
            var Q311;
            Q311=makeQuery(id+"F5.opPattern","COPY",BODY,{"derivedFrom":makeQuery(id+"F2.opPattern","COPY",BODY,{"derivedFrom":makeQuery(id+"F1.opExtrude","SWEPT_BODY",BODY,{"disambiguationData":[OSD([sQuery(id+"F0.wireOp",EDGE,"E0.bottom"),sQuery(id+"F0.wireOp",EDGE,"E0.top"),sQuery(id+"F0.wireOp",EDGE,"E0.left"),sQuery(id+"F0.wireOp",EDGE,"E0.right")])]}),"instanceName":"1"}),"instanceName":"1"});
            var Q312;
            Q312=makeQuery(id+"F45.opPattern","COPY",BODY,{"derivedFrom":makeQuery(id+"F40.opPattern","COPY",BODY,{"derivedFrom":makeQuery(id+"F23.opPattern","COPY",BODY,{"derivedFrom":makeQuery(id+"F19.opPattern","COPY",BODY,{"derivedFrom":makeQuery(id+"F17.opPattern","COPY",BODY,{"derivedFrom":makeQuery(id+"F5.opPattern","COPY",BODY,{"derivedFrom":makeQuery(id+"F4.opPattern","COPY",BODY,{"derivedFrom":makeQuery(id+"F1.opExtrude","SWEPT_BODY",BODY,{"disambiguationData":[OSD([sQuery(id+"F0.wireOp",EDGE,"E0.bottom"),sQuery(id+"F0.wireOp",EDGE,"E0.top"),sQuery(id+"F0.wireOp",EDGE,"E0.left"),sQuery(id+"F0.wireOp",EDGE,"E0.right")])]}),"instanceName":"1"}),"instanceName":"1"}),"instanceName":"1"}),"instanceName":"1"}),"instanceName":"1"}),"instanceName":"1"}),"instanceName":"1"});
            var Q313;
            Q313=makeQuery(id+"F35.opPattern","COPY",BODY,{"derivedFrom":makeQuery(id+"F34.opPattern","COPY",BODY,{"derivedFrom":makeQuery(id+"F31.opPattern","COPY",BODY,{"derivedFrom":makeQuery(id+"F1.opExtrude","SWEPT_BODY",BODY,{"disambiguationData":[OSD([sQuery(id+"F0.wireOp",EDGE,"E0.bottom"),sQuery(id+"F0.wireOp",EDGE,"E0.top"),sQuery(id+"F0.wireOp",EDGE,"E0.left"),sQuery(id+"F0.wireOp",EDGE,"E0.right")])]}),"instanceName":"1"}),"instanceName":"1"}),"instanceName":"1"});
            var Q314;
            Q314=makeQuery(id+"F37.opPattern","COPY",BODY,{"derivedFrom":makeQuery(id+"F36.opPattern","COPY",BODY,{"derivedFrom":makeQuery(id+"F35.opPattern","COPY",BODY,{"derivedFrom":makeQuery(id+"F34.opPattern","COPY",BODY,{"derivedFrom":makeQuery(id+"F31.opPattern","COPY",BODY,{"derivedFrom":makeQuery(id+"F5.opPattern","COPY",BODY,{"derivedFrom":makeQuery(id+"F1.opExtrude","SWEPT_BODY",BODY,{"disambiguationData":[OSD([sQuery(id+"F0.wireOp",EDGE,"E0.bottom"),sQuery(id+"F0.wireOp",EDGE,"E0.top"),sQuery(id+"F0.wireOp",EDGE,"E0.left"),sQuery(id+"F0.wireOp",EDGE,"E0.right")])]}),"instanceName":"1"}),"instanceName":"1"}),"instanceName":"1"}),"instanceName":"1"}),"instanceName":"1"}),"instanceName":"1"});
            var Q315;
            Q315=makeQuery(id+"F19.opPattern","COPY",BODY,{"derivedFrom":makeQuery(id+"F17.opPattern","COPY",BODY,{"derivedFrom":makeQuery(id+"F12.opPattern","COPY",BODY,{"derivedFrom":makeQuery(id+"F6.opPattern","COPY",BODY,{"derivedFrom":makeQuery(id+"F5.opPattern","COPY",BODY,{"derivedFrom":makeQuery(id+"F4.opPattern","COPY",BODY,{"derivedFrom":makeQuery(id+"F2.opPattern","COPY",BODY,{"derivedFrom":makeQuery(id+"F1.opExtrude","SWEPT_BODY",BODY,{"disambiguationData":[OSD([sQuery(id+"F0.wireOp",EDGE,"E0.bottom"),sQuery(id+"F0.wireOp",EDGE,"E0.top"),sQuery(id+"F0.wireOp",EDGE,"E0.left"),sQuery(id+"F0.wireOp",EDGE,"E0.right")])]}),"instanceName":"1"}),"instanceName":"1"}),"instanceName":"1"}),"instanceName":"1"}),"instanceName":"1"}),"instanceName":"1"}),"instanceName":"1"});
            var Q316;
            Q316=makeQuery(id+"F40.opPattern","COPY",BODY,{"derivedFrom":makeQuery(id+"F26.opPattern","COPY",BODY,{"derivedFrom":makeQuery(id+"F18.opPattern","COPY",BODY,{"derivedFrom":makeQuery(id+"F17.opPattern","COPY",BODY,{"derivedFrom":makeQuery(id+"F8.opPattern","COPY",BODY,{"derivedFrom":makeQuery(id+"F5.opPattern","COPY",BODY,{"derivedFrom":makeQuery(id+"F4.opPattern","COPY",BODY,{"derivedFrom":makeQuery(id+"F2.opPattern","COPY",BODY,{"derivedFrom":makeQuery(id+"F1.opExtrude","SWEPT_BODY",BODY,{"disambiguationData":[OSD([sQuery(id+"F0.wireOp",EDGE,"E0.bottom"),sQuery(id+"F0.wireOp",EDGE,"E0.top"),sQuery(id+"F0.wireOp",EDGE,"E0.left"),sQuery(id+"F0.wireOp",EDGE,"E0.right")])]}),"instanceName":"1"}),"instanceName":"1"}),"instanceName":"1"}),"instanceName":"1"}),"instanceName":"1"}),"instanceName":"1"}),"instanceName":"1"}),"instanceName":"1"});
            var Q317;
            Q317=makeQuery(id+"F28.opPattern","COPY",BODY,{"derivedFrom":makeQuery(id+"F19.opPattern","COPY",BODY,{"derivedFrom":makeQuery(id+"F13.opPattern","COPY",BODY,{"derivedFrom":makeQuery(id+"F5.opPattern","COPY",BODY,{"derivedFrom":makeQuery(id+"F4.opPattern","COPY",BODY,{"derivedFrom":makeQuery(id+"F1.opExtrude","SWEPT_BODY",BODY,{"disambiguationData":[OSD([sQuery(id+"F0.wireOp",EDGE,"E0.bottom"),sQuery(id+"F0.wireOp",EDGE,"E0.top"),sQuery(id+"F0.wireOp",EDGE,"E0.left"),sQuery(id+"F0.wireOp",EDGE,"E0.right")])]}),"instanceName":"1"}),"instanceName":"1"}),"instanceName":"1"}),"instanceName":"1"}),"instanceName":"1"});
            var Q318;
            Q318=makeQuery(id+"F40.opPattern","COPY",BODY,{"derivedFrom":makeQuery(id+"F26.opPattern","COPY",BODY,{"derivedFrom":makeQuery(id+"F17.opPattern","COPY",BODY,{"derivedFrom":makeQuery(id+"F8.opPattern","COPY",BODY,{"derivedFrom":makeQuery(id+"F5.opPattern","COPY",BODY,{"derivedFrom":makeQuery(id+"F4.opPattern","COPY",BODY,{"derivedFrom":makeQuery(id+"F1.opExtrude","SWEPT_BODY",BODY,{"disambiguationData":[OSD([sQuery(id+"F0.wireOp",EDGE,"E0.bottom"),sQuery(id+"F0.wireOp",EDGE,"E0.top"),sQuery(id+"F0.wireOp",EDGE,"E0.left"),sQuery(id+"F0.wireOp",EDGE,"E0.right")])]}),"instanceName":"1"}),"instanceName":"1"}),"instanceName":"1"}),"instanceName":"1"}),"instanceName":"1"}),"instanceName":"1"});
            var Q319;
            Q319=makeQuery(id+"F29.opPattern","COPY",BODY,{"derivedFrom":makeQuery(id+"F28.opPattern","COPY",BODY,{"derivedFrom":makeQuery(id+"F19.opPattern","COPY",BODY,{"derivedFrom":makeQuery(id+"F17.opPattern","COPY",BODY,{"derivedFrom":makeQuery(id+"F15.opPattern","COPY",BODY,{"derivedFrom":makeQuery(id+"F12.opPattern","COPY",BODY,{"derivedFrom":makeQuery(id+"F6.opPattern","COPY",BODY,{"derivedFrom":makeQuery(id+"F5.opPattern","COPY",BODY,{"derivedFrom":makeQuery(id+"F4.opPattern","COPY",BODY,{"derivedFrom":makeQuery(id+"F2.opPattern","COPY",BODY,{"derivedFrom":makeQuery(id+"F1.opExtrude","SWEPT_BODY",BODY,{"disambiguationData":[OSD([sQuery(id+"F0.wireOp",EDGE,"E0.bottom"),sQuery(id+"F0.wireOp",EDGE,"E0.top"),sQuery(id+"F0.wireOp",EDGE,"E0.left"),sQuery(id+"F0.wireOp",EDGE,"E0.right")])]}),"instanceName":"1"}),"instanceName":"1"}),"instanceName":"1"}),"instanceName":"1"}),"instanceName":"1"}),"instanceName":"1"}),"instanceName":"1"}),"instanceName":"1"}),"instanceName":"1"}),"instanceName":"1"});
            var Q320;
            Q320=makeQuery(id+"F45.opPattern","COPY",BODY,{"derivedFrom":makeQuery(id+"F40.opPattern","COPY",BODY,{"derivedFrom":makeQuery(id+"F28.opPattern","COPY",BODY,{"derivedFrom":makeQuery(id+"F19.opPattern","COPY",BODY,{"derivedFrom":makeQuery(id+"F15.opPattern","COPY",BODY,{"derivedFrom":makeQuery(id+"F12.opPattern","COPY",BODY,{"derivedFrom":makeQuery(id+"F6.opPattern","COPY",BODY,{"derivedFrom":makeQuery(id+"F5.opPattern","COPY",BODY,{"derivedFrom":makeQuery(id+"F4.opPattern","COPY",BODY,{"derivedFrom":makeQuery(id+"F2.opPattern","COPY",BODY,{"derivedFrom":makeQuery(id+"F1.opExtrude","SWEPT_BODY",BODY,{"disambiguationData":[OSD([sQuery(id+"F0.wireOp",EDGE,"E0.bottom"),sQuery(id+"F0.wireOp",EDGE,"E0.top"),sQuery(id+"F0.wireOp",EDGE,"E0.left"),sQuery(id+"F0.wireOp",EDGE,"E0.right")])]}),"instanceName":"1"}),"instanceName":"1"}),"instanceName":"1"}),"instanceName":"1"}),"instanceName":"1"}),"instanceName":"1"}),"instanceName":"1"}),"instanceName":"1"}),"instanceName":"1"}),"instanceName":"1"});
            var Q321;
            Q321=makeQuery(id+"F35.opPattern","COPY",BODY,{"derivedFrom":makeQuery(id+"F31.opPattern","COPY",BODY,{"derivedFrom":makeQuery(id+"F1.opExtrude","SWEPT_BODY",BODY,{"disambiguationData":[OSD([sQuery(id+"F0.wireOp",EDGE,"E0.bottom"),sQuery(id+"F0.wireOp",EDGE,"E0.top"),sQuery(id+"F0.wireOp",EDGE,"E0.left"),sQuery(id+"F0.wireOp",EDGE,"E0.right")])]}),"instanceName":"1"}),"instanceName":"1"});
            var Q322;
            Q322=makeQuery(id+"F21.opPattern","COPY",BODY,{"derivedFrom":makeQuery(id+"F19.opPattern","COPY",BODY,{"derivedFrom":makeQuery(id+"F17.opPattern","COPY",BODY,{"derivedFrom":makeQuery(id+"F12.opPattern","COPY",BODY,{"derivedFrom":makeQuery(id+"F6.opPattern","COPY",BODY,{"derivedFrom":makeQuery(id+"F5.opPattern","COPY",BODY,{"derivedFrom":makeQuery(id+"F4.opPattern","COPY",BODY,{"derivedFrom":makeQuery(id+"F2.opPattern","COPY",BODY,{"derivedFrom":makeQuery(id+"F1.opExtrude","SWEPT_BODY",BODY,{"disambiguationData":[OSD([sQuery(id+"F0.wireOp",EDGE,"E0.bottom"),sQuery(id+"F0.wireOp",EDGE,"E0.top"),sQuery(id+"F0.wireOp",EDGE,"E0.left"),sQuery(id+"F0.wireOp",EDGE,"E0.right")])]}),"instanceName":"1"}),"instanceName":"1"}),"instanceName":"1"}),"instanceName":"1"}),"instanceName":"1"}),"instanceName":"1"}),"instanceName":"1"}),"instanceName":"1"});
            var Q323;
            Q323=makeQuery(id+"F40.opPattern","COPY",BODY,{"derivedFrom":makeQuery(id+"F21.opPattern","COPY",BODY,{"derivedFrom":makeQuery(id+"F19.opPattern","COPY",BODY,{"derivedFrom":makeQuery(id+"F12.opPattern","COPY",BODY,{"derivedFrom":makeQuery(id+"F6.opPattern","COPY",BODY,{"derivedFrom":makeQuery(id+"F5.opPattern","COPY",BODY,{"derivedFrom":makeQuery(id+"F4.opPattern","COPY",BODY,{"derivedFrom":makeQuery(id+"F2.opPattern","COPY",BODY,{"derivedFrom":makeQuery(id+"F1.opExtrude","SWEPT_BODY",BODY,{"disambiguationData":[OSD([sQuery(id+"F0.wireOp",EDGE,"E0.bottom"),sQuery(id+"F0.wireOp",EDGE,"E0.top"),sQuery(id+"F0.wireOp",EDGE,"E0.left"),sQuery(id+"F0.wireOp",EDGE,"E0.right")])]}),"instanceName":"1"}),"instanceName":"1"}),"instanceName":"1"}),"instanceName":"1"}),"instanceName":"1"}),"instanceName":"1"}),"instanceName":"1"}),"instanceName":"1"});
            var Q324;
            Q324=makeQuery(id+"F21.opPattern","COPY",BODY,{"derivedFrom":makeQuery(id+"F19.opPattern","COPY",BODY,{"derivedFrom":makeQuery(id+"F5.opPattern","COPY",BODY,{"derivedFrom":makeQuery(id+"F4.opPattern","COPY",BODY,{"derivedFrom":makeQuery(id+"F2.opPattern","COPY",BODY,{"derivedFrom":makeQuery(id+"F1.opExtrude","SWEPT_BODY",BODY,{"disambiguationData":[OSD([sQuery(id+"F0.wireOp",EDGE,"E0.bottom"),sQuery(id+"F0.wireOp",EDGE,"E0.top"),sQuery(id+"F0.wireOp",EDGE,"E0.left"),sQuery(id+"F0.wireOp",EDGE,"E0.right")])]}),"instanceName":"1"}),"instanceName":"1"}),"instanceName":"1"}),"instanceName":"1"}),"instanceName":"1"});
            var Q325;
            Q325=makeQuery(id+"F37.opPattern","COPY",BODY,{"derivedFrom":makeQuery(id+"F35.opPattern","COPY",BODY,{"derivedFrom":makeQuery(id+"F34.opPattern","COPY",BODY,{"derivedFrom":makeQuery(id+"F31.opPattern","COPY",BODY,{"derivedFrom":makeQuery(id+"F5.opPattern","COPY",BODY,{"derivedFrom":makeQuery(id+"F1.opExtrude","SWEPT_BODY",BODY,{"disambiguationData":[OSD([sQuery(id+"F0.wireOp",EDGE,"E0.bottom"),sQuery(id+"F0.wireOp",EDGE,"E0.top"),sQuery(id+"F0.wireOp",EDGE,"E0.left"),sQuery(id+"F0.wireOp",EDGE,"E0.right")])]}),"instanceName":"1"}),"instanceName":"1"}),"instanceName":"1"}),"instanceName":"1"}),"instanceName":"1"});
            var Q326;
            Q326=makeQuery(id+"F40.opPattern","COPY",BODY,{"derivedFrom":makeQuery(id+"F28.opPattern","COPY",BODY,{"derivedFrom":makeQuery(id+"F19.opPattern","COPY",BODY,{"derivedFrom":makeQuery(id+"F15.opPattern","COPY",BODY,{"derivedFrom":makeQuery(id+"F12.opPattern","COPY",BODY,{"derivedFrom":makeQuery(id+"F6.opPattern","COPY",BODY,{"derivedFrom":makeQuery(id+"F5.opPattern","COPY",BODY,{"derivedFrom":makeQuery(id+"F4.opPattern","COPY",BODY,{"derivedFrom":makeQuery(id+"F2.opPattern","COPY",BODY,{"derivedFrom":makeQuery(id+"F1.opExtrude","SWEPT_BODY",BODY,{"disambiguationData":[OSD([sQuery(id+"F0.wireOp",EDGE,"E0.bottom"),sQuery(id+"F0.wireOp",EDGE,"E0.top"),sQuery(id+"F0.wireOp",EDGE,"E0.left"),sQuery(id+"F0.wireOp",EDGE,"E0.right")])]}),"instanceName":"1"}),"instanceName":"1"}),"instanceName":"1"}),"instanceName":"1"}),"instanceName":"1"}),"instanceName":"1"}),"instanceName":"1"}),"instanceName":"1"}),"instanceName":"1"});
            var Q327;
            Q327=makeQuery(id+"F29.opPattern","COPY",BODY,{"derivedFrom":makeQuery(id+"F26.opPattern","COPY",BODY,{"derivedFrom":makeQuery(id+"F19.opPattern","COPY",BODY,{"derivedFrom":makeQuery(id+"F17.opPattern","COPY",BODY,{"derivedFrom":makeQuery(id+"F15.opPattern","COPY",BODY,{"derivedFrom":makeQuery(id+"F12.opPattern","COPY",BODY,{"derivedFrom":makeQuery(id+"F6.opPattern","COPY",BODY,{"derivedFrom":makeQuery(id+"F5.opPattern","COPY",BODY,{"derivedFrom":makeQuery(id+"F4.opPattern","COPY",BODY,{"derivedFrom":makeQuery(id+"F2.opPattern","COPY",BODY,{"derivedFrom":makeQuery(id+"F1.opExtrude","SWEPT_BODY",BODY,{"disambiguationData":[OSD([sQuery(id+"F0.wireOp",EDGE,"E0.bottom"),sQuery(id+"F0.wireOp",EDGE,"E0.top"),sQuery(id+"F0.wireOp",EDGE,"E0.left"),sQuery(id+"F0.wireOp",EDGE,"E0.right")])]}),"instanceName":"1"}),"instanceName":"1"}),"instanceName":"1"}),"instanceName":"1"}),"instanceName":"1"}),"instanceName":"1"}),"instanceName":"1"}),"instanceName":"1"}),"instanceName":"1"}),"instanceName":"1"});
            var Q328;
            Q328=makeQuery(id+"F21.opPattern","COPY",BODY,{"derivedFrom":makeQuery(id+"F19.opPattern","COPY",BODY,{"derivedFrom":makeQuery(id+"F12.opPattern","COPY",BODY,{"derivedFrom":makeQuery(id+"F6.opPattern","COPY",BODY,{"derivedFrom":makeQuery(id+"F5.opPattern","COPY",BODY,{"derivedFrom":makeQuery(id+"F4.opPattern","COPY",BODY,{"derivedFrom":makeQuery(id+"F2.opPattern","COPY",BODY,{"derivedFrom":makeQuery(id+"F1.opExtrude","SWEPT_BODY",BODY,{"disambiguationData":[OSD([sQuery(id+"F0.wireOp",EDGE,"E0.bottom"),sQuery(id+"F0.wireOp",EDGE,"E0.top"),sQuery(id+"F0.wireOp",EDGE,"E0.left"),sQuery(id+"F0.wireOp",EDGE,"E0.right")])]}),"instanceName":"1"}),"instanceName":"1"}),"instanceName":"1"}),"instanceName":"1"}),"instanceName":"1"}),"instanceName":"1"}),"instanceName":"1"});
            var Q329;
            Q329=makeQuery(id+"F40.opPattern","COPY",BODY,{"derivedFrom":makeQuery(id+"F21.opPattern","COPY",BODY,{"derivedFrom":makeQuery(id+"F19.opPattern","COPY",BODY,{"derivedFrom":makeQuery(id+"F17.opPattern","COPY",BODY,{"derivedFrom":makeQuery(id+"F12.opPattern","COPY",BODY,{"derivedFrom":makeQuery(id+"F6.opPattern","COPY",BODY,{"derivedFrom":makeQuery(id+"F5.opPattern","COPY",BODY,{"derivedFrom":makeQuery(id+"F4.opPattern","COPY",BODY,{"derivedFrom":makeQuery(id+"F2.opPattern","COPY",BODY,{"derivedFrom":makeQuery(id+"F1.opExtrude","SWEPT_BODY",BODY,{"disambiguationData":[OSD([sQuery(id+"F0.wireOp",EDGE,"E0.bottom"),sQuery(id+"F0.wireOp",EDGE,"E0.top"),sQuery(id+"F0.wireOp",EDGE,"E0.left"),sQuery(id+"F0.wireOp",EDGE,"E0.right")])]}),"instanceName":"1"}),"instanceName":"1"}),"instanceName":"1"}),"instanceName":"1"}),"instanceName":"1"}),"instanceName":"1"}),"instanceName":"1"}),"instanceName":"1"}),"instanceName":"1"});
            var Q330;
            Q330=makeQuery(id+"F30.opPattern","COPY",BODY,{"derivedFrom":makeQuery(id+"F29.opPattern","COPY",BODY,{"derivedFrom":makeQuery(id+"F23.opPattern","COPY",BODY,{"derivedFrom":makeQuery(id+"F19.opPattern","COPY",BODY,{"derivedFrom":makeQuery(id+"F15.opPattern","COPY",BODY,{"derivedFrom":makeQuery(id+"F12.opPattern","COPY",BODY,{"derivedFrom":makeQuery(id+"F6.opPattern","COPY",BODY,{"derivedFrom":makeQuery(id+"F5.opPattern","COPY",BODY,{"derivedFrom":makeQuery(id+"F4.opPattern","COPY",BODY,{"derivedFrom":makeQuery(id+"F2.opPattern","COPY",BODY,{"derivedFrom":makeQuery(id+"F1.opExtrude","SWEPT_BODY",BODY,{"disambiguationData":[OSD([sQuery(id+"F0.wireOp",EDGE,"E0.bottom"),sQuery(id+"F0.wireOp",EDGE,"E0.top"),sQuery(id+"F0.wireOp",EDGE,"E0.left"),sQuery(id+"F0.wireOp",EDGE,"E0.right")])]}),"instanceName":"1"}),"instanceName":"1"}),"instanceName":"1"}),"instanceName":"1"}),"instanceName":"1"}),"instanceName":"1"}),"instanceName":"1"}),"instanceName":"1"}),"instanceName":"1"}),"instanceName":"1"});
            var Q331;
            Q331=makeQuery(id+"F40.opPattern","COPY",BODY,{"derivedFrom":makeQuery(id+"F28.opPattern","COPY",BODY,{"derivedFrom":makeQuery(id+"F26.opPattern","COPY",BODY,{"derivedFrom":makeQuery(id+"F17.opPattern","COPY",BODY,{"derivedFrom":makeQuery(id+"F15.opPattern","COPY",BODY,{"derivedFrom":makeQuery(id+"F12.opPattern","COPY",BODY,{"derivedFrom":makeQuery(id+"F6.opPattern","COPY",BODY,{"derivedFrom":makeQuery(id+"F5.opPattern","COPY",BODY,{"derivedFrom":makeQuery(id+"F4.opPattern","COPY",BODY,{"derivedFrom":makeQuery(id+"F2.opPattern","COPY",BODY,{"derivedFrom":makeQuery(id+"F1.opExtrude","SWEPT_BODY",BODY,{"disambiguationData":[OSD([sQuery(id+"F0.wireOp",EDGE,"E0.bottom"),sQuery(id+"F0.wireOp",EDGE,"E0.top"),sQuery(id+"F0.wireOp",EDGE,"E0.left"),sQuery(id+"F0.wireOp",EDGE,"E0.right")])]}),"instanceName":"1"}),"instanceName":"1"}),"instanceName":"1"}),"instanceName":"1"}),"instanceName":"1"}),"instanceName":"1"}),"instanceName":"1"}),"instanceName":"1"}),"instanceName":"1"}),"instanceName":"1"});
            var Q332;
            Q332=makeQuery(id+"F28.opPattern","COPY",BODY,{"derivedFrom":makeQuery(id+"F19.opPattern","COPY",BODY,{"derivedFrom":makeQuery(id+"F17.opPattern","COPY",BODY,{"derivedFrom":makeQuery(id+"F13.opPattern","COPY",BODY,{"derivedFrom":makeQuery(id+"F5.opPattern","COPY",BODY,{"derivedFrom":makeQuery(id+"F4.opPattern","COPY",BODY,{"derivedFrom":makeQuery(id+"F1.opExtrude","SWEPT_BODY",BODY,{"disambiguationData":[OSD([sQuery(id+"F0.wireOp",EDGE,"E0.bottom"),sQuery(id+"F0.wireOp",EDGE,"E0.top"),sQuery(id+"F0.wireOp",EDGE,"E0.left"),sQuery(id+"F0.wireOp",EDGE,"E0.right")])]}),"instanceName":"1"}),"instanceName":"1"}),"instanceName":"1"}),"instanceName":"1"}),"instanceName":"1"}),"instanceName":"1"});
            var Q333;
            Q333=makeQuery(id+"F37.opPattern","COPY",BODY,{"derivedFrom":makeQuery(id+"F36.opPattern","COPY",BODY,{"derivedFrom":makeQuery(id+"F35.opPattern","COPY",BODY,{"derivedFrom":makeQuery(id+"F31.opPattern","COPY",BODY,{"derivedFrom":makeQuery(id+"F5.opPattern","COPY",BODY,{"derivedFrom":makeQuery(id+"F1.opExtrude","SWEPT_BODY",BODY,{"disambiguationData":[OSD([sQuery(id+"F0.wireOp",EDGE,"E0.bottom"),sQuery(id+"F0.wireOp",EDGE,"E0.top"),sQuery(id+"F0.wireOp",EDGE,"E0.left"),sQuery(id+"F0.wireOp",EDGE,"E0.right")])]}),"instanceName":"1"}),"instanceName":"1"}),"instanceName":"1"}),"instanceName":"1"}),"instanceName":"1"});
            var Q334;
            Q334=makeQuery(id+"F40.opPattern","COPY",BODY,{"derivedFrom":makeQuery(id+"F26.opPattern","COPY",BODY,{"derivedFrom":makeQuery(id+"F19.opPattern","COPY",BODY,{"derivedFrom":makeQuery(id+"F6.opPattern","COPY",BODY,{"derivedFrom":makeQuery(id+"F5.opPattern","COPY",BODY,{"derivedFrom":makeQuery(id+"F4.opPattern","COPY",BODY,{"derivedFrom":makeQuery(id+"F1.opExtrude","SWEPT_BODY",BODY,{"disambiguationData":[OSD([sQuery(id+"F0.wireOp",EDGE,"E0.bottom"),sQuery(id+"F0.wireOp",EDGE,"E0.top"),sQuery(id+"F0.wireOp",EDGE,"E0.left"),sQuery(id+"F0.wireOp",EDGE,"E0.right")])]}),"instanceName":"1"}),"instanceName":"1"}),"instanceName":"1"}),"instanceName":"1"}),"instanceName":"1"}),"instanceName":"1"});
            var Q335;
            Q335=makeQuery(id+"F21.opPattern","COPY",BODY,{"derivedFrom":makeQuery(id+"F19.opPattern","COPY",BODY,{"derivedFrom":makeQuery(id+"F6.opPattern","COPY",BODY,{"derivedFrom":makeQuery(id+"F5.opPattern","COPY",BODY,{"derivedFrom":makeQuery(id+"F4.opPattern","COPY",BODY,{"derivedFrom":makeQuery(id+"F2.opPattern","COPY",BODY,{"derivedFrom":makeQuery(id+"F1.opExtrude","SWEPT_BODY",BODY,{"disambiguationData":[OSD([sQuery(id+"F0.wireOp",EDGE,"E0.bottom"),sQuery(id+"F0.wireOp",EDGE,"E0.top"),sQuery(id+"F0.wireOp",EDGE,"E0.left"),sQuery(id+"F0.wireOp",EDGE,"E0.right")])]}),"instanceName":"1"}),"instanceName":"1"}),"instanceName":"1"}),"instanceName":"1"}),"instanceName":"1"}),"instanceName":"1"});
            var Q336;
            Q336=makeQuery(id+"F40.opPattern","COPY",BODY,{"derivedFrom":makeQuery(id+"F23.opPattern","COPY",BODY,{"derivedFrom":makeQuery(id+"F21.opPattern","COPY",BODY,{"derivedFrom":makeQuery(id+"F19.opPattern","COPY",BODY,{"derivedFrom":makeQuery(id+"F17.opPattern","COPY",BODY,{"derivedFrom":makeQuery(id+"F6.opPattern","COPY",BODY,{"derivedFrom":makeQuery(id+"F5.opPattern","COPY",BODY,{"derivedFrom":makeQuery(id+"F4.opPattern","COPY",BODY,{"derivedFrom":makeQuery(id+"F2.opPattern","COPY",BODY,{"derivedFrom":makeQuery(id+"F1.opExtrude","SWEPT_BODY",BODY,{"disambiguationData":[OSD([sQuery(id+"F0.wireOp",EDGE,"E0.bottom"),sQuery(id+"F0.wireOp",EDGE,"E0.top"),sQuery(id+"F0.wireOp",EDGE,"E0.left"),sQuery(id+"F0.wireOp",EDGE,"E0.right")])]}),"instanceName":"1"}),"instanceName":"1"}),"instanceName":"1"}),"instanceName":"1"}),"instanceName":"1"}),"instanceName":"1"}),"instanceName":"1"}),"instanceName":"1"}),"instanceName":"1"});
            var Q337;
            Q337=makeQuery(id+"F38.opPattern","COPY",BODY,{"derivedFrom":makeQuery(id+"F37.opPattern","COPY",BODY,{"derivedFrom":makeQuery(id+"F35.opPattern","COPY",BODY,{"derivedFrom":makeQuery(id+"F31.opPattern","COPY",BODY,{"derivedFrom":makeQuery(id+"F4.opPattern","COPY",BODY,{"derivedFrom":makeQuery(id+"F2.opPattern","COPY",BODY,{"derivedFrom":makeQuery(id+"F1.opExtrude","SWEPT_BODY",BODY,{"disambiguationData":[OSD([sQuery(id+"F0.wireOp",EDGE,"E0.bottom"),sQuery(id+"F0.wireOp",EDGE,"E0.top"),sQuery(id+"F0.wireOp",EDGE,"E0.left"),sQuery(id+"F0.wireOp",EDGE,"E0.right")])]}),"instanceName":"1"}),"instanceName":"1"}),"instanceName":"1"}),"instanceName":"1"}),"instanceName":"1"}),"instanceName":"1"});
            var Q338;
            Q338=makeQuery(id+"F12.opPattern","COPY",BODY,{"derivedFrom":makeQuery(id+"F6.opPattern","COPY",BODY,{"derivedFrom":makeQuery(id+"F5.opPattern","COPY",BODY,{"derivedFrom":makeQuery(id+"F2.opPattern","COPY",BODY,{"derivedFrom":makeQuery(id+"F1.opExtrude","SWEPT_BODY",BODY,{"disambiguationData":[OSD([sQuery(id+"F0.wireOp",EDGE,"E0.bottom"),sQuery(id+"F0.wireOp",EDGE,"E0.top"),sQuery(id+"F0.wireOp",EDGE,"E0.left"),sQuery(id+"F0.wireOp",EDGE,"E0.right")])]}),"instanceName":"1"}),"instanceName":"1"}),"instanceName":"1"}),"instanceName":"1"});
            var Q339;
            Q339=makeQuery(id+"F40.opPattern","COPY",BODY,{"derivedFrom":makeQuery(id+"F23.opPattern","COPY",BODY,{"derivedFrom":makeQuery(id+"F19.opPattern","COPY",BODY,{"derivedFrom":makeQuery(id+"F17.opPattern","COPY",BODY,{"derivedFrom":makeQuery(id+"F5.opPattern","COPY",BODY,{"derivedFrom":makeQuery(id+"F4.opPattern","COPY",BODY,{"derivedFrom":makeQuery(id+"F2.opPattern","COPY",BODY,{"derivedFrom":makeQuery(id+"F1.opExtrude","SWEPT_BODY",BODY,{"disambiguationData":[OSD([sQuery(id+"F0.wireOp",EDGE,"E0.bottom"),sQuery(id+"F0.wireOp",EDGE,"E0.top"),sQuery(id+"F0.wireOp",EDGE,"E0.left"),sQuery(id+"F0.wireOp",EDGE,"E0.right")])]}),"instanceName":"1"}),"instanceName":"1"}),"instanceName":"1"}),"instanceName":"1"}),"instanceName":"1"}),"instanceName":"1"}),"instanceName":"1"});
            var Q340;
            Q340=makeQuery(id+"F26.opPattern","COPY",BODY,{"derivedFrom":makeQuery(id+"F19.opPattern","COPY",BODY,{"derivedFrom":makeQuery(id+"F6.opPattern","COPY",BODY,{"derivedFrom":makeQuery(id+"F5.opPattern","COPY",BODY,{"derivedFrom":makeQuery(id+"F4.opPattern","COPY",BODY,{"derivedFrom":makeQuery(id+"F2.opPattern","COPY",BODY,{"derivedFrom":makeQuery(id+"F1.opExtrude","SWEPT_BODY",BODY,{"disambiguationData":[OSD([sQuery(id+"F0.wireOp",EDGE,"E0.bottom"),sQuery(id+"F0.wireOp",EDGE,"E0.top"),sQuery(id+"F0.wireOp",EDGE,"E0.left"),sQuery(id+"F0.wireOp",EDGE,"E0.right")])]}),"instanceName":"1"}),"instanceName":"1"}),"instanceName":"1"}),"instanceName":"1"}),"instanceName":"1"}),"instanceName":"1"});
            var Q341;
            Q341=makeQuery(id+"F26.opPattern","COPY",BODY,{"derivedFrom":makeQuery(id+"F17.opPattern","COPY",BODY,{"derivedFrom":makeQuery(id+"F12.opPattern","COPY",BODY,{"derivedFrom":makeQuery(id+"F6.opPattern","COPY",BODY,{"derivedFrom":makeQuery(id+"F5.opPattern","COPY",BODY,{"derivedFrom":makeQuery(id+"F4.opPattern","COPY",BODY,{"derivedFrom":makeQuery(id+"F2.opPattern","COPY",BODY,{"derivedFrom":makeQuery(id+"F1.opExtrude","SWEPT_BODY",BODY,{"disambiguationData":[OSD([sQuery(id+"F0.wireOp",EDGE,"E0.bottom"),sQuery(id+"F0.wireOp",EDGE,"E0.top"),sQuery(id+"F0.wireOp",EDGE,"E0.left"),sQuery(id+"F0.wireOp",EDGE,"E0.right")])]}),"instanceName":"1"}),"instanceName":"1"}),"instanceName":"1"}),"instanceName":"1"}),"instanceName":"1"}),"instanceName":"1"}),"instanceName":"1"});
            var Q342;
            Q342=makeQuery(id+"F20.opPattern","COPY",BODY,{"derivedFrom":makeQuery(id+"F17.opPattern","COPY",BODY,{"derivedFrom":makeQuery(id+"F8.opPattern","COPY",BODY,{"derivedFrom":makeQuery(id+"F5.opPattern","COPY",BODY,{"derivedFrom":makeQuery(id+"F4.opPattern","COPY",BODY,{"derivedFrom":makeQuery(id+"F1.opExtrude","SWEPT_BODY",BODY,{"disambiguationData":[OSD([sQuery(id+"F0.wireOp",EDGE,"E0.bottom"),sQuery(id+"F0.wireOp",EDGE,"E0.top"),sQuery(id+"F0.wireOp",EDGE,"E0.left"),sQuery(id+"F0.wireOp",EDGE,"E0.right")])]}),"instanceName":"1"}),"instanceName":"1"}),"instanceName":"1"}),"instanceName":"1"}),"instanceName":"1"});
            var Q343;
            Q343=makeQuery(id+"F17.opPattern","COPY",BODY,{"derivedFrom":makeQuery(id+"F8.opPattern","COPY",BODY,{"derivedFrom":makeQuery(id+"F5.opPattern","COPY",BODY,{"derivedFrom":makeQuery(id+"F4.opPattern","COPY",BODY,{"derivedFrom":makeQuery(id+"F2.opPattern","COPY",BODY,{"derivedFrom":makeQuery(id+"F1.opExtrude","SWEPT_BODY",BODY,{"disambiguationData":[OSD([sQuery(id+"F0.wireOp",EDGE,"E0.bottom"),sQuery(id+"F0.wireOp",EDGE,"E0.top"),sQuery(id+"F0.wireOp",EDGE,"E0.left"),sQuery(id+"F0.wireOp",EDGE,"E0.right")])]}),"instanceName":"1"}),"instanceName":"1"}),"instanceName":"1"}),"instanceName":"1"}),"instanceName":"1"});
            var Q344;
            Q344=makeQuery(id+"F39.opPattern","COPY",BODY,{"derivedFrom":makeQuery(id+"F26.opPattern","COPY",BODY,{"derivedFrom":makeQuery(id+"F17.opPattern","COPY",BODY,{"derivedFrom":makeQuery(id+"F12.opPattern","COPY",BODY,{"derivedFrom":makeQuery(id+"F6.opPattern","COPY",BODY,{"derivedFrom":makeQuery(id+"F5.opPattern","COPY",BODY,{"derivedFrom":makeQuery(id+"F4.opPattern","COPY",BODY,{"derivedFrom":makeQuery(id+"F1.opExtrude","SWEPT_BODY",BODY,{"disambiguationData":[OSD([sQuery(id+"F0.wireOp",EDGE,"E0.bottom"),sQuery(id+"F0.wireOp",EDGE,"E0.top"),sQuery(id+"F0.wireOp",EDGE,"E0.left"),sQuery(id+"F0.wireOp",EDGE,"E0.right")])]}),"instanceName":"1"}),"instanceName":"1"}),"instanceName":"1"}),"instanceName":"1"}),"instanceName":"1"}),"instanceName":"1"}),"instanceName":"1"});
            var Q345;
            Q345=makeQuery(id+"F26.opPattern","COPY",BODY,{"derivedFrom":makeQuery(id+"F19.opPattern","COPY",BODY,{"derivedFrom":makeQuery(id+"F5.opPattern","COPY",BODY,{"derivedFrom":makeQuery(id+"F4.opPattern","COPY",BODY,{"derivedFrom":makeQuery(id+"F1.opExtrude","SWEPT_BODY",BODY,{"disambiguationData":[OSD([sQuery(id+"F0.wireOp",EDGE,"E0.bottom"),sQuery(id+"F0.wireOp",EDGE,"E0.top"),sQuery(id+"F0.wireOp",EDGE,"E0.left"),sQuery(id+"F0.wireOp",EDGE,"E0.right")])]}),"instanceName":"1"}),"instanceName":"1"}),"instanceName":"1"}),"instanceName":"1"});
            var Q346;
            Q346=makeQuery(id+"F45.opPattern","COPY",BODY,{"derivedFrom":makeQuery(id+"F40.opPattern","COPY",BODY,{"derivedFrom":makeQuery(id+"F23.opPattern","COPY",BODY,{"derivedFrom":makeQuery(id+"F19.opPattern","COPY",BODY,{"derivedFrom":makeQuery(id+"F5.opPattern","COPY",BODY,{"derivedFrom":makeQuery(id+"F4.opPattern","COPY",BODY,{"derivedFrom":makeQuery(id+"F2.opPattern","COPY",BODY,{"derivedFrom":makeQuery(id+"F1.opExtrude","SWEPT_BODY",BODY,{"disambiguationData":[OSD([sQuery(id+"F0.wireOp",EDGE,"E0.bottom"),sQuery(id+"F0.wireOp",EDGE,"E0.top"),sQuery(id+"F0.wireOp",EDGE,"E0.left"),sQuery(id+"F0.wireOp",EDGE,"E0.right")])]}),"instanceName":"1"}),"instanceName":"1"}),"instanceName":"1"}),"instanceName":"1"}),"instanceName":"1"}),"instanceName":"1"}),"instanceName":"1"});
            var Q347;
            Q347=makeQuery(id+"F21.opPattern","COPY",BODY,{"derivedFrom":makeQuery(id+"F19.opPattern","COPY",BODY,{"derivedFrom":makeQuery(id+"F6.opPattern","COPY",BODY,{"derivedFrom":makeQuery(id+"F5.opPattern","COPY",BODY,{"derivedFrom":makeQuery(id+"F4.opPattern","COPY",BODY,{"derivedFrom":makeQuery(id+"F1.opExtrude","SWEPT_BODY",BODY,{"disambiguationData":[OSD([sQuery(id+"F0.wireOp",EDGE,"E0.bottom"),sQuery(id+"F0.wireOp",EDGE,"E0.top"),sQuery(id+"F0.wireOp",EDGE,"E0.left"),sQuery(id+"F0.wireOp",EDGE,"E0.right")])]}),"instanceName":"1"}),"instanceName":"1"}),"instanceName":"1"}),"instanceName":"1"}),"instanceName":"1"});
            var Q348;
            Q348=makeQuery(id+"F8.opPattern","COPY",BODY,{"derivedFrom":makeQuery(id+"F5.opPattern","COPY",BODY,{"derivedFrom":makeQuery(id+"F1.opExtrude","SWEPT_BODY",BODY,{"disambiguationData":[OSD([sQuery(id+"F0.wireOp",EDGE,"E0.bottom"),sQuery(id+"F0.wireOp",EDGE,"E0.top"),sQuery(id+"F0.wireOp",EDGE,"E0.left"),sQuery(id+"F0.wireOp",EDGE,"E0.right")])]}),"instanceName":"1"}),"instanceName":"1"});
            var Q349;
            Q349=makeQuery(id+"F39.opPattern","COPY",BODY,{"derivedFrom":makeQuery(id+"F28.opPattern","COPY",BODY,{"derivedFrom":makeQuery(id+"F26.opPattern","COPY",BODY,{"derivedFrom":makeQuery(id+"F19.opPattern","COPY",BODY,{"derivedFrom":makeQuery(id+"F15.opPattern","COPY",BODY,{"derivedFrom":makeQuery(id+"F12.opPattern","COPY",BODY,{"derivedFrom":makeQuery(id+"F6.opPattern","COPY",BODY,{"derivedFrom":makeQuery(id+"F5.opPattern","COPY",BODY,{"derivedFrom":makeQuery(id+"F4.opPattern","COPY",BODY,{"derivedFrom":makeQuery(id+"F2.opPattern","COPY",BODY,{"derivedFrom":makeQuery(id+"F1.opExtrude","SWEPT_BODY",BODY,{"disambiguationData":[OSD([sQuery(id+"F0.wireOp",EDGE,"E0.bottom"),sQuery(id+"F0.wireOp",EDGE,"E0.top"),sQuery(id+"F0.wireOp",EDGE,"E0.left"),sQuery(id+"F0.wireOp",EDGE,"E0.right")])]}),"instanceName":"1"}),"instanceName":"1"}),"instanceName":"1"}),"instanceName":"1"}),"instanceName":"1"}),"instanceName":"1"}),"instanceName":"1"}),"instanceName":"1"}),"instanceName":"1"}),"instanceName":"1"});
            var Q350;
            Q350=makeQuery(id+"F48.opPattern","COPY",BODY,{"derivedFrom":makeQuery(id+"F45.opPattern","COPY",BODY,{"derivedFrom":makeQuery(id+"F40.opPattern","COPY",BODY,{"derivedFrom":makeQuery(id+"F23.opPattern","COPY",BODY,{"derivedFrom":makeQuery(id+"F19.opPattern","COPY",BODY,{"derivedFrom":makeQuery(id+"F17.opPattern","COPY",BODY,{"derivedFrom":makeQuery(id+"F15.opPattern","COPY",BODY,{"derivedFrom":makeQuery(id+"F12.opPattern","COPY",BODY,{"derivedFrom":makeQuery(id+"F6.opPattern","COPY",BODY,{"derivedFrom":makeQuery(id+"F5.opPattern","COPY",BODY,{"derivedFrom":makeQuery(id+"F4.opPattern","COPY",BODY,{"derivedFrom":makeQuery(id+"F2.opPattern","COPY",BODY,{"derivedFrom":makeQuery(id+"F1.opExtrude","SWEPT_BODY",BODY,{"disambiguationData":[OSD([sQuery(id+"F0.wireOp",EDGE,"E0.bottom"),sQuery(id+"F0.wireOp",EDGE,"E0.top"),sQuery(id+"F0.wireOp",EDGE,"E0.left"),sQuery(id+"F0.wireOp",EDGE,"E0.right")])]}),"instanceName":"1"}),"instanceName":"1"}),"instanceName":"1"}),"instanceName":"1"}),"instanceName":"1"}),"instanceName":"1"}),"instanceName":"1"}),"instanceName":"1"}),"instanceName":"1"}),"instanceName":"1"}),"instanceName":"1"}),"instanceName":"1"});
            var Q351;
            Q351=makeQuery(id+"F40.opPattern","COPY",BODY,{"derivedFrom":makeQuery(id+"F29.opPattern","COPY",BODY,{"derivedFrom":makeQuery(id+"F26.opPattern","COPY",BODY,{"derivedFrom":makeQuery(id+"F17.opPattern","COPY",BODY,{"derivedFrom":makeQuery(id+"F13.opPattern","COPY",BODY,{"derivedFrom":makeQuery(id+"F5.opPattern","COPY",BODY,{"derivedFrom":makeQuery(id+"F4.opPattern","COPY",BODY,{"derivedFrom":makeQuery(id+"F1.opExtrude","SWEPT_BODY",BODY,{"disambiguationData":[OSD([sQuery(id+"F0.wireOp",EDGE,"E0.bottom"),sQuery(id+"F0.wireOp",EDGE,"E0.top"),sQuery(id+"F0.wireOp",EDGE,"E0.left"),sQuery(id+"F0.wireOp",EDGE,"E0.right")])]}),"instanceName":"1"}),"instanceName":"1"}),"instanceName":"1"}),"instanceName":"1"}),"instanceName":"1"}),"instanceName":"1"}),"instanceName":"1"});
            var Q352;
            Q352=makeQuery(id+"F8.opPattern","COPY",BODY,{"derivedFrom":makeQuery(id+"F5.opPattern","COPY",BODY,{"derivedFrom":makeQuery(id+"F4.opPattern","COPY",BODY,{"derivedFrom":makeQuery(id+"F2.opPattern","COPY",BODY,{"derivedFrom":makeQuery(id+"F1.opExtrude","SWEPT_BODY",BODY,{"disambiguationData":[OSD([sQuery(id+"F0.wireOp",EDGE,"E0.bottom"),sQuery(id+"F0.wireOp",EDGE,"E0.top"),sQuery(id+"F0.wireOp",EDGE,"E0.left"),sQuery(id+"F0.wireOp",EDGE,"E0.right")])]}),"instanceName":"1"}),"instanceName":"1"}),"instanceName":"1"}),"instanceName":"1"});
            var Q353;
            Q353=makeQuery(id+"F22.opPattern","COPY",BODY,{"derivedFrom":makeQuery(id+"F21.opPattern","COPY",BODY,{"derivedFrom":makeQuery(id+"F19.opPattern","COPY",BODY,{"derivedFrom":makeQuery(id+"F17.opPattern","COPY",BODY,{"derivedFrom":makeQuery(id+"F6.opPattern","COPY",BODY,{"derivedFrom":makeQuery(id+"F5.opPattern","COPY",BODY,{"derivedFrom":makeQuery(id+"F4.opPattern","COPY",BODY,{"derivedFrom":makeQuery(id+"F1.opExtrude","SWEPT_BODY",BODY,{"disambiguationData":[OSD([sQuery(id+"F0.wireOp",EDGE,"E0.bottom"),sQuery(id+"F0.wireOp",EDGE,"E0.top"),sQuery(id+"F0.wireOp",EDGE,"E0.left"),sQuery(id+"F0.wireOp",EDGE,"E0.right")])]}),"instanceName":"1"}),"instanceName":"1"}),"instanceName":"1"}),"instanceName":"1"}),"instanceName":"1"}),"instanceName":"1"}),"instanceName":"1"});
            var Q354;
            Q354=makeQuery(id+"F40.opPattern","COPY",BODY,{"derivedFrom":makeQuery(id+"F23.opPattern","COPY",BODY,{"derivedFrom":makeQuery(id+"F21.opPattern","COPY",BODY,{"derivedFrom":makeQuery(id+"F19.opPattern","COPY",BODY,{"derivedFrom":makeQuery(id+"F6.opPattern","COPY",BODY,{"derivedFrom":makeQuery(id+"F5.opPattern","COPY",BODY,{"derivedFrom":makeQuery(id+"F4.opPattern","COPY",BODY,{"derivedFrom":makeQuery(id+"F2.opPattern","COPY",BODY,{"derivedFrom":makeQuery(id+"F1.opExtrude","SWEPT_BODY",BODY,{"disambiguationData":[OSD([sQuery(id+"F0.wireOp",EDGE,"E0.bottom"),sQuery(id+"F0.wireOp",EDGE,"E0.top"),sQuery(id+"F0.wireOp",EDGE,"E0.left"),sQuery(id+"F0.wireOp",EDGE,"E0.right")])]}),"instanceName":"1"}),"instanceName":"1"}),"instanceName":"1"}),"instanceName":"1"}),"instanceName":"1"}),"instanceName":"1"}),"instanceName":"1"}),"instanceName":"1"});
            var Q355;
            Q355=makeQuery(id+"F45.opPattern","COPY",BODY,{"derivedFrom":makeQuery(id+"F40.opPattern","COPY",BODY,{"derivedFrom":makeQuery(id+"F19.opPattern","COPY",BODY,{"derivedFrom":makeQuery(id+"F17.opPattern","COPY",BODY,{"derivedFrom":makeQuery(id+"F12.opPattern","COPY",BODY,{"derivedFrom":makeQuery(id+"F6.opPattern","COPY",BODY,{"derivedFrom":makeQuery(id+"F5.opPattern","COPY",BODY,{"derivedFrom":makeQuery(id+"F4.opPattern","COPY",BODY,{"derivedFrom":makeQuery(id+"F1.opExtrude","SWEPT_BODY",BODY,{"disambiguationData":[OSD([sQuery(id+"F0.wireOp",EDGE,"E0.bottom"),sQuery(id+"F0.wireOp",EDGE,"E0.top"),sQuery(id+"F0.wireOp",EDGE,"E0.left"),sQuery(id+"F0.wireOp",EDGE,"E0.right")])]}),"instanceName":"1"}),"instanceName":"1"}),"instanceName":"1"}),"instanceName":"1"}),"instanceName":"1"}),"instanceName":"1"}),"instanceName":"1"}),"instanceName":"1"});
            var Q356;
            Q356=makeQuery(id+"F21.opPattern","COPY",BODY,{"derivedFrom":makeQuery(id+"F19.opPattern","COPY",BODY,{"derivedFrom":makeQuery(id+"F17.opPattern","COPY",BODY,{"derivedFrom":makeQuery(id+"F12.opPattern","COPY",BODY,{"derivedFrom":makeQuery(id+"F6.opPattern","COPY",BODY,{"derivedFrom":makeQuery(id+"F5.opPattern","COPY",BODY,{"derivedFrom":makeQuery(id+"F4.opPattern","COPY",BODY,{"derivedFrom":makeQuery(id+"F1.opExtrude","SWEPT_BODY",BODY,{"disambiguationData":[OSD([sQuery(id+"F0.wireOp",EDGE,"E0.bottom"),sQuery(id+"F0.wireOp",EDGE,"E0.top"),sQuery(id+"F0.wireOp",EDGE,"E0.left"),sQuery(id+"F0.wireOp",EDGE,"E0.right")])]}),"instanceName":"1"}),"instanceName":"1"}),"instanceName":"1"}),"instanceName":"1"}),"instanceName":"1"}),"instanceName":"1"}),"instanceName":"1"});
            var Q357;
            Q357=makeQuery(id+"F40.opPattern","COPY",BODY,{"derivedFrom":makeQuery(id+"F17.opPattern","COPY",BODY,{"derivedFrom":makeQuery(id+"F13.opPattern","COPY",BODY,{"derivedFrom":makeQuery(id+"F5.opPattern","COPY",BODY,{"derivedFrom":makeQuery(id+"F4.opPattern","COPY",BODY,{"derivedFrom":makeQuery(id+"F1.opExtrude","SWEPT_BODY",BODY,{"disambiguationData":[OSD([sQuery(id+"F0.wireOp",EDGE,"E0.bottom"),sQuery(id+"F0.wireOp",EDGE,"E0.top"),sQuery(id+"F0.wireOp",EDGE,"E0.left"),sQuery(id+"F0.wireOp",EDGE,"E0.right")])]}),"instanceName":"1"}),"instanceName":"1"}),"instanceName":"1"}),"instanceName":"1"}),"instanceName":"1"});
            var Q358;
            Q358=makeQuery(id+"F28.opPattern","COPY",BODY,{"derivedFrom":makeQuery(id+"F26.opPattern","COPY",BODY,{"derivedFrom":makeQuery(id+"F17.opPattern","COPY",BODY,{"derivedFrom":makeQuery(id+"F15.opPattern","COPY",BODY,{"derivedFrom":makeQuery(id+"F12.opPattern","COPY",BODY,{"derivedFrom":makeQuery(id+"F6.opPattern","COPY",BODY,{"derivedFrom":makeQuery(id+"F5.opPattern","COPY",BODY,{"derivedFrom":makeQuery(id+"F4.opPattern","COPY",BODY,{"derivedFrom":makeQuery(id+"F2.opPattern","COPY",BODY,{"derivedFrom":makeQuery(id+"F1.opExtrude","SWEPT_BODY",BODY,{"disambiguationData":[OSD([sQuery(id+"F0.wireOp",EDGE,"E0.bottom"),sQuery(id+"F0.wireOp",EDGE,"E0.top"),sQuery(id+"F0.wireOp",EDGE,"E0.left"),sQuery(id+"F0.wireOp",EDGE,"E0.right")])]}),"instanceName":"1"}),"instanceName":"1"}),"instanceName":"1"}),"instanceName":"1"}),"instanceName":"1"}),"instanceName":"1"}),"instanceName":"1"}),"instanceName":"1"}),"instanceName":"1"});
            var Q359;
            Q359=makeQuery(id+"F11.opPattern","COPY",BODY,{"derivedFrom":makeQuery(id+"F6.opPattern","COPY",BODY,{"derivedFrom":makeQuery(id+"F4.opPattern","COPY",BODY,{"derivedFrom":makeQuery(id+"F2.opPattern","COPY",BODY,{"derivedFrom":makeQuery(id+"F1.opExtrude","SWEPT_BODY",BODY,{"disambiguationData":[OSD([sQuery(id+"F0.wireOp",EDGE,"E0.bottom"),sQuery(id+"F0.wireOp",EDGE,"E0.top"),sQuery(id+"F0.wireOp",EDGE,"E0.left"),sQuery(id+"F0.wireOp",EDGE,"E0.right")])]}),"instanceName":"1"}),"instanceName":"1"}),"instanceName":"1"}),"instanceName":"1"});
            var Q360;
            Q360=makeQuery(id+"F36.opPattern","COPY",BODY,{"derivedFrom":makeQuery(id+"F35.opPattern","COPY",BODY,{"derivedFrom":makeQuery(id+"F34.opPattern","COPY",BODY,{"derivedFrom":makeQuery(id+"F31.opPattern","COPY",BODY,{"derivedFrom":makeQuery(id+"F5.opPattern","COPY",BODY,{"derivedFrom":makeQuery(id+"F1.opExtrude","SWEPT_BODY",BODY,{"disambiguationData":[OSD([sQuery(id+"F0.wireOp",EDGE,"E0.bottom"),sQuery(id+"F0.wireOp",EDGE,"E0.top"),sQuery(id+"F0.wireOp",EDGE,"E0.left"),sQuery(id+"F0.wireOp",EDGE,"E0.right")])]}),"instanceName":"1"}),"instanceName":"1"}),"instanceName":"1"}),"instanceName":"1"}),"instanceName":"1"});
            var Q361;
            Q361=makeQuery(id+"F45.opPattern","COPY",BODY,{"derivedFrom":makeQuery(id+"F40.opPattern","COPY",BODY,{"derivedFrom":makeQuery(id+"F23.opPattern","COPY",BODY,{"derivedFrom":makeQuery(id+"F19.opPattern","COPY",BODY,{"derivedFrom":makeQuery(id+"F17.opPattern","COPY",BODY,{"derivedFrom":makeQuery(id+"F6.opPattern","COPY",BODY,{"derivedFrom":makeQuery(id+"F5.opPattern","COPY",BODY,{"derivedFrom":makeQuery(id+"F4.opPattern","COPY",BODY,{"derivedFrom":makeQuery(id+"F2.opPattern","COPY",BODY,{"derivedFrom":makeQuery(id+"F1.opExtrude","SWEPT_BODY",BODY,{"disambiguationData":[OSD([sQuery(id+"F0.wireOp",EDGE,"E0.bottom"),sQuery(id+"F0.wireOp",EDGE,"E0.top"),sQuery(id+"F0.wireOp",EDGE,"E0.left"),sQuery(id+"F0.wireOp",EDGE,"E0.right")])]}),"instanceName":"1"}),"instanceName":"1"}),"instanceName":"1"}),"instanceName":"1"}),"instanceName":"1"}),"instanceName":"1"}),"instanceName":"1"}),"instanceName":"1"}),"instanceName":"1"});
            var Q362;
            Q362=makeQuery(id+"F42.opPattern","COPY",BODY,{"derivedFrom":makeQuery(id+"F29.opPattern","COPY",BODY,{"derivedFrom":makeQuery(id+"F28.opPattern","COPY",BODY,{"derivedFrom":makeQuery(id+"F23.opPattern","COPY",BODY,{"derivedFrom":makeQuery(id+"F19.opPattern","COPY",BODY,{"derivedFrom":makeQuery(id+"F17.opPattern","COPY",BODY,{"derivedFrom":makeQuery(id+"F15.opPattern","COPY",BODY,{"derivedFrom":makeQuery(id+"F12.opPattern","COPY",BODY,{"derivedFrom":makeQuery(id+"F6.opPattern","COPY",BODY,{"derivedFrom":makeQuery(id+"F5.opPattern","COPY",BODY,{"derivedFrom":makeQuery(id+"F4.opPattern","COPY",BODY,{"derivedFrom":makeQuery(id+"F2.opPattern","COPY",BODY,{"derivedFrom":makeQuery(id+"F1.opExtrude","SWEPT_BODY",BODY,{"disambiguationData":[OSD([sQuery(id+"F0.wireOp",EDGE,"E0.bottom"),sQuery(id+"F0.wireOp",EDGE,"E0.top"),sQuery(id+"F0.wireOp",EDGE,"E0.left"),sQuery(id+"F0.wireOp",EDGE,"E0.right")])]}),"instanceName":"1"}),"instanceName":"1"}),"instanceName":"1"}),"instanceName":"1"}),"instanceName":"1"}),"instanceName":"1"}),"instanceName":"1"}),"instanceName":"1"}),"instanceName":"1"}),"instanceName":"1"}),"instanceName":"1"}),"instanceName":"1"});
            var Q363;
            Q363=makeQuery(id+"F26.opPattern","COPY",BODY,{"derivedFrom":makeQuery(id+"F17.opPattern","COPY",BODY,{"derivedFrom":makeQuery(id+"F6.opPattern","COPY",BODY,{"derivedFrom":makeQuery(id+"F5.opPattern","COPY",BODY,{"derivedFrom":makeQuery(id+"F4.opPattern","COPY",BODY,{"derivedFrom":makeQuery(id+"F2.opPattern","COPY",BODY,{"derivedFrom":makeQuery(id+"F1.opExtrude","SWEPT_BODY",BODY,{"disambiguationData":[OSD([sQuery(id+"F0.wireOp",EDGE,"E0.bottom"),sQuery(id+"F0.wireOp",EDGE,"E0.top"),sQuery(id+"F0.wireOp",EDGE,"E0.left"),sQuery(id+"F0.wireOp",EDGE,"E0.right")])]}),"instanceName":"1"}),"instanceName":"1"}),"instanceName":"1"}),"instanceName":"1"}),"instanceName":"1"}),"instanceName":"1"});
            var Q364;
            Q364=makeQuery(id+"F26.opPattern","COPY",BODY,{"derivedFrom":makeQuery(id+"F17.opPattern","COPY",BODY,{"derivedFrom":makeQuery(id+"F5.opPattern","COPY",BODY,{"derivedFrom":makeQuery(id+"F4.opPattern","COPY",BODY,{"derivedFrom":makeQuery(id+"F2.opPattern","COPY",BODY,{"derivedFrom":makeQuery(id+"F1.opExtrude","SWEPT_BODY",BODY,{"disambiguationData":[OSD([sQuery(id+"F0.wireOp",EDGE,"E0.bottom"),sQuery(id+"F0.wireOp",EDGE,"E0.top"),sQuery(id+"F0.wireOp",EDGE,"E0.left"),sQuery(id+"F0.wireOp",EDGE,"E0.right")])]}),"instanceName":"1"}),"instanceName":"1"}),"instanceName":"1"}),"instanceName":"1"}),"instanceName":"1"});
            var Q365;
            Q365=makeQuery(id+"F45.opPattern","COPY",BODY,{"derivedFrom":makeQuery(id+"F40.opPattern","COPY",BODY,{"derivedFrom":makeQuery(id+"F19.opPattern","COPY",BODY,{"derivedFrom":makeQuery(id+"F17.opPattern","COPY",BODY,{"derivedFrom":makeQuery(id+"F6.opPattern","COPY",BODY,{"derivedFrom":makeQuery(id+"F5.opPattern","COPY",BODY,{"derivedFrom":makeQuery(id+"F4.opPattern","COPY",BODY,{"derivedFrom":makeQuery(id+"F2.opPattern","COPY",BODY,{"derivedFrom":makeQuery(id+"F1.opExtrude","SWEPT_BODY",BODY,{"disambiguationData":[OSD([sQuery(id+"F0.wireOp",EDGE,"E0.bottom"),sQuery(id+"F0.wireOp",EDGE,"E0.top"),sQuery(id+"F0.wireOp",EDGE,"E0.left"),sQuery(id+"F0.wireOp",EDGE,"E0.right")])]}),"instanceName":"1"}),"instanceName":"1"}),"instanceName":"1"}),"instanceName":"1"}),"instanceName":"1"}),"instanceName":"1"}),"instanceName":"1"}),"instanceName":"1"});
            var Q366;
            Q366=makeQuery(id+"F42.opPattern","COPY",BODY,{"derivedFrom":makeQuery(id+"F28.opPattern","COPY",BODY,{"derivedFrom":makeQuery(id+"F23.opPattern","COPY",BODY,{"derivedFrom":makeQuery(id+"F19.opPattern","COPY",BODY,{"derivedFrom":makeQuery(id+"F17.opPattern","COPY",BODY,{"derivedFrom":makeQuery(id+"F13.opPattern","COPY",BODY,{"derivedFrom":makeQuery(id+"F5.opPattern","COPY",BODY,{"derivedFrom":makeQuery(id+"F4.opPattern","COPY",BODY,{"derivedFrom":makeQuery(id+"F1.opExtrude","SWEPT_BODY",BODY,{"disambiguationData":[OSD([sQuery(id+"F0.wireOp",EDGE,"E0.bottom"),sQuery(id+"F0.wireOp",EDGE,"E0.top"),sQuery(id+"F0.wireOp",EDGE,"E0.left"),sQuery(id+"F0.wireOp",EDGE,"E0.right")])]}),"instanceName":"1"}),"instanceName":"1"}),"instanceName":"1"}),"instanceName":"1"}),"instanceName":"1"}),"instanceName":"1"}),"instanceName":"1"}),"instanceName":"1"});
            var Q367;
            Q367=makeQuery(id+"F39.opPattern","COPY",BODY,{"derivedFrom":makeQuery(id+"F26.opPattern","COPY",BODY,{"derivedFrom":makeQuery(id+"F19.opPattern","COPY",BODY,{"derivedFrom":makeQuery(id+"F6.opPattern","COPY",BODY,{"derivedFrom":makeQuery(id+"F5.opPattern","COPY",BODY,{"derivedFrom":makeQuery(id+"F4.opPattern","COPY",BODY,{"derivedFrom":makeQuery(id+"F2.opPattern","COPY",BODY,{"derivedFrom":makeQuery(id+"F1.opExtrude","SWEPT_BODY",BODY,{"disambiguationData":[OSD([sQuery(id+"F0.wireOp",EDGE,"E0.bottom"),sQuery(id+"F0.wireOp",EDGE,"E0.top"),sQuery(id+"F0.wireOp",EDGE,"E0.left"),sQuery(id+"F0.wireOp",EDGE,"E0.right")])]}),"instanceName":"1"}),"instanceName":"1"}),"instanceName":"1"}),"instanceName":"1"}),"instanceName":"1"}),"instanceName":"1"}),"instanceName":"1"});
            var Q368;
            Q368=makeQuery(id+"F42.opPattern","COPY",BODY,{"derivedFrom":makeQuery(id+"F29.opPattern","COPY",BODY,{"derivedFrom":makeQuery(id+"F28.opPattern","COPY",BODY,{"derivedFrom":makeQuery(id+"F23.opPattern","COPY",BODY,{"derivedFrom":makeQuery(id+"F19.opPattern","COPY",BODY,{"derivedFrom":makeQuery(id+"F17.opPattern","COPY",BODY,{"derivedFrom":makeQuery(id+"F13.opPattern","COPY",BODY,{"derivedFrom":makeQuery(id+"F5.opPattern","COPY",BODY,{"derivedFrom":makeQuery(id+"F4.opPattern","COPY",BODY,{"derivedFrom":makeQuery(id+"F1.opExtrude","SWEPT_BODY",BODY,{"disambiguationData":[OSD([sQuery(id+"F0.wireOp",EDGE,"E0.bottom"),sQuery(id+"F0.wireOp",EDGE,"E0.top"),sQuery(id+"F0.wireOp",EDGE,"E0.left"),sQuery(id+"F0.wireOp",EDGE,"E0.right")])]}),"instanceName":"1"}),"instanceName":"1"}),"instanceName":"1"}),"instanceName":"1"}),"instanceName":"1"}),"instanceName":"1"}),"instanceName":"1"}),"instanceName":"1"}),"instanceName":"1"});
            var Q369;
            Q369=makeQuery(id+"F3.opPattern","COPY",BODY,{"derivedFrom":makeQuery(id+"F1.opExtrude","SWEPT_BODY",BODY,{"disambiguationData":[OSD([sQuery(id+"F0.wireOp",EDGE,"E0.bottom"),sQuery(id+"F0.wireOp",EDGE,"E0.top"),sQuery(id+"F0.wireOp",EDGE,"E0.left"),sQuery(id+"F0.wireOp",EDGE,"E0.right")])]}),"instanceName":"1"});
            var Q370;
            Q370=makeQuery(id+"F42.opPattern","COPY",BODY,{"derivedFrom":makeQuery(id+"F29.opPattern","COPY",BODY,{"derivedFrom":makeQuery(id+"F19.opPattern","COPY",BODY,{"derivedFrom":makeQuery(id+"F17.opPattern","COPY",BODY,{"derivedFrom":makeQuery(id+"F13.opPattern","COPY",BODY,{"derivedFrom":makeQuery(id+"F5.opPattern","COPY",BODY,{"derivedFrom":makeQuery(id+"F4.opPattern","COPY",BODY,{"derivedFrom":makeQuery(id+"F1.opExtrude","SWEPT_BODY",BODY,{"disambiguationData":[OSD([sQuery(id+"F0.wireOp",EDGE,"E0.bottom"),sQuery(id+"F0.wireOp",EDGE,"E0.top"),sQuery(id+"F0.wireOp",EDGE,"E0.left"),sQuery(id+"F0.wireOp",EDGE,"E0.right")])]}),"instanceName":"1"}),"instanceName":"1"}),"instanceName":"1"}),"instanceName":"1"}),"instanceName":"1"}),"instanceName":"1"}),"instanceName":"1"});
            var Q371;
            Q371=makeQuery(id+"F24.opPattern","COPY",BODY,{"derivedFrom":makeQuery(id+"F23.opPattern","COPY",BODY,{"derivedFrom":makeQuery(id+"F19.opPattern","COPY",BODY,{"derivedFrom":makeQuery(id+"F5.opPattern","COPY",BODY,{"derivedFrom":makeQuery(id+"F4.opPattern","COPY",BODY,{"derivedFrom":makeQuery(id+"F2.opPattern","COPY",BODY,{"derivedFrom":makeQuery(id+"F1.opExtrude","SWEPT_BODY",BODY,{"disambiguationData":[OSD([sQuery(id+"F0.wireOp",EDGE,"E0.bottom"),sQuery(id+"F0.wireOp",EDGE,"E0.top"),sQuery(id+"F0.wireOp",EDGE,"E0.left"),sQuery(id+"F0.wireOp",EDGE,"E0.right")])]}),"instanceName":"1"}),"instanceName":"1"}),"instanceName":"1"}),"instanceName":"1"}),"instanceName":"1"}),"instanceName":"1"});
            var Q372;
            Q372=makeQuery(id+"F7.opPattern","COPY",BODY,{"derivedFrom":makeQuery(id+"F5.opPattern","COPY",BODY,{"derivedFrom":makeQuery(id+"F2.opPattern","COPY",BODY,{"derivedFrom":makeQuery(id+"F1.opExtrude","SWEPT_BODY",BODY,{"disambiguationData":[OSD([sQuery(id+"F0.wireOp",EDGE,"E0.bottom"),sQuery(id+"F0.wireOp",EDGE,"E0.top"),sQuery(id+"F0.wireOp",EDGE,"E0.left"),sQuery(id+"F0.wireOp",EDGE,"E0.right")])]}),"instanceName":"1"}),"instanceName":"1"}),"instanceName":"1"});
            var Q373;
            Q373=makeQuery(id+"F40.opPattern","COPY",BODY,{"derivedFrom":makeQuery(id+"F26.opPattern","COPY",BODY,{"derivedFrom":makeQuery(id+"F19.opPattern","COPY",BODY,{"derivedFrom":makeQuery(id+"F5.opPattern","COPY",BODY,{"derivedFrom":makeQuery(id+"F4.opPattern","COPY",BODY,{"derivedFrom":makeQuery(id+"F1.opExtrude","SWEPT_BODY",BODY,{"disambiguationData":[OSD([sQuery(id+"F0.wireOp",EDGE,"E0.bottom"),sQuery(id+"F0.wireOp",EDGE,"E0.top"),sQuery(id+"F0.wireOp",EDGE,"E0.left"),sQuery(id+"F0.wireOp",EDGE,"E0.right")])]}),"instanceName":"1"}),"instanceName":"1"}),"instanceName":"1"}),"instanceName":"1"}),"instanceName":"1"});
            var Q374;
            Q374=makeQuery(id+"F31.opPattern","COPY",BODY,{"derivedFrom":makeQuery(id+"F4.opPattern","COPY",BODY,{"derivedFrom":makeQuery(id+"F1.opExtrude","SWEPT_BODY",BODY,{"disambiguationData":[OSD([sQuery(id+"F0.wireOp",EDGE,"E0.bottom"),sQuery(id+"F0.wireOp",EDGE,"E0.top"),sQuery(id+"F0.wireOp",EDGE,"E0.left"),sQuery(id+"F0.wireOp",EDGE,"E0.right")])]}),"instanceName":"1"}),"instanceName":"1"});
            var Q375;
            Q375=makeQuery(id+"F40.opPattern","COPY",BODY,{"derivedFrom":makeQuery(id+"F28.opPattern","COPY",BODY,{"derivedFrom":makeQuery(id+"F26.opPattern","COPY",BODY,{"derivedFrom":makeQuery(id+"F19.opPattern","COPY",BODY,{"derivedFrom":makeQuery(id+"F13.opPattern","COPY",BODY,{"derivedFrom":makeQuery(id+"F5.opPattern","COPY",BODY,{"derivedFrom":makeQuery(id+"F4.opPattern","COPY",BODY,{"derivedFrom":makeQuery(id+"F1.opExtrude","SWEPT_BODY",BODY,{"disambiguationData":[OSD([sQuery(id+"F0.wireOp",EDGE,"E0.bottom"),sQuery(id+"F0.wireOp",EDGE,"E0.top"),sQuery(id+"F0.wireOp",EDGE,"E0.left"),sQuery(id+"F0.wireOp",EDGE,"E0.right")])]}),"instanceName":"1"}),"instanceName":"1"}),"instanceName":"1"}),"instanceName":"1"}),"instanceName":"1"}),"instanceName":"1"}),"instanceName":"1"});
            var Q376;
            Q376=makeQuery(id+"F27.opPattern","COPY",BODY,{"derivedFrom":makeQuery(id+"F24.opPattern","COPY",BODY,{"derivedFrom":makeQuery(id+"F23.opPattern","COPY",BODY,{"derivedFrom":makeQuery(id+"F21.opPattern","COPY",BODY,{"derivedFrom":makeQuery(id+"F19.opPattern","COPY",BODY,{"derivedFrom":makeQuery(id+"F17.opPattern","COPY",BODY,{"derivedFrom":makeQuery(id+"F12.opPattern","COPY",BODY,{"derivedFrom":makeQuery(id+"F6.opPattern","COPY",BODY,{"derivedFrom":makeQuery(id+"F5.opPattern","COPY",BODY,{"derivedFrom":makeQuery(id+"F4.opPattern","COPY",BODY,{"derivedFrom":makeQuery(id+"F2.opPattern","COPY",BODY,{"derivedFrom":makeQuery(id+"F1.opExtrude","SWEPT_BODY",BODY,{"disambiguationData":[OSD([sQuery(id+"F0.wireOp",EDGE,"E0.bottom"),sQuery(id+"F0.wireOp",EDGE,"E0.top"),sQuery(id+"F0.wireOp",EDGE,"E0.left"),sQuery(id+"F0.wireOp",EDGE,"E0.right")])]}),"instanceName":"1"}),"instanceName":"1"}),"instanceName":"1"}),"instanceName":"1"}),"instanceName":"1"}),"instanceName":"1"}),"instanceName":"1"}),"instanceName":"1"}),"instanceName":"1"}),"instanceName":"1"}),"instanceName":"1"});
            var Q377;
            Q377=makeQuery(id+"F42.opPattern","COPY",BODY,{"derivedFrom":makeQuery(id+"F28.opPattern","COPY",BODY,{"derivedFrom":makeQuery(id+"F19.opPattern","COPY",BODY,{"derivedFrom":makeQuery(id+"F17.opPattern","COPY",BODY,{"derivedFrom":makeQuery(id+"F15.opPattern","COPY",BODY,{"derivedFrom":makeQuery(id+"F12.opPattern","COPY",BODY,{"derivedFrom":makeQuery(id+"F6.opPattern","COPY",BODY,{"derivedFrom":makeQuery(id+"F5.opPattern","COPY",BODY,{"derivedFrom":makeQuery(id+"F4.opPattern","COPY",BODY,{"derivedFrom":makeQuery(id+"F2.opPattern","COPY",BODY,{"derivedFrom":makeQuery(id+"F1.opExtrude","SWEPT_BODY",BODY,{"disambiguationData":[OSD([sQuery(id+"F0.wireOp",EDGE,"E0.bottom"),sQuery(id+"F0.wireOp",EDGE,"E0.top"),sQuery(id+"F0.wireOp",EDGE,"E0.left"),sQuery(id+"F0.wireOp",EDGE,"E0.right")])]}),"instanceName":"1"}),"instanceName":"1"}),"instanceName":"1"}),"instanceName":"1"}),"instanceName":"1"}),"instanceName":"1"}),"instanceName":"1"}),"instanceName":"1"}),"instanceName":"1"}),"instanceName":"1"});
            var Q378;
            Q378=makeQuery(id+"F39.opPattern","COPY",BODY,{"derivedFrom":makeQuery(id+"F28.opPattern","COPY",BODY,{"derivedFrom":makeQuery(id+"F26.opPattern","COPY",BODY,{"derivedFrom":makeQuery(id+"F17.opPattern","COPY",BODY,{"derivedFrom":makeQuery(id+"F15.opPattern","COPY",BODY,{"derivedFrom":makeQuery(id+"F12.opPattern","COPY",BODY,{"derivedFrom":makeQuery(id+"F6.opPattern","COPY",BODY,{"derivedFrom":makeQuery(id+"F5.opPattern","COPY",BODY,{"derivedFrom":makeQuery(id+"F4.opPattern","COPY",BODY,{"derivedFrom":makeQuery(id+"F2.opPattern","COPY",BODY,{"derivedFrom":makeQuery(id+"F1.opExtrude","SWEPT_BODY",BODY,{"disambiguationData":[OSD([sQuery(id+"F0.wireOp",EDGE,"E0.bottom"),sQuery(id+"F0.wireOp",EDGE,"E0.top"),sQuery(id+"F0.wireOp",EDGE,"E0.left"),sQuery(id+"F0.wireOp",EDGE,"E0.right")])]}),"instanceName":"1"}),"instanceName":"1"}),"instanceName":"1"}),"instanceName":"1"}),"instanceName":"1"}),"instanceName":"1"}),"instanceName":"1"}),"instanceName":"1"}),"instanceName":"1"}),"instanceName":"1"});
            var Q379;
            Q379=makeQuery(id+"F29.opPattern","COPY",BODY,{"derivedFrom":makeQuery(id+"F26.opPattern","COPY",BODY,{"derivedFrom":makeQuery(id+"F17.opPattern","COPY",BODY,{"derivedFrom":makeQuery(id+"F13.opPattern","COPY",BODY,{"derivedFrom":makeQuery(id+"F5.opPattern","COPY",BODY,{"derivedFrom":makeQuery(id+"F4.opPattern","COPY",BODY,{"derivedFrom":makeQuery(id+"F1.opExtrude","SWEPT_BODY",BODY,{"disambiguationData":[OSD([sQuery(id+"F0.wireOp",EDGE,"E0.bottom"),sQuery(id+"F0.wireOp",EDGE,"E0.top"),sQuery(id+"F0.wireOp",EDGE,"E0.left"),sQuery(id+"F0.wireOp",EDGE,"E0.right")])]}),"instanceName":"1"}),"instanceName":"1"}),"instanceName":"1"}),"instanceName":"1"}),"instanceName":"1"}),"instanceName":"1"});
            var Q380;
            Q380=makeQuery(id+"F35.opPattern","COPY",BODY,{"derivedFrom":makeQuery(id+"F31.opPattern","COPY",BODY,{"derivedFrom":makeQuery(id+"F2.opPattern","COPY",BODY,{"derivedFrom":makeQuery(id+"F1.opExtrude","SWEPT_BODY",BODY,{"disambiguationData":[OSD([sQuery(id+"F0.wireOp",EDGE,"E0.bottom"),sQuery(id+"F0.wireOp",EDGE,"E0.top"),sQuery(id+"F0.wireOp",EDGE,"E0.left"),sQuery(id+"F0.wireOp",EDGE,"E0.right")])]}),"instanceName":"1"}),"instanceName":"1"}),"instanceName":"1"});
            var Q381;
            Q381=makeQuery(id+"F29.opPattern","COPY",BODY,{"derivedFrom":makeQuery(id+"F19.opPattern","COPY",BODY,{"derivedFrom":makeQuery(id+"F15.opPattern","COPY",BODY,{"derivedFrom":makeQuery(id+"F12.opPattern","COPY",BODY,{"derivedFrom":makeQuery(id+"F6.opPattern","COPY",BODY,{"derivedFrom":makeQuery(id+"F5.opPattern","COPY",BODY,{"derivedFrom":makeQuery(id+"F4.opPattern","COPY",BODY,{"derivedFrom":makeQuery(id+"F2.opPattern","COPY",BODY,{"derivedFrom":makeQuery(id+"F1.opExtrude","SWEPT_BODY",BODY,{"disambiguationData":[OSD([sQuery(id+"F0.wireOp",EDGE,"E0.bottom"),sQuery(id+"F0.wireOp",EDGE,"E0.top"),sQuery(id+"F0.wireOp",EDGE,"E0.left"),sQuery(id+"F0.wireOp",EDGE,"E0.right")])]}),"instanceName":"1"}),"instanceName":"1"}),"instanceName":"1"}),"instanceName":"1"}),"instanceName":"1"}),"instanceName":"1"}),"instanceName":"1"}),"instanceName":"1"});
            var Q382;
            Q382=makeQuery(id+"F35.opPattern","COPY",BODY,{"derivedFrom":makeQuery(id+"F31.opPattern","COPY",BODY,{"derivedFrom":makeQuery(id+"F5.opPattern","COPY",BODY,{"derivedFrom":makeQuery(id+"F2.opPattern","COPY",BODY,{"derivedFrom":makeQuery(id+"F1.opExtrude","SWEPT_BODY",BODY,{"disambiguationData":[OSD([sQuery(id+"F0.wireOp",EDGE,"E0.bottom"),sQuery(id+"F0.wireOp",EDGE,"E0.top"),sQuery(id+"F0.wireOp",EDGE,"E0.left"),sQuery(id+"F0.wireOp",EDGE,"E0.right")])]}),"instanceName":"1"}),"instanceName":"1"}),"instanceName":"1"}),"instanceName":"1"});
            var Q383;
            Q383=makeQuery(id+"F42.opPattern","COPY",BODY,{"derivedFrom":makeQuery(id+"F29.opPattern","COPY",BODY,{"derivedFrom":makeQuery(id+"F23.opPattern","COPY",BODY,{"derivedFrom":makeQuery(id+"F19.opPattern","COPY",BODY,{"derivedFrom":makeQuery(id+"F17.opPattern","COPY",BODY,{"derivedFrom":makeQuery(id+"F15.opPattern","COPY",BODY,{"derivedFrom":makeQuery(id+"F12.opPattern","COPY",BODY,{"derivedFrom":makeQuery(id+"F6.opPattern","COPY",BODY,{"derivedFrom":makeQuery(id+"F5.opPattern","COPY",BODY,{"derivedFrom":makeQuery(id+"F4.opPattern","COPY",BODY,{"derivedFrom":makeQuery(id+"F2.opPattern","COPY",BODY,{"derivedFrom":makeQuery(id+"F1.opExtrude","SWEPT_BODY",BODY,{"disambiguationData":[OSD([sQuery(id+"F0.wireOp",EDGE,"E0.bottom"),sQuery(id+"F0.wireOp",EDGE,"E0.top"),sQuery(id+"F0.wireOp",EDGE,"E0.left"),sQuery(id+"F0.wireOp",EDGE,"E0.right")])]}),"instanceName":"1"}),"instanceName":"1"}),"instanceName":"1"}),"instanceName":"1"}),"instanceName":"1"}),"instanceName":"1"}),"instanceName":"1"}),"instanceName":"1"}),"instanceName":"1"}),"instanceName":"1"}),"instanceName":"1"});
            var Q384;
            Q384=makeQuery(id+"F45.opPattern","COPY",BODY,{"derivedFrom":makeQuery(id+"F40.opPattern","COPY",BODY,{"derivedFrom":makeQuery(id+"F19.opPattern","COPY",BODY,{"derivedFrom":makeQuery(id+"F17.opPattern","COPY",BODY,{"derivedFrom":makeQuery(id+"F5.opPattern","COPY",BODY,{"derivedFrom":makeQuery(id+"F4.opPattern","COPY",BODY,{"derivedFrom":makeQuery(id+"F2.opPattern","COPY",BODY,{"derivedFrom":makeQuery(id+"F1.opExtrude","SWEPT_BODY",BODY,{"disambiguationData":[OSD([sQuery(id+"F0.wireOp",EDGE,"E0.bottom"),sQuery(id+"F0.wireOp",EDGE,"E0.top"),sQuery(id+"F0.wireOp",EDGE,"E0.left"),sQuery(id+"F0.wireOp",EDGE,"E0.right")])]}),"instanceName":"1"}),"instanceName":"1"}),"instanceName":"1"}),"instanceName":"1"}),"instanceName":"1"}),"instanceName":"1"}),"instanceName":"1"});
            var Q385;
            Q385=makeQuery(id+"F40.opPattern","COPY",BODY,{"derivedFrom":makeQuery(id+"F19.opPattern","COPY",BODY,{"derivedFrom":makeQuery(id+"F6.opPattern","COPY",BODY,{"derivedFrom":makeQuery(id+"F5.opPattern","COPY",BODY,{"derivedFrom":makeQuery(id+"F4.opPattern","COPY",BODY,{"derivedFrom":makeQuery(id+"F1.opExtrude","SWEPT_BODY",BODY,{"disambiguationData":[OSD([sQuery(id+"F0.wireOp",EDGE,"E0.bottom"),sQuery(id+"F0.wireOp",EDGE,"E0.top"),sQuery(id+"F0.wireOp",EDGE,"E0.left"),sQuery(id+"F0.wireOp",EDGE,"E0.right")])]}),"instanceName":"1"}),"instanceName":"1"}),"instanceName":"1"}),"instanceName":"1"}),"instanceName":"1"});
            var Q386;
            Q386=makeQuery(id+"F25.opPattern","COPY",BODY,{"derivedFrom":makeQuery(id+"F24.opPattern","COPY",BODY,{"derivedFrom":makeQuery(id+"F23.opPattern","COPY",BODY,{"derivedFrom":makeQuery(id+"F21.opPattern","COPY",BODY,{"derivedFrom":makeQuery(id+"F19.opPattern","COPY",BODY,{"derivedFrom":makeQuery(id+"F17.opPattern","COPY",BODY,{"derivedFrom":makeQuery(id+"F5.opPattern","COPY",BODY,{"derivedFrom":makeQuery(id+"F4.opPattern","COPY",BODY,{"derivedFrom":makeQuery(id+"F2.opPattern","COPY",BODY,{"derivedFrom":makeQuery(id+"F1.opExtrude","SWEPT_BODY",BODY,{"disambiguationData":[OSD([sQuery(id+"F0.wireOp",EDGE,"E0.bottom"),sQuery(id+"F0.wireOp",EDGE,"E0.top"),sQuery(id+"F0.wireOp",EDGE,"E0.left"),sQuery(id+"F0.wireOp",EDGE,"E0.right")])]}),"instanceName":"1"}),"instanceName":"1"}),"instanceName":"1"}),"instanceName":"1"}),"instanceName":"1"}),"instanceName":"1"}),"instanceName":"1"}),"instanceName":"1"}),"instanceName":"1"});
            var Q387;
            Q387=qCreatedBy(makeId("Origin.pointOp"),VERTEX);
            transform(context, id + "F50", {"entities" : qUnion([Q0, Q1, Q2, Q3, Q4, Q5, Q6, Q7, Q8, Q9, Q10, Q11, Q12, Q13, Q14, Q15, Q16, Q17, Q18, Q19, Q20, Q21, Q22, Q23, Q24, Q25, Q26, Q27, Q28, Q29, Q30, Q31, Q32, Q33, Q34, Q35, Q36, Q37, Q38, Q39, Q40, Q41, Q42, Q43, Q44, Q45, Q46, Q47, Q48, Q49, Q50, Q51, Q52, Q53, Q54, Q55, Q56, Q57, Q58, Q59, Q60, Q61, Q62, Q63, Q64, Q65, Q66, Q67, Q68, Q69, Q70, Q71, Q72, Q73, Q74, Q75, Q76, Q77, Q78, Q79, Q80, Q81, Q82, Q83, Q84, Q85, Q86, Q87, Q88, Q89, Q90, Q91, Q92, Q93, Q94, Q95, Q96, Q97, Q98, Q99, Q100, Q101, Q102, Q103, Q104, Q105, Q106, Q107, Q108, Q109, Q110, Q111, Q112, Q113, Q114, Q115, Q116, Q117, Q118, Q119, Q120, Q121, Q122, Q123, Q124, Q125, Q126, Q127, Q128, Q129, Q130, Q131, Q132, Q133, Q134, Q135, Q136, Q137, Q138, Q139, Q140, Q141, Q142, Q143, Q144, Q145, Q146, Q147, Q148, Q149, Q150, Q151, Q152, Q153, Q154, Q155, Q156, Q157, Q158, Q159, Q160, Q161, Q162, Q163, Q164, Q165, Q166, Q167, Q168, Q169, Q170, Q171, Q172, Q173, Q174, Q175, Q176, Q177, Q178, Q179, Q180, Q181, Q182, Q183, Q184, Q185, Q186, Q187, Q188, Q189, Q190, Q191, Q192, Q193, Q194, Q195, Q196, Q197, Q198, Q199, Q200, Q201, Q202, Q203, Q204, Q205, Q206, Q207, Q208, Q209, Q210, Q211, Q212, Q213, Q214, Q215, Q216, Q217, Q218, Q219, Q220, Q221, Q222, Q223, Q224, Q225, Q226, Q227, Q228, Q229, Q230, Q231, Q232, Q233, Q234, Q235, Q236, Q237, Q238, Q239, Q240, Q241, Q242, Q243, Q244, Q245, Q246, Q247, Q248, Q249, Q250, Q251, Q252, Q253, Q254, Q255, Q256, Q257, Q258, Q259, Q260, Q261, Q262, Q263, Q264, Q265, Q266, Q267, Q268, Q269, Q270, Q271, Q272, Q273, Q274, Q275, Q276, Q277, Q278, Q279, Q280, Q281, Q282, Q283, Q284, Q285, Q286, Q287, Q288, Q289, Q290, Q291, Q292, Q293, Q294, Q295, Q296, Q297, Q298, Q299, Q300, Q301, Q302, Q303, Q304, Q305, Q306, Q307, Q308, Q309, Q310, Q311, Q312, Q313, Q314, Q315, Q316, Q317, Q318, Q319, Q320, Q321, Q322, Q323, Q324, Q325, Q326, Q327, Q328, Q329, Q330, Q331, Q332, Q333, Q334, Q335, Q336, Q337, Q338, Q339, Q340, Q341, Q342, Q343, Q344, Q345, Q346, Q347, Q348, Q349, Q350, Q351, Q352, Q353, Q354, Q355, Q356, Q357, Q358, Q359, Q360, Q361, Q362, Q363, Q364, Q365, Q366, Q367, Q368, Q369, Q370, Q371, Q372, Q373, Q374, Q375, Q376, Q377, Q378, Q379, Q380, Q381, Q382, Q383, Q384, Q385, Q386]), "transformType" : TransformType.SCALE_UNIFORMLY, "scale" : 10, "scalePoint" : qUnion([Q387]), "makeCopy" : false});
        }
        {
            var Q0;
            Q0=makeQuery(id+"F30.opPattern","COPY",BODY,{"derivedFrom":makeQuery(id+"F29.opPattern","COPY",BODY,{"derivedFrom":makeQuery(id+"F23.opPattern","COPY",BODY,{"derivedFrom":makeQuery(id+"F19.opPattern","COPY",BODY,{"derivedFrom":makeQuery(id+"F17.opPattern","COPY",BODY,{"derivedFrom":makeQuery(id+"F13.opPattern","COPY",BODY,{"derivedFrom":makeQuery(id+"F5.opPattern","COPY",BODY,{"derivedFrom":makeQuery(id+"F4.opPattern","COPY",BODY,{"derivedFrom":makeQuery(id+"F1.opExtrude","SWEPT_BODY",BODY,{"disambiguationData":[OSD([sQuery(id+"F0.wireOp",EDGE,"E0.bottom"),sQuery(id+"F0.wireOp",EDGE,"E0.top"),sQuery(id+"F0.wireOp",EDGE,"E0.left"),sQuery(id+"F0.wireOp",EDGE,"E0.right")])]}),"instanceName":"1"}),"instanceName":"1"}),"instanceName":"1"}),"instanceName":"1"}),"instanceName":"1"}),"instanceName":"1"}),"instanceName":"1"}),"instanceName":"1"});
            var Q1;
            Q1=makeQuery(id+"F30.opPattern","COPY",EDGE,{"derivedFrom":makeQuery(id+"F29.opPattern","COPY",EDGE,{"derivedFrom":makeQuery(id+"F23.opPattern","COPY",EDGE,{"derivedFrom":makeQuery(id+"F19.opPattern","COPY",EDGE,{"derivedFrom":makeQuery(id+"F17.opPattern","COPY",EDGE,{"derivedFrom":makeQuery(id+"F13.opPattern","COPY",EDGE,{"derivedFrom":makeQuery(id+"F5.opPattern","COPY",EDGE,{"derivedFrom":makeQuery(id+"F4.opPattern","COPY",EDGE,{"derivedFrom":makeQuery(id+"F1.opExtrude","SWEPT_EDGE",EDGE,{"disambiguationData":[OSD([sQuery(id+"F0.wireOp",EDGE,"E0.bottom"),sQuery(id+"F0.wireOp",EDGE,"E0.right")])]}),"instanceName":"1"}),"instanceName":"1"}),"instanceName":"1"}),"instanceName":"1"}),"instanceName":"1"}),"instanceName":"1"}),"instanceName":"1"}),"instanceName":"1"});
            transform(context, id + "F51", {"entities" : qUnion([Q0]), "transformType" : TransformType.TRANSLATION_DISTANCE, "transformDirection" : qUnion([Q1]), "distance" : 100 * mm, "makeCopy" : true});
        }
        {
            var Q0;
            Q0=makeQuery(id+"F51.opPattern","COPY",BODY,{"derivedFrom":makeQuery(id+"F30.opPattern","COPY",BODY,{"derivedFrom":makeQuery(id+"F29.opPattern","COPY",BODY,{"derivedFrom":makeQuery(id+"F23.opPattern","COPY",BODY,{"derivedFrom":makeQuery(id+"F19.opPattern","COPY",BODY,{"derivedFrom":makeQuery(id+"F17.opPattern","COPY",BODY,{"derivedFrom":makeQuery(id+"F13.opPattern","COPY",BODY,{"derivedFrom":makeQuery(id+"F5.opPattern","COPY",BODY,{"derivedFrom":makeQuery(id+"F4.opPattern","COPY",BODY,{"derivedFrom":makeQuery(id+"F1.opExtrude","SWEPT_BODY",BODY,{"disambiguationData":[OSD([sQuery(id+"F0.wireOp",EDGE,"E0.bottom"),sQuery(id+"F0.wireOp",EDGE,"E0.top"),sQuery(id+"F0.wireOp",EDGE,"E0.left"),sQuery(id+"F0.wireOp",EDGE,"E0.right")])]}),"instanceName":"1"}),"instanceName":"1"}),"instanceName":"1"}),"instanceName":"1"}),"instanceName":"1"}),"instanceName":"1"}),"instanceName":"1"}),"instanceName":"1"}),"instanceName":"1"});
            var Q1;
            Q1=makeQuery(id+"F51.opPattern","COPY",EDGE,{"derivedFrom":makeQuery(id+"F30.opPattern","COPY",EDGE,{"derivedFrom":makeQuery(id+"F29.opPattern","COPY",EDGE,{"derivedFrom":makeQuery(id+"F23.opPattern","COPY",EDGE,{"derivedFrom":makeQuery(id+"F19.opPattern","COPY",EDGE,{"derivedFrom":makeQuery(id+"F17.opPattern","COPY",EDGE,{"derivedFrom":makeQuery(id+"F13.opPattern","COPY",EDGE,{"derivedFrom":makeQuery(id+"F5.opPattern","COPY",EDGE,{"derivedFrom":makeQuery(id+"F4.opPattern","COPY",EDGE,{"derivedFrom":makeQuery(id+"F1.opExtrude","SWEPT_EDGE",EDGE,{"disambiguationData":[OSD([sQuery(id+"F0.wireOp",EDGE,"E0.bottom"),sQuery(id+"F0.wireOp",EDGE,"E0.right")])]}),"instanceName":"1"}),"instanceName":"1"}),"instanceName":"1"}),"instanceName":"1"}),"instanceName":"1"}),"instanceName":"1"}),"instanceName":"1"}),"instanceName":"1"}),"instanceName":"1"});
            transform(context, id + "F52", {"entities" : qUnion([Q0]), "transformType" : TransformType.TRANSLATION_DISTANCE, "transformDirection" : qUnion([Q1]), "distance" : 100 * mm, "makeCopy" : true});
        }
        {
            var Q0;
            Q0=makeQuery(id+"F44.opPattern","COPY",BODY,{"derivedFrom":makeQuery(id+"F42.opPattern","COPY",BODY,{"derivedFrom":makeQuery(id+"F29.opPattern","COPY",BODY,{"derivedFrom":makeQuery(id+"F28.opPattern","COPY",BODY,{"derivedFrom":makeQuery(id+"F23.opPattern","COPY",BODY,{"derivedFrom":makeQuery(id+"F19.opPattern","COPY",BODY,{"derivedFrom":makeQuery(id+"F17.opPattern","COPY",BODY,{"derivedFrom":makeQuery(id+"F13.opPattern","COPY",BODY,{"derivedFrom":makeQuery(id+"F5.opPattern","COPY",BODY,{"derivedFrom":makeQuery(id+"F4.opPattern","COPY",BODY,{"derivedFrom":makeQuery(id+"F1.opExtrude","SWEPT_BODY",BODY,{"disambiguationData":[OSD([sQuery(id+"F0.wireOp",EDGE,"E0.bottom"),sQuery(id+"F0.wireOp",EDGE,"E0.top"),sQuery(id+"F0.wireOp",EDGE,"E0.left"),sQuery(id+"F0.wireOp",EDGE,"E0.right")])]}),"instanceName":"1"}),"instanceName":"1"}),"instanceName":"1"}),"instanceName":"1"}),"instanceName":"1"}),"instanceName":"1"}),"instanceName":"1"}),"instanceName":"1"}),"instanceName":"1"}),"instanceName":"1"});
            var Q1;
            Q1=makeQuery(id+"F44.opPattern","COPY",BODY,{"derivedFrom":makeQuery(id+"F42.opPattern","COPY",BODY,{"derivedFrom":makeQuery(id+"F29.opPattern","COPY",BODY,{"derivedFrom":makeQuery(id+"F28.opPattern","COPY",BODY,{"derivedFrom":makeQuery(id+"F23.opPattern","COPY",BODY,{"derivedFrom":makeQuery(id+"F19.opPattern","COPY",BODY,{"derivedFrom":makeQuery(id+"F15.opPattern","COPY",BODY,{"derivedFrom":makeQuery(id+"F12.opPattern","COPY",BODY,{"derivedFrom":makeQuery(id+"F6.opPattern","COPY",BODY,{"derivedFrom":makeQuery(id+"F5.opPattern","COPY",BODY,{"derivedFrom":makeQuery(id+"F4.opPattern","COPY",BODY,{"derivedFrom":makeQuery(id+"F2.opPattern","COPY",BODY,{"derivedFrom":makeQuery(id+"F1.opExtrude","SWEPT_BODY",BODY,{"disambiguationData":[OSD([sQuery(id+"F0.wireOp",EDGE,"E0.bottom"),sQuery(id+"F0.wireOp",EDGE,"E0.top"),sQuery(id+"F0.wireOp",EDGE,"E0.left"),sQuery(id+"F0.wireOp",EDGE,"E0.right")])]}),"instanceName":"1"}),"instanceName":"1"}),"instanceName":"1"}),"instanceName":"1"}),"instanceName":"1"}),"instanceName":"1"}),"instanceName":"1"}),"instanceName":"1"}),"instanceName":"1"}),"instanceName":"1"}),"instanceName":"1"}),"instanceName":"1"});
            var Q2;
            Q2=makeQuery(id+"F44.opPattern","COPY",EDGE,{"derivedFrom":makeQuery(id+"F42.opPattern","COPY",EDGE,{"derivedFrom":makeQuery(id+"F29.opPattern","COPY",EDGE,{"derivedFrom":makeQuery(id+"F28.opPattern","COPY",EDGE,{"derivedFrom":makeQuery(id+"F23.opPattern","COPY",EDGE,{"derivedFrom":makeQuery(id+"F19.opPattern","COPY",EDGE,{"derivedFrom":makeQuery(id+"F17.opPattern","COPY",EDGE,{"derivedFrom":makeQuery(id+"F15.opPattern","COPY",EDGE,{"derivedFrom":makeQuery(id+"F12.opPattern","COPY",EDGE,{"derivedFrom":makeQuery(id+"F6.opPattern","COPY",EDGE,{"derivedFrom":makeQuery(id+"F5.opPattern","COPY",EDGE,{"derivedFrom":makeQuery(id+"F4.opPattern","COPY",EDGE,{"derivedFrom":makeQuery(id+"F2.opPattern","COPY",EDGE,{"derivedFrom":makeQuery(id+"F1.opExtrude","SWEPT_EDGE",EDGE,{"disambiguationData":[OSD([sQuery(id+"F0.wireOp",EDGE,"E0.bottom"),sQuery(id+"F0.wireOp",EDGE,"E0.right")])]}),"instanceName":"1"}),"instanceName":"1"}),"instanceName":"1"}),"instanceName":"1"}),"instanceName":"1"}),"instanceName":"1"}),"instanceName":"1"}),"instanceName":"1"}),"instanceName":"1"}),"instanceName":"1"}),"instanceName":"1"}),"instanceName":"1"}),"instanceName":"1"});
            transform(context, id + "F53", {"entities" : qUnion([Q0, Q1]), "transformType" : TransformType.TRANSLATION_DISTANCE, "transformDirection" : qUnion([Q2]), "distance" : 100 * mm, "makeCopy" : true});
        }
    });
